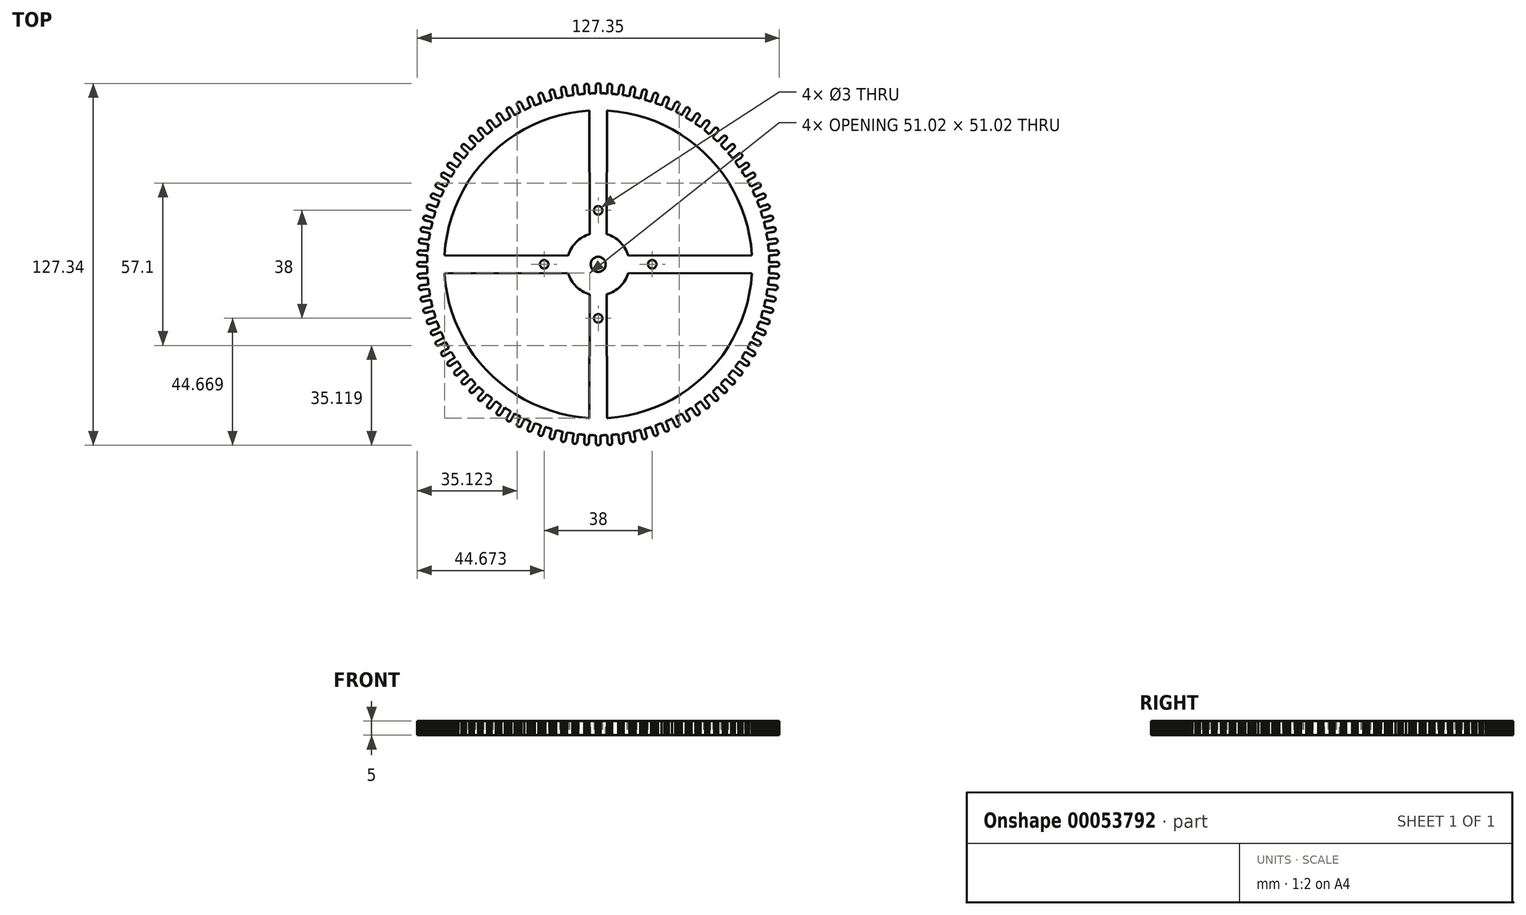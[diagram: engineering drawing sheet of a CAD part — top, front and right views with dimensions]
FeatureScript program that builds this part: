
annotation { "Feature Type Name" : "Feature", "Feature Type Description" : "" }
export const myFeature = defineFeature(function(context is Context, id is Id, definition is map)
    precondition{}
    {
        {
            var Q0;
            Q0=qCreatedBy(makeId("Top.planeOp"),FACE);
            var sketch = newSketch(context, id + "F0", { "sketchPlane" : qUnion([Q0])});
            skLineSegment(sketch, "E0", {"start": v(59.2, -0.78) * mm, "end": v(59.38, -0.79) * mm});
            skLineSegment(sketch, "E1", {"start": v(59.38, -0.79) * mm, "end": v(59.58, -0.79) * mm});
            skLineSegment(sketch, "E2", {"start": v(59.58, -0.79) * mm, "end": v(59.79, -0.8) * mm});
            skLineSegment(sketch, "E3", {"start": v(59.79, -0.8) * mm, "end": v(60, -0.8) * mm});
            skLineSegment(sketch, "E4", {"start": v(60, -0.8) * mm, "end": v(60.2, -0.8) * mm});
            skLineSegment(sketch, "E5", {"start": v(60.2, -0.8) * mm, "end": v(60.41, -0.8) * mm});
            skLineSegment(sketch, "E6", {"start": v(60.41, -0.8) * mm, "end": v(60.62, -0.8) * mm});
            skLineSegment(sketch, "E7", {"start": v(60.62, -0.8) * mm, "end": v(60.83, -0.8) * mm});
            skLineSegment(sketch, "E8", {"start": v(60.83, -0.8) * mm, "end": v(61.04, -0.8) * mm});
            skLineSegment(sketch, "E9", {"start": v(61.04, -0.8) * mm, "end": v(61.25, -0.81) * mm});
            skLineSegment(sketch, "E10", {"start": v(61.25, -0.81) * mm, "end": v(61.45, -0.81) * mm});
            skLineSegment(sketch, "E11", {"start": v(61.45, -0.81) * mm, "end": v(61.66, -0.82) * mm});
            skLineSegment(sketch, "E12", {"start": v(61.66, -0.82) * mm, "end": v(61.87, -0.82) * mm});
            skLineSegment(sketch, "E13", {"start": v(61.87, -0.82) * mm, "end": v(62.08, -0.8) * mm});
            skLineSegment(sketch, "E14", {"start": v(62.08, -0.8) * mm, "end": v(62.28, -0.71) * mm});
            skLineSegment(sketch, "E15", {"start": v(62.28, -0.71) * mm, "end": v(62.45, -0.58) * mm});
            skLineSegment(sketch, "E16", {"start": v(62.45, -0.58) * mm, "end": v(62.58, -0.41) * mm});
            skLineSegment(sketch, "E17", {"start": v(62.58, -0.41) * mm, "end": v(62.67, -0.21) * mm});
            skLineSegment(sketch, "E18", {"start": v(62.67, -0.21) * mm, "end": v(62.7, 0) * mm});
            skLineSegment(sketch, "E19", {"start": v(62.7, 0) * mm, "end": v(62.67, 0.21) * mm});
            skLineSegment(sketch, "E20", {"start": v(62.67, 0.21) * mm, "end": v(62.58, 0.41) * mm});
            skLineSegment(sketch, "E21", {"start": v(62.58, 0.41) * mm, "end": v(62.45, 0.58) * mm});
            skLineSegment(sketch, "E22", {"start": v(62.45, 0.58) * mm, "end": v(62.28, 0.71) * mm});
            skLineSegment(sketch, "E23", {"start": v(62.28, 0.71) * mm, "end": v(62.08, 0.8) * mm});
            skLineSegment(sketch, "E24", {"start": v(62.08, 0.8) * mm, "end": v(61.87, 0.82) * mm});
            skLineSegment(sketch, "E25", {"start": v(61.87, 0.82) * mm, "end": v(61.67, 0.82) * mm});
            skLineSegment(sketch, "E26", {"start": v(61.67, 0.82) * mm, "end": v(61.46, 0.81) * mm});
            skLineSegment(sketch, "E27", {"start": v(61.46, 0.81) * mm, "end": v(61.25, 0.81) * mm});
            skLineSegment(sketch, "E28", {"start": v(61.25, 0.81) * mm, "end": v(61.04, 0.8) * mm});
            skLineSegment(sketch, "E29", {"start": v(61.04, 0.8) * mm, "end": v(60.84, 0.8) * mm});
            skLineSegment(sketch, "E30", {"start": v(60.84, 0.8) * mm, "end": v(60.62, 0.8) * mm});
            skLineSegment(sketch, "E31", {"start": v(60.62, 0.8) * mm, "end": v(60.42, 0.8) * mm});
            skLineSegment(sketch, "E32", {"start": v(60.42, 0.8) * mm, "end": v(60.21, 0.8) * mm});
            skLineSegment(sketch, "E33", {"start": v(60.21, 0.8) * mm, "end": v(60, 0.8) * mm});
            skLineSegment(sketch, "E34", {"start": v(60, 0.8) * mm, "end": v(59.8, 0.8) * mm});
            skLineSegment(sketch, "E35", {"start": v(59.8, 0.8) * mm, "end": v(59.59, 0.79) * mm});
            skLineSegment(sketch, "E36", {"start": v(59.59, 0.79) * mm, "end": v(59.38, 0.79) * mm});
            skLineSegment(sketch, "E37", {"start": v(59.38, 0.79) * mm, "end": v(59.2, 0.78) * mm});
            skLineSegment(sketch, "E38", {"start": v(59.2, 0.78) * mm, "end": v(59.2, 0.99) * mm});
            skLineSegment(sketch, "E39", {"start": v(59.2, 0.99) * mm, "end": v(59.19, 1.2) * mm});
            skLineSegment(sketch, "E40", {"start": v(59.19, 1.2) * mm, "end": v(59.18, 1.4) * mm});
            skLineSegment(sketch, "E41", {"start": v(59.18, 1.4) * mm, "end": v(59.17, 1.6) * mm});
            skLineSegment(sketch, "E42", {"start": v(59.17, 1.6) * mm, "end": v(59.17, 1.81) * mm});
            skLineSegment(sketch, "E43", {"start": v(59.17, 1.81) * mm, "end": v(59.16, 2.02) * mm});
            skLineSegment(sketch, "E44", {"start": v(59.16, 2.02) * mm, "end": v(59.15, 2.22) * mm});
            skLineSegment(sketch, "E45", {"start": v(59.15, 2.22) * mm, "end": v(59.15, 2.43) * mm});
            skLineSegment(sketch, "E46", {"start": v(59.15, 2.43) * mm, "end": v(59.14, 2.64) * mm});
            skLineSegment(sketch, "E47", {"start": v(59.14, 2.64) * mm, "end": v(59.13, 2.84) * mm});
            skLineSegment(sketch, "E48", {"start": v(59.13, 2.84) * mm, "end": v(59.13, 3.05) * mm});
            skLineSegment(sketch, "E49", {"start": v(59.13, 3.05) * mm, "end": v(59.12, 3.15) * mm});
            skLineSegment(sketch, "E50", {"start": v(59.12, 3.15) * mm, "end": v(59.33, 3.16) * mm});
            skLineSegment(sketch, "E51", {"start": v(59.33, 3.16) * mm, "end": v(59.53, 3.17) * mm});
            skLineSegment(sketch, "E52", {"start": v(59.53, 3.17) * mm, "end": v(59.74, 3.19) * mm});
            skLineSegment(sketch, "E53", {"start": v(59.74, 3.19) * mm, "end": v(59.95, 3.2) * mm});
            skLineSegment(sketch, "E54", {"start": v(59.95, 3.2) * mm, "end": v(60.16, 3.2) * mm});
            skLineSegment(sketch, "E55", {"start": v(60.16, 3.2) * mm, "end": v(60.37, 3.22) * mm});
            skLineSegment(sketch, "E56", {"start": v(60.37, 3.22) * mm, "end": v(60.57, 3.23) * mm});
            skLineSegment(sketch, "E57", {"start": v(60.57, 3.23) * mm, "end": v(60.78, 3.24) * mm});
            skLineSegment(sketch, "E58", {"start": v(60.78, 3.24) * mm, "end": v(60.99, 3.25) * mm});
            skLineSegment(sketch, "E59", {"start": v(60.99, 3.25) * mm, "end": v(61.2, 3.26) * mm});
            skLineSegment(sketch, "E60", {"start": v(61.2, 3.26) * mm, "end": v(61.4, 3.27) * mm});
            skLineSegment(sketch, "E61", {"start": v(61.4, 3.27) * mm, "end": v(61.61, 3.28) * mm});
            skLineSegment(sketch, "E62", {"start": v(61.61, 3.28) * mm, "end": v(61.83, 3.3) * mm});
            skLineSegment(sketch, "E63", {"start": v(61.83, 3.3) * mm, "end": v(62.04, 3.35) * mm});
            skLineSegment(sketch, "E64", {"start": v(62.04, 3.35) * mm, "end": v(62.23, 3.45) * mm});
            skLineSegment(sketch, "E65", {"start": v(62.23, 3.45) * mm, "end": v(62.38, 3.6) * mm});
            skLineSegment(sketch, "E66", {"start": v(62.38, 3.6) * mm, "end": v(62.5, 3.79) * mm});
            skLineSegment(sketch, "E67", {"start": v(62.5, 3.79) * mm, "end": v(62.55, 4) * mm});
            skLineSegment(sketch, "E68", {"start": v(62.55, 4) * mm, "end": v(62.55, 4.2) * mm});
            skLineSegment(sketch, "E69", {"start": v(62.55, 4.2) * mm, "end": v(62.5, 4.41) * mm});
            skLineSegment(sketch, "E70", {"start": v(62.5, 4.41) * mm, "end": v(62.4, 4.6) * mm});
            skLineSegment(sketch, "E71", {"start": v(62.4, 4.6) * mm, "end": v(62.25, 4.76) * mm});
            skLineSegment(sketch, "E72", {"start": v(62.25, 4.76) * mm, "end": v(62.06, 4.86) * mm});
            skLineSegment(sketch, "E73", {"start": v(62.06, 4.86) * mm, "end": v(61.86, 4.92) * mm});
            skLineSegment(sketch, "E74", {"start": v(61.86, 4.92) * mm, "end": v(61.73, 4.93) * mm});
            skLineSegment(sketch, "E75", {"start": v(61.73, 4.93) * mm, "end": v(61.5, 4.91) * mm});
            skLineSegment(sketch, "E76", {"start": v(61.5, 4.91) * mm, "end": v(61.3, 4.9) * mm});
            skLineSegment(sketch, "E77", {"start": v(61.3, 4.9) * mm, "end": v(61.1, 4.88) * mm});
            skLineSegment(sketch, "E78", {"start": v(61.1, 4.88) * mm, "end": v(60.88, 4.86) * mm});
            skLineSegment(sketch, "E79", {"start": v(60.88, 4.86) * mm, "end": v(60.68, 4.85) * mm});
            skLineSegment(sketch, "E80", {"start": v(60.68, 4.85) * mm, "end": v(60.47, 4.83) * mm});
            skLineSegment(sketch, "E81", {"start": v(60.47, 4.83) * mm, "end": v(60.26, 4.82) * mm});
            skLineSegment(sketch, "E82", {"start": v(60.26, 4.82) * mm, "end": v(60.06, 4.8) * mm});
            skLineSegment(sketch, "E83", {"start": v(60.06, 4.8) * mm, "end": v(59.85, 4.78) * mm});
            skLineSegment(sketch, "E84", {"start": v(59.85, 4.78) * mm, "end": v(59.64, 4.77) * mm});
            skLineSegment(sketch, "E85", {"start": v(59.64, 4.77) * mm, "end": v(59.44, 4.75) * mm});
            skLineSegment(sketch, "E86", {"start": v(59.44, 4.75) * mm, "end": v(59.23, 4.73) * mm});
            skLineSegment(sketch, "E87", {"start": v(59.23, 4.73) * mm, "end": v(59.02, 4.72) * mm});
            skLineSegment(sketch, "E88", {"start": v(59.02, 4.72) * mm, "end": v(59, 4.92) * mm});
            skLineSegment(sketch, "E89", {"start": v(59, 4.92) * mm, "end": v(58.98, 5.13) * mm});
            skLineSegment(sketch, "E90", {"start": v(58.98, 5.13) * mm, "end": v(58.96, 5.33) * mm});
            skLineSegment(sketch, "E91", {"start": v(58.96, 5.33) * mm, "end": v(58.94, 5.54) * mm});
            skLineSegment(sketch, "E92", {"start": v(58.94, 5.54) * mm, "end": v(58.92, 5.74) * mm});
            skLineSegment(sketch, "E93", {"start": v(58.92, 5.74) * mm, "end": v(58.9, 5.95) * mm});
            skLineSegment(sketch, "E94", {"start": v(58.9, 5.95) * mm, "end": v(58.88, 6.15) * mm});
            skLineSegment(sketch, "E95", {"start": v(58.88, 6.15) * mm, "end": v(58.86, 6.36) * mm});
            skLineSegment(sketch, "E96", {"start": v(58.86, 6.36) * mm, "end": v(58.84, 6.56) * mm});
            skLineSegment(sketch, "E97", {"start": v(58.84, 6.56) * mm, "end": v(58.82, 6.77) * mm});
            skLineSegment(sketch, "E98", {"start": v(58.82, 6.77) * mm, "end": v(58.8, 6.97) * mm});
            skLineSegment(sketch, "E99", {"start": v(58.8, 6.97) * mm, "end": v(58.79, 7.08) * mm});
            skLineSegment(sketch, "E100", {"start": v(58.79, 7.08) * mm, "end": v(59, 7.1) * mm});
            skLineSegment(sketch, "E101", {"start": v(59, 7.1) * mm, "end": v(59.2, 7.13) * mm});
            skLineSegment(sketch, "E102", {"start": v(59.2, 7.13) * mm, "end": v(59.4, 7.15) * mm});
            skLineSegment(sketch, "E103", {"start": v(59.4, 7.15) * mm, "end": v(59.61, 7.17) * mm});
            skLineSegment(sketch, "E104", {"start": v(59.61, 7.17) * mm, "end": v(59.82, 7.2) * mm});
            skLineSegment(sketch, "E105", {"start": v(59.82, 7.2) * mm, "end": v(60.03, 7.22) * mm});
            skLineSegment(sketch, "E106", {"start": v(60.03, 7.22) * mm, "end": v(60.23, 7.25) * mm});
            skLineSegment(sketch, "E107", {"start": v(60.23, 7.25) * mm, "end": v(60.43, 7.27) * mm});
            skLineSegment(sketch, "E108", {"start": v(60.43, 7.27) * mm, "end": v(60.64, 7.3) * mm});
            skLineSegment(sketch, "E109", {"start": v(60.64, 7.3) * mm, "end": v(60.85, 7.32) * mm});
            skLineSegment(sketch, "E110", {"start": v(60.85, 7.32) * mm, "end": v(61.05, 7.35) * mm});
            skLineSegment(sketch, "E111", {"start": v(61.05, 7.35) * mm, "end": v(61.26, 7.37) * mm});
            skLineSegment(sketch, "E112", {"start": v(61.26, 7.37) * mm, "end": v(61.48, 7.4) * mm});
            skLineSegment(sketch, "E113", {"start": v(61.48, 7.4) * mm, "end": v(61.69, 7.46) * mm});
            skLineSegment(sketch, "E114", {"start": v(61.69, 7.46) * mm, "end": v(61.87, 7.58) * mm});
            skLineSegment(sketch, "E115", {"start": v(61.87, 7.58) * mm, "end": v(62.01, 7.74) * mm});
            skLineSegment(sketch, "E116", {"start": v(62.01, 7.74) * mm, "end": v(62.11, 7.93) * mm});
            skLineSegment(sketch, "E117", {"start": v(62.11, 7.93) * mm, "end": v(62.15, 8.14) * mm});
            skLineSegment(sketch, "E118", {"start": v(62.15, 8.14) * mm, "end": v(62.14, 8.35) * mm});
            skLineSegment(sketch, "E119", {"start": v(62.14, 8.35) * mm, "end": v(62.08, 8.56) * mm});
            skLineSegment(sketch, "E120", {"start": v(62.08, 8.56) * mm, "end": v(61.96, 8.74) * mm});
            skLineSegment(sketch, "E121", {"start": v(61.96, 8.74) * mm, "end": v(61.8, 8.88) * mm});
            skLineSegment(sketch, "E122", {"start": v(61.8, 8.88) * mm, "end": v(61.6, 8.98) * mm});
            skLineSegment(sketch, "E123", {"start": v(61.6, 8.98) * mm, "end": v(61.4, 9.02) * mm});
            skLineSegment(sketch, "E124", {"start": v(61.4, 9.02) * mm, "end": v(61.36, 9.02) * mm});
            skLineSegment(sketch, "E125", {"start": v(61.36, 9.02) * mm, "end": v(61.14, 9) * mm});
            skLineSegment(sketch, "E126", {"start": v(61.14, 9) * mm, "end": v(60.93, 8.97) * mm});
            skLineSegment(sketch, "E127", {"start": v(60.93, 8.97) * mm, "end": v(60.73, 8.94) * mm});
            skLineSegment(sketch, "E128", {"start": v(60.73, 8.94) * mm, "end": v(60.52, 8.91) * mm});
            skLineSegment(sketch, "E129", {"start": v(60.52, 8.91) * mm, "end": v(60.32, 8.88) * mm});
            skLineSegment(sketch, "E130", {"start": v(60.32, 8.88) * mm, "end": v(60.11, 8.85) * mm});
            skLineSegment(sketch, "E131", {"start": v(60.11, 8.85) * mm, "end": v(59.9, 8.82) * mm});
            skLineSegment(sketch, "E132", {"start": v(59.9, 8.82) * mm, "end": v(59.7, 8.8) * mm});
            skLineSegment(sketch, "E133", {"start": v(59.7, 8.8) * mm, "end": v(59.5, 8.76) * mm});
            skLineSegment(sketch, "E134", {"start": v(59.5, 8.76) * mm, "end": v(59.29, 8.73) * mm});
            skLineSegment(sketch, "E135", {"start": v(59.29, 8.73) * mm, "end": v(59.08, 8.7) * mm});
            skLineSegment(sketch, "E136", {"start": v(59.08, 8.7) * mm, "end": v(58.88, 8.67) * mm});
            skLineSegment(sketch, "E137", {"start": v(58.88, 8.67) * mm, "end": v(58.67, 8.64) * mm});
            skLineSegment(sketch, "E138", {"start": v(58.67, 8.64) * mm, "end": v(58.58, 8.63) * mm});
            skLineSegment(sketch, "E139", {"start": v(58.58, 8.63) * mm, "end": v(58.55, 8.83) * mm});
            skLineSegment(sketch, "E140", {"start": v(58.55, 8.83) * mm, "end": v(58.52, 9.04) * mm});
            skLineSegment(sketch, "E141", {"start": v(58.52, 9.04) * mm, "end": v(58.48, 9.24) * mm});
            skLineSegment(sketch, "E142", {"start": v(58.48, 9.24) * mm, "end": v(58.45, 9.44) * mm});
            skLineSegment(sketch, "E143", {"start": v(58.45, 9.44) * mm, "end": v(58.41, 9.65) * mm});
            skLineSegment(sketch, "E144", {"start": v(58.41, 9.65) * mm, "end": v(58.38, 9.85) * mm});
            skLineSegment(sketch, "E145", {"start": v(58.38, 9.85) * mm, "end": v(58.35, 10.05) * mm});
            skLineSegment(sketch, "E146", {"start": v(58.35, 10.05) * mm, "end": v(58.31, 10.26) * mm});
            skLineSegment(sketch, "E147", {"start": v(58.31, 10.26) * mm, "end": v(58.28, 10.46) * mm});
            skLineSegment(sketch, "E148", {"start": v(58.28, 10.46) * mm, "end": v(58.25, 10.66) * mm});
            skLineSegment(sketch, "E149", {"start": v(58.25, 10.66) * mm, "end": v(58.21, 10.87) * mm});
            skLineSegment(sketch, "E150", {"start": v(58.21, 10.87) * mm, "end": v(58.2, 10.97) * mm});
            skLineSegment(sketch, "E151", {"start": v(58.2, 10.97) * mm, "end": v(58.4, 11) * mm});
            skLineSegment(sketch, "E152", {"start": v(58.4, 11) * mm, "end": v(58.6, 11.05) * mm});
            skLineSegment(sketch, "E153", {"start": v(58.6, 11.05) * mm, "end": v(58.8, 11.08) * mm});
            skLineSegment(sketch, "E154", {"start": v(58.8, 11.08) * mm, "end": v(59.01, 11.12) * mm});
            skLineSegment(sketch, "E155", {"start": v(59.01, 11.12) * mm, "end": v(59.21, 11.16) * mm});
            skLineSegment(sketch, "E156", {"start": v(59.21, 11.16) * mm, "end": v(59.42, 11.2) * mm});
            skLineSegment(sketch, "E157", {"start": v(59.42, 11.2) * mm, "end": v(59.62, 11.24) * mm});
            skLineSegment(sketch, "E158", {"start": v(59.62, 11.24) * mm, "end": v(59.83, 11.27) * mm});
            skLineSegment(sketch, "E159", {"start": v(59.83, 11.27) * mm, "end": v(60.04, 11.31) * mm});
            skLineSegment(sketch, "E160", {"start": v(60.04, 11.31) * mm, "end": v(60.24, 11.35) * mm});
            skLineSegment(sketch, "E161", {"start": v(60.24, 11.35) * mm, "end": v(60.44, 11.39) * mm});
            skLineSegment(sketch, "E162", {"start": v(60.44, 11.39) * mm, "end": v(60.65, 11.43) * mm});
            skLineSegment(sketch, "E163", {"start": v(60.65, 11.43) * mm, "end": v(60.87, 11.47) * mm});
            skLineSegment(sketch, "E164", {"start": v(60.87, 11.47) * mm, "end": v(61.07, 11.55) * mm});
            skLineSegment(sketch, "E165", {"start": v(61.07, 11.55) * mm, "end": v(61.24, 11.67) * mm});
            skLineSegment(sketch, "E166", {"start": v(61.24, 11.67) * mm, "end": v(61.37, 11.84) * mm});
            skLineSegment(sketch, "E167", {"start": v(61.37, 11.84) * mm, "end": v(61.46, 12.04) * mm});
            skLineSegment(sketch, "E168", {"start": v(61.46, 12.04) * mm, "end": v(61.49, 12.25) * mm});
            skLineSegment(sketch, "E169", {"start": v(61.49, 12.25) * mm, "end": v(61.46, 12.46) * mm});
            skLineSegment(sketch, "E170", {"start": v(61.46, 12.46) * mm, "end": v(61.38, 12.66) * mm});
            skLineSegment(sketch, "E171", {"start": v(61.38, 12.66) * mm, "end": v(61.25, 12.83) * mm});
            skLineSegment(sketch, "E172", {"start": v(61.25, 12.83) * mm, "end": v(61.09, 12.97) * mm});
            skLineSegment(sketch, "E173", {"start": v(61.09, 12.97) * mm, "end": v(60.89, 13.05) * mm});
            skLineSegment(sketch, "E174", {"start": v(60.89, 13.05) * mm, "end": v(60.68, 13.08) * mm});
            skLineSegment(sketch, "E175", {"start": v(60.68, 13.08) * mm, "end": v(60.47, 13.05) * mm});
            skLineSegment(sketch, "E176", {"start": v(60.47, 13.05) * mm, "end": v(60.27, 13.01) * mm});
            skLineSegment(sketch, "E177", {"start": v(60.27, 13.01) * mm, "end": v(60.07, 12.97) * mm});
            skLineSegment(sketch, "E178", {"start": v(60.07, 12.97) * mm, "end": v(59.87, 12.93) * mm});
            skLineSegment(sketch, "E179", {"start": v(59.87, 12.93) * mm, "end": v(59.67, 12.89) * mm});
            skLineSegment(sketch, "E180", {"start": v(59.67, 12.89) * mm, "end": v(59.46, 12.84) * mm});
            skLineSegment(sketch, "E181", {"start": v(59.46, 12.84) * mm, "end": v(59.26, 12.8) * mm});
            skLineSegment(sketch, "E182", {"start": v(59.26, 12.8) * mm, "end": v(59.06, 12.76) * mm});
            skLineSegment(sketch, "E183", {"start": v(59.06, 12.76) * mm, "end": v(58.85, 12.71) * mm});
            skLineSegment(sketch, "E184", {"start": v(58.85, 12.71) * mm, "end": v(58.65, 12.67) * mm});
            skLineSegment(sketch, "E185", {"start": v(58.65, 12.67) * mm, "end": v(58.45, 12.63) * mm});
            skLineSegment(sketch, "E186", {"start": v(58.45, 12.63) * mm, "end": v(58.24, 12.58) * mm});
            skLineSegment(sketch, "E187", {"start": v(58.24, 12.58) * mm, "end": v(58.04, 12.54) * mm});
            skLineSegment(sketch, "E188", {"start": v(58.04, 12.54) * mm, "end": v(57.9, 12.5) * mm});
            skLineSegment(sketch, "E189", {"start": v(57.9, 12.5) * mm, "end": v(57.84, 12.7) * mm});
            skLineSegment(sketch, "E190", {"start": v(57.84, 12.7) * mm, "end": v(57.8, 12.9) * mm});
            skLineSegment(sketch, "E191", {"start": v(57.8, 12.9) * mm, "end": v(57.75, 13.1) * mm});
            skLineSegment(sketch, "E192", {"start": v(57.75, 13.1) * mm, "end": v(57.7, 13.31) * mm});
            skLineSegment(sketch, "E193", {"start": v(57.7, 13.31) * mm, "end": v(57.66, 13.51) * mm});
            skLineSegment(sketch, "E194", {"start": v(57.66, 13.51) * mm, "end": v(57.6, 13.71) * mm});
            skLineSegment(sketch, "E195", {"start": v(57.6, 13.71) * mm, "end": v(57.56, 13.91) * mm});
            skLineSegment(sketch, "E196", {"start": v(57.56, 13.91) * mm, "end": v(57.52, 14.11) * mm});
            skLineSegment(sketch, "E197", {"start": v(57.52, 14.11) * mm, "end": v(57.47, 14.31) * mm});
            skLineSegment(sketch, "E198", {"start": v(57.47, 14.31) * mm, "end": v(57.42, 14.51) * mm});
            skLineSegment(sketch, "E199", {"start": v(57.42, 14.51) * mm, "end": v(57.38, 14.71) * mm});
            skLineSegment(sketch, "E200", {"start": v(57.38, 14.71) * mm, "end": v(57.35, 14.82) * mm});
            skLineSegment(sketch, "E201", {"start": v(57.35, 14.82) * mm, "end": v(57.55, 14.87) * mm});
            skLineSegment(sketch, "E202", {"start": v(57.55, 14.87) * mm, "end": v(57.75, 14.92) * mm});
            skLineSegment(sketch, "E203", {"start": v(57.75, 14.92) * mm, "end": v(57.96, 14.97) * mm});
            skLineSegment(sketch, "E204", {"start": v(57.96, 14.97) * mm, "end": v(58.16, 15.02) * mm});
            skLineSegment(sketch, "E205", {"start": v(58.16, 15.02) * mm, "end": v(58.36, 15.07) * mm});
            skLineSegment(sketch, "E206", {"start": v(58.36, 15.07) * mm, "end": v(58.56, 15.12) * mm});
            skLineSegment(sketch, "E207", {"start": v(58.56, 15.12) * mm, "end": v(58.76, 15.17) * mm});
            skLineSegment(sketch, "E208", {"start": v(58.76, 15.17) * mm, "end": v(58.96, 15.23) * mm});
            skLineSegment(sketch, "E209", {"start": v(58.96, 15.23) * mm, "end": v(59.16, 15.28) * mm});
            skLineSegment(sketch, "E210", {"start": v(59.16, 15.28) * mm, "end": v(59.36, 15.33) * mm});
            skLineSegment(sketch, "E211", {"start": v(59.36, 15.33) * mm, "end": v(59.56, 15.38) * mm});
            skLineSegment(sketch, "E212", {"start": v(59.56, 15.38) * mm, "end": v(59.77, 15.43) * mm});
            skLineSegment(sketch, "E213", {"start": v(59.77, 15.43) * mm, "end": v(59.98, 15.49) * mm});
            skLineSegment(sketch, "E214", {"start": v(59.98, 15.49) * mm, "end": v(60.18, 15.58) * mm});
            skLineSegment(sketch, "E215", {"start": v(60.18, 15.58) * mm, "end": v(60.34, 15.72) * mm});
            skLineSegment(sketch, "E216", {"start": v(60.34, 15.72) * mm, "end": v(60.46, 15.9) * mm});
            skLineSegment(sketch, "E217", {"start": v(60.46, 15.9) * mm, "end": v(60.54, 16.1) * mm});
            skLineSegment(sketch, "E218", {"start": v(60.54, 16.1) * mm, "end": v(60.55, 16.3) * mm});
            skLineSegment(sketch, "E219", {"start": v(60.55, 16.3) * mm, "end": v(60.51, 16.52) * mm});
            skLineSegment(sketch, "E220", {"start": v(60.51, 16.52) * mm, "end": v(60.42, 16.71) * mm});
            skLineSegment(sketch, "E221", {"start": v(60.42, 16.71) * mm, "end": v(60.28, 16.88) * mm});
            skLineSegment(sketch, "E222", {"start": v(60.28, 16.88) * mm, "end": v(60.1, 17) * mm});
            skLineSegment(sketch, "E223", {"start": v(60.1, 17) * mm, "end": v(59.9, 17.07) * mm});
            skLineSegment(sketch, "E224", {"start": v(59.9, 17.07) * mm, "end": v(59.73, 17.09) * mm});
            skLineSegment(sketch, "E225", {"start": v(59.73, 17.09) * mm, "end": v(59.52, 17.06) * mm});
            skLineSegment(sketch, "E226", {"start": v(59.52, 17.06) * mm, "end": v(59.32, 17) * mm});
            skLineSegment(sketch, "E227", {"start": v(59.32, 17) * mm, "end": v(59.12, 16.94) * mm});
            skLineSegment(sketch, "E228", {"start": v(59.12, 16.94) * mm, "end": v(58.92, 16.89) * mm});
            skLineSegment(sketch, "E229", {"start": v(58.92, 16.89) * mm, "end": v(58.72, 16.83) * mm});
            skLineSegment(sketch, "E230", {"start": v(58.72, 16.83) * mm, "end": v(58.52, 16.78) * mm});
            skLineSegment(sketch, "E231", {"start": v(58.52, 16.78) * mm, "end": v(58.32, 16.72) * mm});
            skLineSegment(sketch, "E232", {"start": v(58.32, 16.72) * mm, "end": v(58.12, 16.66) * mm});
            skLineSegment(sketch, "E233", {"start": v(58.12, 16.66) * mm, "end": v(57.92, 16.6) * mm});
            skLineSegment(sketch, "E234", {"start": v(57.92, 16.6) * mm, "end": v(57.72, 16.55) * mm});
            skLineSegment(sketch, "E235", {"start": v(57.72, 16.55) * mm, "end": v(57.52, 16.5) * mm});
            skLineSegment(sketch, "E236", {"start": v(57.52, 16.5) * mm, "end": v(57.32, 16.44) * mm});
            skLineSegment(sketch, "E237", {"start": v(57.32, 16.44) * mm, "end": v(57.12, 16.38) * mm});
            skLineSegment(sketch, "E238", {"start": v(57.12, 16.38) * mm, "end": v(56.95, 16.33) * mm});
            skLineSegment(sketch, "E239", {"start": v(56.95, 16.33) * mm, "end": v(56.89, 16.53) * mm});
            skLineSegment(sketch, "E240", {"start": v(56.89, 16.53) * mm, "end": v(56.83, 16.73) * mm});
            skLineSegment(sketch, "E241", {"start": v(56.83, 16.73) * mm, "end": v(56.77, 16.92) * mm});
            skLineSegment(sketch, "E242", {"start": v(56.77, 16.92) * mm, "end": v(56.7, 17.12) * mm});
            skLineSegment(sketch, "E243", {"start": v(56.7, 17.12) * mm, "end": v(56.65, 17.32) * mm});
            skLineSegment(sketch, "E244", {"start": v(56.65, 17.32) * mm, "end": v(56.59, 17.51) * mm});
            skLineSegment(sketch, "E245", {"start": v(56.59, 17.51) * mm, "end": v(56.53, 17.71) * mm});
            skLineSegment(sketch, "E246", {"start": v(56.53, 17.71) * mm, "end": v(56.47, 17.9) * mm});
            skLineSegment(sketch, "E247", {"start": v(56.47, 17.9) * mm, "end": v(56.4, 18.1) * mm});
            skLineSegment(sketch, "E248", {"start": v(56.4, 18.1) * mm, "end": v(56.35, 18.3) * mm});
            skLineSegment(sketch, "E249", {"start": v(56.35, 18.3) * mm, "end": v(56.29, 18.5) * mm});
            skLineSegment(sketch, "E250", {"start": v(56.29, 18.5) * mm, "end": v(56.26, 18.6) * mm});
            skLineSegment(sketch, "E251", {"start": v(56.26, 18.6) * mm, "end": v(56.45, 18.66) * mm});
            skLineSegment(sketch, "E252", {"start": v(56.45, 18.66) * mm, "end": v(56.65, 18.73) * mm});
            skLineSegment(sketch, "E253", {"start": v(56.65, 18.73) * mm, "end": v(56.85, 18.8) * mm});
            skLineSegment(sketch, "E254", {"start": v(56.85, 18.8) * mm, "end": v(57.05, 18.86) * mm});
            skLineSegment(sketch, "E255", {"start": v(57.05, 18.86) * mm, "end": v(57.24, 18.92) * mm});
            skLineSegment(sketch, "E256", {"start": v(57.24, 18.92) * mm, "end": v(57.44, 18.99) * mm});
            skLineSegment(sketch, "E257", {"start": v(57.44, 18.99) * mm, "end": v(57.64, 19.05) * mm});
            skLineSegment(sketch, "E258", {"start": v(57.64, 19.05) * mm, "end": v(57.84, 19.11) * mm});
            skLineSegment(sketch, "E259", {"start": v(57.84, 19.11) * mm, "end": v(58.04, 19.18) * mm});
            skLineSegment(sketch, "E260", {"start": v(58.04, 19.18) * mm, "end": v(58.23, 19.24) * mm});
            skLineSegment(sketch, "E261", {"start": v(58.23, 19.24) * mm, "end": v(58.43, 19.3) * mm});
            skLineSegment(sketch, "E262", {"start": v(58.43, 19.3) * mm, "end": v(58.63, 19.37) * mm});
            skLineSegment(sketch, "E263", {"start": v(58.63, 19.37) * mm, "end": v(58.84, 19.44) * mm});
            skLineSegment(sketch, "E264", {"start": v(58.84, 19.44) * mm, "end": v(59.03, 19.54) * mm});
            skLineSegment(sketch, "E265", {"start": v(59.03, 19.54) * mm, "end": v(59.18, 19.7) * mm});
            skLineSegment(sketch, "E266", {"start": v(59.18, 19.7) * mm, "end": v(59.3, 19.88) * mm});
            skLineSegment(sketch, "E267", {"start": v(59.3, 19.88) * mm, "end": v(59.35, 20.08) * mm});
            skLineSegment(sketch, "E268", {"start": v(59.35, 20.08) * mm, "end": v(59.35, 20.3) * mm});
            skLineSegment(sketch, "E269", {"start": v(59.35, 20.3) * mm, "end": v(59.3, 20.5) * mm});
            skLineSegment(sketch, "E270", {"start": v(59.3, 20.5) * mm, "end": v(59.2, 20.7) * mm});
            skLineSegment(sketch, "E271", {"start": v(59.2, 20.7) * mm, "end": v(59.05, 20.85) * mm});
            skLineSegment(sketch, "E272", {"start": v(59.05, 20.85) * mm, "end": v(58.86, 20.96) * mm});
            skLineSegment(sketch, "E273", {"start": v(58.86, 20.96) * mm, "end": v(58.65, 21.01) * mm});
            skLineSegment(sketch, "E274", {"start": v(58.65, 21.01) * mm, "end": v(58.53, 21.02) * mm});
            skLineSegment(sketch, "E275", {"start": v(58.53, 21.02) * mm, "end": v(58.31, 20.99) * mm});
            skLineSegment(sketch, "E276", {"start": v(58.31, 20.99) * mm, "end": v(58.1, 20.92) * mm});
            skLineSegment(sketch, "E277", {"start": v(58.1, 20.92) * mm, "end": v(57.91, 20.85) * mm});
            skLineSegment(sketch, "E278", {"start": v(57.91, 20.85) * mm, "end": v(57.72, 20.78) * mm});
            skLineSegment(sketch, "E279", {"start": v(57.72, 20.78) * mm, "end": v(57.52, 20.7) * mm});
            skLineSegment(sketch, "E280", {"start": v(57.52, 20.7) * mm, "end": v(57.32, 20.64) * mm});
            skLineSegment(sketch, "E281", {"start": v(57.32, 20.64) * mm, "end": v(57.13, 20.57) * mm});
            skLineSegment(sketch, "E282", {"start": v(57.13, 20.57) * mm, "end": v(56.93, 20.5) * mm});
            skLineSegment(sketch, "E283", {"start": v(56.93, 20.5) * mm, "end": v(56.74, 20.43) * mm});
            skLineSegment(sketch, "E284", {"start": v(56.74, 20.43) * mm, "end": v(56.54, 20.36) * mm});
            skLineSegment(sketch, "E285", {"start": v(56.54, 20.36) * mm, "end": v(56.34, 20.3) * mm});
            skLineSegment(sketch, "E286", {"start": v(56.34, 20.3) * mm, "end": v(56.15, 20.22) * mm});
            skLineSegment(sketch, "E287", {"start": v(56.15, 20.22) * mm, "end": v(55.95, 20.16) * mm});
            skLineSegment(sketch, "E288", {"start": v(55.95, 20.16) * mm, "end": v(55.75, 20.08) * mm});
            skLineSegment(sketch, "E289", {"start": v(55.75, 20.08) * mm, "end": v(55.68, 20.28) * mm});
            skLineSegment(sketch, "E290", {"start": v(55.68, 20.28) * mm, "end": v(55.6, 20.47) * mm});
            skLineSegment(sketch, "E291", {"start": v(55.6, 20.47) * mm, "end": v(55.54, 20.66) * mm});
            skLineSegment(sketch, "E292", {"start": v(55.54, 20.66) * mm, "end": v(55.46, 20.86) * mm});
            skLineSegment(sketch, "E293", {"start": v(55.46, 20.86) * mm, "end": v(55.4, 21.05) * mm});
            skLineSegment(sketch, "E294", {"start": v(55.4, 21.05) * mm, "end": v(55.32, 21.24) * mm});
            skLineSegment(sketch, "E295", {"start": v(55.32, 21.24) * mm, "end": v(55.25, 21.43) * mm});
            skLineSegment(sketch, "E296", {"start": v(55.25, 21.43) * mm, "end": v(55.17, 21.63) * mm});
            skLineSegment(sketch, "E297", {"start": v(55.17, 21.63) * mm, "end": v(55.1, 21.82) * mm});
            skLineSegment(sketch, "E298", {"start": v(55.1, 21.82) * mm, "end": v(55.03, 22.01) * mm});
            skLineSegment(sketch, "E299", {"start": v(55.03, 22.01) * mm, "end": v(54.96, 22.2) * mm});
            skLineSegment(sketch, "E300", {"start": v(54.96, 22.2) * mm, "end": v(54.92, 22.3) * mm});
            skLineSegment(sketch, "E301", {"start": v(54.92, 22.3) * mm, "end": v(55.11, 22.38) * mm});
            skLineSegment(sketch, "E302", {"start": v(55.11, 22.38) * mm, "end": v(55.3, 22.46) * mm});
            skLineSegment(sketch, "E303", {"start": v(55.3, 22.46) * mm, "end": v(55.5, 22.53) * mm});
            skLineSegment(sketch, "E304", {"start": v(55.5, 22.53) * mm, "end": v(55.69, 22.61) * mm});
            skLineSegment(sketch, "E305", {"start": v(55.69, 22.61) * mm, "end": v(55.88, 22.69) * mm});
            skLineSegment(sketch, "E306", {"start": v(55.88, 22.69) * mm, "end": v(56.08, 22.77) * mm});
            skLineSegment(sketch, "E307", {"start": v(56.08, 22.77) * mm, "end": v(56.27, 22.84) * mm});
            skLineSegment(sketch, "E308", {"start": v(56.27, 22.84) * mm, "end": v(56.46, 22.92) * mm});
            skLineSegment(sketch, "E309", {"start": v(56.46, 22.92) * mm, "end": v(56.66, 23) * mm});
            skLineSegment(sketch, "E310", {"start": v(56.66, 23) * mm, "end": v(56.85, 23.07) * mm});
            skLineSegment(sketch, "E311", {"start": v(56.85, 23.07) * mm, "end": v(57.04, 23.15) * mm});
            skLineSegment(sketch, "E312", {"start": v(57.04, 23.15) * mm, "end": v(57.24, 23.23) * mm});
            skLineSegment(sketch, "E313", {"start": v(57.24, 23.23) * mm, "end": v(57.44, 23.31) * mm});
            skLineSegment(sketch, "E314", {"start": v(57.44, 23.31) * mm, "end": v(57.62, 23.43) * mm});
            skLineSegment(sketch, "E315", {"start": v(57.62, 23.43) * mm, "end": v(57.77, 23.59) * mm});
            skLineSegment(sketch, "E316", {"start": v(57.77, 23.59) * mm, "end": v(57.86, 23.78) * mm});
            skLineSegment(sketch, "E317", {"start": v(57.86, 23.78) * mm, "end": v(57.9, 23.99) * mm});
            skLineSegment(sketch, "E318", {"start": v(57.9, 23.99) * mm, "end": v(57.9, 24.2) * mm});
            skLineSegment(sketch, "E319", {"start": v(57.9, 24.2) * mm, "end": v(57.83, 24.4) * mm});
            skLineSegment(sketch, "E320", {"start": v(57.83, 24.4) * mm, "end": v(57.71, 24.59) * mm});
            skLineSegment(sketch, "E321", {"start": v(57.71, 24.59) * mm, "end": v(57.55, 24.73) * mm});
            skLineSegment(sketch, "E322", {"start": v(57.55, 24.73) * mm, "end": v(57.36, 24.83) * mm});
            skLineSegment(sketch, "E323", {"start": v(57.36, 24.83) * mm, "end": v(57.15, 24.87) * mm});
            skLineSegment(sketch, "E324", {"start": v(57.15, 24.87) * mm, "end": v(57.1, 24.87) * mm});
            skLineSegment(sketch, "E325", {"start": v(57.1, 24.87) * mm, "end": v(56.9, 24.85) * mm});
            skLineSegment(sketch, "E326", {"start": v(56.9, 24.85) * mm, "end": v(56.7, 24.77) * mm});
            skLineSegment(sketch, "E327", {"start": v(56.7, 24.77) * mm, "end": v(56.5, 24.7) * mm});
            skLineSegment(sketch, "E328", {"start": v(56.5, 24.7) * mm, "end": v(56.31, 24.6) * mm});
            skLineSegment(sketch, "E329", {"start": v(56.31, 24.6) * mm, "end": v(56.12, 24.53) * mm});
            skLineSegment(sketch, "E330", {"start": v(56.12, 24.53) * mm, "end": v(55.93, 24.44) * mm});
            skLineSegment(sketch, "E331", {"start": v(55.93, 24.44) * mm, "end": v(55.74, 24.36) * mm});
            skLineSegment(sketch, "E332", {"start": v(55.74, 24.36) * mm, "end": v(55.55, 24.28) * mm});
            skLineSegment(sketch, "E333", {"start": v(55.55, 24.28) * mm, "end": v(55.36, 24.2) * mm});
            skLineSegment(sketch, "E334", {"start": v(55.36, 24.2) * mm, "end": v(55.17, 24.12) * mm});
            skLineSegment(sketch, "E335", {"start": v(55.17, 24.12) * mm, "end": v(54.97, 24.03) * mm});
            skLineSegment(sketch, "E336", {"start": v(54.97, 24.03) * mm, "end": v(54.78, 23.95) * mm});
            skLineSegment(sketch, "E337", {"start": v(54.78, 23.95) * mm, "end": v(54.6, 23.87) * mm});
            skLineSegment(sketch, "E338", {"start": v(54.6, 23.87) * mm, "end": v(54.4, 23.79) * mm});
            skLineSegment(sketch, "E339", {"start": v(54.4, 23.79) * mm, "end": v(54.32, 23.75) * mm});
            skLineSegment(sketch, "E340", {"start": v(54.32, 23.75) * mm, "end": v(54.23, 23.94) * mm});
            skLineSegment(sketch, "E341", {"start": v(54.23, 23.94) * mm, "end": v(54.15, 24.13) * mm});
            skLineSegment(sketch, "E342", {"start": v(54.15, 24.13) * mm, "end": v(54.06, 24.32) * mm});
            skLineSegment(sketch, "E343", {"start": v(54.06, 24.32) * mm, "end": v(53.98, 24.5) * mm});
            skLineSegment(sketch, "E344", {"start": v(53.98, 24.5) * mm, "end": v(53.9, 24.7) * mm});
            skLineSegment(sketch, "E345", {"start": v(53.9, 24.7) * mm, "end": v(53.8, 24.88) * mm});
            skLineSegment(sketch, "E346", {"start": v(53.8, 24.88) * mm, "end": v(53.72, 25.07) * mm});
            skLineSegment(sketch, "E347", {"start": v(53.72, 25.07) * mm, "end": v(53.64, 25.25) * mm});
            skLineSegment(sketch, "E348", {"start": v(53.64, 25.25) * mm, "end": v(53.55, 25.44) * mm});
            skLineSegment(sketch, "E349", {"start": v(53.55, 25.44) * mm, "end": v(53.47, 25.63) * mm});
            skLineSegment(sketch, "E350", {"start": v(53.47, 25.63) * mm, "end": v(53.38, 25.82) * mm});
            skLineSegment(sketch, "E351", {"start": v(53.38, 25.82) * mm, "end": v(53.34, 25.91) * mm});
            skLineSegment(sketch, "E352", {"start": v(53.34, 25.91) * mm, "end": v(53.53, 26) * mm});
            skLineSegment(sketch, "E353", {"start": v(53.53, 26) * mm, "end": v(53.71, 26.09) * mm});
            skLineSegment(sketch, "E354", {"start": v(53.71, 26.09) * mm, "end": v(53.9, 26.18) * mm});
            skLineSegment(sketch, "E355", {"start": v(53.9, 26.18) * mm, "end": v(54.09, 26.27) * mm});
            skLineSegment(sketch, "E356", {"start": v(54.09, 26.27) * mm, "end": v(54.27, 26.36) * mm});
            skLineSegment(sketch, "E357", {"start": v(54.27, 26.36) * mm, "end": v(54.47, 26.45) * mm});
            skLineSegment(sketch, "E358", {"start": v(54.47, 26.45) * mm, "end": v(54.65, 26.54) * mm});
            skLineSegment(sketch, "E359", {"start": v(54.65, 26.54) * mm, "end": v(54.84, 26.63) * mm});
            skLineSegment(sketch, "E360", {"start": v(54.84, 26.63) * mm, "end": v(55.03, 26.72) * mm});
            skLineSegment(sketch, "E361", {"start": v(55.03, 26.72) * mm, "end": v(55.21, 26.8) * mm});
            skLineSegment(sketch, "E362", {"start": v(55.21, 26.8) * mm, "end": v(55.4, 26.9) * mm});
            skLineSegment(sketch, "E363", {"start": v(55.4, 26.9) * mm, "end": v(55.6, 26.99) * mm});
            skLineSegment(sketch, "E364", {"start": v(55.6, 26.99) * mm, "end": v(55.8, 27.08) * mm});
            skLineSegment(sketch, "E365", {"start": v(55.8, 27.08) * mm, "end": v(55.96, 27.2) * mm});
            skLineSegment(sketch, "E366", {"start": v(55.96, 27.2) * mm, "end": v(56.1, 27.38) * mm});
            skLineSegment(sketch, "E367", {"start": v(56.1, 27.38) * mm, "end": v(56.18, 27.57) * mm});
            skLineSegment(sketch, "E368", {"start": v(56.18, 27.57) * mm, "end": v(56.21, 27.79) * mm});
            skLineSegment(sketch, "E369", {"start": v(56.21, 27.79) * mm, "end": v(56.19, 28) * mm});
            skLineSegment(sketch, "E370", {"start": v(56.19, 28) * mm, "end": v(56.1, 28.2) * mm});
            skLineSegment(sketch, "E371", {"start": v(56.1, 28.2) * mm, "end": v(55.98, 28.37) * mm});
            skLineSegment(sketch, "E372", {"start": v(55.98, 28.37) * mm, "end": v(55.81, 28.5) * mm});
            skLineSegment(sketch, "E373", {"start": v(55.81, 28.5) * mm, "end": v(55.61, 28.59) * mm});
            skLineSegment(sketch, "E374", {"start": v(55.61, 28.59) * mm, "end": v(55.4, 28.62) * mm});
            skLineSegment(sketch, "E375", {"start": v(55.4, 28.62) * mm, "end": v(55.19, 28.6) * mm});
            skLineSegment(sketch, "E376", {"start": v(55.19, 28.6) * mm, "end": v(55, 28.51) * mm});
            skLineSegment(sketch, "E377", {"start": v(55, 28.51) * mm, "end": v(54.81, 28.42) * mm});
            skLineSegment(sketch, "E378", {"start": v(54.81, 28.42) * mm, "end": v(54.63, 28.33) * mm});
            skLineSegment(sketch, "E379", {"start": v(54.63, 28.33) * mm, "end": v(54.45, 28.24) * mm});
            skLineSegment(sketch, "E380", {"start": v(54.45, 28.24) * mm, "end": v(54.26, 28.14) * mm});
            skLineSegment(sketch, "E381", {"start": v(54.26, 28.14) * mm, "end": v(54.08, 28.05) * mm});
            skLineSegment(sketch, "E382", {"start": v(54.08, 28.05) * mm, "end": v(53.9, 27.95) * mm});
            skLineSegment(sketch, "E383", {"start": v(53.9, 27.95) * mm, "end": v(53.7, 27.86) * mm});
            skLineSegment(sketch, "E384", {"start": v(53.7, 27.86) * mm, "end": v(53.52, 27.76) * mm});
            skLineSegment(sketch, "E385", {"start": v(53.52, 27.76) * mm, "end": v(53.34, 27.67) * mm});
            skLineSegment(sketch, "E386", {"start": v(53.34, 27.67) * mm, "end": v(53.15, 27.58) * mm});
            skLineSegment(sketch, "E387", {"start": v(53.15, 27.58) * mm, "end": v(52.96, 27.48) * mm});
            skLineSegment(sketch, "E388", {"start": v(52.96, 27.48) * mm, "end": v(52.78, 27.39) * mm});
            skLineSegment(sketch, "E389", {"start": v(52.78, 27.39) * mm, "end": v(52.65, 27.32) * mm});
            skLineSegment(sketch, "E390", {"start": v(52.65, 27.32) * mm, "end": v(52.55, 27.5) * mm});
            skLineSegment(sketch, "E391", {"start": v(52.55, 27.5) * mm, "end": v(52.45, 27.68) * mm});
            skLineSegment(sketch, "E392", {"start": v(52.45, 27.68) * mm, "end": v(52.36, 27.86) * mm});
            skLineSegment(sketch, "E393", {"start": v(52.36, 27.86) * mm, "end": v(52.26, 28.04) * mm});
            skLineSegment(sketch, "E394", {"start": v(52.26, 28.04) * mm, "end": v(52.16, 28.23) * mm});
            skLineSegment(sketch, "E395", {"start": v(52.16, 28.23) * mm, "end": v(52.06, 28.4) * mm});
            skLineSegment(sketch, "E396", {"start": v(52.06, 28.4) * mm, "end": v(51.97, 28.59) * mm});
            skLineSegment(sketch, "E397", {"start": v(51.97, 28.59) * mm, "end": v(51.87, 28.77) * mm});
            skLineSegment(sketch, "E398", {"start": v(51.87, 28.77) * mm, "end": v(51.77, 28.95) * mm});
            skLineSegment(sketch, "E399", {"start": v(51.77, 28.95) * mm, "end": v(51.68, 29.13) * mm});
            skLineSegment(sketch, "E400", {"start": v(51.68, 29.13) * mm, "end": v(51.58, 29.32) * mm});
            skLineSegment(sketch, "E401", {"start": v(51.58, 29.32) * mm, "end": v(51.53, 29.4) * mm});
            skLineSegment(sketch, "E402", {"start": v(51.53, 29.4) * mm, "end": v(51.7, 29.5) * mm});
            skLineSegment(sketch, "E403", {"start": v(51.7, 29.5) * mm, "end": v(51.89, 29.61) * mm});
            skLineSegment(sketch, "E404", {"start": v(51.89, 29.61) * mm, "end": v(52.07, 29.71) * mm});
            skLineSegment(sketch, "E405", {"start": v(52.07, 29.71) * mm, "end": v(52.25, 29.81) * mm});
            skLineSegment(sketch, "E406", {"start": v(52.25, 29.81) * mm, "end": v(52.43, 29.91) * mm});
            skLineSegment(sketch, "E407", {"start": v(52.43, 29.91) * mm, "end": v(52.62, 30.02) * mm});
            skLineSegment(sketch, "E408", {"start": v(52.62, 30.02) * mm, "end": v(52.8, 30.12) * mm});
            skLineSegment(sketch, "E409", {"start": v(52.8, 30.12) * mm, "end": v(52.98, 30.22) * mm});
            skLineSegment(sketch, "E410", {"start": v(52.98, 30.22) * mm, "end": v(53.16, 30.32) * mm});
            skLineSegment(sketch, "E411", {"start": v(53.16, 30.32) * mm, "end": v(53.34, 30.42) * mm});
            skLineSegment(sketch, "E412", {"start": v(53.34, 30.42) * mm, "end": v(53.52, 30.52) * mm});
            skLineSegment(sketch, "E413", {"start": v(53.52, 30.52) * mm, "end": v(53.7, 30.63) * mm});
            skLineSegment(sketch, "E414", {"start": v(53.7, 30.63) * mm, "end": v(53.9, 30.74) * mm});
            skLineSegment(sketch, "E415", {"start": v(53.9, 30.74) * mm, "end": v(54.06, 30.88) * mm});
            skLineSegment(sketch, "E416", {"start": v(54.06, 30.88) * mm, "end": v(54.18, 31.05) * mm});
            skLineSegment(sketch, "E417", {"start": v(54.18, 31.05) * mm, "end": v(54.26, 31.25) * mm});
            skLineSegment(sketch, "E418", {"start": v(54.26, 31.25) * mm, "end": v(54.27, 31.47) * mm});
            skLineSegment(sketch, "E419", {"start": v(54.27, 31.47) * mm, "end": v(54.23, 31.68) * mm});
            skLineSegment(sketch, "E420", {"start": v(54.23, 31.68) * mm, "end": v(54.14, 31.87) * mm});
            skLineSegment(sketch, "E421", {"start": v(54.14, 31.87) * mm, "end": v(54, 32.04) * mm});
            skLineSegment(sketch, "E422", {"start": v(54, 32.04) * mm, "end": v(53.83, 32.16) * mm});
            skLineSegment(sketch, "E423", {"start": v(53.83, 32.16) * mm, "end": v(53.62, 32.23) * mm});
            skLineSegment(sketch, "E424", {"start": v(53.62, 32.23) * mm, "end": v(53.45, 32.25) * mm});
            skLineSegment(sketch, "E425", {"start": v(53.45, 32.25) * mm, "end": v(53.24, 32.22) * mm});
            skLineSegment(sketch, "E426", {"start": v(53.24, 32.22) * mm, "end": v(53.04, 32.13) * mm});
            skLineSegment(sketch, "E427", {"start": v(53.04, 32.13) * mm, "end": v(52.86, 32.03) * mm});
            skLineSegment(sketch, "E428", {"start": v(52.86, 32.03) * mm, "end": v(52.69, 31.92) * mm});
            skLineSegment(sketch, "E429", {"start": v(52.69, 31.92) * mm, "end": v(52.5, 31.81) * mm});
            skLineSegment(sketch, "E430", {"start": v(52.5, 31.81) * mm, "end": v(52.33, 31.7) * mm});
            skLineSegment(sketch, "E431", {"start": v(52.33, 31.7) * mm, "end": v(52.15, 31.6) * mm});
            skLineSegment(sketch, "E432", {"start": v(52.15, 31.6) * mm, "end": v(51.97, 31.5) * mm});
            skLineSegment(sketch, "E433", {"start": v(51.97, 31.5) * mm, "end": v(51.8, 31.4) * mm});
            skLineSegment(sketch, "E434", {"start": v(51.8, 31.4) * mm, "end": v(51.62, 31.28) * mm});
            skLineSegment(sketch, "E435", {"start": v(51.62, 31.28) * mm, "end": v(51.43, 31.18) * mm});
            skLineSegment(sketch, "E436", {"start": v(51.43, 31.18) * mm, "end": v(51.26, 31.07) * mm});
            skLineSegment(sketch, "E437", {"start": v(51.26, 31.07) * mm, "end": v(51.08, 30.97) * mm});
            skLineSegment(sketch, "E438", {"start": v(51.08, 30.97) * mm, "end": v(50.9, 30.86) * mm});
            skLineSegment(sketch, "E439", {"start": v(50.9, 30.86) * mm, "end": v(50.75, 30.77) * mm});
            skLineSegment(sketch, "E440", {"start": v(50.75, 30.77) * mm, "end": v(50.64, 30.94) * mm});
            skLineSegment(sketch, "E441", {"start": v(50.64, 30.94) * mm, "end": v(50.53, 31.12) * mm});
            skLineSegment(sketch, "E442", {"start": v(50.53, 31.12) * mm, "end": v(50.42, 31.3) * mm});
            skLineSegment(sketch, "E443", {"start": v(50.42, 31.3) * mm, "end": v(50.31, 31.47) * mm});
            skLineSegment(sketch, "E444", {"start": v(50.31, 31.47) * mm, "end": v(50.2, 31.64) * mm});
            skLineSegment(sketch, "E445", {"start": v(50.2, 31.64) * mm, "end": v(50.1, 31.82) * mm});
            skLineSegment(sketch, "E446", {"start": v(50.1, 31.82) * mm, "end": v(49.98, 32) * mm});
            skLineSegment(sketch, "E447", {"start": v(49.98, 32) * mm, "end": v(49.88, 32.17) * mm});
            skLineSegment(sketch, "E448", {"start": v(49.88, 32.17) * mm, "end": v(49.77, 32.34) * mm});
            skLineSegment(sketch, "E449", {"start": v(49.77, 32.34) * mm, "end": v(49.66, 32.52) * mm});
            skLineSegment(sketch, "E450", {"start": v(49.66, 32.52) * mm, "end": v(49.55, 32.7) * mm});
            skLineSegment(sketch, "E451", {"start": v(49.55, 32.7) * mm, "end": v(49.5, 32.78) * mm});
            skLineSegment(sketch, "E452", {"start": v(49.5, 32.78) * mm, "end": v(49.67, 32.9) * mm});
            skLineSegment(sketch, "E453", {"start": v(49.67, 32.9) * mm, "end": v(49.84, 33) * mm});
            skLineSegment(sketch, "E454", {"start": v(49.84, 33) * mm, "end": v(50.02, 33.12) * mm});
            skLineSegment(sketch, "E455", {"start": v(50.02, 33.12) * mm, "end": v(50.19, 33.23) * mm});
            skLineSegment(sketch, "E456", {"start": v(50.19, 33.23) * mm, "end": v(50.36, 33.34) * mm});
            skLineSegment(sketch, "E457", {"start": v(50.36, 33.34) * mm, "end": v(50.54, 33.46) * mm});
            skLineSegment(sketch, "E458", {"start": v(50.54, 33.46) * mm, "end": v(50.71, 33.57) * mm});
            skLineSegment(sketch, "E459", {"start": v(50.71, 33.57) * mm, "end": v(50.88, 33.68) * mm});
            skLineSegment(sketch, "E460", {"start": v(50.88, 33.68) * mm, "end": v(51.06, 33.8) * mm});
            skLineSegment(sketch, "E461", {"start": v(51.06, 33.8) * mm, "end": v(51.23, 33.91) * mm});
            skLineSegment(sketch, "E462", {"start": v(51.23, 33.91) * mm, "end": v(51.4, 34.02) * mm});
            skLineSegment(sketch, "E463", {"start": v(51.4, 34.02) * mm, "end": v(51.58, 34.14) * mm});
            skLineSegment(sketch, "E464", {"start": v(51.58, 34.14) * mm, "end": v(51.77, 34.26) * mm});
            skLineSegment(sketch, "E465", {"start": v(51.77, 34.26) * mm, "end": v(51.92, 34.4) * mm});
            skLineSegment(sketch, "E466", {"start": v(51.92, 34.4) * mm, "end": v(52.03, 34.6) * mm});
            skLineSegment(sketch, "E467", {"start": v(52.03, 34.6) * mm, "end": v(52.1, 34.8) * mm});
            skLineSegment(sketch, "E468", {"start": v(52.1, 34.8) * mm, "end": v(52.1, 35.01) * mm});
            skLineSegment(sketch, "E469", {"start": v(52.1, 35.01) * mm, "end": v(52.04, 35.22) * mm});
            skLineSegment(sketch, "E470", {"start": v(52.04, 35.22) * mm, "end": v(51.94, 35.4) * mm});
            skLineSegment(sketch, "E471", {"start": v(51.94, 35.4) * mm, "end": v(51.79, 35.56) * mm});
            skLineSegment(sketch, "E472", {"start": v(51.79, 35.56) * mm, "end": v(51.6, 35.67) * mm});
            skLineSegment(sketch, "E473", {"start": v(51.6, 35.67) * mm, "end": v(51.4, 35.73) * mm});
            skLineSegment(sketch, "E474", {"start": v(51.4, 35.73) * mm, "end": v(51.27, 35.74) * mm});
            skLineSegment(sketch, "E475", {"start": v(51.27, 35.74) * mm, "end": v(51.06, 35.7) * mm});
            skLineSegment(sketch, "E476", {"start": v(51.06, 35.7) * mm, "end": v(50.86, 35.62) * mm});
            skLineSegment(sketch, "E477", {"start": v(50.86, 35.62) * mm, "end": v(50.68, 35.5) * mm});
            skLineSegment(sketch, "E478", {"start": v(50.68, 35.5) * mm, "end": v(50.5, 35.38) * mm});
            skLineSegment(sketch, "E479", {"start": v(50.5, 35.38) * mm, "end": v(50.34, 35.26) * mm});
            skLineSegment(sketch, "E480", {"start": v(50.34, 35.26) * mm, "end": v(50.16, 35.14) * mm});
            skLineSegment(sketch, "E481", {"start": v(50.16, 35.14) * mm, "end": v(50, 35.03) * mm});
            skLineSegment(sketch, "E482", {"start": v(50, 35.03) * mm, "end": v(49.82, 34.9) * mm});
            skLineSegment(sketch, "E483", {"start": v(49.82, 34.9) * mm, "end": v(49.65, 34.79) * mm});
            skLineSegment(sketch, "E484", {"start": v(49.65, 34.79) * mm, "end": v(49.48, 34.67) * mm});
            skLineSegment(sketch, "E485", {"start": v(49.48, 34.67) * mm, "end": v(49.31, 34.56) * mm});
            skLineSegment(sketch, "E486", {"start": v(49.31, 34.56) * mm, "end": v(49.14, 34.44) * mm});
            skLineSegment(sketch, "E487", {"start": v(49.14, 34.44) * mm, "end": v(48.97, 34.32) * mm});
            skLineSegment(sketch, "E488", {"start": v(48.97, 34.32) * mm, "end": v(48.8, 34.2) * mm});
            skLineSegment(sketch, "E489", {"start": v(48.8, 34.2) * mm, "end": v(48.62, 34.08) * mm});
            skLineSegment(sketch, "E490", {"start": v(48.62, 34.08) * mm, "end": v(48.5, 34.25) * mm});
            skLineSegment(sketch, "E491", {"start": v(48.5, 34.25) * mm, "end": v(48.38, 34.42) * mm});
            skLineSegment(sketch, "E492", {"start": v(48.38, 34.42) * mm, "end": v(48.26, 34.59) * mm});
            skLineSegment(sketch, "E493", {"start": v(48.26, 34.59) * mm, "end": v(48.14, 34.75) * mm});
            skLineSegment(sketch, "E494", {"start": v(48.14, 34.75) * mm, "end": v(48.02, 34.92) * mm});
            skLineSegment(sketch, "E495", {"start": v(48.02, 34.92) * mm, "end": v(47.9, 35.09) * mm});
            skLineSegment(sketch, "E496", {"start": v(47.9, 35.09) * mm, "end": v(47.78, 35.26) * mm});
            skLineSegment(sketch, "E497", {"start": v(47.78, 35.26) * mm, "end": v(47.66, 35.42) * mm});
            skLineSegment(sketch, "E498", {"start": v(47.66, 35.42) * mm, "end": v(47.54, 35.6) * mm});
            skLineSegment(sketch, "E499", {"start": v(47.54, 35.6) * mm, "end": v(47.42, 35.76) * mm});
            skLineSegment(sketch, "E500", {"start": v(47.42, 35.76) * mm, "end": v(47.3, 35.93) * mm});
            skLineSegment(sketch, "E501", {"start": v(47.3, 35.93) * mm, "end": v(47.24, 36.01) * mm});
            skLineSegment(sketch, "E502", {"start": v(47.24, 36.01) * mm, "end": v(47.4, 36.13) * mm});
            skLineSegment(sketch, "E503", {"start": v(47.4, 36.13) * mm, "end": v(47.57, 36.26) * mm});
            skLineSegment(sketch, "E504", {"start": v(47.57, 36.26) * mm, "end": v(47.74, 36.38) * mm});
            skLineSegment(sketch, "E505", {"start": v(47.74, 36.38) * mm, "end": v(47.9, 36.5) * mm});
            skLineSegment(sketch, "E506", {"start": v(47.9, 36.5) * mm, "end": v(48.07, 36.63) * mm});
            skLineSegment(sketch, "E507", {"start": v(48.07, 36.63) * mm, "end": v(48.24, 36.76) * mm});
            skLineSegment(sketch, "E508", {"start": v(48.24, 36.76) * mm, "end": v(48.4, 36.88) * mm});
            skLineSegment(sketch, "E509", {"start": v(48.4, 36.88) * mm, "end": v(48.57, 37) * mm});
            skLineSegment(sketch, "E510", {"start": v(48.57, 37) * mm, "end": v(48.74, 37.13) * mm});
            skLineSegment(sketch, "E511", {"start": v(48.74, 37.13) * mm, "end": v(48.9, 37.25) * mm});
            skLineSegment(sketch, "E512", {"start": v(48.9, 37.25) * mm, "end": v(49.07, 37.38) * mm});
            skLineSegment(sketch, "E513", {"start": v(49.07, 37.38) * mm, "end": v(49.24, 37.5) * mm});
            skLineSegment(sketch, "E514", {"start": v(49.24, 37.5) * mm, "end": v(49.42, 37.64) * mm});
            skLineSegment(sketch, "E515", {"start": v(49.42, 37.64) * mm, "end": v(49.56, 37.8) * mm});
            skLineSegment(sketch, "E516", {"start": v(49.56, 37.8) * mm, "end": v(49.66, 37.99) * mm});
            skLineSegment(sketch, "E517", {"start": v(49.66, 37.99) * mm, "end": v(49.7, 38.2) * mm});
            skLineSegment(sketch, "E518", {"start": v(49.7, 38.2) * mm, "end": v(49.7, 38.41) * mm});
            skLineSegment(sketch, "E519", {"start": v(49.7, 38.41) * mm, "end": v(49.63, 38.61) * mm});
            skLineSegment(sketch, "E520", {"start": v(49.63, 38.61) * mm, "end": v(49.51, 38.8) * mm});
            skLineSegment(sketch, "E521", {"start": v(49.51, 38.8) * mm, "end": v(49.35, 38.94) * mm});
            skLineSegment(sketch, "E522", {"start": v(49.35, 38.94) * mm, "end": v(49.16, 39.03) * mm});
            skLineSegment(sketch, "E523", {"start": v(49.16, 39.03) * mm, "end": v(48.95, 39.08) * mm});
            skLineSegment(sketch, "E524", {"start": v(48.95, 39.08) * mm, "end": v(48.9, 39.08) * mm});
            skLineSegment(sketch, "E525", {"start": v(48.9, 39.08) * mm, "end": v(48.7, 39.06) * mm});
            skLineSegment(sketch, "E526", {"start": v(48.7, 39.06) * mm, "end": v(48.5, 38.98) * mm});
            skLineSegment(sketch, "E527", {"start": v(48.5, 38.98) * mm, "end": v(48.32, 38.85) * mm});
            skLineSegment(sketch, "E528", {"start": v(48.32, 38.85) * mm, "end": v(48.15, 38.73) * mm});
            skLineSegment(sketch, "E529", {"start": v(48.15, 38.73) * mm, "end": v(48, 38.6) * mm});
            skLineSegment(sketch, "E530", {"start": v(48, 38.6) * mm, "end": v(47.83, 38.47) * mm});
            skLineSegment(sketch, "E531", {"start": v(47.83, 38.47) * mm, "end": v(47.66, 38.34) * mm});
            skLineSegment(sketch, "E532", {"start": v(47.66, 38.34) * mm, "end": v(47.5, 38.21) * mm});
            skLineSegment(sketch, "E533", {"start": v(47.5, 38.21) * mm, "end": v(47.34, 38.08) * mm});
            skLineSegment(sketch, "E534", {"start": v(47.34, 38.08) * mm, "end": v(47.17, 37.95) * mm});
            skLineSegment(sketch, "E535", {"start": v(47.17, 37.95) * mm, "end": v(47.01, 37.83) * mm});
            skLineSegment(sketch, "E536", {"start": v(47.01, 37.83) * mm, "end": v(46.85, 37.7) * mm});
            skLineSegment(sketch, "E537", {"start": v(46.85, 37.7) * mm, "end": v(46.68, 37.57) * mm});
            skLineSegment(sketch, "E538", {"start": v(46.68, 37.57) * mm, "end": v(46.52, 37.44) * mm});
            skLineSegment(sketch, "E539", {"start": v(46.52, 37.44) * mm, "end": v(46.36, 37.3) * mm});
            skLineSegment(sketch, "E540", {"start": v(46.36, 37.3) * mm, "end": v(46.29, 37.25) * mm});
            skLineSegment(sketch, "E541", {"start": v(46.29, 37.25) * mm, "end": v(46.16, 37.41) * mm});
            skLineSegment(sketch, "E542", {"start": v(46.16, 37.41) * mm, "end": v(46.03, 37.57) * mm});
            skLineSegment(sketch, "E543", {"start": v(46.03, 37.57) * mm, "end": v(45.9, 37.73) * mm});
            skLineSegment(sketch, "E544", {"start": v(45.9, 37.73) * mm, "end": v(45.76, 37.9) * mm});
            skLineSegment(sketch, "E545", {"start": v(45.76, 37.9) * mm, "end": v(45.63, 38.05) * mm});
            skLineSegment(sketch, "E546", {"start": v(45.63, 38.05) * mm, "end": v(45.5, 38.2) * mm});
            skLineSegment(sketch, "E547", {"start": v(45.5, 38.2) * mm, "end": v(45.37, 38.37) * mm});
            skLineSegment(sketch, "E548", {"start": v(45.37, 38.37) * mm, "end": v(45.24, 38.53) * mm});
            skLineSegment(sketch, "E549", {"start": v(45.24, 38.53) * mm, "end": v(45.11, 38.69) * mm});
            skLineSegment(sketch, "E550", {"start": v(45.11, 38.69) * mm, "end": v(44.98, 38.85) * mm});
            skLineSegment(sketch, "E551", {"start": v(44.98, 38.85) * mm, "end": v(44.85, 39) * mm});
            skLineSegment(sketch, "E552", {"start": v(44.85, 39) * mm, "end": v(44.78, 39.09) * mm});
            skLineSegment(sketch, "E553", {"start": v(44.78, 39.09) * mm, "end": v(44.94, 39.22) * mm});
            skLineSegment(sketch, "E554", {"start": v(44.94, 39.22) * mm, "end": v(45.1, 39.35) * mm});
            skLineSegment(sketch, "E555", {"start": v(45.1, 39.35) * mm, "end": v(45.26, 39.5) * mm});
            skLineSegment(sketch, "E556", {"start": v(45.26, 39.5) * mm, "end": v(45.41, 39.63) * mm});
            skLineSegment(sketch, "E557", {"start": v(45.41, 39.63) * mm, "end": v(45.57, 39.76) * mm});
            skLineSegment(sketch, "E558", {"start": v(45.57, 39.76) * mm, "end": v(45.73, 39.9) * mm});
            skLineSegment(sketch, "E559", {"start": v(45.73, 39.9) * mm, "end": v(45.89, 40.03) * mm});
            skLineSegment(sketch, "E560", {"start": v(45.89, 40.03) * mm, "end": v(46.04, 40.16) * mm});
            skLineSegment(sketch, "E561", {"start": v(46.04, 40.16) * mm, "end": v(46.2, 40.3) * mm});
            skLineSegment(sketch, "E562", {"start": v(46.2, 40.3) * mm, "end": v(46.36, 40.44) * mm});
            skLineSegment(sketch, "E563", {"start": v(46.36, 40.44) * mm, "end": v(46.52, 40.57) * mm});
            skLineSegment(sketch, "E564", {"start": v(46.52, 40.57) * mm, "end": v(46.68, 40.7) * mm});
            skLineSegment(sketch, "E565", {"start": v(46.68, 40.7) * mm, "end": v(46.85, 40.85) * mm});
            skLineSegment(sketch, "E566", {"start": v(46.85, 40.85) * mm, "end": v(46.98, 41.02) * mm});
            skLineSegment(sketch, "E567", {"start": v(46.98, 41.02) * mm, "end": v(47.07, 41.22) * mm});
            skLineSegment(sketch, "E568", {"start": v(47.07, 41.22) * mm, "end": v(47.1, 41.43) * mm});
            skLineSegment(sketch, "E569", {"start": v(47.1, 41.43) * mm, "end": v(47.07, 41.64) * mm});
            skLineSegment(sketch, "E570", {"start": v(47.07, 41.64) * mm, "end": v(47, 41.84) * mm});
            skLineSegment(sketch, "E571", {"start": v(47, 41.84) * mm, "end": v(46.86, 42.01) * mm});
            skLineSegment(sketch, "E572", {"start": v(46.86, 42.01) * mm, "end": v(46.7, 42.15) * mm});
            skLineSegment(sketch, "E573", {"start": v(46.7, 42.15) * mm, "end": v(46.5, 42.23) * mm});
            skLineSegment(sketch, "E574", {"start": v(46.5, 42.23) * mm, "end": v(46.29, 42.26) * mm});
            skLineSegment(sketch, "E575", {"start": v(46.29, 42.26) * mm, "end": v(46.07, 42.23) * mm});
            skLineSegment(sketch, "E576", {"start": v(46.07, 42.23) * mm, "end": v(45.87, 42.15) * mm});
            skLineSegment(sketch, "E577", {"start": v(45.87, 42.15) * mm, "end": v(45.71, 42.03) * mm});
            skLineSegment(sketch, "E578", {"start": v(45.71, 42.03) * mm, "end": v(45.56, 41.9) * mm});
            skLineSegment(sketch, "E579", {"start": v(45.56, 41.9) * mm, "end": v(45.4, 41.76) * mm});
            skLineSegment(sketch, "E580", {"start": v(45.4, 41.76) * mm, "end": v(45.25, 41.62) * mm});
            skLineSegment(sketch, "E581", {"start": v(45.25, 41.62) * mm, "end": v(45.1, 41.48) * mm});
            skLineSegment(sketch, "E582", {"start": v(45.1, 41.48) * mm, "end": v(44.94, 41.34) * mm});
            skLineSegment(sketch, "E583", {"start": v(44.94, 41.34) * mm, "end": v(44.79, 41.2) * mm});
            skLineSegment(sketch, "E584", {"start": v(44.79, 41.2) * mm, "end": v(44.63, 41.06) * mm});
            skLineSegment(sketch, "E585", {"start": v(44.63, 41.06) * mm, "end": v(44.48, 40.92) * mm});
            skLineSegment(sketch, "E586", {"start": v(44.48, 40.92) * mm, "end": v(44.32, 40.78) * mm});
            skLineSegment(sketch, "E587", {"start": v(44.32, 40.78) * mm, "end": v(44.17, 40.65) * mm});
            skLineSegment(sketch, "E588", {"start": v(44.17, 40.65) * mm, "end": v(44.01, 40.5) * mm});
            skLineSegment(sketch, "E589", {"start": v(44.01, 40.5) * mm, "end": v(43.86, 40.37) * mm});
            skLineSegment(sketch, "E590", {"start": v(43.86, 40.37) * mm, "end": v(43.75, 40.27) * mm});
            skLineSegment(sketch, "E591", {"start": v(43.75, 40.27) * mm, "end": v(43.6, 40.42) * mm});
            skLineSegment(sketch, "E592", {"start": v(43.6, 40.42) * mm, "end": v(43.47, 40.57) * mm});
            skLineSegment(sketch, "E593", {"start": v(43.47, 40.57) * mm, "end": v(43.33, 40.72) * mm});
            skLineSegment(sketch, "E594", {"start": v(43.33, 40.72) * mm, "end": v(43.19, 40.87) * mm});
            skLineSegment(sketch, "E595", {"start": v(43.19, 40.87) * mm, "end": v(43.05, 41.02) * mm});
            skLineSegment(sketch, "E596", {"start": v(43.05, 41.02) * mm, "end": v(42.9, 41.17) * mm});
            skLineSegment(sketch, "E597", {"start": v(42.9, 41.17) * mm, "end": v(42.76, 41.32) * mm});
            skLineSegment(sketch, "E598", {"start": v(42.76, 41.32) * mm, "end": v(42.62, 41.47) * mm});
            skLineSegment(sketch, "E599", {"start": v(42.62, 41.47) * mm, "end": v(42.48, 41.62) * mm});
            skLineSegment(sketch, "E600", {"start": v(42.48, 41.62) * mm, "end": v(42.34, 41.77) * mm});
            skLineSegment(sketch, "E601", {"start": v(42.34, 41.77) * mm, "end": v(42.2, 41.92) * mm});
            skLineSegment(sketch, "E602", {"start": v(42.2, 41.92) * mm, "end": v(42.13, 42) * mm});
            skLineSegment(sketch, "E603", {"start": v(42.13, 42) * mm, "end": v(42.28, 42.14) * mm});
            skLineSegment(sketch, "E604", {"start": v(42.28, 42.14) * mm, "end": v(42.42, 42.28) * mm});
            skLineSegment(sketch, "E605", {"start": v(42.42, 42.28) * mm, "end": v(42.58, 42.43) * mm});
            skLineSegment(sketch, "E606", {"start": v(42.58, 42.43) * mm, "end": v(42.72, 42.58) * mm});
            skLineSegment(sketch, "E607", {"start": v(42.72, 42.58) * mm, "end": v(42.87, 42.72) * mm});
            skLineSegment(sketch, "E608", {"start": v(42.87, 42.72) * mm, "end": v(43.02, 42.87) * mm});
            skLineSegment(sketch, "E609", {"start": v(43.02, 42.87) * mm, "end": v(43.17, 43.01) * mm});
            skLineSegment(sketch, "E610", {"start": v(43.17, 43.01) * mm, "end": v(43.32, 43.15) * mm});
            skLineSegment(sketch, "E611", {"start": v(43.32, 43.15) * mm, "end": v(43.47, 43.3) * mm});
            skLineSegment(sketch, "E612", {"start": v(43.47, 43.3) * mm, "end": v(43.62, 43.45) * mm});
            skLineSegment(sketch, "E613", {"start": v(43.62, 43.45) * mm, "end": v(43.76, 43.59) * mm});
            skLineSegment(sketch, "E614", {"start": v(43.76, 43.59) * mm, "end": v(43.91, 43.74) * mm});
            skLineSegment(sketch, "E615", {"start": v(43.91, 43.74) * mm, "end": v(44.07, 43.9) * mm});
            skLineSegment(sketch, "E616", {"start": v(44.07, 43.9) * mm, "end": v(44.2, 44.07) * mm});
            skLineSegment(sketch, "E617", {"start": v(44.2, 44.07) * mm, "end": v(44.27, 44.27) * mm});
            skLineSegment(sketch, "E618", {"start": v(44.27, 44.27) * mm, "end": v(44.28, 44.48) * mm});
            skLineSegment(sketch, "E619", {"start": v(44.28, 44.48) * mm, "end": v(44.25, 44.7) * mm});
            skLineSegment(sketch, "E620", {"start": v(44.25, 44.7) * mm, "end": v(44.15, 44.89) * mm});
            skLineSegment(sketch, "E621", {"start": v(44.15, 44.89) * mm, "end": v(44.01, 45.05) * mm});
            skLineSegment(sketch, "E622", {"start": v(44.01, 45.05) * mm, "end": v(43.84, 45.17) * mm});
            skLineSegment(sketch, "E623", {"start": v(43.84, 45.17) * mm, "end": v(43.64, 45.25) * mm});
            skLineSegment(sketch, "E624", {"start": v(43.64, 45.25) * mm, "end": v(43.46, 45.26) * mm});
            skLineSegment(sketch, "E625", {"start": v(43.46, 45.26) * mm, "end": v(43.25, 45.23) * mm});
            skLineSegment(sketch, "E626", {"start": v(43.25, 45.23) * mm, "end": v(43.05, 45.15) * mm});
            skLineSegment(sketch, "E627", {"start": v(43.05, 45.15) * mm, "end": v(42.88, 45.02) * mm});
            skLineSegment(sketch, "E628", {"start": v(42.88, 45.02) * mm, "end": v(42.74, 44.87) * mm});
            skLineSegment(sketch, "E629", {"start": v(42.74, 44.87) * mm, "end": v(42.6, 44.72) * mm});
            skLineSegment(sketch, "E630", {"start": v(42.6, 44.72) * mm, "end": v(42.45, 44.57) * mm});
            skLineSegment(sketch, "E631", {"start": v(42.45, 44.57) * mm, "end": v(42.3, 44.42) * mm});
            skLineSegment(sketch, "E632", {"start": v(42.3, 44.42) * mm, "end": v(42.16, 44.28) * mm});
            skLineSegment(sketch, "E633", {"start": v(42.16, 44.28) * mm, "end": v(42.01, 44.13) * mm});
            skLineSegment(sketch, "E634", {"start": v(42.01, 44.13) * mm, "end": v(41.87, 43.98) * mm});
            skLineSegment(sketch, "E635", {"start": v(41.87, 43.98) * mm, "end": v(41.73, 43.83) * mm});
            skLineSegment(sketch, "E636", {"start": v(41.73, 43.83) * mm, "end": v(41.58, 43.68) * mm});
            skLineSegment(sketch, "E637", {"start": v(41.58, 43.68) * mm, "end": v(41.44, 43.53) * mm});
            skLineSegment(sketch, "E638", {"start": v(41.44, 43.53) * mm, "end": v(41.3, 43.38) * mm});
            skLineSegment(sketch, "E639", {"start": v(41.3, 43.38) * mm, "end": v(41.14, 43.23) * mm});
            skLineSegment(sketch, "E640", {"start": v(41.14, 43.23) * mm, "end": v(41.02, 43.1) * mm});
            skLineSegment(sketch, "E641", {"start": v(41.02, 43.1) * mm, "end": v(40.87, 43.25) * mm});
            skLineSegment(sketch, "E642", {"start": v(40.87, 43.25) * mm, "end": v(40.72, 43.39) * mm});
            skLineSegment(sketch, "E643", {"start": v(40.72, 43.39) * mm, "end": v(40.57, 43.53) * mm});
            skLineSegment(sketch, "E644", {"start": v(40.57, 43.53) * mm, "end": v(40.42, 43.67) * mm});
            skLineSegment(sketch, "E645", {"start": v(40.42, 43.67) * mm, "end": v(40.27, 43.8) * mm});
            skLineSegment(sketch, "E646", {"start": v(40.27, 43.8) * mm, "end": v(40.12, 43.95) * mm});
            skLineSegment(sketch, "E647", {"start": v(40.12, 43.95) * mm, "end": v(39.97, 44.1) * mm});
            skLineSegment(sketch, "E648", {"start": v(39.97, 44.1) * mm, "end": v(39.82, 44.23) * mm});
            skLineSegment(sketch, "E649", {"start": v(39.82, 44.23) * mm, "end": v(39.67, 44.37) * mm});
            skLineSegment(sketch, "E650", {"start": v(39.67, 44.37) * mm, "end": v(39.52, 44.51) * mm});
            skLineSegment(sketch, "E651", {"start": v(39.52, 44.51) * mm, "end": v(39.37, 44.65) * mm});
            skLineSegment(sketch, "E652", {"start": v(39.37, 44.65) * mm, "end": v(39.29, 44.73) * mm});
            skLineSegment(sketch, "E653", {"start": v(39.29, 44.73) * mm, "end": v(39.43, 44.88) * mm});
            skLineSegment(sketch, "E654", {"start": v(39.43, 44.88) * mm, "end": v(39.57, 45.03) * mm});
            skLineSegment(sketch, "E655", {"start": v(39.57, 45.03) * mm, "end": v(39.7, 45.19) * mm});
            skLineSegment(sketch, "E656", {"start": v(39.7, 45.19) * mm, "end": v(39.84, 45.34) * mm});
            skLineSegment(sketch, "E657", {"start": v(39.84, 45.34) * mm, "end": v(39.98, 45.5) * mm});
            skLineSegment(sketch, "E658", {"start": v(39.98, 45.5) * mm, "end": v(40.12, 45.65) * mm});
            skLineSegment(sketch, "E659", {"start": v(40.12, 45.65) * mm, "end": v(40.26, 45.8) * mm});
            skLineSegment(sketch, "E660", {"start": v(40.26, 45.8) * mm, "end": v(40.4, 45.96) * mm});
            skLineSegment(sketch, "E661", {"start": v(40.4, 45.96) * mm, "end": v(40.54, 46.12) * mm});
            skLineSegment(sketch, "E662", {"start": v(40.54, 46.12) * mm, "end": v(40.68, 46.27) * mm});
            skLineSegment(sketch, "E663", {"start": v(40.68, 46.27) * mm, "end": v(40.82, 46.42) * mm});
            skLineSegment(sketch, "E664", {"start": v(40.82, 46.42) * mm, "end": v(40.96, 46.58) * mm});
            skLineSegment(sketch, "E665", {"start": v(40.96, 46.58) * mm, "end": v(41.1, 46.74) * mm});
            skLineSegment(sketch, "E666", {"start": v(41.1, 46.74) * mm, "end": v(41.22, 46.93) * mm});
            skLineSegment(sketch, "E667", {"start": v(41.22, 46.93) * mm, "end": v(41.28, 47.13) * mm});
            skLineSegment(sketch, "E668", {"start": v(41.28, 47.13) * mm, "end": v(41.28, 47.35) * mm});
            skLineSegment(sketch, "E669", {"start": v(41.28, 47.35) * mm, "end": v(41.23, 47.56) * mm});
            skLineSegment(sketch, "E670", {"start": v(41.23, 47.56) * mm, "end": v(41.12, 47.74) * mm});
            skLineSegment(sketch, "E671", {"start": v(41.12, 47.74) * mm, "end": v(40.97, 47.9) * mm});
            skLineSegment(sketch, "E672", {"start": v(40.97, 47.9) * mm, "end": v(40.79, 48) * mm});
            skLineSegment(sketch, "E673", {"start": v(40.79, 48) * mm, "end": v(40.58, 48.07) * mm});
            skLineSegment(sketch, "E674", {"start": v(40.58, 48.07) * mm, "end": v(40.45, 48.07) * mm});
            skLineSegment(sketch, "E675", {"start": v(40.45, 48.07) * mm, "end": v(40.24, 48.04) * mm});
            skLineSegment(sketch, "E676", {"start": v(40.24, 48.04) * mm, "end": v(40.04, 47.96) * mm});
            skLineSegment(sketch, "E677", {"start": v(40.04, 47.96) * mm, "end": v(39.88, 47.82) * mm});
            skLineSegment(sketch, "E678", {"start": v(39.88, 47.82) * mm, "end": v(39.73, 47.66) * mm});
            skLineSegment(sketch, "E679", {"start": v(39.73, 47.66) * mm, "end": v(39.6, 47.5) * mm});
            skLineSegment(sketch, "E680", {"start": v(39.6, 47.5) * mm, "end": v(39.46, 47.34) * mm});
            skLineSegment(sketch, "E681", {"start": v(39.46, 47.34) * mm, "end": v(39.33, 47.18) * mm});
            skLineSegment(sketch, "E682", {"start": v(39.33, 47.18) * mm, "end": v(39.2, 47.03) * mm});
            skLineSegment(sketch, "E683", {"start": v(39.2, 47.03) * mm, "end": v(39.06, 46.87) * mm});
            skLineSegment(sketch, "E684", {"start": v(39.06, 46.87) * mm, "end": v(38.92, 46.7) * mm});
            skLineSegment(sketch, "E685", {"start": v(38.92, 46.7) * mm, "end": v(38.79, 46.55) * mm});
            skLineSegment(sketch, "E686", {"start": v(38.79, 46.55) * mm, "end": v(38.65, 46.4) * mm});
            skLineSegment(sketch, "E687", {"start": v(38.65, 46.4) * mm, "end": v(38.52, 46.23) * mm});
            skLineSegment(sketch, "E688", {"start": v(38.52, 46.23) * mm, "end": v(38.38, 46.08) * mm});
            skLineSegment(sketch, "E689", {"start": v(38.38, 46.08) * mm, "end": v(38.25, 45.92) * mm});
            skLineSegment(sketch, "E690", {"start": v(38.25, 45.92) * mm, "end": v(38.11, 45.76) * mm});
            skLineSegment(sketch, "E691", {"start": v(38.11, 45.76) * mm, "end": v(37.95, 45.9) * mm});
            skLineSegment(sketch, "E692", {"start": v(37.95, 45.9) * mm, "end": v(37.8, 46.02) * mm});
            skLineSegment(sketch, "E693", {"start": v(37.8, 46.02) * mm, "end": v(37.63, 46.15) * mm});
            skLineSegment(sketch, "E694", {"start": v(37.63, 46.15) * mm, "end": v(37.47, 46.28) * mm});
            skLineSegment(sketch, "E695", {"start": v(37.47, 46.28) * mm, "end": v(37.31, 46.41) * mm});
            skLineSegment(sketch, "E696", {"start": v(37.31, 46.41) * mm, "end": v(37.16, 46.54) * mm});
            skLineSegment(sketch, "E697", {"start": v(37.16, 46.54) * mm, "end": v(37, 46.67) * mm});
            skLineSegment(sketch, "E698", {"start": v(37, 46.67) * mm, "end": v(36.84, 46.8) * mm});
            skLineSegment(sketch, "E699", {"start": v(36.84, 46.8) * mm, "end": v(36.68, 46.94) * mm});
            skLineSegment(sketch, "E700", {"start": v(36.68, 46.94) * mm, "end": v(36.52, 47.07) * mm});
            skLineSegment(sketch, "E701", {"start": v(36.52, 47.07) * mm, "end": v(36.36, 47.2) * mm});
            skLineSegment(sketch, "E702", {"start": v(36.36, 47.2) * mm, "end": v(36.28, 47.26) * mm});
            skLineSegment(sketch, "E703", {"start": v(36.28, 47.26) * mm, "end": v(36.4, 47.43) * mm});
            skLineSegment(sketch, "E704", {"start": v(36.4, 47.43) * mm, "end": v(36.53, 47.59) * mm});
            skLineSegment(sketch, "E705", {"start": v(36.53, 47.59) * mm, "end": v(36.66, 47.75) * mm});
            skLineSegment(sketch, "E706", {"start": v(36.66, 47.75) * mm, "end": v(36.8, 47.91) * mm});
            skLineSegment(sketch, "E707", {"start": v(36.8, 47.91) * mm, "end": v(36.92, 48.08) * mm});
            skLineSegment(sketch, "E708", {"start": v(36.92, 48.08) * mm, "end": v(37.05, 48.24) * mm});
            skLineSegment(sketch, "E709", {"start": v(37.05, 48.24) * mm, "end": v(37.18, 48.4) * mm});
            skLineSegment(sketch, "E710", {"start": v(37.18, 48.4) * mm, "end": v(37.3, 48.57) * mm});
            skLineSegment(sketch, "E711", {"start": v(37.3, 48.57) * mm, "end": v(37.44, 48.73) * mm});
            skLineSegment(sketch, "E712", {"start": v(37.44, 48.73) * mm, "end": v(37.56, 48.9) * mm});
            skLineSegment(sketch, "E713", {"start": v(37.56, 48.9) * mm, "end": v(37.7, 49.06) * mm});
            skLineSegment(sketch, "E714", {"start": v(37.7, 49.06) * mm, "end": v(37.82, 49.22) * mm});
            skLineSegment(sketch, "E715", {"start": v(37.82, 49.22) * mm, "end": v(37.96, 49.4) * mm});
            skLineSegment(sketch, "E716", {"start": v(37.96, 49.4) * mm, "end": v(38.06, 49.59) * mm});
            skLineSegment(sketch, "E717", {"start": v(38.06, 49.59) * mm, "end": v(38.1, 49.8) * mm});
            skLineSegment(sketch, "E718", {"start": v(38.1, 49.8) * mm, "end": v(38.1, 50.01) * mm});
            skLineSegment(sketch, "E719", {"start": v(38.1, 50.01) * mm, "end": v(38.03, 50.22) * mm});
            skLineSegment(sketch, "E720", {"start": v(38.03, 50.22) * mm, "end": v(37.9, 50.4) * mm});
            skLineSegment(sketch, "E721", {"start": v(37.9, 50.4) * mm, "end": v(37.75, 50.54) * mm});
            skLineSegment(sketch, "E722", {"start": v(37.75, 50.54) * mm, "end": v(37.56, 50.64) * mm});
            skLineSegment(sketch, "E723", {"start": v(37.56, 50.64) * mm, "end": v(37.35, 50.68) * mm});
            skLineSegment(sketch, "E724", {"start": v(37.35, 50.68) * mm, "end": v(37.3, 50.68) * mm});
            skLineSegment(sketch, "E725", {"start": v(37.3, 50.68) * mm, "end": v(37.1, 50.66) * mm});
            skLineSegment(sketch, "E726", {"start": v(37.1, 50.66) * mm, "end": v(36.9, 50.58) * mm});
            skLineSegment(sketch, "E727", {"start": v(36.9, 50.58) * mm, "end": v(36.72, 50.46) * mm});
            skLineSegment(sketch, "E728", {"start": v(36.72, 50.46) * mm, "end": v(36.58, 50.29) * mm});
            skLineSegment(sketch, "E729", {"start": v(36.58, 50.29) * mm, "end": v(36.46, 50.12) * mm});
            skLineSegment(sketch, "E730", {"start": v(36.46, 50.12) * mm, "end": v(36.33, 49.96) * mm});
            skLineSegment(sketch, "E731", {"start": v(36.33, 49.96) * mm, "end": v(36.2, 49.79) * mm});
            skLineSegment(sketch, "E732", {"start": v(36.2, 49.79) * mm, "end": v(36.08, 49.62) * mm});
            skLineSegment(sketch, "E733", {"start": v(36.08, 49.62) * mm, "end": v(35.96, 49.46) * mm});
            skLineSegment(sketch, "E734", {"start": v(35.96, 49.46) * mm, "end": v(35.83, 49.29) * mm});
            skLineSegment(sketch, "E735", {"start": v(35.83, 49.29) * mm, "end": v(35.71, 49.12) * mm});
            skLineSegment(sketch, "E736", {"start": v(35.71, 49.12) * mm, "end": v(35.59, 48.96) * mm});
            skLineSegment(sketch, "E737", {"start": v(35.59, 48.96) * mm, "end": v(35.46, 48.79) * mm});
            skLineSegment(sketch, "E738", {"start": v(35.46, 48.79) * mm, "end": v(35.34, 48.62) * mm});
            skLineSegment(sketch, "E739", {"start": v(35.34, 48.62) * mm, "end": v(35.21, 48.46) * mm});
            skLineSegment(sketch, "E740", {"start": v(35.21, 48.46) * mm, "end": v(35.09, 48.29) * mm});
            skLineSegment(sketch, "E741", {"start": v(35.09, 48.29) * mm, "end": v(35.03, 48.22) * mm});
            skLineSegment(sketch, "E742", {"start": v(35.03, 48.22) * mm, "end": v(34.87, 48.34) * mm});
            skLineSegment(sketch, "E743", {"start": v(34.87, 48.34) * mm, "end": v(34.7, 48.46) * mm});
            skLineSegment(sketch, "E744", {"start": v(34.7, 48.46) * mm, "end": v(34.53, 48.58) * mm});
            skLineSegment(sketch, "E745", {"start": v(34.53, 48.58) * mm, "end": v(34.36, 48.7) * mm});
            skLineSegment(sketch, "E746", {"start": v(34.36, 48.7) * mm, "end": v(34.2, 48.82) * mm});
            skLineSegment(sketch, "E747", {"start": v(34.2, 48.82) * mm, "end": v(34.03, 48.94) * mm});
            skLineSegment(sketch, "E748", {"start": v(34.03, 48.94) * mm, "end": v(33.86, 49.06) * mm});
            skLineSegment(sketch, "E749", {"start": v(33.86, 49.06) * mm, "end": v(33.7, 49.18) * mm});
            skLineSegment(sketch, "E750", {"start": v(33.7, 49.18) * mm, "end": v(33.53, 49.3) * mm});
            skLineSegment(sketch, "E751", {"start": v(33.53, 49.3) * mm, "end": v(33.36, 49.42) * mm});
            skLineSegment(sketch, "E752", {"start": v(33.36, 49.42) * mm, "end": v(33.2, 49.54) * mm});
            skLineSegment(sketch, "E753", {"start": v(33.2, 49.54) * mm, "end": v(33.1, 49.6) * mm});
            skLineSegment(sketch, "E754", {"start": v(33.1, 49.6) * mm, "end": v(33.22, 49.77) * mm});
            skLineSegment(sketch, "E755", {"start": v(33.22, 49.77) * mm, "end": v(33.34, 49.94) * mm});
            skLineSegment(sketch, "E756", {"start": v(33.34, 49.94) * mm, "end": v(33.46, 50.11) * mm});
            skLineSegment(sketch, "E757", {"start": v(33.46, 50.11) * mm, "end": v(33.58, 50.28) * mm});
            skLineSegment(sketch, "E758", {"start": v(33.58, 50.28) * mm, "end": v(33.7, 50.45) * mm});
            skLineSegment(sketch, "E759", {"start": v(33.7, 50.45) * mm, "end": v(33.81, 50.63) * mm});
            skLineSegment(sketch, "E760", {"start": v(33.81, 50.63) * mm, "end": v(33.93, 50.8) * mm});
            skLineSegment(sketch, "E761", {"start": v(33.93, 50.8) * mm, "end": v(34.05, 50.97) * mm});
            skLineSegment(sketch, "E762", {"start": v(34.05, 50.97) * mm, "end": v(34.17, 51.14) * mm});
            skLineSegment(sketch, "E763", {"start": v(34.17, 51.14) * mm, "end": v(34.28, 51.31) * mm});
            skLineSegment(sketch, "E764", {"start": v(34.28, 51.31) * mm, "end": v(34.4, 51.48) * mm});
            skLineSegment(sketch, "E765", {"start": v(34.4, 51.48) * mm, "end": v(34.52, 51.65) * mm});
            skLineSegment(sketch, "E766", {"start": v(34.52, 51.65) * mm, "end": v(34.64, 51.84) * mm});
            skLineSegment(sketch, "E767", {"start": v(34.64, 51.84) * mm, "end": v(34.73, 52.03) * mm});
            skLineSegment(sketch, "E768", {"start": v(34.73, 52.03) * mm, "end": v(34.76, 52.25) * mm});
            skLineSegment(sketch, "E769", {"start": v(34.76, 52.25) * mm, "end": v(34.74, 52.46) * mm});
            skLineSegment(sketch, "E770", {"start": v(34.74, 52.46) * mm, "end": v(34.66, 52.66) * mm});
            skLineSegment(sketch, "E771", {"start": v(34.66, 52.66) * mm, "end": v(34.53, 52.83) * mm});
            skLineSegment(sketch, "E772", {"start": v(34.53, 52.83) * mm, "end": v(34.36, 52.96) * mm});
            skLineSegment(sketch, "E773", {"start": v(34.36, 52.96) * mm, "end": v(34.16, 53.05) * mm});
            skLineSegment(sketch, "E774", {"start": v(34.16, 53.05) * mm, "end": v(33.95, 53.08) * mm});
            skLineSegment(sketch, "E775", {"start": v(33.95, 53.08) * mm, "end": v(33.74, 53.05) * mm});
            skLineSegment(sketch, "E776", {"start": v(33.74, 53.05) * mm, "end": v(33.54, 52.97) * mm});
            skLineSegment(sketch, "E777", {"start": v(33.54, 52.97) * mm, "end": v(33.37, 52.84) * mm});
            skLineSegment(sketch, "E778", {"start": v(33.37, 52.84) * mm, "end": v(33.24, 52.68) * mm});
            skLineSegment(sketch, "E779", {"start": v(33.24, 52.68) * mm, "end": v(33.13, 52.5) * mm});
            skLineSegment(sketch, "E780", {"start": v(33.13, 52.5) * mm, "end": v(33.02, 52.34) * mm});
            skLineSegment(sketch, "E781", {"start": v(33.02, 52.34) * mm, "end": v(32.9, 52.16) * mm});
            skLineSegment(sketch, "E782", {"start": v(32.9, 52.16) * mm, "end": v(32.8, 52) * mm});
            skLineSegment(sketch, "E783", {"start": v(32.8, 52) * mm, "end": v(32.68, 51.81) * mm});
            skLineSegment(sketch, "E784", {"start": v(32.68, 51.81) * mm, "end": v(32.56, 51.64) * mm});
            skLineSegment(sketch, "E785", {"start": v(32.56, 51.64) * mm, "end": v(32.45, 51.47) * mm});
            skLineSegment(sketch, "E786", {"start": v(32.45, 51.47) * mm, "end": v(32.34, 51.3) * mm});
            skLineSegment(sketch, "E787", {"start": v(32.34, 51.3) * mm, "end": v(32.22, 51.12) * mm});
            skLineSegment(sketch, "E788", {"start": v(32.22, 51.12) * mm, "end": v(32.11, 50.95) * mm});
            skLineSegment(sketch, "E789", {"start": v(32.11, 50.95) * mm, "end": v(32, 50.77) * mm});
            skLineSegment(sketch, "E790", {"start": v(32, 50.77) * mm, "end": v(31.89, 50.6) * mm});
            skLineSegment(sketch, "E791", {"start": v(31.89, 50.6) * mm, "end": v(31.8, 50.47) * mm});
            skLineSegment(sketch, "E792", {"start": v(31.8, 50.47) * mm, "end": v(31.63, 50.58) * mm});
            skLineSegment(sketch, "E793", {"start": v(31.63, 50.58) * mm, "end": v(31.45, 50.69) * mm});
            skLineSegment(sketch, "E794", {"start": v(31.45, 50.69) * mm, "end": v(31.28, 50.8) * mm});
            skLineSegment(sketch, "E795", {"start": v(31.28, 50.8) * mm, "end": v(31.1, 50.9) * mm});
            skLineSegment(sketch, "E796", {"start": v(31.1, 50.9) * mm, "end": v(30.93, 51.01) * mm});
            skLineSegment(sketch, "E797", {"start": v(30.93, 51.01) * mm, "end": v(30.75, 51.12) * mm});
            skLineSegment(sketch, "E798", {"start": v(30.75, 51.12) * mm, "end": v(30.58, 51.23) * mm});
            skLineSegment(sketch, "E799", {"start": v(30.58, 51.23) * mm, "end": v(30.4, 51.34) * mm});
            skLineSegment(sketch, "E800", {"start": v(30.4, 51.34) * mm, "end": v(30.23, 51.45) * mm});
            skLineSegment(sketch, "E801", {"start": v(30.23, 51.45) * mm, "end": v(30.05, 51.56) * mm});
            skLineSegment(sketch, "E802", {"start": v(30.05, 51.56) * mm, "end": v(29.88, 51.67) * mm});
            skLineSegment(sketch, "E803", {"start": v(29.88, 51.67) * mm, "end": v(29.8, 51.72) * mm});
            skLineSegment(sketch, "E804", {"start": v(29.8, 51.72) * mm, "end": v(29.9, 51.9) * mm});
            skLineSegment(sketch, "E805", {"start": v(29.9, 51.9) * mm, "end": v(30, 52.08) * mm});
            skLineSegment(sketch, "E806", {"start": v(30, 52.08) * mm, "end": v(30.1, 52.26) * mm});
            skLineSegment(sketch, "E807", {"start": v(30.1, 52.26) * mm, "end": v(30.21, 52.43) * mm});
            skLineSegment(sketch, "E808", {"start": v(30.21, 52.43) * mm, "end": v(30.32, 52.61) * mm});
            skLineSegment(sketch, "E809", {"start": v(30.32, 52.61) * mm, "end": v(30.43, 52.8) * mm});
            skLineSegment(sketch, "E810", {"start": v(30.43, 52.8) * mm, "end": v(30.53, 52.97) * mm});
            skLineSegment(sketch, "E811", {"start": v(30.53, 52.97) * mm, "end": v(30.64, 53.15) * mm});
            skLineSegment(sketch, "E812", {"start": v(30.64, 53.15) * mm, "end": v(30.75, 53.33) * mm});
            skLineSegment(sketch, "E813", {"start": v(30.75, 53.33) * mm, "end": v(30.85, 53.5) * mm});
            skLineSegment(sketch, "E814", {"start": v(30.85, 53.5) * mm, "end": v(30.96, 53.68) * mm});
            skLineSegment(sketch, "E815", {"start": v(30.96, 53.68) * mm, "end": v(31.07, 53.87) * mm});
            skLineSegment(sketch, "E816", {"start": v(31.07, 53.87) * mm, "end": v(31.18, 54.06) * mm});
            skLineSegment(sketch, "E817", {"start": v(31.18, 54.06) * mm, "end": v(31.25, 54.26) * mm});
            skLineSegment(sketch, "E818", {"start": v(31.25, 54.26) * mm, "end": v(31.27, 54.47) * mm});
            skLineSegment(sketch, "E819", {"start": v(31.27, 54.47) * mm, "end": v(31.23, 54.68) * mm});
            skLineSegment(sketch, "E820", {"start": v(31.23, 54.68) * mm, "end": v(31.14, 54.88) * mm});
            skLineSegment(sketch, "E821", {"start": v(31.14, 54.88) * mm, "end": v(31, 55.04) * mm});
            skLineSegment(sketch, "E822", {"start": v(31, 55.04) * mm, "end": v(30.82, 55.16) * mm});
            skLineSegment(sketch, "E823", {"start": v(30.82, 55.16) * mm, "end": v(30.62, 55.23) * mm});
            skLineSegment(sketch, "E824", {"start": v(30.62, 55.23) * mm, "end": v(30.45, 55.25) * mm});
            skLineSegment(sketch, "E825", {"start": v(30.45, 55.25) * mm, "end": v(30.24, 55.22) * mm});
            skLineSegment(sketch, "E826", {"start": v(30.24, 55.22) * mm, "end": v(30.04, 55.14) * mm});
            skLineSegment(sketch, "E827", {"start": v(30.04, 55.14) * mm, "end": v(29.87, 55) * mm});
            skLineSegment(sketch, "E828", {"start": v(29.87, 55) * mm, "end": v(29.74, 54.84) * mm});
            skLineSegment(sketch, "E829", {"start": v(29.74, 54.84) * mm, "end": v(29.64, 54.66) * mm});
            skLineSegment(sketch, "E830", {"start": v(29.64, 54.66) * mm, "end": v(29.54, 54.48) * mm});
            skLineSegment(sketch, "E831", {"start": v(29.54, 54.48) * mm, "end": v(29.43, 54.3) * mm});
            skLineSegment(sketch, "E832", {"start": v(29.43, 54.3) * mm, "end": v(29.33, 54.11) * mm});
            skLineSegment(sketch, "E833", {"start": v(29.33, 54.11) * mm, "end": v(29.23, 53.93) * mm});
            skLineSegment(sketch, "E834", {"start": v(29.23, 53.93) * mm, "end": v(29.13, 53.75) * mm});
            skLineSegment(sketch, "E835", {"start": v(29.13, 53.75) * mm, "end": v(29.03, 53.57) * mm});
            skLineSegment(sketch, "E836", {"start": v(29.03, 53.57) * mm, "end": v(28.93, 53.39) * mm});
            skLineSegment(sketch, "E837", {"start": v(28.93, 53.39) * mm, "end": v(28.82, 53.2) * mm});
            skLineSegment(sketch, "E838", {"start": v(28.82, 53.2) * mm, "end": v(28.72, 53.03) * mm});
            skLineSegment(sketch, "E839", {"start": v(28.72, 53.03) * mm, "end": v(28.62, 52.85) * mm});
            skLineSegment(sketch, "E840", {"start": v(28.62, 52.85) * mm, "end": v(28.52, 52.66) * mm});
            skLineSegment(sketch, "E841", {"start": v(28.52, 52.66) * mm, "end": v(28.43, 52.5) * mm});
            skLineSegment(sketch, "E842", {"start": v(28.43, 52.5) * mm, "end": v(28.25, 52.6) * mm});
            skLineSegment(sketch, "E843", {"start": v(28.25, 52.6) * mm, "end": v(28.07, 52.7) * mm});
            skLineSegment(sketch, "E844", {"start": v(28.07, 52.7) * mm, "end": v(27.89, 52.8) * mm});
            skLineSegment(sketch, "E845", {"start": v(27.89, 52.8) * mm, "end": v(27.7, 52.9) * mm});
            skLineSegment(sketch, "E846", {"start": v(27.7, 52.9) * mm, "end": v(27.52, 53) * mm});
            skLineSegment(sketch, "E847", {"start": v(27.52, 53) * mm, "end": v(27.34, 53.09) * mm});
            skLineSegment(sketch, "E848", {"start": v(27.34, 53.09) * mm, "end": v(27.16, 53.19) * mm});
            skLineSegment(sketch, "E849", {"start": v(27.16, 53.19) * mm, "end": v(26.98, 53.28) * mm});
            skLineSegment(sketch, "E850", {"start": v(26.98, 53.28) * mm, "end": v(26.8, 53.38) * mm});
            skLineSegment(sketch, "E851", {"start": v(26.8, 53.38) * mm, "end": v(26.62, 53.48) * mm});
            skLineSegment(sketch, "E852", {"start": v(26.62, 53.48) * mm, "end": v(26.43, 53.57) * mm});
            skLineSegment(sketch, "E853", {"start": v(26.43, 53.57) * mm, "end": v(26.34, 53.62) * mm});
            skLineSegment(sketch, "E854", {"start": v(26.34, 53.62) * mm, "end": v(26.43, 53.8) * mm});
            skLineSegment(sketch, "E855", {"start": v(26.43, 53.8) * mm, "end": v(26.53, 54) * mm});
            skLineSegment(sketch, "E856", {"start": v(26.53, 54) * mm, "end": v(26.62, 54.18) * mm});
            skLineSegment(sketch, "E857", {"start": v(26.62, 54.18) * mm, "end": v(26.72, 54.36) * mm});
            skLineSegment(sketch, "E858", {"start": v(26.72, 54.36) * mm, "end": v(26.81, 54.55) * mm});
            skLineSegment(sketch, "E859", {"start": v(26.81, 54.55) * mm, "end": v(26.9, 54.73) * mm});
            skLineSegment(sketch, "E860", {"start": v(26.9, 54.73) * mm, "end": v(27, 54.92) * mm});
            skLineSegment(sketch, "E861", {"start": v(27, 54.92) * mm, "end": v(27.1, 55.1) * mm});
            skLineSegment(sketch, "E862", {"start": v(27.1, 55.1) * mm, "end": v(27.2, 55.3) * mm});
            skLineSegment(sketch, "E863", {"start": v(27.2, 55.3) * mm, "end": v(27.28, 55.47) * mm});
            skLineSegment(sketch, "E864", {"start": v(27.28, 55.47) * mm, "end": v(27.38, 55.66) * mm});
            skLineSegment(sketch, "E865", {"start": v(27.38, 55.66) * mm, "end": v(27.47, 55.85) * mm});
            skLineSegment(sketch, "E866", {"start": v(27.47, 55.85) * mm, "end": v(27.57, 56.04) * mm});
            skLineSegment(sketch, "E867", {"start": v(27.57, 56.04) * mm, "end": v(27.63, 56.25) * mm});
            skLineSegment(sketch, "E868", {"start": v(27.63, 56.25) * mm, "end": v(27.64, 56.46) * mm});
            skLineSegment(sketch, "E869", {"start": v(27.64, 56.46) * mm, "end": v(27.58, 56.67) * mm});
            skLineSegment(sketch, "E870", {"start": v(27.58, 56.67) * mm, "end": v(27.48, 56.86) * mm});
            skLineSegment(sketch, "E871", {"start": v(27.48, 56.86) * mm, "end": v(27.33, 57.01) * mm});
            skLineSegment(sketch, "E872", {"start": v(27.33, 57.01) * mm, "end": v(27.15, 57.12) * mm});
            skLineSegment(sketch, "E873", {"start": v(27.15, 57.12) * mm, "end": v(26.94, 57.18) * mm});
            skLineSegment(sketch, "E874", {"start": v(26.94, 57.18) * mm, "end": v(26.8, 57.19) * mm});
            skLineSegment(sketch, "E875", {"start": v(26.8, 57.19) * mm, "end": v(26.6, 57.16) * mm});
            skLineSegment(sketch, "E876", {"start": v(26.6, 57.16) * mm, "end": v(26.4, 57.07) * mm});
            skLineSegment(sketch, "E877", {"start": v(26.4, 57.07) * mm, "end": v(26.23, 56.94) * mm});
            skLineSegment(sketch, "E878", {"start": v(26.23, 56.94) * mm, "end": v(26.1, 56.77) * mm});
            skLineSegment(sketch, "E879", {"start": v(26.1, 56.77) * mm, "end": v(26, 56.57) * mm});
            skLineSegment(sketch, "E880", {"start": v(26, 56.57) * mm, "end": v(25.92, 56.38) * mm});
            skLineSegment(sketch, "E881", {"start": v(25.92, 56.38) * mm, "end": v(25.83, 56.2) * mm});
            skLineSegment(sketch, "E882", {"start": v(25.83, 56.2) * mm, "end": v(25.74, 56) * mm});
            skLineSegment(sketch, "E883", {"start": v(25.74, 56) * mm, "end": v(25.65, 55.82) * mm});
            skLineSegment(sketch, "E884", {"start": v(25.65, 55.82) * mm, "end": v(25.56, 55.63) * mm});
            skLineSegment(sketch, "E885", {"start": v(25.56, 55.63) * mm, "end": v(25.47, 55.44) * mm});
            skLineSegment(sketch, "E886", {"start": v(25.47, 55.44) * mm, "end": v(25.38, 55.26) * mm});
            skLineSegment(sketch, "E887", {"start": v(25.38, 55.26) * mm, "end": v(25.3, 55.07) * mm});
            skLineSegment(sketch, "E888", {"start": v(25.3, 55.07) * mm, "end": v(25.2, 54.88) * mm});
            skLineSegment(sketch, "E889", {"start": v(25.2, 54.88) * mm, "end": v(25.11, 54.7) * mm});
            skLineSegment(sketch, "E890", {"start": v(25.11, 54.7) * mm, "end": v(25.03, 54.5) * mm});
            skLineSegment(sketch, "E891", {"start": v(25.03, 54.5) * mm, "end": v(24.94, 54.32) * mm});
            skLineSegment(sketch, "E892", {"start": v(24.94, 54.32) * mm, "end": v(24.75, 54.4) * mm});
            skLineSegment(sketch, "E893", {"start": v(24.75, 54.4) * mm, "end": v(24.56, 54.49) * mm});
            skLineSegment(sketch, "E894", {"start": v(24.56, 54.49) * mm, "end": v(24.37, 54.57) * mm});
            skLineSegment(sketch, "E895", {"start": v(24.37, 54.57) * mm, "end": v(24.18, 54.66) * mm});
            skLineSegment(sketch, "E896", {"start": v(24.18, 54.66) * mm, "end": v(24, 54.74) * mm});
            skLineSegment(sketch, "E897", {"start": v(24, 54.74) * mm, "end": v(23.8, 54.83) * mm});
            skLineSegment(sketch, "E898", {"start": v(23.8, 54.83) * mm, "end": v(23.62, 54.91) * mm});
            skLineSegment(sketch, "E899", {"start": v(23.62, 54.91) * mm, "end": v(23.43, 55) * mm});
            skLineSegment(sketch, "E900", {"start": v(23.43, 55) * mm, "end": v(23.25, 55.08) * mm});
            skLineSegment(sketch, "E901", {"start": v(23.25, 55.08) * mm, "end": v(23.06, 55.17) * mm});
            skLineSegment(sketch, "E902", {"start": v(23.06, 55.17) * mm, "end": v(22.87, 55.25) * mm});
            skLineSegment(sketch, "E903", {"start": v(22.87, 55.25) * mm, "end": v(22.78, 55.3) * mm});
            skLineSegment(sketch, "E904", {"start": v(22.78, 55.3) * mm, "end": v(22.86, 55.48) * mm});
            skLineSegment(sketch, "E905", {"start": v(22.86, 55.48) * mm, "end": v(22.94, 55.67) * mm});
            skLineSegment(sketch, "E906", {"start": v(22.94, 55.67) * mm, "end": v(23.02, 55.87) * mm});
            skLineSegment(sketch, "E907", {"start": v(23.02, 55.87) * mm, "end": v(23.1, 56.06) * mm});
            skLineSegment(sketch, "E908", {"start": v(23.1, 56.06) * mm, "end": v(23.18, 56.25) * mm});
            skLineSegment(sketch, "E909", {"start": v(23.18, 56.25) * mm, "end": v(23.27, 56.44) * mm});
            skLineSegment(sketch, "E910", {"start": v(23.27, 56.44) * mm, "end": v(23.35, 56.63) * mm});
            skLineSegment(sketch, "E911", {"start": v(23.35, 56.63) * mm, "end": v(23.43, 56.82) * mm});
            skLineSegment(sketch, "E912", {"start": v(23.43, 56.82) * mm, "end": v(23.51, 57.01) * mm});
            skLineSegment(sketch, "E913", {"start": v(23.51, 57.01) * mm, "end": v(23.6, 57.2) * mm});
            skLineSegment(sketch, "E914", {"start": v(23.6, 57.2) * mm, "end": v(23.68, 57.4) * mm});
            skLineSegment(sketch, "E915", {"start": v(23.68, 57.4) * mm, "end": v(23.76, 57.59) * mm});
            skLineSegment(sketch, "E916", {"start": v(23.76, 57.59) * mm, "end": v(23.85, 57.8) * mm});
            skLineSegment(sketch, "E917", {"start": v(23.85, 57.8) * mm, "end": v(23.9, 58) * mm});
            skLineSegment(sketch, "E918", {"start": v(23.9, 58) * mm, "end": v(23.88, 58.21) * mm});
            skLineSegment(sketch, "E919", {"start": v(23.88, 58.21) * mm, "end": v(23.82, 58.42) * mm});
            skLineSegment(sketch, "E920", {"start": v(23.82, 58.42) * mm, "end": v(23.7, 58.6) * mm});
            skLineSegment(sketch, "E921", {"start": v(23.7, 58.6) * mm, "end": v(23.54, 58.74) * mm});
            skLineSegment(sketch, "E922", {"start": v(23.54, 58.74) * mm, "end": v(23.35, 58.84) * mm});
            skLineSegment(sketch, "E923", {"start": v(23.35, 58.84) * mm, "end": v(23.14, 58.89) * mm});
            skLineSegment(sketch, "E924", {"start": v(23.14, 58.89) * mm, "end": v(23.1, 58.89) * mm});
            skLineSegment(sketch, "E925", {"start": v(23.1, 58.89) * mm, "end": v(22.88, 58.86) * mm});
            skLineSegment(sketch, "E926", {"start": v(22.88, 58.86) * mm, "end": v(22.68, 58.79) * mm});
            skLineSegment(sketch, "E927", {"start": v(22.68, 58.79) * mm, "end": v(22.5, 58.66) * mm});
            skLineSegment(sketch, "E928", {"start": v(22.5, 58.66) * mm, "end": v(22.38, 58.5) * mm});
            skLineSegment(sketch, "E929", {"start": v(22.38, 58.5) * mm, "end": v(22.28, 58.3) * mm});
            skLineSegment(sketch, "E930", {"start": v(22.28, 58.3) * mm, "end": v(22.2, 58.1) * mm});
            skLineSegment(sketch, "E931", {"start": v(22.2, 58.1) * mm, "end": v(22.13, 57.91) * mm});
            skLineSegment(sketch, "E932", {"start": v(22.13, 57.91) * mm, "end": v(22.05, 57.72) * mm});
            skLineSegment(sketch, "E933", {"start": v(22.05, 57.72) * mm, "end": v(21.98, 57.52) * mm});
            skLineSegment(sketch, "E934", {"start": v(21.98, 57.52) * mm, "end": v(21.9, 57.33) * mm});
            skLineSegment(sketch, "E935", {"start": v(21.9, 57.33) * mm, "end": v(21.82, 57.14) * mm});
            skLineSegment(sketch, "E936", {"start": v(21.82, 57.14) * mm, "end": v(21.75, 56.95) * mm});
            skLineSegment(sketch, "E937", {"start": v(21.75, 56.95) * mm, "end": v(21.67, 56.75) * mm});
            skLineSegment(sketch, "E938", {"start": v(21.67, 56.75) * mm, "end": v(21.6, 56.56) * mm});
            skLineSegment(sketch, "E939", {"start": v(21.6, 56.56) * mm, "end": v(21.51, 56.37) * mm});
            skLineSegment(sketch, "E940", {"start": v(21.51, 56.37) * mm, "end": v(21.44, 56.17) * mm});
            skLineSegment(sketch, "E941", {"start": v(21.44, 56.17) * mm, "end": v(21.36, 55.98) * mm});
            skLineSegment(sketch, "E942", {"start": v(21.36, 55.98) * mm, "end": v(21.33, 55.9) * mm});
            skLineSegment(sketch, "E943", {"start": v(21.33, 55.9) * mm, "end": v(21.13, 55.97) * mm});
            skLineSegment(sketch, "E944", {"start": v(21.13, 55.97) * mm, "end": v(20.94, 56.04) * mm});
            skLineSegment(sketch, "E945", {"start": v(20.94, 56.04) * mm, "end": v(20.75, 56.11) * mm});
            skLineSegment(sketch, "E946", {"start": v(20.75, 56.11) * mm, "end": v(20.56, 56.19) * mm});
            skLineSegment(sketch, "E947", {"start": v(20.56, 56.19) * mm, "end": v(20.36, 56.26) * mm});
            skLineSegment(sketch, "E948", {"start": v(20.36, 56.26) * mm, "end": v(20.17, 56.33) * mm});
            skLineSegment(sketch, "E949", {"start": v(20.17, 56.33) * mm, "end": v(19.98, 56.4) * mm});
            skLineSegment(sketch, "E950", {"start": v(19.98, 56.4) * mm, "end": v(19.79, 56.48) * mm});
            skLineSegment(sketch, "E951", {"start": v(19.79, 56.48) * mm, "end": v(19.6, 56.55) * mm});
            skLineSegment(sketch, "E952", {"start": v(19.6, 56.55) * mm, "end": v(19.4, 56.62) * mm});
            skLineSegment(sketch, "E953", {"start": v(19.4, 56.62) * mm, "end": v(19.2, 56.7) * mm});
            skLineSegment(sketch, "E954", {"start": v(19.2, 56.7) * mm, "end": v(19.1, 56.73) * mm});
            skLineSegment(sketch, "E955", {"start": v(19.1, 56.73) * mm, "end": v(19.18, 56.92) * mm});
            skLineSegment(sketch, "E956", {"start": v(19.18, 56.92) * mm, "end": v(19.25, 57.12) * mm});
            skLineSegment(sketch, "E957", {"start": v(19.25, 57.12) * mm, "end": v(19.32, 57.32) * mm});
            skLineSegment(sketch, "E958", {"start": v(19.32, 57.32) * mm, "end": v(19.39, 57.51) * mm});
            skLineSegment(sketch, "E959", {"start": v(19.39, 57.51) * mm, "end": v(19.45, 57.7) * mm});
            skLineSegment(sketch, "E960", {"start": v(19.45, 57.7) * mm, "end": v(19.52, 57.9) * mm});
            skLineSegment(sketch, "E961", {"start": v(19.52, 57.9) * mm, "end": v(19.6, 58.1) * mm});
            skLineSegment(sketch, "E962", {"start": v(19.6, 58.1) * mm, "end": v(19.66, 58.3) * mm});
            skLineSegment(sketch, "E963", {"start": v(19.66, 58.3) * mm, "end": v(19.73, 58.5) * mm});
            skLineSegment(sketch, "E964", {"start": v(19.73, 58.5) * mm, "end": v(19.8, 58.69) * mm});
            skLineSegment(sketch, "E965", {"start": v(19.8, 58.69) * mm, "end": v(19.87, 58.88) * mm});
            skLineSegment(sketch, "E966", {"start": v(19.87, 58.88) * mm, "end": v(19.94, 59.08) * mm});
            skLineSegment(sketch, "E967", {"start": v(19.94, 59.08) * mm, "end": v(20.01, 59.3) * mm});
            skLineSegment(sketch, "E968", {"start": v(20.01, 59.3) * mm, "end": v(20.05, 59.5) * mm});
            skLineSegment(sketch, "E969", {"start": v(20.05, 59.5) * mm, "end": v(20.02, 59.72) * mm});
            skLineSegment(sketch, "E970", {"start": v(20.02, 59.72) * mm, "end": v(19.94, 59.92) * mm});
            skLineSegment(sketch, "E971", {"start": v(19.94, 59.92) * mm, "end": v(19.81, 60.09) * mm});
            skLineSegment(sketch, "E972", {"start": v(19.81, 60.09) * mm, "end": v(19.65, 60.22) * mm});
            skLineSegment(sketch, "E973", {"start": v(19.65, 60.22) * mm, "end": v(19.45, 60.3) * mm});
            skLineSegment(sketch, "E974", {"start": v(19.45, 60.3) * mm, "end": v(19.24, 60.34) * mm});
            skLineSegment(sketch, "E975", {"start": v(19.24, 60.34) * mm, "end": v(19.02, 60.31) * mm});
            skLineSegment(sketch, "E976", {"start": v(19.02, 60.31) * mm, "end": v(18.82, 60.23) * mm});
            skLineSegment(sketch, "E977", {"start": v(18.82, 60.23) * mm, "end": v(18.65, 60.1) * mm});
            skLineSegment(sketch, "E978", {"start": v(18.65, 60.1) * mm, "end": v(18.52, 59.93) * mm});
            skLineSegment(sketch, "E979", {"start": v(18.52, 59.93) * mm, "end": v(18.44, 59.74) * mm});
            skLineSegment(sketch, "E980", {"start": v(18.44, 59.74) * mm, "end": v(18.38, 59.55) * mm});
            skLineSegment(sketch, "E981", {"start": v(18.38, 59.55) * mm, "end": v(18.31, 59.35) * mm});
            skLineSegment(sketch, "E982", {"start": v(18.31, 59.35) * mm, "end": v(18.25, 59.16) * mm});
            skLineSegment(sketch, "E983", {"start": v(18.25, 59.16) * mm, "end": v(18.18, 58.96) * mm});
            skLineSegment(sketch, "E984", {"start": v(18.18, 58.96) * mm, "end": v(18.12, 58.76) * mm});
            skLineSegment(sketch, "E985", {"start": v(18.12, 58.76) * mm, "end": v(18.06, 58.56) * mm});
            skLineSegment(sketch, "E986", {"start": v(18.06, 58.56) * mm, "end": v(18, 58.37) * mm});
            skLineSegment(sketch, "E987", {"start": v(18, 58.37) * mm, "end": v(17.93, 58.17) * mm});
            skLineSegment(sketch, "E988", {"start": v(17.93, 58.17) * mm, "end": v(17.86, 57.97) * mm});
            skLineSegment(sketch, "E989", {"start": v(17.86, 57.97) * mm, "end": v(17.8, 57.77) * mm});
            skLineSegment(sketch, "E990", {"start": v(17.8, 57.77) * mm, "end": v(17.73, 57.57) * mm});
            skLineSegment(sketch, "E991", {"start": v(17.73, 57.57) * mm, "end": v(17.67, 57.38) * mm});
            skLineSegment(sketch, "E992", {"start": v(17.67, 57.38) * mm, "end": v(17.62, 57.23) * mm});
            skLineSegment(sketch, "E993", {"start": v(17.62, 57.23) * mm, "end": v(17.43, 57.3) * mm});
            skLineSegment(sketch, "E994", {"start": v(17.43, 57.3) * mm, "end": v(17.23, 57.35) * mm});
            skLineSegment(sketch, "E995", {"start": v(17.23, 57.35) * mm, "end": v(17.03, 57.41) * mm});
            skLineSegment(sketch, "E996", {"start": v(17.03, 57.41) * mm, "end": v(16.84, 57.47) * mm});
            skLineSegment(sketch, "E997", {"start": v(16.84, 57.47) * mm, "end": v(16.64, 57.53) * mm});
            skLineSegment(sketch, "E998", {"start": v(16.64, 57.53) * mm, "end": v(16.44, 57.6) * mm});
            skLineSegment(sketch, "E999", {"start": v(16.44, 57.6) * mm, "end": v(16.24, 57.65) * mm});
            skLineSegment(sketch, "E1000", {"start": v(16.24, 57.65) * mm, "end": v(16.05, 57.71) * mm});
            skLineSegment(sketch, "E1001", {"start": v(16.05, 57.71) * mm, "end": v(15.85, 57.77) * mm});
            skLineSegment(sketch, "E1002", {"start": v(15.85, 57.77) * mm, "end": v(15.65, 57.83) * mm});
            skLineSegment(sketch, "E1003", {"start": v(15.65, 57.83) * mm, "end": v(15.46, 57.9) * mm});
            skLineSegment(sketch, "E1004", {"start": v(15.46, 57.9) * mm, "end": v(15.35, 57.92) * mm});
            skLineSegment(sketch, "E1005", {"start": v(15.35, 57.92) * mm, "end": v(15.41, 58.12) * mm});
            skLineSegment(sketch, "E1006", {"start": v(15.41, 58.12) * mm, "end": v(15.47, 58.32) * mm});
            skLineSegment(sketch, "E1007", {"start": v(15.47, 58.32) * mm, "end": v(15.52, 58.52) * mm});
            skLineSegment(sketch, "E1008", {"start": v(15.52, 58.52) * mm, "end": v(15.58, 58.72) * mm});
            skLineSegment(sketch, "E1009", {"start": v(15.58, 58.72) * mm, "end": v(15.64, 58.92) * mm});
            skLineSegment(sketch, "E1010", {"start": v(15.64, 58.92) * mm, "end": v(15.7, 59.12) * mm});
            skLineSegment(sketch, "E1011", {"start": v(15.7, 59.12) * mm, "end": v(15.75, 59.32) * mm});
            skLineSegment(sketch, "E1012", {"start": v(15.75, 59.32) * mm, "end": v(15.8, 59.52) * mm});
            skLineSegment(sketch, "E1013", {"start": v(15.8, 59.52) * mm, "end": v(15.86, 59.72) * mm});
            skLineSegment(sketch, "E1014", {"start": v(15.86, 59.72) * mm, "end": v(15.92, 59.92) * mm});
            skLineSegment(sketch, "E1015", {"start": v(15.92, 59.92) * mm, "end": v(15.97, 60.12) * mm});
            skLineSegment(sketch, "E1016", {"start": v(15.97, 60.12) * mm, "end": v(16.03, 60.32) * mm});
            skLineSegment(sketch, "E1017", {"start": v(16.03, 60.32) * mm, "end": v(16.1, 60.54) * mm});
            skLineSegment(sketch, "E1018", {"start": v(16.1, 60.54) * mm, "end": v(16.1, 60.75) * mm});
            skLineSegment(sketch, "E1019", {"start": v(16.1, 60.75) * mm, "end": v(16.07, 60.96) * mm});
            skLineSegment(sketch, "E1020", {"start": v(16.07, 60.96) * mm, "end": v(15.98, 61.16) * mm});
            skLineSegment(sketch, "E1021", {"start": v(15.98, 61.16) * mm, "end": v(15.84, 61.32) * mm});
            skLineSegment(sketch, "E1022", {"start": v(15.84, 61.32) * mm, "end": v(15.66, 61.44) * mm});
            skLineSegment(sketch, "E1023", {"start": v(15.66, 61.44) * mm, "end": v(15.46, 61.51) * mm});
            skLineSegment(sketch, "E1024", {"start": v(15.46, 61.51) * mm, "end": v(15.29, 61.53) * mm});
            skLineSegment(sketch, "E1025", {"start": v(15.29, 61.53) * mm, "end": v(15.08, 61.5) * mm});
            skLineSegment(sketch, "E1026", {"start": v(15.08, 61.5) * mm, "end": v(14.88, 61.42) * mm});
            skLineSegment(sketch, "E1027", {"start": v(14.88, 61.42) * mm, "end": v(14.7, 61.29) * mm});
            skLineSegment(sketch, "E1028", {"start": v(14.7, 61.29) * mm, "end": v(14.58, 61.12) * mm});
            skLineSegment(sketch, "E1029", {"start": v(14.58, 61.12) * mm, "end": v(14.5, 60.92) * mm});
            skLineSegment(sketch, "E1030", {"start": v(14.5, 60.92) * mm, "end": v(14.45, 60.72) * mm});
            skLineSegment(sketch, "E1031", {"start": v(14.45, 60.72) * mm, "end": v(14.4, 60.52) * mm});
            skLineSegment(sketch, "E1032", {"start": v(14.4, 60.52) * mm, "end": v(14.34, 60.31) * mm});
            skLineSegment(sketch, "E1033", {"start": v(14.34, 60.31) * mm, "end": v(14.3, 60.11) * mm});
            skLineSegment(sketch, "E1034", {"start": v(14.3, 60.11) * mm, "end": v(14.24, 59.91) * mm});
            skLineSegment(sketch, "E1035", {"start": v(14.24, 59.91) * mm, "end": v(14.2, 59.7) * mm});
            skLineSegment(sketch, "E1036", {"start": v(14.2, 59.7) * mm, "end": v(14.14, 59.51) * mm});
            skLineSegment(sketch, "E1037", {"start": v(14.14, 59.51) * mm, "end": v(14.09, 59.31) * mm});
            skLineSegment(sketch, "E1038", {"start": v(14.09, 59.31) * mm, "end": v(14.04, 59.1) * mm});
            skLineSegment(sketch, "E1039", {"start": v(14.04, 59.1) * mm, "end": v(13.99, 58.9) * mm});
            skLineSegment(sketch, "E1040", {"start": v(13.99, 58.9) * mm, "end": v(13.94, 58.7) * mm});
            skLineSegment(sketch, "E1041", {"start": v(13.94, 58.7) * mm, "end": v(13.88, 58.5) * mm});
            skLineSegment(sketch, "E1042", {"start": v(13.88, 58.5) * mm, "end": v(13.84, 58.33) * mm});
            skLineSegment(sketch, "E1043", {"start": v(13.84, 58.33) * mm, "end": v(13.64, 58.38) * mm});
            skLineSegment(sketch, "E1044", {"start": v(13.64, 58.38) * mm, "end": v(13.44, 58.42) * mm});
            skLineSegment(sketch, "E1045", {"start": v(13.44, 58.42) * mm, "end": v(13.24, 58.47) * mm});
            skLineSegment(sketch, "E1046", {"start": v(13.24, 58.47) * mm, "end": v(13.04, 58.52) * mm});
            skLineSegment(sketch, "E1047", {"start": v(13.04, 58.52) * mm, "end": v(12.84, 58.56) * mm});
            skLineSegment(sketch, "E1048", {"start": v(12.84, 58.56) * mm, "end": v(12.64, 58.6) * mm});
            skLineSegment(sketch, "E1049", {"start": v(12.64, 58.6) * mm, "end": v(12.44, 58.66) * mm});
            skLineSegment(sketch, "E1050", {"start": v(12.44, 58.66) * mm, "end": v(12.24, 58.7) * mm});
            skLineSegment(sketch, "E1051", {"start": v(12.24, 58.7) * mm, "end": v(12.04, 58.75) * mm});
            skLineSegment(sketch, "E1052", {"start": v(12.04, 58.75) * mm, "end": v(11.83, 58.8) * mm});
            skLineSegment(sketch, "E1053", {"start": v(11.83, 58.8) * mm, "end": v(11.63, 58.84) * mm});
            skLineSegment(sketch, "E1054", {"start": v(11.63, 58.84) * mm, "end": v(11.53, 58.87) * mm});
            skLineSegment(sketch, "E1055", {"start": v(11.53, 58.87) * mm, "end": v(11.57, 59.07) * mm});
            skLineSegment(sketch, "E1056", {"start": v(11.57, 59.07) * mm, "end": v(11.62, 59.27) * mm});
            skLineSegment(sketch, "E1057", {"start": v(11.62, 59.27) * mm, "end": v(11.66, 59.48) * mm});
            skLineSegment(sketch, "E1058", {"start": v(11.66, 59.48) * mm, "end": v(11.7, 59.68) * mm});
            skLineSegment(sketch, "E1059", {"start": v(11.7, 59.68) * mm, "end": v(11.75, 59.88) * mm});
            skLineSegment(sketch, "E1060", {"start": v(11.75, 59.88) * mm, "end": v(11.8, 60.09) * mm});
            skLineSegment(sketch, "E1061", {"start": v(11.8, 60.09) * mm, "end": v(11.83, 60.29) * mm});
            skLineSegment(sketch, "E1062", {"start": v(11.83, 60.29) * mm, "end": v(11.88, 60.49) * mm});
            skLineSegment(sketch, "E1063", {"start": v(11.88, 60.49) * mm, "end": v(11.92, 60.7) * mm});
            skLineSegment(sketch, "E1064", {"start": v(11.92, 60.7) * mm, "end": v(11.96, 60.9) * mm});
            skLineSegment(sketch, "E1065", {"start": v(11.96, 60.9) * mm, "end": v(12, 61.1) * mm});
            skLineSegment(sketch, "E1066", {"start": v(12, 61.1) * mm, "end": v(12.05, 61.3) * mm});
            skLineSegment(sketch, "E1067", {"start": v(12.05, 61.3) * mm, "end": v(12.1, 61.52) * mm});
            skLineSegment(sketch, "E1068", {"start": v(12.1, 61.52) * mm, "end": v(12.1, 61.74) * mm});
            skLineSegment(sketch, "E1069", {"start": v(12.1, 61.74) * mm, "end": v(12.05, 61.95) * mm});
            skLineSegment(sketch, "E1070", {"start": v(12.05, 61.95) * mm, "end": v(11.94, 62.13) * mm});
            skLineSegment(sketch, "E1071", {"start": v(11.94, 62.13) * mm, "end": v(11.8, 62.29) * mm});
            skLineSegment(sketch, "E1072", {"start": v(11.8, 62.29) * mm, "end": v(11.6, 62.4) * mm});
            skLineSegment(sketch, "E1073", {"start": v(11.6, 62.4) * mm, "end": v(11.4, 62.46) * mm});
            skLineSegment(sketch, "E1074", {"start": v(11.4, 62.46) * mm, "end": v(11.27, 62.46) * mm});
            skLineSegment(sketch, "E1075", {"start": v(11.27, 62.46) * mm, "end": v(11.06, 62.43) * mm});
            skLineSegment(sketch, "E1076", {"start": v(11.06, 62.43) * mm, "end": v(10.86, 62.35) * mm});
            skLineSegment(sketch, "E1077", {"start": v(10.86, 62.35) * mm, "end": v(10.7, 62.21) * mm});
            skLineSegment(sketch, "E1078", {"start": v(10.7, 62.21) * mm, "end": v(10.57, 62.04) * mm});
            skLineSegment(sketch, "E1079", {"start": v(10.57, 62.04) * mm, "end": v(10.5, 61.84) * mm});
            skLineSegment(sketch, "E1080", {"start": v(10.5, 61.84) * mm, "end": v(10.45, 61.63) * mm});
            skLineSegment(sketch, "E1081", {"start": v(10.45, 61.63) * mm, "end": v(10.41, 61.42) * mm});
            skLineSegment(sketch, "E1082", {"start": v(10.41, 61.42) * mm, "end": v(10.37, 61.22) * mm});
            skLineSegment(sketch, "E1083", {"start": v(10.37, 61.22) * mm, "end": v(10.33, 61.01) * mm});
            skLineSegment(sketch, "E1084", {"start": v(10.33, 61.01) * mm, "end": v(10.3, 60.8) * mm});
            skLineSegment(sketch, "E1085", {"start": v(10.3, 60.8) * mm, "end": v(10.26, 60.6) * mm});
            skLineSegment(sketch, "E1086", {"start": v(10.26, 60.6) * mm, "end": v(10.22, 60.4) * mm});
            skLineSegment(sketch, "E1087", {"start": v(10.22, 60.4) * mm, "end": v(10.18, 60.2) * mm});
            skLineSegment(sketch, "E1088", {"start": v(10.18, 60.2) * mm, "end": v(10.15, 60) * mm});
            skLineSegment(sketch, "E1089", {"start": v(10.15, 60) * mm, "end": v(10.1, 59.79) * mm});
            skLineSegment(sketch, "E1090", {"start": v(10.1, 59.79) * mm, "end": v(10.07, 59.58) * mm});
            skLineSegment(sketch, "E1091", {"start": v(10.07, 59.58) * mm, "end": v(10.03, 59.38) * mm});
            skLineSegment(sketch, "E1092", {"start": v(10.03, 59.38) * mm, "end": v(10, 59.17) * mm});
            skLineSegment(sketch, "E1093", {"start": v(10, 59.17) * mm, "end": v(9.8, 59.2) * mm});
            skLineSegment(sketch, "E1094", {"start": v(9.8, 59.2) * mm, "end": v(9.59, 59.24) * mm});
            skLineSegment(sketch, "E1095", {"start": v(9.59, 59.24) * mm, "end": v(9.38, 59.27) * mm});
            skLineSegment(sketch, "E1096", {"start": v(9.38, 59.27) * mm, "end": v(9.18, 59.3) * mm});
            skLineSegment(sketch, "E1097", {"start": v(9.18, 59.3) * mm, "end": v(8.98, 59.34) * mm});
            skLineSegment(sketch, "E1098", {"start": v(8.98, 59.34) * mm, "end": v(8.77, 59.37) * mm});
            skLineSegment(sketch, "E1099", {"start": v(8.77, 59.37) * mm, "end": v(8.57, 59.4) * mm});
            skLineSegment(sketch, "E1100", {"start": v(8.57, 59.4) * mm, "end": v(8.37, 59.44) * mm});
            skLineSegment(sketch, "E1101", {"start": v(8.37, 59.44) * mm, "end": v(8.16, 59.47) * mm});
            skLineSegment(sketch, "E1102", {"start": v(8.16, 59.47) * mm, "end": v(7.96, 59.5) * mm});
            skLineSegment(sketch, "E1103", {"start": v(7.96, 59.5) * mm, "end": v(7.76, 59.54) * mm});
            skLineSegment(sketch, "E1104", {"start": v(7.76, 59.54) * mm, "end": v(7.65, 59.56) * mm});
            skLineSegment(sketch, "E1105", {"start": v(7.65, 59.56) * mm, "end": v(7.68, 59.76) * mm});
            skLineSegment(sketch, "E1106", {"start": v(7.68, 59.76) * mm, "end": v(7.71, 59.97) * mm});
            skLineSegment(sketch, "E1107", {"start": v(7.71, 59.97) * mm, "end": v(7.74, 60.18) * mm});
            skLineSegment(sketch, "E1108", {"start": v(7.74, 60.18) * mm, "end": v(7.77, 60.38) * mm});
            skLineSegment(sketch, "E1109", {"start": v(7.77, 60.38) * mm, "end": v(7.8, 60.58) * mm});
            skLineSegment(sketch, "E1110", {"start": v(7.8, 60.58) * mm, "end": v(7.83, 60.8) * mm});
            skLineSegment(sketch, "E1111", {"start": v(7.83, 60.8) * mm, "end": v(7.86, 61) * mm});
            skLineSegment(sketch, "E1112", {"start": v(7.86, 61) * mm, "end": v(7.9, 61.2) * mm});
            skLineSegment(sketch, "E1113", {"start": v(7.9, 61.2) * mm, "end": v(7.92, 61.41) * mm});
            skLineSegment(sketch, "E1114", {"start": v(7.92, 61.41) * mm, "end": v(7.95, 61.61) * mm});
            skLineSegment(sketch, "E1115", {"start": v(7.95, 61.61) * mm, "end": v(7.98, 61.82) * mm});
            skLineSegment(sketch, "E1116", {"start": v(7.98, 61.82) * mm, "end": v(8.01, 62.03) * mm});
            skLineSegment(sketch, "E1117", {"start": v(8.01, 62.03) * mm, "end": v(8.04, 62.25) * mm});
            skLineSegment(sketch, "E1118", {"start": v(8.04, 62.25) * mm, "end": v(8.03, 62.46) * mm});
            skLineSegment(sketch, "E1119", {"start": v(8.03, 62.46) * mm, "end": v(7.97, 62.67) * mm});
            skLineSegment(sketch, "E1120", {"start": v(7.97, 62.67) * mm, "end": v(7.85, 62.85) * mm});
            skLineSegment(sketch, "E1121", {"start": v(7.85, 62.85) * mm, "end": v(7.7, 62.99) * mm});
            skLineSegment(sketch, "E1122", {"start": v(7.7, 62.99) * mm, "end": v(7.5, 63.09) * mm});
            skLineSegment(sketch, "E1123", {"start": v(7.5, 63.09) * mm, "end": v(7.3, 63.13) * mm});
            skLineSegment(sketch, "E1124", {"start": v(7.3, 63.13) * mm, "end": v(7.25, 63.13) * mm});
            skLineSegment(sketch, "E1125", {"start": v(7.25, 63.13) * mm, "end": v(7.03, 63.11) * mm});
            skLineSegment(sketch, "E1126", {"start": v(7.03, 63.11) * mm, "end": v(6.83, 63.03) * mm});
            skLineSegment(sketch, "E1127", {"start": v(6.83, 63.03) * mm, "end": v(6.66, 62.9) * mm});
            skLineSegment(sketch, "E1128", {"start": v(6.66, 62.9) * mm, "end": v(6.53, 62.74) * mm});
            skLineSegment(sketch, "E1129", {"start": v(6.53, 62.74) * mm, "end": v(6.44, 62.54) * mm});
            skLineSegment(sketch, "E1130", {"start": v(6.44, 62.54) * mm, "end": v(6.4, 62.33) * mm});
            skLineSegment(sketch, "E1131", {"start": v(6.4, 62.33) * mm, "end": v(6.38, 62.12) * mm});
            skLineSegment(sketch, "E1132", {"start": v(6.38, 62.12) * mm, "end": v(6.36, 61.92) * mm});
            skLineSegment(sketch, "E1133", {"start": v(6.36, 61.92) * mm, "end": v(6.33, 61.7) * mm});
            skLineSegment(sketch, "E1134", {"start": v(6.33, 61.7) * mm, "end": v(6.3, 61.5) * mm});
            skLineSegment(sketch, "E1135", {"start": v(6.3, 61.5) * mm, "end": v(6.28, 61.3) * mm});
            skLineSegment(sketch, "E1136", {"start": v(6.28, 61.3) * mm, "end": v(6.26, 61.1) * mm});
            skLineSegment(sketch, "E1137", {"start": v(6.26, 61.1) * mm, "end": v(6.23, 60.89) * mm});
            skLineSegment(sketch, "E1138", {"start": v(6.23, 60.89) * mm, "end": v(6.2, 60.68) * mm});
            skLineSegment(sketch, "E1139", {"start": v(6.2, 60.68) * mm, "end": v(6.18, 60.47) * mm});
            skLineSegment(sketch, "E1140", {"start": v(6.18, 60.47) * mm, "end": v(6.16, 60.27) * mm});
            skLineSegment(sketch, "E1141", {"start": v(6.16, 60.27) * mm, "end": v(6.14, 60.06) * mm});
            skLineSegment(sketch, "E1142", {"start": v(6.14, 60.06) * mm, "end": v(6.11, 59.85) * mm});
            skLineSegment(sketch, "E1143", {"start": v(6.11, 59.85) * mm, "end": v(6.1, 59.76) * mm});
            skLineSegment(sketch, "E1144", {"start": v(6.1, 59.76) * mm, "end": v(5.9, 59.78) * mm});
            skLineSegment(sketch, "E1145", {"start": v(5.9, 59.78) * mm, "end": v(5.7, 59.8) * mm});
            skLineSegment(sketch, "E1146", {"start": v(5.7, 59.8) * mm, "end": v(5.49, 59.82) * mm});
            skLineSegment(sketch, "E1147", {"start": v(5.49, 59.82) * mm, "end": v(5.28, 59.84) * mm});
            skLineSegment(sketch, "E1148", {"start": v(5.28, 59.84) * mm, "end": v(5.08, 59.86) * mm});
            skLineSegment(sketch, "E1149", {"start": v(5.08, 59.86) * mm, "end": v(4.87, 59.88) * mm});
            skLineSegment(sketch, "E1150", {"start": v(4.87, 59.88) * mm, "end": v(4.67, 59.9) * mm});
            skLineSegment(sketch, "E1151", {"start": v(4.67, 59.9) * mm, "end": v(4.46, 59.93) * mm});
            skLineSegment(sketch, "E1152", {"start": v(4.46, 59.93) * mm, "end": v(4.26, 59.95) * mm});
            skLineSegment(sketch, "E1153", {"start": v(4.26, 59.95) * mm, "end": v(4.05, 59.97) * mm});
            skLineSegment(sketch, "E1154", {"start": v(4.05, 59.97) * mm, "end": v(3.85, 59.99) * mm});
            skLineSegment(sketch, "E1155", {"start": v(3.85, 59.99) * mm, "end": v(3.74, 60) * mm});
            skLineSegment(sketch, "E1156", {"start": v(3.74, 60) * mm, "end": v(3.76, 60.2) * mm});
            skLineSegment(sketch, "E1157", {"start": v(3.76, 60.2) * mm, "end": v(3.77, 60.4) * mm});
            skLineSegment(sketch, "E1158", {"start": v(3.77, 60.4) * mm, "end": v(3.79, 60.62) * mm});
            skLineSegment(sketch, "E1159", {"start": v(3.79, 60.62) * mm, "end": v(3.8, 60.82) * mm});
            skLineSegment(sketch, "E1160", {"start": v(3.8, 60.82) * mm, "end": v(3.82, 61.03) * mm});
            skLineSegment(sketch, "E1161", {"start": v(3.82, 61.03) * mm, "end": v(3.84, 61.24) * mm});
            skLineSegment(sketch, "E1162", {"start": v(3.84, 61.24) * mm, "end": v(3.85, 61.44) * mm});
            skLineSegment(sketch, "E1163", {"start": v(3.85, 61.44) * mm, "end": v(3.87, 61.65) * mm});
            skLineSegment(sketch, "E1164", {"start": v(3.87, 61.65) * mm, "end": v(3.89, 61.86) * mm});
            skLineSegment(sketch, "E1165", {"start": v(3.89, 61.86) * mm, "end": v(3.9, 62.07) * mm});
            skLineSegment(sketch, "E1166", {"start": v(3.9, 62.07) * mm, "end": v(3.92, 62.27) * mm});
            skLineSegment(sketch, "E1167", {"start": v(3.92, 62.27) * mm, "end": v(3.94, 62.48) * mm});
            skLineSegment(sketch, "E1168", {"start": v(3.94, 62.48) * mm, "end": v(3.95, 62.7) * mm});
            skLineSegment(sketch, "E1169", {"start": v(3.95, 62.7) * mm, "end": v(3.93, 62.92) * mm});
            skLineSegment(sketch, "E1170", {"start": v(3.93, 62.92) * mm, "end": v(3.85, 63.12) * mm});
            skLineSegment(sketch, "E1171", {"start": v(3.85, 63.12) * mm, "end": v(3.72, 63.29) * mm});
            skLineSegment(sketch, "E1172", {"start": v(3.72, 63.29) * mm, "end": v(3.55, 63.42) * mm});
            skLineSegment(sketch, "E1173", {"start": v(3.55, 63.42) * mm, "end": v(3.36, 63.5) * mm});
            skLineSegment(sketch, "E1174", {"start": v(3.36, 63.5) * mm, "end": v(3.14, 63.54) * mm});
            skLineSegment(sketch, "E1175", {"start": v(3.14, 63.54) * mm, "end": v(2.93, 63.51) * mm});
            skLineSegment(sketch, "E1176", {"start": v(2.93, 63.51) * mm, "end": v(2.73, 63.43) * mm});
            skLineSegment(sketch, "E1177", {"start": v(2.73, 63.43) * mm, "end": v(2.56, 63.3) * mm});
            skLineSegment(sketch, "E1178", {"start": v(2.56, 63.3) * mm, "end": v(2.43, 63.13) * mm});
            skLineSegment(sketch, "E1179", {"start": v(2.43, 63.13) * mm, "end": v(2.34, 62.94) * mm});
            skLineSegment(sketch, "E1180", {"start": v(2.34, 62.94) * mm, "end": v(2.32, 62.73) * mm});
            skLineSegment(sketch, "E1181", {"start": v(2.32, 62.73) * mm, "end": v(2.3, 62.53) * mm});
            skLineSegment(sketch, "E1182", {"start": v(2.3, 62.53) * mm, "end": v(2.3, 62.32) * mm});
            skLineSegment(sketch, "E1183", {"start": v(2.3, 62.32) * mm, "end": v(2.28, 62.12) * mm});
            skLineSegment(sketch, "E1184", {"start": v(2.28, 62.12) * mm, "end": v(2.27, 61.91) * mm});
            skLineSegment(sketch, "E1185", {"start": v(2.27, 61.91) * mm, "end": v(2.26, 61.7) * mm});
            skLineSegment(sketch, "E1186", {"start": v(2.26, 61.7) * mm, "end": v(2.25, 61.5) * mm});
            skLineSegment(sketch, "E1187", {"start": v(2.25, 61.5) * mm, "end": v(2.24, 61.29) * mm});
            skLineSegment(sketch, "E1188", {"start": v(2.24, 61.29) * mm, "end": v(2.23, 61.08) * mm});
            skLineSegment(sketch, "E1189", {"start": v(2.23, 61.08) * mm, "end": v(2.22, 60.87) * mm});
            skLineSegment(sketch, "E1190", {"start": v(2.22, 60.87) * mm, "end": v(2.2, 60.67) * mm});
            skLineSegment(sketch, "E1191", {"start": v(2.2, 60.67) * mm, "end": v(2.2, 60.45) * mm});
            skLineSegment(sketch, "E1192", {"start": v(2.2, 60.45) * mm, "end": v(2.18, 60.25) * mm});
            skLineSegment(sketch, "E1193", {"start": v(2.18, 60.25) * mm, "end": v(2.18, 60.1) * mm});
            skLineSegment(sketch, "E1194", {"start": v(2.18, 60.1) * mm, "end": v(1.97, 60.1) * mm});
            skLineSegment(sketch, "E1195", {"start": v(1.97, 60.1) * mm, "end": v(1.76, 60.11) * mm});
            skLineSegment(sketch, "E1196", {"start": v(1.76, 60.11) * mm, "end": v(1.56, 60.12) * mm});
            skLineSegment(sketch, "E1197", {"start": v(1.56, 60.12) * mm, "end": v(1.35, 60.13) * mm});
            skLineSegment(sketch, "E1198", {"start": v(1.35, 60.13) * mm, "end": v(1.15, 60.13) * mm});
            skLineSegment(sketch, "E1199", {"start": v(1.15, 60.13) * mm, "end": v(0.94, 60.14) * mm});
            skLineSegment(sketch, "E1200", {"start": v(0.94, 60.14) * mm, "end": v(0.74, 60.15) * mm});
            skLineSegment(sketch, "E1201", {"start": v(0.74, 60.15) * mm, "end": v(0.53, 60.15) * mm});
            skLineSegment(sketch, "E1202", {"start": v(0.53, 60.15) * mm, "end": v(0.32, 60.16) * mm});
            skLineSegment(sketch, "E1203", {"start": v(0.32, 60.16) * mm, "end": v(0.12, 60.17) * mm});
            skLineSegment(sketch, "E1204", {"start": v(0.12, 60.17) * mm, "end": v(-0.09, 60.17) * mm});
            skLineSegment(sketch, "E1205", {"start": v(-0.09, 60.17) * mm, "end": v(-0.2, 60.18) * mm});
            skLineSegment(sketch, "E1206", {"start": v(-0.2, 60.18) * mm, "end": v(-0.2, 60.38) * mm});
            skLineSegment(sketch, "E1207", {"start": v(-0.2, 60.38) * mm, "end": v(-0.19, 60.59) * mm});
            skLineSegment(sketch, "E1208", {"start": v(-0.19, 60.59) * mm, "end": v(-0.19, 60.8) * mm});
            skLineSegment(sketch, "E1209", {"start": v(-0.19, 60.8) * mm, "end": v(-0.18, 61) * mm});
            skLineSegment(sketch, "E1210", {"start": v(-0.18, 61) * mm, "end": v(-0.18, 61.21) * mm});
            skLineSegment(sketch, "E1211", {"start": v(-0.18, 61.21) * mm, "end": v(-0.18, 61.42) * mm});
            skLineSegment(sketch, "E1212", {"start": v(-0.18, 61.42) * mm, "end": v(-0.17, 61.63) * mm});
            skLineSegment(sketch, "E1213", {"start": v(-0.17, 61.63) * mm, "end": v(-0.17, 61.83) * mm});
            skLineSegment(sketch, "E1214", {"start": v(-0.17, 61.83) * mm, "end": v(-0.17, 62.05) * mm});
            skLineSegment(sketch, "E1215", {"start": v(-0.17, 62.05) * mm, "end": v(-0.17, 62.25) * mm});
            skLineSegment(sketch, "E1216", {"start": v(-0.17, 62.25) * mm, "end": v(-0.16, 62.46) * mm});
            skLineSegment(sketch, "E1217", {"start": v(-0.16, 62.46) * mm, "end": v(-0.16, 62.67) * mm});
            skLineSegment(sketch, "E1218", {"start": v(-0.16, 62.67) * mm, "end": v(-0.16, 62.9) * mm});
            skLineSegment(sketch, "E1219", {"start": v(-0.16, 62.9) * mm, "end": v(-0.2, 63.1) * mm});
            skLineSegment(sketch, "E1220", {"start": v(-0.2, 63.1) * mm, "end": v(-0.29, 63.3) * mm});
            skLineSegment(sketch, "E1221", {"start": v(-0.29, 63.3) * mm, "end": v(-0.43, 63.46) * mm});
            skLineSegment(sketch, "E1222", {"start": v(-0.43, 63.46) * mm, "end": v(-0.6, 63.58) * mm});
            skLineSegment(sketch, "E1223", {"start": v(-0.6, 63.58) * mm, "end": v(-0.8, 63.65) * mm});
            skLineSegment(sketch, "E1224", {"start": v(-0.8, 63.65) * mm, "end": v(-0.98, 63.67) * mm});
            skLineSegment(sketch, "E1225", {"start": v(-0.98, 63.67) * mm, "end": v(-1.19, 63.64) * mm});
            skLineSegment(sketch, "E1226", {"start": v(-1.19, 63.64) * mm, "end": v(-1.39, 63.56) * mm});
            skLineSegment(sketch, "E1227", {"start": v(-1.39, 63.56) * mm, "end": v(-1.56, 63.43) * mm});
            skLineSegment(sketch, "E1228", {"start": v(-1.56, 63.43) * mm, "end": v(-1.69, 63.26) * mm});
            skLineSegment(sketch, "E1229", {"start": v(-1.69, 63.26) * mm, "end": v(-1.77, 63.06) * mm});
            skLineSegment(sketch, "E1230", {"start": v(-1.77, 63.06) * mm, "end": v(-1.8, 62.85) * mm});
            skLineSegment(sketch, "E1231", {"start": v(-1.8, 62.85) * mm, "end": v(-1.8, 62.64) * mm});
            skLineSegment(sketch, "E1232", {"start": v(-1.8, 62.64) * mm, "end": v(-1.8, 62.44) * mm});
            skLineSegment(sketch, "E1233", {"start": v(-1.8, 62.44) * mm, "end": v(-1.79, 62.22) * mm});
            skLineSegment(sketch, "E1234", {"start": v(-1.79, 62.22) * mm, "end": v(-1.79, 62.02) * mm});
            skLineSegment(sketch, "E1235", {"start": v(-1.79, 62.02) * mm, "end": v(-1.78, 61.81) * mm});
            skLineSegment(sketch, "E1236", {"start": v(-1.78, 61.81) * mm, "end": v(-1.78, 61.6) * mm});
            skLineSegment(sketch, "E1237", {"start": v(-1.78, 61.6) * mm, "end": v(-1.78, 61.4) * mm});
            skLineSegment(sketch, "E1238", {"start": v(-1.78, 61.4) * mm, "end": v(-1.77, 61.19) * mm});
            skLineSegment(sketch, "E1239", {"start": v(-1.77, 61.19) * mm, "end": v(-1.77, 60.98) * mm});
            skLineSegment(sketch, "E1240", {"start": v(-1.77, 60.98) * mm, "end": v(-1.77, 60.77) * mm});
            skLineSegment(sketch, "E1241", {"start": v(-1.77, 60.77) * mm, "end": v(-1.77, 60.57) * mm});
            skLineSegment(sketch, "E1242", {"start": v(-1.77, 60.57) * mm, "end": v(-1.76, 60.35) * mm});
            skLineSegment(sketch, "E1243", {"start": v(-1.76, 60.35) * mm, "end": v(-1.76, 60.18) * mm});
            skLineSegment(sketch, "E1244", {"start": v(-1.76, 60.18) * mm, "end": v(-1.97, 60.17) * mm});
            skLineSegment(sketch, "E1245", {"start": v(-1.97, 60.17) * mm, "end": v(-2.17, 60.16) * mm});
            skLineSegment(sketch, "E1246", {"start": v(-2.17, 60.16) * mm, "end": v(-2.38, 60.16) * mm});
            skLineSegment(sketch, "E1247", {"start": v(-2.38, 60.16) * mm, "end": v(-2.58, 60.15) * mm});
            skLineSegment(sketch, "E1248", {"start": v(-2.58, 60.15) * mm, "end": v(-2.8, 60.14) * mm});
            skLineSegment(sketch, "E1249", {"start": v(-2.8, 60.14) * mm, "end": v(-3, 60.14) * mm});
            skLineSegment(sketch, "E1250", {"start": v(-3, 60.14) * mm, "end": v(-3.2, 60.13) * mm});
            skLineSegment(sketch, "E1251", {"start": v(-3.2, 60.13) * mm, "end": v(-3.4, 60.12) * mm});
            skLineSegment(sketch, "E1252", {"start": v(-3.4, 60.12) * mm, "end": v(-3.61, 60.12) * mm});
            skLineSegment(sketch, "E1253", {"start": v(-3.61, 60.12) * mm, "end": v(-3.82, 60.1) * mm});
            skLineSegment(sketch, "E1254", {"start": v(-3.82, 60.1) * mm, "end": v(-4.03, 60.1) * mm});
            skLineSegment(sketch, "E1255", {"start": v(-4.03, 60.1) * mm, "end": v(-4.13, 60.1) * mm});
            skLineSegment(sketch, "E1256", {"start": v(-4.13, 60.1) * mm, "end": v(-4.14, 60.3) * mm});
            skLineSegment(sketch, "E1257", {"start": v(-4.14, 60.3) * mm, "end": v(-4.15, 60.5) * mm});
            skLineSegment(sketch, "E1258", {"start": v(-4.15, 60.5) * mm, "end": v(-4.16, 60.72) * mm});
            skLineSegment(sketch, "E1259", {"start": v(-4.16, 60.72) * mm, "end": v(-4.17, 60.93) * mm});
            skLineSegment(sketch, "E1260", {"start": v(-4.17, 60.93) * mm, "end": v(-4.18, 61.13) * mm});
            skLineSegment(sketch, "E1261", {"start": v(-4.18, 61.13) * mm, "end": v(-4.2, 61.34) * mm});
            skLineSegment(sketch, "E1262", {"start": v(-4.2, 61.34) * mm, "end": v(-4.2, 61.55) * mm});
            skLineSegment(sketch, "E1263", {"start": v(-4.2, 61.55) * mm, "end": v(-4.22, 61.76) * mm});
            skLineSegment(sketch, "E1264", {"start": v(-4.22, 61.76) * mm, "end": v(-4.23, 61.97) * mm});
            skLineSegment(sketch, "E1265", {"start": v(-4.23, 61.97) * mm, "end": v(-4.24, 62.17) * mm});
            skLineSegment(sketch, "E1266", {"start": v(-4.24, 62.17) * mm, "end": v(-4.25, 62.38) * mm});
            skLineSegment(sketch, "E1267", {"start": v(-4.25, 62.38) * mm, "end": v(-4.26, 62.59) * mm});
            skLineSegment(sketch, "E1268", {"start": v(-4.26, 62.59) * mm, "end": v(-4.27, 62.8) * mm});
            skLineSegment(sketch, "E1269", {"start": v(-4.27, 62.8) * mm, "end": v(-4.33, 63.02) * mm});
            skLineSegment(sketch, "E1270", {"start": v(-4.33, 63.02) * mm, "end": v(-4.43, 63.2) * mm});
            skLineSegment(sketch, "E1271", {"start": v(-4.43, 63.2) * mm, "end": v(-4.58, 63.36) * mm});
            skLineSegment(sketch, "E1272", {"start": v(-4.58, 63.36) * mm, "end": v(-4.76, 63.47) * mm});
            skLineSegment(sketch, "E1273", {"start": v(-4.76, 63.47) * mm, "end": v(-4.97, 63.53) * mm});
            skLineSegment(sketch, "E1274", {"start": v(-4.97, 63.53) * mm, "end": v(-5.1, 63.54) * mm});
            skLineSegment(sketch, "E1275", {"start": v(-5.1, 63.54) * mm, "end": v(-5.31, 63.5) * mm});
            skLineSegment(sketch, "E1276", {"start": v(-5.31, 63.5) * mm, "end": v(-5.5, 63.42) * mm});
            skLineSegment(sketch, "E1277", {"start": v(-5.5, 63.42) * mm, "end": v(-5.68, 63.29) * mm});
            skLineSegment(sketch, "E1278", {"start": v(-5.68, 63.29) * mm, "end": v(-5.8, 63.12) * mm});
            skLineSegment(sketch, "E1279", {"start": v(-5.8, 63.12) * mm, "end": v(-5.88, 62.92) * mm});
            skLineSegment(sketch, "E1280", {"start": v(-5.88, 62.92) * mm, "end": v(-5.9, 62.7) * mm});
            skLineSegment(sketch, "E1281", {"start": v(-5.9, 62.7) * mm, "end": v(-5.9, 62.48) * mm});
            skLineSegment(sketch, "E1282", {"start": v(-5.9, 62.48) * mm, "end": v(-5.87, 62.28) * mm});
            skLineSegment(sketch, "E1283", {"start": v(-5.87, 62.28) * mm, "end": v(-5.86, 62.07) * mm});
            skLineSegment(sketch, "E1284", {"start": v(-5.86, 62.07) * mm, "end": v(-5.84, 61.86) * mm});
            skLineSegment(sketch, "E1285", {"start": v(-5.84, 61.86) * mm, "end": v(-5.83, 61.66) * mm});
            skLineSegment(sketch, "E1286", {"start": v(-5.83, 61.66) * mm, "end": v(-5.8, 61.45) * mm});
            skLineSegment(sketch, "E1287", {"start": v(-5.8, 61.45) * mm, "end": v(-5.8, 61.24) * mm});
            skLineSegment(sketch, "E1288", {"start": v(-5.8, 61.24) * mm, "end": v(-5.78, 61.03) * mm});
            skLineSegment(sketch, "E1289", {"start": v(-5.78, 61.03) * mm, "end": v(-5.76, 60.83) * mm});
            skLineSegment(sketch, "E1290", {"start": v(-5.76, 60.83) * mm, "end": v(-5.74, 60.62) * mm});
            skLineSegment(sketch, "E1291", {"start": v(-5.74, 60.62) * mm, "end": v(-5.73, 60.41) * mm});
            skLineSegment(sketch, "E1292", {"start": v(-5.73, 60.41) * mm, "end": v(-5.71, 60.2) * mm});
            skLineSegment(sketch, "E1293", {"start": v(-5.71, 60.2) * mm, "end": v(-5.7, 60) * mm});
            skLineSegment(sketch, "E1294", {"start": v(-5.7, 60) * mm, "end": v(-5.9, 59.98) * mm});
            skLineSegment(sketch, "E1295", {"start": v(-5.9, 59.98) * mm, "end": v(-6.1, 59.96) * mm});
            skLineSegment(sketch, "E1296", {"start": v(-6.1, 59.96) * mm, "end": v(-6.31, 59.94) * mm});
            skLineSegment(sketch, "E1297", {"start": v(-6.31, 59.94) * mm, "end": v(-6.52, 59.92) * mm});
            skLineSegment(sketch, "E1298", {"start": v(-6.52, 59.92) * mm, "end": v(-6.72, 59.9) * mm});
            skLineSegment(sketch, "E1299", {"start": v(-6.72, 59.9) * mm, "end": v(-6.93, 59.87) * mm});
            skLineSegment(sketch, "E1300", {"start": v(-6.93, 59.87) * mm, "end": v(-7.13, 59.85) * mm});
            skLineSegment(sketch, "E1301", {"start": v(-7.13, 59.85) * mm, "end": v(-7.33, 59.83) * mm});
            skLineSegment(sketch, "E1302", {"start": v(-7.33, 59.83) * mm, "end": v(-7.54, 59.81) * mm});
            skLineSegment(sketch, "E1303", {"start": v(-7.54, 59.81) * mm, "end": v(-7.74, 59.8) * mm});
            skLineSegment(sketch, "E1304", {"start": v(-7.74, 59.8) * mm, "end": v(-7.95, 59.77) * mm});
            skLineSegment(sketch, "E1305", {"start": v(-7.95, 59.77) * mm, "end": v(-8.05, 59.76) * mm});
            skLineSegment(sketch, "E1306", {"start": v(-8.05, 59.76) * mm, "end": v(-8.08, 59.97) * mm});
            skLineSegment(sketch, "E1307", {"start": v(-8.08, 59.97) * mm, "end": v(-8.1, 60.17) * mm});
            skLineSegment(sketch, "E1308", {"start": v(-8.1, 60.17) * mm, "end": v(-8.13, 60.38) * mm});
            skLineSegment(sketch, "E1309", {"start": v(-8.13, 60.38) * mm, "end": v(-8.15, 60.59) * mm});
            skLineSegment(sketch, "E1310", {"start": v(-8.15, 60.59) * mm, "end": v(-8.18, 60.8) * mm});
            skLineSegment(sketch, "E1311", {"start": v(-8.18, 60.8) * mm, "end": v(-8.2, 61) * mm});
            skLineSegment(sketch, "E1312", {"start": v(-8.2, 61) * mm, "end": v(-8.23, 61.2) * mm});
            skLineSegment(sketch, "E1313", {"start": v(-8.23, 61.2) * mm, "end": v(-8.25, 61.41) * mm});
            skLineSegment(sketch, "E1314", {"start": v(-8.25, 61.41) * mm, "end": v(-8.27, 61.62) * mm});
            skLineSegment(sketch, "E1315", {"start": v(-8.27, 61.62) * mm, "end": v(-8.3, 61.83) * mm});
            skLineSegment(sketch, "E1316", {"start": v(-8.3, 61.83) * mm, "end": v(-8.32, 62.03) * mm});
            skLineSegment(sketch, "E1317", {"start": v(-8.32, 62.03) * mm, "end": v(-8.35, 62.24) * mm});
            skLineSegment(sketch, "E1318", {"start": v(-8.35, 62.24) * mm, "end": v(-8.38, 62.46) * mm});
            skLineSegment(sketch, "E1319", {"start": v(-8.38, 62.46) * mm, "end": v(-8.44, 62.66) * mm});
            skLineSegment(sketch, "E1320", {"start": v(-8.44, 62.66) * mm, "end": v(-8.56, 62.84) * mm});
            skLineSegment(sketch, "E1321", {"start": v(-8.56, 62.84) * mm, "end": v(-8.72, 62.99) * mm});
            skLineSegment(sketch, "E1322", {"start": v(-8.72, 62.99) * mm, "end": v(-8.9, 63.09) * mm});
            skLineSegment(sketch, "E1323", {"start": v(-8.9, 63.09) * mm, "end": v(-9.12, 63.13) * mm});
            skLineSegment(sketch, "E1324", {"start": v(-9.12, 63.13) * mm, "end": v(-9.2, 63.13) * mm});
            skLineSegment(sketch, "E1325", {"start": v(-9.2, 63.13) * mm, "end": v(-9.41, 63.1) * mm});
            skLineSegment(sketch, "E1326", {"start": v(-9.41, 63.1) * mm, "end": v(-9.61, 63.01) * mm});
            skLineSegment(sketch, "E1327", {"start": v(-9.61, 63.01) * mm, "end": v(-9.78, 62.88) * mm});
            skLineSegment(sketch, "E1328", {"start": v(-9.78, 62.88) * mm, "end": v(-9.9, 62.7) * mm});
            skLineSegment(sketch, "E1329", {"start": v(-9.9, 62.7) * mm, "end": v(-9.98, 62.5) * mm});
            skLineSegment(sketch, "E1330", {"start": v(-9.98, 62.5) * mm, "end": v(-10, 62.29) * mm});
            skLineSegment(sketch, "E1331", {"start": v(-10, 62.29) * mm, "end": v(-9.97, 62.08) * mm});
            skLineSegment(sketch, "E1332", {"start": v(-9.97, 62.08) * mm, "end": v(-9.95, 61.88) * mm});
            skLineSegment(sketch, "E1333", {"start": v(-9.95, 61.88) * mm, "end": v(-9.92, 61.67) * mm});
            skLineSegment(sketch, "E1334", {"start": v(-9.92, 61.67) * mm, "end": v(-9.89, 61.47) * mm});
            skLineSegment(sketch, "E1335", {"start": v(-9.89, 61.47) * mm, "end": v(-9.86, 61.27) * mm});
            skLineSegment(sketch, "E1336", {"start": v(-9.86, 61.27) * mm, "end": v(-9.83, 61.06) * mm});
            skLineSegment(sketch, "E1337", {"start": v(-9.83, 61.06) * mm, "end": v(-9.8, 60.85) * mm});
            skLineSegment(sketch, "E1338", {"start": v(-9.8, 60.85) * mm, "end": v(-9.77, 60.65) * mm});
            skLineSegment(sketch, "E1339", {"start": v(-9.77, 60.65) * mm, "end": v(-9.74, 60.44) * mm});
            skLineSegment(sketch, "E1340", {"start": v(-9.74, 60.44) * mm, "end": v(-9.7, 60.24) * mm});
            skLineSegment(sketch, "E1341", {"start": v(-9.7, 60.24) * mm, "end": v(-9.68, 60.03) * mm});
            skLineSegment(sketch, "E1342", {"start": v(-9.68, 60.03) * mm, "end": v(-9.65, 59.82) * mm});
            skLineSegment(sketch, "E1343", {"start": v(-9.65, 59.82) * mm, "end": v(-9.62, 59.62) * mm});
            skLineSegment(sketch, "E1344", {"start": v(-9.62, 59.62) * mm, "end": v(-9.6, 59.56) * mm});
            skLineSegment(sketch, "E1345", {"start": v(-9.6, 59.56) * mm, "end": v(-9.81, 59.53) * mm});
            skLineSegment(sketch, "E1346", {"start": v(-9.81, 59.53) * mm, "end": v(-10.02, 59.5) * mm});
            skLineSegment(sketch, "E1347", {"start": v(-10.02, 59.5) * mm, "end": v(-10.22, 59.46) * mm});
            skLineSegment(sketch, "E1348", {"start": v(-10.22, 59.46) * mm, "end": v(-10.42, 59.42) * mm});
            skLineSegment(sketch, "E1349", {"start": v(-10.42, 59.42) * mm, "end": v(-10.63, 59.4) * mm});
            skLineSegment(sketch, "E1350", {"start": v(-10.63, 59.4) * mm, "end": v(-10.83, 59.36) * mm});
            skLineSegment(sketch, "E1351", {"start": v(-10.83, 59.36) * mm, "end": v(-11.03, 59.32) * mm});
            skLineSegment(sketch, "E1352", {"start": v(-11.03, 59.32) * mm, "end": v(-11.23, 59.3) * mm});
            skLineSegment(sketch, "E1353", {"start": v(-11.23, 59.3) * mm, "end": v(-11.44, 59.26) * mm});
            skLineSegment(sketch, "E1354", {"start": v(-11.44, 59.26) * mm, "end": v(-11.64, 59.22) * mm});
            skLineSegment(sketch, "E1355", {"start": v(-11.64, 59.22) * mm, "end": v(-11.84, 59.19) * mm});
            skLineSegment(sketch, "E1356", {"start": v(-11.84, 59.19) * mm, "end": v(-11.95, 59.17) * mm});
            skLineSegment(sketch, "E1357", {"start": v(-11.95, 59.17) * mm, "end": v(-11.99, 59.38) * mm});
            skLineSegment(sketch, "E1358", {"start": v(-11.99, 59.38) * mm, "end": v(-12.02, 59.58) * mm});
            skLineSegment(sketch, "E1359", {"start": v(-12.02, 59.58) * mm, "end": v(-12.06, 59.79) * mm});
            skLineSegment(sketch, "E1360", {"start": v(-12.06, 59.79) * mm, "end": v(-12.1, 59.99) * mm});
            skLineSegment(sketch, "E1361", {"start": v(-12.1, 59.99) * mm, "end": v(-12.14, 60.2) * mm});
            skLineSegment(sketch, "E1362", {"start": v(-12.14, 60.2) * mm, "end": v(-12.18, 60.4) * mm});
            skLineSegment(sketch, "E1363", {"start": v(-12.18, 60.4) * mm, "end": v(-12.21, 60.6) * mm});
            skLineSegment(sketch, "E1364", {"start": v(-12.21, 60.6) * mm, "end": v(-12.25, 60.8) * mm});
            skLineSegment(sketch, "E1365", {"start": v(-12.25, 60.8) * mm, "end": v(-12.29, 61.01) * mm});
            skLineSegment(sketch, "E1366", {"start": v(-12.29, 61.01) * mm, "end": v(-12.33, 61.21) * mm});
            skLineSegment(sketch, "E1367", {"start": v(-12.33, 61.21) * mm, "end": v(-12.36, 61.42) * mm});
            skLineSegment(sketch, "E1368", {"start": v(-12.36, 61.42) * mm, "end": v(-12.4, 61.63) * mm});
            skLineSegment(sketch, "E1369", {"start": v(-12.4, 61.63) * mm, "end": v(-12.44, 61.84) * mm});
            skLineSegment(sketch, "E1370", {"start": v(-12.44, 61.84) * mm, "end": v(-12.52, 62.04) * mm});
            skLineSegment(sketch, "E1371", {"start": v(-12.52, 62.04) * mm, "end": v(-12.65, 62.21) * mm});
            skLineSegment(sketch, "E1372", {"start": v(-12.65, 62.21) * mm, "end": v(-12.82, 62.35) * mm});
            skLineSegment(sketch, "E1373", {"start": v(-12.82, 62.35) * mm, "end": v(-13.02, 62.43) * mm});
            skLineSegment(sketch, "E1374", {"start": v(-13.02, 62.43) * mm, "end": v(-13.23, 62.46) * mm});
            skLineSegment(sketch, "E1375", {"start": v(-13.23, 62.46) * mm, "end": v(-13.44, 62.44) * mm});
            skLineSegment(sketch, "E1376", {"start": v(-13.44, 62.44) * mm, "end": v(-13.64, 62.36) * mm});
            skLineSegment(sketch, "E1377", {"start": v(-13.64, 62.36) * mm, "end": v(-13.81, 62.23) * mm});
            skLineSegment(sketch, "E1378", {"start": v(-13.81, 62.23) * mm, "end": v(-13.94, 62.06) * mm});
            skLineSegment(sketch, "E1379", {"start": v(-13.94, 62.06) * mm, "end": v(-14.03, 61.86) * mm});
            skLineSegment(sketch, "E1380", {"start": v(-14.03, 61.86) * mm, "end": v(-14.06, 61.65) * mm});
            skLineSegment(sketch, "E1381", {"start": v(-14.06, 61.65) * mm, "end": v(-14.03, 61.45) * mm});
            skLineSegment(sketch, "E1382", {"start": v(-14.03, 61.45) * mm, "end": v(-14, 61.25) * mm});
            skLineSegment(sketch, "E1383", {"start": v(-14, 61.25) * mm, "end": v(-13.95, 61.05) * mm});
            skLineSegment(sketch, "E1384", {"start": v(-13.95, 61.05) * mm, "end": v(-13.9, 60.84) * mm});
            skLineSegment(sketch, "E1385", {"start": v(-13.9, 60.84) * mm, "end": v(-13.86, 60.64) * mm});
            skLineSegment(sketch, "E1386", {"start": v(-13.86, 60.64) * mm, "end": v(-13.82, 60.44) * mm});
            skLineSegment(sketch, "E1387", {"start": v(-13.82, 60.44) * mm, "end": v(-13.78, 60.23) * mm});
            skLineSegment(sketch, "E1388", {"start": v(-13.78, 60.23) * mm, "end": v(-13.73, 60.03) * mm});
            skLineSegment(sketch, "E1389", {"start": v(-13.73, 60.03) * mm, "end": v(-13.69, 59.83) * mm});
            skLineSegment(sketch, "E1390", {"start": v(-13.69, 59.83) * mm, "end": v(-13.65, 59.62) * mm});
            skLineSegment(sketch, "E1391", {"start": v(-13.65, 59.62) * mm, "end": v(-13.6, 59.42) * mm});
            skLineSegment(sketch, "E1392", {"start": v(-13.6, 59.42) * mm, "end": v(-13.56, 59.22) * mm});
            skLineSegment(sketch, "E1393", {"start": v(-13.56, 59.22) * mm, "end": v(-13.52, 59.01) * mm});
            skLineSegment(sketch, "E1394", {"start": v(-13.52, 59.01) * mm, "end": v(-13.49, 58.87) * mm});
            skLineSegment(sketch, "E1395", {"start": v(-13.49, 58.87) * mm, "end": v(-13.69, 58.82) * mm});
            skLineSegment(sketch, "E1396", {"start": v(-13.69, 58.82) * mm, "end": v(-13.89, 58.77) * mm});
            skLineSegment(sketch, "E1397", {"start": v(-13.89, 58.77) * mm, "end": v(-14.09, 58.73) * mm});
            skLineSegment(sketch, "E1398", {"start": v(-14.09, 58.73) * mm, "end": v(-14.29, 58.68) * mm});
            skLineSegment(sketch, "E1399", {"start": v(-14.29, 58.68) * mm, "end": v(-14.49, 58.63) * mm});
            skLineSegment(sketch, "E1400", {"start": v(-14.49, 58.63) * mm, "end": v(-14.69, 58.59) * mm});
            skLineSegment(sketch, "E1401", {"start": v(-14.69, 58.59) * mm, "end": v(-14.9, 58.54) * mm});
            skLineSegment(sketch, "E1402", {"start": v(-14.9, 58.54) * mm, "end": v(-15.1, 58.5) * mm});
            skLineSegment(sketch, "E1403", {"start": v(-15.1, 58.5) * mm, "end": v(-15.3, 58.45) * mm});
            skLineSegment(sketch, "E1404", {"start": v(-15.3, 58.45) * mm, "end": v(-15.5, 58.4) * mm});
            skLineSegment(sketch, "E1405", {"start": v(-15.5, 58.4) * mm, "end": v(-15.7, 58.35) * mm});
            skLineSegment(sketch, "E1406", {"start": v(-15.7, 58.35) * mm, "end": v(-15.8, 58.33) * mm});
            skLineSegment(sketch, "E1407", {"start": v(-15.8, 58.33) * mm, "end": v(-15.85, 58.53) * mm});
            skLineSegment(sketch, "E1408", {"start": v(-15.85, 58.53) * mm, "end": v(-15.9, 58.73) * mm});
            skLineSegment(sketch, "E1409", {"start": v(-15.9, 58.73) * mm, "end": v(-15.95, 58.93) * mm});
            skLineSegment(sketch, "E1410", {"start": v(-15.95, 58.93) * mm, "end": v(-16, 59.13) * mm});
            skLineSegment(sketch, "E1411", {"start": v(-16, 59.13) * mm, "end": v(-16.05, 59.33) * mm});
            skLineSegment(sketch, "E1412", {"start": v(-16.05, 59.33) * mm, "end": v(-16.1, 59.54) * mm});
            skLineSegment(sketch, "E1413", {"start": v(-16.1, 59.54) * mm, "end": v(-16.15, 59.74) * mm});
            skLineSegment(sketch, "E1414", {"start": v(-16.15, 59.74) * mm, "end": v(-16.2, 59.94) * mm});
            skLineSegment(sketch, "E1415", {"start": v(-16.2, 59.94) * mm, "end": v(-16.26, 60.14) * mm});
            skLineSegment(sketch, "E1416", {"start": v(-16.26, 60.14) * mm, "end": v(-16.3, 60.34) * mm});
            skLineSegment(sketch, "E1417", {"start": v(-16.3, 60.34) * mm, "end": v(-16.36, 60.54) * mm});
            skLineSegment(sketch, "E1418", {"start": v(-16.36, 60.54) * mm, "end": v(-16.4, 60.75) * mm});
            skLineSegment(sketch, "E1419", {"start": v(-16.4, 60.75) * mm, "end": v(-16.46, 60.96) * mm});
            skLineSegment(sketch, "E1420", {"start": v(-16.46, 60.96) * mm, "end": v(-16.56, 61.15) * mm});
            skLineSegment(sketch, "E1421", {"start": v(-16.56, 61.15) * mm, "end": v(-16.7, 61.32) * mm});
            skLineSegment(sketch, "E1422", {"start": v(-16.7, 61.32) * mm, "end": v(-16.87, 61.44) * mm});
            skLineSegment(sketch, "E1423", {"start": v(-16.87, 61.44) * mm, "end": v(-17.07, 61.51) * mm});
            skLineSegment(sketch, "E1424", {"start": v(-17.07, 61.51) * mm, "end": v(-17.24, 61.53) * mm});
            skLineSegment(sketch, "E1425", {"start": v(-17.24, 61.53) * mm, "end": v(-17.46, 61.5) * mm});
            skLineSegment(sketch, "E1426", {"start": v(-17.46, 61.5) * mm, "end": v(-17.66, 61.42) * mm});
            skLineSegment(sketch, "E1427", {"start": v(-17.66, 61.42) * mm, "end": v(-17.83, 61.29) * mm});
            skLineSegment(sketch, "E1428", {"start": v(-17.83, 61.29) * mm, "end": v(-17.96, 61.12) * mm});
            skLineSegment(sketch, "E1429", {"start": v(-17.96, 61.12) * mm, "end": v(-18.04, 60.92) * mm});
            skLineSegment(sketch, "E1430", {"start": v(-18.04, 60.92) * mm, "end": v(-18.06, 60.7) * mm});
            skLineSegment(sketch, "E1431", {"start": v(-18.06, 60.7) * mm, "end": v(-18.03, 60.5) * mm});
            skLineSegment(sketch, "E1432", {"start": v(-18.03, 60.5) * mm, "end": v(-17.98, 60.3) * mm});
            skLineSegment(sketch, "E1433", {"start": v(-17.98, 60.3) * mm, "end": v(-17.92, 60.1) * mm});
            skLineSegment(sketch, "E1434", {"start": v(-17.92, 60.1) * mm, "end": v(-17.87, 59.9) * mm});
            skLineSegment(sketch, "E1435", {"start": v(-17.87, 59.9) * mm, "end": v(-17.8, 59.7) * mm});
            skLineSegment(sketch, "E1436", {"start": v(-17.8, 59.7) * mm, "end": v(-17.75, 59.5) * mm});
            skLineSegment(sketch, "E1437", {"start": v(-17.75, 59.5) * mm, "end": v(-17.7, 59.3) * mm});
            skLineSegment(sketch, "E1438", {"start": v(-17.7, 59.3) * mm, "end": v(-17.64, 59.1) * mm});
            skLineSegment(sketch, "E1439", {"start": v(-17.64, 59.1) * mm, "end": v(-17.58, 58.9) * mm});
            skLineSegment(sketch, "E1440", {"start": v(-17.58, 58.9) * mm, "end": v(-17.53, 58.7) * mm});
            skLineSegment(sketch, "E1441", {"start": v(-17.53, 58.7) * mm, "end": v(-17.47, 58.5) * mm});
            skLineSegment(sketch, "E1442", {"start": v(-17.47, 58.5) * mm, "end": v(-17.42, 58.3) * mm});
            skLineSegment(sketch, "E1443", {"start": v(-17.42, 58.3) * mm, "end": v(-17.36, 58.1) * mm});
            skLineSegment(sketch, "E1444", {"start": v(-17.36, 58.1) * mm, "end": v(-17.3, 57.92) * mm});
            skLineSegment(sketch, "E1445", {"start": v(-17.3, 57.92) * mm, "end": v(-17.5, 57.86) * mm});
            skLineSegment(sketch, "E1446", {"start": v(-17.5, 57.86) * mm, "end": v(-17.7, 57.8) * mm});
            skLineSegment(sketch, "E1447", {"start": v(-17.7, 57.8) * mm, "end": v(-17.9, 57.74) * mm});
            skLineSegment(sketch, "E1448", {"start": v(-17.9, 57.74) * mm, "end": v(-18.1, 57.68) * mm});
            skLineSegment(sketch, "E1449", {"start": v(-18.1, 57.68) * mm, "end": v(-18.3, 57.62) * mm});
            skLineSegment(sketch, "E1450", {"start": v(-18.3, 57.62) * mm, "end": v(-18.5, 57.56) * mm});
            skLineSegment(sketch, "E1451", {"start": v(-18.5, 57.56) * mm, "end": v(-18.69, 57.5) * mm});
            skLineSegment(sketch, "E1452", {"start": v(-18.69, 57.5) * mm, "end": v(-18.89, 57.44) * mm});
            skLineSegment(sketch, "E1453", {"start": v(-18.89, 57.44) * mm, "end": v(-19.08, 57.38) * mm});
            skLineSegment(sketch, "E1454", {"start": v(-19.08, 57.38) * mm, "end": v(-19.28, 57.32) * mm});
            skLineSegment(sketch, "E1455", {"start": v(-19.28, 57.32) * mm, "end": v(-19.48, 57.27) * mm});
            skLineSegment(sketch, "E1456", {"start": v(-19.48, 57.27) * mm, "end": v(-19.58, 57.23) * mm});
            skLineSegment(sketch, "E1457", {"start": v(-19.58, 57.23) * mm, "end": v(-19.64, 57.43) * mm});
            skLineSegment(sketch, "E1458", {"start": v(-19.64, 57.43) * mm, "end": v(-19.7, 57.63) * mm});
            skLineSegment(sketch, "E1459", {"start": v(-19.7, 57.63) * mm, "end": v(-19.77, 57.83) * mm});
            skLineSegment(sketch, "E1460", {"start": v(-19.77, 57.83) * mm, "end": v(-19.83, 58.02) * mm});
            skLineSegment(sketch, "E1461", {"start": v(-19.83, 58.02) * mm, "end": v(-19.9, 58.22) * mm});
            skLineSegment(sketch, "E1462", {"start": v(-19.9, 58.22) * mm, "end": v(-19.96, 58.42) * mm});
            skLineSegment(sketch, "E1463", {"start": v(-19.96, 58.42) * mm, "end": v(-20.03, 58.62) * mm});
            skLineSegment(sketch, "E1464", {"start": v(-20.03, 58.62) * mm, "end": v(-20.1, 58.81) * mm});
            skLineSegment(sketch, "E1465", {"start": v(-20.1, 58.81) * mm, "end": v(-20.16, 59.01) * mm});
            skLineSegment(sketch, "E1466", {"start": v(-20.16, 59.01) * mm, "end": v(-20.22, 59.2) * mm});
            skLineSegment(sketch, "E1467", {"start": v(-20.22, 59.2) * mm, "end": v(-20.28, 59.4) * mm});
            skLineSegment(sketch, "E1468", {"start": v(-20.28, 59.4) * mm, "end": v(-20.35, 59.6) * mm});
            skLineSegment(sketch, "E1469", {"start": v(-20.35, 59.6) * mm, "end": v(-20.42, 59.82) * mm});
            skLineSegment(sketch, "E1470", {"start": v(-20.42, 59.82) * mm, "end": v(-20.52, 60) * mm});
            skLineSegment(sketch, "E1471", {"start": v(-20.52, 60) * mm, "end": v(-20.67, 60.16) * mm});
            skLineSegment(sketch, "E1472", {"start": v(-20.67, 60.16) * mm, "end": v(-20.86, 60.27) * mm});
            skLineSegment(sketch, "E1473", {"start": v(-20.86, 60.27) * mm, "end": v(-21.06, 60.33) * mm});
            skLineSegment(sketch, "E1474", {"start": v(-21.06, 60.33) * mm, "end": v(-21.2, 60.34) * mm});
            skLineSegment(sketch, "E1475", {"start": v(-21.2, 60.34) * mm, "end": v(-21.4, 60.3) * mm});
            skLineSegment(sketch, "E1476", {"start": v(-21.4, 60.3) * mm, "end": v(-21.6, 60.22) * mm});
            skLineSegment(sketch, "E1477", {"start": v(-21.6, 60.22) * mm, "end": v(-21.77, 60.09) * mm});
            skLineSegment(sketch, "E1478", {"start": v(-21.77, 60.09) * mm, "end": v(-21.9, 59.92) * mm});
            skLineSegment(sketch, "E1479", {"start": v(-21.9, 59.92) * mm, "end": v(-21.98, 59.72) * mm});
            skLineSegment(sketch, "E1480", {"start": v(-21.98, 59.72) * mm, "end": v(-22, 59.5) * mm});
            skLineSegment(sketch, "E1481", {"start": v(-22, 59.5) * mm, "end": v(-21.97, 59.3) * mm});
            skLineSegment(sketch, "E1482", {"start": v(-21.97, 59.3) * mm, "end": v(-21.9, 59.08) * mm});
            skLineSegment(sketch, "E1483", {"start": v(-21.9, 59.08) * mm, "end": v(-21.83, 58.89) * mm});
            skLineSegment(sketch, "E1484", {"start": v(-21.83, 58.89) * mm, "end": v(-21.76, 58.7) * mm});
            skLineSegment(sketch, "E1485", {"start": v(-21.76, 58.7) * mm, "end": v(-21.69, 58.5) * mm});
            skLineSegment(sketch, "E1486", {"start": v(-21.69, 58.5) * mm, "end": v(-21.62, 58.3) * mm});
            skLineSegment(sketch, "E1487", {"start": v(-21.62, 58.3) * mm, "end": v(-21.55, 58.1) * mm});
            skLineSegment(sketch, "E1488", {"start": v(-21.55, 58.1) * mm, "end": v(-21.48, 57.9) * mm});
            skLineSegment(sketch, "E1489", {"start": v(-21.48, 57.9) * mm, "end": v(-21.41, 57.71) * mm});
            skLineSegment(sketch, "E1490", {"start": v(-21.41, 57.71) * mm, "end": v(-21.34, 57.52) * mm});
            skLineSegment(sketch, "E1491", {"start": v(-21.34, 57.52) * mm, "end": v(-21.27, 57.32) * mm});
            skLineSegment(sketch, "E1492", {"start": v(-21.27, 57.32) * mm, "end": v(-21.2, 57.12) * mm});
            skLineSegment(sketch, "E1493", {"start": v(-21.2, 57.12) * mm, "end": v(-21.13, 56.93) * mm});
            skLineSegment(sketch, "E1494", {"start": v(-21.13, 56.93) * mm, "end": v(-21.06, 56.73) * mm});
            skLineSegment(sketch, "E1495", {"start": v(-21.06, 56.73) * mm, "end": v(-21.26, 56.66) * mm});
            skLineSegment(sketch, "E1496", {"start": v(-21.26, 56.66) * mm, "end": v(-21.45, 56.59) * mm});
            skLineSegment(sketch, "E1497", {"start": v(-21.45, 56.59) * mm, "end": v(-21.64, 56.51) * mm});
            skLineSegment(sketch, "E1498", {"start": v(-21.64, 56.51) * mm, "end": v(-21.83, 56.44) * mm});
            skLineSegment(sketch, "E1499", {"start": v(-21.83, 56.44) * mm, "end": v(-22.03, 56.37) * mm});
            skLineSegment(sketch, "E1500", {"start": v(-22.03, 56.37) * mm, "end": v(-22.22, 56.3) * mm});
            skLineSegment(sketch, "E1501", {"start": v(-22.22, 56.3) * mm, "end": v(-22.41, 56.22) * mm});
            skLineSegment(sketch, "E1502", {"start": v(-22.41, 56.22) * mm, "end": v(-22.6, 56.15) * mm});
            skLineSegment(sketch, "E1503", {"start": v(-22.6, 56.15) * mm, "end": v(-22.8, 56.08) * mm});
            skLineSegment(sketch, "E1504", {"start": v(-22.8, 56.08) * mm, "end": v(-23, 56) * mm});
            skLineSegment(sketch, "E1505", {"start": v(-23, 56) * mm, "end": v(-23.18, 55.93) * mm});
            skLineSegment(sketch, "E1506", {"start": v(-23.18, 55.93) * mm, "end": v(-23.28, 55.9) * mm});
            skLineSegment(sketch, "E1507", {"start": v(-23.28, 55.9) * mm, "end": v(-23.36, 56.09) * mm});
            skLineSegment(sketch, "E1508", {"start": v(-23.36, 56.09) * mm, "end": v(-23.43, 56.28) * mm});
            skLineSegment(sketch, "E1509", {"start": v(-23.43, 56.28) * mm, "end": v(-23.51, 56.47) * mm});
            skLineSegment(sketch, "E1510", {"start": v(-23.51, 56.47) * mm, "end": v(-23.59, 56.67) * mm});
            skLineSegment(sketch, "E1511", {"start": v(-23.59, 56.67) * mm, "end": v(-23.67, 56.86) * mm});
            skLineSegment(sketch, "E1512", {"start": v(-23.67, 56.86) * mm, "end": v(-23.74, 57.05) * mm});
            skLineSegment(sketch, "E1513", {"start": v(-23.74, 57.05) * mm, "end": v(-23.82, 57.24) * mm});
            skLineSegment(sketch, "E1514", {"start": v(-23.82, 57.24) * mm, "end": v(-23.9, 57.44) * mm});
            skLineSegment(sketch, "E1515", {"start": v(-23.9, 57.44) * mm, "end": v(-23.97, 57.63) * mm});
            skLineSegment(sketch, "E1516", {"start": v(-23.97, 57.63) * mm, "end": v(-24.05, 57.82) * mm});
            skLineSegment(sketch, "E1517", {"start": v(-24.05, 57.82) * mm, "end": v(-24.13, 58.02) * mm});
            skLineSegment(sketch, "E1518", {"start": v(-24.13, 58.02) * mm, "end": v(-24.2, 58.21) * mm});
            skLineSegment(sketch, "E1519", {"start": v(-24.2, 58.21) * mm, "end": v(-24.29, 58.42) * mm});
            skLineSegment(sketch, "E1520", {"start": v(-24.29, 58.42) * mm, "end": v(-24.4, 58.6) * mm});
            skLineSegment(sketch, "E1521", {"start": v(-24.4, 58.6) * mm, "end": v(-24.56, 58.74) * mm});
            skLineSegment(sketch, "E1522", {"start": v(-24.56, 58.74) * mm, "end": v(-24.75, 58.84) * mm});
            skLineSegment(sketch, "E1523", {"start": v(-24.75, 58.84) * mm, "end": v(-24.96, 58.88) * mm});
            skLineSegment(sketch, "E1524", {"start": v(-24.96, 58.88) * mm, "end": v(-25.05, 58.89) * mm});
            skLineSegment(sketch, "E1525", {"start": v(-25.05, 58.89) * mm, "end": v(-25.26, 58.85) * mm});
            skLineSegment(sketch, "E1526", {"start": v(-25.26, 58.85) * mm, "end": v(-25.46, 58.77) * mm});
            skLineSegment(sketch, "E1527", {"start": v(-25.46, 58.77) * mm, "end": v(-25.63, 58.63) * mm});
            skLineSegment(sketch, "E1528", {"start": v(-25.63, 58.63) * mm, "end": v(-25.75, 58.46) * mm});
            skLineSegment(sketch, "E1529", {"start": v(-25.75, 58.46) * mm, "end": v(-25.83, 58.26) * mm});
            skLineSegment(sketch, "E1530", {"start": v(-25.83, 58.26) * mm, "end": v(-25.85, 58.04) * mm});
            skLineSegment(sketch, "E1531", {"start": v(-25.85, 58.04) * mm, "end": v(-25.81, 57.83) * mm});
            skLineSegment(sketch, "E1532", {"start": v(-25.81, 57.83) * mm, "end": v(-25.74, 57.64) * mm});
            skLineSegment(sketch, "E1533", {"start": v(-25.74, 57.64) * mm, "end": v(-25.66, 57.45) * mm});
            skLineSegment(sketch, "E1534", {"start": v(-25.66, 57.45) * mm, "end": v(-25.57, 57.26) * mm});
            skLineSegment(sketch, "E1535", {"start": v(-25.57, 57.26) * mm, "end": v(-25.5, 57.07) * mm});
            skLineSegment(sketch, "E1536", {"start": v(-25.5, 57.07) * mm, "end": v(-25.41, 56.88) * mm});
            skLineSegment(sketch, "E1537", {"start": v(-25.41, 56.88) * mm, "end": v(-25.33, 56.69) * mm});
            skLineSegment(sketch, "E1538", {"start": v(-25.33, 56.69) * mm, "end": v(-25.25, 56.5) * mm});
            skLineSegment(sketch, "E1539", {"start": v(-25.25, 56.5) * mm, "end": v(-25.17, 56.3) * mm});
            skLineSegment(sketch, "E1540", {"start": v(-25.17, 56.3) * mm, "end": v(-25.08, 56.11) * mm});
            skLineSegment(sketch, "E1541", {"start": v(-25.08, 56.11) * mm, "end": v(-25, 55.92) * mm});
            skLineSegment(sketch, "E1542", {"start": v(-25, 55.92) * mm, "end": v(-24.92, 55.74) * mm});
            skLineSegment(sketch, "E1543", {"start": v(-24.92, 55.74) * mm, "end": v(-24.84, 55.54) * mm});
            skLineSegment(sketch, "E1544", {"start": v(-24.84, 55.54) * mm, "end": v(-24.75, 55.35) * mm});
            skLineSegment(sketch, "E1545", {"start": v(-24.75, 55.35) * mm, "end": v(-24.73, 55.3) * mm});
            skLineSegment(sketch, "E1546", {"start": v(-24.73, 55.3) * mm, "end": v(-24.92, 55.21) * mm});
            skLineSegment(sketch, "E1547", {"start": v(-24.92, 55.21) * mm, "end": v(-25.1, 55.13) * mm});
            skLineSegment(sketch, "E1548", {"start": v(-25.1, 55.13) * mm, "end": v(-25.3, 55.04) * mm});
            skLineSegment(sketch, "E1549", {"start": v(-25.3, 55.04) * mm, "end": v(-25.48, 54.96) * mm});
            skLineSegment(sketch, "E1550", {"start": v(-25.48, 54.96) * mm, "end": v(-25.67, 54.87) * mm});
            skLineSegment(sketch, "E1551", {"start": v(-25.67, 54.87) * mm, "end": v(-25.86, 54.79) * mm});
            skLineSegment(sketch, "E1552", {"start": v(-25.86, 54.79) * mm, "end": v(-26.04, 54.7) * mm});
            skLineSegment(sketch, "E1553", {"start": v(-26.04, 54.7) * mm, "end": v(-26.23, 54.62) * mm});
            skLineSegment(sketch, "E1554", {"start": v(-26.23, 54.62) * mm, "end": v(-26.42, 54.53) * mm});
            skLineSegment(sketch, "E1555", {"start": v(-26.42, 54.53) * mm, "end": v(-26.6, 54.45) * mm});
            skLineSegment(sketch, "E1556", {"start": v(-26.6, 54.45) * mm, "end": v(-26.8, 54.36) * mm});
            skLineSegment(sketch, "E1557", {"start": v(-26.8, 54.36) * mm, "end": v(-26.89, 54.32) * mm});
            skLineSegment(sketch, "E1558", {"start": v(-26.89, 54.32) * mm, "end": v(-26.98, 54.5) * mm});
            skLineSegment(sketch, "E1559", {"start": v(-26.98, 54.5) * mm, "end": v(-27.07, 54.69) * mm});
            skLineSegment(sketch, "E1560", {"start": v(-27.07, 54.69) * mm, "end": v(-27.16, 54.88) * mm});
            skLineSegment(sketch, "E1561", {"start": v(-27.16, 54.88) * mm, "end": v(-27.25, 55.07) * mm});
            skLineSegment(sketch, "E1562", {"start": v(-27.25, 55.07) * mm, "end": v(-27.34, 55.25) * mm});
            skLineSegment(sketch, "E1563", {"start": v(-27.34, 55.25) * mm, "end": v(-27.43, 55.44) * mm});
            skLineSegment(sketch, "E1564", {"start": v(-27.43, 55.44) * mm, "end": v(-27.52, 55.63) * mm});
            skLineSegment(sketch, "E1565", {"start": v(-27.52, 55.63) * mm, "end": v(-27.6, 55.81) * mm});
            skLineSegment(sketch, "E1566", {"start": v(-27.6, 55.81) * mm, "end": v(-27.7, 56) * mm});
            skLineSegment(sketch, "E1567", {"start": v(-27.7, 56) * mm, "end": v(-27.78, 56.2) * mm});
            skLineSegment(sketch, "E1568", {"start": v(-27.78, 56.2) * mm, "end": v(-27.87, 56.38) * mm});
            skLineSegment(sketch, "E1569", {"start": v(-27.87, 56.38) * mm, "end": v(-27.96, 56.57) * mm});
            skLineSegment(sketch, "E1570", {"start": v(-27.96, 56.57) * mm, "end": v(-28.06, 56.77) * mm});
            skLineSegment(sketch, "E1571", {"start": v(-28.06, 56.77) * mm, "end": v(-28.19, 56.94) * mm});
            skLineSegment(sketch, "E1572", {"start": v(-28.19, 56.94) * mm, "end": v(-28.36, 57.07) * mm});
            skLineSegment(sketch, "E1573", {"start": v(-28.36, 57.07) * mm, "end": v(-28.55, 57.16) * mm});
            skLineSegment(sketch, "E1574", {"start": v(-28.55, 57.16) * mm, "end": v(-28.76, 57.19) * mm});
            skLineSegment(sketch, "E1575", {"start": v(-28.76, 57.19) * mm, "end": v(-28.98, 57.16) * mm});
            skLineSegment(sketch, "E1576", {"start": v(-28.98, 57.16) * mm, "end": v(-29.18, 57.09) * mm});
            skLineSegment(sketch, "E1577", {"start": v(-29.18, 57.09) * mm, "end": v(-29.35, 56.96) * mm});
            skLineSegment(sketch, "E1578", {"start": v(-29.35, 56.96) * mm, "end": v(-29.48, 56.79) * mm});
            skLineSegment(sketch, "E1579", {"start": v(-29.48, 56.79) * mm, "end": v(-29.57, 56.6) * mm});
            skLineSegment(sketch, "E1580", {"start": v(-29.57, 56.6) * mm, "end": v(-29.6, 56.38) * mm});
            skLineSegment(sketch, "E1581", {"start": v(-29.6, 56.38) * mm, "end": v(-29.57, 56.17) * mm});
            skLineSegment(sketch, "E1582", {"start": v(-29.57, 56.17) * mm, "end": v(-29.49, 55.98) * mm});
            skLineSegment(sketch, "E1583", {"start": v(-29.49, 55.98) * mm, "end": v(-29.4, 55.8) * mm});
            skLineSegment(sketch, "E1584", {"start": v(-29.4, 55.8) * mm, "end": v(-29.3, 55.6) * mm});
            skLineSegment(sketch, "E1585", {"start": v(-29.3, 55.6) * mm, "end": v(-29.21, 55.42) * mm});
            skLineSegment(sketch, "E1586", {"start": v(-29.21, 55.42) * mm, "end": v(-29.12, 55.24) * mm});
            skLineSegment(sketch, "E1587", {"start": v(-29.12, 55.24) * mm, "end": v(-29.02, 55.05) * mm});
            skLineSegment(sketch, "E1588", {"start": v(-29.02, 55.05) * mm, "end": v(-28.93, 54.87) * mm});
            skLineSegment(sketch, "E1589", {"start": v(-28.93, 54.87) * mm, "end": v(-28.84, 54.69) * mm});
            skLineSegment(sketch, "E1590", {"start": v(-28.84, 54.69) * mm, "end": v(-28.74, 54.5) * mm});
            skLineSegment(sketch, "E1591", {"start": v(-28.74, 54.5) * mm, "end": v(-28.65, 54.31) * mm});
            skLineSegment(sketch, "E1592", {"start": v(-28.65, 54.31) * mm, "end": v(-28.55, 54.13) * mm});
            skLineSegment(sketch, "E1593", {"start": v(-28.55, 54.13) * mm, "end": v(-28.46, 53.94) * mm});
            skLineSegment(sketch, "E1594", {"start": v(-28.46, 53.94) * mm, "end": v(-28.36, 53.76) * mm});
            skLineSegment(sketch, "E1595", {"start": v(-28.36, 53.76) * mm, "end": v(-28.3, 53.62) * mm});
            skLineSegment(sketch, "E1596", {"start": v(-28.3, 53.62) * mm, "end": v(-28.48, 53.53) * mm});
            skLineSegment(sketch, "E1597", {"start": v(-28.48, 53.53) * mm, "end": v(-28.66, 53.43) * mm});
            skLineSegment(sketch, "E1598", {"start": v(-28.66, 53.43) * mm, "end": v(-28.84, 53.33) * mm});
            skLineSegment(sketch, "E1599", {"start": v(-28.84, 53.33) * mm, "end": v(-29.02, 53.24) * mm});
            skLineSegment(sketch, "E1600", {"start": v(-29.02, 53.24) * mm, "end": v(-29.2, 53.14) * mm});
            skLineSegment(sketch, "E1601", {"start": v(-29.2, 53.14) * mm, "end": v(-29.39, 53.04) * mm});
            skLineSegment(sketch, "E1602", {"start": v(-29.39, 53.04) * mm, "end": v(-29.57, 52.94) * mm});
            skLineSegment(sketch, "E1603", {"start": v(-29.57, 52.94) * mm, "end": v(-29.75, 52.85) * mm});
            skLineSegment(sketch, "E1604", {"start": v(-29.75, 52.85) * mm, "end": v(-29.93, 52.75) * mm});
            skLineSegment(sketch, "E1605", {"start": v(-29.93, 52.75) * mm, "end": v(-30.11, 52.65) * mm});
            skLineSegment(sketch, "E1606", {"start": v(-30.11, 52.65) * mm, "end": v(-30.3, 52.56) * mm});
            skLineSegment(sketch, "E1607", {"start": v(-30.3, 52.56) * mm, "end": v(-30.39, 52.5) * mm});
            skLineSegment(sketch, "E1608", {"start": v(-30.39, 52.5) * mm, "end": v(-30.49, 52.69) * mm});
            skLineSegment(sketch, "E1609", {"start": v(-30.49, 52.69) * mm, "end": v(-30.59, 52.87) * mm});
            skLineSegment(sketch, "E1610", {"start": v(-30.59, 52.87) * mm, "end": v(-30.7, 53.05) * mm});
            skLineSegment(sketch, "E1611", {"start": v(-30.7, 53.05) * mm, "end": v(-30.8, 53.23) * mm});
            skLineSegment(sketch, "E1612", {"start": v(-30.8, 53.23) * mm, "end": v(-30.9, 53.4) * mm});
            skLineSegment(sketch, "E1613", {"start": v(-30.9, 53.4) * mm, "end": v(-31, 53.6) * mm});
            skLineSegment(sketch, "E1614", {"start": v(-31, 53.6) * mm, "end": v(-31.1, 53.77) * mm});
            skLineSegment(sketch, "E1615", {"start": v(-31.1, 53.77) * mm, "end": v(-31.2, 53.95) * mm});
            skLineSegment(sketch, "E1616", {"start": v(-31.2, 53.95) * mm, "end": v(-31.3, 54.14) * mm});
            skLineSegment(sketch, "E1617", {"start": v(-31.3, 54.14) * mm, "end": v(-31.4, 54.32) * mm});
            skLineSegment(sketch, "E1618", {"start": v(-31.4, 54.32) * mm, "end": v(-31.5, 54.5) * mm});
            skLineSegment(sketch, "E1619", {"start": v(-31.5, 54.5) * mm, "end": v(-31.6, 54.68) * mm});
            skLineSegment(sketch, "E1620", {"start": v(-31.6, 54.68) * mm, "end": v(-31.71, 54.87) * mm});
            skLineSegment(sketch, "E1621", {"start": v(-31.71, 54.87) * mm, "end": v(-31.85, 55.04) * mm});
            skLineSegment(sketch, "E1622", {"start": v(-31.85, 55.04) * mm, "end": v(-32.03, 55.16) * mm});
            skLineSegment(sketch, "E1623", {"start": v(-32.03, 55.16) * mm, "end": v(-32.23, 55.23) * mm});
            skLineSegment(sketch, "E1624", {"start": v(-32.23, 55.23) * mm, "end": v(-32.4, 55.25) * mm});
            skLineSegment(sketch, "E1625", {"start": v(-32.4, 55.25) * mm, "end": v(-32.62, 55.22) * mm});
            skLineSegment(sketch, "E1626", {"start": v(-32.62, 55.22) * mm, "end": v(-32.81, 55.14) * mm});
            skLineSegment(sketch, "E1627", {"start": v(-32.81, 55.14) * mm, "end": v(-32.98, 55.01) * mm});
            skLineSegment(sketch, "E1628", {"start": v(-32.98, 55.01) * mm, "end": v(-33.11, 54.84) * mm});
            skLineSegment(sketch, "E1629", {"start": v(-33.11, 54.84) * mm, "end": v(-33.2, 54.64) * mm});
            skLineSegment(sketch, "E1630", {"start": v(-33.2, 54.64) * mm, "end": v(-33.22, 54.43) * mm});
            skLineSegment(sketch, "E1631", {"start": v(-33.22, 54.43) * mm, "end": v(-33.2, 54.22) * mm});
            skLineSegment(sketch, "E1632", {"start": v(-33.2, 54.22) * mm, "end": v(-33.11, 54.02) * mm});
            skLineSegment(sketch, "E1633", {"start": v(-33.11, 54.02) * mm, "end": v(-33, 53.84) * mm});
            skLineSegment(sketch, "E1634", {"start": v(-33, 53.84) * mm, "end": v(-32.9, 53.66) * mm});
            skLineSegment(sketch, "E1635", {"start": v(-32.9, 53.66) * mm, "end": v(-32.8, 53.48) * mm});
            skLineSegment(sketch, "E1636", {"start": v(-32.8, 53.48) * mm, "end": v(-32.69, 53.3) * mm});
            skLineSegment(sketch, "E1637", {"start": v(-32.69, 53.3) * mm, "end": v(-32.58, 53.13) * mm});
            skLineSegment(sketch, "E1638", {"start": v(-32.58, 53.13) * mm, "end": v(-32.47, 52.95) * mm});
            skLineSegment(sketch, "E1639", {"start": v(-32.47, 52.95) * mm, "end": v(-32.37, 52.77) * mm});
            skLineSegment(sketch, "E1640", {"start": v(-32.37, 52.77) * mm, "end": v(-32.26, 52.6) * mm});
            skLineSegment(sketch, "E1641", {"start": v(-32.26, 52.6) * mm, "end": v(-32.15, 52.41) * mm});
            skLineSegment(sketch, "E1642", {"start": v(-32.15, 52.41) * mm, "end": v(-32.05, 52.23) * mm});
            skLineSegment(sketch, "E1643", {"start": v(-32.05, 52.23) * mm, "end": v(-31.94, 52.06) * mm});
            skLineSegment(sketch, "E1644", {"start": v(-31.94, 52.06) * mm, "end": v(-31.84, 51.88) * mm});
            skLineSegment(sketch, "E1645", {"start": v(-31.84, 51.88) * mm, "end": v(-31.74, 51.72) * mm});
            skLineSegment(sketch, "E1646", {"start": v(-31.74, 51.72) * mm, "end": v(-31.92, 51.61) * mm});
            skLineSegment(sketch, "E1647", {"start": v(-31.92, 51.61) * mm, "end": v(-32.1, 51.5) * mm});
            skLineSegment(sketch, "E1648", {"start": v(-32.1, 51.5) * mm, "end": v(-32.27, 51.4) * mm});
            skLineSegment(sketch, "E1649", {"start": v(-32.27, 51.4) * mm, "end": v(-32.44, 51.29) * mm});
            skLineSegment(sketch, "E1650", {"start": v(-32.44, 51.29) * mm, "end": v(-32.62, 51.18) * mm});
            skLineSegment(sketch, "E1651", {"start": v(-32.62, 51.18) * mm, "end": v(-32.8, 51.07) * mm});
            skLineSegment(sketch, "E1652", {"start": v(-32.8, 51.07) * mm, "end": v(-32.97, 50.96) * mm});
            skLineSegment(sketch, "E1653", {"start": v(-32.97, 50.96) * mm, "end": v(-33.14, 50.85) * mm});
            skLineSegment(sketch, "E1654", {"start": v(-33.14, 50.85) * mm, "end": v(-33.32, 50.74) * mm});
            skLineSegment(sketch, "E1655", {"start": v(-33.32, 50.74) * mm, "end": v(-33.5, 50.63) * mm});
            skLineSegment(sketch, "E1656", {"start": v(-33.5, 50.63) * mm, "end": v(-33.67, 50.53) * mm});
            skLineSegment(sketch, "E1657", {"start": v(-33.67, 50.53) * mm, "end": v(-33.76, 50.47) * mm});
            skLineSegment(sketch, "E1658", {"start": v(-33.76, 50.47) * mm, "end": v(-33.87, 50.64) * mm});
            skLineSegment(sketch, "E1659", {"start": v(-33.87, 50.64) * mm, "end": v(-33.98, 50.82) * mm});
            skLineSegment(sketch, "E1660", {"start": v(-33.98, 50.82) * mm, "end": v(-34.1, 51) * mm});
            skLineSegment(sketch, "E1661", {"start": v(-34.1, 51) * mm, "end": v(-34.2, 51.17) * mm});
            skLineSegment(sketch, "E1662", {"start": v(-34.2, 51.17) * mm, "end": v(-34.32, 51.34) * mm});
            skLineSegment(sketch, "E1663", {"start": v(-34.32, 51.34) * mm, "end": v(-34.44, 51.52) * mm});
            skLineSegment(sketch, "E1664", {"start": v(-34.44, 51.52) * mm, "end": v(-34.55, 51.69) * mm});
            skLineSegment(sketch, "E1665", {"start": v(-34.55, 51.69) * mm, "end": v(-34.66, 51.86) * mm});
            skLineSegment(sketch, "E1666", {"start": v(-34.66, 51.86) * mm, "end": v(-34.78, 52.04) * mm});
            skLineSegment(sketch, "E1667", {"start": v(-34.78, 52.04) * mm, "end": v(-34.89, 52.21) * mm});
            skLineSegment(sketch, "E1668", {"start": v(-34.89, 52.21) * mm, "end": v(-35, 52.38) * mm});
            skLineSegment(sketch, "E1669", {"start": v(-35, 52.38) * mm, "end": v(-35.12, 52.56) * mm});
            skLineSegment(sketch, "E1670", {"start": v(-35.12, 52.56) * mm, "end": v(-35.24, 52.75) * mm});
            skLineSegment(sketch, "E1671", {"start": v(-35.24, 52.75) * mm, "end": v(-35.39, 52.9) * mm});
            skLineSegment(sketch, "E1672", {"start": v(-35.39, 52.9) * mm, "end": v(-35.57, 53.01) * mm});
            skLineSegment(sketch, "E1673", {"start": v(-35.57, 53.01) * mm, "end": v(-35.78, 53.07) * mm});
            skLineSegment(sketch, "E1674", {"start": v(-35.78, 53.07) * mm, "end": v(-35.9, 53.08) * mm});
            skLineSegment(sketch, "E1675", {"start": v(-35.9, 53.08) * mm, "end": v(-36.12, 53.05) * mm});
            skLineSegment(sketch, "E1676", {"start": v(-36.12, 53.05) * mm, "end": v(-36.32, 52.96) * mm});
            skLineSegment(sketch, "E1677", {"start": v(-36.32, 52.96) * mm, "end": v(-36.48, 52.83) * mm});
            skLineSegment(sketch, "E1678", {"start": v(-36.48, 52.83) * mm, "end": v(-36.61, 52.66) * mm});
            skLineSegment(sketch, "E1679", {"start": v(-36.61, 52.66) * mm, "end": v(-36.7, 52.46) * mm});
            skLineSegment(sketch, "E1680", {"start": v(-36.7, 52.46) * mm, "end": v(-36.72, 52.25) * mm});
            skLineSegment(sketch, "E1681", {"start": v(-36.72, 52.25) * mm, "end": v(-36.68, 52.03) * mm});
            skLineSegment(sketch, "E1682", {"start": v(-36.68, 52.03) * mm, "end": v(-36.6, 51.84) * mm});
            skLineSegment(sketch, "E1683", {"start": v(-36.6, 51.84) * mm, "end": v(-36.47, 51.65) * mm});
            skLineSegment(sketch, "E1684", {"start": v(-36.47, 51.65) * mm, "end": v(-36.36, 51.48) * mm});
            skLineSegment(sketch, "E1685", {"start": v(-36.36, 51.48) * mm, "end": v(-36.24, 51.31) * mm});
            skLineSegment(sketch, "E1686", {"start": v(-36.24, 51.31) * mm, "end": v(-36.12, 51.14) * mm});
            skLineSegment(sketch, "E1687", {"start": v(-36.12, 51.14) * mm, "end": v(-36, 50.97) * mm});
            skLineSegment(sketch, "E1688", {"start": v(-36, 50.97) * mm, "end": v(-35.89, 50.8) * mm});
            skLineSegment(sketch, "E1689", {"start": v(-35.89, 50.8) * mm, "end": v(-35.77, 50.63) * mm});
            skLineSegment(sketch, "E1690", {"start": v(-35.77, 50.63) * mm, "end": v(-35.65, 50.46) * mm});
            skLineSegment(sketch, "E1691", {"start": v(-35.65, 50.46) * mm, "end": v(-35.53, 50.29) * mm});
            skLineSegment(sketch, "E1692", {"start": v(-35.53, 50.29) * mm, "end": v(-35.41, 50.11) * mm});
            skLineSegment(sketch, "E1693", {"start": v(-35.41, 50.11) * mm, "end": v(-35.3, 49.94) * mm});
            skLineSegment(sketch, "E1694", {"start": v(-35.3, 49.94) * mm, "end": v(-35.18, 49.77) * mm});
            skLineSegment(sketch, "E1695", {"start": v(-35.18, 49.77) * mm, "end": v(-35.06, 49.6) * mm});
            skLineSegment(sketch, "E1696", {"start": v(-35.06, 49.6) * mm, "end": v(-35.23, 49.48) * mm});
            skLineSegment(sketch, "E1697", {"start": v(-35.23, 49.48) * mm, "end": v(-35.4, 49.36) * mm});
            skLineSegment(sketch, "E1698", {"start": v(-35.4, 49.36) * mm, "end": v(-35.56, 49.24) * mm});
            skLineSegment(sketch, "E1699", {"start": v(-35.56, 49.24) * mm, "end": v(-35.73, 49.12) * mm});
            skLineSegment(sketch, "E1700", {"start": v(-35.73, 49.12) * mm, "end": v(-35.9, 49) * mm});
            skLineSegment(sketch, "E1701", {"start": v(-35.9, 49) * mm, "end": v(-36.07, 48.88) * mm});
            skLineSegment(sketch, "E1702", {"start": v(-36.07, 48.88) * mm, "end": v(-36.23, 48.76) * mm});
            skLineSegment(sketch, "E1703", {"start": v(-36.23, 48.76) * mm, "end": v(-36.4, 48.64) * mm});
            skLineSegment(sketch, "E1704", {"start": v(-36.4, 48.64) * mm, "end": v(-36.57, 48.52) * mm});
            skLineSegment(sketch, "E1705", {"start": v(-36.57, 48.52) * mm, "end": v(-36.74, 48.4) * mm});
            skLineSegment(sketch, "E1706", {"start": v(-36.74, 48.4) * mm, "end": v(-36.9, 48.28) * mm});
            skLineSegment(sketch, "E1707", {"start": v(-36.9, 48.28) * mm, "end": v(-36.99, 48.22) * mm});
            skLineSegment(sketch, "E1708", {"start": v(-36.99, 48.22) * mm, "end": v(-37.11, 48.38) * mm});
            skLineSegment(sketch, "E1709", {"start": v(-37.11, 48.38) * mm, "end": v(-37.23, 48.55) * mm});
            skLineSegment(sketch, "E1710", {"start": v(-37.23, 48.55) * mm, "end": v(-37.36, 48.72) * mm});
            skLineSegment(sketch, "E1711", {"start": v(-37.36, 48.72) * mm, "end": v(-37.48, 48.88) * mm});
            skLineSegment(sketch, "E1712", {"start": v(-37.48, 48.88) * mm, "end": v(-37.6, 49.05) * mm});
            skLineSegment(sketch, "E1713", {"start": v(-37.6, 49.05) * mm, "end": v(-37.73, 49.22) * mm});
            skLineSegment(sketch, "E1714", {"start": v(-37.73, 49.22) * mm, "end": v(-37.86, 49.38) * mm});
            skLineSegment(sketch, "E1715", {"start": v(-37.86, 49.38) * mm, "end": v(-37.98, 49.55) * mm});
            skLineSegment(sketch, "E1716", {"start": v(-37.98, 49.55) * mm, "end": v(-38.1, 49.72) * mm});
            skLineSegment(sketch, "E1717", {"start": v(-38.1, 49.72) * mm, "end": v(-38.23, 49.88) * mm});
            skLineSegment(sketch, "E1718", {"start": v(-38.23, 49.88) * mm, "end": v(-38.35, 50.05) * mm});
            skLineSegment(sketch, "E1719", {"start": v(-38.35, 50.05) * mm, "end": v(-38.48, 50.22) * mm});
            skLineSegment(sketch, "E1720", {"start": v(-38.48, 50.22) * mm, "end": v(-38.61, 50.4) * mm});
            skLineSegment(sketch, "E1721", {"start": v(-38.61, 50.4) * mm, "end": v(-38.77, 50.54) * mm});
            skLineSegment(sketch, "E1722", {"start": v(-38.77, 50.54) * mm, "end": v(-38.96, 50.64) * mm});
            skLineSegment(sketch, "E1723", {"start": v(-38.96, 50.64) * mm, "end": v(-39.17, 50.68) * mm});
            skLineSegment(sketch, "E1724", {"start": v(-39.17, 50.68) * mm, "end": v(-39.26, 50.68) * mm});
            skLineSegment(sketch, "E1725", {"start": v(-39.26, 50.68) * mm, "end": v(-39.47, 50.65) * mm});
            skLineSegment(sketch, "E1726", {"start": v(-39.47, 50.65) * mm, "end": v(-39.67, 50.56) * mm});
            skLineSegment(sketch, "E1727", {"start": v(-39.67, 50.56) * mm, "end": v(-39.83, 50.43) * mm});
            skLineSegment(sketch, "E1728", {"start": v(-39.83, 50.43) * mm, "end": v(-39.96, 50.25) * mm});
            skLineSegment(sketch, "E1729", {"start": v(-39.96, 50.25) * mm, "end": v(-40.04, 50.05) * mm});
            skLineSegment(sketch, "E1730", {"start": v(-40.04, 50.05) * mm, "end": v(-40.06, 49.84) * mm});
            skLineSegment(sketch, "E1731", {"start": v(-40.06, 49.84) * mm, "end": v(-40.02, 49.63) * mm});
            skLineSegment(sketch, "E1732", {"start": v(-40.02, 49.63) * mm, "end": v(-39.94, 49.43) * mm});
            skLineSegment(sketch, "E1733", {"start": v(-39.94, 49.43) * mm, "end": v(-39.81, 49.27) * mm});
            skLineSegment(sketch, "E1734", {"start": v(-39.81, 49.27) * mm, "end": v(-39.68, 49.1) * mm});
            skLineSegment(sketch, "E1735", {"start": v(-39.68, 49.1) * mm, "end": v(-39.56, 48.94) * mm});
            skLineSegment(sketch, "E1736", {"start": v(-39.56, 48.94) * mm, "end": v(-39.43, 48.78) * mm});
            skLineSegment(sketch, "E1737", {"start": v(-39.43, 48.78) * mm, "end": v(-39.3, 48.62) * mm});
            skLineSegment(sketch, "E1738", {"start": v(-39.3, 48.62) * mm, "end": v(-39.17, 48.45) * mm});
            skLineSegment(sketch, "E1739", {"start": v(-39.17, 48.45) * mm, "end": v(-39.04, 48.3) * mm});
            skLineSegment(sketch, "E1740", {"start": v(-39.04, 48.3) * mm, "end": v(-38.91, 48.13) * mm});
            skLineSegment(sketch, "E1741", {"start": v(-38.91, 48.13) * mm, "end": v(-38.78, 47.96) * mm});
            skLineSegment(sketch, "E1742", {"start": v(-38.78, 47.96) * mm, "end": v(-38.66, 47.8) * mm});
            skLineSegment(sketch, "E1743", {"start": v(-38.66, 47.8) * mm, "end": v(-38.53, 47.64) * mm});
            skLineSegment(sketch, "E1744", {"start": v(-38.53, 47.64) * mm, "end": v(-38.4, 47.47) * mm});
            skLineSegment(sketch, "E1745", {"start": v(-38.4, 47.47) * mm, "end": v(-38.27, 47.31) * mm});
            skLineSegment(sketch, "E1746", {"start": v(-38.27, 47.31) * mm, "end": v(-38.23, 47.26) * mm});
            skLineSegment(sketch, "E1747", {"start": v(-38.23, 47.26) * mm, "end": v(-38.4, 47.13) * mm});
            skLineSegment(sketch, "E1748", {"start": v(-38.4, 47.13) * mm, "end": v(-38.55, 47) * mm});
            skLineSegment(sketch, "E1749", {"start": v(-38.55, 47) * mm, "end": v(-38.71, 46.87) * mm});
            skLineSegment(sketch, "E1750", {"start": v(-38.71, 46.87) * mm, "end": v(-38.87, 46.74) * mm});
            skLineSegment(sketch, "E1751", {"start": v(-38.87, 46.74) * mm, "end": v(-39.03, 46.61) * mm});
            skLineSegment(sketch, "E1752", {"start": v(-39.03, 46.61) * mm, "end": v(-39.19, 46.48) * mm});
            skLineSegment(sketch, "E1753", {"start": v(-39.19, 46.48) * mm, "end": v(-39.35, 46.35) * mm});
            skLineSegment(sketch, "E1754", {"start": v(-39.35, 46.35) * mm, "end": v(-39.5, 46.22) * mm});
            skLineSegment(sketch, "E1755", {"start": v(-39.5, 46.22) * mm, "end": v(-39.67, 46.09) * mm});
            skLineSegment(sketch, "E1756", {"start": v(-39.67, 46.09) * mm, "end": v(-39.82, 45.96) * mm});
            skLineSegment(sketch, "E1757", {"start": v(-39.82, 45.96) * mm, "end": v(-39.98, 45.83) * mm});
            skLineSegment(sketch, "E1758", {"start": v(-39.98, 45.83) * mm, "end": v(-40.07, 45.76) * mm});
            skLineSegment(sketch, "E1759", {"start": v(-40.07, 45.76) * mm, "end": v(-40.2, 45.92) * mm});
            skLineSegment(sketch, "E1760", {"start": v(-40.2, 45.92) * mm, "end": v(-40.33, 46.07) * mm});
            skLineSegment(sketch, "E1761", {"start": v(-40.33, 46.07) * mm, "end": v(-40.47, 46.23) * mm});
            skLineSegment(sketch, "E1762", {"start": v(-40.47, 46.23) * mm, "end": v(-40.6, 46.4) * mm});
            skLineSegment(sketch, "E1763", {"start": v(-40.6, 46.4) * mm, "end": v(-40.74, 46.55) * mm});
            skLineSegment(sketch, "E1764", {"start": v(-40.74, 46.55) * mm, "end": v(-40.87, 46.7) * mm});
            skLineSegment(sketch, "E1765", {"start": v(-40.87, 46.7) * mm, "end": v(-41, 46.86) * mm});
            skLineSegment(sketch, "E1766", {"start": v(-41, 46.86) * mm, "end": v(-41.14, 47.02) * mm});
            skLineSegment(sketch, "E1767", {"start": v(-41.14, 47.02) * mm, "end": v(-41.28, 47.18) * mm});
            skLineSegment(sketch, "E1768", {"start": v(-41.28, 47.18) * mm, "end": v(-41.41, 47.34) * mm});
            skLineSegment(sketch, "E1769", {"start": v(-41.41, 47.34) * mm, "end": v(-41.55, 47.5) * mm});
            skLineSegment(sketch, "E1770", {"start": v(-41.55, 47.5) * mm, "end": v(-41.68, 47.66) * mm});
            skLineSegment(sketch, "E1771", {"start": v(-41.68, 47.66) * mm, "end": v(-41.83, 47.82) * mm});
            skLineSegment(sketch, "E1772", {"start": v(-41.83, 47.82) * mm, "end": v(-42, 47.96) * mm});
            skLineSegment(sketch, "E1773", {"start": v(-42, 47.96) * mm, "end": v(-42.2, 48.04) * mm});
            skLineSegment(sketch, "E1774", {"start": v(-42.2, 48.04) * mm, "end": v(-42.4, 48.07) * mm});
            skLineSegment(sketch, "E1775", {"start": v(-42.4, 48.07) * mm, "end": v(-42.62, 48.05) * mm});
            skLineSegment(sketch, "E1776", {"start": v(-42.62, 48.05) * mm, "end": v(-42.82, 47.97) * mm});
            skLineSegment(sketch, "E1777", {"start": v(-42.82, 47.97) * mm, "end": v(-43, 47.84) * mm});
            skLineSegment(sketch, "E1778", {"start": v(-43, 47.84) * mm, "end": v(-43.12, 47.67) * mm});
            skLineSegment(sketch, "E1779", {"start": v(-43.12, 47.67) * mm, "end": v(-43.2, 47.48) * mm});
            skLineSegment(sketch, "E1780", {"start": v(-43.2, 47.48) * mm, "end": v(-43.24, 47.26) * mm});
            skLineSegment(sketch, "E1781", {"start": v(-43.24, 47.26) * mm, "end": v(-43.21, 47.05) * mm});
            skLineSegment(sketch, "E1782", {"start": v(-43.21, 47.05) * mm, "end": v(-43.13, 46.85) * mm});
            skLineSegment(sketch, "E1783", {"start": v(-43.13, 46.85) * mm, "end": v(-43, 46.69) * mm});
            skLineSegment(sketch, "E1784", {"start": v(-43, 46.69) * mm, "end": v(-42.87, 46.53) * mm});
            skLineSegment(sketch, "E1785", {"start": v(-42.87, 46.53) * mm, "end": v(-42.73, 46.38) * mm});
            skLineSegment(sketch, "E1786", {"start": v(-42.73, 46.38) * mm, "end": v(-42.6, 46.23) * mm});
            skLineSegment(sketch, "E1787", {"start": v(-42.6, 46.23) * mm, "end": v(-42.46, 46.07) * mm});
            skLineSegment(sketch, "E1788", {"start": v(-42.46, 46.07) * mm, "end": v(-42.32, 45.92) * mm});
            skLineSegment(sketch, "E1789", {"start": v(-42.32, 45.92) * mm, "end": v(-42.18, 45.76) * mm});
            skLineSegment(sketch, "E1790", {"start": v(-42.18, 45.76) * mm, "end": v(-42.04, 45.61) * mm});
            skLineSegment(sketch, "E1791", {"start": v(-42.04, 45.61) * mm, "end": v(-41.9, 45.45) * mm});
            skLineSegment(sketch, "E1792", {"start": v(-41.9, 45.45) * mm, "end": v(-41.76, 45.3) * mm});
            skLineSegment(sketch, "E1793", {"start": v(-41.76, 45.3) * mm, "end": v(-41.62, 45.15) * mm});
            skLineSegment(sketch, "E1794", {"start": v(-41.62, 45.15) * mm, "end": v(-41.48, 45) * mm});
            skLineSegment(sketch, "E1795", {"start": v(-41.48, 45) * mm, "end": v(-41.34, 44.84) * mm});
            skLineSegment(sketch, "E1796", {"start": v(-41.34, 44.84) * mm, "end": v(-41.24, 44.73) * mm});
            skLineSegment(sketch, "E1797", {"start": v(-41.24, 44.73) * mm, "end": v(-41.4, 44.58) * mm});
            skLineSegment(sketch, "E1798", {"start": v(-41.4, 44.58) * mm, "end": v(-41.54, 44.44) * mm});
            skLineSegment(sketch, "E1799", {"start": v(-41.54, 44.44) * mm, "end": v(-41.7, 44.3) * mm});
            skLineSegment(sketch, "E1800", {"start": v(-41.7, 44.3) * mm, "end": v(-41.85, 44.16) * mm});
            skLineSegment(sketch, "E1801", {"start": v(-41.85, 44.16) * mm, "end": v(-42, 44.02) * mm});
            skLineSegment(sketch, "E1802", {"start": v(-42, 44.02) * mm, "end": v(-42.15, 43.88) * mm});
            skLineSegment(sketch, "E1803", {"start": v(-42.15, 43.88) * mm, "end": v(-42.3, 43.74) * mm});
            skLineSegment(sketch, "E1804", {"start": v(-42.3, 43.74) * mm, "end": v(-42.45, 43.6) * mm});
            skLineSegment(sketch, "E1805", {"start": v(-42.45, 43.6) * mm, "end": v(-42.6, 43.46) * mm});
            skLineSegment(sketch, "E1806", {"start": v(-42.6, 43.46) * mm, "end": v(-42.75, 43.32) * mm});
            skLineSegment(sketch, "E1807", {"start": v(-42.75, 43.32) * mm, "end": v(-42.9, 43.18) * mm});
            skLineSegment(sketch, "E1808", {"start": v(-42.9, 43.18) * mm, "end": v(-42.97, 43.1) * mm});
            skLineSegment(sketch, "E1809", {"start": v(-42.97, 43.1) * mm, "end": v(-43.12, 43.25) * mm});
            skLineSegment(sketch, "E1810", {"start": v(-43.12, 43.25) * mm, "end": v(-43.26, 43.4) * mm});
            skLineSegment(sketch, "E1811", {"start": v(-43.26, 43.4) * mm, "end": v(-43.4, 43.55) * mm});
            skLineSegment(sketch, "E1812", {"start": v(-43.4, 43.55) * mm, "end": v(-43.55, 43.7) * mm});
            skLineSegment(sketch, "E1813", {"start": v(-43.55, 43.7) * mm, "end": v(-43.7, 43.85) * mm});
            skLineSegment(sketch, "E1814", {"start": v(-43.7, 43.85) * mm, "end": v(-43.84, 44) * mm});
            skLineSegment(sketch, "E1815", {"start": v(-43.84, 44) * mm, "end": v(-43.99, 44.15) * mm});
            skLineSegment(sketch, "E1816", {"start": v(-43.99, 44.15) * mm, "end": v(-44.13, 44.3) * mm});
            skLineSegment(sketch, "E1817", {"start": v(-44.13, 44.3) * mm, "end": v(-44.28, 44.44) * mm});
            skLineSegment(sketch, "E1818", {"start": v(-44.28, 44.44) * mm, "end": v(-44.42, 44.6) * mm});
            skLineSegment(sketch, "E1819", {"start": v(-44.42, 44.6) * mm, "end": v(-44.57, 44.74) * mm});
            skLineSegment(sketch, "E1820", {"start": v(-44.57, 44.74) * mm, "end": v(-44.71, 44.9) * mm});
            skLineSegment(sketch, "E1821", {"start": v(-44.71, 44.9) * mm, "end": v(-44.87, 45.05) * mm});
            skLineSegment(sketch, "E1822", {"start": v(-44.87, 45.05) * mm, "end": v(-45.05, 45.17) * mm});
            skLineSegment(sketch, "E1823", {"start": v(-45.05, 45.17) * mm, "end": v(-45.25, 45.24) * mm});
            skLineSegment(sketch, "E1824", {"start": v(-45.25, 45.24) * mm, "end": v(-45.42, 45.26) * mm});
            skLineSegment(sketch, "E1825", {"start": v(-45.42, 45.26) * mm, "end": v(-45.63, 45.24) * mm});
            skLineSegment(sketch, "E1826", {"start": v(-45.63, 45.24) * mm, "end": v(-45.83, 45.15) * mm});
            skLineSegment(sketch, "E1827", {"start": v(-45.83, 45.15) * mm, "end": v(-46, 45.02) * mm});
            skLineSegment(sketch, "E1828", {"start": v(-46, 45.02) * mm, "end": v(-46.13, 44.85) * mm});
            skLineSegment(sketch, "E1829", {"start": v(-46.13, 44.85) * mm, "end": v(-46.21, 44.65) * mm});
            skLineSegment(sketch, "E1830", {"start": v(-46.21, 44.65) * mm, "end": v(-46.24, 44.44) * mm});
            skLineSegment(sketch, "E1831", {"start": v(-46.24, 44.44) * mm, "end": v(-46.21, 44.23) * mm});
            skLineSegment(sketch, "E1832", {"start": v(-46.21, 44.23) * mm, "end": v(-46.13, 44.03) * mm});
            skLineSegment(sketch, "E1833", {"start": v(-46.13, 44.03) * mm, "end": v(-46, 43.86) * mm});
            skLineSegment(sketch, "E1834", {"start": v(-46, 43.86) * mm, "end": v(-45.85, 43.72) * mm});
            skLineSegment(sketch, "E1835", {"start": v(-45.85, 43.72) * mm, "end": v(-45.7, 43.57) * mm});
            skLineSegment(sketch, "E1836", {"start": v(-45.7, 43.57) * mm, "end": v(-45.55, 43.43) * mm});
            skLineSegment(sketch, "E1837", {"start": v(-45.55, 43.43) * mm, "end": v(-45.4, 43.28) * mm});
            skLineSegment(sketch, "E1838", {"start": v(-45.4, 43.28) * mm, "end": v(-45.26, 43.14) * mm});
            skLineSegment(sketch, "E1839", {"start": v(-45.26, 43.14) * mm, "end": v(-45.1, 43) * mm});
            skLineSegment(sketch, "E1840", {"start": v(-45.1, 43) * mm, "end": v(-44.96, 42.85) * mm});
            skLineSegment(sketch, "E1841", {"start": v(-44.96, 42.85) * mm, "end": v(-44.8, 42.7) * mm});
            skLineSegment(sketch, "E1842", {"start": v(-44.8, 42.7) * mm, "end": v(-44.66, 42.56) * mm});
            skLineSegment(sketch, "E1843", {"start": v(-44.66, 42.56) * mm, "end": v(-44.5, 42.41) * mm});
            skLineSegment(sketch, "E1844", {"start": v(-44.5, 42.41) * mm, "end": v(-44.36, 42.27) * mm});
            skLineSegment(sketch, "E1845", {"start": v(-44.36, 42.27) * mm, "end": v(-44.21, 42.12) * mm});
            skLineSegment(sketch, "E1846", {"start": v(-44.21, 42.12) * mm, "end": v(-44.08, 42) * mm});
            skLineSegment(sketch, "E1847", {"start": v(-44.08, 42) * mm, "end": v(-44.22, 41.85) * mm});
            skLineSegment(sketch, "E1848", {"start": v(-44.22, 41.85) * mm, "end": v(-44.36, 41.7) * mm});
            skLineSegment(sketch, "E1849", {"start": v(-44.36, 41.7) * mm, "end": v(-44.5, 41.55) * mm});
            skLineSegment(sketch, "E1850", {"start": v(-44.5, 41.55) * mm, "end": v(-44.65, 41.4) * mm});
            skLineSegment(sketch, "E1851", {"start": v(-44.65, 41.4) * mm, "end": v(-44.79, 41.24) * mm});
            skLineSegment(sketch, "E1852", {"start": v(-44.79, 41.24) * mm, "end": v(-44.93, 41.1) * mm});
            skLineSegment(sketch, "E1853", {"start": v(-44.93, 41.1) * mm, "end": v(-45.07, 40.94) * mm});
            skLineSegment(sketch, "E1854", {"start": v(-45.07, 40.94) * mm, "end": v(-45.2, 40.8) * mm});
            skLineSegment(sketch, "E1855", {"start": v(-45.2, 40.8) * mm, "end": v(-45.35, 40.64) * mm});
            skLineSegment(sketch, "E1856", {"start": v(-45.35, 40.64) * mm, "end": v(-45.5, 40.5) * mm});
            skLineSegment(sketch, "E1857", {"start": v(-45.5, 40.5) * mm, "end": v(-45.63, 40.34) * mm});
            skLineSegment(sketch, "E1858", {"start": v(-45.63, 40.34) * mm, "end": v(-45.7, 40.27) * mm});
            skLineSegment(sketch, "E1859", {"start": v(-45.7, 40.27) * mm, "end": v(-45.86, 40.4) * mm});
            skLineSegment(sketch, "E1860", {"start": v(-45.86, 40.4) * mm, "end": v(-46, 40.54) * mm});
            skLineSegment(sketch, "E1861", {"start": v(-46, 40.54) * mm, "end": v(-46.17, 40.68) * mm});
            skLineSegment(sketch, "E1862", {"start": v(-46.17, 40.68) * mm, "end": v(-46.32, 40.82) * mm});
            skLineSegment(sketch, "E1863", {"start": v(-46.32, 40.82) * mm, "end": v(-46.47, 40.96) * mm});
            skLineSegment(sketch, "E1864", {"start": v(-46.47, 40.96) * mm, "end": v(-46.63, 41.1) * mm});
            skLineSegment(sketch, "E1865", {"start": v(-46.63, 41.1) * mm, "end": v(-46.78, 41.24) * mm});
            skLineSegment(sketch, "E1866", {"start": v(-46.78, 41.24) * mm, "end": v(-46.94, 41.38) * mm});
            skLineSegment(sketch, "E1867", {"start": v(-46.94, 41.38) * mm, "end": v(-47.1, 41.52) * mm});
            skLineSegment(sketch, "E1868", {"start": v(-47.1, 41.52) * mm, "end": v(-47.25, 41.66) * mm});
            skLineSegment(sketch, "E1869", {"start": v(-47.25, 41.66) * mm, "end": v(-47.4, 41.8) * mm});
            skLineSegment(sketch, "E1870", {"start": v(-47.4, 41.8) * mm, "end": v(-47.56, 41.93) * mm});
            skLineSegment(sketch, "E1871", {"start": v(-47.56, 41.93) * mm, "end": v(-47.72, 42.08) * mm});
            skLineSegment(sketch, "E1872", {"start": v(-47.72, 42.08) * mm, "end": v(-47.9, 42.2) * mm});
            skLineSegment(sketch, "E1873", {"start": v(-47.9, 42.2) * mm, "end": v(-48.11, 42.25) * mm});
            skLineSegment(sketch, "E1874", {"start": v(-48.11, 42.25) * mm, "end": v(-48.24, 42.26) * mm});
            skLineSegment(sketch, "E1875", {"start": v(-48.24, 42.26) * mm, "end": v(-48.45, 42.23) * mm});
            skLineSegment(sketch, "E1876", {"start": v(-48.45, 42.23) * mm, "end": v(-48.65, 42.15) * mm});
            skLineSegment(sketch, "E1877", {"start": v(-48.65, 42.15) * mm, "end": v(-48.82, 42.01) * mm});
            skLineSegment(sketch, "E1878", {"start": v(-48.82, 42.01) * mm, "end": v(-48.95, 41.84) * mm});
            skLineSegment(sketch, "E1879", {"start": v(-48.95, 41.84) * mm, "end": v(-49.03, 41.64) * mm});
            skLineSegment(sketch, "E1880", {"start": v(-49.03, 41.64) * mm, "end": v(-49.05, 41.43) * mm});
            skLineSegment(sketch, "E1881", {"start": v(-49.05, 41.43) * mm, "end": v(-49.02, 41.22) * mm});
            skLineSegment(sketch, "E1882", {"start": v(-49.02, 41.22) * mm, "end": v(-48.93, 41.02) * mm});
            skLineSegment(sketch, "E1883", {"start": v(-48.93, 41.02) * mm, "end": v(-48.8, 40.85) * mm});
            skLineSegment(sketch, "E1884", {"start": v(-48.8, 40.85) * mm, "end": v(-48.63, 40.7) * mm});
            skLineSegment(sketch, "E1885", {"start": v(-48.63, 40.7) * mm, "end": v(-48.48, 40.57) * mm});
            skLineSegment(sketch, "E1886", {"start": v(-48.48, 40.57) * mm, "end": v(-48.32, 40.44) * mm});
            skLineSegment(sketch, "E1887", {"start": v(-48.32, 40.44) * mm, "end": v(-48.16, 40.3) * mm});
            skLineSegment(sketch, "E1888", {"start": v(-48.16, 40.3) * mm, "end": v(-48, 40.17) * mm});
            skLineSegment(sketch, "E1889", {"start": v(-48, 40.17) * mm, "end": v(-47.85, 40.03) * mm});
            skLineSegment(sketch, "E1890", {"start": v(-47.85, 40.03) * mm, "end": v(-47.69, 39.9) * mm});
            skLineSegment(sketch, "E1891", {"start": v(-47.69, 39.9) * mm, "end": v(-47.53, 39.76) * mm});
            skLineSegment(sketch, "E1892", {"start": v(-47.53, 39.76) * mm, "end": v(-47.37, 39.63) * mm});
            skLineSegment(sketch, "E1893", {"start": v(-47.37, 39.63) * mm, "end": v(-47.21, 39.5) * mm});
            skLineSegment(sketch, "E1894", {"start": v(-47.21, 39.5) * mm, "end": v(-47.05, 39.36) * mm});
            skLineSegment(sketch, "E1895", {"start": v(-47.05, 39.36) * mm, "end": v(-46.9, 39.22) * mm});
            skLineSegment(sketch, "E1896", {"start": v(-46.9, 39.22) * mm, "end": v(-46.74, 39.09) * mm});
            skLineSegment(sketch, "E1897", {"start": v(-46.74, 39.09) * mm, "end": v(-46.87, 38.93) * mm});
            skLineSegment(sketch, "E1898", {"start": v(-46.87, 38.93) * mm, "end": v(-47, 38.77) * mm});
            skLineSegment(sketch, "E1899", {"start": v(-47, 38.77) * mm, "end": v(-47.13, 38.6) * mm});
            skLineSegment(sketch, "E1900", {"start": v(-47.13, 38.6) * mm, "end": v(-47.26, 38.45) * mm});
            skLineSegment(sketch, "E1901", {"start": v(-47.26, 38.45) * mm, "end": v(-47.4, 38.3) * mm});
            skLineSegment(sketch, "E1902", {"start": v(-47.4, 38.3) * mm, "end": v(-47.52, 38.13) * mm});
            skLineSegment(sketch, "E1903", {"start": v(-47.52, 38.13) * mm, "end": v(-47.65, 37.97) * mm});
            skLineSegment(sketch, "E1904", {"start": v(-47.65, 37.97) * mm, "end": v(-47.78, 37.81) * mm});
            skLineSegment(sketch, "E1905", {"start": v(-47.78, 37.81) * mm, "end": v(-47.91, 37.65) * mm});
            skLineSegment(sketch, "E1906", {"start": v(-47.91, 37.65) * mm, "end": v(-48.04, 37.5) * mm});
            skLineSegment(sketch, "E1907", {"start": v(-48.04, 37.5) * mm, "end": v(-48.17, 37.34) * mm});
            skLineSegment(sketch, "E1908", {"start": v(-48.17, 37.34) * mm, "end": v(-48.24, 37.25) * mm});
            skLineSegment(sketch, "E1909", {"start": v(-48.24, 37.25) * mm, "end": v(-48.4, 37.38) * mm});
            skLineSegment(sketch, "E1910", {"start": v(-48.4, 37.38) * mm, "end": v(-48.56, 37.5) * mm});
            skLineSegment(sketch, "E1911", {"start": v(-48.56, 37.5) * mm, "end": v(-48.73, 37.64) * mm});
            skLineSegment(sketch, "E1912", {"start": v(-48.73, 37.64) * mm, "end": v(-48.9, 37.77) * mm});
            skLineSegment(sketch, "E1913", {"start": v(-48.9, 37.77) * mm, "end": v(-49.05, 37.9) * mm});
            skLineSegment(sketch, "E1914", {"start": v(-49.05, 37.9) * mm, "end": v(-49.22, 38.03) * mm});
            skLineSegment(sketch, "E1915", {"start": v(-49.22, 38.03) * mm, "end": v(-49.38, 38.15) * mm});
            skLineSegment(sketch, "E1916", {"start": v(-49.38, 38.15) * mm, "end": v(-49.54, 38.28) * mm});
            skLineSegment(sketch, "E1917", {"start": v(-49.54, 38.28) * mm, "end": v(-49.71, 38.41) * mm});
            skLineSegment(sketch, "E1918", {"start": v(-49.71, 38.41) * mm, "end": v(-49.87, 38.54) * mm});
            skLineSegment(sketch, "E1919", {"start": v(-49.87, 38.54) * mm, "end": v(-50.03, 38.67) * mm});
            skLineSegment(sketch, "E1920", {"start": v(-50.03, 38.67) * mm, "end": v(-50.2, 38.8) * mm});
            skLineSegment(sketch, "E1921", {"start": v(-50.2, 38.8) * mm, "end": v(-50.37, 38.93) * mm});
            skLineSegment(sketch, "E1922", {"start": v(-50.37, 38.93) * mm, "end": v(-50.57, 39.03) * mm});
            skLineSegment(sketch, "E1923", {"start": v(-50.57, 39.03) * mm, "end": v(-50.77, 39.08) * mm});
            skLineSegment(sketch, "E1924", {"start": v(-50.77, 39.08) * mm, "end": v(-50.86, 39.08) * mm});
            skLineSegment(sketch, "E1925", {"start": v(-50.86, 39.08) * mm, "end": v(-51.07, 39.05) * mm});
            skLineSegment(sketch, "E1926", {"start": v(-51.07, 39.05) * mm, "end": v(-51.27, 38.96) * mm});
            skLineSegment(sketch, "E1927", {"start": v(-51.27, 38.96) * mm, "end": v(-51.44, 38.83) * mm});
            skLineSegment(sketch, "E1928", {"start": v(-51.44, 38.83) * mm, "end": v(-51.56, 38.65) * mm});
            skLineSegment(sketch, "E1929", {"start": v(-51.56, 38.65) * mm, "end": v(-51.64, 38.45) * mm});
            skLineSegment(sketch, "E1930", {"start": v(-51.64, 38.45) * mm, "end": v(-51.66, 38.24) * mm});
            skLineSegment(sketch, "E1931", {"start": v(-51.66, 38.24) * mm, "end": v(-51.63, 38.03) * mm});
            skLineSegment(sketch, "E1932", {"start": v(-51.63, 38.03) * mm, "end": v(-51.54, 37.83) * mm});
            skLineSegment(sketch, "E1933", {"start": v(-51.54, 37.83) * mm, "end": v(-51.4, 37.67) * mm});
            skLineSegment(sketch, "E1934", {"start": v(-51.4, 37.67) * mm, "end": v(-51.24, 37.54) * mm});
            skLineSegment(sketch, "E1935", {"start": v(-51.24, 37.54) * mm, "end": v(-51.08, 37.41) * mm});
            skLineSegment(sketch, "E1936", {"start": v(-51.08, 37.41) * mm, "end": v(-50.9, 37.29) * mm});
            skLineSegment(sketch, "E1937", {"start": v(-50.9, 37.29) * mm, "end": v(-50.74, 37.17) * mm});
            skLineSegment(sketch, "E1938", {"start": v(-50.74, 37.17) * mm, "end": v(-50.58, 37.04) * mm});
            skLineSegment(sketch, "E1939", {"start": v(-50.58, 37.04) * mm, "end": v(-50.4, 36.92) * mm});
            skLineSegment(sketch, "E1940", {"start": v(-50.4, 36.92) * mm, "end": v(-50.24, 36.8) * mm});
            skLineSegment(sketch, "E1941", {"start": v(-50.24, 36.8) * mm, "end": v(-50.08, 36.67) * mm});
            skLineSegment(sketch, "E1942", {"start": v(-50.08, 36.67) * mm, "end": v(-49.9, 36.54) * mm});
            skLineSegment(sketch, "E1943", {"start": v(-49.9, 36.54) * mm, "end": v(-49.74, 36.42) * mm});
            skLineSegment(sketch, "E1944", {"start": v(-49.74, 36.42) * mm, "end": v(-49.58, 36.3) * mm});
            skLineSegment(sketch, "E1945", {"start": v(-49.58, 36.3) * mm, "end": v(-49.4, 36.17) * mm});
            skLineSegment(sketch, "E1946", {"start": v(-49.4, 36.17) * mm, "end": v(-49.24, 36.05) * mm});
            skLineSegment(sketch, "E1947", {"start": v(-49.24, 36.05) * mm, "end": v(-49.2, 36.01) * mm});
            skLineSegment(sketch, "E1948", {"start": v(-49.2, 36.01) * mm, "end": v(-49.32, 35.84) * mm});
            skLineSegment(sketch, "E1949", {"start": v(-49.32, 35.84) * mm, "end": v(-49.44, 35.68) * mm});
            skLineSegment(sketch, "E1950", {"start": v(-49.44, 35.68) * mm, "end": v(-49.56, 35.5) * mm});
            skLineSegment(sketch, "E1951", {"start": v(-49.56, 35.5) * mm, "end": v(-49.68, 35.34) * mm});
            skLineSegment(sketch, "E1952", {"start": v(-49.68, 35.34) * mm, "end": v(-49.8, 35.17) * mm});
            skLineSegment(sketch, "E1953", {"start": v(-49.8, 35.17) * mm, "end": v(-49.92, 35) * mm});
            skLineSegment(sketch, "E1954", {"start": v(-49.92, 35) * mm, "end": v(-50.04, 34.84) * mm});
            skLineSegment(sketch, "E1955", {"start": v(-50.04, 34.84) * mm, "end": v(-50.16, 34.67) * mm});
            skLineSegment(sketch, "E1956", {"start": v(-50.16, 34.67) * mm, "end": v(-50.28, 34.5) * mm});
            skLineSegment(sketch, "E1957", {"start": v(-50.28, 34.5) * mm, "end": v(-50.4, 34.34) * mm});
            skLineSegment(sketch, "E1958", {"start": v(-50.4, 34.34) * mm, "end": v(-50.52, 34.17) * mm});
            skLineSegment(sketch, "E1959", {"start": v(-50.52, 34.17) * mm, "end": v(-50.58, 34.08) * mm});
            skLineSegment(sketch, "E1960", {"start": v(-50.58, 34.08) * mm, "end": v(-50.75, 34.2) * mm});
            skLineSegment(sketch, "E1961", {"start": v(-50.75, 34.2) * mm, "end": v(-50.92, 34.32) * mm});
            skLineSegment(sketch, "E1962", {"start": v(-50.92, 34.32) * mm, "end": v(-51.1, 34.44) * mm});
            skLineSegment(sketch, "E1963", {"start": v(-51.1, 34.44) * mm, "end": v(-51.26, 34.55) * mm});
            skLineSegment(sketch, "E1964", {"start": v(-51.26, 34.55) * mm, "end": v(-51.43, 34.67) * mm});
            skLineSegment(sketch, "E1965", {"start": v(-51.43, 34.67) * mm, "end": v(-51.6, 34.79) * mm});
            skLineSegment(sketch, "E1966", {"start": v(-51.6, 34.79) * mm, "end": v(-51.77, 34.9) * mm});
            skLineSegment(sketch, "E1967", {"start": v(-51.77, 34.9) * mm, "end": v(-51.94, 35.02) * mm});
            skLineSegment(sketch, "E1968", {"start": v(-51.94, 35.02) * mm, "end": v(-52.12, 35.14) * mm});
            skLineSegment(sketch, "E1969", {"start": v(-52.12, 35.14) * mm, "end": v(-52.29, 35.26) * mm});
            skLineSegment(sketch, "E1970", {"start": v(-52.29, 35.26) * mm, "end": v(-52.46, 35.38) * mm});
            skLineSegment(sketch, "E1971", {"start": v(-52.46, 35.38) * mm, "end": v(-52.63, 35.5) * mm});
            skLineSegment(sketch, "E1972", {"start": v(-52.63, 35.5) * mm, "end": v(-52.82, 35.62) * mm});
            skLineSegment(sketch, "E1973", {"start": v(-52.82, 35.62) * mm, "end": v(-53.01, 35.7) * mm});
            skLineSegment(sketch, "E1974", {"start": v(-53.01, 35.7) * mm, "end": v(-53.22, 35.74) * mm});
            skLineSegment(sketch, "E1975", {"start": v(-53.22, 35.74) * mm, "end": v(-53.44, 35.71) * mm});
            skLineSegment(sketch, "E1976", {"start": v(-53.44, 35.71) * mm, "end": v(-53.64, 35.63) * mm});
            skLineSegment(sketch, "E1977", {"start": v(-53.64, 35.63) * mm, "end": v(-53.8, 35.5) * mm});
            skLineSegment(sketch, "E1978", {"start": v(-53.8, 35.5) * mm, "end": v(-53.94, 35.34) * mm});
            skLineSegment(sketch, "E1979", {"start": v(-53.94, 35.34) * mm, "end": v(-54.03, 35.14) * mm});
            skLineSegment(sketch, "E1980", {"start": v(-54.03, 35.14) * mm, "end": v(-54.06, 34.93) * mm});
            skLineSegment(sketch, "E1981", {"start": v(-54.06, 34.93) * mm, "end": v(-54.03, 34.71) * mm});
            skLineSegment(sketch, "E1982", {"start": v(-54.03, 34.71) * mm, "end": v(-53.95, 34.52) * mm});
            skLineSegment(sketch, "E1983", {"start": v(-53.95, 34.52) * mm, "end": v(-53.82, 34.34) * mm});
            skLineSegment(sketch, "E1984", {"start": v(-53.82, 34.34) * mm, "end": v(-53.66, 34.22) * mm});
            skLineSegment(sketch, "E1985", {"start": v(-53.66, 34.22) * mm, "end": v(-53.49, 34.1) * mm});
            skLineSegment(sketch, "E1986", {"start": v(-53.49, 34.1) * mm, "end": v(-53.32, 34) * mm});
            skLineSegment(sketch, "E1987", {"start": v(-53.32, 34) * mm, "end": v(-53.14, 33.88) * mm});
            skLineSegment(sketch, "E1988", {"start": v(-53.14, 33.88) * mm, "end": v(-52.97, 33.77) * mm});
            skLineSegment(sketch, "E1989", {"start": v(-52.97, 33.77) * mm, "end": v(-52.8, 33.65) * mm});
            skLineSegment(sketch, "E1990", {"start": v(-52.8, 33.65) * mm, "end": v(-52.62, 33.54) * mm});
            skLineSegment(sketch, "E1991", {"start": v(-52.62, 33.54) * mm, "end": v(-52.45, 33.43) * mm});
            skLineSegment(sketch, "E1992", {"start": v(-52.45, 33.43) * mm, "end": v(-52.27, 33.31) * mm});
            skLineSegment(sketch, "E1993", {"start": v(-52.27, 33.31) * mm, "end": v(-52.1, 33.2) * mm});
            skLineSegment(sketch, "E1994", {"start": v(-52.1, 33.2) * mm, "end": v(-51.92, 33.09) * mm});
            skLineSegment(sketch, "E1995", {"start": v(-51.92, 33.09) * mm, "end": v(-51.75, 32.97) * mm});
            skLineSegment(sketch, "E1996", {"start": v(-51.75, 32.97) * mm, "end": v(-51.57, 32.86) * mm});
            skLineSegment(sketch, "E1997", {"start": v(-51.57, 32.86) * mm, "end": v(-51.45, 32.78) * mm});
            skLineSegment(sketch, "E1998", {"start": v(-51.45, 32.78) * mm, "end": v(-51.56, 32.6) * mm});
            skLineSegment(sketch, "E1999", {"start": v(-51.56, 32.6) * mm, "end": v(-51.67, 32.43) * mm});
            skLineSegment(sketch, "E2000", {"start": v(-51.67, 32.43) * mm, "end": v(-51.77, 32.26) * mm});
            skLineSegment(sketch, "E2001", {"start": v(-51.77, 32.26) * mm, "end": v(-51.88, 32.08) * mm});
            skLineSegment(sketch, "E2002", {"start": v(-51.88, 32.08) * mm, "end": v(-52, 31.9) * mm});
            skLineSegment(sketch, "E2003", {"start": v(-52, 31.9) * mm, "end": v(-52.1, 31.73) * mm});
            skLineSegment(sketch, "E2004", {"start": v(-52.1, 31.73) * mm, "end": v(-52.2, 31.56) * mm});
            skLineSegment(sketch, "E2005", {"start": v(-52.2, 31.56) * mm, "end": v(-52.32, 31.38) * mm});
            skLineSegment(sketch, "E2006", {"start": v(-52.32, 31.38) * mm, "end": v(-52.43, 31.2) * mm});
            skLineSegment(sketch, "E2007", {"start": v(-52.43, 31.2) * mm, "end": v(-52.54, 31.03) * mm});
            skLineSegment(sketch, "E2008", {"start": v(-52.54, 31.03) * mm, "end": v(-52.64, 30.86) * mm});
            skLineSegment(sketch, "E2009", {"start": v(-52.64, 30.86) * mm, "end": v(-52.7, 30.77) * mm});
            skLineSegment(sketch, "E2010", {"start": v(-52.7, 30.77) * mm, "end": v(-52.88, 30.87) * mm});
            skLineSegment(sketch, "E2011", {"start": v(-52.88, 30.87) * mm, "end": v(-53.05, 30.98) * mm});
            skLineSegment(sketch, "E2012", {"start": v(-53.05, 30.98) * mm, "end": v(-53.24, 31.09) * mm});
            skLineSegment(sketch, "E2013", {"start": v(-53.24, 31.09) * mm, "end": v(-53.41, 31.2) * mm});
            skLineSegment(sketch, "E2014", {"start": v(-53.41, 31.2) * mm, "end": v(-53.59, 31.3) * mm});
            skLineSegment(sketch, "E2015", {"start": v(-53.59, 31.3) * mm, "end": v(-53.77, 31.4) * mm});
            skLineSegment(sketch, "E2016", {"start": v(-53.77, 31.4) * mm, "end": v(-53.95, 31.5) * mm});
            skLineSegment(sketch, "E2017", {"start": v(-53.95, 31.5) * mm, "end": v(-54.13, 31.61) * mm});
            skLineSegment(sketch, "E2018", {"start": v(-54.13, 31.61) * mm, "end": v(-54.3, 31.72) * mm});
            skLineSegment(sketch, "E2019", {"start": v(-54.3, 31.72) * mm, "end": v(-54.48, 31.83) * mm});
            skLineSegment(sketch, "E2020", {"start": v(-54.48, 31.83) * mm, "end": v(-54.66, 31.93) * mm});
            skLineSegment(sketch, "E2021", {"start": v(-54.66, 31.93) * mm, "end": v(-54.84, 32.04) * mm});
            skLineSegment(sketch, "E2022", {"start": v(-54.84, 32.04) * mm, "end": v(-55.03, 32.15) * mm});
            skLineSegment(sketch, "E2023", {"start": v(-55.03, 32.15) * mm, "end": v(-55.24, 32.23) * mm});
            skLineSegment(sketch, "E2024", {"start": v(-55.24, 32.23) * mm, "end": v(-55.4, 32.25) * mm});
            skLineSegment(sketch, "E2025", {"start": v(-55.4, 32.25) * mm, "end": v(-55.62, 32.22) * mm});
            skLineSegment(sketch, "E2026", {"start": v(-55.62, 32.22) * mm, "end": v(-55.82, 32.14) * mm});
            skLineSegment(sketch, "E2027", {"start": v(-55.82, 32.14) * mm, "end": v(-55.99, 32) * mm});
            skLineSegment(sketch, "E2028", {"start": v(-55.99, 32) * mm, "end": v(-56.12, 31.84) * mm});
            skLineSegment(sketch, "E2029", {"start": v(-56.12, 31.84) * mm, "end": v(-56.2, 31.64) * mm});
            skLineSegment(sketch, "E2030", {"start": v(-56.2, 31.64) * mm, "end": v(-56.23, 31.42) * mm});
            skLineSegment(sketch, "E2031", {"start": v(-56.23, 31.42) * mm, "end": v(-56.2, 31.21) * mm});
            skLineSegment(sketch, "E2032", {"start": v(-56.2, 31.21) * mm, "end": v(-56.12, 31.01) * mm});
            skLineSegment(sketch, "E2033", {"start": v(-56.12, 31.01) * mm, "end": v(-55.99, 30.84) * mm});
            skLineSegment(sketch, "E2034", {"start": v(-55.99, 30.84) * mm, "end": v(-55.82, 30.71) * mm});
            skLineSegment(sketch, "E2035", {"start": v(-55.82, 30.71) * mm, "end": v(-55.64, 30.61) * mm});
            skLineSegment(sketch, "E2036", {"start": v(-55.64, 30.61) * mm, "end": v(-55.46, 30.51) * mm});
            skLineSegment(sketch, "E2037", {"start": v(-55.46, 30.51) * mm, "end": v(-55.27, 30.4) * mm});
            skLineSegment(sketch, "E2038", {"start": v(-55.27, 30.4) * mm, "end": v(-55.1, 30.3) * mm});
            skLineSegment(sketch, "E2039", {"start": v(-55.1, 30.3) * mm, "end": v(-54.91, 30.2) * mm});
            skLineSegment(sketch, "E2040", {"start": v(-54.91, 30.2) * mm, "end": v(-54.73, 30.1) * mm});
            skLineSegment(sketch, "E2041", {"start": v(-54.73, 30.1) * mm, "end": v(-54.55, 30) * mm});
            skLineSegment(sketch, "E2042", {"start": v(-54.55, 30) * mm, "end": v(-54.37, 29.9) * mm});
            skLineSegment(sketch, "E2043", {"start": v(-54.37, 29.9) * mm, "end": v(-54.18, 29.8) * mm});
            skLineSegment(sketch, "E2044", {"start": v(-54.18, 29.8) * mm, "end": v(-54, 29.7) * mm});
            skLineSegment(sketch, "E2045", {"start": v(-54, 29.7) * mm, "end": v(-53.82, 29.6) * mm});
            skLineSegment(sketch, "E2046", {"start": v(-53.82, 29.6) * mm, "end": v(-53.64, 29.5) * mm});
            skLineSegment(sketch, "E2047", {"start": v(-53.64, 29.5) * mm, "end": v(-53.48, 29.4) * mm});
            skLineSegment(sketch, "E2048", {"start": v(-53.48, 29.4) * mm, "end": v(-53.58, 29.23) * mm});
            skLineSegment(sketch, "E2049", {"start": v(-53.58, 29.23) * mm, "end": v(-53.68, 29.05) * mm});
            skLineSegment(sketch, "E2050", {"start": v(-53.68, 29.05) * mm, "end": v(-53.77, 28.86) * mm});
            skLineSegment(sketch, "E2051", {"start": v(-53.77, 28.86) * mm, "end": v(-53.87, 28.68) * mm});
            skLineSegment(sketch, "E2052", {"start": v(-53.87, 28.68) * mm, "end": v(-53.97, 28.5) * mm});
            skLineSegment(sketch, "E2053", {"start": v(-53.97, 28.5) * mm, "end": v(-54.07, 28.32) * mm});
            skLineSegment(sketch, "E2054", {"start": v(-54.07, 28.32) * mm, "end": v(-54.16, 28.14) * mm});
            skLineSegment(sketch, "E2055", {"start": v(-54.16, 28.14) * mm, "end": v(-54.26, 27.96) * mm});
            skLineSegment(sketch, "E2056", {"start": v(-54.26, 27.96) * mm, "end": v(-54.36, 27.77) * mm});
            skLineSegment(sketch, "E2057", {"start": v(-54.36, 27.77) * mm, "end": v(-54.45, 27.6) * mm});
            skLineSegment(sketch, "E2058", {"start": v(-54.45, 27.6) * mm, "end": v(-54.55, 27.41) * mm});
            skLineSegment(sketch, "E2059", {"start": v(-54.55, 27.41) * mm, "end": v(-54.6, 27.32) * mm});
            skLineSegment(sketch, "E2060", {"start": v(-54.6, 27.32) * mm, "end": v(-54.78, 27.41) * mm});
            skLineSegment(sketch, "E2061", {"start": v(-54.78, 27.41) * mm, "end": v(-54.97, 27.5) * mm});
            skLineSegment(sketch, "E2062", {"start": v(-54.97, 27.5) * mm, "end": v(-55.16, 27.6) * mm});
            skLineSegment(sketch, "E2063", {"start": v(-55.16, 27.6) * mm, "end": v(-55.34, 27.7) * mm});
            skLineSegment(sketch, "E2064", {"start": v(-55.34, 27.7) * mm, "end": v(-55.52, 27.79) * mm});
            skLineSegment(sketch, "E2065", {"start": v(-55.52, 27.79) * mm, "end": v(-55.71, 27.88) * mm});
            skLineSegment(sketch, "E2066", {"start": v(-55.71, 27.88) * mm, "end": v(-55.9, 27.98) * mm});
            skLineSegment(sketch, "E2067", {"start": v(-55.9, 27.98) * mm, "end": v(-56.08, 28.07) * mm});
            skLineSegment(sketch, "E2068", {"start": v(-56.08, 28.07) * mm, "end": v(-56.27, 28.17) * mm});
            skLineSegment(sketch, "E2069", {"start": v(-56.27, 28.17) * mm, "end": v(-56.45, 28.26) * mm});
            skLineSegment(sketch, "E2070", {"start": v(-56.45, 28.26) * mm, "end": v(-56.63, 28.35) * mm});
            skLineSegment(sketch, "E2071", {"start": v(-56.63, 28.35) * mm, "end": v(-56.82, 28.45) * mm});
            skLineSegment(sketch, "E2072", {"start": v(-56.82, 28.45) * mm, "end": v(-57.02, 28.55) * mm});
            skLineSegment(sketch, "E2073", {"start": v(-57.02, 28.55) * mm, "end": v(-57.23, 28.6) * mm});
            skLineSegment(sketch, "E2074", {"start": v(-57.23, 28.6) * mm, "end": v(-57.36, 28.62) * mm});
            skLineSegment(sketch, "E2075", {"start": v(-57.36, 28.62) * mm, "end": v(-57.57, 28.59) * mm});
            skLineSegment(sketch, "E2076", {"start": v(-57.57, 28.59) * mm, "end": v(-57.77, 28.5) * mm});
            skLineSegment(sketch, "E2077", {"start": v(-57.77, 28.5) * mm, "end": v(-57.93, 28.37) * mm});
            skLineSegment(sketch, "E2078", {"start": v(-57.93, 28.37) * mm, "end": v(-58.06, 28.2) * mm});
            skLineSegment(sketch, "E2079", {"start": v(-58.06, 28.2) * mm, "end": v(-58.14, 28) * mm});
            skLineSegment(sketch, "E2080", {"start": v(-58.14, 28) * mm, "end": v(-58.17, 27.79) * mm});
            skLineSegment(sketch, "E2081", {"start": v(-58.17, 27.79) * mm, "end": v(-58.14, 27.57) * mm});
            skLineSegment(sketch, "E2082", {"start": v(-58.14, 27.57) * mm, "end": v(-58.05, 27.38) * mm});
            skLineSegment(sketch, "E2083", {"start": v(-58.05, 27.38) * mm, "end": v(-57.92, 27.2) * mm});
            skLineSegment(sketch, "E2084", {"start": v(-57.92, 27.2) * mm, "end": v(-57.74, 27.08) * mm});
            skLineSegment(sketch, "E2085", {"start": v(-57.74, 27.08) * mm, "end": v(-57.55, 26.99) * mm});
            skLineSegment(sketch, "E2086", {"start": v(-57.55, 26.99) * mm, "end": v(-57.36, 26.9) * mm});
            skLineSegment(sketch, "E2087", {"start": v(-57.36, 26.9) * mm, "end": v(-57.17, 26.8) * mm});
            skLineSegment(sketch, "E2088", {"start": v(-57.17, 26.8) * mm, "end": v(-56.98, 26.72) * mm});
            skLineSegment(sketch, "E2089", {"start": v(-56.98, 26.72) * mm, "end": v(-56.8, 26.63) * mm});
            skLineSegment(sketch, "E2090", {"start": v(-56.8, 26.63) * mm, "end": v(-56.61, 26.54) * mm});
            skLineSegment(sketch, "E2091", {"start": v(-56.61, 26.54) * mm, "end": v(-56.42, 26.45) * mm});
            skLineSegment(sketch, "E2092", {"start": v(-56.42, 26.45) * mm, "end": v(-56.23, 26.36) * mm});
            skLineSegment(sketch, "E2093", {"start": v(-56.23, 26.36) * mm, "end": v(-56.05, 26.27) * mm});
            skLineSegment(sketch, "E2094", {"start": v(-56.05, 26.27) * mm, "end": v(-55.86, 26.18) * mm});
            skLineSegment(sketch, "E2095", {"start": v(-55.86, 26.18) * mm, "end": v(-55.67, 26.1) * mm});
            skLineSegment(sketch, "E2096", {"start": v(-55.67, 26.1) * mm, "end": v(-55.49, 26) * mm});
            skLineSegment(sketch, "E2097", {"start": v(-55.49, 26) * mm, "end": v(-55.3, 25.91) * mm});
            skLineSegment(sketch, "E2098", {"start": v(-55.3, 25.91) * mm, "end": v(-55.38, 25.72) * mm});
            skLineSegment(sketch, "E2099", {"start": v(-55.38, 25.72) * mm, "end": v(-55.46, 25.54) * mm});
            skLineSegment(sketch, "E2100", {"start": v(-55.46, 25.54) * mm, "end": v(-55.55, 25.35) * mm});
            skLineSegment(sketch, "E2101", {"start": v(-55.55, 25.35) * mm, "end": v(-55.63, 25.16) * mm});
            skLineSegment(sketch, "E2102", {"start": v(-55.63, 25.16) * mm, "end": v(-55.72, 24.97) * mm});
            skLineSegment(sketch, "E2103", {"start": v(-55.72, 24.97) * mm, "end": v(-55.8, 24.79) * mm});
            skLineSegment(sketch, "E2104", {"start": v(-55.8, 24.79) * mm, "end": v(-55.89, 24.6) * mm});
            skLineSegment(sketch, "E2105", {"start": v(-55.89, 24.6) * mm, "end": v(-55.97, 24.41) * mm});
            skLineSegment(sketch, "E2106", {"start": v(-55.97, 24.41) * mm, "end": v(-56.06, 24.22) * mm});
            skLineSegment(sketch, "E2107", {"start": v(-56.06, 24.22) * mm, "end": v(-56.14, 24.04) * mm});
            skLineSegment(sketch, "E2108", {"start": v(-56.14, 24.04) * mm, "end": v(-56.23, 23.85) * mm});
            skLineSegment(sketch, "E2109", {"start": v(-56.23, 23.85) * mm, "end": v(-56.27, 23.75) * mm});
            skLineSegment(sketch, "E2110", {"start": v(-56.27, 23.75) * mm, "end": v(-56.46, 23.83) * mm});
            skLineSegment(sketch, "E2111", {"start": v(-56.46, 23.83) * mm, "end": v(-56.65, 23.91) * mm});
            skLineSegment(sketch, "E2112", {"start": v(-56.65, 23.91) * mm, "end": v(-56.85, 24) * mm});
            skLineSegment(sketch, "E2113", {"start": v(-56.85, 24) * mm, "end": v(-57.04, 24.08) * mm});
            skLineSegment(sketch, "E2114", {"start": v(-57.04, 24.08) * mm, "end": v(-57.22, 24.16) * mm});
            skLineSegment(sketch, "E2115", {"start": v(-57.22, 24.16) * mm, "end": v(-57.42, 24.24) * mm});
            skLineSegment(sketch, "E2116", {"start": v(-57.42, 24.24) * mm, "end": v(-57.6, 24.33) * mm});
            skLineSegment(sketch, "E2117", {"start": v(-57.6, 24.33) * mm, "end": v(-57.8, 24.4) * mm});
            skLineSegment(sketch, "E2118", {"start": v(-57.8, 24.4) * mm, "end": v(-58, 24.5) * mm});
            skLineSegment(sketch, "E2119", {"start": v(-58, 24.5) * mm, "end": v(-58.18, 24.57) * mm});
            skLineSegment(sketch, "E2120", {"start": v(-58.18, 24.57) * mm, "end": v(-58.37, 24.65) * mm});
            skLineSegment(sketch, "E2121", {"start": v(-58.37, 24.65) * mm, "end": v(-58.56, 24.74) * mm});
            skLineSegment(sketch, "E2122", {"start": v(-58.56, 24.74) * mm, "end": v(-58.77, 24.82) * mm});
            skLineSegment(sketch, "E2123", {"start": v(-58.77, 24.82) * mm, "end": v(-58.98, 24.87) * mm});
            skLineSegment(sketch, "E2124", {"start": v(-58.98, 24.87) * mm, "end": v(-59.06, 24.87) * mm});
            skLineSegment(sketch, "E2125", {"start": v(-59.06, 24.87) * mm, "end": v(-59.28, 24.84) * mm});
            skLineSegment(sketch, "E2126", {"start": v(-59.28, 24.84) * mm, "end": v(-59.47, 24.75) * mm});
            skLineSegment(sketch, "E2127", {"start": v(-59.47, 24.75) * mm, "end": v(-59.64, 24.62) * mm});
            skLineSegment(sketch, "E2128", {"start": v(-59.64, 24.62) * mm, "end": v(-59.77, 24.44) * mm});
            skLineSegment(sketch, "E2129", {"start": v(-59.77, 24.44) * mm, "end": v(-59.84, 24.24) * mm});
            skLineSegment(sketch, "E2130", {"start": v(-59.84, 24.24) * mm, "end": v(-59.86, 24.03) * mm});
            skLineSegment(sketch, "E2131", {"start": v(-59.86, 24.03) * mm, "end": v(-59.83, 23.82) * mm});
            skLineSegment(sketch, "E2132", {"start": v(-59.83, 23.82) * mm, "end": v(-59.74, 23.62) * mm});
            skLineSegment(sketch, "E2133", {"start": v(-59.74, 23.62) * mm, "end": v(-59.6, 23.46) * mm});
            skLineSegment(sketch, "E2134", {"start": v(-59.6, 23.46) * mm, "end": v(-59.43, 23.33) * mm});
            skLineSegment(sketch, "E2135", {"start": v(-59.43, 23.33) * mm, "end": v(-59.24, 23.25) * mm});
            skLineSegment(sketch, "E2136", {"start": v(-59.24, 23.25) * mm, "end": v(-59.05, 23.17) * mm});
            skLineSegment(sketch, "E2137", {"start": v(-59.05, 23.17) * mm, "end": v(-58.86, 23.1) * mm});
            skLineSegment(sketch, "E2138", {"start": v(-58.86, 23.1) * mm, "end": v(-58.67, 23.02) * mm});
            skLineSegment(sketch, "E2139", {"start": v(-58.67, 23.02) * mm, "end": v(-58.48, 22.94) * mm});
            skLineSegment(sketch, "E2140", {"start": v(-58.48, 22.94) * mm, "end": v(-58.28, 22.86) * mm});
            skLineSegment(sketch, "E2141", {"start": v(-58.28, 22.86) * mm, "end": v(-58.09, 22.79) * mm});
            skLineSegment(sketch, "E2142", {"start": v(-58.09, 22.79) * mm, "end": v(-57.9, 22.71) * mm});
            skLineSegment(sketch, "E2143", {"start": v(-57.9, 22.71) * mm, "end": v(-57.7, 22.63) * mm});
            skLineSegment(sketch, "E2144", {"start": v(-57.7, 22.63) * mm, "end": v(-57.5, 22.56) * mm});
            skLineSegment(sketch, "E2145", {"start": v(-57.5, 22.56) * mm, "end": v(-57.32, 22.48) * mm});
            skLineSegment(sketch, "E2146", {"start": v(-57.32, 22.48) * mm, "end": v(-57.12, 22.4) * mm});
            skLineSegment(sketch, "E2147", {"start": v(-57.12, 22.4) * mm, "end": v(-56.93, 22.33) * mm});
            skLineSegment(sketch, "E2148", {"start": v(-56.93, 22.33) * mm, "end": v(-56.87, 22.3) * mm});
            skLineSegment(sketch, "E2149", {"start": v(-56.87, 22.3) * mm, "end": v(-56.95, 22.11) * mm});
            skLineSegment(sketch, "E2150", {"start": v(-56.95, 22.11) * mm, "end": v(-57.02, 21.92) * mm});
            skLineSegment(sketch, "E2151", {"start": v(-57.02, 21.92) * mm, "end": v(-57.1, 21.73) * mm});
            skLineSegment(sketch, "E2152", {"start": v(-57.1, 21.73) * mm, "end": v(-57.16, 21.53) * mm});
            skLineSegment(sketch, "E2153", {"start": v(-57.16, 21.53) * mm, "end": v(-57.24, 21.34) * mm});
            skLineSegment(sketch, "E2154", {"start": v(-57.24, 21.34) * mm, "end": v(-57.3, 21.15) * mm});
            skLineSegment(sketch, "E2155", {"start": v(-57.3, 21.15) * mm, "end": v(-57.38, 20.95) * mm});
            skLineSegment(sketch, "E2156", {"start": v(-57.38, 20.95) * mm, "end": v(-57.45, 20.76) * mm});
            skLineSegment(sketch, "E2157", {"start": v(-57.45, 20.76) * mm, "end": v(-57.53, 20.57) * mm});
            skLineSegment(sketch, "E2158", {"start": v(-57.53, 20.57) * mm, "end": v(-57.6, 20.38) * mm});
            skLineSegment(sketch, "E2159", {"start": v(-57.6, 20.38) * mm, "end": v(-57.67, 20.18) * mm});
            skLineSegment(sketch, "E2160", {"start": v(-57.67, 20.18) * mm, "end": v(-57.7, 20.08) * mm});
            skLineSegment(sketch, "E2161", {"start": v(-57.7, 20.08) * mm, "end": v(-57.9, 20.15) * mm});
            skLineSegment(sketch, "E2162", {"start": v(-57.9, 20.15) * mm, "end": v(-58.1, 20.22) * mm});
            skLineSegment(sketch, "E2163", {"start": v(-58.1, 20.22) * mm, "end": v(-58.3, 20.3) * mm});
            skLineSegment(sketch, "E2164", {"start": v(-58.3, 20.3) * mm, "end": v(-58.5, 20.36) * mm});
            skLineSegment(sketch, "E2165", {"start": v(-58.5, 20.36) * mm, "end": v(-58.68, 20.43) * mm});
            skLineSegment(sketch, "E2166", {"start": v(-58.68, 20.43) * mm, "end": v(-58.88, 20.5) * mm});
            skLineSegment(sketch, "E2167", {"start": v(-58.88, 20.5) * mm, "end": v(-59.08, 20.57) * mm});
            skLineSegment(sketch, "E2168", {"start": v(-59.08, 20.57) * mm, "end": v(-59.27, 20.64) * mm});
            skLineSegment(sketch, "E2169", {"start": v(-59.27, 20.64) * mm, "end": v(-59.47, 20.7) * mm});
            skLineSegment(sketch, "E2170", {"start": v(-59.47, 20.7) * mm, "end": v(-59.67, 20.78) * mm});
            skLineSegment(sketch, "E2171", {"start": v(-59.67, 20.78) * mm, "end": v(-59.86, 20.85) * mm});
            skLineSegment(sketch, "E2172", {"start": v(-59.86, 20.85) * mm, "end": v(-60.06, 20.92) * mm});
            skLineSegment(sketch, "E2173", {"start": v(-60.06, 20.92) * mm, "end": v(-60.27, 20.99) * mm});
            skLineSegment(sketch, "E2174", {"start": v(-60.27, 20.99) * mm, "end": v(-60.48, 21.02) * mm});
            skLineSegment(sketch, "E2175", {"start": v(-60.48, 21.02) * mm, "end": v(-60.7, 21) * mm});
            skLineSegment(sketch, "E2176", {"start": v(-60.7, 21) * mm, "end": v(-60.9, 20.92) * mm});
            skLineSegment(sketch, "E2177", {"start": v(-60.9, 20.92) * mm, "end": v(-61.07, 20.8) * mm});
            skLineSegment(sketch, "E2178", {"start": v(-61.07, 20.8) * mm, "end": v(-61.2, 20.62) * mm});
            skLineSegment(sketch, "E2179", {"start": v(-61.2, 20.62) * mm, "end": v(-61.28, 20.43) * mm});
            skLineSegment(sketch, "E2180", {"start": v(-61.28, 20.43) * mm, "end": v(-61.31, 20.21) * mm});
            skLineSegment(sketch, "E2181", {"start": v(-61.31, 20.21) * mm, "end": v(-61.29, 20) * mm});
            skLineSegment(sketch, "E2182", {"start": v(-61.29, 20) * mm, "end": v(-61.2, 19.8) * mm});
            skLineSegment(sketch, "E2183", {"start": v(-61.2, 19.8) * mm, "end": v(-61.08, 19.63) * mm});
            skLineSegment(sketch, "E2184", {"start": v(-61.08, 19.63) * mm, "end": v(-60.91, 19.5) * mm});
            skLineSegment(sketch, "E2185", {"start": v(-60.91, 19.5) * mm, "end": v(-60.72, 19.42) * mm});
            skLineSegment(sketch, "E2186", {"start": v(-60.72, 19.42) * mm, "end": v(-60.52, 19.35) * mm});
            skLineSegment(sketch, "E2187", {"start": v(-60.52, 19.35) * mm, "end": v(-60.33, 19.29) * mm});
            skLineSegment(sketch, "E2188", {"start": v(-60.33, 19.29) * mm, "end": v(-60.13, 19.22) * mm});
            skLineSegment(sketch, "E2189", {"start": v(-60.13, 19.22) * mm, "end": v(-59.94, 19.16) * mm});
            skLineSegment(sketch, "E2190", {"start": v(-59.94, 19.16) * mm, "end": v(-59.74, 19.1) * mm});
            skLineSegment(sketch, "E2191", {"start": v(-59.74, 19.1) * mm, "end": v(-59.54, 19.03) * mm});
            skLineSegment(sketch, "E2192", {"start": v(-59.54, 19.03) * mm, "end": v(-59.35, 18.97) * mm});
            skLineSegment(sketch, "E2193", {"start": v(-59.35, 18.97) * mm, "end": v(-59.14, 18.9) * mm});
            skLineSegment(sketch, "E2194", {"start": v(-59.14, 18.9) * mm, "end": v(-58.95, 18.84) * mm});
            skLineSegment(sketch, "E2195", {"start": v(-58.95, 18.84) * mm, "end": v(-58.75, 18.78) * mm});
            skLineSegment(sketch, "E2196", {"start": v(-58.75, 18.78) * mm, "end": v(-58.55, 18.71) * mm});
            skLineSegment(sketch, "E2197", {"start": v(-58.55, 18.71) * mm, "end": v(-58.36, 18.65) * mm});
            skLineSegment(sketch, "E2198", {"start": v(-58.36, 18.65) * mm, "end": v(-58.21, 18.6) * mm});
            skLineSegment(sketch, "E2199", {"start": v(-58.21, 18.6) * mm, "end": v(-58.27, 18.4) * mm});
            skLineSegment(sketch, "E2200", {"start": v(-58.27, 18.4) * mm, "end": v(-58.33, 18.2) * mm});
            skLineSegment(sketch, "E2201", {"start": v(-58.33, 18.2) * mm, "end": v(-58.4, 18) * mm});
            skLineSegment(sketch, "E2202", {"start": v(-58.4, 18) * mm, "end": v(-58.45, 17.81) * mm});
            skLineSegment(sketch, "E2203", {"start": v(-58.45, 17.81) * mm, "end": v(-58.51, 17.61) * mm});
            skLineSegment(sketch, "E2204", {"start": v(-58.51, 17.61) * mm, "end": v(-58.57, 17.42) * mm});
            skLineSegment(sketch, "E2205", {"start": v(-58.57, 17.42) * mm, "end": v(-58.63, 17.22) * mm});
            skLineSegment(sketch, "E2206", {"start": v(-58.63, 17.22) * mm, "end": v(-58.7, 17.02) * mm});
            skLineSegment(sketch, "E2207", {"start": v(-58.7, 17.02) * mm, "end": v(-58.75, 16.83) * mm});
            skLineSegment(sketch, "E2208", {"start": v(-58.75, 16.83) * mm, "end": v(-58.81, 16.63) * mm});
            skLineSegment(sketch, "E2209", {"start": v(-58.81, 16.63) * mm, "end": v(-58.87, 16.43) * mm});
            skLineSegment(sketch, "E2210", {"start": v(-58.87, 16.43) * mm, "end": v(-58.9, 16.33) * mm});
            skLineSegment(sketch, "E2211", {"start": v(-58.9, 16.33) * mm, "end": v(-59.1, 16.39) * mm});
            skLineSegment(sketch, "E2212", {"start": v(-59.1, 16.39) * mm, "end": v(-59.3, 16.44) * mm});
            skLineSegment(sketch, "E2213", {"start": v(-59.3, 16.44) * mm, "end": v(-59.5, 16.5) * mm});
            skLineSegment(sketch, "E2214", {"start": v(-59.5, 16.5) * mm, "end": v(-59.7, 16.56) * mm});
            skLineSegment(sketch, "E2215", {"start": v(-59.7, 16.56) * mm, "end": v(-59.9, 16.61) * mm});
            skLineSegment(sketch, "E2216", {"start": v(-59.9, 16.61) * mm, "end": v(-60.1, 16.67) * mm});
            skLineSegment(sketch, "E2217", {"start": v(-60.1, 16.67) * mm, "end": v(-60.3, 16.73) * mm});
            skLineSegment(sketch, "E2218", {"start": v(-60.3, 16.73) * mm, "end": v(-60.5, 16.78) * mm});
            skLineSegment(sketch, "E2219", {"start": v(-60.5, 16.78) * mm, "end": v(-60.7, 16.84) * mm});
            skLineSegment(sketch, "E2220", {"start": v(-60.7, 16.84) * mm, "end": v(-60.9, 16.9) * mm});
            skLineSegment(sketch, "E2221", {"start": v(-60.9, 16.9) * mm, "end": v(-61.1, 16.95) * mm});
            skLineSegment(sketch, "E2222", {"start": v(-61.1, 16.95) * mm, "end": v(-61.3, 17) * mm});
            skLineSegment(sketch, "E2223", {"start": v(-61.3, 17) * mm, "end": v(-61.51, 17.07) * mm});
            skLineSegment(sketch, "E2224", {"start": v(-61.51, 17.07) * mm, "end": v(-61.68, 17.09) * mm});
            skLineSegment(sketch, "E2225", {"start": v(-61.68, 17.09) * mm, "end": v(-61.9, 17.06) * mm});
            skLineSegment(sketch, "E2226", {"start": v(-61.9, 17.06) * mm, "end": v(-62.1, 16.98) * mm});
            skLineSegment(sketch, "E2227", {"start": v(-62.1, 16.98) * mm, "end": v(-62.27, 16.85) * mm});
            skLineSegment(sketch, "E2228", {"start": v(-62.27, 16.85) * mm, "end": v(-62.4, 16.68) * mm});
            skLineSegment(sketch, "E2229", {"start": v(-62.4, 16.68) * mm, "end": v(-62.48, 16.48) * mm});
            skLineSegment(sketch, "E2230", {"start": v(-62.48, 16.48) * mm, "end": v(-62.5, 16.27) * mm});
            skLineSegment(sketch, "E2231", {"start": v(-62.5, 16.27) * mm, "end": v(-62.48, 16.05) * mm});
            skLineSegment(sketch, "E2232", {"start": v(-62.48, 16.05) * mm, "end": v(-62.4, 15.86) * mm});
            skLineSegment(sketch, "E2233", {"start": v(-62.4, 15.86) * mm, "end": v(-62.27, 15.69) * mm});
            skLineSegment(sketch, "E2234", {"start": v(-62.27, 15.69) * mm, "end": v(-62.1, 15.56) * mm});
            skLineSegment(sketch, "E2235", {"start": v(-62.1, 15.56) * mm, "end": v(-61.9, 15.47) * mm});
            skLineSegment(sketch, "E2236", {"start": v(-61.9, 15.47) * mm, "end": v(-61.7, 15.42) * mm});
            skLineSegment(sketch, "E2237", {"start": v(-61.7, 15.42) * mm, "end": v(-61.5, 15.37) * mm});
            skLineSegment(sketch, "E2238", {"start": v(-61.5, 15.37) * mm, "end": v(-61.3, 15.32) * mm});
            skLineSegment(sketch, "E2239", {"start": v(-61.3, 15.32) * mm, "end": v(-61.1, 15.27) * mm});
            skLineSegment(sketch, "E2240", {"start": v(-61.1, 15.27) * mm, "end": v(-60.9, 15.22) * mm});
            skLineSegment(sketch, "E2241", {"start": v(-60.9, 15.22) * mm, "end": v(-60.69, 15.17) * mm});
            skLineSegment(sketch, "E2242", {"start": v(-60.69, 15.17) * mm, "end": v(-60.49, 15.12) * mm});
            skLineSegment(sketch, "E2243", {"start": v(-60.49, 15.12) * mm, "end": v(-60.29, 15.07) * mm});
            skLineSegment(sketch, "E2244", {"start": v(-60.29, 15.07) * mm, "end": v(-60.08, 15.01) * mm});
            skLineSegment(sketch, "E2245", {"start": v(-60.08, 15.01) * mm, "end": v(-59.88, 14.96) * mm});
            skLineSegment(sketch, "E2246", {"start": v(-59.88, 14.96) * mm, "end": v(-59.68, 14.91) * mm});
            skLineSegment(sketch, "E2247", {"start": v(-59.68, 14.91) * mm, "end": v(-59.48, 14.86) * mm});
            skLineSegment(sketch, "E2248", {"start": v(-59.48, 14.86) * mm, "end": v(-59.3, 14.82) * mm});
            skLineSegment(sketch, "E2249", {"start": v(-59.3, 14.82) * mm, "end": v(-59.35, 14.62) * mm});
            skLineSegment(sketch, "E2250", {"start": v(-59.35, 14.62) * mm, "end": v(-59.4, 14.42) * mm});
            skLineSegment(sketch, "E2251", {"start": v(-59.4, 14.42) * mm, "end": v(-59.45, 14.22) * mm});
            skLineSegment(sketch, "E2252", {"start": v(-59.45, 14.22) * mm, "end": v(-59.5, 14.01) * mm});
            skLineSegment(sketch, "E2253", {"start": v(-59.5, 14.01) * mm, "end": v(-59.54, 13.81) * mm});
            skLineSegment(sketch, "E2254", {"start": v(-59.54, 13.81) * mm, "end": v(-59.59, 13.61) * mm});
            skLineSegment(sketch, "E2255", {"start": v(-59.59, 13.61) * mm, "end": v(-59.63, 13.41) * mm});
            skLineSegment(sketch, "E2256", {"start": v(-59.63, 13.41) * mm, "end": v(-59.68, 13.21) * mm});
            skLineSegment(sketch, "E2257", {"start": v(-59.68, 13.21) * mm, "end": v(-59.73, 13.01) * mm});
            skLineSegment(sketch, "E2258", {"start": v(-59.73, 13.01) * mm, "end": v(-59.77, 12.81) * mm});
            skLineSegment(sketch, "E2259", {"start": v(-59.77, 12.81) * mm, "end": v(-59.82, 12.61) * mm});
            skLineSegment(sketch, "E2260", {"start": v(-59.82, 12.61) * mm, "end": v(-59.84, 12.5) * mm});
            skLineSegment(sketch, "E2261", {"start": v(-59.84, 12.5) * mm, "end": v(-60.05, 12.55) * mm});
            skLineSegment(sketch, "E2262", {"start": v(-60.05, 12.55) * mm, "end": v(-60.25, 12.6) * mm});
            skLineSegment(sketch, "E2263", {"start": v(-60.25, 12.6) * mm, "end": v(-60.45, 12.64) * mm});
            skLineSegment(sketch, "E2264", {"start": v(-60.45, 12.64) * mm, "end": v(-60.66, 12.68) * mm});
            skLineSegment(sketch, "E2265", {"start": v(-60.66, 12.68) * mm, "end": v(-60.86, 12.72) * mm});
            skLineSegment(sketch, "E2266", {"start": v(-60.86, 12.72) * mm, "end": v(-61.06, 12.77) * mm});
            skLineSegment(sketch, "E2267", {"start": v(-61.06, 12.77) * mm, "end": v(-61.27, 12.81) * mm});
            skLineSegment(sketch, "E2268", {"start": v(-61.27, 12.81) * mm, "end": v(-61.47, 12.85) * mm});
            skLineSegment(sketch, "E2269", {"start": v(-61.47, 12.85) * mm, "end": v(-61.67, 12.9) * mm});
            skLineSegment(sketch, "E2270", {"start": v(-61.67, 12.9) * mm, "end": v(-61.88, 12.94) * mm});
            skLineSegment(sketch, "E2271", {"start": v(-61.88, 12.94) * mm, "end": v(-62.08, 12.98) * mm});
            skLineSegment(sketch, "E2272", {"start": v(-62.08, 12.98) * mm, "end": v(-62.28, 13.03) * mm});
            skLineSegment(sketch, "E2273", {"start": v(-62.28, 13.03) * mm, "end": v(-62.5, 13.07) * mm});
            skLineSegment(sketch, "E2274", {"start": v(-62.5, 13.07) * mm, "end": v(-62.63, 13.08) * mm});
            skLineSegment(sketch, "E2275", {"start": v(-62.63, 13.08) * mm, "end": v(-62.84, 13.05) * mm});
            skLineSegment(sketch, "E2276", {"start": v(-62.84, 13.05) * mm, "end": v(-63.04, 12.97) * mm});
            skLineSegment(sketch, "E2277", {"start": v(-63.04, 12.97) * mm, "end": v(-63.2, 12.83) * mm});
            skLineSegment(sketch, "E2278", {"start": v(-63.2, 12.83) * mm, "end": v(-63.34, 12.66) * mm});
            skLineSegment(sketch, "E2279", {"start": v(-63.34, 12.66) * mm, "end": v(-63.42, 12.46) * mm});
            skLineSegment(sketch, "E2280", {"start": v(-63.42, 12.46) * mm, "end": v(-63.44, 12.25) * mm});
            skLineSegment(sketch, "E2281", {"start": v(-63.44, 12.25) * mm, "end": v(-63.41, 12.04) * mm});
            skLineSegment(sketch, "E2282", {"start": v(-63.41, 12.04) * mm, "end": v(-63.33, 11.84) * mm});
            skLineSegment(sketch, "E2283", {"start": v(-63.33, 11.84) * mm, "end": v(-63.2, 11.67) * mm});
            skLineSegment(sketch, "E2284", {"start": v(-63.2, 11.67) * mm, "end": v(-63.02, 11.55) * mm});
            skLineSegment(sketch, "E2285", {"start": v(-63.02, 11.55) * mm, "end": v(-62.82, 11.47) * mm});
            skLineSegment(sketch, "E2286", {"start": v(-62.82, 11.47) * mm, "end": v(-62.6, 11.43) * mm});
            skLineSegment(sketch, "E2287", {"start": v(-62.6, 11.43) * mm, "end": v(-62.4, 11.39) * mm});
            skLineSegment(sketch, "E2288", {"start": v(-62.4, 11.39) * mm, "end": v(-62.2, 11.35) * mm});
            skLineSegment(sketch, "E2289", {"start": v(-62.2, 11.35) * mm, "end": v(-61.99, 11.31) * mm});
            skLineSegment(sketch, "E2290", {"start": v(-61.99, 11.31) * mm, "end": v(-61.79, 11.27) * mm});
            skLineSegment(sketch, "E2291", {"start": v(-61.79, 11.27) * mm, "end": v(-61.58, 11.24) * mm});
            skLineSegment(sketch, "E2292", {"start": v(-61.58, 11.24) * mm, "end": v(-61.38, 11.2) * mm});
            skLineSegment(sketch, "E2293", {"start": v(-61.38, 11.2) * mm, "end": v(-61.17, 11.16) * mm});
            skLineSegment(sketch, "E2294", {"start": v(-61.17, 11.16) * mm, "end": v(-60.97, 11.12) * mm});
            skLineSegment(sketch, "E2295", {"start": v(-60.97, 11.12) * mm, "end": v(-60.76, 11.08) * mm});
            skLineSegment(sketch, "E2296", {"start": v(-60.76, 11.08) * mm, "end": v(-60.56, 11.05) * mm});
            skLineSegment(sketch, "E2297", {"start": v(-60.56, 11.05) * mm, "end": v(-60.36, 11) * mm});
            skLineSegment(sketch, "E2298", {"start": v(-60.36, 11) * mm, "end": v(-60.15, 10.97) * mm});
            skLineSegment(sketch, "E2299", {"start": v(-60.15, 10.97) * mm, "end": v(-60.18, 10.77) * mm});
            skLineSegment(sketch, "E2300", {"start": v(-60.18, 10.77) * mm, "end": v(-60.22, 10.56) * mm});
            skLineSegment(sketch, "E2301", {"start": v(-60.22, 10.56) * mm, "end": v(-60.25, 10.36) * mm});
            skLineSegment(sketch, "E2302", {"start": v(-60.25, 10.36) * mm, "end": v(-60.28, 10.16) * mm});
            skLineSegment(sketch, "E2303", {"start": v(-60.28, 10.16) * mm, "end": v(-60.32, 9.95) * mm});
            skLineSegment(sketch, "E2304", {"start": v(-60.32, 9.95) * mm, "end": v(-60.35, 9.75) * mm});
            skLineSegment(sketch, "E2305", {"start": v(-60.35, 9.75) * mm, "end": v(-60.39, 9.55) * mm});
            skLineSegment(sketch, "E2306", {"start": v(-60.39, 9.55) * mm, "end": v(-60.42, 9.34) * mm});
            skLineSegment(sketch, "E2307", {"start": v(-60.42, 9.34) * mm, "end": v(-60.45, 9.14) * mm});
            skLineSegment(sketch, "E2308", {"start": v(-60.45, 9.14) * mm, "end": v(-60.49, 8.94) * mm});
            skLineSegment(sketch, "E2309", {"start": v(-60.49, 8.94) * mm, "end": v(-60.52, 8.74) * mm});
            skLineSegment(sketch, "E2310", {"start": v(-60.52, 8.74) * mm, "end": v(-60.54, 8.63) * mm});
            skLineSegment(sketch, "E2311", {"start": v(-60.54, 8.63) * mm, "end": v(-60.74, 8.66) * mm});
            skLineSegment(sketch, "E2312", {"start": v(-60.74, 8.66) * mm, "end": v(-60.94, 8.7) * mm});
            skLineSegment(sketch, "E2313", {"start": v(-60.94, 8.7) * mm, "end": v(-61.15, 8.72) * mm});
            skLineSegment(sketch, "E2314", {"start": v(-61.15, 8.72) * mm, "end": v(-61.36, 8.75) * mm});
            skLineSegment(sketch, "E2315", {"start": v(-61.36, 8.75) * mm, "end": v(-61.56, 8.78) * mm});
            skLineSegment(sketch, "E2316", {"start": v(-61.56, 8.78) * mm, "end": v(-61.77, 8.81) * mm});
            skLineSegment(sketch, "E2317", {"start": v(-61.77, 8.81) * mm, "end": v(-61.97, 8.84) * mm});
            skLineSegment(sketch, "E2318", {"start": v(-61.97, 8.84) * mm, "end": v(-62.18, 8.87) * mm});
            skLineSegment(sketch, "E2319", {"start": v(-62.18, 8.87) * mm, "end": v(-62.39, 8.9) * mm});
            skLineSegment(sketch, "E2320", {"start": v(-62.39, 8.9) * mm, "end": v(-62.6, 8.93) * mm});
            skLineSegment(sketch, "E2321", {"start": v(-62.6, 8.93) * mm, "end": v(-62.8, 8.96) * mm});
            skLineSegment(sketch, "E2322", {"start": v(-62.8, 8.96) * mm, "end": v(-63, 8.99) * mm});
            skLineSegment(sketch, "E2323", {"start": v(-63, 8.99) * mm, "end": v(-63.22, 9.02) * mm});
            skLineSegment(sketch, "E2324", {"start": v(-63.22, 9.02) * mm, "end": v(-63.31, 9.02) * mm});
            skLineSegment(sketch, "E2325", {"start": v(-63.31, 9.02) * mm, "end": v(-63.52, 8.99) * mm});
            skLineSegment(sketch, "E2326", {"start": v(-63.52, 8.99) * mm, "end": v(-63.72, 8.9) * mm});
            skLineSegment(sketch, "E2327", {"start": v(-63.72, 8.9) * mm, "end": v(-63.89, 8.77) * mm});
            skLineSegment(sketch, "E2328", {"start": v(-63.89, 8.77) * mm, "end": v(-64.01, 8.6) * mm});
            skLineSegment(sketch, "E2329", {"start": v(-64.01, 8.6) * mm, "end": v(-64.09, 8.4) * mm});
            skLineSegment(sketch, "E2330", {"start": v(-64.09, 8.4) * mm, "end": v(-64.11, 8.18) * mm});
            skLineSegment(sketch, "E2331", {"start": v(-64.11, 8.18) * mm, "end": v(-64.08, 7.97) * mm});
            skLineSegment(sketch, "E2332", {"start": v(-64.08, 7.97) * mm, "end": v(-64, 7.77) * mm});
            skLineSegment(sketch, "E2333", {"start": v(-64, 7.77) * mm, "end": v(-63.85, 7.6) * mm});
            skLineSegment(sketch, "E2334", {"start": v(-63.85, 7.6) * mm, "end": v(-63.68, 7.48) * mm});
            skLineSegment(sketch, "E2335", {"start": v(-63.68, 7.48) * mm, "end": v(-63.48, 7.4) * mm});
            skLineSegment(sketch, "E2336", {"start": v(-63.48, 7.4) * mm, "end": v(-63.28, 7.38) * mm});
            skLineSegment(sketch, "E2337", {"start": v(-63.28, 7.38) * mm, "end": v(-63.07, 7.35) * mm});
            skLineSegment(sketch, "E2338", {"start": v(-63.07, 7.35) * mm, "end": v(-62.86, 7.33) * mm});
            skLineSegment(sketch, "E2339", {"start": v(-62.86, 7.33) * mm, "end": v(-62.66, 7.3) * mm});
            skLineSegment(sketch, "E2340", {"start": v(-62.66, 7.3) * mm, "end": v(-62.46, 7.28) * mm});
            skLineSegment(sketch, "E2341", {"start": v(-62.46, 7.28) * mm, "end": v(-62.25, 7.25) * mm});
            skLineSegment(sketch, "E2342", {"start": v(-62.25, 7.25) * mm, "end": v(-62.04, 7.23) * mm});
            skLineSegment(sketch, "E2343", {"start": v(-62.04, 7.23) * mm, "end": v(-61.84, 7.2) * mm});
            skLineSegment(sketch, "E2344", {"start": v(-61.84, 7.2) * mm, "end": v(-61.63, 7.18) * mm});
            skLineSegment(sketch, "E2345", {"start": v(-61.63, 7.18) * mm, "end": v(-61.42, 7.16) * mm});
            skLineSegment(sketch, "E2346", {"start": v(-61.42, 7.16) * mm, "end": v(-61.22, 7.13) * mm});
            skLineSegment(sketch, "E2347", {"start": v(-61.22, 7.13) * mm, "end": v(-61, 7.1) * mm});
            skLineSegment(sketch, "E2348", {"start": v(-61, 7.1) * mm, "end": v(-60.8, 7.08) * mm});
            skLineSegment(sketch, "E2349", {"start": v(-60.8, 7.08) * mm, "end": v(-60.74, 7.08) * mm});
            skLineSegment(sketch, "E2350", {"start": v(-60.74, 7.08) * mm, "end": v(-60.76, 6.87) * mm});
            skLineSegment(sketch, "E2351", {"start": v(-60.76, 6.87) * mm, "end": v(-60.78, 6.67) * mm});
            skLineSegment(sketch, "E2352", {"start": v(-60.78, 6.67) * mm, "end": v(-60.8, 6.46) * mm});
            skLineSegment(sketch, "E2353", {"start": v(-60.8, 6.46) * mm, "end": v(-60.82, 6.26) * mm});
            skLineSegment(sketch, "E2354", {"start": v(-60.82, 6.26) * mm, "end": v(-60.84, 6.05) * mm});
            skLineSegment(sketch, "E2355", {"start": v(-60.84, 6.05) * mm, "end": v(-60.86, 5.85) * mm});
            skLineSegment(sketch, "E2356", {"start": v(-60.86, 5.85) * mm, "end": v(-60.88, 5.64) * mm});
            skLineSegment(sketch, "E2357", {"start": v(-60.88, 5.64) * mm, "end": v(-60.9, 5.44) * mm});
            skLineSegment(sketch, "E2358", {"start": v(-60.9, 5.44) * mm, "end": v(-60.92, 5.23) * mm});
            skLineSegment(sketch, "E2359", {"start": v(-60.92, 5.23) * mm, "end": v(-60.94, 5.03) * mm});
            skLineSegment(sketch, "E2360", {"start": v(-60.94, 5.03) * mm, "end": v(-60.96, 4.82) * mm});
            skLineSegment(sketch, "E2361", {"start": v(-60.96, 4.82) * mm, "end": v(-60.97, 4.72) * mm});
            skLineSegment(sketch, "E2362", {"start": v(-60.97, 4.72) * mm, "end": v(-61.18, 4.73) * mm});
            skLineSegment(sketch, "E2363", {"start": v(-61.18, 4.73) * mm, "end": v(-61.38, 4.75) * mm});
            skLineSegment(sketch, "E2364", {"start": v(-61.38, 4.75) * mm, "end": v(-61.6, 4.77) * mm});
            skLineSegment(sketch, "E2365", {"start": v(-61.6, 4.77) * mm, "end": v(-61.8, 4.78) * mm});
            skLineSegment(sketch, "E2366", {"start": v(-61.8, 4.78) * mm, "end": v(-62, 4.8) * mm});
            skLineSegment(sketch, "E2367", {"start": v(-62, 4.8) * mm, "end": v(-62.22, 4.82) * mm});
            skLineSegment(sketch, "E2368", {"start": v(-62.22, 4.82) * mm, "end": v(-62.42, 4.83) * mm});
            skLineSegment(sketch, "E2369", {"start": v(-62.42, 4.83) * mm, "end": v(-62.63, 4.85) * mm});
            skLineSegment(sketch, "E2370", {"start": v(-62.63, 4.85) * mm, "end": v(-62.84, 4.86) * mm});
            skLineSegment(sketch, "E2371", {"start": v(-62.84, 4.86) * mm, "end": v(-63.04, 4.88) * mm});
            skLineSegment(sketch, "E2372", {"start": v(-63.04, 4.88) * mm, "end": v(-63.25, 4.9) * mm});
            skLineSegment(sketch, "E2373", {"start": v(-63.25, 4.9) * mm, "end": v(-63.46, 4.91) * mm});
            skLineSegment(sketch, "E2374", {"start": v(-63.46, 4.91) * mm, "end": v(-63.68, 4.93) * mm});
            skLineSegment(sketch, "E2375", {"start": v(-63.68, 4.93) * mm, "end": v(-63.9, 4.9) * mm});
            skLineSegment(sketch, "E2376", {"start": v(-63.9, 4.9) * mm, "end": v(-64.1, 4.83) * mm});
            skLineSegment(sketch, "E2377", {"start": v(-64.1, 4.83) * mm, "end": v(-64.27, 4.7) * mm});
            skLineSegment(sketch, "E2378", {"start": v(-64.27, 4.7) * mm, "end": v(-64.4, 4.53) * mm});
            skLineSegment(sketch, "E2379", {"start": v(-64.4, 4.53) * mm, "end": v(-64.48, 4.33) * mm});
            skLineSegment(sketch, "E2380", {"start": v(-64.48, 4.33) * mm, "end": v(-64.51, 4.12) * mm});
            skLineSegment(sketch, "E2381", {"start": v(-64.51, 4.12) * mm, "end": v(-64.49, 3.9) * mm});
            skLineSegment(sketch, "E2382", {"start": v(-64.49, 3.9) * mm, "end": v(-64.4, 3.7) * mm});
            skLineSegment(sketch, "E2383", {"start": v(-64.4, 3.7) * mm, "end": v(-64.28, 3.54) * mm});
            skLineSegment(sketch, "E2384", {"start": v(-64.28, 3.54) * mm, "end": v(-64.11, 3.4) * mm});
            skLineSegment(sketch, "E2385", {"start": v(-64.11, 3.4) * mm, "end": v(-63.91, 3.32) * mm});
            skLineSegment(sketch, "E2386", {"start": v(-63.91, 3.32) * mm, "end": v(-63.71, 3.3) * mm});
            skLineSegment(sketch, "E2387", {"start": v(-63.71, 3.3) * mm, "end": v(-63.5, 3.28) * mm});
            skLineSegment(sketch, "E2388", {"start": v(-63.5, 3.28) * mm, "end": v(-63.3, 3.27) * mm});
            skLineSegment(sketch, "E2389", {"start": v(-63.3, 3.27) * mm, "end": v(-63.1, 3.26) * mm});
            skLineSegment(sketch, "E2390", {"start": v(-63.1, 3.26) * mm, "end": v(-62.89, 3.25) * mm});
            skLineSegment(sketch, "E2391", {"start": v(-62.89, 3.25) * mm, "end": v(-62.68, 3.24) * mm});
            skLineSegment(sketch, "E2392", {"start": v(-62.68, 3.24) * mm, "end": v(-62.47, 3.23) * mm});
            skLineSegment(sketch, "E2393", {"start": v(-62.47, 3.23) * mm, "end": v(-62.27, 3.22) * mm});
            skLineSegment(sketch, "E2394", {"start": v(-62.27, 3.22) * mm, "end": v(-62.05, 3.2) * mm});
            skLineSegment(sketch, "E2395", {"start": v(-62.05, 3.2) * mm, "end": v(-61.85, 3.2) * mm});
            skLineSegment(sketch, "E2396", {"start": v(-61.85, 3.2) * mm, "end": v(-61.64, 3.18) * mm});
            skLineSegment(sketch, "E2397", {"start": v(-61.64, 3.18) * mm, "end": v(-61.43, 3.17) * mm});
            skLineSegment(sketch, "E2398", {"start": v(-61.43, 3.17) * mm, "end": v(-61.23, 3.16) * mm});
            skLineSegment(sketch, "E2399", {"start": v(-61.23, 3.16) * mm, "end": v(-61.08, 3.15) * mm});
            skLineSegment(sketch, "E2400", {"start": v(-61.08, 3.15) * mm, "end": v(-61.08, 2.95) * mm});
            skLineSegment(sketch, "E2401", {"start": v(-61.08, 2.95) * mm, "end": v(-61.09, 2.74) * mm});
            skLineSegment(sketch, "E2402", {"start": v(-61.09, 2.74) * mm, "end": v(-61.1, 2.54) * mm});
            skLineSegment(sketch, "E2403", {"start": v(-61.1, 2.54) * mm, "end": v(-61.1, 2.33) * mm});
            skLineSegment(sketch, "E2404", {"start": v(-61.1, 2.33) * mm, "end": v(-61.1, 2.12) * mm});
            skLineSegment(sketch, "E2405", {"start": v(-61.1, 2.12) * mm, "end": v(-61.12, 1.92) * mm});
            skLineSegment(sketch, "E2406", {"start": v(-61.12, 1.92) * mm, "end": v(-61.12, 1.71) * mm});
            skLineSegment(sketch, "E2407", {"start": v(-61.12, 1.71) * mm, "end": v(-61.13, 1.5) * mm});
            skLineSegment(sketch, "E2408", {"start": v(-61.13, 1.5) * mm, "end": v(-61.14, 1.3) * mm});
            skLineSegment(sketch, "E2409", {"start": v(-61.14, 1.3) * mm, "end": v(-61.14, 1.1) * mm});
            skLineSegment(sketch, "E2410", {"start": v(-61.14, 1.1) * mm, "end": v(-61.15, 0.89) * mm});
            skLineSegment(sketch, "E2411", {"start": v(-61.15, 0.89) * mm, "end": v(-61.15, 0.78) * mm});
            skLineSegment(sketch, "E2412", {"start": v(-61.15, 0.78) * mm, "end": v(-61.36, 0.79) * mm});
            skLineSegment(sketch, "E2413", {"start": v(-61.36, 0.79) * mm, "end": v(-61.57, 0.79) * mm});
            skLineSegment(sketch, "E2414", {"start": v(-61.57, 0.79) * mm, "end": v(-61.78, 0.8) * mm});
            skLineSegment(sketch, "E2415", {"start": v(-61.78, 0.8) * mm, "end": v(-61.98, 0.8) * mm});
            skLineSegment(sketch, "E2416", {"start": v(-61.98, 0.8) * mm, "end": v(-62.19, 0.8) * mm});
            skLineSegment(sketch, "E2417", {"start": v(-62.19, 0.8) * mm, "end": v(-62.4, 0.8) * mm});
            skLineSegment(sketch, "E2418", {"start": v(-62.4, 0.8) * mm, "end": v(-62.6, 0.8) * mm});
            skLineSegment(sketch, "E2419", {"start": v(-62.6, 0.8) * mm, "end": v(-62.81, 0.8) * mm});
            skLineSegment(sketch, "E2420", {"start": v(-62.81, 0.8) * mm, "end": v(-63.02, 0.8) * mm});
            skLineSegment(sketch, "E2421", {"start": v(-63.02, 0.8) * mm, "end": v(-63.23, 0.81) * mm});
            skLineSegment(sketch, "E2422", {"start": v(-63.23, 0.81) * mm, "end": v(-63.44, 0.81) * mm});
            skLineSegment(sketch, "E2423", {"start": v(-63.44, 0.81) * mm, "end": v(-63.65, 0.82) * mm});
            skLineSegment(sketch, "E2424", {"start": v(-63.65, 0.82) * mm, "end": v(-63.83, 0.82) * mm});
            skLineSegment(sketch, "E2425", {"start": v(-63.83, 0.82) * mm, "end": v(-64.04, 0.8) * mm});
            skLineSegment(sketch, "E2426", {"start": v(-64.04, 0.8) * mm, "end": v(-64.24, 0.71) * mm});
            skLineSegment(sketch, "E2427", {"start": v(-64.24, 0.71) * mm, "end": v(-64.4, 0.58) * mm});
            skLineSegment(sketch, "E2428", {"start": v(-64.4, 0.58) * mm, "end": v(-64.54, 0.41) * mm});
            skLineSegment(sketch, "E2429", {"start": v(-64.54, 0.41) * mm, "end": v(-64.62, 0.21) * mm});
            skLineSegment(sketch, "E2430", {"start": v(-64.62, 0.21) * mm, "end": v(-64.65, 0) * mm});
            skLineSegment(sketch, "E2431", {"start": v(-64.65, 0) * mm, "end": v(-64.62, -0.21) * mm});
            skLineSegment(sketch, "E2432", {"start": v(-64.62, -0.21) * mm, "end": v(-64.54, -0.41) * mm});
            skLineSegment(sketch, "E2433", {"start": v(-64.54, -0.41) * mm, "end": v(-64.4, -0.58) * mm});
            skLineSegment(sketch, "E2434", {"start": v(-64.4, -0.58) * mm, "end": v(-64.24, -0.71) * mm});
            skLineSegment(sketch, "E2435", {"start": v(-64.24, -0.71) * mm, "end": v(-64.04, -0.8) * mm});
            skLineSegment(sketch, "E2436", {"start": v(-64.04, -0.8) * mm, "end": v(-63.83, -0.82) * mm});
            skLineSegment(sketch, "E2437", {"start": v(-63.83, -0.82) * mm, "end": v(-63.62, -0.82) * mm});
            skLineSegment(sketch, "E2438", {"start": v(-63.62, -0.82) * mm, "end": v(-63.41, -0.81) * mm});
            skLineSegment(sketch, "E2439", {"start": v(-63.41, -0.81) * mm, "end": v(-63.2, -0.81) * mm});
            skLineSegment(sketch, "E2440", {"start": v(-63.2, -0.81) * mm, "end": v(-63, -0.8) * mm});
            skLineSegment(sketch, "E2441", {"start": v(-63, -0.8) * mm, "end": v(-62.8, -0.8) * mm});
            skLineSegment(sketch, "E2442", {"start": v(-62.8, -0.8) * mm, "end": v(-62.58, -0.8) * mm});
            skLineSegment(sketch, "E2443", {"start": v(-62.58, -0.8) * mm, "end": v(-62.37, -0.8) * mm});
            skLineSegment(sketch, "E2444", {"start": v(-62.37, -0.8) * mm, "end": v(-62.17, -0.8) * mm});
            skLineSegment(sketch, "E2445", {"start": v(-62.17, -0.8) * mm, "end": v(-61.96, -0.8) * mm});
            skLineSegment(sketch, "E2446", {"start": v(-61.96, -0.8) * mm, "end": v(-61.75, -0.8) * mm});
            skLineSegment(sketch, "E2447", {"start": v(-61.75, -0.8) * mm, "end": v(-61.54, -0.79) * mm});
            skLineSegment(sketch, "E2448", {"start": v(-61.54, -0.79) * mm, "end": v(-61.33, -0.79) * mm});
            skLineSegment(sketch, "E2449", {"start": v(-61.33, -0.79) * mm, "end": v(-61.15, -0.78) * mm});
            skLineSegment(sketch, "E2450", {"start": v(-61.15, -0.78) * mm, "end": v(-61.15, -1) * mm});
            skLineSegment(sketch, "E2451", {"start": v(-61.15, -1) * mm, "end": v(-61.14, -1.2) * mm});
            skLineSegment(sketch, "E2452", {"start": v(-61.14, -1.2) * mm, "end": v(-61.13, -1.4) * mm});
            skLineSegment(sketch, "E2453", {"start": v(-61.13, -1.4) * mm, "end": v(-61.13, -1.6) * mm});
            skLineSegment(sketch, "E2454", {"start": v(-61.13, -1.6) * mm, "end": v(-61.12, -1.81) * mm});
            skLineSegment(sketch, "E2455", {"start": v(-61.12, -1.81) * mm, "end": v(-61.11, -2.02) * mm});
            skLineSegment(sketch, "E2456", {"start": v(-61.11, -2.02) * mm, "end": v(-61.1, -2.23) * mm});
            skLineSegment(sketch, "E2457", {"start": v(-61.1, -2.23) * mm, "end": v(-61.1, -2.43) * mm});
            skLineSegment(sketch, "E2458", {"start": v(-61.1, -2.43) * mm, "end": v(-61.1, -2.64) * mm});
            skLineSegment(sketch, "E2459", {"start": v(-61.1, -2.64) * mm, "end": v(-61.09, -2.84) * mm});
            skLineSegment(sketch, "E2460", {"start": v(-61.09, -2.84) * mm, "end": v(-61.08, -3.05) * mm});
            skLineSegment(sketch, "E2461", {"start": v(-61.08, -3.05) * mm, "end": v(-61.08, -3.15) * mm});
            skLineSegment(sketch, "E2462", {"start": v(-61.08, -3.15) * mm, "end": v(-61.28, -3.16) * mm});
            skLineSegment(sketch, "E2463", {"start": v(-61.28, -3.16) * mm, "end": v(-61.49, -3.18) * mm});
            skLineSegment(sketch, "E2464", {"start": v(-61.49, -3.18) * mm, "end": v(-61.7, -3.19) * mm});
            skLineSegment(sketch, "E2465", {"start": v(-61.7, -3.19) * mm, "end": v(-61.9, -3.2) * mm});
            skLineSegment(sketch, "E2466", {"start": v(-61.9, -3.2) * mm, "end": v(-62.11, -3.2) * mm});
            skLineSegment(sketch, "E2467", {"start": v(-62.11, -3.2) * mm, "end": v(-62.32, -3.22) * mm});
            skLineSegment(sketch, "E2468", {"start": v(-62.32, -3.22) * mm, "end": v(-62.53, -3.23) * mm});
            skLineSegment(sketch, "E2469", {"start": v(-62.53, -3.23) * mm, "end": v(-62.73, -3.24) * mm});
            skLineSegment(sketch, "E2470", {"start": v(-62.73, -3.24) * mm, "end": v(-62.94, -3.25) * mm});
            skLineSegment(sketch, "E2471", {"start": v(-62.94, -3.25) * mm, "end": v(-63.15, -3.26) * mm});
            skLineSegment(sketch, "E2472", {"start": v(-63.15, -3.26) * mm, "end": v(-63.36, -3.27) * mm});
            skLineSegment(sketch, "E2473", {"start": v(-63.36, -3.27) * mm, "end": v(-63.57, -3.28) * mm});
            skLineSegment(sketch, "E2474", {"start": v(-63.57, -3.28) * mm, "end": v(-63.79, -3.3) * mm});
            skLineSegment(sketch, "E2475", {"start": v(-63.79, -3.3) * mm, "end": v(-64, -3.35) * mm});
            skLineSegment(sketch, "E2476", {"start": v(-64, -3.35) * mm, "end": v(-64.18, -3.45) * mm});
            skLineSegment(sketch, "E2477", {"start": v(-64.18, -3.45) * mm, "end": v(-64.34, -3.6) * mm});
            skLineSegment(sketch, "E2478", {"start": v(-64.34, -3.6) * mm, "end": v(-64.45, -3.79) * mm});
            skLineSegment(sketch, "E2479", {"start": v(-64.45, -3.79) * mm, "end": v(-64.5, -4) * mm});
            skLineSegment(sketch, "E2480", {"start": v(-64.5, -4) * mm, "end": v(-64.5, -4.2) * mm});
            skLineSegment(sketch, "E2481", {"start": v(-64.5, -4.2) * mm, "end": v(-64.46, -4.42) * mm});
            skLineSegment(sketch, "E2482", {"start": v(-64.46, -4.42) * mm, "end": v(-64.35, -4.6) * mm});
            skLineSegment(sketch, "E2483", {"start": v(-64.35, -4.6) * mm, "end": v(-64.2, -4.76) * mm});
            skLineSegment(sketch, "E2484", {"start": v(-64.2, -4.76) * mm, "end": v(-64.02, -4.87) * mm});
            skLineSegment(sketch, "E2485", {"start": v(-64.02, -4.87) * mm, "end": v(-63.8, -4.92) * mm});
            skLineSegment(sketch, "E2486", {"start": v(-63.8, -4.92) * mm, "end": v(-63.6, -4.92) * mm});
            skLineSegment(sketch, "E2487", {"start": v(-63.6, -4.92) * mm, "end": v(-63.4, -4.9) * mm});
            skLineSegment(sketch, "E2488", {"start": v(-63.4, -4.9) * mm, "end": v(-63.2, -4.9) * mm});
            skLineSegment(sketch, "E2489", {"start": v(-63.2, -4.9) * mm, "end": v(-62.99, -4.88) * mm});
            skLineSegment(sketch, "E2490", {"start": v(-62.99, -4.88) * mm, "end": v(-62.78, -4.86) * mm});
            skLineSegment(sketch, "E2491", {"start": v(-62.78, -4.86) * mm, "end": v(-62.57, -4.84) * mm});
            skLineSegment(sketch, "E2492", {"start": v(-62.57, -4.84) * mm, "end": v(-62.37, -4.83) * mm});
            skLineSegment(sketch, "E2493", {"start": v(-62.37, -4.83) * mm, "end": v(-62.16, -4.81) * mm});
            skLineSegment(sketch, "E2494", {"start": v(-62.16, -4.81) * mm, "end": v(-61.95, -4.8) * mm});
            skLineSegment(sketch, "E2495", {"start": v(-61.95, -4.8) * mm, "end": v(-61.75, -4.78) * mm});
            skLineSegment(sketch, "E2496", {"start": v(-61.75, -4.78) * mm, "end": v(-61.54, -4.76) * mm});
            skLineSegment(sketch, "E2497", {"start": v(-61.54, -4.76) * mm, "end": v(-61.33, -4.75) * mm});
            skLineSegment(sketch, "E2498", {"start": v(-61.33, -4.75) * mm, "end": v(-61.12, -4.73) * mm});
            skLineSegment(sketch, "E2499", {"start": v(-61.12, -4.73) * mm, "end": v(-60.97, -4.72) * mm});
            skLineSegment(sketch, "E2500", {"start": v(-60.97, -4.72) * mm, "end": v(-60.95, -4.92) * mm});
            skLineSegment(sketch, "E2501", {"start": v(-60.95, -4.92) * mm, "end": v(-60.93, -5.13) * mm});
            skLineSegment(sketch, "E2502", {"start": v(-60.93, -5.13) * mm, "end": v(-60.91, -5.33) * mm});
            skLineSegment(sketch, "E2503", {"start": v(-60.91, -5.33) * mm, "end": v(-60.9, -5.54) * mm});
            skLineSegment(sketch, "E2504", {"start": v(-60.9, -5.54) * mm, "end": v(-60.87, -5.74) * mm});
            skLineSegment(sketch, "E2505", {"start": v(-60.87, -5.74) * mm, "end": v(-60.85, -5.95) * mm});
            skLineSegment(sketch, "E2506", {"start": v(-60.85, -5.95) * mm, "end": v(-60.83, -6.15) * mm});
            skLineSegment(sketch, "E2507", {"start": v(-60.83, -6.15) * mm, "end": v(-60.81, -6.36) * mm});
            skLineSegment(sketch, "E2508", {"start": v(-60.81, -6.36) * mm, "end": v(-60.8, -6.56) * mm});
            skLineSegment(sketch, "E2509", {"start": v(-60.8, -6.56) * mm, "end": v(-60.77, -6.77) * mm});
            skLineSegment(sketch, "E2510", {"start": v(-60.77, -6.77) * mm, "end": v(-60.75, -6.97) * mm});
            skLineSegment(sketch, "E2511", {"start": v(-60.75, -6.97) * mm, "end": v(-60.74, -7.08) * mm});
            skLineSegment(sketch, "E2512", {"start": v(-60.74, -7.08) * mm, "end": v(-60.95, -7.1) * mm});
            skLineSegment(sketch, "E2513", {"start": v(-60.95, -7.1) * mm, "end": v(-61.15, -7.13) * mm});
            skLineSegment(sketch, "E2514", {"start": v(-61.15, -7.13) * mm, "end": v(-61.36, -7.15) * mm});
            skLineSegment(sketch, "E2515", {"start": v(-61.36, -7.15) * mm, "end": v(-61.57, -7.18) * mm});
            skLineSegment(sketch, "E2516", {"start": v(-61.57, -7.18) * mm, "end": v(-61.77, -7.2) * mm});
            skLineSegment(sketch, "E2517", {"start": v(-61.77, -7.2) * mm, "end": v(-61.98, -7.22) * mm});
            skLineSegment(sketch, "E2518", {"start": v(-61.98, -7.22) * mm, "end": v(-62.18, -7.25) * mm});
            skLineSegment(sketch, "E2519", {"start": v(-62.18, -7.25) * mm, "end": v(-62.39, -7.27) * mm});
            skLineSegment(sketch, "E2520", {"start": v(-62.39, -7.27) * mm, "end": v(-62.6, -7.3) * mm});
            skLineSegment(sketch, "E2521", {"start": v(-62.6, -7.3) * mm, "end": v(-62.8, -7.32) * mm});
            skLineSegment(sketch, "E2522", {"start": v(-62.8, -7.32) * mm, "end": v(-63, -7.35) * mm});
            skLineSegment(sketch, "E2523", {"start": v(-63, -7.35) * mm, "end": v(-63.22, -7.37) * mm});
            skLineSegment(sketch, "E2524", {"start": v(-63.22, -7.37) * mm, "end": v(-63.44, -7.4) * mm});
            skLineSegment(sketch, "E2525", {"start": v(-63.44, -7.4) * mm, "end": v(-63.64, -7.46) * mm});
            skLineSegment(sketch, "E2526", {"start": v(-63.64, -7.46) * mm, "end": v(-63.82, -7.58) * mm});
            skLineSegment(sketch, "E2527", {"start": v(-63.82, -7.58) * mm, "end": v(-63.97, -7.74) * mm});
            skLineSegment(sketch, "E2528", {"start": v(-63.97, -7.74) * mm, "end": v(-64.06, -7.93) * mm});
            skLineSegment(sketch, "E2529", {"start": v(-64.06, -7.93) * mm, "end": v(-64.1, -8.14) * mm});
            skLineSegment(sketch, "E2530", {"start": v(-64.1, -8.14) * mm, "end": v(-64.1, -8.35) * mm});
            skLineSegment(sketch, "E2531", {"start": v(-64.1, -8.35) * mm, "end": v(-64.03, -8.56) * mm});
            skLineSegment(sketch, "E2532", {"start": v(-64.03, -8.56) * mm, "end": v(-63.91, -8.74) * mm});
            skLineSegment(sketch, "E2533", {"start": v(-63.91, -8.74) * mm, "end": v(-63.75, -8.88) * mm});
            skLineSegment(sketch, "E2534", {"start": v(-63.75, -8.88) * mm, "end": v(-63.56, -8.98) * mm});
            skLineSegment(sketch, "E2535", {"start": v(-63.56, -8.98) * mm, "end": v(-63.35, -9.02) * mm});
            skLineSegment(sketch, "E2536", {"start": v(-63.35, -9.02) * mm, "end": v(-63.15, -9) * mm});
            skLineSegment(sketch, "E2537", {"start": v(-63.15, -9) * mm, "end": v(-62.94, -8.98) * mm});
            skLineSegment(sketch, "E2538", {"start": v(-62.94, -8.98) * mm, "end": v(-62.74, -8.95) * mm});
            skLineSegment(sketch, "E2539", {"start": v(-62.74, -8.95) * mm, "end": v(-62.54, -8.92) * mm});
            skLineSegment(sketch, "E2540", {"start": v(-62.54, -8.92) * mm, "end": v(-62.33, -8.9) * mm});
            skLineSegment(sketch, "E2541", {"start": v(-62.33, -8.9) * mm, "end": v(-62.12, -8.86) * mm});
            skLineSegment(sketch, "E2542", {"start": v(-62.12, -8.86) * mm, "end": v(-61.92, -8.83) * mm});
            skLineSegment(sketch, "E2543", {"start": v(-61.92, -8.83) * mm, "end": v(-61.72, -8.8) * mm});
            skLineSegment(sketch, "E2544", {"start": v(-61.72, -8.8) * mm, "end": v(-61.5, -8.77) * mm});
            skLineSegment(sketch, "E2545", {"start": v(-61.5, -8.77) * mm, "end": v(-61.3, -8.74) * mm});
            skLineSegment(sketch, "E2546", {"start": v(-61.3, -8.74) * mm, "end": v(-61.1, -8.71) * mm});
            skLineSegment(sketch, "E2547", {"start": v(-61.1, -8.71) * mm, "end": v(-60.89, -8.68) * mm});
            skLineSegment(sketch, "E2548", {"start": v(-60.89, -8.68) * mm, "end": v(-60.69, -8.65) * mm});
            skLineSegment(sketch, "E2549", {"start": v(-60.69, -8.65) * mm, "end": v(-60.54, -8.63) * mm});
            skLineSegment(sketch, "E2550", {"start": v(-60.54, -8.63) * mm, "end": v(-60.5, -8.84) * mm});
            skLineSegment(sketch, "E2551", {"start": v(-60.5, -8.84) * mm, "end": v(-60.47, -9.04) * mm});
            skLineSegment(sketch, "E2552", {"start": v(-60.47, -9.04) * mm, "end": v(-60.44, -9.24) * mm});
            skLineSegment(sketch, "E2553", {"start": v(-60.44, -9.24) * mm, "end": v(-60.4, -9.45) * mm});
            skLineSegment(sketch, "E2554", {"start": v(-60.4, -9.45) * mm, "end": v(-60.37, -9.65) * mm});
            skLineSegment(sketch, "E2555", {"start": v(-60.37, -9.65) * mm, "end": v(-60.34, -9.85) * mm});
            skLineSegment(sketch, "E2556", {"start": v(-60.34, -9.85) * mm, "end": v(-60.3, -10.05) * mm});
            skLineSegment(sketch, "E2557", {"start": v(-60.3, -10.05) * mm, "end": v(-60.27, -10.26) * mm});
            skLineSegment(sketch, "E2558", {"start": v(-60.27, -10.26) * mm, "end": v(-60.23, -10.46) * mm});
            skLineSegment(sketch, "E2559", {"start": v(-60.23, -10.46) * mm, "end": v(-60.2, -10.66) * mm});
            skLineSegment(sketch, "E2560", {"start": v(-60.2, -10.66) * mm, "end": v(-60.17, -10.87) * mm});
            skLineSegment(sketch, "E2561", {"start": v(-60.17, -10.87) * mm, "end": v(-60.15, -10.97) * mm});
            skLineSegment(sketch, "E2562", {"start": v(-60.15, -10.97) * mm, "end": v(-60.35, -11) * mm});
            skLineSegment(sketch, "E2563", {"start": v(-60.35, -11) * mm, "end": v(-60.56, -11.05) * mm});
            skLineSegment(sketch, "E2564", {"start": v(-60.56, -11.05) * mm, "end": v(-60.76, -11.09) * mm});
            skLineSegment(sketch, "E2565", {"start": v(-60.76, -11.09) * mm, "end": v(-60.97, -11.12) * mm});
            skLineSegment(sketch, "E2566", {"start": v(-60.97, -11.12) * mm, "end": v(-61.17, -11.16) * mm});
            skLineSegment(sketch, "E2567", {"start": v(-61.17, -11.16) * mm, "end": v(-61.38, -11.2) * mm});
            skLineSegment(sketch, "E2568", {"start": v(-61.38, -11.2) * mm, "end": v(-61.58, -11.24) * mm});
            skLineSegment(sketch, "E2569", {"start": v(-61.58, -11.24) * mm, "end": v(-61.78, -11.27) * mm});
            skLineSegment(sketch, "E2570", {"start": v(-61.78, -11.27) * mm, "end": v(-61.99, -11.31) * mm});
            skLineSegment(sketch, "E2571", {"start": v(-61.99, -11.31) * mm, "end": v(-62.2, -11.35) * mm});
            skLineSegment(sketch, "E2572", {"start": v(-62.2, -11.35) * mm, "end": v(-62.4, -11.39) * mm});
            skLineSegment(sketch, "E2573", {"start": v(-62.4, -11.39) * mm, "end": v(-62.6, -11.43) * mm});
            skLineSegment(sketch, "E2574", {"start": v(-62.6, -11.43) * mm, "end": v(-62.82, -11.47) * mm});
            skLineSegment(sketch, "E2575", {"start": v(-62.82, -11.47) * mm, "end": v(-63.02, -11.55) * mm});
            skLineSegment(sketch, "E2576", {"start": v(-63.02, -11.55) * mm, "end": v(-63.2, -11.67) * mm});
            skLineSegment(sketch, "E2577", {"start": v(-63.2, -11.67) * mm, "end": v(-63.33, -11.84) * mm});
            skLineSegment(sketch, "E2578", {"start": v(-63.33, -11.84) * mm, "end": v(-63.41, -12.04) * mm});
            skLineSegment(sketch, "E2579", {"start": v(-63.41, -12.04) * mm, "end": v(-63.44, -12.25) * mm});
            skLineSegment(sketch, "E2580", {"start": v(-63.44, -12.25) * mm, "end": v(-63.42, -12.46) * mm});
            skLineSegment(sketch, "E2581", {"start": v(-63.42, -12.46) * mm, "end": v(-63.34, -12.66) * mm});
            skLineSegment(sketch, "E2582", {"start": v(-63.34, -12.66) * mm, "end": v(-63.2, -12.84) * mm});
            skLineSegment(sketch, "E2583", {"start": v(-63.2, -12.84) * mm, "end": v(-63.04, -12.97) * mm});
            skLineSegment(sketch, "E2584", {"start": v(-63.04, -12.97) * mm, "end": v(-62.84, -13.05) * mm});
            skLineSegment(sketch, "E2585", {"start": v(-62.84, -13.05) * mm, "end": v(-62.63, -13.08) * mm});
            skLineSegment(sketch, "E2586", {"start": v(-62.63, -13.08) * mm, "end": v(-62.43, -13.05) * mm});
            skLineSegment(sketch, "E2587", {"start": v(-62.43, -13.05) * mm, "end": v(-62.22, -13.01) * mm});
            skLineSegment(sketch, "E2588", {"start": v(-62.22, -13.01) * mm, "end": v(-62.02, -12.97) * mm});
            skLineSegment(sketch, "E2589", {"start": v(-62.02, -12.97) * mm, "end": v(-61.82, -12.93) * mm});
            skLineSegment(sketch, "E2590", {"start": v(-61.82, -12.93) * mm, "end": v(-61.62, -12.89) * mm});
            skLineSegment(sketch, "E2591", {"start": v(-61.62, -12.89) * mm, "end": v(-61.41, -12.84) * mm});
            skLineSegment(sketch, "E2592", {"start": v(-61.41, -12.84) * mm, "end": v(-61.21, -12.8) * mm});
            skLineSegment(sketch, "E2593", {"start": v(-61.21, -12.8) * mm, "end": v(-61.01, -12.76) * mm});
            skLineSegment(sketch, "E2594", {"start": v(-61.01, -12.76) * mm, "end": v(-60.8, -12.71) * mm});
            skLineSegment(sketch, "E2595", {"start": v(-60.8, -12.71) * mm, "end": v(-60.6, -12.67) * mm});
            skLineSegment(sketch, "E2596", {"start": v(-60.6, -12.67) * mm, "end": v(-60.4, -12.63) * mm});
            skLineSegment(sketch, "E2597", {"start": v(-60.4, -12.63) * mm, "end": v(-60.2, -12.58) * mm});
            skLineSegment(sketch, "E2598", {"start": v(-60.2, -12.58) * mm, "end": v(-60, -12.54) * mm});
            skLineSegment(sketch, "E2599", {"start": v(-60, -12.54) * mm, "end": v(-59.84, -12.5) * mm});
            skLineSegment(sketch, "E2600", {"start": v(-59.84, -12.5) * mm, "end": v(-59.8, -12.7) * mm});
            skLineSegment(sketch, "E2601", {"start": v(-59.8, -12.7) * mm, "end": v(-59.75, -12.91) * mm});
            skLineSegment(sketch, "E2602", {"start": v(-59.75, -12.91) * mm, "end": v(-59.7, -13.11) * mm});
            skLineSegment(sketch, "E2603", {"start": v(-59.7, -13.11) * mm, "end": v(-59.66, -13.31) * mm});
            skLineSegment(sketch, "E2604", {"start": v(-59.66, -13.31) * mm, "end": v(-59.61, -13.51) * mm});
            skLineSegment(sketch, "E2605", {"start": v(-59.61, -13.51) * mm, "end": v(-59.56, -13.71) * mm});
            skLineSegment(sketch, "E2606", {"start": v(-59.56, -13.71) * mm, "end": v(-59.52, -13.91) * mm});
            skLineSegment(sketch, "E2607", {"start": v(-59.52, -13.91) * mm, "end": v(-59.47, -14.11) * mm});
            skLineSegment(sketch, "E2608", {"start": v(-59.47, -14.11) * mm, "end": v(-59.42, -14.31) * mm});
            skLineSegment(sketch, "E2609", {"start": v(-59.42, -14.31) * mm, "end": v(-59.38, -14.52) * mm});
            skLineSegment(sketch, "E2610", {"start": v(-59.38, -14.52) * mm, "end": v(-59.33, -14.72) * mm});
            skLineSegment(sketch, "E2611", {"start": v(-59.33, -14.72) * mm, "end": v(-59.3, -14.82) * mm});
            skLineSegment(sketch, "E2612", {"start": v(-59.3, -14.82) * mm, "end": v(-59.5, -14.87) * mm});
            skLineSegment(sketch, "E2613", {"start": v(-59.5, -14.87) * mm, "end": v(-59.7, -14.92) * mm});
            skLineSegment(sketch, "E2614", {"start": v(-59.7, -14.92) * mm, "end": v(-59.91, -14.97) * mm});
            skLineSegment(sketch, "E2615", {"start": v(-59.91, -14.97) * mm, "end": v(-60.11, -15.02) * mm});
            skLineSegment(sketch, "E2616", {"start": v(-60.11, -15.02) * mm, "end": v(-60.3, -15.07) * mm});
            skLineSegment(sketch, "E2617", {"start": v(-60.3, -15.07) * mm, "end": v(-60.51, -15.13) * mm});
            skLineSegment(sketch, "E2618", {"start": v(-60.51, -15.13) * mm, "end": v(-60.71, -15.18) * mm});
            skLineSegment(sketch, "E2619", {"start": v(-60.71, -15.18) * mm, "end": v(-60.91, -15.23) * mm});
            skLineSegment(sketch, "E2620", {"start": v(-60.91, -15.23) * mm, "end": v(-61.12, -15.28) * mm});
            skLineSegment(sketch, "E2621", {"start": v(-61.12, -15.28) * mm, "end": v(-61.32, -15.33) * mm});
            skLineSegment(sketch, "E2622", {"start": v(-61.32, -15.33) * mm, "end": v(-61.52, -15.38) * mm});
            skLineSegment(sketch, "E2623", {"start": v(-61.52, -15.38) * mm, "end": v(-61.72, -15.43) * mm});
            skLineSegment(sketch, "E2624", {"start": v(-61.72, -15.43) * mm, "end": v(-61.94, -15.49) * mm});
            skLineSegment(sketch, "E2625", {"start": v(-61.94, -15.49) * mm, "end": v(-62.13, -15.58) * mm});
            skLineSegment(sketch, "E2626", {"start": v(-62.13, -15.58) * mm, "end": v(-62.3, -15.72) * mm});
            skLineSegment(sketch, "E2627", {"start": v(-62.3, -15.72) * mm, "end": v(-62.42, -15.9) * mm});
            skLineSegment(sketch, "E2628", {"start": v(-62.42, -15.9) * mm, "end": v(-62.49, -16.1) * mm});
            skLineSegment(sketch, "E2629", {"start": v(-62.49, -16.1) * mm, "end": v(-62.5, -16.31) * mm});
            skLineSegment(sketch, "E2630", {"start": v(-62.5, -16.31) * mm, "end": v(-62.47, -16.52) * mm});
            skLineSegment(sketch, "E2631", {"start": v(-62.47, -16.52) * mm, "end": v(-62.38, -16.72) * mm});
            skLineSegment(sketch, "E2632", {"start": v(-62.38, -16.72) * mm, "end": v(-62.24, -16.88) * mm});
            skLineSegment(sketch, "E2633", {"start": v(-62.24, -16.88) * mm, "end": v(-62.06, -17) * mm});
            skLineSegment(sketch, "E2634", {"start": v(-62.06, -17) * mm, "end": v(-61.86, -17.07) * mm});
            skLineSegment(sketch, "E2635", {"start": v(-61.86, -17.07) * mm, "end": v(-61.64, -17.09) * mm});
            skLineSegment(sketch, "E2636", {"start": v(-61.64, -17.09) * mm, "end": v(-61.44, -17.04) * mm});
            skLineSegment(sketch, "E2637", {"start": v(-61.44, -17.04) * mm, "end": v(-61.24, -17) * mm});
            skLineSegment(sketch, "E2638", {"start": v(-61.24, -17) * mm, "end": v(-61.04, -16.94) * mm});
            skLineSegment(sketch, "E2639", {"start": v(-61.04, -16.94) * mm, "end": v(-60.85, -16.88) * mm});
            skLineSegment(sketch, "E2640", {"start": v(-60.85, -16.88) * mm, "end": v(-60.65, -16.83) * mm});
            skLineSegment(sketch, "E2641", {"start": v(-60.65, -16.83) * mm, "end": v(-60.44, -16.77) * mm});
            skLineSegment(sketch, "E2642", {"start": v(-60.44, -16.77) * mm, "end": v(-60.25, -16.71) * mm});
            skLineSegment(sketch, "E2643", {"start": v(-60.25, -16.71) * mm, "end": v(-60.05, -16.66) * mm});
            skLineSegment(sketch, "E2644", {"start": v(-60.05, -16.66) * mm, "end": v(-59.84, -16.6) * mm});
            skLineSegment(sketch, "E2645", {"start": v(-59.84, -16.6) * mm, "end": v(-59.65, -16.54) * mm});
            skLineSegment(sketch, "E2646", {"start": v(-59.65, -16.54) * mm, "end": v(-59.45, -16.49) * mm});
            skLineSegment(sketch, "E2647", {"start": v(-59.45, -16.49) * mm, "end": v(-59.24, -16.43) * mm});
            skLineSegment(sketch, "E2648", {"start": v(-59.24, -16.43) * mm, "end": v(-59.05, -16.37) * mm});
            skLineSegment(sketch, "E2649", {"start": v(-59.05, -16.37) * mm, "end": v(-58.9, -16.33) * mm});
            skLineSegment(sketch, "E2650", {"start": v(-58.9, -16.33) * mm, "end": v(-58.84, -16.53) * mm});
            skLineSegment(sketch, "E2651", {"start": v(-58.84, -16.53) * mm, "end": v(-58.78, -16.73) * mm});
            skLineSegment(sketch, "E2652", {"start": v(-58.78, -16.73) * mm, "end": v(-58.72, -16.92) * mm});
            skLineSegment(sketch, "E2653", {"start": v(-58.72, -16.92) * mm, "end": v(-58.66, -17.12) * mm});
            skLineSegment(sketch, "E2654", {"start": v(-58.66, -17.12) * mm, "end": v(-58.6, -17.32) * mm});
            skLineSegment(sketch, "E2655", {"start": v(-58.6, -17.32) * mm, "end": v(-58.54, -17.52) * mm});
            skLineSegment(sketch, "E2656", {"start": v(-58.54, -17.52) * mm, "end": v(-58.48, -17.71) * mm});
            skLineSegment(sketch, "E2657", {"start": v(-58.48, -17.71) * mm, "end": v(-58.42, -17.9) * mm});
            skLineSegment(sketch, "E2658", {"start": v(-58.42, -17.9) * mm, "end": v(-58.36, -18.1) * mm});
            skLineSegment(sketch, "E2659", {"start": v(-58.36, -18.1) * mm, "end": v(-58.3, -18.3) * mm});
            skLineSegment(sketch, "E2660", {"start": v(-58.3, -18.3) * mm, "end": v(-58.24, -18.5) * mm});
            skLineSegment(sketch, "E2661", {"start": v(-58.24, -18.5) * mm, "end": v(-58.21, -18.6) * mm});
            skLineSegment(sketch, "E2662", {"start": v(-58.21, -18.6) * mm, "end": v(-58.4, -18.66) * mm});
            skLineSegment(sketch, "E2663", {"start": v(-58.4, -18.66) * mm, "end": v(-58.6, -18.73) * mm});
            skLineSegment(sketch, "E2664", {"start": v(-58.6, -18.73) * mm, "end": v(-58.8, -18.8) * mm});
            skLineSegment(sketch, "E2665", {"start": v(-58.8, -18.8) * mm, "end": v(-59, -18.86) * mm});
            skLineSegment(sketch, "E2666", {"start": v(-59, -18.86) * mm, "end": v(-59.2, -18.92) * mm});
            skLineSegment(sketch, "E2667", {"start": v(-59.2, -18.92) * mm, "end": v(-59.4, -18.99) * mm});
            skLineSegment(sketch, "E2668", {"start": v(-59.4, -18.99) * mm, "end": v(-59.6, -19.05) * mm});
            skLineSegment(sketch, "E2669", {"start": v(-59.6, -19.05) * mm, "end": v(-59.79, -19.11) * mm});
            skLineSegment(sketch, "E2670", {"start": v(-59.79, -19.11) * mm, "end": v(-60, -19.18) * mm});
            skLineSegment(sketch, "E2671", {"start": v(-60, -19.18) * mm, "end": v(-60.19, -19.24) * mm});
            skLineSegment(sketch, "E2672", {"start": v(-60.19, -19.24) * mm, "end": v(-60.38, -19.3) * mm});
            skLineSegment(sketch, "E2673", {"start": v(-60.38, -19.3) * mm, "end": v(-60.58, -19.37) * mm});
            skLineSegment(sketch, "E2674", {"start": v(-60.58, -19.37) * mm, "end": v(-60.8, -19.44) * mm});
            skLineSegment(sketch, "E2675", {"start": v(-60.8, -19.44) * mm, "end": v(-60.98, -19.55) * mm});
            skLineSegment(sketch, "E2676", {"start": v(-60.98, -19.55) * mm, "end": v(-61.14, -19.7) * mm});
            skLineSegment(sketch, "E2677", {"start": v(-61.14, -19.7) * mm, "end": v(-61.25, -19.88) * mm});
            skLineSegment(sketch, "E2678", {"start": v(-61.25, -19.88) * mm, "end": v(-61.3, -20.09) * mm});
            skLineSegment(sketch, "E2679", {"start": v(-61.3, -20.09) * mm, "end": v(-61.3, -20.3) * mm});
            skLineSegment(sketch, "E2680", {"start": v(-61.3, -20.3) * mm, "end": v(-61.26, -20.5) * mm});
            skLineSegment(sketch, "E2681", {"start": v(-61.26, -20.5) * mm, "end": v(-61.15, -20.7) * mm});
            skLineSegment(sketch, "E2682", {"start": v(-61.15, -20.7) * mm, "end": v(-61, -20.85) * mm});
            skLineSegment(sketch, "E2683", {"start": v(-61, -20.85) * mm, "end": v(-60.82, -20.96) * mm});
            skLineSegment(sketch, "E2684", {"start": v(-60.82, -20.96) * mm, "end": v(-60.6, -21.02) * mm});
            skLineSegment(sketch, "E2685", {"start": v(-60.6, -21.02) * mm, "end": v(-60.4, -21.02) * mm});
            skLineSegment(sketch, "E2686", {"start": v(-60.4, -21.02) * mm, "end": v(-60.2, -20.96) * mm});
            skLineSegment(sketch, "E2687", {"start": v(-60.2, -20.96) * mm, "end": v(-60, -20.9) * mm});
            skLineSegment(sketch, "E2688", {"start": v(-60, -20.9) * mm, "end": v(-59.8, -20.83) * mm});
            skLineSegment(sketch, "E2689", {"start": v(-59.8, -20.83) * mm, "end": v(-59.61, -20.76) * mm});
            skLineSegment(sketch, "E2690", {"start": v(-59.61, -20.76) * mm, "end": v(-59.42, -20.7) * mm});
            skLineSegment(sketch, "E2691", {"start": v(-59.42, -20.7) * mm, "end": v(-59.22, -20.62) * mm});
            skLineSegment(sketch, "E2692", {"start": v(-59.22, -20.62) * mm, "end": v(-59.03, -20.55) * mm});
            skLineSegment(sketch, "E2693", {"start": v(-59.03, -20.55) * mm, "end": v(-58.83, -20.48) * mm});
            skLineSegment(sketch, "E2694", {"start": v(-58.83, -20.48) * mm, "end": v(-58.63, -20.41) * mm});
            skLineSegment(sketch, "E2695", {"start": v(-58.63, -20.41) * mm, "end": v(-58.44, -20.34) * mm});
            skLineSegment(sketch, "E2696", {"start": v(-58.44, -20.34) * mm, "end": v(-58.24, -20.28) * mm});
            skLineSegment(sketch, "E2697", {"start": v(-58.24, -20.28) * mm, "end": v(-58.04, -20.2) * mm});
            skLineSegment(sketch, "E2698", {"start": v(-58.04, -20.2) * mm, "end": v(-57.85, -20.14) * mm});
            skLineSegment(sketch, "E2699", {"start": v(-57.85, -20.14) * mm, "end": v(-57.7, -20.09) * mm});
            skLineSegment(sketch, "E2700", {"start": v(-57.7, -20.09) * mm, "end": v(-57.64, -20.28) * mm});
            skLineSegment(sketch, "E2701", {"start": v(-57.64, -20.28) * mm, "end": v(-57.56, -20.47) * mm});
            skLineSegment(sketch, "E2702", {"start": v(-57.56, -20.47) * mm, "end": v(-57.5, -20.66) * mm});
            skLineSegment(sketch, "E2703", {"start": v(-57.5, -20.66) * mm, "end": v(-57.42, -20.86) * mm});
            skLineSegment(sketch, "E2704", {"start": v(-57.42, -20.86) * mm, "end": v(-57.35, -21.05) * mm});
            skLineSegment(sketch, "E2705", {"start": v(-57.35, -21.05) * mm, "end": v(-57.27, -21.24) * mm});
            skLineSegment(sketch, "E2706", {"start": v(-57.27, -21.24) * mm, "end": v(-57.2, -21.44) * mm});
            skLineSegment(sketch, "E2707", {"start": v(-57.2, -21.44) * mm, "end": v(-57.13, -21.63) * mm});
            skLineSegment(sketch, "E2708", {"start": v(-57.13, -21.63) * mm, "end": v(-57.06, -21.82) * mm});
            skLineSegment(sketch, "E2709", {"start": v(-57.06, -21.82) * mm, "end": v(-56.98, -22.01) * mm});
            skLineSegment(sketch, "E2710", {"start": v(-56.98, -22.01) * mm, "end": v(-56.91, -22.2) * mm});
            skLineSegment(sketch, "E2711", {"start": v(-56.91, -22.2) * mm, "end": v(-56.87, -22.3) * mm});
            skLineSegment(sketch, "E2712", {"start": v(-56.87, -22.3) * mm, "end": v(-57.06, -22.38) * mm});
            skLineSegment(sketch, "E2713", {"start": v(-57.06, -22.38) * mm, "end": v(-57.26, -22.46) * mm});
            skLineSegment(sketch, "E2714", {"start": v(-57.26, -22.46) * mm, "end": v(-57.45, -22.54) * mm});
            skLineSegment(sketch, "E2715", {"start": v(-57.45, -22.54) * mm, "end": v(-57.64, -22.61) * mm});
            skLineSegment(sketch, "E2716", {"start": v(-57.64, -22.61) * mm, "end": v(-57.83, -22.69) * mm});
            skLineSegment(sketch, "E2717", {"start": v(-57.83, -22.69) * mm, "end": v(-58.03, -22.77) * mm});
            skLineSegment(sketch, "E2718", {"start": v(-58.03, -22.77) * mm, "end": v(-58.22, -22.84) * mm});
            skLineSegment(sketch, "E2719", {"start": v(-58.22, -22.84) * mm, "end": v(-58.41, -22.92) * mm});
            skLineSegment(sketch, "E2720", {"start": v(-58.41, -22.92) * mm, "end": v(-58.61, -23) * mm});
            skLineSegment(sketch, "E2721", {"start": v(-58.61, -23) * mm, "end": v(-58.8, -23.07) * mm});
            skLineSegment(sketch, "E2722", {"start": v(-58.8, -23.07) * mm, "end": v(-59, -23.15) * mm});
            skLineSegment(sketch, "E2723", {"start": v(-59, -23.15) * mm, "end": v(-59.19, -23.23) * mm});
            skLineSegment(sketch, "E2724", {"start": v(-59.19, -23.23) * mm, "end": v(-59.4, -23.31) * mm});
            skLineSegment(sketch, "E2725", {"start": v(-59.4, -23.31) * mm, "end": v(-59.58, -23.43) * mm});
            skLineSegment(sketch, "E2726", {"start": v(-59.58, -23.43) * mm, "end": v(-59.72, -23.59) * mm});
            skLineSegment(sketch, "E2727", {"start": v(-59.72, -23.59) * mm, "end": v(-59.82, -23.78) * mm});
            skLineSegment(sketch, "E2728", {"start": v(-59.82, -23.78) * mm, "end": v(-59.86, -23.99) * mm});
            skLineSegment(sketch, "E2729", {"start": v(-59.86, -23.99) * mm, "end": v(-59.85, -24.2) * mm});
            skLineSegment(sketch, "E2730", {"start": v(-59.85, -24.2) * mm, "end": v(-59.79, -24.4) * mm});
            skLineSegment(sketch, "E2731", {"start": v(-59.79, -24.4) * mm, "end": v(-59.67, -24.59) * mm});
            skLineSegment(sketch, "E2732", {"start": v(-59.67, -24.59) * mm, "end": v(-59.5, -24.73) * mm});
            skLineSegment(sketch, "E2733", {"start": v(-59.5, -24.73) * mm, "end": v(-59.32, -24.83) * mm});
            skLineSegment(sketch, "E2734", {"start": v(-59.32, -24.83) * mm, "end": v(-59.1, -24.87) * mm});
            skLineSegment(sketch, "E2735", {"start": v(-59.1, -24.87) * mm, "end": v(-58.9, -24.86) * mm});
            skLineSegment(sketch, "E2736", {"start": v(-58.9, -24.86) * mm, "end": v(-58.7, -24.8) * mm});
            skLineSegment(sketch, "E2737", {"start": v(-58.7, -24.8) * mm, "end": v(-58.5, -24.71) * mm});
            skLineSegment(sketch, "E2738", {"start": v(-58.5, -24.71) * mm, "end": v(-58.32, -24.63) * mm});
            skLineSegment(sketch, "E2739", {"start": v(-58.32, -24.63) * mm, "end": v(-58.13, -24.55) * mm});
            skLineSegment(sketch, "E2740", {"start": v(-58.13, -24.55) * mm, "end": v(-57.94, -24.47) * mm});
            skLineSegment(sketch, "E2741", {"start": v(-57.94, -24.47) * mm, "end": v(-57.75, -24.39) * mm});
            skLineSegment(sketch, "E2742", {"start": v(-57.75, -24.39) * mm, "end": v(-57.56, -24.3) * mm});
            skLineSegment(sketch, "E2743", {"start": v(-57.56, -24.3) * mm, "end": v(-57.37, -24.22) * mm});
            skLineSegment(sketch, "E2744", {"start": v(-57.37, -24.22) * mm, "end": v(-57.17, -24.14) * mm});
            skLineSegment(sketch, "E2745", {"start": v(-57.17, -24.14) * mm, "end": v(-56.98, -24.06) * mm});
            skLineSegment(sketch, "E2746", {"start": v(-56.98, -24.06) * mm, "end": v(-56.8, -23.98) * mm});
            skLineSegment(sketch, "E2747", {"start": v(-56.8, -23.98) * mm, "end": v(-56.6, -23.9) * mm});
            skLineSegment(sketch, "E2748", {"start": v(-56.6, -23.9) * mm, "end": v(-56.41, -23.81) * mm});
            skLineSegment(sketch, "E2749", {"start": v(-56.41, -23.81) * mm, "end": v(-56.27, -23.75) * mm});
            skLineSegment(sketch, "E2750", {"start": v(-56.27, -23.75) * mm, "end": v(-56.19, -23.94) * mm});
            skLineSegment(sketch, "E2751", {"start": v(-56.19, -23.94) * mm, "end": v(-56.1, -24.13) * mm});
            skLineSegment(sketch, "E2752", {"start": v(-56.1, -24.13) * mm, "end": v(-56.02, -24.32) * mm});
            skLineSegment(sketch, "E2753", {"start": v(-56.02, -24.32) * mm, "end": v(-55.93, -24.5) * mm});
            skLineSegment(sketch, "E2754", {"start": v(-55.93, -24.5) * mm, "end": v(-55.85, -24.7) * mm});
            skLineSegment(sketch, "E2755", {"start": v(-55.85, -24.7) * mm, "end": v(-55.76, -24.88) * mm});
            skLineSegment(sketch, "E2756", {"start": v(-55.76, -24.88) * mm, "end": v(-55.68, -25.07) * mm});
            skLineSegment(sketch, "E2757", {"start": v(-55.68, -25.07) * mm, "end": v(-55.6, -25.25) * mm});
            skLineSegment(sketch, "E2758", {"start": v(-55.6, -25.25) * mm, "end": v(-55.5, -25.44) * mm});
            skLineSegment(sketch, "E2759", {"start": v(-55.5, -25.44) * mm, "end": v(-55.42, -25.63) * mm});
            skLineSegment(sketch, "E2760", {"start": v(-55.42, -25.63) * mm, "end": v(-55.34, -25.82) * mm});
            skLineSegment(sketch, "E2761", {"start": v(-55.34, -25.82) * mm, "end": v(-55.3, -25.91) * mm});
            skLineSegment(sketch, "E2762", {"start": v(-55.3, -25.91) * mm, "end": v(-55.48, -26) * mm});
            skLineSegment(sketch, "E2763", {"start": v(-55.48, -26) * mm, "end": v(-55.67, -26.1) * mm});
            skLineSegment(sketch, "E2764", {"start": v(-55.67, -26.1) * mm, "end": v(-55.86, -26.18) * mm});
            skLineSegment(sketch, "E2765", {"start": v(-55.86, -26.18) * mm, "end": v(-56.04, -26.27) * mm});
            skLineSegment(sketch, "E2766", {"start": v(-56.04, -26.27) * mm, "end": v(-56.23, -26.36) * mm});
            skLineSegment(sketch, "E2767", {"start": v(-56.23, -26.36) * mm, "end": v(-56.42, -26.45) * mm});
            skLineSegment(sketch, "E2768", {"start": v(-56.42, -26.45) * mm, "end": v(-56.6, -26.54) * mm});
            skLineSegment(sketch, "E2769", {"start": v(-56.6, -26.54) * mm, "end": v(-56.8, -26.63) * mm});
            skLineSegment(sketch, "E2770", {"start": v(-56.8, -26.63) * mm, "end": v(-56.98, -26.72) * mm});
            skLineSegment(sketch, "E2771", {"start": v(-56.98, -26.72) * mm, "end": v(-57.17, -26.8) * mm});
            skLineSegment(sketch, "E2772", {"start": v(-57.17, -26.8) * mm, "end": v(-57.35, -26.9) * mm});
            skLineSegment(sketch, "E2773", {"start": v(-57.35, -26.9) * mm, "end": v(-57.55, -26.99) * mm});
            skLineSegment(sketch, "E2774", {"start": v(-57.55, -26.99) * mm, "end": v(-57.74, -27.08) * mm});
            skLineSegment(sketch, "E2775", {"start": v(-57.74, -27.08) * mm, "end": v(-57.92, -27.21) * mm});
            skLineSegment(sketch, "E2776", {"start": v(-57.92, -27.21) * mm, "end": v(-58.05, -27.38) * mm});
            skLineSegment(sketch, "E2777", {"start": v(-58.05, -27.38) * mm, "end": v(-58.14, -27.58) * mm});
            skLineSegment(sketch, "E2778", {"start": v(-58.14, -27.58) * mm, "end": v(-58.17, -27.79) * mm});
            skLineSegment(sketch, "E2779", {"start": v(-58.17, -27.79) * mm, "end": v(-58.14, -28) * mm});
            skLineSegment(sketch, "E2780", {"start": v(-58.14, -28) * mm, "end": v(-58.06, -28.2) * mm});
            skLineSegment(sketch, "E2781", {"start": v(-58.06, -28.2) * mm, "end": v(-57.93, -28.37) * mm});
            skLineSegment(sketch, "E2782", {"start": v(-57.93, -28.37) * mm, "end": v(-57.77, -28.5) * mm});
            skLineSegment(sketch, "E2783", {"start": v(-57.77, -28.5) * mm, "end": v(-57.57, -28.59) * mm});
            skLineSegment(sketch, "E2784", {"start": v(-57.57, -28.59) * mm, "end": v(-57.36, -28.62) * mm});
            skLineSegment(sketch, "E2785", {"start": v(-57.36, -28.62) * mm, "end": v(-57.14, -28.6) * mm});
            skLineSegment(sketch, "E2786", {"start": v(-57.14, -28.6) * mm, "end": v(-56.95, -28.51) * mm});
            skLineSegment(sketch, "E2787", {"start": v(-56.95, -28.51) * mm, "end": v(-56.77, -28.42) * mm});
            skLineSegment(sketch, "E2788", {"start": v(-56.77, -28.42) * mm, "end": v(-56.59, -28.33) * mm});
            skLineSegment(sketch, "E2789", {"start": v(-56.59, -28.33) * mm, "end": v(-56.4, -28.24) * mm});
            skLineSegment(sketch, "E2790", {"start": v(-56.4, -28.24) * mm, "end": v(-56.22, -28.14) * mm});
            skLineSegment(sketch, "E2791", {"start": v(-56.22, -28.14) * mm, "end": v(-56.03, -28.05) * mm});
            skLineSegment(sketch, "E2792", {"start": v(-56.03, -28.05) * mm, "end": v(-55.85, -27.95) * mm});
            skLineSegment(sketch, "E2793", {"start": v(-55.85, -27.95) * mm, "end": v(-55.66, -27.86) * mm});
            skLineSegment(sketch, "E2794", {"start": v(-55.66, -27.86) * mm, "end": v(-55.47, -27.76) * mm});
            skLineSegment(sketch, "E2795", {"start": v(-55.47, -27.76) * mm, "end": v(-55.3, -27.67) * mm});
            skLineSegment(sketch, "E2796", {"start": v(-55.3, -27.67) * mm, "end": v(-55.1, -27.58) * mm});
            skLineSegment(sketch, "E2797", {"start": v(-55.1, -27.58) * mm, "end": v(-54.92, -27.48) * mm});
            skLineSegment(sketch, "E2798", {"start": v(-54.92, -27.48) * mm, "end": v(-54.74, -27.39) * mm});
            skLineSegment(sketch, "E2799", {"start": v(-54.74, -27.39) * mm, "end": v(-54.6, -27.32) * mm});
            skLineSegment(sketch, "E2800", {"start": v(-54.6, -27.32) * mm, "end": v(-54.5, -27.5) * mm});
            skLineSegment(sketch, "E2801", {"start": v(-54.5, -27.5) * mm, "end": v(-54.4, -27.68) * mm});
            skLineSegment(sketch, "E2802", {"start": v(-54.4, -27.68) * mm, "end": v(-54.31, -27.86) * mm});
            skLineSegment(sketch, "E2803", {"start": v(-54.31, -27.86) * mm, "end": v(-54.21, -28.05) * mm});
            skLineSegment(sketch, "E2804", {"start": v(-54.21, -28.05) * mm, "end": v(-54.12, -28.23) * mm});
            skLineSegment(sketch, "E2805", {"start": v(-54.12, -28.23) * mm, "end": v(-54.02, -28.4) * mm});
            skLineSegment(sketch, "E2806", {"start": v(-54.02, -28.4) * mm, "end": v(-53.92, -28.6) * mm});
            skLineSegment(sketch, "E2807", {"start": v(-53.92, -28.6) * mm, "end": v(-53.82, -28.77) * mm});
            skLineSegment(sketch, "E2808", {"start": v(-53.82, -28.77) * mm, "end": v(-53.73, -28.95) * mm});
            skLineSegment(sketch, "E2809", {"start": v(-53.73, -28.95) * mm, "end": v(-53.63, -29.14) * mm});
            skLineSegment(sketch, "E2810", {"start": v(-53.63, -29.14) * mm, "end": v(-53.53, -29.32) * mm});
            skLineSegment(sketch, "E2811", {"start": v(-53.53, -29.32) * mm, "end": v(-53.48, -29.4) * mm});
            skLineSegment(sketch, "E2812", {"start": v(-53.48, -29.4) * mm, "end": v(-53.66, -29.51) * mm});
            skLineSegment(sketch, "E2813", {"start": v(-53.66, -29.51) * mm, "end": v(-53.84, -29.61) * mm});
            skLineSegment(sketch, "E2814", {"start": v(-53.84, -29.61) * mm, "end": v(-54.03, -29.71) * mm});
            skLineSegment(sketch, "E2815", {"start": v(-54.03, -29.71) * mm, "end": v(-54.2, -29.82) * mm});
            skLineSegment(sketch, "E2816", {"start": v(-54.2, -29.82) * mm, "end": v(-54.39, -29.92) * mm});
            skLineSegment(sketch, "E2817", {"start": v(-54.39, -29.92) * mm, "end": v(-54.57, -30.02) * mm});
            skLineSegment(sketch, "E2818", {"start": v(-54.57, -30.02) * mm, "end": v(-54.75, -30.12) * mm});
            skLineSegment(sketch, "E2819", {"start": v(-54.75, -30.12) * mm, "end": v(-54.93, -30.22) * mm});
            skLineSegment(sketch, "E2820", {"start": v(-54.93, -30.22) * mm, "end": v(-55.12, -30.32) * mm});
            skLineSegment(sketch, "E2821", {"start": v(-55.12, -30.32) * mm, "end": v(-55.3, -30.42) * mm});
            skLineSegment(sketch, "E2822", {"start": v(-55.3, -30.42) * mm, "end": v(-55.48, -30.53) * mm});
            skLineSegment(sketch, "E2823", {"start": v(-55.48, -30.53) * mm, "end": v(-55.66, -30.63) * mm});
            skLineSegment(sketch, "E2824", {"start": v(-55.66, -30.63) * mm, "end": v(-55.85, -30.74) * mm});
            skLineSegment(sketch, "E2825", {"start": v(-55.85, -30.74) * mm, "end": v(-56.02, -30.88) * mm});
            skLineSegment(sketch, "E2826", {"start": v(-56.02, -30.88) * mm, "end": v(-56.14, -31.05) * mm});
            skLineSegment(sketch, "E2827", {"start": v(-56.14, -31.05) * mm, "end": v(-56.21, -31.25) * mm});
            skLineSegment(sketch, "E2828", {"start": v(-56.21, -31.25) * mm, "end": v(-56.23, -31.47) * mm});
            skLineSegment(sketch, "E2829", {"start": v(-56.23, -31.47) * mm, "end": v(-56.19, -31.68) * mm});
            skLineSegment(sketch, "E2830", {"start": v(-56.19, -31.68) * mm, "end": v(-56.1, -31.87) * mm});
            skLineSegment(sketch, "E2831", {"start": v(-56.1, -31.87) * mm, "end": v(-55.96, -32.04) * mm});
            skLineSegment(sketch, "E2832", {"start": v(-55.96, -32.04) * mm, "end": v(-55.78, -32.16) * mm});
            skLineSegment(sketch, "E2833", {"start": v(-55.78, -32.16) * mm, "end": v(-55.58, -32.23) * mm});
            skLineSegment(sketch, "E2834", {"start": v(-55.58, -32.23) * mm, "end": v(-55.36, -32.24) * mm});
            skLineSegment(sketch, "E2835", {"start": v(-55.36, -32.24) * mm, "end": v(-55.15, -32.2) * mm});
            skLineSegment(sketch, "E2836", {"start": v(-55.15, -32.2) * mm, "end": v(-54.97, -32.11) * mm});
            skLineSegment(sketch, "E2837", {"start": v(-54.97, -32.11) * mm, "end": v(-54.79, -32.01) * mm});
            skLineSegment(sketch, "E2838", {"start": v(-54.79, -32.01) * mm, "end": v(-54.61, -31.9) * mm});
            skLineSegment(sketch, "E2839", {"start": v(-54.61, -31.9) * mm, "end": v(-54.44, -31.8) * mm});
            skLineSegment(sketch, "E2840", {"start": v(-54.44, -31.8) * mm, "end": v(-54.26, -31.7) * mm});
            skLineSegment(sketch, "E2841", {"start": v(-54.26, -31.7) * mm, "end": v(-54.08, -31.59) * mm});
            skLineSegment(sketch, "E2842", {"start": v(-54.08, -31.59) * mm, "end": v(-53.9, -31.48) * mm});
            skLineSegment(sketch, "E2843", {"start": v(-53.9, -31.48) * mm, "end": v(-53.72, -31.38) * mm});
            skLineSegment(sketch, "E2844", {"start": v(-53.72, -31.38) * mm, "end": v(-53.54, -31.27) * mm});
            skLineSegment(sketch, "E2845", {"start": v(-53.54, -31.27) * mm, "end": v(-53.36, -31.16) * mm});
            skLineSegment(sketch, "E2846", {"start": v(-53.36, -31.16) * mm, "end": v(-53.19, -31.06) * mm});
            skLineSegment(sketch, "E2847", {"start": v(-53.19, -31.06) * mm, "end": v(-53, -30.95) * mm});
            skLineSegment(sketch, "E2848", {"start": v(-53, -30.95) * mm, "end": v(-52.83, -30.84) * mm});
            skLineSegment(sketch, "E2849", {"start": v(-52.83, -30.84) * mm, "end": v(-52.7, -30.77) * mm});
            skLineSegment(sketch, "E2850", {"start": v(-52.7, -30.77) * mm, "end": v(-52.6, -30.94) * mm});
            skLineSegment(sketch, "E2851", {"start": v(-52.6, -30.94) * mm, "end": v(-52.48, -31.12) * mm});
            skLineSegment(sketch, "E2852", {"start": v(-52.48, -31.12) * mm, "end": v(-52.37, -31.3) * mm});
            skLineSegment(sketch, "E2853", {"start": v(-52.37, -31.3) * mm, "end": v(-52.26, -31.47) * mm});
            skLineSegment(sketch, "E2854", {"start": v(-52.26, -31.47) * mm, "end": v(-52.16, -31.64) * mm});
            skLineSegment(sketch, "E2855", {"start": v(-52.16, -31.64) * mm, "end": v(-52.05, -31.82) * mm});
            skLineSegment(sketch, "E2856", {"start": v(-52.05, -31.82) * mm, "end": v(-51.94, -32) * mm});
            skLineSegment(sketch, "E2857", {"start": v(-51.94, -32) * mm, "end": v(-51.83, -32.17) * mm});
            skLineSegment(sketch, "E2858", {"start": v(-51.83, -32.17) * mm, "end": v(-51.72, -32.34) * mm});
            skLineSegment(sketch, "E2859", {"start": v(-51.72, -32.34) * mm, "end": v(-51.61, -32.52) * mm});
            skLineSegment(sketch, "E2860", {"start": v(-51.61, -32.52) * mm, "end": v(-51.5, -32.7) * mm});
            skLineSegment(sketch, "E2861", {"start": v(-51.5, -32.7) * mm, "end": v(-51.45, -32.78) * mm});
            skLineSegment(sketch, "E2862", {"start": v(-51.45, -32.78) * mm, "end": v(-51.62, -32.9) * mm});
            skLineSegment(sketch, "E2863", {"start": v(-51.62, -32.9) * mm, "end": v(-51.8, -33) * mm});
            skLineSegment(sketch, "E2864", {"start": v(-51.8, -33) * mm, "end": v(-51.97, -33.12) * mm});
            skLineSegment(sketch, "E2865", {"start": v(-51.97, -33.12) * mm, "end": v(-52.14, -33.23) * mm});
            skLineSegment(sketch, "E2866", {"start": v(-52.14, -33.23) * mm, "end": v(-52.32, -33.35) * mm});
            skLineSegment(sketch, "E2867", {"start": v(-52.32, -33.35) * mm, "end": v(-52.5, -33.46) * mm});
            skLineSegment(sketch, "E2868", {"start": v(-52.5, -33.46) * mm, "end": v(-52.67, -33.57) * mm});
            skLineSegment(sketch, "E2869", {"start": v(-52.67, -33.57) * mm, "end": v(-52.84, -33.68) * mm});
            skLineSegment(sketch, "E2870", {"start": v(-52.84, -33.68) * mm, "end": v(-53.02, -33.8) * mm});
            skLineSegment(sketch, "E2871", {"start": v(-53.02, -33.8) * mm, "end": v(-53.19, -33.91) * mm});
            skLineSegment(sketch, "E2872", {"start": v(-53.19, -33.91) * mm, "end": v(-53.36, -34.02) * mm});
            skLineSegment(sketch, "E2873", {"start": v(-53.36, -34.02) * mm, "end": v(-53.54, -34.14) * mm});
            skLineSegment(sketch, "E2874", {"start": v(-53.54, -34.14) * mm, "end": v(-53.72, -34.26) * mm});
            skLineSegment(sketch, "E2875", {"start": v(-53.72, -34.26) * mm, "end": v(-53.88, -34.41) * mm});
            skLineSegment(sketch, "E2876", {"start": v(-53.88, -34.41) * mm, "end": v(-53.99, -34.6) * mm});
            skLineSegment(sketch, "E2877", {"start": v(-53.99, -34.6) * mm, "end": v(-54.05, -34.8) * mm});
            skLineSegment(sketch, "E2878", {"start": v(-54.05, -34.8) * mm, "end": v(-54.05, -35.01) * mm});
            skLineSegment(sketch, "E2879", {"start": v(-54.05, -35.01) * mm, "end": v(-54, -35.22) * mm});
            skLineSegment(sketch, "E2880", {"start": v(-54, -35.22) * mm, "end": v(-53.9, -35.41) * mm});
            skLineSegment(sketch, "E2881", {"start": v(-53.9, -35.41) * mm, "end": v(-53.74, -35.56) * mm});
            skLineSegment(sketch, "E2882", {"start": v(-53.74, -35.56) * mm, "end": v(-53.56, -35.67) * mm});
            skLineSegment(sketch, "E2883", {"start": v(-53.56, -35.67) * mm, "end": v(-53.35, -35.73) * mm});
            skLineSegment(sketch, "E2884", {"start": v(-53.35, -35.73) * mm, "end": v(-53.14, -35.73) * mm});
            skLineSegment(sketch, "E2885", {"start": v(-53.14, -35.73) * mm, "end": v(-52.93, -35.68) * mm});
            skLineSegment(sketch, "E2886", {"start": v(-52.93, -35.68) * mm, "end": v(-52.75, -35.58) * mm});
            skLineSegment(sketch, "E2887", {"start": v(-52.75, -35.58) * mm, "end": v(-52.58, -35.46) * mm});
            skLineSegment(sketch, "E2888", {"start": v(-52.58, -35.46) * mm, "end": v(-52.41, -35.35) * mm});
            skLineSegment(sketch, "E2889", {"start": v(-52.41, -35.35) * mm, "end": v(-52.24, -35.23) * mm});
            skLineSegment(sketch, "E2890", {"start": v(-52.24, -35.23) * mm, "end": v(-52.07, -35.11) * mm});
            skLineSegment(sketch, "E2891", {"start": v(-52.07, -35.11) * mm, "end": v(-51.9, -35) * mm});
            skLineSegment(sketch, "E2892", {"start": v(-51.9, -35) * mm, "end": v(-51.73, -34.88) * mm});
            skLineSegment(sketch, "E2893", {"start": v(-51.73, -34.88) * mm, "end": v(-51.56, -34.76) * mm});
            skLineSegment(sketch, "E2894", {"start": v(-51.56, -34.76) * mm, "end": v(-51.38, -34.64) * mm});
            skLineSegment(sketch, "E2895", {"start": v(-51.38, -34.64) * mm, "end": v(-51.21, -34.52) * mm});
            skLineSegment(sketch, "E2896", {"start": v(-51.21, -34.52) * mm, "end": v(-51.04, -34.4) * mm});
            skLineSegment(sketch, "E2897", {"start": v(-51.04, -34.4) * mm, "end": v(-50.87, -34.29) * mm});
            skLineSegment(sketch, "E2898", {"start": v(-50.87, -34.29) * mm, "end": v(-50.7, -34.17) * mm});
            skLineSegment(sketch, "E2899", {"start": v(-50.7, -34.17) * mm, "end": v(-50.58, -34.08) * mm});
            skLineSegment(sketch, "E2900", {"start": v(-50.58, -34.08) * mm, "end": v(-50.46, -34.25) * mm});
            skLineSegment(sketch, "E2901", {"start": v(-50.46, -34.25) * mm, "end": v(-50.34, -34.42) * mm});
            skLineSegment(sketch, "E2902", {"start": v(-50.34, -34.42) * mm, "end": v(-50.22, -34.59) * mm});
            skLineSegment(sketch, "E2903", {"start": v(-50.22, -34.59) * mm, "end": v(-50.1, -34.75) * mm});
            skLineSegment(sketch, "E2904", {"start": v(-50.1, -34.75) * mm, "end": v(-49.98, -34.92) * mm});
            skLineSegment(sketch, "E2905", {"start": v(-49.98, -34.92) * mm, "end": v(-49.86, -35.09) * mm});
            skLineSegment(sketch, "E2906", {"start": v(-49.86, -35.09) * mm, "end": v(-49.74, -35.26) * mm});
            skLineSegment(sketch, "E2907", {"start": v(-49.74, -35.26) * mm, "end": v(-49.62, -35.42) * mm});
            skLineSegment(sketch, "E2908", {"start": v(-49.62, -35.42) * mm, "end": v(-49.5, -35.6) * mm});
            skLineSegment(sketch, "E2909", {"start": v(-49.5, -35.6) * mm, "end": v(-49.38, -35.76) * mm});
            skLineSegment(sketch, "E2910", {"start": v(-49.38, -35.76) * mm, "end": v(-49.26, -35.93) * mm});
            skLineSegment(sketch, "E2911", {"start": v(-49.26, -35.93) * mm, "end": v(-49.2, -36.01) * mm});
            skLineSegment(sketch, "E2912", {"start": v(-49.2, -36.01) * mm, "end": v(-49.36, -36.14) * mm});
            skLineSegment(sketch, "E2913", {"start": v(-49.36, -36.14) * mm, "end": v(-49.53, -36.26) * mm});
            skLineSegment(sketch, "E2914", {"start": v(-49.53, -36.26) * mm, "end": v(-49.7, -36.38) * mm});
            skLineSegment(sketch, "E2915", {"start": v(-49.7, -36.38) * mm, "end": v(-49.86, -36.5) * mm});
            skLineSegment(sketch, "E2916", {"start": v(-49.86, -36.5) * mm, "end": v(-50.03, -36.63) * mm});
            skLineSegment(sketch, "E2917", {"start": v(-50.03, -36.63) * mm, "end": v(-50.2, -36.76) * mm});
            skLineSegment(sketch, "E2918", {"start": v(-50.2, -36.76) * mm, "end": v(-50.36, -36.88) * mm});
            skLineSegment(sketch, "E2919", {"start": v(-50.36, -36.88) * mm, "end": v(-50.52, -37) * mm});
            skLineSegment(sketch, "E2920", {"start": v(-50.52, -37) * mm, "end": v(-50.7, -37.13) * mm});
            skLineSegment(sketch, "E2921", {"start": v(-50.7, -37.13) * mm, "end": v(-50.86, -37.25) * mm});
            skLineSegment(sketch, "E2922", {"start": v(-50.86, -37.25) * mm, "end": v(-51.02, -37.38) * mm});
            skLineSegment(sketch, "E2923", {"start": v(-51.02, -37.38) * mm, "end": v(-51.2, -37.5) * mm});
            skLineSegment(sketch, "E2924", {"start": v(-51.2, -37.5) * mm, "end": v(-51.37, -37.64) * mm});
            skLineSegment(sketch, "E2925", {"start": v(-51.37, -37.64) * mm, "end": v(-51.51, -37.8) * mm});
            skLineSegment(sketch, "E2926", {"start": v(-51.51, -37.8) * mm, "end": v(-51.61, -37.99) * mm});
            skLineSegment(sketch, "E2927", {"start": v(-51.61, -37.99) * mm, "end": v(-51.66, -38.2) * mm});
            skLineSegment(sketch, "E2928", {"start": v(-51.66, -38.2) * mm, "end": v(-51.65, -38.41) * mm});
            skLineSegment(sketch, "E2929", {"start": v(-51.65, -38.41) * mm, "end": v(-51.58, -38.62) * mm});
            skLineSegment(sketch, "E2930", {"start": v(-51.58, -38.62) * mm, "end": v(-51.46, -38.8) * mm});
            skLineSegment(sketch, "E2931", {"start": v(-51.46, -38.8) * mm, "end": v(-51.3, -38.94) * mm});
            skLineSegment(sketch, "E2932", {"start": v(-51.3, -38.94) * mm, "end": v(-51.11, -39.04) * mm});
            skLineSegment(sketch, "E2933", {"start": v(-51.11, -39.04) * mm, "end": v(-50.9, -39.08) * mm});
            skLineSegment(sketch, "E2934", {"start": v(-50.9, -39.08) * mm, "end": v(-50.69, -39.07) * mm});
            skLineSegment(sketch, "E2935", {"start": v(-50.69, -39.07) * mm, "end": v(-50.49, -39) * mm});
            skLineSegment(sketch, "E2936", {"start": v(-50.49, -39) * mm, "end": v(-50.32, -38.89) * mm});
            skLineSegment(sketch, "E2937", {"start": v(-50.32, -38.89) * mm, "end": v(-50.15, -38.76) * mm});
            skLineSegment(sketch, "E2938", {"start": v(-50.15, -38.76) * mm, "end": v(-50, -38.63) * mm});
            skLineSegment(sketch, "E2939", {"start": v(-50, -38.63) * mm, "end": v(-49.83, -38.5) * mm});
            skLineSegment(sketch, "E2940", {"start": v(-49.83, -38.5) * mm, "end": v(-49.67, -38.38) * mm});
            skLineSegment(sketch, "E2941", {"start": v(-49.67, -38.38) * mm, "end": v(-49.5, -38.25) * mm});
            skLineSegment(sketch, "E2942", {"start": v(-49.5, -38.25) * mm, "end": v(-49.34, -38.12) * mm});
            skLineSegment(sketch, "E2943", {"start": v(-49.34, -38.12) * mm, "end": v(-49.18, -38) * mm});
            skLineSegment(sketch, "E2944", {"start": v(-49.18, -38) * mm, "end": v(-49.01, -37.86) * mm});
            skLineSegment(sketch, "E2945", {"start": v(-49.01, -37.86) * mm, "end": v(-48.85, -37.73) * mm});
            skLineSegment(sketch, "E2946", {"start": v(-48.85, -37.73) * mm, "end": v(-48.69, -37.6) * mm});
            skLineSegment(sketch, "E2947", {"start": v(-48.69, -37.6) * mm, "end": v(-48.52, -37.48) * mm});
            skLineSegment(sketch, "E2948", {"start": v(-48.52, -37.48) * mm, "end": v(-48.36, -37.35) * mm});
            skLineSegment(sketch, "E2949", {"start": v(-48.36, -37.35) * mm, "end": v(-48.24, -37.26) * mm});
            skLineSegment(sketch, "E2950", {"start": v(-48.24, -37.26) * mm, "end": v(-48.11, -37.41) * mm});
            skLineSegment(sketch, "E2951", {"start": v(-48.11, -37.41) * mm, "end": v(-47.98, -37.57) * mm});
            skLineSegment(sketch, "E2952", {"start": v(-47.98, -37.57) * mm, "end": v(-47.85, -37.73) * mm});
            skLineSegment(sketch, "E2953", {"start": v(-47.85, -37.73) * mm, "end": v(-47.72, -37.9) * mm});
            skLineSegment(sketch, "E2954", {"start": v(-47.72, -37.9) * mm, "end": v(-47.59, -38.05) * mm});
            skLineSegment(sketch, "E2955", {"start": v(-47.59, -38.05) * mm, "end": v(-47.46, -38.21) * mm});
            skLineSegment(sketch, "E2956", {"start": v(-47.46, -38.21) * mm, "end": v(-47.33, -38.37) * mm});
            skLineSegment(sketch, "E2957", {"start": v(-47.33, -38.37) * mm, "end": v(-47.2, -38.53) * mm});
            skLineSegment(sketch, "E2958", {"start": v(-47.2, -38.53) * mm, "end": v(-47.07, -38.69) * mm});
            skLineSegment(sketch, "E2959", {"start": v(-47.07, -38.69) * mm, "end": v(-46.93, -38.85) * mm});
            skLineSegment(sketch, "E2960", {"start": v(-46.93, -38.85) * mm, "end": v(-46.8, -39) * mm});
            skLineSegment(sketch, "E2961", {"start": v(-46.8, -39) * mm, "end": v(-46.74, -39.09) * mm});
            skLineSegment(sketch, "E2962", {"start": v(-46.74, -39.09) * mm, "end": v(-46.9, -39.22) * mm});
            skLineSegment(sketch, "E2963", {"start": v(-46.9, -39.22) * mm, "end": v(-47.05, -39.36) * mm});
            skLineSegment(sketch, "E2964", {"start": v(-47.05, -39.36) * mm, "end": v(-47.21, -39.5) * mm});
            skLineSegment(sketch, "E2965", {"start": v(-47.21, -39.5) * mm, "end": v(-47.37, -39.63) * mm});
            skLineSegment(sketch, "E2966", {"start": v(-47.37, -39.63) * mm, "end": v(-47.52, -39.76) * mm});
            skLineSegment(sketch, "E2967", {"start": v(-47.52, -39.76) * mm, "end": v(-47.69, -39.9) * mm});
            skLineSegment(sketch, "E2968", {"start": v(-47.69, -39.9) * mm, "end": v(-47.84, -40.03) * mm});
            skLineSegment(sketch, "E2969", {"start": v(-47.84, -40.03) * mm, "end": v(-48, -40.17) * mm});
            skLineSegment(sketch, "E2970", {"start": v(-48, -40.17) * mm, "end": v(-48.16, -40.3) * mm});
            skLineSegment(sketch, "E2971", {"start": v(-48.16, -40.3) * mm, "end": v(-48.32, -40.44) * mm});
            skLineSegment(sketch, "E2972", {"start": v(-48.32, -40.44) * mm, "end": v(-48.47, -40.57) * mm});
            skLineSegment(sketch, "E2973", {"start": v(-48.47, -40.57) * mm, "end": v(-48.63, -40.7) * mm});
            skLineSegment(sketch, "E2974", {"start": v(-48.63, -40.7) * mm, "end": v(-48.8, -40.85) * mm});
            skLineSegment(sketch, "E2975", {"start": v(-48.8, -40.85) * mm, "end": v(-48.93, -41.02) * mm});
            skLineSegment(sketch, "E2976", {"start": v(-48.93, -41.02) * mm, "end": v(-49.02, -41.22) * mm});
            skLineSegment(sketch, "E2977", {"start": v(-49.02, -41.22) * mm, "end": v(-49.05, -41.43) * mm});
            skLineSegment(sketch, "E2978", {"start": v(-49.05, -41.43) * mm, "end": v(-49.03, -41.64) * mm});
            skLineSegment(sketch, "E2979", {"start": v(-49.03, -41.64) * mm, "end": v(-48.95, -41.84) * mm});
            skLineSegment(sketch, "E2980", {"start": v(-48.95, -41.84) * mm, "end": v(-48.82, -42.01) * mm});
            skLineSegment(sketch, "E2981", {"start": v(-48.82, -42.01) * mm, "end": v(-48.65, -42.15) * mm});
            skLineSegment(sketch, "E2982", {"start": v(-48.65, -42.15) * mm, "end": v(-48.45, -42.23) * mm});
            skLineSegment(sketch, "E2983", {"start": v(-48.45, -42.23) * mm, "end": v(-48.24, -42.26) * mm});
            skLineSegment(sketch, "E2984", {"start": v(-48.24, -42.26) * mm, "end": v(-48.03, -42.24) * mm});
            skLineSegment(sketch, "E2985", {"start": v(-48.03, -42.24) * mm, "end": v(-47.83, -42.16) * mm});
            skLineSegment(sketch, "E2986", {"start": v(-47.83, -42.16) * mm, "end": v(-47.67, -42.03) * mm});
            skLineSegment(sketch, "E2987", {"start": v(-47.67, -42.03) * mm, "end": v(-47.51, -41.9) * mm});
            skLineSegment(sketch, "E2988", {"start": v(-47.51, -41.9) * mm, "end": v(-47.36, -41.76) * mm});
            skLineSegment(sketch, "E2989", {"start": v(-47.36, -41.76) * mm, "end": v(-47.2, -41.62) * mm});
            skLineSegment(sketch, "E2990", {"start": v(-47.2, -41.62) * mm, "end": v(-47.05, -41.48) * mm});
            skLineSegment(sketch, "E2991", {"start": v(-47.05, -41.48) * mm, "end": v(-46.9, -41.34) * mm});
            skLineSegment(sketch, "E2992", {"start": v(-46.9, -41.34) * mm, "end": v(-46.74, -41.2) * mm});
            skLineSegment(sketch, "E2993", {"start": v(-46.74, -41.2) * mm, "end": v(-46.59, -41.06) * mm});
            skLineSegment(sketch, "E2994", {"start": v(-46.59, -41.06) * mm, "end": v(-46.43, -40.92) * mm});
            skLineSegment(sketch, "E2995", {"start": v(-46.43, -40.92) * mm, "end": v(-46.28, -40.78) * mm});
            skLineSegment(sketch, "E2996", {"start": v(-46.28, -40.78) * mm, "end": v(-46.13, -40.65) * mm});
            skLineSegment(sketch, "E2997", {"start": v(-46.13, -40.65) * mm, "end": v(-45.97, -40.5) * mm});
            skLineSegment(sketch, "E2998", {"start": v(-45.97, -40.5) * mm, "end": v(-45.82, -40.37) * mm});
            skLineSegment(sketch, "E2999", {"start": v(-45.82, -40.37) * mm, "end": v(-45.7, -40.27) * mm});
            skLineSegment(sketch, "E3000", {"start": v(-45.7, -40.27) * mm, "end": v(-45.56, -40.42) * mm});
            skLineSegment(sketch, "E3001", {"start": v(-45.56, -40.42) * mm, "end": v(-45.42, -40.57) * mm});
            skLineSegment(sketch, "E3002", {"start": v(-45.42, -40.57) * mm, "end": v(-45.28, -40.72) * mm});
            skLineSegment(sketch, "E3003", {"start": v(-45.28, -40.72) * mm, "end": v(-45.14, -40.87) * mm});
            skLineSegment(sketch, "E3004", {"start": v(-45.14, -40.87) * mm, "end": v(-45, -41.02) * mm});
            skLineSegment(sketch, "E3005", {"start": v(-45, -41.02) * mm, "end": v(-44.86, -41.17) * mm});
            skLineSegment(sketch, "E3006", {"start": v(-44.86, -41.17) * mm, "end": v(-44.72, -41.32) * mm});
            skLineSegment(sketch, "E3007", {"start": v(-44.72, -41.32) * mm, "end": v(-44.58, -41.47) * mm});
            skLineSegment(sketch, "E3008", {"start": v(-44.58, -41.47) * mm, "end": v(-44.44, -41.62) * mm});
            skLineSegment(sketch, "E3009", {"start": v(-44.44, -41.62) * mm, "end": v(-44.3, -41.77) * mm});
            skLineSegment(sketch, "E3010", {"start": v(-44.3, -41.77) * mm, "end": v(-44.15, -41.92) * mm});
            skLineSegment(sketch, "E3011", {"start": v(-44.15, -41.92) * mm, "end": v(-44.08, -42) * mm});
            skLineSegment(sketch, "E3012", {"start": v(-44.08, -42) * mm, "end": v(-44.23, -42.14) * mm});
            skLineSegment(sketch, "E3013", {"start": v(-44.23, -42.14) * mm, "end": v(-44.38, -42.28) * mm});
            skLineSegment(sketch, "E3014", {"start": v(-44.38, -42.28) * mm, "end": v(-44.53, -42.43) * mm});
            skLineSegment(sketch, "E3015", {"start": v(-44.53, -42.43) * mm, "end": v(-44.68, -42.58) * mm});
            skLineSegment(sketch, "E3016", {"start": v(-44.68, -42.58) * mm, "end": v(-44.82, -42.72) * mm});
            skLineSegment(sketch, "E3017", {"start": v(-44.82, -42.72) * mm, "end": v(-44.98, -42.87) * mm});
            skLineSegment(sketch, "E3018", {"start": v(-44.98, -42.87) * mm, "end": v(-45.12, -43.01) * mm});
            skLineSegment(sketch, "E3019", {"start": v(-45.12, -43.01) * mm, "end": v(-45.27, -43.16) * mm});
            skLineSegment(sketch, "E3020", {"start": v(-45.27, -43.16) * mm, "end": v(-45.42, -43.3) * mm});
            skLineSegment(sketch, "E3021", {"start": v(-45.42, -43.3) * mm, "end": v(-45.57, -43.45) * mm});
            skLineSegment(sketch, "E3022", {"start": v(-45.57, -43.45) * mm, "end": v(-45.72, -43.6) * mm});
            skLineSegment(sketch, "E3023", {"start": v(-45.72, -43.6) * mm, "end": v(-45.87, -43.74) * mm});
            skLineSegment(sketch, "E3024", {"start": v(-45.87, -43.74) * mm, "end": v(-46.03, -43.9) * mm});
            skLineSegment(sketch, "E3025", {"start": v(-46.03, -43.9) * mm, "end": v(-46.15, -44.07) * mm});
            skLineSegment(sketch, "E3026", {"start": v(-46.15, -44.07) * mm, "end": v(-46.22, -44.27) * mm});
            skLineSegment(sketch, "E3027", {"start": v(-46.22, -44.27) * mm, "end": v(-46.24, -44.49) * mm});
            skLineSegment(sketch, "E3028", {"start": v(-46.24, -44.49) * mm, "end": v(-46.2, -44.7) * mm});
            skLineSegment(sketch, "E3029", {"start": v(-46.2, -44.7) * mm, "end": v(-46.1, -44.9) * mm});
            skLineSegment(sketch, "E3030", {"start": v(-46.1, -44.9) * mm, "end": v(-45.97, -45.05) * mm});
            skLineSegment(sketch, "E3031", {"start": v(-45.97, -45.05) * mm, "end": v(-45.8, -45.17) * mm});
            skLineSegment(sketch, "E3032", {"start": v(-45.8, -45.17) * mm, "end": v(-45.59, -45.25) * mm});
            skLineSegment(sketch, "E3033", {"start": v(-45.59, -45.25) * mm, "end": v(-45.38, -45.26) * mm});
            skLineSegment(sketch, "E3034", {"start": v(-45.38, -45.26) * mm, "end": v(-45.17, -45.22) * mm});
            skLineSegment(sketch, "E3035", {"start": v(-45.17, -45.22) * mm, "end": v(-44.97, -45.13) * mm});
            skLineSegment(sketch, "E3036", {"start": v(-44.97, -45.13) * mm, "end": v(-44.82, -45) * mm});
            skLineSegment(sketch, "E3037", {"start": v(-44.82, -45) * mm, "end": v(-44.67, -44.85) * mm});
            skLineSegment(sketch, "E3038", {"start": v(-44.67, -44.85) * mm, "end": v(-44.53, -44.7) * mm});
            skLineSegment(sketch, "E3039", {"start": v(-44.53, -44.7) * mm, "end": v(-44.38, -44.55) * mm});
            skLineSegment(sketch, "E3040", {"start": v(-44.38, -44.55) * mm, "end": v(-44.24, -44.4) * mm});
            skLineSegment(sketch, "E3041", {"start": v(-44.24, -44.4) * mm, "end": v(-44.1, -44.25) * mm});
            skLineSegment(sketch, "E3042", {"start": v(-44.1, -44.25) * mm, "end": v(-43.95, -44.1) * mm});
            skLineSegment(sketch, "E3043", {"start": v(-43.95, -44.1) * mm, "end": v(-43.8, -43.96) * mm});
            skLineSegment(sketch, "E3044", {"start": v(-43.8, -43.96) * mm, "end": v(-43.66, -43.8) * mm});
            skLineSegment(sketch, "E3045", {"start": v(-43.66, -43.8) * mm, "end": v(-43.51, -43.66) * mm});
            skLineSegment(sketch, "E3046", {"start": v(-43.51, -43.66) * mm, "end": v(-43.37, -43.51) * mm});
            skLineSegment(sketch, "E3047", {"start": v(-43.37, -43.51) * mm, "end": v(-43.22, -43.36) * mm});
            skLineSegment(sketch, "E3048", {"start": v(-43.22, -43.36) * mm, "end": v(-43.08, -43.21) * mm});
            skLineSegment(sketch, "E3049", {"start": v(-43.08, -43.21) * mm, "end": v(-42.97, -43.1) * mm});
            skLineSegment(sketch, "E3050", {"start": v(-42.97, -43.1) * mm, "end": v(-42.82, -43.25) * mm});
            skLineSegment(sketch, "E3051", {"start": v(-42.82, -43.25) * mm, "end": v(-42.67, -43.39) * mm});
            skLineSegment(sketch, "E3052", {"start": v(-42.67, -43.39) * mm, "end": v(-42.52, -43.53) * mm});
            skLineSegment(sketch, "E3053", {"start": v(-42.52, -43.53) * mm, "end": v(-42.37, -43.67) * mm});
            skLineSegment(sketch, "E3054", {"start": v(-42.37, -43.67) * mm, "end": v(-42.22, -43.81) * mm});
            skLineSegment(sketch, "E3055", {"start": v(-42.22, -43.81) * mm, "end": v(-42.07, -43.95) * mm});
            skLineSegment(sketch, "E3056", {"start": v(-42.07, -43.95) * mm, "end": v(-41.92, -44.1) * mm});
            skLineSegment(sketch, "E3057", {"start": v(-41.92, -44.1) * mm, "end": v(-41.77, -44.23) * mm});
            skLineSegment(sketch, "E3058", {"start": v(-41.77, -44.23) * mm, "end": v(-41.62, -44.37) * mm});
            skLineSegment(sketch, "E3059", {"start": v(-41.62, -44.37) * mm, "end": v(-41.47, -44.51) * mm});
            skLineSegment(sketch, "E3060", {"start": v(-41.47, -44.51) * mm, "end": v(-41.32, -44.65) * mm});
            skLineSegment(sketch, "E3061", {"start": v(-41.32, -44.65) * mm, "end": v(-41.24, -44.73) * mm});
            skLineSegment(sketch, "E3062", {"start": v(-41.24, -44.73) * mm, "end": v(-41.38, -44.88) * mm});
            skLineSegment(sketch, "E3063", {"start": v(-41.38, -44.88) * mm, "end": v(-41.52, -45.03) * mm});
            skLineSegment(sketch, "E3064", {"start": v(-41.52, -45.03) * mm, "end": v(-41.66, -45.2) * mm});
            skLineSegment(sketch, "E3065", {"start": v(-41.66, -45.2) * mm, "end": v(-41.8, -45.34) * mm});
            skLineSegment(sketch, "E3066", {"start": v(-41.8, -45.34) * mm, "end": v(-41.94, -45.5) * mm});
            skLineSegment(sketch, "E3067", {"start": v(-41.94, -45.5) * mm, "end": v(-42.08, -45.65) * mm});
            skLineSegment(sketch, "E3068", {"start": v(-42.08, -45.65) * mm, "end": v(-42.22, -45.8) * mm});
            skLineSegment(sketch, "E3069", {"start": v(-42.22, -45.8) * mm, "end": v(-42.35, -45.96) * mm});
            skLineSegment(sketch, "E3070", {"start": v(-42.35, -45.96) * mm, "end": v(-42.5, -46.12) * mm});
            skLineSegment(sketch, "E3071", {"start": v(-42.5, -46.12) * mm, "end": v(-42.63, -46.27) * mm});
            skLineSegment(sketch, "E3072", {"start": v(-42.63, -46.27) * mm, "end": v(-42.77, -46.42) * mm});
            skLineSegment(sketch, "E3073", {"start": v(-42.77, -46.42) * mm, "end": v(-42.91, -46.58) * mm});
            skLineSegment(sketch, "E3074", {"start": v(-42.91, -46.58) * mm, "end": v(-43.06, -46.75) * mm});
            skLineSegment(sketch, "E3075", {"start": v(-43.06, -46.75) * mm, "end": v(-43.17, -46.93) * mm});
            skLineSegment(sketch, "E3076", {"start": v(-43.17, -46.93) * mm, "end": v(-43.23, -47.14) * mm});
            skLineSegment(sketch, "E3077", {"start": v(-43.23, -47.14) * mm, "end": v(-43.23, -47.35) * mm});
            skLineSegment(sketch, "E3078", {"start": v(-43.23, -47.35) * mm, "end": v(-43.18, -47.56) * mm});
            skLineSegment(sketch, "E3079", {"start": v(-43.18, -47.56) * mm, "end": v(-43.08, -47.75) * mm});
            skLineSegment(sketch, "E3080", {"start": v(-43.08, -47.75) * mm, "end": v(-42.93, -47.9) * mm});
            skLineSegment(sketch, "E3081", {"start": v(-42.93, -47.9) * mm, "end": v(-42.74, -48) * mm});
            skLineSegment(sketch, "E3082", {"start": v(-42.74, -48) * mm, "end": v(-42.54, -48.07) * mm});
            skLineSegment(sketch, "E3083", {"start": v(-42.54, -48.07) * mm, "end": v(-42.32, -48.07) * mm});
            skLineSegment(sketch, "E3084", {"start": v(-42.32, -48.07) * mm, "end": v(-42.11, -48.02) * mm});
            skLineSegment(sketch, "E3085", {"start": v(-42.11, -48.02) * mm, "end": v(-41.93, -47.9) * mm});
            skLineSegment(sketch, "E3086", {"start": v(-41.93, -47.9) * mm, "end": v(-41.78, -47.76) * mm});
            skLineSegment(sketch, "E3087", {"start": v(-41.78, -47.76) * mm, "end": v(-41.64, -47.6) * mm});
            skLineSegment(sketch, "E3088", {"start": v(-41.64, -47.6) * mm, "end": v(-41.51, -47.45) * mm});
            skLineSegment(sketch, "E3089", {"start": v(-41.51, -47.45) * mm, "end": v(-41.38, -47.3) * mm});
            skLineSegment(sketch, "E3090", {"start": v(-41.38, -47.3) * mm, "end": v(-41.24, -47.14) * mm});
            skLineSegment(sketch, "E3091", {"start": v(-41.24, -47.14) * mm, "end": v(-41.1, -46.98) * mm});
            skLineSegment(sketch, "E3092", {"start": v(-41.1, -46.98) * mm, "end": v(-40.97, -46.82) * mm});
            skLineSegment(sketch, "E3093", {"start": v(-40.97, -46.82) * mm, "end": v(-40.84, -46.67) * mm});
            skLineSegment(sketch, "E3094", {"start": v(-40.84, -46.67) * mm, "end": v(-40.7, -46.5) * mm});
            skLineSegment(sketch, "E3095", {"start": v(-40.7, -46.5) * mm, "end": v(-40.57, -46.35) * mm});
            skLineSegment(sketch, "E3096", {"start": v(-40.57, -46.35) * mm, "end": v(-40.43, -46.2) * mm});
            skLineSegment(sketch, "E3097", {"start": v(-40.43, -46.2) * mm, "end": v(-40.3, -46.03) * mm});
            skLineSegment(sketch, "E3098", {"start": v(-40.3, -46.03) * mm, "end": v(-40.16, -45.87) * mm});
            skLineSegment(sketch, "E3099", {"start": v(-40.16, -45.87) * mm, "end": v(-40.07, -45.76) * mm});
            skLineSegment(sketch, "E3100", {"start": v(-40.07, -45.76) * mm, "end": v(-39.9, -45.9) * mm});
            skLineSegment(sketch, "E3101", {"start": v(-39.9, -45.9) * mm, "end": v(-39.75, -46.02) * mm});
            skLineSegment(sketch, "E3102", {"start": v(-39.75, -46.02) * mm, "end": v(-39.59, -46.15) * mm});
            skLineSegment(sketch, "E3103", {"start": v(-39.59, -46.15) * mm, "end": v(-39.43, -46.28) * mm});
            skLineSegment(sketch, "E3104", {"start": v(-39.43, -46.28) * mm, "end": v(-39.27, -46.41) * mm});
            skLineSegment(sketch, "E3105", {"start": v(-39.27, -46.41) * mm, "end": v(-39.1, -46.54) * mm});
            skLineSegment(sketch, "E3106", {"start": v(-39.1, -46.54) * mm, "end": v(-38.95, -46.68) * mm});
            skLineSegment(sketch, "E3107", {"start": v(-38.95, -46.68) * mm, "end": v(-38.8, -46.8) * mm});
            skLineSegment(sketch, "E3108", {"start": v(-38.8, -46.8) * mm, "end": v(-38.63, -46.94) * mm});
            skLineSegment(sketch, "E3109", {"start": v(-38.63, -46.94) * mm, "end": v(-38.47, -47.07) * mm});
            skLineSegment(sketch, "E3110", {"start": v(-38.47, -47.07) * mm, "end": v(-38.31, -47.2) * mm});
            skLineSegment(sketch, "E3111", {"start": v(-38.31, -47.2) * mm, "end": v(-38.23, -47.26) * mm});
            skLineSegment(sketch, "E3112", {"start": v(-38.23, -47.26) * mm, "end": v(-38.36, -47.43) * mm});
            skLineSegment(sketch, "E3113", {"start": v(-38.36, -47.43) * mm, "end": v(-38.49, -47.59) * mm});
            skLineSegment(sketch, "E3114", {"start": v(-38.49, -47.59) * mm, "end": v(-38.62, -47.75) * mm});
            skLineSegment(sketch, "E3115", {"start": v(-38.62, -47.75) * mm, "end": v(-38.75, -47.92) * mm});
            skLineSegment(sketch, "E3116", {"start": v(-38.75, -47.92) * mm, "end": v(-38.87, -48.08) * mm});
            skLineSegment(sketch, "E3117", {"start": v(-38.87, -48.08) * mm, "end": v(-39, -48.24) * mm});
            skLineSegment(sketch, "E3118", {"start": v(-39, -48.24) * mm, "end": v(-39.13, -48.4) * mm});
            skLineSegment(sketch, "E3119", {"start": v(-39.13, -48.4) * mm, "end": v(-39.26, -48.57) * mm});
            skLineSegment(sketch, "E3120", {"start": v(-39.26, -48.57) * mm, "end": v(-39.4, -48.73) * mm});
            skLineSegment(sketch, "E3121", {"start": v(-39.4, -48.73) * mm, "end": v(-39.52, -48.9) * mm});
            skLineSegment(sketch, "E3122", {"start": v(-39.52, -48.9) * mm, "end": v(-39.65, -49.06) * mm});
            skLineSegment(sketch, "E3123", {"start": v(-39.65, -49.06) * mm, "end": v(-39.78, -49.22) * mm});
            skLineSegment(sketch, "E3124", {"start": v(-39.78, -49.22) * mm, "end": v(-39.91, -49.4) * mm});
            skLineSegment(sketch, "E3125", {"start": v(-39.91, -49.4) * mm, "end": v(-40.01, -49.59) * mm});
            skLineSegment(sketch, "E3126", {"start": v(-40.01, -49.59) * mm, "end": v(-40.06, -49.8) * mm});
            skLineSegment(sketch, "E3127", {"start": v(-40.06, -49.8) * mm, "end": v(-40.05, -50.01) * mm});
            skLineSegment(sketch, "E3128", {"start": v(-40.05, -50.01) * mm, "end": v(-39.98, -50.22) * mm});
            skLineSegment(sketch, "E3129", {"start": v(-39.98, -50.22) * mm, "end": v(-39.86, -50.4) * mm});
            skLineSegment(sketch, "E3130", {"start": v(-39.86, -50.4) * mm, "end": v(-39.7, -50.54) * mm});
            skLineSegment(sketch, "E3131", {"start": v(-39.7, -50.54) * mm, "end": v(-39.51, -50.64) * mm});
            skLineSegment(sketch, "E3132", {"start": v(-39.51, -50.64) * mm, "end": v(-39.3, -50.68) * mm});
            skLineSegment(sketch, "E3133", {"start": v(-39.3, -50.68) * mm, "end": v(-39.09, -50.67) * mm});
            skLineSegment(sketch, "E3134", {"start": v(-39.09, -50.67) * mm, "end": v(-38.88, -50.6) * mm});
            skLineSegment(sketch, "E3135", {"start": v(-38.88, -50.6) * mm, "end": v(-38.7, -50.49) * mm});
            skLineSegment(sketch, "E3136", {"start": v(-38.7, -50.49) * mm, "end": v(-38.57, -50.33) * mm});
            skLineSegment(sketch, "E3137", {"start": v(-38.57, -50.33) * mm, "end": v(-38.44, -50.17) * mm});
            skLineSegment(sketch, "E3138", {"start": v(-38.44, -50.17) * mm, "end": v(-38.32, -50) * mm});
            skLineSegment(sketch, "E3139", {"start": v(-38.32, -50) * mm, "end": v(-38.2, -49.84) * mm});
            skLineSegment(sketch, "E3140", {"start": v(-38.2, -49.84) * mm, "end": v(-38.07, -49.67) * mm});
            skLineSegment(sketch, "E3141", {"start": v(-38.07, -49.67) * mm, "end": v(-37.95, -49.5) * mm});
            skLineSegment(sketch, "E3142", {"start": v(-37.95, -49.5) * mm, "end": v(-37.82, -49.34) * mm});
            skLineSegment(sketch, "E3143", {"start": v(-37.82, -49.34) * mm, "end": v(-37.7, -49.17) * mm});
            skLineSegment(sketch, "E3144", {"start": v(-37.7, -49.17) * mm, "end": v(-37.57, -49) * mm});
            skLineSegment(sketch, "E3145", {"start": v(-37.57, -49) * mm, "end": v(-37.45, -48.84) * mm});
            skLineSegment(sketch, "E3146", {"start": v(-37.45, -48.84) * mm, "end": v(-37.33, -48.67) * mm});
            skLineSegment(sketch, "E3147", {"start": v(-37.33, -48.67) * mm, "end": v(-37.2, -48.5) * mm});
            skLineSegment(sketch, "E3148", {"start": v(-37.2, -48.5) * mm, "end": v(-37.08, -48.34) * mm});
            skLineSegment(sketch, "E3149", {"start": v(-37.08, -48.34) * mm, "end": v(-36.99, -48.22) * mm});
            skLineSegment(sketch, "E3150", {"start": v(-36.99, -48.22) * mm, "end": v(-36.82, -48.34) * mm});
            skLineSegment(sketch, "E3151", {"start": v(-36.82, -48.34) * mm, "end": v(-36.65, -48.46) * mm});
            skLineSegment(sketch, "E3152", {"start": v(-36.65, -48.46) * mm, "end": v(-36.49, -48.58) * mm});
            skLineSegment(sketch, "E3153", {"start": v(-36.49, -48.58) * mm, "end": v(-36.32, -48.7) * mm});
            skLineSegment(sketch, "E3154", {"start": v(-36.32, -48.7) * mm, "end": v(-36.15, -48.82) * mm});
            skLineSegment(sketch, "E3155", {"start": v(-36.15, -48.82) * mm, "end": v(-35.98, -48.94) * mm});
            skLineSegment(sketch, "E3156", {"start": v(-35.98, -48.94) * mm, "end": v(-35.82, -49.06) * mm});
            skLineSegment(sketch, "E3157", {"start": v(-35.82, -49.06) * mm, "end": v(-35.65, -49.18) * mm});
            skLineSegment(sketch, "E3158", {"start": v(-35.65, -49.18) * mm, "end": v(-35.48, -49.3) * mm});
            skLineSegment(sketch, "E3159", {"start": v(-35.48, -49.3) * mm, "end": v(-35.31, -49.42) * mm});
            skLineSegment(sketch, "E3160", {"start": v(-35.31, -49.42) * mm, "end": v(-35.15, -49.54) * mm});
            skLineSegment(sketch, "E3161", {"start": v(-35.15, -49.54) * mm, "end": v(-35.06, -49.6) * mm});
            skLineSegment(sketch, "E3162", {"start": v(-35.06, -49.6) * mm, "end": v(-35.18, -49.77) * mm});
            skLineSegment(sketch, "E3163", {"start": v(-35.18, -49.77) * mm, "end": v(-35.3, -49.94) * mm});
            skLineSegment(sketch, "E3164", {"start": v(-35.3, -49.94) * mm, "end": v(-35.41, -50.11) * mm});
            skLineSegment(sketch, "E3165", {"start": v(-35.41, -50.11) * mm, "end": v(-35.53, -50.28) * mm});
            skLineSegment(sketch, "E3166", {"start": v(-35.53, -50.28) * mm, "end": v(-35.65, -50.45) * mm});
            skLineSegment(sketch, "E3167", {"start": v(-35.65, -50.45) * mm, "end": v(-35.77, -50.63) * mm});
            skLineSegment(sketch, "E3168", {"start": v(-35.77, -50.63) * mm, "end": v(-35.88, -50.8) * mm});
            skLineSegment(sketch, "E3169", {"start": v(-35.88, -50.8) * mm, "end": v(-36, -50.97) * mm});
            skLineSegment(sketch, "E3170", {"start": v(-36, -50.97) * mm, "end": v(-36.12, -51.14) * mm});
            skLineSegment(sketch, "E3171", {"start": v(-36.12, -51.14) * mm, "end": v(-36.24, -51.31) * mm});
            skLineSegment(sketch, "E3172", {"start": v(-36.24, -51.31) * mm, "end": v(-36.35, -51.48) * mm});
            skLineSegment(sketch, "E3173", {"start": v(-36.35, -51.48) * mm, "end": v(-36.47, -51.66) * mm});
            skLineSegment(sketch, "E3174", {"start": v(-36.47, -51.66) * mm, "end": v(-36.6, -51.84) * mm});
            skLineSegment(sketch, "E3175", {"start": v(-36.6, -51.84) * mm, "end": v(-36.68, -52.04) * mm});
            skLineSegment(sketch, "E3176", {"start": v(-36.68, -52.04) * mm, "end": v(-36.72, -52.25) * mm});
            skLineSegment(sketch, "E3177", {"start": v(-36.72, -52.25) * mm, "end": v(-36.7, -52.46) * mm});
            skLineSegment(sketch, "E3178", {"start": v(-36.7, -52.46) * mm, "end": v(-36.61, -52.66) * mm});
            skLineSegment(sketch, "E3179", {"start": v(-36.61, -52.66) * mm, "end": v(-36.48, -52.83) * mm});
            skLineSegment(sketch, "E3180", {"start": v(-36.48, -52.83) * mm, "end": v(-36.32, -52.97) * mm});
            skLineSegment(sketch, "E3181", {"start": v(-36.32, -52.97) * mm, "end": v(-36.12, -53.05) * mm});
            skLineSegment(sketch, "E3182", {"start": v(-36.12, -53.05) * mm, "end": v(-35.9, -53.08) * mm});
            skLineSegment(sketch, "E3183", {"start": v(-35.9, -53.08) * mm, "end": v(-35.7, -53.05) * mm});
            skLineSegment(sketch, "E3184", {"start": v(-35.7, -53.05) * mm, "end": v(-35.5, -52.97) * mm});
            skLineSegment(sketch, "E3185", {"start": v(-35.5, -52.97) * mm, "end": v(-35.32, -52.84) * mm});
            skLineSegment(sketch, "E3186", {"start": v(-35.32, -52.84) * mm, "end": v(-35.2, -52.68) * mm});
            skLineSegment(sketch, "E3187", {"start": v(-35.2, -52.68) * mm, "end": v(-35.08, -52.51) * mm});
            skLineSegment(sketch, "E3188", {"start": v(-35.08, -52.51) * mm, "end": v(-34.97, -52.34) * mm});
            skLineSegment(sketch, "E3189", {"start": v(-34.97, -52.34) * mm, "end": v(-34.86, -52.17) * mm});
            skLineSegment(sketch, "E3190", {"start": v(-34.86, -52.17) * mm, "end": v(-34.75, -52) * mm});
            skLineSegment(sketch, "E3191", {"start": v(-34.75, -52) * mm, "end": v(-34.63, -51.82) * mm});
            skLineSegment(sketch, "E3192", {"start": v(-34.63, -51.82) * mm, "end": v(-34.52, -51.64) * mm});
            skLineSegment(sketch, "E3193", {"start": v(-34.52, -51.64) * mm, "end": v(-34.4, -51.47) * mm});
            skLineSegment(sketch, "E3194", {"start": v(-34.4, -51.47) * mm, "end": v(-34.3, -51.3) * mm});
            skLineSegment(sketch, "E3195", {"start": v(-34.3, -51.3) * mm, "end": v(-34.18, -51.12) * mm});
            skLineSegment(sketch, "E3196", {"start": v(-34.18, -51.12) * mm, "end": v(-34.07, -50.95) * mm});
            skLineSegment(sketch, "E3197", {"start": v(-34.07, -50.95) * mm, "end": v(-33.95, -50.77) * mm});
            skLineSegment(sketch, "E3198", {"start": v(-33.95, -50.77) * mm, "end": v(-33.84, -50.6) * mm});
            skLineSegment(sketch, "E3199", {"start": v(-33.84, -50.6) * mm, "end": v(-33.76, -50.47) * mm});
            skLineSegment(sketch, "E3200", {"start": v(-33.76, -50.47) * mm, "end": v(-33.58, -50.58) * mm});
            skLineSegment(sketch, "E3201", {"start": v(-33.58, -50.58) * mm, "end": v(-33.4, -50.69) * mm});
            skLineSegment(sketch, "E3202", {"start": v(-33.4, -50.69) * mm, "end": v(-33.23, -50.8) * mm});
            skLineSegment(sketch, "E3203", {"start": v(-33.23, -50.8) * mm, "end": v(-33.06, -50.9) * mm});
            skLineSegment(sketch, "E3204", {"start": v(-33.06, -50.9) * mm, "end": v(-32.88, -51.01) * mm});
            skLineSegment(sketch, "E3205", {"start": v(-32.88, -51.01) * mm, "end": v(-32.7, -51.12) * mm});
            skLineSegment(sketch, "E3206", {"start": v(-32.7, -51.12) * mm, "end": v(-32.53, -51.23) * mm});
            skLineSegment(sketch, "E3207", {"start": v(-32.53, -51.23) * mm, "end": v(-32.36, -51.34) * mm});
            skLineSegment(sketch, "E3208", {"start": v(-32.36, -51.34) * mm, "end": v(-32.18, -51.45) * mm});
            skLineSegment(sketch, "E3209", {"start": v(-32.18, -51.45) * mm, "end": v(-32, -51.56) * mm});
            skLineSegment(sketch, "E3210", {"start": v(-32, -51.56) * mm, "end": v(-31.83, -51.67) * mm});
            skLineSegment(sketch, "E3211", {"start": v(-31.83, -51.67) * mm, "end": v(-31.74, -51.72) * mm});
            skLineSegment(sketch, "E3212", {"start": v(-31.74, -51.72) * mm, "end": v(-31.85, -51.9) * mm});
            skLineSegment(sketch, "E3213", {"start": v(-31.85, -51.9) * mm, "end": v(-31.96, -52.08) * mm});
            skLineSegment(sketch, "E3214", {"start": v(-31.96, -52.08) * mm, "end": v(-32.06, -52.26) * mm});
            skLineSegment(sketch, "E3215", {"start": v(-32.06, -52.26) * mm, "end": v(-32.17, -52.44) * mm});
            skLineSegment(sketch, "E3216", {"start": v(-32.17, -52.44) * mm, "end": v(-32.27, -52.61) * mm});
            skLineSegment(sketch, "E3217", {"start": v(-32.27, -52.61) * mm, "end": v(-32.38, -52.8) * mm});
            skLineSegment(sketch, "E3218", {"start": v(-32.38, -52.8) * mm, "end": v(-32.49, -52.97) * mm});
            skLineSegment(sketch, "E3219", {"start": v(-32.49, -52.97) * mm, "end": v(-32.6, -53.15) * mm});
            skLineSegment(sketch, "E3220", {"start": v(-32.6, -53.15) * mm, "end": v(-32.7, -53.33) * mm});
            skLineSegment(sketch, "E3221", {"start": v(-32.7, -53.33) * mm, "end": v(-32.8, -53.5) * mm});
            skLineSegment(sketch, "E3222", {"start": v(-32.8, -53.5) * mm, "end": v(-32.91, -53.68) * mm});
            skLineSegment(sketch, "E3223", {"start": v(-32.91, -53.68) * mm, "end": v(-33.02, -53.87) * mm});
            skLineSegment(sketch, "E3224", {"start": v(-33.02, -53.87) * mm, "end": v(-33.13, -54.06) * mm});
            skLineSegment(sketch, "E3225", {"start": v(-33.13, -54.06) * mm, "end": v(-33.2, -54.26) * mm});
            skLineSegment(sketch, "E3226", {"start": v(-33.2, -54.26) * mm, "end": v(-33.22, -54.47) * mm});
            skLineSegment(sketch, "E3227", {"start": v(-33.22, -54.47) * mm, "end": v(-33.18, -54.68) * mm});
            skLineSegment(sketch, "E3228", {"start": v(-33.18, -54.68) * mm, "end": v(-33.1, -54.88) * mm});
            skLineSegment(sketch, "E3229", {"start": v(-33.1, -54.88) * mm, "end": v(-32.95, -55.04) * mm});
            skLineSegment(sketch, "E3230", {"start": v(-32.95, -55.04) * mm, "end": v(-32.78, -55.16) * mm});
            skLineSegment(sketch, "E3231", {"start": v(-32.78, -55.16) * mm, "end": v(-32.57, -55.23) * mm});
            skLineSegment(sketch, "E3232", {"start": v(-32.57, -55.23) * mm, "end": v(-32.36, -55.25) * mm});
            skLineSegment(sketch, "E3233", {"start": v(-32.36, -55.25) * mm, "end": v(-32.15, -55.21) * mm});
            skLineSegment(sketch, "E3234", {"start": v(-32.15, -55.21) * mm, "end": v(-31.96, -55.12) * mm});
            skLineSegment(sketch, "E3235", {"start": v(-31.96, -55.12) * mm, "end": v(-31.8, -54.98) * mm});
            skLineSegment(sketch, "E3236", {"start": v(-31.8, -54.98) * mm, "end": v(-31.68, -54.8) * mm});
            skLineSegment(sketch, "E3237", {"start": v(-31.68, -54.8) * mm, "end": v(-31.58, -54.63) * mm});
            skLineSegment(sketch, "E3238", {"start": v(-31.58, -54.63) * mm, "end": v(-31.47, -54.45) * mm});
            skLineSegment(sketch, "E3239", {"start": v(-31.47, -54.45) * mm, "end": v(-31.37, -54.27) * mm});
            skLineSegment(sketch, "E3240", {"start": v(-31.37, -54.27) * mm, "end": v(-31.27, -54.1) * mm});
            skLineSegment(sketch, "E3241", {"start": v(-31.27, -54.1) * mm, "end": v(-31.17, -53.9) * mm});
            skLineSegment(sketch, "E3242", {"start": v(-31.17, -53.9) * mm, "end": v(-31.07, -53.73) * mm});
            skLineSegment(sketch, "E3243", {"start": v(-31.07, -53.73) * mm, "end": v(-30.97, -53.55) * mm});
            skLineSegment(sketch, "E3244", {"start": v(-30.97, -53.55) * mm, "end": v(-30.87, -53.36) * mm});
            skLineSegment(sketch, "E3245", {"start": v(-30.87, -53.36) * mm, "end": v(-30.76, -53.18) * mm});
            skLineSegment(sketch, "E3246", {"start": v(-30.76, -53.18) * mm, "end": v(-30.66, -53) * mm});
            skLineSegment(sketch, "E3247", {"start": v(-30.66, -53) * mm, "end": v(-30.56, -52.82) * mm});
            skLineSegment(sketch, "E3248", {"start": v(-30.56, -52.82) * mm, "end": v(-30.46, -52.64) * mm});
            skLineSegment(sketch, "E3249", {"start": v(-30.46, -52.64) * mm, "end": v(-30.39, -52.5) * mm});
            skLineSegment(sketch, "E3250", {"start": v(-30.39, -52.5) * mm, "end": v(-30.2, -52.6) * mm});
            skLineSegment(sketch, "E3251", {"start": v(-30.2, -52.6) * mm, "end": v(-30.02, -52.7) * mm});
            skLineSegment(sketch, "E3252", {"start": v(-30.02, -52.7) * mm, "end": v(-29.84, -52.8) * mm});
            skLineSegment(sketch, "E3253", {"start": v(-29.84, -52.8) * mm, "end": v(-29.66, -52.9) * mm});
            skLineSegment(sketch, "E3254", {"start": v(-29.66, -52.9) * mm, "end": v(-29.48, -53) * mm});
            skLineSegment(sketch, "E3255", {"start": v(-29.48, -53) * mm, "end": v(-29.3, -53.09) * mm});
            skLineSegment(sketch, "E3256", {"start": v(-29.3, -53.09) * mm, "end": v(-29.12, -53.19) * mm});
            skLineSegment(sketch, "E3257", {"start": v(-29.12, -53.19) * mm, "end": v(-28.93, -53.28) * mm});
            skLineSegment(sketch, "E3258", {"start": v(-28.93, -53.28) * mm, "end": v(-28.75, -53.38) * mm});
            skLineSegment(sketch, "E3259", {"start": v(-28.75, -53.38) * mm, "end": v(-28.57, -53.48) * mm});
            skLineSegment(sketch, "E3260", {"start": v(-28.57, -53.48) * mm, "end": v(-28.39, -53.57) * mm});
            skLineSegment(sketch, "E3261", {"start": v(-28.39, -53.57) * mm, "end": v(-28.3, -53.62) * mm});
            skLineSegment(sketch, "E3262", {"start": v(-28.3, -53.62) * mm, "end": v(-28.39, -53.8) * mm});
            skLineSegment(sketch, "E3263", {"start": v(-28.39, -53.8) * mm, "end": v(-28.48, -54) * mm});
            skLineSegment(sketch, "E3264", {"start": v(-28.48, -54) * mm, "end": v(-28.58, -54.18) * mm});
            skLineSegment(sketch, "E3265", {"start": v(-28.58, -54.18) * mm, "end": v(-28.67, -54.36) * mm});
            skLineSegment(sketch, "E3266", {"start": v(-28.67, -54.36) * mm, "end": v(-28.77, -54.55) * mm});
            skLineSegment(sketch, "E3267", {"start": v(-28.77, -54.55) * mm, "end": v(-28.86, -54.74) * mm});
            skLineSegment(sketch, "E3268", {"start": v(-28.86, -54.74) * mm, "end": v(-28.96, -54.92) * mm});
            skLineSegment(sketch, "E3269", {"start": v(-28.96, -54.92) * mm, "end": v(-29.05, -55.1) * mm});
            skLineSegment(sketch, "E3270", {"start": v(-29.05, -55.1) * mm, "end": v(-29.14, -55.3) * mm});
            skLineSegment(sketch, "E3271", {"start": v(-29.14, -55.3) * mm, "end": v(-29.24, -55.47) * mm});
            skLineSegment(sketch, "E3272", {"start": v(-29.24, -55.47) * mm, "end": v(-29.33, -55.66) * mm});
            skLineSegment(sketch, "E3273", {"start": v(-29.33, -55.66) * mm, "end": v(-29.43, -55.85) * mm});
            skLineSegment(sketch, "E3274", {"start": v(-29.43, -55.85) * mm, "end": v(-29.53, -56.04) * mm});
            skLineSegment(sketch, "E3275", {"start": v(-29.53, -56.04) * mm, "end": v(-29.59, -56.25) * mm});
            skLineSegment(sketch, "E3276", {"start": v(-29.59, -56.25) * mm, "end": v(-29.6, -56.47) * mm});
            skLineSegment(sketch, "E3277", {"start": v(-29.6, -56.47) * mm, "end": v(-29.54, -56.67) * mm});
            skLineSegment(sketch, "E3278", {"start": v(-29.54, -56.67) * mm, "end": v(-29.43, -56.86) * mm});
            skLineSegment(sketch, "E3279", {"start": v(-29.43, -56.86) * mm, "end": v(-29.28, -57.01) * mm});
            skLineSegment(sketch, "E3280", {"start": v(-29.28, -57.01) * mm, "end": v(-29.1, -57.12) * mm});
            skLineSegment(sketch, "E3281", {"start": v(-29.1, -57.12) * mm, "end": v(-28.9, -57.18) * mm});
            skLineSegment(sketch, "E3282", {"start": v(-28.9, -57.18) * mm, "end": v(-28.68, -57.19) * mm});
            skLineSegment(sketch, "E3283", {"start": v(-28.68, -57.19) * mm, "end": v(-28.47, -57.13) * mm});
            skLineSegment(sketch, "E3284", {"start": v(-28.47, -57.13) * mm, "end": v(-28.28, -57.03) * mm});
            skLineSegment(sketch, "E3285", {"start": v(-28.28, -57.03) * mm, "end": v(-28.13, -56.88) * mm});
            skLineSegment(sketch, "E3286", {"start": v(-28.13, -56.88) * mm, "end": v(-28.03, -56.7) * mm});
            skLineSegment(sketch, "E3287", {"start": v(-28.03, -56.7) * mm, "end": v(-27.94, -56.51) * mm});
            skLineSegment(sketch, "E3288", {"start": v(-27.94, -56.51) * mm, "end": v(-27.85, -56.33) * mm});
            skLineSegment(sketch, "E3289", {"start": v(-27.85, -56.33) * mm, "end": v(-27.76, -56.14) * mm});
            skLineSegment(sketch, "E3290", {"start": v(-27.76, -56.14) * mm, "end": v(-27.67, -55.96) * mm});
            skLineSegment(sketch, "E3291", {"start": v(-27.67, -55.96) * mm, "end": v(-27.58, -55.77) * mm});
            skLineSegment(sketch, "E3292", {"start": v(-27.58, -55.77) * mm, "end": v(-27.5, -55.58) * mm});
            skLineSegment(sketch, "E3293", {"start": v(-27.5, -55.58) * mm, "end": v(-27.4, -55.4) * mm});
            skLineSegment(sketch, "E3294", {"start": v(-27.4, -55.4) * mm, "end": v(-27.31, -55.2) * mm});
            skLineSegment(sketch, "E3295", {"start": v(-27.31, -55.2) * mm, "end": v(-27.22, -55.02) * mm});
            skLineSegment(sketch, "E3296", {"start": v(-27.22, -55.02) * mm, "end": v(-27.13, -54.83) * mm});
            skLineSegment(sketch, "E3297", {"start": v(-27.13, -54.83) * mm, "end": v(-27.04, -54.64) * mm});
            skLineSegment(sketch, "E3298", {"start": v(-27.04, -54.64) * mm, "end": v(-26.95, -54.45) * mm});
            skLineSegment(sketch, "E3299", {"start": v(-26.95, -54.45) * mm, "end": v(-26.89, -54.32) * mm});
            skLineSegment(sketch, "E3300", {"start": v(-26.89, -54.32) * mm, "end": v(-26.7, -54.4) * mm});
            skLineSegment(sketch, "E3301", {"start": v(-26.7, -54.4) * mm, "end": v(-26.51, -54.49) * mm});
            skLineSegment(sketch, "E3302", {"start": v(-26.51, -54.49) * mm, "end": v(-26.33, -54.57) * mm});
            skLineSegment(sketch, "E3303", {"start": v(-26.33, -54.57) * mm, "end": v(-26.14, -54.66) * mm});
            skLineSegment(sketch, "E3304", {"start": v(-26.14, -54.66) * mm, "end": v(-25.95, -54.74) * mm});
            skLineSegment(sketch, "E3305", {"start": v(-25.95, -54.74) * mm, "end": v(-25.76, -54.83) * mm});
            skLineSegment(sketch, "E3306", {"start": v(-25.76, -54.83) * mm, "end": v(-25.58, -54.91) * mm});
            skLineSegment(sketch, "E3307", {"start": v(-25.58, -54.91) * mm, "end": v(-25.39, -55) * mm});
            skLineSegment(sketch, "E3308", {"start": v(-25.39, -55) * mm, "end": v(-25.2, -55.08) * mm});
            skLineSegment(sketch, "E3309", {"start": v(-25.2, -55.08) * mm, "end": v(-25.01, -55.17) * mm});
            skLineSegment(sketch, "E3310", {"start": v(-25.01, -55.17) * mm, "end": v(-24.83, -55.25) * mm});
            skLineSegment(sketch, "E3311", {"start": v(-24.83, -55.25) * mm, "end": v(-24.73, -55.3) * mm});
            skLineSegment(sketch, "E3312", {"start": v(-24.73, -55.3) * mm, "end": v(-24.81, -55.49) * mm});
            skLineSegment(sketch, "E3313", {"start": v(-24.81, -55.49) * mm, "end": v(-24.9, -55.67) * mm});
            skLineSegment(sketch, "E3314", {"start": v(-24.9, -55.67) * mm, "end": v(-24.98, -55.87) * mm});
            skLineSegment(sketch, "E3315", {"start": v(-24.98, -55.87) * mm, "end": v(-25.06, -56.06) * mm});
            skLineSegment(sketch, "E3316", {"start": v(-25.06, -56.06) * mm, "end": v(-25.14, -56.25) * mm});
            skLineSegment(sketch, "E3317", {"start": v(-25.14, -56.25) * mm, "end": v(-25.22, -56.44) * mm});
            skLineSegment(sketch, "E3318", {"start": v(-25.22, -56.44) * mm, "end": v(-25.3, -56.63) * mm});
            skLineSegment(sketch, "E3319", {"start": v(-25.3, -56.63) * mm, "end": v(-25.38, -56.82) * mm});
            skLineSegment(sketch, "E3320", {"start": v(-25.38, -56.82) * mm, "end": v(-25.47, -57.02) * mm});
            skLineSegment(sketch, "E3321", {"start": v(-25.47, -57.02) * mm, "end": v(-25.55, -57.2) * mm});
            skLineSegment(sketch, "E3322", {"start": v(-25.55, -57.2) * mm, "end": v(-25.63, -57.4) * mm});
            skLineSegment(sketch, "E3323", {"start": v(-25.63, -57.4) * mm, "end": v(-25.71, -57.59) * mm});
            skLineSegment(sketch, "E3324", {"start": v(-25.71, -57.59) * mm, "end": v(-25.8, -57.8) * mm});
            skLineSegment(sketch, "E3325", {"start": v(-25.8, -57.8) * mm, "end": v(-25.85, -58) * mm});
            skLineSegment(sketch, "E3326", {"start": v(-25.85, -58) * mm, "end": v(-25.84, -58.22) * mm});
            skLineSegment(sketch, "E3327", {"start": v(-25.84, -58.22) * mm, "end": v(-25.77, -58.42) * mm});
            skLineSegment(sketch, "E3328", {"start": v(-25.77, -58.42) * mm, "end": v(-25.65, -58.6) * mm});
            skLineSegment(sketch, "E3329", {"start": v(-25.65, -58.6) * mm, "end": v(-25.5, -58.74) * mm});
            skLineSegment(sketch, "E3330", {"start": v(-25.5, -58.74) * mm, "end": v(-25.3, -58.84) * mm});
            skLineSegment(sketch, "E3331", {"start": v(-25.3, -58.84) * mm, "end": v(-25.1, -58.89) * mm});
            skLineSegment(sketch, "E3332", {"start": v(-25.1, -58.89) * mm, "end": v(-24.88, -58.87) * mm});
            skLineSegment(sketch, "E3333", {"start": v(-24.88, -58.87) * mm, "end": v(-24.68, -58.8) * mm});
            skLineSegment(sketch, "E3334", {"start": v(-24.68, -58.8) * mm, "end": v(-24.5, -58.7) * mm});
            skLineSegment(sketch, "E3335", {"start": v(-24.5, -58.7) * mm, "end": v(-24.35, -58.53) * mm});
            skLineSegment(sketch, "E3336", {"start": v(-24.35, -58.53) * mm, "end": v(-24.26, -58.34) * mm});
            skLineSegment(sketch, "E3337", {"start": v(-24.26, -58.34) * mm, "end": v(-24.18, -58.15) * mm});
            skLineSegment(sketch, "E3338", {"start": v(-24.18, -58.15) * mm, "end": v(-24.1, -57.96) * mm});
            skLineSegment(sketch, "E3339", {"start": v(-24.1, -57.96) * mm, "end": v(-24.03, -57.77) * mm});
            skLineSegment(sketch, "E3340", {"start": v(-24.03, -57.77) * mm, "end": v(-23.95, -57.58) * mm});
            skLineSegment(sketch, "E3341", {"start": v(-23.95, -57.58) * mm, "end": v(-23.88, -57.39) * mm});
            skLineSegment(sketch, "E3342", {"start": v(-23.88, -57.39) * mm, "end": v(-23.8, -57.2) * mm});
            skLineSegment(sketch, "E3343", {"start": v(-23.8, -57.2) * mm, "end": v(-23.72, -57) * mm});
            skLineSegment(sketch, "E3344", {"start": v(-23.72, -57) * mm, "end": v(-23.64, -56.8) * mm});
            skLineSegment(sketch, "E3345", {"start": v(-23.64, -56.8) * mm, "end": v(-23.57, -56.62) * mm});
            skLineSegment(sketch, "E3346", {"start": v(-23.57, -56.62) * mm, "end": v(-23.5, -56.42) * mm});
            skLineSegment(sketch, "E3347", {"start": v(-23.5, -56.42) * mm, "end": v(-23.41, -56.23) * mm});
            skLineSegment(sketch, "E3348", {"start": v(-23.41, -56.23) * mm, "end": v(-23.34, -56.04) * mm});
            skLineSegment(sketch, "E3349", {"start": v(-23.34, -56.04) * mm, "end": v(-23.28, -55.9) * mm});
            skLineSegment(sketch, "E3350", {"start": v(-23.28, -55.9) * mm, "end": v(-23.09, -55.97) * mm});
            skLineSegment(sketch, "E3351", {"start": v(-23.09, -55.97) * mm, "end": v(-22.9, -56.04) * mm});
            skLineSegment(sketch, "E3352", {"start": v(-22.9, -56.04) * mm, "end": v(-22.7, -56.11) * mm});
            skLineSegment(sketch, "E3353", {"start": v(-22.7, -56.11) * mm, "end": v(-22.51, -56.19) * mm});
            skLineSegment(sketch, "E3354", {"start": v(-22.51, -56.19) * mm, "end": v(-22.32, -56.26) * mm});
            skLineSegment(sketch, "E3355", {"start": v(-22.32, -56.26) * mm, "end": v(-22.13, -56.33) * mm});
            skLineSegment(sketch, "E3356", {"start": v(-22.13, -56.33) * mm, "end": v(-21.93, -56.4) * mm});
            skLineSegment(sketch, "E3357", {"start": v(-21.93, -56.4) * mm, "end": v(-21.74, -56.48) * mm});
            skLineSegment(sketch, "E3358", {"start": v(-21.74, -56.48) * mm, "end": v(-21.55, -56.55) * mm});
            skLineSegment(sketch, "E3359", {"start": v(-21.55, -56.55) * mm, "end": v(-21.35, -56.62) * mm});
            skLineSegment(sketch, "E3360", {"start": v(-21.35, -56.62) * mm, "end": v(-21.16, -56.7) * mm});
            skLineSegment(sketch, "E3361", {"start": v(-21.16, -56.7) * mm, "end": v(-21.06, -56.73) * mm});
            skLineSegment(sketch, "E3362", {"start": v(-21.06, -56.73) * mm, "end": v(-21.13, -56.93) * mm});
            skLineSegment(sketch, "E3363", {"start": v(-21.13, -56.93) * mm, "end": v(-21.2, -57.12) * mm});
            skLineSegment(sketch, "E3364", {"start": v(-21.2, -57.12) * mm, "end": v(-21.27, -57.32) * mm});
            skLineSegment(sketch, "E3365", {"start": v(-21.27, -57.32) * mm, "end": v(-21.34, -57.51) * mm});
            skLineSegment(sketch, "E3366", {"start": v(-21.34, -57.51) * mm, "end": v(-21.4, -57.7) * mm});
            skLineSegment(sketch, "E3367", {"start": v(-21.4, -57.7) * mm, "end": v(-21.48, -57.9) * mm});
            skLineSegment(sketch, "E3368", {"start": v(-21.48, -57.9) * mm, "end": v(-21.55, -58.1) * mm});
            skLineSegment(sketch, "E3369", {"start": v(-21.55, -58.1) * mm, "end": v(-21.62, -58.3) * mm});
            skLineSegment(sketch, "E3370", {"start": v(-21.62, -58.3) * mm, "end": v(-21.69, -58.5) * mm});
            skLineSegment(sketch, "E3371", {"start": v(-21.69, -58.5) * mm, "end": v(-21.76, -58.69) * mm});
            skLineSegment(sketch, "E3372", {"start": v(-21.76, -58.69) * mm, "end": v(-21.82, -58.88) * mm});
            skLineSegment(sketch, "E3373", {"start": v(-21.82, -58.88) * mm, "end": v(-21.9, -59.08) * mm});
            skLineSegment(sketch, "E3374", {"start": v(-21.9, -59.08) * mm, "end": v(-21.97, -59.3) * mm});
            skLineSegment(sketch, "E3375", {"start": v(-21.97, -59.3) * mm, "end": v(-22, -59.5) * mm});
            skLineSegment(sketch, "E3376", {"start": v(-22, -59.5) * mm, "end": v(-21.98, -59.72) * mm});
            skLineSegment(sketch, "E3377", {"start": v(-21.98, -59.72) * mm, "end": v(-21.9, -59.92) * mm});
            skLineSegment(sketch, "E3378", {"start": v(-21.9, -59.92) * mm, "end": v(-21.77, -60.09) * mm});
            skLineSegment(sketch, "E3379", {"start": v(-21.77, -60.09) * mm, "end": v(-21.6, -60.22) * mm});
            skLineSegment(sketch, "E3380", {"start": v(-21.6, -60.22) * mm, "end": v(-21.4, -60.3) * mm});
            skLineSegment(sketch, "E3381", {"start": v(-21.4, -60.3) * mm, "end": v(-21.2, -60.34) * mm});
            skLineSegment(sketch, "E3382", {"start": v(-21.2, -60.34) * mm, "end": v(-20.98, -60.31) * mm});
            skLineSegment(sketch, "E3383", {"start": v(-20.98, -60.31) * mm, "end": v(-20.78, -60.23) * mm});
            skLineSegment(sketch, "E3384", {"start": v(-20.78, -60.23) * mm, "end": v(-20.6, -60.1) * mm});
            skLineSegment(sketch, "E3385", {"start": v(-20.6, -60.1) * mm, "end": v(-20.47, -59.93) * mm});
            skLineSegment(sketch, "E3386", {"start": v(-20.47, -59.93) * mm, "end": v(-20.4, -59.74) * mm});
            skLineSegment(sketch, "E3387", {"start": v(-20.4, -59.74) * mm, "end": v(-20.33, -59.55) * mm});
            skLineSegment(sketch, "E3388", {"start": v(-20.33, -59.55) * mm, "end": v(-20.27, -59.35) * mm});
            skLineSegment(sketch, "E3389", {"start": v(-20.27, -59.35) * mm, "end": v(-20.2, -59.16) * mm});
            skLineSegment(sketch, "E3390", {"start": v(-20.2, -59.16) * mm, "end": v(-20.14, -58.96) * mm});
            skLineSegment(sketch, "E3391", {"start": v(-20.14, -58.96) * mm, "end": v(-20.07, -58.76) * mm});
            skLineSegment(sketch, "E3392", {"start": v(-20.07, -58.76) * mm, "end": v(-20, -58.56) * mm});
            skLineSegment(sketch, "E3393", {"start": v(-20, -58.56) * mm, "end": v(-19.95, -58.37) * mm});
            skLineSegment(sketch, "E3394", {"start": v(-19.95, -58.37) * mm, "end": v(-19.88, -58.17) * mm});
            skLineSegment(sketch, "E3395", {"start": v(-19.88, -58.17) * mm, "end": v(-19.82, -57.97) * mm});
            skLineSegment(sketch, "E3396", {"start": v(-19.82, -57.97) * mm, "end": v(-19.75, -57.78) * mm});
            skLineSegment(sketch, "E3397", {"start": v(-19.75, -57.78) * mm, "end": v(-19.69, -57.57) * mm});
            skLineSegment(sketch, "E3398", {"start": v(-19.69, -57.57) * mm, "end": v(-19.62, -57.38) * mm});
            skLineSegment(sketch, "E3399", {"start": v(-19.62, -57.38) * mm, "end": v(-19.58, -57.24) * mm});
            skLineSegment(sketch, "E3400", {"start": v(-19.58, -57.24) * mm, "end": v(-19.38, -57.3) * mm});
            skLineSegment(sketch, "E3401", {"start": v(-19.38, -57.3) * mm, "end": v(-19.18, -57.36) * mm});
            skLineSegment(sketch, "E3402", {"start": v(-19.18, -57.36) * mm, "end": v(-18.99, -57.41) * mm});
            skLineSegment(sketch, "E3403", {"start": v(-18.99, -57.41) * mm, "end": v(-18.79, -57.47) * mm});
            skLineSegment(sketch, "E3404", {"start": v(-18.79, -57.47) * mm, "end": v(-18.6, -57.53) * mm});
            skLineSegment(sketch, "E3405", {"start": v(-18.6, -57.53) * mm, "end": v(-18.4, -57.6) * mm});
            skLineSegment(sketch, "E3406", {"start": v(-18.4, -57.6) * mm, "end": v(-18.2, -57.65) * mm});
            skLineSegment(sketch, "E3407", {"start": v(-18.2, -57.65) * mm, "end": v(-18, -57.71) * mm});
            skLineSegment(sketch, "E3408", {"start": v(-18, -57.71) * mm, "end": v(-17.8, -57.77) * mm});
            skLineSegment(sketch, "E3409", {"start": v(-17.8, -57.77) * mm, "end": v(-17.6, -57.83) * mm});
            skLineSegment(sketch, "E3410", {"start": v(-17.6, -57.83) * mm, "end": v(-17.41, -57.9) * mm});
            skLineSegment(sketch, "E3411", {"start": v(-17.41, -57.9) * mm, "end": v(-17.3, -57.92) * mm});
            skLineSegment(sketch, "E3412", {"start": v(-17.3, -57.92) * mm, "end": v(-17.37, -58.12) * mm});
            skLineSegment(sketch, "E3413", {"start": v(-17.37, -58.12) * mm, "end": v(-17.42, -58.32) * mm});
            skLineSegment(sketch, "E3414", {"start": v(-17.42, -58.32) * mm, "end": v(-17.48, -58.52) * mm});
            skLineSegment(sketch, "E3415", {"start": v(-17.48, -58.52) * mm, "end": v(-17.53, -58.72) * mm});
            skLineSegment(sketch, "E3416", {"start": v(-17.53, -58.72) * mm, "end": v(-17.6, -58.92) * mm});
            skLineSegment(sketch, "E3417", {"start": v(-17.6, -58.92) * mm, "end": v(-17.65, -59.12) * mm});
            skLineSegment(sketch, "E3418", {"start": v(-17.65, -59.12) * mm, "end": v(-17.7, -59.32) * mm});
            skLineSegment(sketch, "E3419", {"start": v(-17.7, -59.32) * mm, "end": v(-17.76, -59.52) * mm});
            skLineSegment(sketch, "E3420", {"start": v(-17.76, -59.52) * mm, "end": v(-17.82, -59.72) * mm});
            skLineSegment(sketch, "E3421", {"start": v(-17.82, -59.72) * mm, "end": v(-17.87, -59.92) * mm});
            skLineSegment(sketch, "E3422", {"start": v(-17.87, -59.92) * mm, "end": v(-17.93, -60.12) * mm});
            skLineSegment(sketch, "E3423", {"start": v(-17.93, -60.12) * mm, "end": v(-17.99, -60.32) * mm});
            skLineSegment(sketch, "E3424", {"start": v(-17.99, -60.32) * mm, "end": v(-18.04, -60.54) * mm});
            skLineSegment(sketch, "E3425", {"start": v(-18.04, -60.54) * mm, "end": v(-18.06, -60.75) * mm});
            skLineSegment(sketch, "E3426", {"start": v(-18.06, -60.75) * mm, "end": v(-18.02, -60.96) * mm});
            skLineSegment(sketch, "E3427", {"start": v(-18.02, -60.96) * mm, "end": v(-17.93, -61.16) * mm});
            skLineSegment(sketch, "E3428", {"start": v(-17.93, -61.16) * mm, "end": v(-17.8, -61.32) * mm});
            skLineSegment(sketch, "E3429", {"start": v(-17.8, -61.32) * mm, "end": v(-17.62, -61.44) * mm});
            skLineSegment(sketch, "E3430", {"start": v(-17.62, -61.44) * mm, "end": v(-17.41, -61.51) * mm});
            skLineSegment(sketch, "E3431", {"start": v(-17.41, -61.51) * mm, "end": v(-17.2, -61.53) * mm});
            skLineSegment(sketch, "E3432", {"start": v(-17.2, -61.53) * mm, "end": v(-17, -61.5) * mm});
            skLineSegment(sketch, "E3433", {"start": v(-17, -61.5) * mm, "end": v(-16.8, -61.4) * mm});
            skLineSegment(sketch, "E3434", {"start": v(-16.8, -61.4) * mm, "end": v(-16.63, -61.26) * mm});
            skLineSegment(sketch, "E3435", {"start": v(-16.63, -61.26) * mm, "end": v(-16.51, -61.08) * mm});
            skLineSegment(sketch, "E3436", {"start": v(-16.51, -61.08) * mm, "end": v(-16.45, -60.89) * mm});
            skLineSegment(sketch, "E3437", {"start": v(-16.45, -60.89) * mm, "end": v(-16.4, -60.69) * mm});
            skLineSegment(sketch, "E3438", {"start": v(-16.4, -60.69) * mm, "end": v(-16.34, -60.49) * mm});
            skLineSegment(sketch, "E3439", {"start": v(-16.34, -60.49) * mm, "end": v(-16.3, -60.29) * mm});
            skLineSegment(sketch, "E3440", {"start": v(-16.3, -60.29) * mm, "end": v(-16.24, -60.09) * mm});
            skLineSegment(sketch, "E3441", {"start": v(-16.24, -60.09) * mm, "end": v(-16.19, -59.88) * mm});
            skLineSegment(sketch, "E3442", {"start": v(-16.19, -59.88) * mm, "end": v(-16.14, -59.68) * mm});
            skLineSegment(sketch, "E3443", {"start": v(-16.14, -59.68) * mm, "end": v(-16.09, -59.48) * mm});
            skLineSegment(sketch, "E3444", {"start": v(-16.09, -59.48) * mm, "end": v(-16.04, -59.28) * mm});
            skLineSegment(sketch, "E3445", {"start": v(-16.04, -59.28) * mm, "end": v(-15.99, -59.08) * mm});
            skLineSegment(sketch, "E3446", {"start": v(-15.99, -59.08) * mm, "end": v(-15.93, -58.88) * mm});
            skLineSegment(sketch, "E3447", {"start": v(-15.93, -58.88) * mm, "end": v(-15.88, -58.67) * mm});
            skLineSegment(sketch, "E3448", {"start": v(-15.88, -58.67) * mm, "end": v(-15.83, -58.48) * mm});
            skLineSegment(sketch, "E3449", {"start": v(-15.83, -58.48) * mm, "end": v(-15.8, -58.33) * mm});
            skLineSegment(sketch, "E3450", {"start": v(-15.8, -58.33) * mm, "end": v(-15.6, -58.38) * mm});
            skLineSegment(sketch, "E3451", {"start": v(-15.6, -58.38) * mm, "end": v(-15.4, -58.42) * mm});
            skLineSegment(sketch, "E3452", {"start": v(-15.4, -58.42) * mm, "end": v(-15.2, -58.47) * mm});
            skLineSegment(sketch, "E3453", {"start": v(-15.2, -58.47) * mm, "end": v(-15, -58.52) * mm});
            skLineSegment(sketch, "E3454", {"start": v(-15, -58.52) * mm, "end": v(-14.8, -58.56) * mm});
            skLineSegment(sketch, "E3455", {"start": v(-14.8, -58.56) * mm, "end": v(-14.6, -58.61) * mm});
            skLineSegment(sketch, "E3456", {"start": v(-14.6, -58.61) * mm, "end": v(-14.4, -58.66) * mm});
            skLineSegment(sketch, "E3457", {"start": v(-14.4, -58.66) * mm, "end": v(-14.2, -58.7) * mm});
            skLineSegment(sketch, "E3458", {"start": v(-14.2, -58.7) * mm, "end": v(-13.99, -58.75) * mm});
            skLineSegment(sketch, "E3459", {"start": v(-13.99, -58.75) * mm, "end": v(-13.79, -58.8) * mm});
            skLineSegment(sketch, "E3460", {"start": v(-13.79, -58.8) * mm, "end": v(-13.59, -58.84) * mm});
            skLineSegment(sketch, "E3461", {"start": v(-13.59, -58.84) * mm, "end": v(-13.49, -58.87) * mm});
            skLineSegment(sketch, "E3462", {"start": v(-13.49, -58.87) * mm, "end": v(-13.53, -59.07) * mm});
            skLineSegment(sketch, "E3463", {"start": v(-13.53, -59.07) * mm, "end": v(-13.57, -59.27) * mm});
            skLineSegment(sketch, "E3464", {"start": v(-13.57, -59.27) * mm, "end": v(-13.62, -59.48) * mm});
            skLineSegment(sketch, "E3465", {"start": v(-13.62, -59.48) * mm, "end": v(-13.66, -59.68) * mm});
            skLineSegment(sketch, "E3466", {"start": v(-13.66, -59.68) * mm, "end": v(-13.7, -59.88) * mm});
            skLineSegment(sketch, "E3467", {"start": v(-13.7, -59.88) * mm, "end": v(-13.75, -60.09) * mm});
            skLineSegment(sketch, "E3468", {"start": v(-13.75, -60.09) * mm, "end": v(-13.79, -60.29) * mm});
            skLineSegment(sketch, "E3469", {"start": v(-13.79, -60.29) * mm, "end": v(-13.83, -60.5) * mm});
            skLineSegment(sketch, "E3470", {"start": v(-13.83, -60.5) * mm, "end": v(-13.87, -60.7) * mm});
            skLineSegment(sketch, "E3471", {"start": v(-13.87, -60.7) * mm, "end": v(-13.92, -60.9) * mm});
            skLineSegment(sketch, "E3472", {"start": v(-13.92, -60.9) * mm, "end": v(-13.96, -61.1) * mm});
            skLineSegment(sketch, "E3473", {"start": v(-13.96, -61.1) * mm, "end": v(-14, -61.3) * mm});
            skLineSegment(sketch, "E3474", {"start": v(-14, -61.3) * mm, "end": v(-14.05, -61.52) * mm});
            skLineSegment(sketch, "E3475", {"start": v(-14.05, -61.52) * mm, "end": v(-14.05, -61.74) * mm});
            skLineSegment(sketch, "E3476", {"start": v(-14.05, -61.74) * mm, "end": v(-14, -61.95) * mm});
            skLineSegment(sketch, "E3477", {"start": v(-14, -61.95) * mm, "end": v(-13.9, -62.13) * mm});
            skLineSegment(sketch, "E3478", {"start": v(-13.9, -62.13) * mm, "end": v(-13.75, -62.29) * mm});
            skLineSegment(sketch, "E3479", {"start": v(-13.75, -62.29) * mm, "end": v(-13.56, -62.4) * mm});
            skLineSegment(sketch, "E3480", {"start": v(-13.56, -62.4) * mm, "end": v(-13.36, -62.46) * mm});
            skLineSegment(sketch, "E3481", {"start": v(-13.36, -62.46) * mm, "end": v(-13.14, -62.46) * mm});
            skLineSegment(sketch, "E3482", {"start": v(-13.14, -62.46) * mm, "end": v(-12.93, -62.4) * mm});
            skLineSegment(sketch, "E3483", {"start": v(-12.93, -62.4) * mm, "end": v(-12.75, -62.3) * mm});
            skLineSegment(sketch, "E3484", {"start": v(-12.75, -62.3) * mm, "end": v(-12.6, -62.15) * mm});
            skLineSegment(sketch, "E3485", {"start": v(-12.6, -62.15) * mm, "end": v(-12.49, -61.97) * mm});
            skLineSegment(sketch, "E3486", {"start": v(-12.49, -61.97) * mm, "end": v(-12.43, -61.77) * mm});
            skLineSegment(sketch, "E3487", {"start": v(-12.43, -61.77) * mm, "end": v(-12.4, -61.56) * mm});
            skLineSegment(sketch, "E3488", {"start": v(-12.4, -61.56) * mm, "end": v(-12.35, -61.36) * mm});
            skLineSegment(sketch, "E3489", {"start": v(-12.35, -61.36) * mm, "end": v(-12.32, -61.16) * mm});
            skLineSegment(sketch, "E3490", {"start": v(-12.32, -61.16) * mm, "end": v(-12.28, -60.96) * mm});
            skLineSegment(sketch, "E3491", {"start": v(-12.28, -60.96) * mm, "end": v(-12.24, -60.75) * mm});
            skLineSegment(sketch, "E3492", {"start": v(-12.24, -60.75) * mm, "end": v(-12.2, -60.55) * mm});
            skLineSegment(sketch, "E3493", {"start": v(-12.2, -60.55) * mm, "end": v(-12.17, -60.35) * mm});
            skLineSegment(sketch, "E3494", {"start": v(-12.17, -60.35) * mm, "end": v(-12.13, -60.14) * mm});
            skLineSegment(sketch, "E3495", {"start": v(-12.13, -60.14) * mm, "end": v(-12.09, -59.93) * mm});
            skLineSegment(sketch, "E3496", {"start": v(-12.09, -59.93) * mm, "end": v(-12.05, -59.73) * mm});
            skLineSegment(sketch, "E3497", {"start": v(-12.05, -59.73) * mm, "end": v(-12.01, -59.52) * mm});
            skLineSegment(sketch, "E3498", {"start": v(-12.01, -59.52) * mm, "end": v(-11.98, -59.32) * mm});
            skLineSegment(sketch, "E3499", {"start": v(-11.98, -59.32) * mm, "end": v(-11.95, -59.17) * mm});
            skLineSegment(sketch, "E3500", {"start": v(-11.95, -59.17) * mm, "end": v(-11.74, -59.2) * mm});
            skLineSegment(sketch, "E3501", {"start": v(-11.74, -59.2) * mm, "end": v(-11.54, -59.24) * mm});
            skLineSegment(sketch, "E3502", {"start": v(-11.54, -59.24) * mm, "end": v(-11.34, -59.27) * mm});
            skLineSegment(sketch, "E3503", {"start": v(-11.34, -59.27) * mm, "end": v(-11.14, -59.3) * mm});
            skLineSegment(sketch, "E3504", {"start": v(-11.14, -59.3) * mm, "end": v(-10.93, -59.34) * mm});
            skLineSegment(sketch, "E3505", {"start": v(-10.93, -59.34) * mm, "end": v(-10.73, -59.38) * mm});
            skLineSegment(sketch, "E3506", {"start": v(-10.73, -59.38) * mm, "end": v(-10.53, -59.4) * mm});
            skLineSegment(sketch, "E3507", {"start": v(-10.53, -59.4) * mm, "end": v(-10.32, -59.44) * mm});
            skLineSegment(sketch, "E3508", {"start": v(-10.32, -59.44) * mm, "end": v(-10.12, -59.48) * mm});
            skLineSegment(sketch, "E3509", {"start": v(-10.12, -59.48) * mm, "end": v(-9.92, -59.5) * mm});
            skLineSegment(sketch, "E3510", {"start": v(-9.92, -59.5) * mm, "end": v(-9.71, -59.54) * mm});
            skLineSegment(sketch, "E3511", {"start": v(-9.71, -59.54) * mm, "end": v(-9.6, -59.56) * mm});
            skLineSegment(sketch, "E3512", {"start": v(-9.6, -59.56) * mm, "end": v(-9.64, -59.76) * mm});
            skLineSegment(sketch, "E3513", {"start": v(-9.64, -59.76) * mm, "end": v(-9.67, -59.97) * mm});
            skLineSegment(sketch, "E3514", {"start": v(-9.67, -59.97) * mm, "end": v(-9.7, -60.18) * mm});
            skLineSegment(sketch, "E3515", {"start": v(-9.7, -60.18) * mm, "end": v(-9.73, -60.38) * mm});
            skLineSegment(sketch, "E3516", {"start": v(-9.73, -60.38) * mm, "end": v(-9.76, -60.58) * mm});
            skLineSegment(sketch, "E3517", {"start": v(-9.76, -60.58) * mm, "end": v(-9.79, -60.8) * mm});
            skLineSegment(sketch, "E3518", {"start": v(-9.79, -60.8) * mm, "end": v(-9.82, -61) * mm});
            skLineSegment(sketch, "E3519", {"start": v(-9.82, -61) * mm, "end": v(-9.85, -61.2) * mm});
            skLineSegment(sketch, "E3520", {"start": v(-9.85, -61.2) * mm, "end": v(-9.88, -61.41) * mm});
            skLineSegment(sketch, "E3521", {"start": v(-9.88, -61.41) * mm, "end": v(-9.9, -61.62) * mm});
            skLineSegment(sketch, "E3522", {"start": v(-9.9, -61.62) * mm, "end": v(-9.94, -61.82) * mm});
            skLineSegment(sketch, "E3523", {"start": v(-9.94, -61.82) * mm, "end": v(-9.97, -62.03) * mm});
            skLineSegment(sketch, "E3524", {"start": v(-9.97, -62.03) * mm, "end": v(-10, -62.25) * mm});
            skLineSegment(sketch, "E3525", {"start": v(-10, -62.25) * mm, "end": v(-9.99, -62.46) * mm});
            skLineSegment(sketch, "E3526", {"start": v(-9.99, -62.46) * mm, "end": v(-9.92, -62.67) * mm});
            skLineSegment(sketch, "E3527", {"start": v(-9.92, -62.67) * mm, "end": v(-9.8, -62.85) * mm});
            skLineSegment(sketch, "E3528", {"start": v(-9.8, -62.85) * mm, "end": v(-9.65, -63) * mm});
            skLineSegment(sketch, "E3529", {"start": v(-9.65, -63) * mm, "end": v(-9.46, -63.09) * mm});
            skLineSegment(sketch, "E3530", {"start": v(-9.46, -63.09) * mm, "end": v(-9.25, -63.13) * mm});
            skLineSegment(sketch, "E3531", {"start": v(-9.25, -63.13) * mm, "end": v(-9.03, -63.12) * mm});
            skLineSegment(sketch, "E3532", {"start": v(-9.03, -63.12) * mm, "end": v(-8.83, -63.05) * mm});
            skLineSegment(sketch, "E3533", {"start": v(-8.83, -63.05) * mm, "end": v(-8.65, -62.94) * mm});
            skLineSegment(sketch, "E3534", {"start": v(-8.65, -62.94) * mm, "end": v(-8.5, -62.78) * mm});
            skLineSegment(sketch, "E3535", {"start": v(-8.5, -62.78) * mm, "end": v(-8.4, -62.59) * mm});
            skLineSegment(sketch, "E3536", {"start": v(-8.4, -62.59) * mm, "end": v(-8.37, -62.38) * mm});
            skLineSegment(sketch, "E3537", {"start": v(-8.37, -62.38) * mm, "end": v(-8.34, -62.18) * mm});
            skLineSegment(sketch, "E3538", {"start": v(-8.34, -62.18) * mm, "end": v(-8.32, -61.98) * mm});
            skLineSegment(sketch, "E3539", {"start": v(-8.32, -61.98) * mm, "end": v(-8.3, -61.77) * mm});
            skLineSegment(sketch, "E3540", {"start": v(-8.3, -61.77) * mm, "end": v(-8.27, -61.57) * mm});
            skLineSegment(sketch, "E3541", {"start": v(-8.27, -61.57) * mm, "end": v(-8.24, -61.36) * mm});
            skLineSegment(sketch, "E3542", {"start": v(-8.24, -61.36) * mm, "end": v(-8.22, -61.15) * mm});
            skLineSegment(sketch, "E3543", {"start": v(-8.22, -61.15) * mm, "end": v(-8.2, -60.95) * mm});
            skLineSegment(sketch, "E3544", {"start": v(-8.2, -60.95) * mm, "end": v(-8.17, -60.74) * mm});
            skLineSegment(sketch, "E3545", {"start": v(-8.17, -60.74) * mm, "end": v(-8.15, -60.53) * mm});
            skLineSegment(sketch, "E3546", {"start": v(-8.15, -60.53) * mm, "end": v(-8.12, -60.33) * mm});
            skLineSegment(sketch, "E3547", {"start": v(-8.12, -60.33) * mm, "end": v(-8.1, -60.12) * mm});
            skLineSegment(sketch, "E3548", {"start": v(-8.1, -60.12) * mm, "end": v(-8.07, -59.91) * mm});
            skLineSegment(sketch, "E3549", {"start": v(-8.07, -59.91) * mm, "end": v(-8.05, -59.76) * mm});
            skLineSegment(sketch, "E3550", {"start": v(-8.05, -59.76) * mm, "end": v(-7.85, -59.78) * mm});
            skLineSegment(sketch, "E3551", {"start": v(-7.85, -59.78) * mm, "end": v(-7.64, -59.8) * mm});
            skLineSegment(sketch, "E3552", {"start": v(-7.64, -59.8) * mm, "end": v(-7.44, -59.83) * mm});
            skLineSegment(sketch, "E3553", {"start": v(-7.44, -59.83) * mm, "end": v(-7.23, -59.85) * mm});
            skLineSegment(sketch, "E3554", {"start": v(-7.23, -59.85) * mm, "end": v(-7.03, -59.87) * mm});
            skLineSegment(sketch, "E3555", {"start": v(-7.03, -59.87) * mm, "end": v(-6.82, -59.89) * mm});
            skLineSegment(sketch, "E3556", {"start": v(-6.82, -59.89) * mm, "end": v(-6.62, -59.9) * mm});
            skLineSegment(sketch, "E3557", {"start": v(-6.62, -59.9) * mm, "end": v(-6.41, -59.93) * mm});
            skLineSegment(sketch, "E3558", {"start": v(-6.41, -59.93) * mm, "end": v(-6.2, -59.95) * mm});
            skLineSegment(sketch, "E3559", {"start": v(-6.2, -59.95) * mm, "end": v(-6, -59.97) * mm});
            skLineSegment(sketch, "E3560", {"start": v(-6, -59.97) * mm, "end": v(-5.8, -59.99) * mm});
            skLineSegment(sketch, "E3561", {"start": v(-5.8, -59.99) * mm, "end": v(-5.7, -60) * mm});
            skLineSegment(sketch, "E3562", {"start": v(-5.7, -60) * mm, "end": v(-5.71, -60.2) * mm});
            skLineSegment(sketch, "E3563", {"start": v(-5.71, -60.2) * mm, "end": v(-5.73, -60.4) * mm});
            skLineSegment(sketch, "E3564", {"start": v(-5.73, -60.4) * mm, "end": v(-5.74, -60.62) * mm});
            skLineSegment(sketch, "E3565", {"start": v(-5.74, -60.62) * mm, "end": v(-5.76, -60.82) * mm});
            skLineSegment(sketch, "E3566", {"start": v(-5.76, -60.82) * mm, "end": v(-5.78, -61.03) * mm});
            skLineSegment(sketch, "E3567", {"start": v(-5.78, -61.03) * mm, "end": v(-5.8, -61.24) * mm});
            skLineSegment(sketch, "E3568", {"start": v(-5.8, -61.24) * mm, "end": v(-5.8, -61.45) * mm});
            skLineSegment(sketch, "E3569", {"start": v(-5.8, -61.45) * mm, "end": v(-5.83, -61.65) * mm});
            skLineSegment(sketch, "E3570", {"start": v(-5.83, -61.65) * mm, "end": v(-5.84, -61.86) * mm});
            skLineSegment(sketch, "E3571", {"start": v(-5.84, -61.86) * mm, "end": v(-5.86, -62.07) * mm});
            skLineSegment(sketch, "E3572", {"start": v(-5.86, -62.07) * mm, "end": v(-5.87, -62.27) * mm});
            skLineSegment(sketch, "E3573", {"start": v(-5.87, -62.27) * mm, "end": v(-5.9, -62.48) * mm});
            skLineSegment(sketch, "E3574", {"start": v(-5.9, -62.48) * mm, "end": v(-5.9, -62.7) * mm});
            skLineSegment(sketch, "E3575", {"start": v(-5.9, -62.7) * mm, "end": v(-5.88, -62.92) * mm});
            skLineSegment(sketch, "E3576", {"start": v(-5.88, -62.92) * mm, "end": v(-5.8, -63.12) * mm});
            skLineSegment(sketch, "E3577", {"start": v(-5.8, -63.12) * mm, "end": v(-5.68, -63.29) * mm});
            skLineSegment(sketch, "E3578", {"start": v(-5.68, -63.29) * mm, "end": v(-5.5, -63.42) * mm});
            skLineSegment(sketch, "E3579", {"start": v(-5.5, -63.42) * mm, "end": v(-5.31, -63.5) * mm});
            skLineSegment(sketch, "E3580", {"start": v(-5.31, -63.5) * mm, "end": v(-5.1, -63.54) * mm});
            skLineSegment(sketch, "E3581", {"start": v(-5.1, -63.54) * mm, "end": v(-4.89, -63.51) * mm});
            skLineSegment(sketch, "E3582", {"start": v(-4.89, -63.51) * mm, "end": v(-4.69, -63.43) * mm});
            skLineSegment(sketch, "E3583", {"start": v(-4.69, -63.43) * mm, "end": v(-4.51, -63.3) * mm});
            skLineSegment(sketch, "E3584", {"start": v(-4.51, -63.3) * mm, "end": v(-4.38, -63.14) * mm});
            skLineSegment(sketch, "E3585", {"start": v(-4.38, -63.14) * mm, "end": v(-4.3, -62.94) * mm});
            skLineSegment(sketch, "E3586", {"start": v(-4.3, -62.94) * mm, "end": v(-4.27, -62.73) * mm});
            skLineSegment(sketch, "E3587", {"start": v(-4.27, -62.73) * mm, "end": v(-4.26, -62.53) * mm});
            skLineSegment(sketch, "E3588", {"start": v(-4.26, -62.53) * mm, "end": v(-4.25, -62.32) * mm});
            skLineSegment(sketch, "E3589", {"start": v(-4.25, -62.32) * mm, "end": v(-4.24, -62.12) * mm});
            skLineSegment(sketch, "E3590", {"start": v(-4.24, -62.12) * mm, "end": v(-4.23, -61.91) * mm});
            skLineSegment(sketch, "E3591", {"start": v(-4.23, -61.91) * mm, "end": v(-4.21, -61.7) * mm});
            skLineSegment(sketch, "E3592", {"start": v(-4.21, -61.7) * mm, "end": v(-4.2, -61.5) * mm});
            skLineSegment(sketch, "E3593", {"start": v(-4.2, -61.5) * mm, "end": v(-4.2, -61.29) * mm});
            skLineSegment(sketch, "E3594", {"start": v(-4.2, -61.29) * mm, "end": v(-4.18, -61.08) * mm});
            skLineSegment(sketch, "E3595", {"start": v(-4.18, -61.08) * mm, "end": v(-4.17, -60.87) * mm});
            skLineSegment(sketch, "E3596", {"start": v(-4.17, -60.87) * mm, "end": v(-4.16, -60.67) * mm});
            skLineSegment(sketch, "E3597", {"start": v(-4.16, -60.67) * mm, "end": v(-4.15, -60.46) * mm});
            skLineSegment(sketch, "E3598", {"start": v(-4.15, -60.46) * mm, "end": v(-4.14, -60.25) * mm});
            skLineSegment(sketch, "E3599", {"start": v(-4.14, -60.25) * mm, "end": v(-4.13, -60.1) * mm});
            skLineSegment(sketch, "E3600", {"start": v(-4.13, -60.1) * mm, "end": v(-3.92, -60.1) * mm});
            skLineSegment(sketch, "E3601", {"start": v(-3.92, -60.1) * mm, "end": v(-3.72, -60.11) * mm});
            skLineSegment(sketch, "E3602", {"start": v(-3.72, -60.11) * mm, "end": v(-3.51, -60.12) * mm});
            skLineSegment(sketch, "E3603", {"start": v(-3.51, -60.12) * mm, "end": v(-3.3, -60.13) * mm});
            skLineSegment(sketch, "E3604", {"start": v(-3.3, -60.13) * mm, "end": v(-3.1, -60.13) * mm});
            skLineSegment(sketch, "E3605", {"start": v(-3.1, -60.13) * mm, "end": v(-2.9, -60.14) * mm});
            skLineSegment(sketch, "E3606", {"start": v(-2.9, -60.14) * mm, "end": v(-2.69, -60.15) * mm});
            skLineSegment(sketch, "E3607", {"start": v(-2.69, -60.15) * mm, "end": v(-2.48, -60.15) * mm});
            skLineSegment(sketch, "E3608", {"start": v(-2.48, -60.15) * mm, "end": v(-2.28, -60.16) * mm});
            skLineSegment(sketch, "E3609", {"start": v(-2.28, -60.16) * mm, "end": v(-2.07, -60.17) * mm});
            skLineSegment(sketch, "E3610", {"start": v(-2.07, -60.17) * mm, "end": v(-1.87, -60.17) * mm});
            skLineSegment(sketch, "E3611", {"start": v(-1.87, -60.17) * mm, "end": v(-1.76, -60.18) * mm});
            skLineSegment(sketch, "E3612", {"start": v(-1.76, -60.18) * mm, "end": v(-1.76, -60.38) * mm});
            skLineSegment(sketch, "E3613", {"start": v(-1.76, -60.38) * mm, "end": v(-1.77, -60.59) * mm});
            skLineSegment(sketch, "E3614", {"start": v(-1.77, -60.59) * mm, "end": v(-1.77, -60.8) * mm});
            skLineSegment(sketch, "E3615", {"start": v(-1.77, -60.8) * mm, "end": v(-1.77, -61) * mm});
            skLineSegment(sketch, "E3616", {"start": v(-1.77, -61) * mm, "end": v(-1.77, -61.21) * mm});
            skLineSegment(sketch, "E3617", {"start": v(-1.77, -61.21) * mm, "end": v(-1.78, -61.42) * mm});
            skLineSegment(sketch, "E3618", {"start": v(-1.78, -61.42) * mm, "end": v(-1.78, -61.63) * mm});
            skLineSegment(sketch, "E3619", {"start": v(-1.78, -61.63) * mm, "end": v(-1.78, -61.84) * mm});
            skLineSegment(sketch, "E3620", {"start": v(-1.78, -61.84) * mm, "end": v(-1.79, -62.05) * mm});
            skLineSegment(sketch, "E3621", {"start": v(-1.79, -62.05) * mm, "end": v(-1.79, -62.25) * mm});
            skLineSegment(sketch, "E3622", {"start": v(-1.79, -62.25) * mm, "end": v(-1.8, -62.46) * mm});
            skLineSegment(sketch, "E3623", {"start": v(-1.8, -62.46) * mm, "end": v(-1.8, -62.67) * mm});
            skLineSegment(sketch, "E3624", {"start": v(-1.8, -62.67) * mm, "end": v(-1.8, -62.9) * mm});
            skLineSegment(sketch, "E3625", {"start": v(-1.8, -62.9) * mm, "end": v(-1.76, -63.1) * mm});
            skLineSegment(sketch, "E3626", {"start": v(-1.76, -63.1) * mm, "end": v(-1.67, -63.3) * mm});
            skLineSegment(sketch, "E3627", {"start": v(-1.67, -63.3) * mm, "end": v(-1.53, -63.46) * mm});
            skLineSegment(sketch, "E3628", {"start": v(-1.53, -63.46) * mm, "end": v(-1.35, -63.58) * mm});
            skLineSegment(sketch, "E3629", {"start": v(-1.35, -63.58) * mm, "end": v(-1.15, -63.65) * mm});
            skLineSegment(sketch, "E3630", {"start": v(-1.15, -63.65) * mm, "end": v(-0.93, -63.67) * mm});
            skLineSegment(sketch, "E3631", {"start": v(-0.93, -63.67) * mm, "end": v(-0.72, -63.63) * mm});
            skLineSegment(sketch, "E3632", {"start": v(-0.72, -63.63) * mm, "end": v(-0.53, -63.54) * mm});
            skLineSegment(sketch, "E3633", {"start": v(-0.53, -63.54) * mm, "end": v(-0.37, -63.4) * mm});
            skLineSegment(sketch, "E3634", {"start": v(-0.37, -63.4) * mm, "end": v(-0.25, -63.22) * mm});
            skLineSegment(sketch, "E3635", {"start": v(-0.25, -63.22) * mm, "end": v(-0.18, -63.02) * mm});
            skLineSegment(sketch, "E3636", {"start": v(-0.18, -63.02) * mm, "end": v(-0.16, -62.81) * mm});
            skLineSegment(sketch, "E3637", {"start": v(-0.16, -62.81) * mm, "end": v(-0.16, -62.6) * mm});
            skLineSegment(sketch, "E3638", {"start": v(-0.16, -62.6) * mm, "end": v(-0.16, -62.4) * mm});
            skLineSegment(sketch, "E3639", {"start": v(-0.16, -62.4) * mm, "end": v(-0.17, -62.2) * mm});
            skLineSegment(sketch, "E3640", {"start": v(-0.17, -62.2) * mm, "end": v(-0.17, -62) * mm});
            skLineSegment(sketch, "E3641", {"start": v(-0.17, -62) * mm, "end": v(-0.17, -61.78) * mm});
            skLineSegment(sketch, "E3642", {"start": v(-0.17, -61.78) * mm, "end": v(-0.18, -61.57) * mm});
            skLineSegment(sketch, "E3643", {"start": v(-0.18, -61.57) * mm, "end": v(-0.18, -61.37) * mm});
            skLineSegment(sketch, "E3644", {"start": v(-0.18, -61.37) * mm, "end": v(-0.18, -61.16) * mm});
            skLineSegment(sketch, "E3645", {"start": v(-0.18, -61.16) * mm, "end": v(-0.18, -60.95) * mm});
            skLineSegment(sketch, "E3646", {"start": v(-0.18, -60.95) * mm, "end": v(-0.19, -60.75) * mm});
            skLineSegment(sketch, "E3647", {"start": v(-0.19, -60.75) * mm, "end": v(-0.19, -60.53) * mm});
            skLineSegment(sketch, "E3648", {"start": v(-0.19, -60.53) * mm, "end": v(-0.2, -60.33) * mm});
            skLineSegment(sketch, "E3649", {"start": v(-0.2, -60.33) * mm, "end": v(-0.2, -60.18) * mm});
            skLineSegment(sketch, "E3650", {"start": v(-0.2, -60.18) * mm, "end": v(0.01, -60.17) * mm});
            skLineSegment(sketch, "E3651", {"start": v(0.01, -60.17) * mm, "end": v(0.22, -60.16) * mm});
            skLineSegment(sketch, "E3652", {"start": v(0.22, -60.16) * mm, "end": v(0.42, -60.16) * mm});
            skLineSegment(sketch, "E3653", {"start": v(0.42, -60.16) * mm, "end": v(0.63, -60.15) * mm});
            skLineSegment(sketch, "E3654", {"start": v(0.63, -60.15) * mm, "end": v(0.84, -60.14) * mm});
            skLineSegment(sketch, "E3655", {"start": v(0.84, -60.14) * mm, "end": v(1.04, -60.14) * mm});
            skLineSegment(sketch, "E3656", {"start": v(1.04, -60.14) * mm, "end": v(1.25, -60.13) * mm});
            skLineSegment(sketch, "E3657", {"start": v(1.25, -60.13) * mm, "end": v(1.45, -60.12) * mm});
            skLineSegment(sketch, "E3658", {"start": v(1.45, -60.12) * mm, "end": v(1.66, -60.12) * mm});
            skLineSegment(sketch, "E3659", {"start": v(1.66, -60.12) * mm, "end": v(1.87, -60.1) * mm});
            skLineSegment(sketch, "E3660", {"start": v(1.87, -60.1) * mm, "end": v(2.07, -60.1) * mm});
            skLineSegment(sketch, "E3661", {"start": v(2.07, -60.1) * mm, "end": v(2.18, -60.1) * mm});
            skLineSegment(sketch, "E3662", {"start": v(2.18, -60.1) * mm, "end": v(2.19, -60.3) * mm});
            skLineSegment(sketch, "E3663", {"start": v(2.19, -60.3) * mm, "end": v(2.2, -60.51) * mm});
            skLineSegment(sketch, "E3664", {"start": v(2.2, -60.51) * mm, "end": v(2.2, -60.72) * mm});
            skLineSegment(sketch, "E3665", {"start": v(2.2, -60.72) * mm, "end": v(2.22, -60.93) * mm});
            skLineSegment(sketch, "E3666", {"start": v(2.22, -60.93) * mm, "end": v(2.23, -61.13) * mm});
            skLineSegment(sketch, "E3667", {"start": v(2.23, -61.13) * mm, "end": v(2.24, -61.34) * mm});
            skLineSegment(sketch, "E3668", {"start": v(2.24, -61.34) * mm, "end": v(2.25, -61.55) * mm});
            skLineSegment(sketch, "E3669", {"start": v(2.25, -61.55) * mm, "end": v(2.26, -61.76) * mm});
            skLineSegment(sketch, "E3670", {"start": v(2.26, -61.76) * mm, "end": v(2.27, -61.97) * mm});
            skLineSegment(sketch, "E3671", {"start": v(2.27, -61.97) * mm, "end": v(2.29, -62.17) * mm});
            skLineSegment(sketch, "E3672", {"start": v(2.29, -62.17) * mm, "end": v(2.3, -62.38) * mm});
            skLineSegment(sketch, "E3673", {"start": v(2.3, -62.38) * mm, "end": v(2.3, -62.6) * mm});
            skLineSegment(sketch, "E3674", {"start": v(2.3, -62.6) * mm, "end": v(2.32, -62.81) * mm});
            skLineSegment(sketch, "E3675", {"start": v(2.32, -62.81) * mm, "end": v(2.37, -63.02) * mm});
            skLineSegment(sketch, "E3676", {"start": v(2.37, -63.02) * mm, "end": v(2.48, -63.2) * mm});
            skLineSegment(sketch, "E3677", {"start": v(2.48, -63.2) * mm, "end": v(2.62, -63.36) * mm});
            skLineSegment(sketch, "E3678", {"start": v(2.62, -63.36) * mm, "end": v(2.8, -63.47) * mm});
            skLineSegment(sketch, "E3679", {"start": v(2.8, -63.47) * mm, "end": v(3.02, -63.53) * mm});
            skLineSegment(sketch, "E3680", {"start": v(3.02, -63.53) * mm, "end": v(3.23, -63.53) * mm});
            skLineSegment(sketch, "E3681", {"start": v(3.23, -63.53) * mm, "end": v(3.44, -63.48) * mm});
            skLineSegment(sketch, "E3682", {"start": v(3.44, -63.48) * mm, "end": v(3.63, -63.37) * mm});
            skLineSegment(sketch, "E3683", {"start": v(3.63, -63.37) * mm, "end": v(3.78, -63.22) * mm});
            skLineSegment(sketch, "E3684", {"start": v(3.78, -63.22) * mm, "end": v(3.89, -63.04) * mm});
            skLineSegment(sketch, "E3685", {"start": v(3.89, -63.04) * mm, "end": v(3.94, -62.83) * mm});
            skLineSegment(sketch, "E3686", {"start": v(3.94, -62.83) * mm, "end": v(3.94, -62.63) * mm});
            skLineSegment(sketch, "E3687", {"start": v(3.94, -62.63) * mm, "end": v(3.93, -62.42) * mm});
            skLineSegment(sketch, "E3688", {"start": v(3.93, -62.42) * mm, "end": v(3.92, -62.22) * mm});
            skLineSegment(sketch, "E3689", {"start": v(3.92, -62.22) * mm, "end": v(3.9, -62.01) * mm});
            skLineSegment(sketch, "E3690", {"start": v(3.9, -62.01) * mm, "end": v(3.88, -61.8) * mm});
            skLineSegment(sketch, "E3691", {"start": v(3.88, -61.8) * mm, "end": v(3.87, -61.6) * mm});
            skLineSegment(sketch, "E3692", {"start": v(3.87, -61.6) * mm, "end": v(3.85, -61.4) * mm});
            skLineSegment(sketch, "E3693", {"start": v(3.85, -61.4) * mm, "end": v(3.83, -61.18) * mm});
            skLineSegment(sketch, "E3694", {"start": v(3.83, -61.18) * mm, "end": v(3.82, -60.97) * mm});
            skLineSegment(sketch, "E3695", {"start": v(3.82, -60.97) * mm, "end": v(3.8, -60.77) * mm});
            skLineSegment(sketch, "E3696", {"start": v(3.8, -60.77) * mm, "end": v(3.79, -60.56) * mm});
            skLineSegment(sketch, "E3697", {"start": v(3.79, -60.56) * mm, "end": v(3.77, -60.35) * mm});
            skLineSegment(sketch, "E3698", {"start": v(3.77, -60.35) * mm, "end": v(3.75, -60.15) * mm});
            skLineSegment(sketch, "E3699", {"start": v(3.75, -60.15) * mm, "end": v(3.74, -60) * mm});
            skLineSegment(sketch, "E3700", {"start": v(3.74, -60) * mm, "end": v(3.95, -59.98) * mm});
            skLineSegment(sketch, "E3701", {"start": v(3.95, -59.98) * mm, "end": v(4.15, -59.96) * mm});
            skLineSegment(sketch, "E3702", {"start": v(4.15, -59.96) * mm, "end": v(4.36, -59.94) * mm});
            skLineSegment(sketch, "E3703", {"start": v(4.36, -59.94) * mm, "end": v(4.56, -59.92) * mm});
            skLineSegment(sketch, "E3704", {"start": v(4.56, -59.92) * mm, "end": v(4.77, -59.9) * mm});
            skLineSegment(sketch, "E3705", {"start": v(4.77, -59.9) * mm, "end": v(4.97, -59.88) * mm});
            skLineSegment(sketch, "E3706", {"start": v(4.97, -59.88) * mm, "end": v(5.18, -59.86) * mm});
            skLineSegment(sketch, "E3707", {"start": v(5.18, -59.86) * mm, "end": v(5.38, -59.84) * mm});
            skLineSegment(sketch, "E3708", {"start": v(5.38, -59.84) * mm, "end": v(5.59, -59.82) * mm});
            skLineSegment(sketch, "E3709", {"start": v(5.59, -59.82) * mm, "end": v(5.8, -59.8) * mm});
            skLineSegment(sketch, "E3710", {"start": v(5.8, -59.8) * mm, "end": v(6, -59.78) * mm});
            skLineSegment(sketch, "E3711", {"start": v(6, -59.78) * mm, "end": v(6.1, -59.76) * mm});
            skLineSegment(sketch, "E3712", {"start": v(6.1, -59.76) * mm, "end": v(6.12, -59.97) * mm});
            skLineSegment(sketch, "E3713", {"start": v(6.12, -59.97) * mm, "end": v(6.15, -60.17) * mm});
            skLineSegment(sketch, "E3714", {"start": v(6.15, -60.17) * mm, "end": v(6.17, -60.38) * mm});
            skLineSegment(sketch, "E3715", {"start": v(6.17, -60.38) * mm, "end": v(6.2, -60.59) * mm});
            skLineSegment(sketch, "E3716", {"start": v(6.2, -60.59) * mm, "end": v(6.22, -60.8) * mm});
            skLineSegment(sketch, "E3717", {"start": v(6.22, -60.8) * mm, "end": v(6.25, -61) * mm});
            skLineSegment(sketch, "E3718", {"start": v(6.25, -61) * mm, "end": v(6.27, -61.2) * mm});
            skLineSegment(sketch, "E3719", {"start": v(6.27, -61.2) * mm, "end": v(6.3, -61.41) * mm});
            skLineSegment(sketch, "E3720", {"start": v(6.3, -61.41) * mm, "end": v(6.32, -61.62) * mm});
            skLineSegment(sketch, "E3721", {"start": v(6.32, -61.62) * mm, "end": v(6.34, -61.83) * mm});
            skLineSegment(sketch, "E3722", {"start": v(6.34, -61.83) * mm, "end": v(6.37, -62.03) * mm});
            skLineSegment(sketch, "E3723", {"start": v(6.37, -62.03) * mm, "end": v(6.4, -62.24) * mm});
            skLineSegment(sketch, "E3724", {"start": v(6.4, -62.24) * mm, "end": v(6.42, -62.46) * mm});
            skLineSegment(sketch, "E3725", {"start": v(6.42, -62.46) * mm, "end": v(6.49, -62.67) * mm});
            skLineSegment(sketch, "E3726", {"start": v(6.49, -62.67) * mm, "end": v(6.6, -62.85) * mm});
            skLineSegment(sketch, "E3727", {"start": v(6.6, -62.85) * mm, "end": v(6.76, -63) * mm});
            skLineSegment(sketch, "E3728", {"start": v(6.76, -63) * mm, "end": v(6.95, -63.09) * mm});
            skLineSegment(sketch, "E3729", {"start": v(6.95, -63.09) * mm, "end": v(7.16, -63.13) * mm});
            skLineSegment(sketch, "E3730", {"start": v(7.16, -63.13) * mm, "end": v(7.38, -63.12) * mm});
            skLineSegment(sketch, "E3731", {"start": v(7.38, -63.12) * mm, "end": v(7.58, -63.06) * mm});
            skLineSegment(sketch, "E3732", {"start": v(7.58, -63.06) * mm, "end": v(7.76, -62.94) * mm});
            skLineSegment(sketch, "E3733", {"start": v(7.76, -62.94) * mm, "end": v(7.9, -62.78) * mm});
            skLineSegment(sketch, "E3734", {"start": v(7.9, -62.78) * mm, "end": v(8, -62.59) * mm});
            skLineSegment(sketch, "E3735", {"start": v(8, -62.59) * mm, "end": v(8.04, -62.38) * mm});
            skLineSegment(sketch, "E3736", {"start": v(8.04, -62.38) * mm, "end": v(8.03, -62.17) * mm});
            skLineSegment(sketch, "E3737", {"start": v(8.03, -62.17) * mm, "end": v(8, -61.97) * mm});
            skLineSegment(sketch, "E3738", {"start": v(8, -61.97) * mm, "end": v(7.97, -61.76) * mm});
            skLineSegment(sketch, "E3739", {"start": v(7.97, -61.76) * mm, "end": v(7.94, -61.56) * mm});
            skLineSegment(sketch, "E3740", {"start": v(7.94, -61.56) * mm, "end": v(7.92, -61.36) * mm});
            skLineSegment(sketch, "E3741", {"start": v(7.92, -61.36) * mm, "end": v(7.88, -61.15) * mm});
            skLineSegment(sketch, "E3742", {"start": v(7.88, -61.15) * mm, "end": v(7.86, -60.94) * mm});
            skLineSegment(sketch, "E3743", {"start": v(7.86, -60.94) * mm, "end": v(7.83, -60.74) * mm});
            skLineSegment(sketch, "E3744", {"start": v(7.83, -60.74) * mm, "end": v(7.8, -60.53) * mm});
            skLineSegment(sketch, "E3745", {"start": v(7.8, -60.53) * mm, "end": v(7.77, -60.33) * mm});
            skLineSegment(sketch, "E3746", {"start": v(7.77, -60.33) * mm, "end": v(7.74, -60.12) * mm});
            skLineSegment(sketch, "E3747", {"start": v(7.74, -60.12) * mm, "end": v(7.7, -59.91) * mm});
            skLineSegment(sketch, "E3748", {"start": v(7.7, -59.91) * mm, "end": v(7.68, -59.7) * mm});
            skLineSegment(sketch, "E3749", {"start": v(7.68, -59.7) * mm, "end": v(7.65, -59.56) * mm});
            skLineSegment(sketch, "E3750", {"start": v(7.65, -59.56) * mm, "end": v(7.86, -59.53) * mm});
            skLineSegment(sketch, "E3751", {"start": v(7.86, -59.53) * mm, "end": v(8.06, -59.5) * mm});
            skLineSegment(sketch, "E3752", {"start": v(8.06, -59.5) * mm, "end": v(8.26, -59.46) * mm});
            skLineSegment(sketch, "E3753", {"start": v(8.26, -59.46) * mm, "end": v(8.47, -59.43) * mm});
            skLineSegment(sketch, "E3754", {"start": v(8.47, -59.43) * mm, "end": v(8.67, -59.4) * mm});
            skLineSegment(sketch, "E3755", {"start": v(8.67, -59.4) * mm, "end": v(8.87, -59.36) * mm});
            skLineSegment(sketch, "E3756", {"start": v(8.87, -59.36) * mm, "end": v(9.08, -59.33) * mm});
            skLineSegment(sketch, "E3757", {"start": v(9.08, -59.33) * mm, "end": v(9.28, -59.3) * mm});
            skLineSegment(sketch, "E3758", {"start": v(9.28, -59.3) * mm, "end": v(9.48, -59.26) * mm});
            skLineSegment(sketch, "E3759", {"start": v(9.48, -59.26) * mm, "end": v(9.69, -59.22) * mm});
            skLineSegment(sketch, "E3760", {"start": v(9.69, -59.22) * mm, "end": v(9.89, -59.2) * mm});
            skLineSegment(sketch, "E3761", {"start": v(9.89, -59.2) * mm, "end": v(10, -59.17) * mm});
            skLineSegment(sketch, "E3762", {"start": v(10, -59.17) * mm, "end": v(10.03, -59.38) * mm});
            skLineSegment(sketch, "E3763", {"start": v(10.03, -59.38) * mm, "end": v(10.07, -59.58) * mm});
            skLineSegment(sketch, "E3764", {"start": v(10.07, -59.58) * mm, "end": v(10.1, -59.79) * mm});
            skLineSegment(sketch, "E3765", {"start": v(10.1, -59.79) * mm, "end": v(10.14, -59.99) * mm});
            skLineSegment(sketch, "E3766", {"start": v(10.14, -59.99) * mm, "end": v(10.18, -60.2) * mm});
            skLineSegment(sketch, "E3767", {"start": v(10.18, -60.2) * mm, "end": v(10.22, -60.4) * mm});
            skLineSegment(sketch, "E3768", {"start": v(10.22, -60.4) * mm, "end": v(10.26, -60.6) * mm});
            skLineSegment(sketch, "E3769", {"start": v(10.26, -60.6) * mm, "end": v(10.3, -60.8) * mm});
            skLineSegment(sketch, "E3770", {"start": v(10.3, -60.8) * mm, "end": v(10.33, -61.01) * mm});
            skLineSegment(sketch, "E3771", {"start": v(10.33, -61.01) * mm, "end": v(10.37, -61.22) * mm});
            skLineSegment(sketch, "E3772", {"start": v(10.37, -61.22) * mm, "end": v(10.4, -61.42) * mm});
            skLineSegment(sketch, "E3773", {"start": v(10.4, -61.42) * mm, "end": v(10.45, -61.63) * mm});
            skLineSegment(sketch, "E3774", {"start": v(10.45, -61.63) * mm, "end": v(10.5, -61.84) * mm});
            skLineSegment(sketch, "E3775", {"start": v(10.5, -61.84) * mm, "end": v(10.57, -62.04) * mm});
            skLineSegment(sketch, "E3776", {"start": v(10.57, -62.04) * mm, "end": v(10.7, -62.22) * mm});
            skLineSegment(sketch, "E3777", {"start": v(10.7, -62.22) * mm, "end": v(10.86, -62.35) * mm});
            skLineSegment(sketch, "E3778", {"start": v(10.86, -62.35) * mm, "end": v(11.06, -62.43) * mm});
            skLineSegment(sketch, "E3779", {"start": v(11.06, -62.43) * mm, "end": v(11.27, -62.47) * mm});
            skLineSegment(sketch, "E3780", {"start": v(11.27, -62.47) * mm, "end": v(11.49, -62.44) * mm});
            skLineSegment(sketch, "E3781", {"start": v(11.49, -62.44) * mm, "end": v(11.69, -62.36) * mm});
            skLineSegment(sketch, "E3782", {"start": v(11.69, -62.36) * mm, "end": v(11.86, -62.23) * mm});
            skLineSegment(sketch, "E3783", {"start": v(11.86, -62.23) * mm, "end": v(12, -62.06) * mm});
            skLineSegment(sketch, "E3784", {"start": v(12, -62.06) * mm, "end": v(12.07, -61.87) * mm});
            skLineSegment(sketch, "E3785", {"start": v(12.07, -61.87) * mm, "end": v(12.1, -61.65) * mm});
            skLineSegment(sketch, "E3786", {"start": v(12.1, -61.65) * mm, "end": v(12.08, -61.45) * mm});
            skLineSegment(sketch, "E3787", {"start": v(12.08, -61.45) * mm, "end": v(12.04, -61.25) * mm});
            skLineSegment(sketch, "E3788", {"start": v(12.04, -61.25) * mm, "end": v(12, -61.05) * mm});
            skLineSegment(sketch, "E3789", {"start": v(12, -61.05) * mm, "end": v(11.95, -60.84) * mm});
            skLineSegment(sketch, "E3790", {"start": v(11.95, -60.84) * mm, "end": v(11.9, -60.64) * mm});
            skLineSegment(sketch, "E3791", {"start": v(11.9, -60.64) * mm, "end": v(11.86, -60.44) * mm});
            skLineSegment(sketch, "E3792", {"start": v(11.86, -60.44) * mm, "end": v(11.82, -60.23) * mm});
            skLineSegment(sketch, "E3793", {"start": v(11.82, -60.23) * mm, "end": v(11.78, -60.03) * mm});
            skLineSegment(sketch, "E3794", {"start": v(11.78, -60.03) * mm, "end": v(11.74, -59.83) * mm});
            skLineSegment(sketch, "E3795", {"start": v(11.74, -59.83) * mm, "end": v(11.7, -59.62) * mm});
            skLineSegment(sketch, "E3796", {"start": v(11.7, -59.62) * mm, "end": v(11.65, -59.42) * mm});
            skLineSegment(sketch, "E3797", {"start": v(11.65, -59.42) * mm, "end": v(11.6, -59.22) * mm});
            skLineSegment(sketch, "E3798", {"start": v(11.6, -59.22) * mm, "end": v(11.56, -59.02) * mm});
            skLineSegment(sketch, "E3799", {"start": v(11.56, -59.02) * mm, "end": v(11.53, -58.87) * mm});
            skLineSegment(sketch, "E3800", {"start": v(11.53, -58.87) * mm, "end": v(11.73, -58.82) * mm});
            skLineSegment(sketch, "E3801", {"start": v(11.73, -58.82) * mm, "end": v(11.93, -58.77) * mm});
            skLineSegment(sketch, "E3802", {"start": v(11.93, -58.77) * mm, "end": v(12.13, -58.73) * mm});
            skLineSegment(sketch, "E3803", {"start": v(12.13, -58.73) * mm, "end": v(12.33, -58.68) * mm});
            skLineSegment(sketch, "E3804", {"start": v(12.33, -58.68) * mm, "end": v(12.53, -58.63) * mm});
            skLineSegment(sketch, "E3805", {"start": v(12.53, -58.63) * mm, "end": v(12.73, -58.59) * mm});
            skLineSegment(sketch, "E3806", {"start": v(12.73, -58.59) * mm, "end": v(12.94, -58.54) * mm});
            skLineSegment(sketch, "E3807", {"start": v(12.94, -58.54) * mm, "end": v(13.14, -58.5) * mm});
            skLineSegment(sketch, "E3808", {"start": v(13.14, -58.5) * mm, "end": v(13.34, -58.45) * mm});
            skLineSegment(sketch, "E3809", {"start": v(13.34, -58.45) * mm, "end": v(13.54, -58.4) * mm});
            skLineSegment(sketch, "E3810", {"start": v(13.54, -58.4) * mm, "end": v(13.74, -58.35) * mm});
            skLineSegment(sketch, "E3811", {"start": v(13.74, -58.35) * mm, "end": v(13.84, -58.33) * mm});
            skLineSegment(sketch, "E3812", {"start": v(13.84, -58.33) * mm, "end": v(13.9, -58.53) * mm});
            skLineSegment(sketch, "E3813", {"start": v(13.9, -58.53) * mm, "end": v(13.94, -58.73) * mm});
            skLineSegment(sketch, "E3814", {"start": v(13.94, -58.73) * mm, "end": v(14, -58.93) * mm});
            skLineSegment(sketch, "E3815", {"start": v(14, -58.93) * mm, "end": v(14.04, -59.13) * mm});
            skLineSegment(sketch, "E3816", {"start": v(14.04, -59.13) * mm, "end": v(14.1, -59.33) * mm});
            skLineSegment(sketch, "E3817", {"start": v(14.1, -59.33) * mm, "end": v(14.15, -59.54) * mm});
            skLineSegment(sketch, "E3818", {"start": v(14.15, -59.54) * mm, "end": v(14.2, -59.74) * mm});
            skLineSegment(sketch, "E3819", {"start": v(14.2, -59.74) * mm, "end": v(14.25, -59.94) * mm});
            skLineSegment(sketch, "E3820", {"start": v(14.25, -59.94) * mm, "end": v(14.3, -60.14) * mm});
            skLineSegment(sketch, "E3821", {"start": v(14.3, -60.14) * mm, "end": v(14.35, -60.34) * mm});
            skLineSegment(sketch, "E3822", {"start": v(14.35, -60.34) * mm, "end": v(14.4, -60.54) * mm});
            skLineSegment(sketch, "E3823", {"start": v(14.4, -60.54) * mm, "end": v(14.45, -60.75) * mm});
            skLineSegment(sketch, "E3824", {"start": v(14.45, -60.75) * mm, "end": v(14.51, -60.96) * mm});
            skLineSegment(sketch, "E3825", {"start": v(14.51, -60.96) * mm, "end": v(14.6, -61.16) * mm});
            skLineSegment(sketch, "E3826", {"start": v(14.6, -61.16) * mm, "end": v(14.74, -61.32) * mm});
            skLineSegment(sketch, "E3827", {"start": v(14.74, -61.32) * mm, "end": v(14.92, -61.44) * mm});
            skLineSegment(sketch, "E3828", {"start": v(14.92, -61.44) * mm, "end": v(15.12, -61.51) * mm});
            skLineSegment(sketch, "E3829", {"start": v(15.12, -61.51) * mm, "end": v(15.33, -61.53) * mm});
            skLineSegment(sketch, "E3830", {"start": v(15.33, -61.53) * mm, "end": v(15.54, -61.5) * mm});
            skLineSegment(sketch, "E3831", {"start": v(15.54, -61.5) * mm, "end": v(15.74, -61.4) * mm});
            skLineSegment(sketch, "E3832", {"start": v(15.74, -61.4) * mm, "end": v(15.9, -61.26) * mm});
            skLineSegment(sketch, "E3833", {"start": v(15.9, -61.26) * mm, "end": v(16.02, -61.08) * mm});
            skLineSegment(sketch, "E3834", {"start": v(16.02, -61.08) * mm, "end": v(16.1, -60.88) * mm});
            skLineSegment(sketch, "E3835", {"start": v(16.1, -60.88) * mm, "end": v(16.1, -60.67) * mm});
            skLineSegment(sketch, "E3836", {"start": v(16.1, -60.67) * mm, "end": v(16.07, -60.46) * mm});
            skLineSegment(sketch, "E3837", {"start": v(16.07, -60.46) * mm, "end": v(16.01, -60.26) * mm});
            skLineSegment(sketch, "E3838", {"start": v(16.01, -60.26) * mm, "end": v(15.96, -60.07) * mm});
            skLineSegment(sketch, "E3839", {"start": v(15.96, -60.07) * mm, "end": v(15.9, -59.87) * mm});
            skLineSegment(sketch, "E3840", {"start": v(15.9, -59.87) * mm, "end": v(15.85, -59.67) * mm});
            skLineSegment(sketch, "E3841", {"start": v(15.85, -59.67) * mm, "end": v(15.8, -59.47) * mm});
            skLineSegment(sketch, "E3842", {"start": v(15.8, -59.47) * mm, "end": v(15.73, -59.27) * mm});
            skLineSegment(sketch, "E3843", {"start": v(15.73, -59.27) * mm, "end": v(15.68, -59.07) * mm});
            skLineSegment(sketch, "E3844", {"start": v(15.68, -59.07) * mm, "end": v(15.62, -58.87) * mm});
            skLineSegment(sketch, "E3845", {"start": v(15.62, -58.87) * mm, "end": v(15.56, -58.67) * mm});
            skLineSegment(sketch, "E3846", {"start": v(15.56, -58.67) * mm, "end": v(15.5, -58.47) * mm});
            skLineSegment(sketch, "E3847", {"start": v(15.5, -58.47) * mm, "end": v(15.45, -58.27) * mm});
            skLineSegment(sketch, "E3848", {"start": v(15.45, -58.27) * mm, "end": v(15.4, -58.07) * mm});
            skLineSegment(sketch, "E3849", {"start": v(15.4, -58.07) * mm, "end": v(15.35, -57.92) * mm});
            skLineSegment(sketch, "E3850", {"start": v(15.35, -57.92) * mm, "end": v(15.55, -57.86) * mm});
            skLineSegment(sketch, "E3851", {"start": v(15.55, -57.86) * mm, "end": v(15.75, -57.8) * mm});
            skLineSegment(sketch, "E3852", {"start": v(15.75, -57.8) * mm, "end": v(15.95, -57.74) * mm});
            skLineSegment(sketch, "E3853", {"start": v(15.95, -57.74) * mm, "end": v(16.14, -57.68) * mm});
            skLineSegment(sketch, "E3854", {"start": v(16.14, -57.68) * mm, "end": v(16.34, -57.62) * mm});
            skLineSegment(sketch, "E3855", {"start": v(16.34, -57.62) * mm, "end": v(16.54, -57.57) * mm});
            skLineSegment(sketch, "E3856", {"start": v(16.54, -57.57) * mm, "end": v(16.73, -57.5) * mm});
            skLineSegment(sketch, "E3857", {"start": v(16.73, -57.5) * mm, "end": v(16.93, -57.45) * mm});
            skLineSegment(sketch, "E3858", {"start": v(16.93, -57.45) * mm, "end": v(17.13, -57.39) * mm});
            skLineSegment(sketch, "E3859", {"start": v(17.13, -57.39) * mm, "end": v(17.33, -57.33) * mm});
            skLineSegment(sketch, "E3860", {"start": v(17.33, -57.33) * mm, "end": v(17.52, -57.27) * mm});
            skLineSegment(sketch, "E3861", {"start": v(17.52, -57.27) * mm, "end": v(17.62, -57.24) * mm});
            skLineSegment(sketch, "E3862", {"start": v(17.62, -57.24) * mm, "end": v(17.69, -57.43) * mm});
            skLineSegment(sketch, "E3863", {"start": v(17.69, -57.43) * mm, "end": v(17.75, -57.63) * mm});
            skLineSegment(sketch, "E3864", {"start": v(17.75, -57.63) * mm, "end": v(17.82, -57.83) * mm});
            skLineSegment(sketch, "E3865", {"start": v(17.82, -57.83) * mm, "end": v(17.88, -58.02) * mm});
            skLineSegment(sketch, "E3866", {"start": v(17.88, -58.02) * mm, "end": v(17.94, -58.22) * mm});
            skLineSegment(sketch, "E3867", {"start": v(17.94, -58.22) * mm, "end": v(18, -58.42) * mm});
            skLineSegment(sketch, "E3868", {"start": v(18, -58.42) * mm, "end": v(18.07, -58.62) * mm});
            skLineSegment(sketch, "E3869", {"start": v(18.07, -58.62) * mm, "end": v(18.14, -58.81) * mm});
            skLineSegment(sketch, "E3870", {"start": v(18.14, -58.81) * mm, "end": v(18.2, -59.01) * mm});
            skLineSegment(sketch, "E3871", {"start": v(18.2, -59.01) * mm, "end": v(18.27, -59.21) * mm});
            skLineSegment(sketch, "E3872", {"start": v(18.27, -59.21) * mm, "end": v(18.33, -59.4) * mm});
            skLineSegment(sketch, "E3873", {"start": v(18.33, -59.4) * mm, "end": v(18.4, -59.6) * mm});
            skLineSegment(sketch, "E3874", {"start": v(18.4, -59.6) * mm, "end": v(18.46, -59.82) * mm});
            skLineSegment(sketch, "E3875", {"start": v(18.46, -59.82) * mm, "end": v(18.57, -60) * mm});
            skLineSegment(sketch, "E3876", {"start": v(18.57, -60) * mm, "end": v(18.72, -60.16) * mm});
            skLineSegment(sketch, "E3877", {"start": v(18.72, -60.16) * mm, "end": v(18.9, -60.27) * mm});
            skLineSegment(sketch, "E3878", {"start": v(18.9, -60.27) * mm, "end": v(19.1, -60.33) * mm});
            skLineSegment(sketch, "E3879", {"start": v(19.1, -60.33) * mm, "end": v(19.32, -60.33) * mm});
            skLineSegment(sketch, "E3880", {"start": v(19.32, -60.33) * mm, "end": v(19.53, -60.28) * mm});
            skLineSegment(sketch, "E3881", {"start": v(19.53, -60.28) * mm, "end": v(19.72, -60.17) * mm});
            skLineSegment(sketch, "E3882", {"start": v(19.72, -60.17) * mm, "end": v(19.87, -60.02) * mm});
            skLineSegment(sketch, "E3883", {"start": v(19.87, -60.02) * mm, "end": v(19.98, -59.84) * mm});
            skLineSegment(sketch, "E3884", {"start": v(19.98, -59.84) * mm, "end": v(20.04, -59.63) * mm});
            skLineSegment(sketch, "E3885", {"start": v(20.04, -59.63) * mm, "end": v(20.04, -59.42) * mm});
            skLineSegment(sketch, "E3886", {"start": v(20.04, -59.42) * mm, "end": v(19.98, -59.22) * mm});
            skLineSegment(sketch, "E3887", {"start": v(19.98, -59.22) * mm, "end": v(19.92, -59.02) * mm});
            skLineSegment(sketch, "E3888", {"start": v(19.92, -59.02) * mm, "end": v(19.85, -58.83) * mm});
            skLineSegment(sketch, "E3889", {"start": v(19.85, -58.83) * mm, "end": v(19.78, -58.64) * mm});
            skLineSegment(sketch, "E3890", {"start": v(19.78, -58.64) * mm, "end": v(19.71, -58.44) * mm});
            skLineSegment(sketch, "E3891", {"start": v(19.71, -58.44) * mm, "end": v(19.64, -58.24) * mm});
            skLineSegment(sketch, "E3892", {"start": v(19.64, -58.24) * mm, "end": v(19.57, -58.05) * mm});
            skLineSegment(sketch, "E3893", {"start": v(19.57, -58.05) * mm, "end": v(19.5, -57.85) * mm});
            skLineSegment(sketch, "E3894", {"start": v(19.5, -57.85) * mm, "end": v(19.44, -57.66) * mm});
            skLineSegment(sketch, "E3895", {"start": v(19.44, -57.66) * mm, "end": v(19.37, -57.46) * mm});
            skLineSegment(sketch, "E3896", {"start": v(19.37, -57.46) * mm, "end": v(19.3, -57.27) * mm});
            skLineSegment(sketch, "E3897", {"start": v(19.3, -57.27) * mm, "end": v(19.23, -57.07) * mm});
            skLineSegment(sketch, "E3898", {"start": v(19.23, -57.07) * mm, "end": v(19.16, -56.87) * mm});
            skLineSegment(sketch, "E3899", {"start": v(19.16, -56.87) * mm, "end": v(19.1, -56.73) * mm});
            skLineSegment(sketch, "E3900", {"start": v(19.1, -56.73) * mm, "end": v(19.3, -56.66) * mm});
            skLineSegment(sketch, "E3901", {"start": v(19.3, -56.66) * mm, "end": v(19.5, -56.59) * mm});
            skLineSegment(sketch, "E3902", {"start": v(19.5, -56.59) * mm, "end": v(19.69, -56.51) * mm});
            skLineSegment(sketch, "E3903", {"start": v(19.69, -56.51) * mm, "end": v(19.88, -56.44) * mm});
            skLineSegment(sketch, "E3904", {"start": v(19.88, -56.44) * mm, "end": v(20.07, -56.37) * mm});
            skLineSegment(sketch, "E3905", {"start": v(20.07, -56.37) * mm, "end": v(20.26, -56.3) * mm});
            skLineSegment(sketch, "E3906", {"start": v(20.26, -56.3) * mm, "end": v(20.46, -56.22) * mm});
            skLineSegment(sketch, "E3907", {"start": v(20.46, -56.22) * mm, "end": v(20.65, -56.15) * mm});
            skLineSegment(sketch, "E3908", {"start": v(20.65, -56.15) * mm, "end": v(20.84, -56.08) * mm});
            skLineSegment(sketch, "E3909", {"start": v(20.84, -56.08) * mm, "end": v(21.04, -56) * mm});
            skLineSegment(sketch, "E3910", {"start": v(21.04, -56) * mm, "end": v(21.23, -55.93) * mm});
            skLineSegment(sketch, "E3911", {"start": v(21.23, -55.93) * mm, "end": v(21.33, -55.9) * mm});
            skLineSegment(sketch, "E3912", {"start": v(21.33, -55.9) * mm, "end": v(21.4, -56.09) * mm});
            skLineSegment(sketch, "E3913", {"start": v(21.4, -56.09) * mm, "end": v(21.48, -56.28) * mm});
            skLineSegment(sketch, "E3914", {"start": v(21.48, -56.28) * mm, "end": v(21.56, -56.48) * mm});
            skLineSegment(sketch, "E3915", {"start": v(21.56, -56.48) * mm, "end": v(21.63, -56.67) * mm});
            skLineSegment(sketch, "E3916", {"start": v(21.63, -56.67) * mm, "end": v(21.71, -56.86) * mm});
            skLineSegment(sketch, "E3917", {"start": v(21.71, -56.86) * mm, "end": v(21.79, -57.05) * mm});
            skLineSegment(sketch, "E3918", {"start": v(21.79, -57.05) * mm, "end": v(21.87, -57.25) * mm});
            skLineSegment(sketch, "E3919", {"start": v(21.87, -57.25) * mm, "end": v(21.94, -57.44) * mm});
            skLineSegment(sketch, "E3920", {"start": v(21.94, -57.44) * mm, "end": v(22.02, -57.63) * mm});
            skLineSegment(sketch, "E3921", {"start": v(22.02, -57.63) * mm, "end": v(22.1, -57.83) * mm});
            skLineSegment(sketch, "E3922", {"start": v(22.1, -57.83) * mm, "end": v(22.17, -58.02) * mm});
            skLineSegment(sketch, "E3923", {"start": v(22.17, -58.02) * mm, "end": v(22.25, -58.21) * mm});
            skLineSegment(sketch, "E3924", {"start": v(22.25, -58.21) * mm, "end": v(22.33, -58.42) * mm});
            skLineSegment(sketch, "E3925", {"start": v(22.33, -58.42) * mm, "end": v(22.45, -58.6) * mm});
            skLineSegment(sketch, "E3926", {"start": v(22.45, -58.6) * mm, "end": v(22.6, -58.74) * mm});
            skLineSegment(sketch, "E3927", {"start": v(22.6, -58.74) * mm, "end": v(22.8, -58.84) * mm});
            skLineSegment(sketch, "E3928", {"start": v(22.8, -58.84) * mm, "end": v(23.01, -58.89) * mm});
            skLineSegment(sketch, "E3929", {"start": v(23.01, -58.89) * mm, "end": v(23.22, -58.87) * mm});
            skLineSegment(sketch, "E3930", {"start": v(23.22, -58.87) * mm, "end": v(23.43, -58.8) * mm});
            skLineSegment(sketch, "E3931", {"start": v(23.43, -58.8) * mm, "end": v(23.6, -58.7) * mm});
            skLineSegment(sketch, "E3932", {"start": v(23.6, -58.7) * mm, "end": v(23.75, -58.53) * mm});
            skLineSegment(sketch, "E3933", {"start": v(23.75, -58.53) * mm, "end": v(23.85, -58.34) * mm});
            skLineSegment(sketch, "E3934", {"start": v(23.85, -58.34) * mm, "end": v(23.9, -58.13) * mm});
            skLineSegment(sketch, "E3935", {"start": v(23.9, -58.13) * mm, "end": v(23.88, -57.92) * mm});
            skLineSegment(sketch, "E3936", {"start": v(23.88, -57.92) * mm, "end": v(23.81, -57.72) * mm});
            skLineSegment(sketch, "E3937", {"start": v(23.81, -57.72) * mm, "end": v(23.74, -57.53) * mm});
            skLineSegment(sketch, "E3938", {"start": v(23.74, -57.53) * mm, "end": v(23.65, -57.34) * mm});
            skLineSegment(sketch, "E3939", {"start": v(23.65, -57.34) * mm, "end": v(23.57, -57.15) * mm});
            skLineSegment(sketch, "E3940", {"start": v(23.57, -57.15) * mm, "end": v(23.5, -56.96) * mm});
            skLineSegment(sketch, "E3941", {"start": v(23.5, -56.96) * mm, "end": v(23.4, -56.77) * mm});
            skLineSegment(sketch, "E3942", {"start": v(23.4, -56.77) * mm, "end": v(23.33, -56.58) * mm});
            skLineSegment(sketch, "E3943", {"start": v(23.33, -56.58) * mm, "end": v(23.25, -56.4) * mm});
            skLineSegment(sketch, "E3944", {"start": v(23.25, -56.4) * mm, "end": v(23.16, -56.2) * mm});
            skLineSegment(sketch, "E3945", {"start": v(23.16, -56.2) * mm, "end": v(23.08, -56) * mm});
            skLineSegment(sketch, "E3946", {"start": v(23.08, -56) * mm, "end": v(23, -55.82) * mm});
            skLineSegment(sketch, "E3947", {"start": v(23, -55.82) * mm, "end": v(22.92, -55.62) * mm});
            skLineSegment(sketch, "E3948", {"start": v(22.92, -55.62) * mm, "end": v(22.84, -55.43) * mm});
            skLineSegment(sketch, "E3949", {"start": v(22.84, -55.43) * mm, "end": v(22.78, -55.3) * mm});
            skLineSegment(sketch, "E3950", {"start": v(22.78, -55.3) * mm, "end": v(22.96, -55.21) * mm});
            skLineSegment(sketch, "E3951", {"start": v(22.96, -55.21) * mm, "end": v(23.15, -55.13) * mm});
            skLineSegment(sketch, "E3952", {"start": v(23.15, -55.13) * mm, "end": v(23.34, -55.04) * mm});
            skLineSegment(sketch, "E3953", {"start": v(23.34, -55.04) * mm, "end": v(23.53, -54.96) * mm});
            skLineSegment(sketch, "E3954", {"start": v(23.53, -54.96) * mm, "end": v(23.71, -54.87) * mm});
            skLineSegment(sketch, "E3955", {"start": v(23.71, -54.87) * mm, "end": v(23.9, -54.79) * mm});
            skLineSegment(sketch, "E3956", {"start": v(23.9, -54.79) * mm, "end": v(24.09, -54.7) * mm});
            skLineSegment(sketch, "E3957", {"start": v(24.09, -54.7) * mm, "end": v(24.28, -54.62) * mm});
            skLineSegment(sketch, "E3958", {"start": v(24.28, -54.62) * mm, "end": v(24.46, -54.53) * mm});
            skLineSegment(sketch, "E3959", {"start": v(24.46, -54.53) * mm, "end": v(24.65, -54.45) * mm});
            skLineSegment(sketch, "E3960", {"start": v(24.65, -54.45) * mm, "end": v(24.84, -54.36) * mm});
            skLineSegment(sketch, "E3961", {"start": v(24.84, -54.36) * mm, "end": v(24.94, -54.32) * mm});
            skLineSegment(sketch, "E3962", {"start": v(24.94, -54.32) * mm, "end": v(25.02, -54.5) * mm});
            skLineSegment(sketch, "E3963", {"start": v(25.02, -54.5) * mm, "end": v(25.11, -54.69) * mm});
            skLineSegment(sketch, "E3964", {"start": v(25.11, -54.69) * mm, "end": v(25.2, -54.88) * mm});
            skLineSegment(sketch, "E3965", {"start": v(25.2, -54.88) * mm, "end": v(25.3, -55.07) * mm});
            skLineSegment(sketch, "E3966", {"start": v(25.3, -55.07) * mm, "end": v(25.38, -55.25) * mm});
            skLineSegment(sketch, "E3967", {"start": v(25.38, -55.25) * mm, "end": v(25.47, -55.44) * mm});
            skLineSegment(sketch, "E3968", {"start": v(25.47, -55.44) * mm, "end": v(25.56, -55.63) * mm});
            skLineSegment(sketch, "E3969", {"start": v(25.56, -55.63) * mm, "end": v(25.65, -55.82) * mm});
            skLineSegment(sketch, "E3970", {"start": v(25.65, -55.82) * mm, "end": v(25.74, -56) * mm});
            skLineSegment(sketch, "E3971", {"start": v(25.74, -56) * mm, "end": v(25.83, -56.2) * mm});
            skLineSegment(sketch, "E3972", {"start": v(25.83, -56.2) * mm, "end": v(25.92, -56.38) * mm});
            skLineSegment(sketch, "E3973", {"start": v(25.92, -56.38) * mm, "end": v(26, -56.57) * mm});
            skLineSegment(sketch, "E3974", {"start": v(26, -56.57) * mm, "end": v(26.1, -56.77) * mm});
            skLineSegment(sketch, "E3975", {"start": v(26.1, -56.77) * mm, "end": v(26.23, -56.94) * mm});
            skLineSegment(sketch, "E3976", {"start": v(26.23, -56.94) * mm, "end": v(26.4, -57.07) * mm});
            skLineSegment(sketch, "E3977", {"start": v(26.4, -57.07) * mm, "end": v(26.6, -57.16) * mm});
            skLineSegment(sketch, "E3978", {"start": v(26.6, -57.16) * mm, "end": v(26.8, -57.2) * mm});
            skLineSegment(sketch, "E3979", {"start": v(26.8, -57.2) * mm, "end": v(27.02, -57.17) * mm});
            skLineSegment(sketch, "E3980", {"start": v(27.02, -57.17) * mm, "end": v(27.22, -57.09) * mm});
            skLineSegment(sketch, "E3981", {"start": v(27.22, -57.09) * mm, "end": v(27.4, -56.96) * mm});
            skLineSegment(sketch, "E3982", {"start": v(27.4, -56.96) * mm, "end": v(27.53, -56.79) * mm});
            skLineSegment(sketch, "E3983", {"start": v(27.53, -56.79) * mm, "end": v(27.61, -56.6) * mm});
            skLineSegment(sketch, "E3984", {"start": v(27.61, -56.6) * mm, "end": v(27.64, -56.38) * mm});
            skLineSegment(sketch, "E3985", {"start": v(27.64, -56.38) * mm, "end": v(27.61, -56.17) * mm});
            skLineSegment(sketch, "E3986", {"start": v(27.61, -56.17) * mm, "end": v(27.54, -55.98) * mm});
            skLineSegment(sketch, "E3987", {"start": v(27.54, -55.98) * mm, "end": v(27.44, -55.8) * mm});
            skLineSegment(sketch, "E3988", {"start": v(27.44, -55.8) * mm, "end": v(27.35, -55.6) * mm});
            skLineSegment(sketch, "E3989", {"start": v(27.35, -55.6) * mm, "end": v(27.26, -55.43) * mm});
            skLineSegment(sketch, "E3990", {"start": v(27.26, -55.43) * mm, "end": v(27.17, -55.24) * mm});
            skLineSegment(sketch, "E3991", {"start": v(27.17, -55.24) * mm, "end": v(27.07, -55.05) * mm});
            skLineSegment(sketch, "E3992", {"start": v(27.07, -55.05) * mm, "end": v(26.98, -54.87) * mm});
            skLineSegment(sketch, "E3993", {"start": v(26.98, -54.87) * mm, "end": v(26.88, -54.69) * mm});
            skLineSegment(sketch, "E3994", {"start": v(26.88, -54.69) * mm, "end": v(26.79, -54.5) * mm});
            skLineSegment(sketch, "E3995", {"start": v(26.79, -54.5) * mm, "end": v(26.7, -54.31) * mm});
            skLineSegment(sketch, "E3996", {"start": v(26.7, -54.31) * mm, "end": v(26.6, -54.13) * mm});
            skLineSegment(sketch, "E3997", {"start": v(26.6, -54.13) * mm, "end": v(26.5, -53.94) * mm});
            skLineSegment(sketch, "E3998", {"start": v(26.5, -53.94) * mm, "end": v(26.4, -53.76) * mm});
            skLineSegment(sketch, "E3999", {"start": v(26.4, -53.76) * mm, "end": v(26.34, -53.62) * mm});
            skLineSegment(sketch, "E4000", {"start": v(26.34, -53.62) * mm, "end": v(26.52, -53.53) * mm});
            skLineSegment(sketch, "E4001", {"start": v(26.52, -53.53) * mm, "end": v(26.7, -53.43) * mm});
            skLineSegment(sketch, "E4002", {"start": v(26.7, -53.43) * mm, "end": v(26.89, -53.33) * mm});
            skLineSegment(sketch, "E4003", {"start": v(26.89, -53.33) * mm, "end": v(27.07, -53.24) * mm});
            skLineSegment(sketch, "E4004", {"start": v(27.07, -53.24) * mm, "end": v(27.25, -53.14) * mm});
            skLineSegment(sketch, "E4005", {"start": v(27.25, -53.14) * mm, "end": v(27.43, -53.04) * mm});
            skLineSegment(sketch, "E4006", {"start": v(27.43, -53.04) * mm, "end": v(27.61, -52.95) * mm});
            skLineSegment(sketch, "E4007", {"start": v(27.61, -52.95) * mm, "end": v(27.8, -52.85) * mm});
            skLineSegment(sketch, "E4008", {"start": v(27.8, -52.85) * mm, "end": v(27.98, -52.75) * mm});
            skLineSegment(sketch, "E4009", {"start": v(27.98, -52.75) * mm, "end": v(28.16, -52.65) * mm});
            skLineSegment(sketch, "E4010", {"start": v(28.16, -52.65) * mm, "end": v(28.34, -52.56) * mm});
            skLineSegment(sketch, "E4011", {"start": v(28.34, -52.56) * mm, "end": v(28.43, -52.5) * mm});
            skLineSegment(sketch, "E4012", {"start": v(28.43, -52.5) * mm, "end": v(28.53, -52.69) * mm});
            skLineSegment(sketch, "E4013", {"start": v(28.53, -52.69) * mm, "end": v(28.63, -52.87) * mm});
            skLineSegment(sketch, "E4014", {"start": v(28.63, -52.87) * mm, "end": v(28.74, -53.05) * mm});
            skLineSegment(sketch, "E4015", {"start": v(28.74, -53.05) * mm, "end": v(28.84, -53.23) * mm});
            skLineSegment(sketch, "E4016", {"start": v(28.84, -53.23) * mm, "end": v(28.94, -53.41) * mm});
            skLineSegment(sketch, "E4017", {"start": v(28.94, -53.41) * mm, "end": v(29.04, -53.6) * mm});
            skLineSegment(sketch, "E4018", {"start": v(29.04, -53.6) * mm, "end": v(29.14, -53.77) * mm});
            skLineSegment(sketch, "E4019", {"start": v(29.14, -53.77) * mm, "end": v(29.24, -53.95) * mm});
            skLineSegment(sketch, "E4020", {"start": v(29.24, -53.95) * mm, "end": v(29.35, -54.14) * mm});
            skLineSegment(sketch, "E4021", {"start": v(29.35, -54.14) * mm, "end": v(29.45, -54.32) * mm});
            skLineSegment(sketch, "E4022", {"start": v(29.45, -54.32) * mm, "end": v(29.55, -54.5) * mm});
            skLineSegment(sketch, "E4023", {"start": v(29.55, -54.5) * mm, "end": v(29.65, -54.68) * mm});
            skLineSegment(sketch, "E4024", {"start": v(29.65, -54.68) * mm, "end": v(29.76, -54.88) * mm});
            skLineSegment(sketch, "E4025", {"start": v(29.76, -54.88) * mm, "end": v(29.9, -55.04) * mm});
            skLineSegment(sketch, "E4026", {"start": v(29.9, -55.04) * mm, "end": v(30.07, -55.16) * mm});
            skLineSegment(sketch, "E4027", {"start": v(30.07, -55.16) * mm, "end": v(30.28, -55.23) * mm});
            skLineSegment(sketch, "E4028", {"start": v(30.28, -55.23) * mm, "end": v(30.5, -55.25) * mm});
            skLineSegment(sketch, "E4029", {"start": v(30.5, -55.25) * mm, "end": v(30.7, -55.21) * mm});
            skLineSegment(sketch, "E4030", {"start": v(30.7, -55.21) * mm, "end": v(30.9, -55.12) * mm});
            skLineSegment(sketch, "E4031", {"start": v(30.9, -55.12) * mm, "end": v(31.06, -54.98) * mm});
            skLineSegment(sketch, "E4032", {"start": v(31.06, -54.98) * mm, "end": v(31.18, -54.8) * mm});
            skLineSegment(sketch, "E4033", {"start": v(31.18, -54.8) * mm, "end": v(31.25, -54.6) * mm});
            skLineSegment(sketch, "E4034", {"start": v(31.25, -54.6) * mm, "end": v(31.27, -54.39) * mm});
            skLineSegment(sketch, "E4035", {"start": v(31.27, -54.39) * mm, "end": v(31.23, -54.18) * mm});
            skLineSegment(sketch, "E4036", {"start": v(31.23, -54.18) * mm, "end": v(31.14, -54) * mm});
            skLineSegment(sketch, "E4037", {"start": v(31.14, -54) * mm, "end": v(31.03, -53.81) * mm});
            skLineSegment(sketch, "E4038", {"start": v(31.03, -53.81) * mm, "end": v(30.93, -53.64) * mm});
            skLineSegment(sketch, "E4039", {"start": v(30.93, -53.64) * mm, "end": v(30.82, -53.46) * mm});
            skLineSegment(sketch, "E4040", {"start": v(30.82, -53.46) * mm, "end": v(30.72, -53.28) * mm});
            skLineSegment(sketch, "E4041", {"start": v(30.72, -53.28) * mm, "end": v(30.6, -53.1) * mm});
            skLineSegment(sketch, "E4042", {"start": v(30.6, -53.1) * mm, "end": v(30.5, -52.92) * mm});
            skLineSegment(sketch, "E4043", {"start": v(30.5, -52.92) * mm, "end": v(30.4, -52.75) * mm});
            skLineSegment(sketch, "E4044", {"start": v(30.4, -52.75) * mm, "end": v(30.3, -52.57) * mm});
            skLineSegment(sketch, "E4045", {"start": v(30.3, -52.57) * mm, "end": v(30.19, -52.39) * mm});
            skLineSegment(sketch, "E4046", {"start": v(30.19, -52.39) * mm, "end": v(30.08, -52.21) * mm});
            skLineSegment(sketch, "E4047", {"start": v(30.08, -52.21) * mm, "end": v(29.97, -52.03) * mm});
            skLineSegment(sketch, "E4048", {"start": v(29.97, -52.03) * mm, "end": v(29.87, -51.85) * mm});
            skLineSegment(sketch, "E4049", {"start": v(29.87, -51.85) * mm, "end": v(29.8, -51.72) * mm});
            skLineSegment(sketch, "E4050", {"start": v(29.8, -51.72) * mm, "end": v(29.96, -51.61) * mm});
            skLineSegment(sketch, "E4051", {"start": v(29.96, -51.61) * mm, "end": v(30.14, -51.5) * mm});
            skLineSegment(sketch, "E4052", {"start": v(30.14, -51.5) * mm, "end": v(30.31, -51.4) * mm});
            skLineSegment(sketch, "E4053", {"start": v(30.31, -51.4) * mm, "end": v(30.49, -51.29) * mm});
            skLineSegment(sketch, "E4054", {"start": v(30.49, -51.29) * mm, "end": v(30.66, -51.18) * mm});
            skLineSegment(sketch, "E4055", {"start": v(30.66, -51.18) * mm, "end": v(30.84, -51.07) * mm});
            skLineSegment(sketch, "E4056", {"start": v(30.84, -51.07) * mm, "end": v(31.01, -50.96) * mm});
            skLineSegment(sketch, "E4057", {"start": v(31.01, -50.96) * mm, "end": v(31.19, -50.85) * mm});
            skLineSegment(sketch, "E4058", {"start": v(31.19, -50.85) * mm, "end": v(31.36, -50.74) * mm});
            skLineSegment(sketch, "E4059", {"start": v(31.36, -50.74) * mm, "end": v(31.54, -50.64) * mm});
            skLineSegment(sketch, "E4060", {"start": v(31.54, -50.64) * mm, "end": v(31.71, -50.53) * mm});
            skLineSegment(sketch, "E4061", {"start": v(31.71, -50.53) * mm, "end": v(31.8, -50.47) * mm});
            skLineSegment(sketch, "E4062", {"start": v(31.8, -50.47) * mm, "end": v(31.92, -50.64) * mm});
            skLineSegment(sketch, "E4063", {"start": v(31.92, -50.64) * mm, "end": v(32.03, -50.82) * mm});
            skLineSegment(sketch, "E4064", {"start": v(32.03, -50.82) * mm, "end": v(32.14, -51) * mm});
            skLineSegment(sketch, "E4065", {"start": v(32.14, -51) * mm, "end": v(32.26, -51.17) * mm});
            skLineSegment(sketch, "E4066", {"start": v(32.26, -51.17) * mm, "end": v(32.37, -51.34) * mm});
            skLineSegment(sketch, "E4067", {"start": v(32.37, -51.34) * mm, "end": v(32.48, -51.52) * mm});
            skLineSegment(sketch, "E4068", {"start": v(32.48, -51.52) * mm, "end": v(32.6, -51.69) * mm});
            skLineSegment(sketch, "E4069", {"start": v(32.6, -51.69) * mm, "end": v(32.7, -51.86) * mm});
            skLineSegment(sketch, "E4070", {"start": v(32.7, -51.86) * mm, "end": v(32.82, -52.04) * mm});
            skLineSegment(sketch, "E4071", {"start": v(32.82, -52.04) * mm, "end": v(32.93, -52.21) * mm});
            skLineSegment(sketch, "E4072", {"start": v(32.93, -52.21) * mm, "end": v(33.05, -52.39) * mm});
            skLineSegment(sketch, "E4073", {"start": v(33.05, -52.39) * mm, "end": v(33.16, -52.56) * mm});
            skLineSegment(sketch, "E4074", {"start": v(33.16, -52.56) * mm, "end": v(33.28, -52.75) * mm});
            skLineSegment(sketch, "E4075", {"start": v(33.28, -52.75) * mm, "end": v(33.43, -52.9) * mm});
            skLineSegment(sketch, "E4076", {"start": v(33.43, -52.9) * mm, "end": v(33.62, -53.01) * mm});
            skLineSegment(sketch, "E4077", {"start": v(33.62, -53.01) * mm, "end": v(33.82, -53.07) * mm});
            skLineSegment(sketch, "E4078", {"start": v(33.82, -53.07) * mm, "end": v(34.04, -53.07) * mm});
            skLineSegment(sketch, "E4079", {"start": v(34.04, -53.07) * mm, "end": v(34.25, -53.02) * mm});
            skLineSegment(sketch, "E4080", {"start": v(34.25, -53.02) * mm, "end": v(34.43, -52.92) * mm});
            skLineSegment(sketch, "E4081", {"start": v(34.43, -52.92) * mm, "end": v(34.59, -52.77) * mm});
            skLineSegment(sketch, "E4082", {"start": v(34.59, -52.77) * mm, "end": v(34.7, -52.58) * mm});
            skLineSegment(sketch, "E4083", {"start": v(34.7, -52.58) * mm, "end": v(34.75, -52.38) * mm});
            skLineSegment(sketch, "E4084", {"start": v(34.75, -52.38) * mm, "end": v(34.76, -52.16) * mm});
            skLineSegment(sketch, "E4085", {"start": v(34.76, -52.16) * mm, "end": v(34.7, -51.95) * mm});
            skLineSegment(sketch, "E4086", {"start": v(34.7, -51.95) * mm, "end": v(34.6, -51.78) * mm});
            skLineSegment(sketch, "E4087", {"start": v(34.6, -51.78) * mm, "end": v(34.48, -51.6) * mm});
            skLineSegment(sketch, "E4088", {"start": v(34.48, -51.6) * mm, "end": v(34.37, -51.44) * mm});
            skLineSegment(sketch, "E4089", {"start": v(34.37, -51.44) * mm, "end": v(34.25, -51.27) * mm});
            skLineSegment(sketch, "E4090", {"start": v(34.25, -51.27) * mm, "end": v(34.13, -51.1) * mm});
            skLineSegment(sketch, "E4091", {"start": v(34.13, -51.1) * mm, "end": v(34.02, -50.92) * mm});
            skLineSegment(sketch, "E4092", {"start": v(34.02, -50.92) * mm, "end": v(33.9, -50.75) * mm});
            skLineSegment(sketch, "E4093", {"start": v(33.9, -50.75) * mm, "end": v(33.78, -50.58) * mm});
            skLineSegment(sketch, "E4094", {"start": v(33.78, -50.58) * mm, "end": v(33.66, -50.4) * mm});
            skLineSegment(sketch, "E4095", {"start": v(33.66, -50.4) * mm, "end": v(33.55, -50.24) * mm});
            skLineSegment(sketch, "E4096", {"start": v(33.55, -50.24) * mm, "end": v(33.43, -50.07) * mm});
            skLineSegment(sketch, "E4097", {"start": v(33.43, -50.07) * mm, "end": v(33.3, -49.9) * mm});
            skLineSegment(sketch, "E4098", {"start": v(33.3, -49.9) * mm, "end": v(33.2, -49.72) * mm});
            skLineSegment(sketch, "E4099", {"start": v(33.2, -49.72) * mm, "end": v(33.1, -49.6) * mm});
            skLineSegment(sketch, "E4100", {"start": v(33.1, -49.6) * mm, "end": v(33.27, -49.48) * mm});
            skLineSegment(sketch, "E4101", {"start": v(33.27, -49.48) * mm, "end": v(33.44, -49.36) * mm});
            skLineSegment(sketch, "E4102", {"start": v(33.44, -49.36) * mm, "end": v(33.6, -49.24) * mm});
            skLineSegment(sketch, "E4103", {"start": v(33.6, -49.24) * mm, "end": v(33.78, -49.12) * mm});
            skLineSegment(sketch, "E4104", {"start": v(33.78, -49.12) * mm, "end": v(33.94, -49) * mm});
            skLineSegment(sketch, "E4105", {"start": v(33.94, -49) * mm, "end": v(34.11, -48.88) * mm});
            skLineSegment(sketch, "E4106", {"start": v(34.11, -48.88) * mm, "end": v(34.28, -48.76) * mm});
            skLineSegment(sketch, "E4107", {"start": v(34.28, -48.76) * mm, "end": v(34.45, -48.64) * mm});
            skLineSegment(sketch, "E4108", {"start": v(34.45, -48.64) * mm, "end": v(34.61, -48.52) * mm});
            skLineSegment(sketch, "E4109", {"start": v(34.61, -48.52) * mm, "end": v(34.78, -48.4) * mm});
            skLineSegment(sketch, "E4110", {"start": v(34.78, -48.4) * mm, "end": v(34.95, -48.28) * mm});
            skLineSegment(sketch, "E4111", {"start": v(34.95, -48.28) * mm, "end": v(35.03, -48.22) * mm});
            skLineSegment(sketch, "E4112", {"start": v(35.03, -48.22) * mm, "end": v(35.16, -48.38) * mm});
            skLineSegment(sketch, "E4113", {"start": v(35.16, -48.38) * mm, "end": v(35.28, -48.55) * mm});
            skLineSegment(sketch, "E4114", {"start": v(35.28, -48.55) * mm, "end": v(35.4, -48.72) * mm});
            skLineSegment(sketch, "E4115", {"start": v(35.4, -48.72) * mm, "end": v(35.53, -48.88) * mm});
            skLineSegment(sketch, "E4116", {"start": v(35.53, -48.88) * mm, "end": v(35.65, -49.05) * mm});
            skLineSegment(sketch, "E4117", {"start": v(35.65, -49.05) * mm, "end": v(35.78, -49.22) * mm});
            skLineSegment(sketch, "E4118", {"start": v(35.78, -49.22) * mm, "end": v(35.9, -49.38) * mm});
            skLineSegment(sketch, "E4119", {"start": v(35.9, -49.38) * mm, "end": v(36.03, -49.55) * mm});
            skLineSegment(sketch, "E4120", {"start": v(36.03, -49.55) * mm, "end": v(36.15, -49.72) * mm});
            skLineSegment(sketch, "E4121", {"start": v(36.15, -49.72) * mm, "end": v(36.28, -49.88) * mm});
            skLineSegment(sketch, "E4122", {"start": v(36.28, -49.88) * mm, "end": v(36.4, -50.05) * mm});
            skLineSegment(sketch, "E4123", {"start": v(36.4, -50.05) * mm, "end": v(36.53, -50.22) * mm});
            skLineSegment(sketch, "E4124", {"start": v(36.53, -50.22) * mm, "end": v(36.66, -50.4) * mm});
            skLineSegment(sketch, "E4125", {"start": v(36.66, -50.4) * mm, "end": v(36.82, -50.54) * mm});
            skLineSegment(sketch, "E4126", {"start": v(36.82, -50.54) * mm, "end": v(37, -50.64) * mm});
            skLineSegment(sketch, "E4127", {"start": v(37, -50.64) * mm, "end": v(37.22, -50.68) * mm});
            skLineSegment(sketch, "E4128", {"start": v(37.22, -50.68) * mm, "end": v(37.43, -50.67) * mm});
            skLineSegment(sketch, "E4129", {"start": v(37.43, -50.67) * mm, "end": v(37.64, -50.6) * mm});
            skLineSegment(sketch, "E4130", {"start": v(37.64, -50.6) * mm, "end": v(37.82, -50.49) * mm});
            skLineSegment(sketch, "E4131", {"start": v(37.82, -50.49) * mm, "end": v(37.96, -50.33) * mm});
            skLineSegment(sketch, "E4132", {"start": v(37.96, -50.33) * mm, "end": v(38.06, -50.14) * mm});
            skLineSegment(sketch, "E4133", {"start": v(38.06, -50.14) * mm, "end": v(38.1, -49.93) * mm});
            skLineSegment(sketch, "E4134", {"start": v(38.1, -49.93) * mm, "end": v(38.1, -49.71) * mm});
            skLineSegment(sketch, "E4135", {"start": v(38.1, -49.71) * mm, "end": v(38.02, -49.5) * mm});
            skLineSegment(sketch, "E4136", {"start": v(38.02, -49.5) * mm, "end": v(37.9, -49.34) * mm});
            skLineSegment(sketch, "E4137", {"start": v(37.9, -49.34) * mm, "end": v(37.78, -49.17) * mm});
            skLineSegment(sketch, "E4138", {"start": v(37.78, -49.17) * mm, "end": v(37.66, -49.01) * mm});
            skLineSegment(sketch, "E4139", {"start": v(37.66, -49.01) * mm, "end": v(37.53, -48.85) * mm});
            skLineSegment(sketch, "E4140", {"start": v(37.53, -48.85) * mm, "end": v(37.4, -48.69) * mm});
            skLineSegment(sketch, "E4141", {"start": v(37.4, -48.69) * mm, "end": v(37.27, -48.52) * mm});
            skLineSegment(sketch, "E4142", {"start": v(37.27, -48.52) * mm, "end": v(37.14, -48.36) * mm});
            skLineSegment(sketch, "E4143", {"start": v(37.14, -48.36) * mm, "end": v(37.02, -48.2) * mm});
            skLineSegment(sketch, "E4144", {"start": v(37.02, -48.2) * mm, "end": v(36.88, -48.03) * mm});
            skLineSegment(sketch, "E4145", {"start": v(36.88, -48.03) * mm, "end": v(36.76, -47.87) * mm});
            skLineSegment(sketch, "E4146", {"start": v(36.76, -47.87) * mm, "end": v(36.63, -47.71) * mm});
            skLineSegment(sketch, "E4147", {"start": v(36.63, -47.71) * mm, "end": v(36.5, -47.54) * mm});
            skLineSegment(sketch, "E4148", {"start": v(36.5, -47.54) * mm, "end": v(36.37, -47.38) * mm});
            skLineSegment(sketch, "E4149", {"start": v(36.37, -47.38) * mm, "end": v(36.28, -47.26) * mm});
            skLineSegment(sketch, "E4150", {"start": v(36.28, -47.26) * mm, "end": v(36.44, -47.13) * mm});
            skLineSegment(sketch, "E4151", {"start": v(36.44, -47.13) * mm, "end": v(36.6, -47) * mm});
            skLineSegment(sketch, "E4152", {"start": v(36.6, -47) * mm, "end": v(36.76, -46.87) * mm});
            skLineSegment(sketch, "E4153", {"start": v(36.76, -46.87) * mm, "end": v(36.91, -46.74) * mm});
            skLineSegment(sketch, "E4154", {"start": v(36.91, -46.74) * mm, "end": v(37.07, -46.61) * mm});
            skLineSegment(sketch, "E4155", {"start": v(37.07, -46.61) * mm, "end": v(37.23, -46.48) * mm});
            skLineSegment(sketch, "E4156", {"start": v(37.23, -46.48) * mm, "end": v(37.4, -46.35) * mm});
            skLineSegment(sketch, "E4157", {"start": v(37.4, -46.35) * mm, "end": v(37.55, -46.22) * mm});
            skLineSegment(sketch, "E4158", {"start": v(37.55, -46.22) * mm, "end": v(37.71, -46.09) * mm});
            skLineSegment(sketch, "E4159", {"start": v(37.71, -46.09) * mm, "end": v(37.87, -45.96) * mm});
            skLineSegment(sketch, "E4160", {"start": v(37.87, -45.96) * mm, "end": v(38.03, -45.83) * mm});
            skLineSegment(sketch, "E4161", {"start": v(38.03, -45.83) * mm, "end": v(38.11, -45.76) * mm});
            skLineSegment(sketch, "E4162", {"start": v(38.11, -45.76) * mm, "end": v(38.24, -45.92) * mm});
            skLineSegment(sketch, "E4163", {"start": v(38.24, -45.92) * mm, "end": v(38.38, -46.07) * mm});
            skLineSegment(sketch, "E4164", {"start": v(38.38, -46.07) * mm, "end": v(38.52, -46.23) * mm});
            skLineSegment(sketch, "E4165", {"start": v(38.52, -46.23) * mm, "end": v(38.65, -46.4) * mm});
            skLineSegment(sketch, "E4166", {"start": v(38.65, -46.4) * mm, "end": v(38.78, -46.55) * mm});
            skLineSegment(sketch, "E4167", {"start": v(38.78, -46.55) * mm, "end": v(38.92, -46.7) * mm});
            skLineSegment(sketch, "E4168", {"start": v(38.92, -46.7) * mm, "end": v(39.05, -46.87) * mm});
            skLineSegment(sketch, "E4169", {"start": v(39.05, -46.87) * mm, "end": v(39.19, -47.02) * mm});
            skLineSegment(sketch, "E4170", {"start": v(39.19, -47.02) * mm, "end": v(39.33, -47.18) * mm});
            skLineSegment(sketch, "E4171", {"start": v(39.33, -47.18) * mm, "end": v(39.46, -47.34) * mm});
            skLineSegment(sketch, "E4172", {"start": v(39.46, -47.34) * mm, "end": v(39.6, -47.5) * mm});
            skLineSegment(sketch, "E4173", {"start": v(39.6, -47.5) * mm, "end": v(39.73, -47.66) * mm});
            skLineSegment(sketch, "E4174", {"start": v(39.73, -47.66) * mm, "end": v(39.88, -47.82) * mm});
            skLineSegment(sketch, "E4175", {"start": v(39.88, -47.82) * mm, "end": v(40.04, -47.96) * mm});
            skLineSegment(sketch, "E4176", {"start": v(40.04, -47.96) * mm, "end": v(40.24, -48.04) * mm});
            skLineSegment(sketch, "E4177", {"start": v(40.24, -48.04) * mm, "end": v(40.45, -48.08) * mm});
            skLineSegment(sketch, "E4178", {"start": v(40.45, -48.08) * mm, "end": v(40.67, -48.05) * mm});
            skLineSegment(sketch, "E4179", {"start": v(40.67, -48.05) * mm, "end": v(40.86, -47.97) * mm});
            skLineSegment(sketch, "E4180", {"start": v(40.86, -47.97) * mm, "end": v(41.04, -47.84) * mm});
            skLineSegment(sketch, "E4181", {"start": v(41.04, -47.84) * mm, "end": v(41.17, -47.67) * mm});
            skLineSegment(sketch, "E4182", {"start": v(41.17, -47.67) * mm, "end": v(41.25, -47.48) * mm});
            skLineSegment(sketch, "E4183", {"start": v(41.25, -47.48) * mm, "end": v(41.28, -47.26) * mm});
            skLineSegment(sketch, "E4184", {"start": v(41.28, -47.26) * mm, "end": v(41.26, -47.05) * mm});
            skLineSegment(sketch, "E4185", {"start": v(41.26, -47.05) * mm, "end": v(41.18, -46.85) * mm});
            skLineSegment(sketch, "E4186", {"start": v(41.18, -46.85) * mm, "end": v(41.05, -46.69) * mm});
            skLineSegment(sketch, "E4187", {"start": v(41.05, -46.69) * mm, "end": v(40.92, -46.53) * mm});
            skLineSegment(sketch, "E4188", {"start": v(40.92, -46.53) * mm, "end": v(40.78, -46.38) * mm});
            skLineSegment(sketch, "E4189", {"start": v(40.78, -46.38) * mm, "end": v(40.64, -46.23) * mm});
            skLineSegment(sketch, "E4190", {"start": v(40.64, -46.23) * mm, "end": v(40.5, -46.08) * mm});
            skLineSegment(sketch, "E4191", {"start": v(40.5, -46.08) * mm, "end": v(40.36, -45.92) * mm});
            skLineSegment(sketch, "E4192", {"start": v(40.36, -45.92) * mm, "end": v(40.22, -45.77) * mm});
            skLineSegment(sketch, "E4193", {"start": v(40.22, -45.77) * mm, "end": v(40.09, -45.61) * mm});
            skLineSegment(sketch, "E4194", {"start": v(40.09, -45.61) * mm, "end": v(39.95, -45.46) * mm});
            skLineSegment(sketch, "E4195", {"start": v(39.95, -45.46) * mm, "end": v(39.8, -45.3) * mm});
            skLineSegment(sketch, "E4196", {"start": v(39.8, -45.3) * mm, "end": v(39.67, -45.15) * mm});
            skLineSegment(sketch, "E4197", {"start": v(39.67, -45.15) * mm, "end": v(39.53, -45) * mm});
            skLineSegment(sketch, "E4198", {"start": v(39.53, -45) * mm, "end": v(39.4, -44.84) * mm});
            skLineSegment(sketch, "E4199", {"start": v(39.4, -44.84) * mm, "end": v(39.29, -44.73) * mm});
            skLineSegment(sketch, "E4200", {"start": v(39.29, -44.73) * mm, "end": v(39.44, -44.59) * mm});
            skLineSegment(sketch, "E4201", {"start": v(39.44, -44.59) * mm, "end": v(39.6, -44.45) * mm});
            skLineSegment(sketch, "E4202", {"start": v(39.6, -44.45) * mm, "end": v(39.74, -44.3) * mm});
            skLineSegment(sketch, "E4203", {"start": v(39.74, -44.3) * mm, "end": v(39.9, -44.16) * mm});
            skLineSegment(sketch, "E4204", {"start": v(39.9, -44.16) * mm, "end": v(40.04, -44.02) * mm});
            skLineSegment(sketch, "E4205", {"start": v(40.04, -44.02) * mm, "end": v(40.2, -43.88) * mm});
            skLineSegment(sketch, "E4206", {"start": v(40.2, -43.88) * mm, "end": v(40.34, -43.74) * mm});
            skLineSegment(sketch, "E4207", {"start": v(40.34, -43.74) * mm, "end": v(40.5, -43.6) * mm});
            skLineSegment(sketch, "E4208", {"start": v(40.5, -43.6) * mm, "end": v(40.64, -43.46) * mm});
            skLineSegment(sketch, "E4209", {"start": v(40.64, -43.46) * mm, "end": v(40.8, -43.32) * mm});
            skLineSegment(sketch, "E4210", {"start": v(40.8, -43.32) * mm, "end": v(40.94, -43.18) * mm});
            skLineSegment(sketch, "E4211", {"start": v(40.94, -43.18) * mm, "end": v(41.02, -43.1) * mm});
            skLineSegment(sketch, "E4212", {"start": v(41.02, -43.1) * mm, "end": v(41.16, -43.25) * mm});
            skLineSegment(sketch, "E4213", {"start": v(41.16, -43.25) * mm, "end": v(41.3, -43.4) * mm});
            skLineSegment(sketch, "E4214", {"start": v(41.3, -43.4) * mm, "end": v(41.45, -43.55) * mm});
            skLineSegment(sketch, "E4215", {"start": v(41.45, -43.55) * mm, "end": v(41.6, -43.7) * mm});
            skLineSegment(sketch, "E4216", {"start": v(41.6, -43.7) * mm, "end": v(41.74, -43.85) * mm});
            skLineSegment(sketch, "E4217", {"start": v(41.74, -43.85) * mm, "end": v(41.89, -44) * mm});
            skLineSegment(sketch, "E4218", {"start": v(41.89, -44) * mm, "end": v(42.03, -44.15) * mm});
            skLineSegment(sketch, "E4219", {"start": v(42.03, -44.15) * mm, "end": v(42.18, -44.3) * mm});
            skLineSegment(sketch, "E4220", {"start": v(42.18, -44.3) * mm, "end": v(42.33, -44.45) * mm});
            skLineSegment(sketch, "E4221", {"start": v(42.33, -44.45) * mm, "end": v(42.47, -44.6) * mm});
            skLineSegment(sketch, "E4222", {"start": v(42.47, -44.6) * mm, "end": v(42.61, -44.74) * mm});
            skLineSegment(sketch, "E4223", {"start": v(42.61, -44.74) * mm, "end": v(42.76, -44.9) * mm});
            skLineSegment(sketch, "E4224", {"start": v(42.76, -44.9) * mm, "end": v(42.92, -45.05) * mm});
            skLineSegment(sketch, "E4225", {"start": v(42.92, -45.05) * mm, "end": v(43.1, -45.17) * mm});
            skLineSegment(sketch, "E4226", {"start": v(43.1, -45.17) * mm, "end": v(43.3, -45.25) * mm});
            skLineSegment(sketch, "E4227", {"start": v(43.3, -45.25) * mm, "end": v(43.5, -45.26) * mm});
            skLineSegment(sketch, "E4228", {"start": v(43.5, -45.26) * mm, "end": v(43.72, -45.22) * mm});
            skLineSegment(sketch, "E4229", {"start": v(43.72, -45.22) * mm, "end": v(43.91, -45.13) * mm});
            skLineSegment(sketch, "E4230", {"start": v(43.91, -45.13) * mm, "end": v(44.08, -45) * mm});
            skLineSegment(sketch, "E4231", {"start": v(44.08, -45) * mm, "end": v(44.2, -44.82) * mm});
            skLineSegment(sketch, "E4232", {"start": v(44.2, -44.82) * mm, "end": v(44.27, -44.61) * mm});
            skLineSegment(sketch, "E4233", {"start": v(44.27, -44.61) * mm, "end": v(44.28, -44.4) * mm});
            skLineSegment(sketch, "E4234", {"start": v(44.28, -44.4) * mm, "end": v(44.24, -44.19) * mm});
            skLineSegment(sketch, "E4235", {"start": v(44.24, -44.19) * mm, "end": v(44.15, -44) * mm});
            skLineSegment(sketch, "E4236", {"start": v(44.15, -44) * mm, "end": v(44.01, -43.84) * mm});
            skLineSegment(sketch, "E4237", {"start": v(44.01, -43.84) * mm, "end": v(43.87, -43.7) * mm});
            skLineSegment(sketch, "E4238", {"start": v(43.87, -43.7) * mm, "end": v(43.72, -43.55) * mm});
            skLineSegment(sketch, "E4239", {"start": v(43.72, -43.55) * mm, "end": v(43.58, -43.4) * mm});
            skLineSegment(sketch, "E4240", {"start": v(43.58, -43.4) * mm, "end": v(43.43, -43.26) * mm});
            skLineSegment(sketch, "E4241", {"start": v(43.43, -43.26) * mm, "end": v(43.28, -43.12) * mm});
            skLineSegment(sketch, "E4242", {"start": v(43.28, -43.12) * mm, "end": v(43.13, -42.97) * mm});
            skLineSegment(sketch, "E4243", {"start": v(43.13, -42.97) * mm, "end": v(42.98, -42.83) * mm});
            skLineSegment(sketch, "E4244", {"start": v(42.98, -42.83) * mm, "end": v(42.83, -42.68) * mm});
            skLineSegment(sketch, "E4245", {"start": v(42.83, -42.68) * mm, "end": v(42.68, -42.54) * mm});
            skLineSegment(sketch, "E4246", {"start": v(42.68, -42.54) * mm, "end": v(42.54, -42.4) * mm});
            skLineSegment(sketch, "E4247", {"start": v(42.54, -42.4) * mm, "end": v(42.38, -42.25) * mm});
            skLineSegment(sketch, "E4248", {"start": v(42.38, -42.25) * mm, "end": v(42.24, -42.1) * mm});
            skLineSegment(sketch, "E4249", {"start": v(42.24, -42.1) * mm, "end": v(42.13, -42) * mm});
            skLineSegment(sketch, "E4250", {"start": v(42.13, -42) * mm, "end": v(42.27, -41.85) * mm});
            skLineSegment(sketch, "E4251", {"start": v(42.27, -41.85) * mm, "end": v(42.41, -41.7) * mm});
            skLineSegment(sketch, "E4252", {"start": v(42.41, -41.7) * mm, "end": v(42.55, -41.55) * mm});
            skLineSegment(sketch, "E4253", {"start": v(42.55, -41.55) * mm, "end": v(42.7, -41.4) * mm});
            skLineSegment(sketch, "E4254", {"start": v(42.7, -41.4) * mm, "end": v(42.83, -41.25) * mm});
            skLineSegment(sketch, "E4255", {"start": v(42.83, -41.25) * mm, "end": v(42.97, -41.1) * mm});
            skLineSegment(sketch, "E4256", {"start": v(42.97, -41.1) * mm, "end": v(43.11, -40.95) * mm});
            skLineSegment(sketch, "E4257", {"start": v(43.11, -40.95) * mm, "end": v(43.25, -40.8) * mm});
            skLineSegment(sketch, "E4258", {"start": v(43.25, -40.8) * mm, "end": v(43.4, -40.64) * mm});
            skLineSegment(sketch, "E4259", {"start": v(43.4, -40.64) * mm, "end": v(43.54, -40.5) * mm});
            skLineSegment(sketch, "E4260", {"start": v(43.54, -40.5) * mm, "end": v(43.68, -40.34) * mm});
            skLineSegment(sketch, "E4261", {"start": v(43.68, -40.34) * mm, "end": v(43.75, -40.27) * mm});
            skLineSegment(sketch, "E4262", {"start": v(43.75, -40.27) * mm, "end": v(43.9, -40.4) * mm});
            skLineSegment(sketch, "E4263", {"start": v(43.9, -40.4) * mm, "end": v(44.06, -40.54) * mm});
            skLineSegment(sketch, "E4264", {"start": v(44.06, -40.54) * mm, "end": v(44.21, -40.68) * mm});
            skLineSegment(sketch, "E4265", {"start": v(44.21, -40.68) * mm, "end": v(44.37, -40.82) * mm});
            skLineSegment(sketch, "E4266", {"start": v(44.37, -40.82) * mm, "end": v(44.52, -40.96) * mm});
            skLineSegment(sketch, "E4267", {"start": v(44.52, -40.96) * mm, "end": v(44.68, -41.1) * mm});
            skLineSegment(sketch, "E4268", {"start": v(44.68, -41.1) * mm, "end": v(44.83, -41.24) * mm});
            skLineSegment(sketch, "E4269", {"start": v(44.83, -41.24) * mm, "end": v(44.98, -41.38) * mm});
            skLineSegment(sketch, "E4270", {"start": v(44.98, -41.38) * mm, "end": v(45.14, -41.52) * mm});
            skLineSegment(sketch, "E4271", {"start": v(45.14, -41.52) * mm, "end": v(45.3, -41.66) * mm});
            skLineSegment(sketch, "E4272", {"start": v(45.3, -41.66) * mm, "end": v(45.45, -41.8) * mm});
            skLineSegment(sketch, "E4273", {"start": v(45.45, -41.8) * mm, "end": v(45.6, -41.94) * mm});
            skLineSegment(sketch, "E4274", {"start": v(45.6, -41.94) * mm, "end": v(45.77, -42.08) * mm});
            skLineSegment(sketch, "E4275", {"start": v(45.77, -42.08) * mm, "end": v(45.95, -42.2) * mm});
            skLineSegment(sketch, "E4276", {"start": v(45.95, -42.2) * mm, "end": v(46.16, -42.25) * mm});
            skLineSegment(sketch, "E4277", {"start": v(46.16, -42.25) * mm, "end": v(46.37, -42.26) * mm});
            skLineSegment(sketch, "E4278", {"start": v(46.37, -42.26) * mm, "end": v(46.58, -42.2) * mm});
            skLineSegment(sketch, "E4279", {"start": v(46.58, -42.2) * mm, "end": v(46.77, -42.1) * mm});
            skLineSegment(sketch, "E4280", {"start": v(46.77, -42.1) * mm, "end": v(46.92, -41.95) * mm});
            skLineSegment(sketch, "E4281", {"start": v(46.92, -41.95) * mm, "end": v(47.03, -41.77) * mm});
            skLineSegment(sketch, "E4282", {"start": v(47.03, -41.77) * mm, "end": v(47.09, -41.56) * mm});
            skLineSegment(sketch, "E4283", {"start": v(47.09, -41.56) * mm, "end": v(47.1, -41.34) * mm});
            skLineSegment(sketch, "E4284", {"start": v(47.1, -41.34) * mm, "end": v(47.04, -41.14) * mm});
            skLineSegment(sketch, "E4285", {"start": v(47.04, -41.14) * mm, "end": v(46.93, -40.95) * mm});
            skLineSegment(sketch, "E4286", {"start": v(46.93, -40.95) * mm, "end": v(46.79, -40.8) * mm});
            skLineSegment(sketch, "E4287", {"start": v(46.79, -40.8) * mm, "end": v(46.63, -40.67) * mm});
            skLineSegment(sketch, "E4288", {"start": v(46.63, -40.67) * mm, "end": v(46.48, -40.53) * mm});
            skLineSegment(sketch, "E4289", {"start": v(46.48, -40.53) * mm, "end": v(46.32, -40.4) * mm});
            skLineSegment(sketch, "E4290", {"start": v(46.32, -40.4) * mm, "end": v(46.16, -40.27) * mm});
            skLineSegment(sketch, "E4291", {"start": v(46.16, -40.27) * mm, "end": v(46, -40.13) * mm});
            skLineSegment(sketch, "E4292", {"start": v(46, -40.13) * mm, "end": v(45.85, -40) * mm});
            skLineSegment(sketch, "E4293", {"start": v(45.85, -40) * mm, "end": v(45.69, -39.86) * mm});
            skLineSegment(sketch, "E4294", {"start": v(45.69, -39.86) * mm, "end": v(45.53, -39.72) * mm});
            skLineSegment(sketch, "E4295", {"start": v(45.53, -39.72) * mm, "end": v(45.37, -39.6) * mm});
            skLineSegment(sketch, "E4296", {"start": v(45.37, -39.6) * mm, "end": v(45.21, -39.46) * mm});
            skLineSegment(sketch, "E4297", {"start": v(45.21, -39.46) * mm, "end": v(45.05, -39.32) * mm});
            skLineSegment(sketch, "E4298", {"start": v(45.05, -39.32) * mm, "end": v(44.9, -39.19) * mm});
            skLineSegment(sketch, "E4299", {"start": v(44.9, -39.19) * mm, "end": v(44.78, -39.09) * mm});
            skLineSegment(sketch, "E4300", {"start": v(44.78, -39.09) * mm, "end": v(44.91, -38.93) * mm});
            skLineSegment(sketch, "E4301", {"start": v(44.91, -38.93) * mm, "end": v(45.04, -38.77) * mm});
            skLineSegment(sketch, "E4302", {"start": v(45.04, -38.77) * mm, "end": v(45.17, -38.61) * mm});
            skLineSegment(sketch, "E4303", {"start": v(45.17, -38.61) * mm, "end": v(45.3, -38.45) * mm});
            skLineSegment(sketch, "E4304", {"start": v(45.3, -38.45) * mm, "end": v(45.44, -38.3) * mm});
            skLineSegment(sketch, "E4305", {"start": v(45.44, -38.3) * mm, "end": v(45.57, -38.13) * mm});
            skLineSegment(sketch, "E4306", {"start": v(45.57, -38.13) * mm, "end": v(45.7, -37.97) * mm});
            skLineSegment(sketch, "E4307", {"start": v(45.7, -37.97) * mm, "end": v(45.83, -37.81) * mm});
            skLineSegment(sketch, "E4308", {"start": v(45.83, -37.81) * mm, "end": v(45.96, -37.66) * mm});
            skLineSegment(sketch, "E4309", {"start": v(45.96, -37.66) * mm, "end": v(46.09, -37.5) * mm});
            skLineSegment(sketch, "E4310", {"start": v(46.09, -37.5) * mm, "end": v(46.22, -37.34) * mm});
            skLineSegment(sketch, "E4311", {"start": v(46.22, -37.34) * mm, "end": v(46.29, -37.26) * mm});
            skLineSegment(sketch, "E4312", {"start": v(46.29, -37.26) * mm, "end": v(46.45, -37.38) * mm});
            skLineSegment(sketch, "E4313", {"start": v(46.45, -37.38) * mm, "end": v(46.61, -37.51) * mm});
            skLineSegment(sketch, "E4314", {"start": v(46.61, -37.51) * mm, "end": v(46.78, -37.64) * mm});
            skLineSegment(sketch, "E4315", {"start": v(46.78, -37.64) * mm, "end": v(46.94, -37.77) * mm});
            skLineSegment(sketch, "E4316", {"start": v(46.94, -37.77) * mm, "end": v(47.1, -37.9) * mm});
            skLineSegment(sketch, "E4317", {"start": v(47.1, -37.9) * mm, "end": v(47.27, -38.03) * mm});
            skLineSegment(sketch, "E4318", {"start": v(47.27, -38.03) * mm, "end": v(47.43, -38.16) * mm});
            skLineSegment(sketch, "E4319", {"start": v(47.43, -38.16) * mm, "end": v(47.59, -38.28) * mm});
            skLineSegment(sketch, "E4320", {"start": v(47.59, -38.28) * mm, "end": v(47.76, -38.41) * mm});
            skLineSegment(sketch, "E4321", {"start": v(47.76, -38.41) * mm, "end": v(47.92, -38.54) * mm});
            skLineSegment(sketch, "E4322", {"start": v(47.92, -38.54) * mm, "end": v(48.08, -38.67) * mm});
            skLineSegment(sketch, "E4323", {"start": v(48.08, -38.67) * mm, "end": v(48.25, -38.8) * mm});
            skLineSegment(sketch, "E4324", {"start": v(48.25, -38.8) * mm, "end": v(48.42, -38.94) * mm});
            skLineSegment(sketch, "E4325", {"start": v(48.42, -38.94) * mm, "end": v(48.61, -39.03) * mm});
            skLineSegment(sketch, "E4326", {"start": v(48.61, -39.03) * mm, "end": v(48.82, -39.08) * mm});
            skLineSegment(sketch, "E4327", {"start": v(48.82, -39.08) * mm, "end": v(49.03, -39.07) * mm});
            skLineSegment(sketch, "E4328", {"start": v(49.03, -39.07) * mm, "end": v(49.24, -39) * mm});
            skLineSegment(sketch, "E4329", {"start": v(49.24, -39) * mm, "end": v(49.42, -38.89) * mm});
            skLineSegment(sketch, "E4330", {"start": v(49.42, -38.89) * mm, "end": v(49.56, -38.73) * mm});
            skLineSegment(sketch, "E4331", {"start": v(49.56, -38.73) * mm, "end": v(49.66, -38.54) * mm});
            skLineSegment(sketch, "E4332", {"start": v(49.66, -38.54) * mm, "end": v(49.7, -38.33) * mm});
            skLineSegment(sketch, "E4333", {"start": v(49.7, -38.33) * mm, "end": v(49.7, -38.11) * mm});
            skLineSegment(sketch, "E4334", {"start": v(49.7, -38.11) * mm, "end": v(49.63, -37.9) * mm});
            skLineSegment(sketch, "E4335", {"start": v(49.63, -37.9) * mm, "end": v(49.5, -37.73) * mm});
            skLineSegment(sketch, "E4336", {"start": v(49.5, -37.73) * mm, "end": v(49.35, -37.6) * mm});
            skLineSegment(sketch, "E4337", {"start": v(49.35, -37.6) * mm, "end": v(49.19, -37.47) * mm});
            skLineSegment(sketch, "E4338", {"start": v(49.19, -37.47) * mm, "end": v(49.03, -37.34) * mm});
            skLineSegment(sketch, "E4339", {"start": v(49.03, -37.34) * mm, "end": v(48.86, -37.22) * mm});
            skLineSegment(sketch, "E4340", {"start": v(48.86, -37.22) * mm, "end": v(48.7, -37.1) * mm});
            skLineSegment(sketch, "E4341", {"start": v(48.7, -37.1) * mm, "end": v(48.53, -36.97) * mm});
            skLineSegment(sketch, "E4342", {"start": v(48.53, -36.97) * mm, "end": v(48.36, -36.85) * mm});
            skLineSegment(sketch, "E4343", {"start": v(48.36, -36.85) * mm, "end": v(48.2, -36.72) * mm});
            skLineSegment(sketch, "E4344", {"start": v(48.2, -36.72) * mm, "end": v(48.03, -36.6) * mm});
            skLineSegment(sketch, "E4345", {"start": v(48.03, -36.6) * mm, "end": v(47.86, -36.47) * mm});
            skLineSegment(sketch, "E4346", {"start": v(47.86, -36.47) * mm, "end": v(47.7, -36.35) * mm});
            skLineSegment(sketch, "E4347", {"start": v(47.7, -36.35) * mm, "end": v(47.53, -36.22) * mm});
            skLineSegment(sketch, "E4348", {"start": v(47.53, -36.22) * mm, "end": v(47.36, -36.1) * mm});
            skLineSegment(sketch, "E4349", {"start": v(47.36, -36.1) * mm, "end": v(47.24, -36.01) * mm});
            skLineSegment(sketch, "E4350", {"start": v(47.24, -36.01) * mm, "end": v(47.36, -35.84) * mm});
            skLineSegment(sketch, "E4351", {"start": v(47.36, -35.84) * mm, "end": v(47.48, -35.68) * mm});
            skLineSegment(sketch, "E4352", {"start": v(47.48, -35.68) * mm, "end": v(47.6, -35.5) * mm});
            skLineSegment(sketch, "E4353", {"start": v(47.6, -35.5) * mm, "end": v(47.72, -35.34) * mm});
            skLineSegment(sketch, "E4354", {"start": v(47.72, -35.34) * mm, "end": v(47.84, -35.17) * mm});
            skLineSegment(sketch, "E4355", {"start": v(47.84, -35.17) * mm, "end": v(47.96, -35) * mm});
            skLineSegment(sketch, "E4356", {"start": v(47.96, -35) * mm, "end": v(48.08, -34.84) * mm});
            skLineSegment(sketch, "E4357", {"start": v(48.08, -34.84) * mm, "end": v(48.2, -34.67) * mm});
            skLineSegment(sketch, "E4358", {"start": v(48.2, -34.67) * mm, "end": v(48.32, -34.5) * mm});
            skLineSegment(sketch, "E4359", {"start": v(48.32, -34.5) * mm, "end": v(48.44, -34.34) * mm});
            skLineSegment(sketch, "E4360", {"start": v(48.44, -34.34) * mm, "end": v(48.56, -34.17) * mm});
            skLineSegment(sketch, "E4361", {"start": v(48.56, -34.17) * mm, "end": v(48.62, -34.08) * mm});
            skLineSegment(sketch, "E4362", {"start": v(48.62, -34.08) * mm, "end": v(48.8, -34.2) * mm});
            skLineSegment(sketch, "E4363", {"start": v(48.8, -34.2) * mm, "end": v(48.96, -34.32) * mm});
            skLineSegment(sketch, "E4364", {"start": v(48.96, -34.32) * mm, "end": v(49.14, -34.44) * mm});
            skLineSegment(sketch, "E4365", {"start": v(49.14, -34.44) * mm, "end": v(49.3, -34.55) * mm});
            skLineSegment(sketch, "E4366", {"start": v(49.3, -34.55) * mm, "end": v(49.48, -34.67) * mm});
            skLineSegment(sketch, "E4367", {"start": v(49.48, -34.67) * mm, "end": v(49.65, -34.8) * mm});
            skLineSegment(sketch, "E4368", {"start": v(49.65, -34.8) * mm, "end": v(49.82, -34.9) * mm});
            skLineSegment(sketch, "E4369", {"start": v(49.82, -34.9) * mm, "end": v(49.99, -35.02) * mm});
            skLineSegment(sketch, "E4370", {"start": v(49.99, -35.02) * mm, "end": v(50.16, -35.14) * mm});
            skLineSegment(sketch, "E4371", {"start": v(50.16, -35.14) * mm, "end": v(50.33, -35.26) * mm});
            skLineSegment(sketch, "E4372", {"start": v(50.33, -35.26) * mm, "end": v(50.5, -35.38) * mm});
            skLineSegment(sketch, "E4373", {"start": v(50.5, -35.38) * mm, "end": v(50.68, -35.5) * mm});
            skLineSegment(sketch, "E4374", {"start": v(50.68, -35.5) * mm, "end": v(50.86, -35.62) * mm});
            skLineSegment(sketch, "E4375", {"start": v(50.86, -35.62) * mm, "end": v(51.06, -35.7) * mm});
            skLineSegment(sketch, "E4376", {"start": v(51.06, -35.7) * mm, "end": v(51.27, -35.74) * mm});
            skLineSegment(sketch, "E4377", {"start": v(51.27, -35.74) * mm, "end": v(51.48, -35.71) * mm});
            skLineSegment(sketch, "E4378", {"start": v(51.48, -35.71) * mm, "end": v(51.68, -35.64) * mm});
            skLineSegment(sketch, "E4379", {"start": v(51.68, -35.64) * mm, "end": v(51.85, -35.5) * mm});
            skLineSegment(sketch, "E4380", {"start": v(51.85, -35.5) * mm, "end": v(51.99, -35.34) * mm});
            skLineSegment(sketch, "E4381", {"start": v(51.99, -35.34) * mm, "end": v(52.07, -35.14) * mm});
            skLineSegment(sketch, "E4382", {"start": v(52.07, -35.14) * mm, "end": v(52.1, -34.93) * mm});
            skLineSegment(sketch, "E4383", {"start": v(52.1, -34.93) * mm, "end": v(52.08, -34.72) * mm});
            skLineSegment(sketch, "E4384", {"start": v(52.08, -34.72) * mm, "end": v(52, -34.52) * mm});
            skLineSegment(sketch, "E4385", {"start": v(52, -34.52) * mm, "end": v(51.87, -34.35) * mm});
            skLineSegment(sketch, "E4386", {"start": v(51.87, -34.35) * mm, "end": v(51.7, -34.22) * mm});
            skLineSegment(sketch, "E4387", {"start": v(51.7, -34.22) * mm, "end": v(51.53, -34.1) * mm});
            skLineSegment(sketch, "E4388", {"start": v(51.53, -34.1) * mm, "end": v(51.36, -34) * mm});
            skLineSegment(sketch, "E4389", {"start": v(51.36, -34) * mm, "end": v(51.19, -33.88) * mm});
            skLineSegment(sketch, "E4390", {"start": v(51.19, -33.88) * mm, "end": v(51.02, -33.77) * mm});
            skLineSegment(sketch, "E4391", {"start": v(51.02, -33.77) * mm, "end": v(50.84, -33.65) * mm});
            skLineSegment(sketch, "E4392", {"start": v(50.84, -33.65) * mm, "end": v(50.67, -33.54) * mm});
            skLineSegment(sketch, "E4393", {"start": v(50.67, -33.54) * mm, "end": v(50.5, -33.43) * mm});
            skLineSegment(sketch, "E4394", {"start": v(50.5, -33.43) * mm, "end": v(50.32, -33.31) * mm});
            skLineSegment(sketch, "E4395", {"start": v(50.32, -33.31) * mm, "end": v(50.14, -33.2) * mm});
            skLineSegment(sketch, "E4396", {"start": v(50.14, -33.2) * mm, "end": v(49.97, -33.1) * mm});
            skLineSegment(sketch, "E4397", {"start": v(49.97, -33.1) * mm, "end": v(49.8, -32.98) * mm});
            skLineSegment(sketch, "E4398", {"start": v(49.8, -32.98) * mm, "end": v(49.62, -32.86) * mm});
            skLineSegment(sketch, "E4399", {"start": v(49.62, -32.86) * mm, "end": v(49.5, -32.78) * mm});
            skLineSegment(sketch, "E4400", {"start": v(49.5, -32.78) * mm, "end": v(49.6, -32.6) * mm});
            skLineSegment(sketch, "E4401", {"start": v(49.6, -32.6) * mm, "end": v(49.71, -32.43) * mm});
            skLineSegment(sketch, "E4402", {"start": v(49.71, -32.43) * mm, "end": v(49.82, -32.26) * mm});
            skLineSegment(sketch, "E4403", {"start": v(49.82, -32.26) * mm, "end": v(49.93, -32.08) * mm});
            skLineSegment(sketch, "E4404", {"start": v(49.93, -32.08) * mm, "end": v(50.04, -31.9) * mm});
            skLineSegment(sketch, "E4405", {"start": v(50.04, -31.9) * mm, "end": v(50.15, -31.73) * mm});
            skLineSegment(sketch, "E4406", {"start": v(50.15, -31.73) * mm, "end": v(50.25, -31.56) * mm});
            skLineSegment(sketch, "E4407", {"start": v(50.25, -31.56) * mm, "end": v(50.36, -31.38) * mm});
            skLineSegment(sketch, "E4408", {"start": v(50.36, -31.38) * mm, "end": v(50.47, -31.2) * mm});
            skLineSegment(sketch, "E4409", {"start": v(50.47, -31.2) * mm, "end": v(50.58, -31.03) * mm});
            skLineSegment(sketch, "E4410", {"start": v(50.58, -31.03) * mm, "end": v(50.69, -30.86) * mm});
            skLineSegment(sketch, "E4411", {"start": v(50.69, -30.86) * mm, "end": v(50.75, -30.77) * mm});
            skLineSegment(sketch, "E4412", {"start": v(50.75, -30.77) * mm, "end": v(50.92, -30.87) * mm});
            skLineSegment(sketch, "E4413", {"start": v(50.92, -30.87) * mm, "end": v(51.1, -30.98) * mm});
            skLineSegment(sketch, "E4414", {"start": v(51.1, -30.98) * mm, "end": v(51.28, -31.09) * mm});
            skLineSegment(sketch, "E4415", {"start": v(51.28, -31.09) * mm, "end": v(51.46, -31.2) * mm});
            skLineSegment(sketch, "E4416", {"start": v(51.46, -31.2) * mm, "end": v(51.64, -31.3) * mm});
            skLineSegment(sketch, "E4417", {"start": v(51.64, -31.3) * mm, "end": v(51.82, -31.4) * mm});
            skLineSegment(sketch, "E4418", {"start": v(51.82, -31.4) * mm, "end": v(52, -31.51) * mm});
            skLineSegment(sketch, "E4419", {"start": v(52, -31.51) * mm, "end": v(52.17, -31.62) * mm});
            skLineSegment(sketch, "E4420", {"start": v(52.17, -31.62) * mm, "end": v(52.35, -31.72) * mm});
            skLineSegment(sketch, "E4421", {"start": v(52.35, -31.72) * mm, "end": v(52.53, -31.83) * mm});
            skLineSegment(sketch, "E4422", {"start": v(52.53, -31.83) * mm, "end": v(52.7, -31.93) * mm});
            skLineSegment(sketch, "E4423", {"start": v(52.7, -31.93) * mm, "end": v(52.89, -32.04) * mm});
            skLineSegment(sketch, "E4424", {"start": v(52.89, -32.04) * mm, "end": v(53.08, -32.15) * mm});
            skLineSegment(sketch, "E4425", {"start": v(53.08, -32.15) * mm, "end": v(53.28, -32.23) * mm});
            skLineSegment(sketch, "E4426", {"start": v(53.28, -32.23) * mm, "end": v(53.5, -32.25) * mm});
            skLineSegment(sketch, "E4427", {"start": v(53.5, -32.25) * mm, "end": v(53.7, -32.2) * mm});
            skLineSegment(sketch, "E4428", {"start": v(53.7, -32.2) * mm, "end": v(53.9, -32.11) * mm});
            skLineSegment(sketch, "E4429", {"start": v(53.9, -32.11) * mm, "end": v(54.06, -31.98) * mm});
            skLineSegment(sketch, "E4430", {"start": v(54.06, -31.98) * mm, "end": v(54.19, -31.8) * mm});
            skLineSegment(sketch, "E4431", {"start": v(54.19, -31.8) * mm, "end": v(54.26, -31.6) * mm});
            skLineSegment(sketch, "E4432", {"start": v(54.26, -31.6) * mm, "end": v(54.27, -31.38) * mm});
            skLineSegment(sketch, "E4433", {"start": v(54.27, -31.38) * mm, "end": v(54.23, -31.17) * mm});
            skLineSegment(sketch, "E4434", {"start": v(54.23, -31.17) * mm, "end": v(54.14, -30.98) * mm});
            skLineSegment(sketch, "E4435", {"start": v(54.14, -30.98) * mm, "end": v(54, -30.82) * mm});
            skLineSegment(sketch, "E4436", {"start": v(54, -30.82) * mm, "end": v(53.83, -30.7) * mm});
            skLineSegment(sketch, "E4437", {"start": v(53.83, -30.7) * mm, "end": v(53.65, -30.6) * mm});
            skLineSegment(sketch, "E4438", {"start": v(53.65, -30.6) * mm, "end": v(53.47, -30.5) * mm});
            skLineSegment(sketch, "E4439", {"start": v(53.47, -30.5) * mm, "end": v(53.3, -30.4) * mm});
            skLineSegment(sketch, "E4440", {"start": v(53.3, -30.4) * mm, "end": v(53.11, -30.3) * mm});
            skLineSegment(sketch, "E4441", {"start": v(53.11, -30.3) * mm, "end": v(52.93, -30.2) * mm});
            skLineSegment(sketch, "E4442", {"start": v(52.93, -30.2) * mm, "end": v(52.75, -30.1) * mm});
            skLineSegment(sketch, "E4443", {"start": v(52.75, -30.1) * mm, "end": v(52.57, -30) * mm});
            skLineSegment(sketch, "E4444", {"start": v(52.57, -30) * mm, "end": v(52.38, -29.89) * mm});
            skLineSegment(sketch, "E4445", {"start": v(52.38, -29.89) * mm, "end": v(52.2, -29.79) * mm});
            skLineSegment(sketch, "E4446", {"start": v(52.2, -29.79) * mm, "end": v(52.02, -29.69) * mm});
            skLineSegment(sketch, "E4447", {"start": v(52.02, -29.69) * mm, "end": v(51.84, -29.58) * mm});
            skLineSegment(sketch, "E4448", {"start": v(51.84, -29.58) * mm, "end": v(51.66, -29.48) * mm});
            skLineSegment(sketch, "E4449", {"start": v(51.66, -29.48) * mm, "end": v(51.53, -29.4) * mm});
            skLineSegment(sketch, "E4450", {"start": v(51.53, -29.4) * mm, "end": v(51.63, -29.23) * mm});
            skLineSegment(sketch, "E4451", {"start": v(51.63, -29.23) * mm, "end": v(51.72, -29.05) * mm});
            skLineSegment(sketch, "E4452", {"start": v(51.72, -29.05) * mm, "end": v(51.82, -28.87) * mm});
            skLineSegment(sketch, "E4453", {"start": v(51.82, -28.87) * mm, "end": v(51.92, -28.68) * mm});
            skLineSegment(sketch, "E4454", {"start": v(51.92, -28.68) * mm, "end": v(52.01, -28.5) * mm});
            skLineSegment(sketch, "E4455", {"start": v(52.01, -28.5) * mm, "end": v(52.11, -28.32) * mm});
            skLineSegment(sketch, "E4456", {"start": v(52.11, -28.32) * mm, "end": v(52.2, -28.14) * mm});
            skLineSegment(sketch, "E4457", {"start": v(52.2, -28.14) * mm, "end": v(52.3, -27.96) * mm});
            skLineSegment(sketch, "E4458", {"start": v(52.3, -27.96) * mm, "end": v(52.4, -27.78) * mm});
            skLineSegment(sketch, "E4459", {"start": v(52.4, -27.78) * mm, "end": v(52.5, -27.6) * mm});
            skLineSegment(sketch, "E4460", {"start": v(52.5, -27.6) * mm, "end": v(52.6, -27.41) * mm});
            skLineSegment(sketch, "E4461", {"start": v(52.6, -27.41) * mm, "end": v(52.65, -27.32) * mm});
            skLineSegment(sketch, "E4462", {"start": v(52.65, -27.32) * mm, "end": v(52.83, -27.41) * mm});
            skLineSegment(sketch, "E4463", {"start": v(52.83, -27.41) * mm, "end": v(53.01, -27.5) * mm});
            skLineSegment(sketch, "E4464", {"start": v(53.01, -27.5) * mm, "end": v(53.2, -27.6) * mm});
            skLineSegment(sketch, "E4465", {"start": v(53.2, -27.6) * mm, "end": v(53.39, -27.7) * mm});
            skLineSegment(sketch, "E4466", {"start": v(53.39, -27.7) * mm, "end": v(53.57, -27.79) * mm});
            skLineSegment(sketch, "E4467", {"start": v(53.57, -27.79) * mm, "end": v(53.76, -27.89) * mm});
            skLineSegment(sketch, "E4468", {"start": v(53.76, -27.89) * mm, "end": v(53.94, -27.98) * mm});
            skLineSegment(sketch, "E4469", {"start": v(53.94, -27.98) * mm, "end": v(54.12, -28.07) * mm});
            skLineSegment(sketch, "E4470", {"start": v(54.12, -28.07) * mm, "end": v(54.31, -28.17) * mm});
            skLineSegment(sketch, "E4471", {"start": v(54.31, -28.17) * mm, "end": v(54.5, -28.26) * mm});
            skLineSegment(sketch, "E4472", {"start": v(54.5, -28.26) * mm, "end": v(54.68, -28.36) * mm});
            skLineSegment(sketch, "E4473", {"start": v(54.68, -28.36) * mm, "end": v(54.87, -28.45) * mm});
            skLineSegment(sketch, "E4474", {"start": v(54.87, -28.45) * mm, "end": v(55.07, -28.55) * mm});
            skLineSegment(sketch, "E4475", {"start": v(55.07, -28.55) * mm, "end": v(55.27, -28.6) * mm});
            skLineSegment(sketch, "E4476", {"start": v(55.27, -28.6) * mm, "end": v(55.49, -28.61) * mm});
            skLineSegment(sketch, "E4477", {"start": v(55.49, -28.61) * mm, "end": v(55.7, -28.56) * mm});
            skLineSegment(sketch, "E4478", {"start": v(55.7, -28.56) * mm, "end": v(55.88, -28.46) * mm});
            skLineSegment(sketch, "E4479", {"start": v(55.88, -28.46) * mm, "end": v(56.04, -28.3) * mm});
            skLineSegment(sketch, "E4480", {"start": v(56.04, -28.3) * mm, "end": v(56.15, -28.12) * mm});
            skLineSegment(sketch, "E4481", {"start": v(56.15, -28.12) * mm, "end": v(56.2, -27.92) * mm});
            skLineSegment(sketch, "E4482", {"start": v(56.2, -27.92) * mm, "end": v(56.2, -27.7) * mm});
            skLineSegment(sketch, "E4483", {"start": v(56.2, -27.7) * mm, "end": v(56.15, -27.5) * mm});
            skLineSegment(sketch, "E4484", {"start": v(56.15, -27.5) * mm, "end": v(56.05, -27.3) * mm});
            skLineSegment(sketch, "E4485", {"start": v(56.05, -27.3) * mm, "end": v(55.9, -27.15) * mm});
            skLineSegment(sketch, "E4486", {"start": v(55.9, -27.15) * mm, "end": v(55.72, -27.05) * mm});
            skLineSegment(sketch, "E4487", {"start": v(55.72, -27.05) * mm, "end": v(55.53, -26.96) * mm});
            skLineSegment(sketch, "E4488", {"start": v(55.53, -26.96) * mm, "end": v(55.35, -26.87) * mm});
            skLineSegment(sketch, "E4489", {"start": v(55.35, -26.87) * mm, "end": v(55.16, -26.78) * mm});
            skLineSegment(sketch, "E4490", {"start": v(55.16, -26.78) * mm, "end": v(54.98, -26.7) * mm});
            skLineSegment(sketch, "E4491", {"start": v(54.98, -26.7) * mm, "end": v(54.79, -26.6) * mm});
            skLineSegment(sketch, "E4492", {"start": v(54.79, -26.6) * mm, "end": v(54.6, -26.51) * mm});
            skLineSegment(sketch, "E4493", {"start": v(54.6, -26.51) * mm, "end": v(54.42, -26.43) * mm});
            skLineSegment(sketch, "E4494", {"start": v(54.42, -26.43) * mm, "end": v(54.22, -26.33) * mm});
            skLineSegment(sketch, "E4495", {"start": v(54.22, -26.33) * mm, "end": v(54.04, -26.25) * mm});
            skLineSegment(sketch, "E4496", {"start": v(54.04, -26.25) * mm, "end": v(53.85, -26.16) * mm});
            skLineSegment(sketch, "E4497", {"start": v(53.85, -26.16) * mm, "end": v(53.66, -26.07) * mm});
            skLineSegment(sketch, "E4498", {"start": v(53.66, -26.07) * mm, "end": v(53.48, -25.98) * mm});
            skLineSegment(sketch, "E4499", {"start": v(53.48, -25.98) * mm, "end": v(53.34, -25.91) * mm});
            skLineSegment(sketch, "E4500", {"start": v(53.34, -25.91) * mm, "end": v(53.43, -25.73) * mm});
            skLineSegment(sketch, "E4501", {"start": v(53.43, -25.73) * mm, "end": v(53.51, -25.54) * mm});
            skLineSegment(sketch, "E4502", {"start": v(53.51, -25.54) * mm, "end": v(53.6, -25.35) * mm});
            skLineSegment(sketch, "E4503", {"start": v(53.6, -25.35) * mm, "end": v(53.68, -25.16) * mm});
            skLineSegment(sketch, "E4504", {"start": v(53.68, -25.16) * mm, "end": v(53.77, -24.97) * mm});
            skLineSegment(sketch, "E4505", {"start": v(53.77, -24.97) * mm, "end": v(53.85, -24.79) * mm});
            skLineSegment(sketch, "E4506", {"start": v(53.85, -24.79) * mm, "end": v(53.94, -24.6) * mm});
            skLineSegment(sketch, "E4507", {"start": v(53.94, -24.6) * mm, "end": v(54.02, -24.41) * mm});
            skLineSegment(sketch, "E4508", {"start": v(54.02, -24.41) * mm, "end": v(54.1, -24.22) * mm});
            skLineSegment(sketch, "E4509", {"start": v(54.1, -24.22) * mm, "end": v(54.2, -24.04) * mm});
            skLineSegment(sketch, "E4510", {"start": v(54.2, -24.04) * mm, "end": v(54.28, -23.85) * mm});
            skLineSegment(sketch, "E4511", {"start": v(54.28, -23.85) * mm, "end": v(54.32, -23.75) * mm});
            skLineSegment(sketch, "E4512", {"start": v(54.32, -23.75) * mm, "end": v(54.5, -23.83) * mm});
            skLineSegment(sketch, "E4513", {"start": v(54.5, -23.83) * mm, "end": v(54.7, -23.92) * mm});
            skLineSegment(sketch, "E4514", {"start": v(54.7, -23.92) * mm, "end": v(54.9, -24) * mm});
            skLineSegment(sketch, "E4515", {"start": v(54.9, -24) * mm, "end": v(55.08, -24.08) * mm});
            skLineSegment(sketch, "E4516", {"start": v(55.08, -24.08) * mm, "end": v(55.27, -24.16) * mm});
            skLineSegment(sketch, "E4517", {"start": v(55.27, -24.16) * mm, "end": v(55.46, -24.25) * mm});
            skLineSegment(sketch, "E4518", {"start": v(55.46, -24.25) * mm, "end": v(55.65, -24.33) * mm});
            skLineSegment(sketch, "E4519", {"start": v(55.65, -24.33) * mm, "end": v(55.84, -24.4) * mm});
            skLineSegment(sketch, "E4520", {"start": v(55.84, -24.4) * mm, "end": v(56.04, -24.5) * mm});
            skLineSegment(sketch, "E4521", {"start": v(56.04, -24.5) * mm, "end": v(56.23, -24.57) * mm});
            skLineSegment(sketch, "E4522", {"start": v(56.23, -24.57) * mm, "end": v(56.42, -24.65) * mm});
            skLineSegment(sketch, "E4523", {"start": v(56.42, -24.65) * mm, "end": v(56.61, -24.74) * mm});
            skLineSegment(sketch, "E4524", {"start": v(56.61, -24.74) * mm, "end": v(56.81, -24.82) * mm});
            skLineSegment(sketch, "E4525", {"start": v(56.81, -24.82) * mm, "end": v(57.02, -24.87) * mm});
            skLineSegment(sketch, "E4526", {"start": v(57.02, -24.87) * mm, "end": v(57.24, -24.86) * mm});
            skLineSegment(sketch, "E4527", {"start": v(57.24, -24.86) * mm, "end": v(57.44, -24.8) * mm});
            skLineSegment(sketch, "E4528", {"start": v(57.44, -24.8) * mm, "end": v(57.62, -24.68) * mm});
            skLineSegment(sketch, "E4529", {"start": v(57.62, -24.68) * mm, "end": v(57.77, -24.52) * mm});
            skLineSegment(sketch, "E4530", {"start": v(57.77, -24.52) * mm, "end": v(57.86, -24.33) * mm});
            skLineSegment(sketch, "E4531", {"start": v(57.86, -24.33) * mm, "end": v(57.9, -24.12) * mm});
            skLineSegment(sketch, "E4532", {"start": v(57.9, -24.12) * mm, "end": v(57.9, -23.9) * mm});
            skLineSegment(sketch, "E4533", {"start": v(57.9, -23.9) * mm, "end": v(57.83, -23.7) * mm});
            skLineSegment(sketch, "E4534", {"start": v(57.83, -23.7) * mm, "end": v(57.71, -23.52) * mm});
            skLineSegment(sketch, "E4535", {"start": v(57.71, -23.52) * mm, "end": v(57.55, -23.38) * mm});
            skLineSegment(sketch, "E4536", {"start": v(57.55, -23.38) * mm, "end": v(57.37, -23.29) * mm});
            skLineSegment(sketch, "E4537", {"start": v(57.37, -23.29) * mm, "end": v(57.18, -23.2) * mm});
            skLineSegment(sketch, "E4538", {"start": v(57.18, -23.2) * mm, "end": v(56.99, -23.13) * mm});
            skLineSegment(sketch, "E4539", {"start": v(56.99, -23.13) * mm, "end": v(56.8, -23.05) * mm});
            skLineSegment(sketch, "E4540", {"start": v(56.8, -23.05) * mm, "end": v(56.6, -22.98) * mm});
            skLineSegment(sketch, "E4541", {"start": v(56.6, -22.98) * mm, "end": v(56.4, -22.9) * mm});
            skLineSegment(sketch, "E4542", {"start": v(56.4, -22.9) * mm, "end": v(56.22, -22.82) * mm});
            skLineSegment(sketch, "E4543", {"start": v(56.22, -22.82) * mm, "end": v(56.03, -22.75) * mm});
            skLineSegment(sketch, "E4544", {"start": v(56.03, -22.75) * mm, "end": v(55.83, -22.67) * mm});
            skLineSegment(sketch, "E4545", {"start": v(55.83, -22.67) * mm, "end": v(55.64, -22.6) * mm});
            skLineSegment(sketch, "E4546", {"start": v(55.64, -22.6) * mm, "end": v(55.45, -22.52) * mm});
            skLineSegment(sketch, "E4547", {"start": v(55.45, -22.52) * mm, "end": v(55.25, -22.44) * mm});
            skLineSegment(sketch, "E4548", {"start": v(55.25, -22.44) * mm, "end": v(55.06, -22.36) * mm});
            skLineSegment(sketch, "E4549", {"start": v(55.06, -22.36) * mm, "end": v(54.92, -22.3) * mm});
            skLineSegment(sketch, "E4550", {"start": v(54.92, -22.3) * mm, "end": v(55, -22.11) * mm});
            skLineSegment(sketch, "E4551", {"start": v(55, -22.11) * mm, "end": v(55.06, -21.92) * mm});
            skLineSegment(sketch, "E4552", {"start": v(55.06, -21.92) * mm, "end": v(55.14, -21.73) * mm});
            skLineSegment(sketch, "E4553", {"start": v(55.14, -21.73) * mm, "end": v(55.2, -21.53) * mm});
            skLineSegment(sketch, "E4554", {"start": v(55.2, -21.53) * mm, "end": v(55.28, -21.34) * mm});
            skLineSegment(sketch, "E4555", {"start": v(55.28, -21.34) * mm, "end": v(55.35, -21.15) * mm});
            skLineSegment(sketch, "E4556", {"start": v(55.35, -21.15) * mm, "end": v(55.43, -20.96) * mm});
            skLineSegment(sketch, "E4557", {"start": v(55.43, -20.96) * mm, "end": v(55.5, -20.76) * mm});
            skLineSegment(sketch, "E4558", {"start": v(55.5, -20.76) * mm, "end": v(55.57, -20.57) * mm});
            skLineSegment(sketch, "E4559", {"start": v(55.57, -20.57) * mm, "end": v(55.64, -20.38) * mm});
            skLineSegment(sketch, "E4560", {"start": v(55.64, -20.38) * mm, "end": v(55.72, -20.18) * mm});
            skLineSegment(sketch, "E4561", {"start": v(55.72, -20.18) * mm, "end": v(55.75, -20.09) * mm});
            skLineSegment(sketch, "E4562", {"start": v(55.75, -20.09) * mm, "end": v(55.95, -20.15) * mm});
            skLineSegment(sketch, "E4563", {"start": v(55.95, -20.15) * mm, "end": v(56.14, -20.22) * mm});
            skLineSegment(sketch, "E4564", {"start": v(56.14, -20.22) * mm, "end": v(56.34, -20.3) * mm});
            skLineSegment(sketch, "E4565", {"start": v(56.34, -20.3) * mm, "end": v(56.54, -20.36) * mm});
            skLineSegment(sketch, "E4566", {"start": v(56.54, -20.36) * mm, "end": v(56.73, -20.43) * mm});
            skLineSegment(sketch, "E4567", {"start": v(56.73, -20.43) * mm, "end": v(56.93, -20.5) * mm});
            skLineSegment(sketch, "E4568", {"start": v(56.93, -20.5) * mm, "end": v(57.12, -20.57) * mm});
            skLineSegment(sketch, "E4569", {"start": v(57.12, -20.57) * mm, "end": v(57.32, -20.64) * mm});
            skLineSegment(sketch, "E4570", {"start": v(57.32, -20.64) * mm, "end": v(57.52, -20.71) * mm});
            skLineSegment(sketch, "E4571", {"start": v(57.52, -20.71) * mm, "end": v(57.71, -20.78) * mm});
            skLineSegment(sketch, "E4572", {"start": v(57.71, -20.78) * mm, "end": v(57.9, -20.85) * mm});
            skLineSegment(sketch, "E4573", {"start": v(57.9, -20.85) * mm, "end": v(58.1, -20.92) * mm});
            skLineSegment(sketch, "E4574", {"start": v(58.1, -20.92) * mm, "end": v(58.31, -21) * mm});
            skLineSegment(sketch, "E4575", {"start": v(58.31, -21) * mm, "end": v(58.53, -21.02) * mm});
            skLineSegment(sketch, "E4576", {"start": v(58.53, -21.02) * mm, "end": v(58.74, -21) * mm});
            skLineSegment(sketch, "E4577", {"start": v(58.74, -21) * mm, "end": v(58.94, -20.92) * mm});
            skLineSegment(sketch, "E4578", {"start": v(58.94, -20.92) * mm, "end": v(59.11, -20.8) * mm});
            skLineSegment(sketch, "E4579", {"start": v(59.11, -20.8) * mm, "end": v(59.24, -20.62) * mm});
            skLineSegment(sketch, "E4580", {"start": v(59.24, -20.62) * mm, "end": v(59.33, -20.43) * mm});
            skLineSegment(sketch, "E4581", {"start": v(59.33, -20.43) * mm, "end": v(59.36, -20.21) * mm});
            skLineSegment(sketch, "E4582", {"start": v(59.36, -20.21) * mm, "end": v(59.33, -20) * mm});
            skLineSegment(sketch, "E4583", {"start": v(59.33, -20) * mm, "end": v(59.25, -19.8) * mm});
            skLineSegment(sketch, "E4584", {"start": v(59.25, -19.8) * mm, "end": v(59.12, -19.63) * mm});
            skLineSegment(sketch, "E4585", {"start": v(59.12, -19.63) * mm, "end": v(58.96, -19.5) * mm});
            skLineSegment(sketch, "E4586", {"start": v(58.96, -19.5) * mm, "end": v(58.77, -19.42) * mm});
            skLineSegment(sketch, "E4587", {"start": v(58.77, -19.42) * mm, "end": v(58.57, -19.35) * mm});
            skLineSegment(sketch, "E4588", {"start": v(58.57, -19.35) * mm, "end": v(58.38, -19.29) * mm});
            skLineSegment(sketch, "E4589", {"start": v(58.38, -19.29) * mm, "end": v(58.18, -19.23) * mm});
            skLineSegment(sketch, "E4590", {"start": v(58.18, -19.23) * mm, "end": v(57.98, -19.16) * mm});
            skLineSegment(sketch, "E4591", {"start": v(57.98, -19.16) * mm, "end": v(57.78, -19.1) * mm});
            skLineSegment(sketch, "E4592", {"start": v(57.78, -19.1) * mm, "end": v(57.59, -19.03) * mm});
            skLineSegment(sketch, "E4593", {"start": v(57.59, -19.03) * mm, "end": v(57.4, -18.97) * mm});
            skLineSegment(sketch, "E4594", {"start": v(57.4, -18.97) * mm, "end": v(57.19, -18.9) * mm});
            skLineSegment(sketch, "E4595", {"start": v(57.19, -18.9) * mm, "end": v(57, -18.84) * mm});
            skLineSegment(sketch, "E4596", {"start": v(57, -18.84) * mm, "end": v(56.8, -18.78) * mm});
            skLineSegment(sketch, "E4597", {"start": v(56.8, -18.78) * mm, "end": v(56.6, -18.71) * mm});
            skLineSegment(sketch, "E4598", {"start": v(56.6, -18.71) * mm, "end": v(56.4, -18.65) * mm});
            skLineSegment(sketch, "E4599", {"start": v(56.4, -18.65) * mm, "end": v(56.26, -18.6) * mm});
            skLineSegment(sketch, "E4600", {"start": v(56.26, -18.6) * mm, "end": v(56.32, -18.4) * mm});
            skLineSegment(sketch, "E4601", {"start": v(56.32, -18.4) * mm, "end": v(56.38, -18.2) * mm});
            skLineSegment(sketch, "E4602", {"start": v(56.38, -18.2) * mm, "end": v(56.44, -18.01) * mm});
            skLineSegment(sketch, "E4603", {"start": v(56.44, -18.01) * mm, "end": v(56.5, -17.81) * mm});
            skLineSegment(sketch, "E4604", {"start": v(56.5, -17.81) * mm, "end": v(56.56, -17.62) * mm});
            skLineSegment(sketch, "E4605", {"start": v(56.56, -17.62) * mm, "end": v(56.62, -17.42) * mm});
            skLineSegment(sketch, "E4606", {"start": v(56.62, -17.42) * mm, "end": v(56.68, -17.22) * mm});
            skLineSegment(sketch, "E4607", {"start": v(56.68, -17.22) * mm, "end": v(56.74, -17.02) * mm});
            skLineSegment(sketch, "E4608", {"start": v(56.74, -17.02) * mm, "end": v(56.8, -16.83) * mm});
            skLineSegment(sketch, "E4609", {"start": v(56.8, -16.83) * mm, "end": v(56.86, -16.63) * mm});
            skLineSegment(sketch, "E4610", {"start": v(56.86, -16.63) * mm, "end": v(56.92, -16.43) * mm});
            skLineSegment(sketch, "E4611", {"start": v(56.92, -16.43) * mm, "end": v(56.95, -16.33) * mm});
            skLineSegment(sketch, "E4612", {"start": v(56.95, -16.33) * mm, "end": v(57.14, -16.39) * mm});
            skLineSegment(sketch, "E4613", {"start": v(57.14, -16.39) * mm, "end": v(57.34, -16.44) * mm});
            skLineSegment(sketch, "E4614", {"start": v(57.34, -16.44) * mm, "end": v(57.55, -16.5) * mm});
            skLineSegment(sketch, "E4615", {"start": v(57.55, -16.5) * mm, "end": v(57.74, -16.56) * mm});
            skLineSegment(sketch, "E4616", {"start": v(57.74, -16.56) * mm, "end": v(57.94, -16.61) * mm});
            skLineSegment(sketch, "E4617", {"start": v(57.94, -16.61) * mm, "end": v(58.15, -16.67) * mm});
            skLineSegment(sketch, "E4618", {"start": v(58.15, -16.67) * mm, "end": v(58.34, -16.73) * mm});
            skLineSegment(sketch, "E4619", {"start": v(58.34, -16.73) * mm, "end": v(58.54, -16.78) * mm});
            skLineSegment(sketch, "E4620", {"start": v(58.54, -16.78) * mm, "end": v(58.75, -16.84) * mm});
            skLineSegment(sketch, "E4621", {"start": v(58.75, -16.84) * mm, "end": v(58.94, -16.9) * mm});
            skLineSegment(sketch, "E4622", {"start": v(58.94, -16.9) * mm, "end": v(59.14, -16.95) * mm});
            skLineSegment(sketch, "E4623", {"start": v(59.14, -16.95) * mm, "end": v(59.35, -17) * mm});
            skLineSegment(sketch, "E4624", {"start": v(59.35, -17) * mm, "end": v(59.56, -17.07) * mm});
            skLineSegment(sketch, "E4625", {"start": v(59.56, -17.07) * mm, "end": v(59.77, -17.09) * mm});
            skLineSegment(sketch, "E4626", {"start": v(59.77, -17.09) * mm, "end": v(59.98, -17.05) * mm});
            skLineSegment(sketch, "E4627", {"start": v(59.98, -17.05) * mm, "end": v(60.18, -16.96) * mm});
            skLineSegment(sketch, "E4628", {"start": v(60.18, -16.96) * mm, "end": v(60.34, -16.82) * mm});
            skLineSegment(sketch, "E4629", {"start": v(60.34, -16.82) * mm, "end": v(60.46, -16.64) * mm});
            skLineSegment(sketch, "E4630", {"start": v(60.46, -16.64) * mm, "end": v(60.54, -16.44) * mm});
            skLineSegment(sketch, "E4631", {"start": v(60.54, -16.44) * mm, "end": v(60.55, -16.22) * mm});
            skLineSegment(sketch, "E4632", {"start": v(60.55, -16.22) * mm, "end": v(60.51, -16.01) * mm});
            skLineSegment(sketch, "E4633", {"start": v(60.51, -16.01) * mm, "end": v(60.42, -15.82) * mm});
            skLineSegment(sketch, "E4634", {"start": v(60.42, -15.82) * mm, "end": v(60.28, -15.66) * mm});
            skLineSegment(sketch, "E4635", {"start": v(60.28, -15.66) * mm, "end": v(60.1, -15.54) * mm});
            skLineSegment(sketch, "E4636", {"start": v(60.1, -15.54) * mm, "end": v(59.9, -15.47) * mm});
            skLineSegment(sketch, "E4637", {"start": v(59.9, -15.47) * mm, "end": v(59.7, -15.42) * mm});
            skLineSegment(sketch, "E4638", {"start": v(59.7, -15.42) * mm, "end": v(59.51, -15.37) * mm});
            skLineSegment(sketch, "E4639", {"start": v(59.51, -15.37) * mm, "end": v(59.31, -15.32) * mm});
            skLineSegment(sketch, "E4640", {"start": v(59.31, -15.32) * mm, "end": v(59.11, -15.26) * mm});
            skLineSegment(sketch, "E4641", {"start": v(59.11, -15.26) * mm, "end": v(58.9, -15.21) * mm});
            skLineSegment(sketch, "E4642", {"start": v(58.9, -15.21) * mm, "end": v(58.7, -15.16) * mm});
            skLineSegment(sketch, "E4643", {"start": v(58.7, -15.16) * mm, "end": v(58.5, -15.11) * mm});
            skLineSegment(sketch, "E4644", {"start": v(58.5, -15.11) * mm, "end": v(58.3, -15.06) * mm});
            skLineSegment(sketch, "E4645", {"start": v(58.3, -15.06) * mm, "end": v(58.1, -15) * mm});
            skLineSegment(sketch, "E4646", {"start": v(58.1, -15) * mm, "end": v(57.9, -14.96) * mm});
            skLineSegment(sketch, "E4647", {"start": v(57.9, -14.96) * mm, "end": v(57.7, -14.9) * mm});
            skLineSegment(sketch, "E4648", {"start": v(57.7, -14.9) * mm, "end": v(57.5, -14.86) * mm});
            skLineSegment(sketch, "E4649", {"start": v(57.5, -14.86) * mm, "end": v(57.35, -14.82) * mm});
            skLineSegment(sketch, "E4650", {"start": v(57.35, -14.82) * mm, "end": v(57.4, -14.62) * mm});
            skLineSegment(sketch, "E4651", {"start": v(57.4, -14.62) * mm, "end": v(57.45, -14.42) * mm});
            skLineSegment(sketch, "E4652", {"start": v(57.45, -14.42) * mm, "end": v(57.5, -14.22) * mm});
            skLineSegment(sketch, "E4653", {"start": v(57.5, -14.22) * mm, "end": v(57.54, -14.02) * mm});
            skLineSegment(sketch, "E4654", {"start": v(57.54, -14.02) * mm, "end": v(57.59, -13.82) * mm});
            skLineSegment(sketch, "E4655", {"start": v(57.59, -13.82) * mm, "end": v(57.63, -13.61) * mm});
            skLineSegment(sketch, "E4656", {"start": v(57.63, -13.61) * mm, "end": v(57.68, -13.41) * mm});
            skLineSegment(sketch, "E4657", {"start": v(57.68, -13.41) * mm, "end": v(57.73, -13.21) * mm});
            skLineSegment(sketch, "E4658", {"start": v(57.73, -13.21) * mm, "end": v(57.77, -13.01) * mm});
            skLineSegment(sketch, "E4659", {"start": v(57.77, -13.01) * mm, "end": v(57.82, -12.81) * mm});
            skLineSegment(sketch, "E4660", {"start": v(57.82, -12.81) * mm, "end": v(57.87, -12.61) * mm});
            skLineSegment(sketch, "E4661", {"start": v(57.87, -12.61) * mm, "end": v(57.9, -12.5) * mm});
            skLineSegment(sketch, "E4662", {"start": v(57.9, -12.5) * mm, "end": v(58.1, -12.55) * mm});
            skLineSegment(sketch, "E4663", {"start": v(58.1, -12.55) * mm, "end": v(58.3, -12.6) * mm});
            skLineSegment(sketch, "E4664", {"start": v(58.3, -12.6) * mm, "end": v(58.5, -12.64) * mm});
            skLineSegment(sketch, "E4665", {"start": v(58.5, -12.64) * mm, "end": v(58.7, -12.68) * mm});
            skLineSegment(sketch, "E4666", {"start": v(58.7, -12.68) * mm, "end": v(58.9, -12.72) * mm});
            skLineSegment(sketch, "E4667", {"start": v(58.9, -12.72) * mm, "end": v(59.1, -12.77) * mm});
            skLineSegment(sketch, "E4668", {"start": v(59.1, -12.77) * mm, "end": v(59.31, -12.81) * mm});
            skLineSegment(sketch, "E4669", {"start": v(59.31, -12.81) * mm, "end": v(59.51, -12.85) * mm});
            skLineSegment(sketch, "E4670", {"start": v(59.51, -12.85) * mm, "end": v(59.72, -12.9) * mm});
            skLineSegment(sketch, "E4671", {"start": v(59.72, -12.9) * mm, "end": v(59.92, -12.94) * mm});
            skLineSegment(sketch, "E4672", {"start": v(59.92, -12.94) * mm, "end": v(60.12, -12.98) * mm});
            skLineSegment(sketch, "E4673", {"start": v(60.12, -12.98) * mm, "end": v(60.33, -13.03) * mm});
            skLineSegment(sketch, "E4674", {"start": v(60.33, -13.03) * mm, "end": v(60.55, -13.07) * mm});
            skLineSegment(sketch, "E4675", {"start": v(60.55, -13.07) * mm, "end": v(60.76, -13.08) * mm});
            skLineSegment(sketch, "E4676", {"start": v(60.76, -13.08) * mm, "end": v(60.97, -13.02) * mm});
            skLineSegment(sketch, "E4677", {"start": v(60.97, -13.02) * mm, "end": v(61.16, -12.92) * mm});
            skLineSegment(sketch, "E4678", {"start": v(61.16, -12.92) * mm, "end": v(61.31, -12.77) * mm});
            skLineSegment(sketch, "E4679", {"start": v(61.31, -12.77) * mm, "end": v(61.42, -12.59) * mm});
            skLineSegment(sketch, "E4680", {"start": v(61.42, -12.59) * mm, "end": v(61.48, -12.38) * mm});
            skLineSegment(sketch, "E4681", {"start": v(61.48, -12.38) * mm, "end": v(61.48, -12.17) * mm});
            skLineSegment(sketch, "E4682", {"start": v(61.48, -12.17) * mm, "end": v(61.43, -11.96) * mm});
            skLineSegment(sketch, "E4683", {"start": v(61.43, -11.96) * mm, "end": v(61.32, -11.77) * mm});
            skLineSegment(sketch, "E4684", {"start": v(61.32, -11.77) * mm, "end": v(61.17, -11.62) * mm});
            skLineSegment(sketch, "E4685", {"start": v(61.17, -11.62) * mm, "end": v(60.99, -11.5) * mm});
            skLineSegment(sketch, "E4686", {"start": v(60.99, -11.5) * mm, "end": v(60.79, -11.46) * mm});
            skLineSegment(sketch, "E4687", {"start": v(60.79, -11.46) * mm, "end": v(60.59, -11.42) * mm});
            skLineSegment(sketch, "E4688", {"start": v(60.59, -11.42) * mm, "end": v(60.39, -11.38) * mm});
            skLineSegment(sketch, "E4689", {"start": v(60.39, -11.38) * mm, "end": v(60.18, -11.34) * mm});
            skLineSegment(sketch, "E4690", {"start": v(60.18, -11.34) * mm, "end": v(59.98, -11.3) * mm});
            skLineSegment(sketch, "E4691", {"start": v(59.98, -11.3) * mm, "end": v(59.77, -11.26) * mm});
            skLineSegment(sketch, "E4692", {"start": v(59.77, -11.26) * mm, "end": v(59.57, -11.23) * mm});
            skLineSegment(sketch, "E4693", {"start": v(59.57, -11.23) * mm, "end": v(59.37, -11.19) * mm});
            skLineSegment(sketch, "E4694", {"start": v(59.37, -11.19) * mm, "end": v(59.16, -11.15) * mm});
            skLineSegment(sketch, "E4695", {"start": v(59.16, -11.15) * mm, "end": v(58.96, -11.11) * mm});
            skLineSegment(sketch, "E4696", {"start": v(58.96, -11.11) * mm, "end": v(58.75, -11.08) * mm});
            skLineSegment(sketch, "E4697", {"start": v(58.75, -11.08) * mm, "end": v(58.55, -11.04) * mm});
            skLineSegment(sketch, "E4698", {"start": v(58.55, -11.04) * mm, "end": v(58.34, -11) * mm});
            skLineSegment(sketch, "E4699", {"start": v(58.34, -11) * mm, "end": v(58.2, -10.97) * mm});
            skLineSegment(sketch, "E4700", {"start": v(58.2, -10.97) * mm, "end": v(58.23, -10.77) * mm});
            skLineSegment(sketch, "E4701", {"start": v(58.23, -10.77) * mm, "end": v(58.26, -10.57) * mm});
            skLineSegment(sketch, "E4702", {"start": v(58.26, -10.57) * mm, "end": v(58.3, -10.36) * mm});
            skLineSegment(sketch, "E4703", {"start": v(58.3, -10.36) * mm, "end": v(58.33, -10.16) * mm});
            skLineSegment(sketch, "E4704", {"start": v(58.33, -10.16) * mm, "end": v(58.36, -9.96) * mm});
            skLineSegment(sketch, "E4705", {"start": v(58.36, -9.96) * mm, "end": v(58.4, -9.75) * mm});
            skLineSegment(sketch, "E4706", {"start": v(58.4, -9.75) * mm, "end": v(58.43, -9.55) * mm});
            skLineSegment(sketch, "E4707", {"start": v(58.43, -9.55) * mm, "end": v(58.46, -9.35) * mm});
            skLineSegment(sketch, "E4708", {"start": v(58.46, -9.35) * mm, "end": v(58.5, -9.14) * mm});
            skLineSegment(sketch, "E4709", {"start": v(58.5, -9.14) * mm, "end": v(58.53, -8.94) * mm});
            skLineSegment(sketch, "E4710", {"start": v(58.53, -8.94) * mm, "end": v(58.57, -8.74) * mm});
            skLineSegment(sketch, "E4711", {"start": v(58.57, -8.74) * mm, "end": v(58.58, -8.63) * mm});
            skLineSegment(sketch, "E4712", {"start": v(58.58, -8.63) * mm, "end": v(58.79, -8.66) * mm});
            skLineSegment(sketch, "E4713", {"start": v(58.79, -8.66) * mm, "end": v(58.99, -8.7) * mm});
            skLineSegment(sketch, "E4714", {"start": v(58.99, -8.7) * mm, "end": v(59.2, -8.72) * mm});
            skLineSegment(sketch, "E4715", {"start": v(59.2, -8.72) * mm, "end": v(59.4, -8.75) * mm});
            skLineSegment(sketch, "E4716", {"start": v(59.4, -8.75) * mm, "end": v(59.6, -8.78) * mm});
            skLineSegment(sketch, "E4717", {"start": v(59.6, -8.78) * mm, "end": v(59.82, -8.81) * mm});
            skLineSegment(sketch, "E4718", {"start": v(59.82, -8.81) * mm, "end": v(60.02, -8.84) * mm});
            skLineSegment(sketch, "E4719", {"start": v(60.02, -8.84) * mm, "end": v(60.22, -8.87) * mm});
            skLineSegment(sketch, "E4720", {"start": v(60.22, -8.87) * mm, "end": v(60.43, -8.9) * mm});
            skLineSegment(sketch, "E4721", {"start": v(60.43, -8.9) * mm, "end": v(60.64, -8.93) * mm});
            skLineSegment(sketch, "E4722", {"start": v(60.64, -8.93) * mm, "end": v(60.84, -8.96) * mm});
            skLineSegment(sketch, "E4723", {"start": v(60.84, -8.96) * mm, "end": v(61.05, -9) * mm});
            skLineSegment(sketch, "E4724", {"start": v(61.05, -9) * mm, "end": v(61.27, -9.02) * mm});
            skLineSegment(sketch, "E4725", {"start": v(61.27, -9.02) * mm, "end": v(61.48, -9.01) * mm});
            skLineSegment(sketch, "E4726", {"start": v(61.48, -9.01) * mm, "end": v(61.69, -8.95) * mm});
            skLineSegment(sketch, "E4727", {"start": v(61.69, -8.95) * mm, "end": v(61.87, -8.83) * mm});
            skLineSegment(sketch, "E4728", {"start": v(61.87, -8.83) * mm, "end": v(62.01, -8.67) * mm});
            skLineSegment(sketch, "E4729", {"start": v(62.01, -8.67) * mm, "end": v(62.11, -8.48) * mm});
            skLineSegment(sketch, "E4730", {"start": v(62.11, -8.48) * mm, "end": v(62.15, -8.27) * mm});
            skLineSegment(sketch, "E4731", {"start": v(62.15, -8.27) * mm, "end": v(62.14, -8.05) * mm});
            skLineSegment(sketch, "E4732", {"start": v(62.14, -8.05) * mm, "end": v(62.08, -7.85) * mm});
            skLineSegment(sketch, "E4733", {"start": v(62.08, -7.85) * mm, "end": v(61.96, -7.67) * mm});
            skLineSegment(sketch, "E4734", {"start": v(61.96, -7.67) * mm, "end": v(61.8, -7.53) * mm});
            skLineSegment(sketch, "E4735", {"start": v(61.8, -7.53) * mm, "end": v(61.6, -7.43) * mm});
            skLineSegment(sketch, "E4736", {"start": v(61.6, -7.43) * mm, "end": v(61.4, -7.4) * mm});
            skLineSegment(sketch, "E4737", {"start": v(61.4, -7.4) * mm, "end": v(61.2, -7.36) * mm});
            skLineSegment(sketch, "E4738", {"start": v(61.2, -7.36) * mm, "end": v(61, -7.34) * mm});
            skLineSegment(sketch, "E4739", {"start": v(61, -7.34) * mm, "end": v(60.8, -7.32) * mm});
            skLineSegment(sketch, "E4740", {"start": v(60.8, -7.32) * mm, "end": v(60.59, -7.3) * mm});
            skLineSegment(sketch, "E4741", {"start": v(60.59, -7.3) * mm, "end": v(60.38, -7.27) * mm});
            skLineSegment(sketch, "E4742", {"start": v(60.38, -7.27) * mm, "end": v(60.17, -7.24) * mm});
            skLineSegment(sketch, "E4743", {"start": v(60.17, -7.24) * mm, "end": v(59.97, -7.22) * mm});
            skLineSegment(sketch, "E4744", {"start": v(59.97, -7.22) * mm, "end": v(59.76, -7.2) * mm});
            skLineSegment(sketch, "E4745", {"start": v(59.76, -7.2) * mm, "end": v(59.56, -7.17) * mm});
            skLineSegment(sketch, "E4746", {"start": v(59.56, -7.17) * mm, "end": v(59.35, -7.14) * mm});
            skLineSegment(sketch, "E4747", {"start": v(59.35, -7.14) * mm, "end": v(59.14, -7.12) * mm});
            skLineSegment(sketch, "E4748", {"start": v(59.14, -7.12) * mm, "end": v(58.94, -7.1) * mm});
            skLineSegment(sketch, "E4749", {"start": v(58.94, -7.1) * mm, "end": v(58.79, -7.08) * mm});
            skLineSegment(sketch, "E4750", {"start": v(58.79, -7.08) * mm, "end": v(58.8, -6.87) * mm});
            skLineSegment(sketch, "E4751", {"start": v(58.8, -6.87) * mm, "end": v(58.83, -6.67) * mm});
            skLineSegment(sketch, "E4752", {"start": v(58.83, -6.67) * mm, "end": v(58.85, -6.46) * mm});
            skLineSegment(sketch, "E4753", {"start": v(58.85, -6.46) * mm, "end": v(58.87, -6.26) * mm});
            skLineSegment(sketch, "E4754", {"start": v(58.87, -6.26) * mm, "end": v(58.89, -6.05) * mm});
            skLineSegment(sketch, "E4755", {"start": v(58.89, -6.05) * mm, "end": v(58.9, -5.85) * mm});
            skLineSegment(sketch, "E4756", {"start": v(58.9, -5.85) * mm, "end": v(58.93, -5.64) * mm});
            skLineSegment(sketch, "E4757", {"start": v(58.93, -5.64) * mm, "end": v(58.95, -5.44) * mm});
            skLineSegment(sketch, "E4758", {"start": v(58.95, -5.44) * mm, "end": v(58.97, -5.23) * mm});
            skLineSegment(sketch, "E4759", {"start": v(58.97, -5.23) * mm, "end": v(58.99, -5.03) * mm});
            skLineSegment(sketch, "E4760", {"start": v(58.99, -5.03) * mm, "end": v(59, -4.82) * mm});
            skLineSegment(sketch, "E4761", {"start": v(59, -4.82) * mm, "end": v(59.02, -4.72) * mm});
            skLineSegment(sketch, "E4762", {"start": v(59.02, -4.72) * mm, "end": v(59.22, -4.73) * mm});
            skLineSegment(sketch, "E4763", {"start": v(59.22, -4.73) * mm, "end": v(59.43, -4.75) * mm});
            skLineSegment(sketch, "E4764", {"start": v(59.43, -4.75) * mm, "end": v(59.64, -4.77) * mm});
            skLineSegment(sketch, "E4765", {"start": v(59.64, -4.77) * mm, "end": v(59.85, -4.78) * mm});
            skLineSegment(sketch, "E4766", {"start": v(59.85, -4.78) * mm, "end": v(60.05, -4.8) * mm});
            skLineSegment(sketch, "E4767", {"start": v(60.05, -4.8) * mm, "end": v(60.26, -4.82) * mm});
            skLineSegment(sketch, "E4768", {"start": v(60.26, -4.82) * mm, "end": v(60.47, -4.83) * mm});
            skLineSegment(sketch, "E4769", {"start": v(60.47, -4.83) * mm, "end": v(60.67, -4.85) * mm});
            skLineSegment(sketch, "E4770", {"start": v(60.67, -4.85) * mm, "end": v(60.88, -4.87) * mm});
            skLineSegment(sketch, "E4771", {"start": v(60.88, -4.87) * mm, "end": v(61.09, -4.88) * mm});
            skLineSegment(sketch, "E4772", {"start": v(61.09, -4.88) * mm, "end": v(61.3, -4.9) * mm});
            skLineSegment(sketch, "E4773", {"start": v(61.3, -4.9) * mm, "end": v(61.5, -4.91) * mm});
            skLineSegment(sketch, "E4774", {"start": v(61.5, -4.91) * mm, "end": v(61.73, -4.93) * mm});
            skLineSegment(sketch, "E4775", {"start": v(61.73, -4.93) * mm, "end": v(61.94, -4.9) * mm});
            skLineSegment(sketch, "E4776", {"start": v(61.94, -4.9) * mm, "end": v(62.14, -4.83) * mm});
            skLineSegment(sketch, "E4777", {"start": v(62.14, -4.83) * mm, "end": v(62.31, -4.7) * mm});
            skLineSegment(sketch, "E4778", {"start": v(62.31, -4.7) * mm, "end": v(62.44, -4.53) * mm});
            skLineSegment(sketch, "E4779", {"start": v(62.44, -4.53) * mm, "end": v(62.53, -4.33) * mm});
            skLineSegment(sketch, "E4780", {"start": v(62.53, -4.33) * mm, "end": v(62.56, -4.12) * mm});
            skLineSegment(sketch, "E4781", {"start": v(62.56, -4.12) * mm, "end": v(62.54, -3.9) * mm});
            skLineSegment(sketch, "E4782", {"start": v(62.54, -3.9) * mm, "end": v(62.46, -3.7) * mm});
            skLineSegment(sketch, "E4783", {"start": v(62.46, -3.7) * mm, "end": v(62.33, -3.54) * mm});
            skLineSegment(sketch, "E4784", {"start": v(62.33, -3.54) * mm, "end": v(62.16, -3.4) * mm});
            skLineSegment(sketch, "E4785", {"start": v(62.16, -3.4) * mm, "end": v(61.96, -3.32) * mm});
            skLineSegment(sketch, "E4786", {"start": v(61.96, -3.32) * mm, "end": v(61.76, -3.3) * mm});
            skLineSegment(sketch, "E4787", {"start": v(61.76, -3.3) * mm, "end": v(61.55, -3.28) * mm});
            skLineSegment(sketch, "E4788", {"start": v(61.55, -3.28) * mm, "end": v(61.35, -3.27) * mm});
            skLineSegment(sketch, "E4789", {"start": v(61.35, -3.27) * mm, "end": v(61.14, -3.26) * mm});
            skLineSegment(sketch, "E4790", {"start": v(61.14, -3.26) * mm, "end": v(60.93, -3.25) * mm});
            skLineSegment(sketch, "E4791", {"start": v(60.93, -3.25) * mm, "end": v(60.72, -3.24) * mm});
            skLineSegment(sketch, "E4792", {"start": v(60.72, -3.24) * mm, "end": v(60.52, -3.23) * mm});
            skLineSegment(sketch, "E4793", {"start": v(60.52, -3.23) * mm, "end": v(60.31, -3.22) * mm});
            skLineSegment(sketch, "E4794", {"start": v(60.31, -3.22) * mm, "end": v(60.1, -3.2) * mm});
            skLineSegment(sketch, "E4795", {"start": v(60.1, -3.2) * mm, "end": v(59.9, -3.2) * mm});
            skLineSegment(sketch, "E4796", {"start": v(59.9, -3.2) * mm, "end": v(59.69, -3.18) * mm});
            skLineSegment(sketch, "E4797", {"start": v(59.69, -3.18) * mm, "end": v(59.48, -3.17) * mm});
            skLineSegment(sketch, "E4798", {"start": v(59.48, -3.17) * mm, "end": v(59.27, -3.16) * mm});
            skLineSegment(sketch, "E4799", {"start": v(59.27, -3.16) * mm, "end": v(59.12, -3.15) * mm});
            skLineSegment(sketch, "E4800", {"start": v(59.12, -3.15) * mm, "end": v(59.13, -2.95) * mm});
            skLineSegment(sketch, "E4801", {"start": v(59.13, -2.95) * mm, "end": v(59.14, -2.74) * mm});
            skLineSegment(sketch, "E4802", {"start": v(59.14, -2.74) * mm, "end": v(59.14, -2.54) * mm});
            skLineSegment(sketch, "E4803", {"start": v(59.14, -2.54) * mm, "end": v(59.15, -2.33) * mm});
            skLineSegment(sketch, "E4804", {"start": v(59.15, -2.33) * mm, "end": v(59.16, -2.12) * mm});
            skLineSegment(sketch, "E4805", {"start": v(59.16, -2.12) * mm, "end": v(59.16, -1.92) * mm});
            skLineSegment(sketch, "E4806", {"start": v(59.16, -1.92) * mm, "end": v(59.17, -1.71) * mm});
            skLineSegment(sketch, "E4807", {"start": v(59.17, -1.71) * mm, "end": v(59.18, -1.5) * mm});
            skLineSegment(sketch, "E4808", {"start": v(59.18, -1.5) * mm, "end": v(59.18, -1.3) * mm});
            skLineSegment(sketch, "E4809", {"start": v(59.18, -1.3) * mm, "end": v(59.19, -1.1) * mm});
            skLineSegment(sketch, "E4810", {"start": v(59.19, -1.1) * mm, "end": v(59.2, -0.89) * mm});
            skLineSegment(sketch, "E4811", {"start": v(59.2, -0.89) * mm, "end": v(59.2, -0.78) * mm});
            skLineSegment(sketch, "E4812", {"start": v(-8.05, 3.33) * mm, "end": v(-7.83, 3.77) * mm});
            skLineSegment(sketch, "E4813", {"start": v(-7.83, 3.77) * mm, "end": v(-7.58, 4.19) * mm});
            skLineSegment(sketch, "E4814", {"start": v(-7.58, 4.19) * mm, "end": v(-7.3, 4.6) * mm});
            skLineSegment(sketch, "E4815", {"start": v(-7.3, 4.6) * mm, "end": v(-7, 4.98) * mm});
            skLineSegment(sketch, "E4816", {"start": v(-7, 4.98) * mm, "end": v(-6.68, 5.35) * mm});
            skLineSegment(sketch, "E4817", {"start": v(-6.68, 5.35) * mm, "end": v(-6.33, 5.7) * mm});
            skLineSegment(sketch, "E4818", {"start": v(-6.33, 5.7) * mm, "end": v(-5.96, 6.02) * mm});
            skLineSegment(sketch, "E4819", {"start": v(-5.96, 6.02) * mm, "end": v(-5.57, 6.32) * mm});
            skLineSegment(sketch, "E4820", {"start": v(-5.57, 6.32) * mm, "end": v(-5.17, 6.6) * mm});
            skLineSegment(sketch, "E4821", {"start": v(-5.17, 6.6) * mm, "end": v(-4.74, 6.85) * mm});
            skLineSegment(sketch, "E4822", {"start": v(-4.74, 6.85) * mm, "end": v(-4.3, 7.07) * mm});
            skLineSegment(sketch, "E4823", {"start": v(-4.3, 7.07) * mm, "end": v(-4, 7.2) * mm});
            skLineSegment(sketch, "E4824", {"start": v(-4, 7.2) * mm, "end": v(-4.14, 54.06) * mm});
            skLineSegment(sketch, "E4825", {"start": v(-4.14, 54.06) * mm, "end": v(-4.38, 54.05) * mm});
            skLineSegment(sketch, "E4826", {"start": v(-4.38, 54.05) * mm, "end": v(-7.76, 53.73) * mm});
            skLineSegment(sketch, "E4827", {"start": v(-7.76, 53.73) * mm, "end": v(-11.13, 53.2) * mm});
            skLineSegment(sketch, "E4828", {"start": v(-11.13, 53.2) * mm, "end": v(-14.45, 52.46) * mm});
            skLineSegment(sketch, "E4829", {"start": v(-14.45, 52.46) * mm, "end": v(-17.71, 51.5) * mm});
            skLineSegment(sketch, "E4830", {"start": v(-17.71, 51.5) * mm, "end": v(-20.92, 50.36) * mm});
            skLineSegment(sketch, "E4831", {"start": v(-20.92, 50.36) * mm, "end": v(-24.04, 49) * mm});
            skLineSegment(sketch, "E4832", {"start": v(-24.04, 49) * mm, "end": v(-27.07, 47.46) * mm});
            skLineSegment(sketch, "E4833", {"start": v(-27.07, 47.46) * mm, "end": v(-30, 45.73) * mm});
            skLineSegment(sketch, "E4834", {"start": v(-30, 45.73) * mm, "end": v(-32.81, 43.82) * mm});
            skLineSegment(sketch, "E4835", {"start": v(-32.81, 43.82) * mm, "end": v(-35.5, 41.73) * mm});
            skLineSegment(sketch, "E4836", {"start": v(-35.5, 41.73) * mm, "end": v(-38.05, 39.48) * mm});
            skLineSegment(sketch, "E4837", {"start": v(-38.05, 39.48) * mm, "end": v(-40.46, 37.08) * mm});
            skLineSegment(sketch, "E4838", {"start": v(-40.46, 37.08) * mm, "end": v(-42.7, 34.52) * mm});
            skLineSegment(sketch, "E4839", {"start": v(-42.7, 34.52) * mm, "end": v(-44.8, 31.83) * mm});
            skLineSegment(sketch, "E4840", {"start": v(-44.8, 31.83) * mm, "end": v(-46.7, 29.02) * mm});
            skLineSegment(sketch, "E4841", {"start": v(-46.7, 29.02) * mm, "end": v(-48.44, 26.1) * mm});
            skLineSegment(sketch, "E4842", {"start": v(-48.44, 26.1) * mm, "end": v(-49.98, 23.06) * mm});
            skLineSegment(sketch, "E4843", {"start": v(-49.98, 23.06) * mm, "end": v(-51.33, 19.94) * mm});
            skLineSegment(sketch, "E4844", {"start": v(-51.33, 19.94) * mm, "end": v(-52.49, 16.74) * mm});
            skLineSegment(sketch, "E4845", {"start": v(-52.49, 16.74) * mm, "end": v(-53.44, 13.47) * mm});
            skLineSegment(sketch, "E4846", {"start": v(-53.44, 13.47) * mm, "end": v(-54.18, 10.15) * mm});
            skLineSegment(sketch, "E4847", {"start": v(-54.18, 10.15) * mm, "end": v(-54.71, 6.79) * mm});
            skLineSegment(sketch, "E4848", {"start": v(-54.71, 6.79) * mm, "end": v(-55.03, 3.4) * mm});
            skLineSegment(sketch, "E4849", {"start": v(-55.03, 3.4) * mm, "end": v(-55.04, 3.16) * mm});
            skLineSegment(sketch, "E4850", {"start": v(-55.04, 3.16) * mm, "end": v(-8.18, 3.03) * mm});
            skLineSegment(sketch, "E4851", {"start": v(-8.18, 3.03) * mm, "end": v(-8.05, 3.33) * mm});
            skLineSegment(sketch, "E4852", {"start": v(53.08, 3.16) * mm, "end": v(53.08, 3.4) * mm});
            skLineSegment(sketch, "E4853", {"start": v(53.08, 3.4) * mm, "end": v(52.76, 6.79) * mm});
            skLineSegment(sketch, "E4854", {"start": v(52.76, 6.79) * mm, "end": v(52.22, 10.15) * mm});
            skLineSegment(sketch, "E4855", {"start": v(52.22, 10.15) * mm, "end": v(51.48, 13.47) * mm});
            skLineSegment(sketch, "E4856", {"start": v(51.48, 13.47) * mm, "end": v(50.53, 16.74) * mm});
            skLineSegment(sketch, "E4857", {"start": v(50.53, 16.74) * mm, "end": v(49.38, 19.94) * mm});
            skLineSegment(sketch, "E4858", {"start": v(49.38, 19.94) * mm, "end": v(48.03, 23.06) * mm});
            skLineSegment(sketch, "E4859", {"start": v(48.03, 23.06) * mm, "end": v(46.48, 26.1) * mm});
            skLineSegment(sketch, "E4860", {"start": v(46.48, 26.1) * mm, "end": v(44.75, 29.02) * mm});
            skLineSegment(sketch, "E4861", {"start": v(44.75, 29.02) * mm, "end": v(42.84, 31.83) * mm});
            skLineSegment(sketch, "E4862", {"start": v(42.84, 31.83) * mm, "end": v(40.75, 34.52) * mm});
            skLineSegment(sketch, "E4863", {"start": v(40.75, 34.52) * mm, "end": v(38.5, 37.08) * mm});
            skLineSegment(sketch, "E4864", {"start": v(38.5, 37.08) * mm, "end": v(36.1, 39.48) * mm});
            skLineSegment(sketch, "E4865", {"start": v(36.1, 39.48) * mm, "end": v(33.55, 41.73) * mm});
            skLineSegment(sketch, "E4866", {"start": v(33.55, 41.73) * mm, "end": v(30.86, 43.82) * mm});
            skLineSegment(sketch, "E4867", {"start": v(30.86, 43.82) * mm, "end": v(28.04, 45.73) * mm});
            skLineSegment(sketch, "E4868", {"start": v(28.04, 45.73) * mm, "end": v(25.12, 47.46) * mm});
            skLineSegment(sketch, "E4869", {"start": v(25.12, 47.46) * mm, "end": v(22.08, 49) * mm});
            skLineSegment(sketch, "E4870", {"start": v(22.08, 49) * mm, "end": v(18.96, 50.36) * mm});
            skLineSegment(sketch, "E4871", {"start": v(18.96, 50.36) * mm, "end": v(15.76, 51.5) * mm});
            skLineSegment(sketch, "E4872", {"start": v(15.76, 51.5) * mm, "end": v(12.5, 52.46) * mm});
            skLineSegment(sketch, "E4873", {"start": v(12.5, 52.46) * mm, "end": v(9.17, 53.2) * mm});
            skLineSegment(sketch, "E4874", {"start": v(9.17, 53.2) * mm, "end": v(5.81, 53.73) * mm});
            skLineSegment(sketch, "E4875", {"start": v(5.81, 53.73) * mm, "end": v(2.42, 54.05) * mm});
            skLineSegment(sketch, "E4876", {"start": v(2.42, 54.05) * mm, "end": v(2.19, 54.06) * mm});
            skLineSegment(sketch, "E4877", {"start": v(2.19, 54.06) * mm, "end": v(2.05, 7.2) * mm});
            skLineSegment(sketch, "E4878", {"start": v(2.05, 7.2) * mm, "end": v(2.35, 7.07) * mm});
            skLineSegment(sketch, "E4879", {"start": v(2.35, 7.07) * mm, "end": v(2.79, 6.85) * mm});
            skLineSegment(sketch, "E4880", {"start": v(2.79, 6.85) * mm, "end": v(3.21, 6.6) * mm});
            skLineSegment(sketch, "E4881", {"start": v(3.21, 6.6) * mm, "end": v(3.62, 6.32) * mm});
            skLineSegment(sketch, "E4882", {"start": v(3.62, 6.32) * mm, "end": v(4, 6.02) * mm});
            skLineSegment(sketch, "E4883", {"start": v(4, 6.02) * mm, "end": v(4.37, 5.7) * mm});
            skLineSegment(sketch, "E4884", {"start": v(4.37, 5.7) * mm, "end": v(4.72, 5.35) * mm});
            skLineSegment(sketch, "E4885", {"start": v(4.72, 5.35) * mm, "end": v(5.05, 4.98) * mm});
            skLineSegment(sketch, "E4886", {"start": v(5.05, 4.98) * mm, "end": v(5.35, 4.6) * mm});
            skLineSegment(sketch, "E4887", {"start": v(5.35, 4.6) * mm, "end": v(5.62, 4.19) * mm});
            skLineSegment(sketch, "E4888", {"start": v(5.62, 4.19) * mm, "end": v(5.87, 3.77) * mm});
            skLineSegment(sketch, "E4889", {"start": v(5.87, 3.77) * mm, "end": v(6.1, 3.33) * mm});
            skLineSegment(sketch, "E4890", {"start": v(6.1, 3.33) * mm, "end": v(6.23, 3.03) * mm});
            skLineSegment(sketch, "E4891", {"start": v(6.23, 3.03) * mm, "end": v(53.08, 3.16) * mm});
            skLineSegment(sketch, "E4892", {"start": v(2.42, -54.05) * mm, "end": v(5.81, -53.73) * mm});
            skLineSegment(sketch, "E4893", {"start": v(5.81, -53.73) * mm, "end": v(9.17, -53.2) * mm});
            skLineSegment(sketch, "E4894", {"start": v(9.17, -53.2) * mm, "end": v(12.5, -52.46) * mm});
            skLineSegment(sketch, "E4895", {"start": v(12.5, -52.46) * mm, "end": v(15.76, -51.51) * mm});
            skLineSegment(sketch, "E4896", {"start": v(15.76, -51.51) * mm, "end": v(18.96, -50.36) * mm});
            skLineSegment(sketch, "E4897", {"start": v(18.96, -50.36) * mm, "end": v(22.08, -49) * mm});
            skLineSegment(sketch, "E4898", {"start": v(22.08, -49) * mm, "end": v(25.12, -47.46) * mm});
            skLineSegment(sketch, "E4899", {"start": v(25.12, -47.46) * mm, "end": v(28.04, -45.73) * mm});
            skLineSegment(sketch, "E4900", {"start": v(28.04, -45.73) * mm, "end": v(30.86, -43.82) * mm});
            skLineSegment(sketch, "E4901", {"start": v(30.86, -43.82) * mm, "end": v(33.55, -41.73) * mm});
            skLineSegment(sketch, "E4902", {"start": v(33.55, -41.73) * mm, "end": v(36.1, -39.48) * mm});
            skLineSegment(sketch, "E4903", {"start": v(36.1, -39.48) * mm, "end": v(38.5, -37.08) * mm});
            skLineSegment(sketch, "E4904", {"start": v(38.5, -37.08) * mm, "end": v(40.75, -34.52) * mm});
            skLineSegment(sketch, "E4905", {"start": v(40.75, -34.52) * mm, "end": v(42.84, -31.84) * mm});
            skLineSegment(sketch, "E4906", {"start": v(42.84, -31.84) * mm, "end": v(44.75, -29.02) * mm});
            skLineSegment(sketch, "E4907", {"start": v(44.75, -29.02) * mm, "end": v(46.48, -26.1) * mm});
            skLineSegment(sketch, "E4908", {"start": v(46.48, -26.1) * mm, "end": v(48.03, -23.06) * mm});
            skLineSegment(sketch, "E4909", {"start": v(48.03, -23.06) * mm, "end": v(49.38, -19.94) * mm});
            skLineSegment(sketch, "E4910", {"start": v(49.38, -19.94) * mm, "end": v(50.53, -16.74) * mm});
            skLineSegment(sketch, "E4911", {"start": v(50.53, -16.74) * mm, "end": v(51.48, -13.47) * mm});
            skLineSegment(sketch, "E4912", {"start": v(51.48, -13.47) * mm, "end": v(52.22, -10.15) * mm});
            skLineSegment(sketch, "E4913", {"start": v(52.22, -10.15) * mm, "end": v(52.76, -6.79) * mm});
            skLineSegment(sketch, "E4914", {"start": v(52.76, -6.79) * mm, "end": v(53.08, -3.4) * mm});
            skLineSegment(sketch, "E4915", {"start": v(53.08, -3.4) * mm, "end": v(53.08, -3.16) * mm});
            skLineSegment(sketch, "E4916", {"start": v(53.08, -3.16) * mm, "end": v(6.23, -3.03) * mm});
            skLineSegment(sketch, "E4917", {"start": v(6.23, -3.03) * mm, "end": v(6.1, -3.33) * mm});
            skLineSegment(sketch, "E4918", {"start": v(6.1, -3.33) * mm, "end": v(5.87, -3.77) * mm});
            skLineSegment(sketch, "E4919", {"start": v(5.87, -3.77) * mm, "end": v(5.62, -4.19) * mm});
            skLineSegment(sketch, "E4920", {"start": v(5.62, -4.19) * mm, "end": v(5.35, -4.6) * mm});
            skLineSegment(sketch, "E4921", {"start": v(5.35, -4.6) * mm, "end": v(5.05, -4.98) * mm});
            skLineSegment(sketch, "E4922", {"start": v(5.05, -4.98) * mm, "end": v(4.72, -5.35) * mm});
            skLineSegment(sketch, "E4923", {"start": v(4.72, -5.35) * mm, "end": v(4.37, -5.7) * mm});
            skLineSegment(sketch, "E4924", {"start": v(4.37, -5.7) * mm, "end": v(4, -6.02) * mm});
            skLineSegment(sketch, "E4925", {"start": v(4, -6.02) * mm, "end": v(3.62, -6.33) * mm});
            skLineSegment(sketch, "E4926", {"start": v(3.62, -6.33) * mm, "end": v(3.21, -6.6) * mm});
            skLineSegment(sketch, "E4927", {"start": v(3.21, -6.6) * mm, "end": v(2.79, -6.85) * mm});
            skLineSegment(sketch, "E4928", {"start": v(2.79, -6.85) * mm, "end": v(2.35, -7.07) * mm});
            skLineSegment(sketch, "E4929", {"start": v(2.35, -7.07) * mm, "end": v(2.05, -7.2) * mm});
            skLineSegment(sketch, "E4930", {"start": v(2.05, -7.2) * mm, "end": v(2.19, -54.06) * mm});
            skLineSegment(sketch, "E4931", {"start": v(2.19, -54.06) * mm, "end": v(2.42, -54.05) * mm});
            skLineSegment(sketch, "E4932", {"start": v(-4, -7.2) * mm, "end": v(-4.3, -7.07) * mm});
            skLineSegment(sketch, "E4933", {"start": v(-4.3, -7.07) * mm, "end": v(-4.74, -6.85) * mm});
            skLineSegment(sketch, "E4934", {"start": v(-4.74, -6.85) * mm, "end": v(-5.17, -6.6) * mm});
            skLineSegment(sketch, "E4935", {"start": v(-5.17, -6.6) * mm, "end": v(-5.57, -6.33) * mm});
            skLineSegment(sketch, "E4936", {"start": v(-5.57, -6.33) * mm, "end": v(-5.96, -6.02) * mm});
            skLineSegment(sketch, "E4937", {"start": v(-5.96, -6.02) * mm, "end": v(-6.33, -5.7) * mm});
            skLineSegment(sketch, "E4938", {"start": v(-6.33, -5.7) * mm, "end": v(-6.68, -5.35) * mm});
            skLineSegment(sketch, "E4939", {"start": v(-6.68, -5.35) * mm, "end": v(-7, -4.98) * mm});
            skLineSegment(sketch, "E4940", {"start": v(-7, -4.98) * mm, "end": v(-7.3, -4.6) * mm});
            skLineSegment(sketch, "E4941", {"start": v(-7.3, -4.6) * mm, "end": v(-7.58, -4.19) * mm});
            skLineSegment(sketch, "E4942", {"start": v(-7.58, -4.19) * mm, "end": v(-7.83, -3.77) * mm});
            skLineSegment(sketch, "E4943", {"start": v(-7.83, -3.77) * mm, "end": v(-8.05, -3.33) * mm});
            skLineSegment(sketch, "E4944", {"start": v(-8.05, -3.33) * mm, "end": v(-8.18, -3.03) * mm});
            skLineSegment(sketch, "E4945", {"start": v(-8.18, -3.03) * mm, "end": v(-55.04, -3.16) * mm});
            skLineSegment(sketch, "E4946", {"start": v(-55.04, -3.16) * mm, "end": v(-55.03, -3.4) * mm});
            skLineSegment(sketch, "E4947", {"start": v(-55.03, -3.4) * mm, "end": v(-54.71, -6.79) * mm});
            skLineSegment(sketch, "E4948", {"start": v(-54.71, -6.79) * mm, "end": v(-54.18, -10.15) * mm});
            skLineSegment(sketch, "E4949", {"start": v(-54.18, -10.15) * mm, "end": v(-53.44, -13.47) * mm});
            skLineSegment(sketch, "E4950", {"start": v(-53.44, -13.47) * mm, "end": v(-52.49, -16.74) * mm});
            skLineSegment(sketch, "E4951", {"start": v(-52.49, -16.74) * mm, "end": v(-51.33, -19.94) * mm});
            skLineSegment(sketch, "E4952", {"start": v(-51.33, -19.94) * mm, "end": v(-49.98, -23.06) * mm});
            skLineSegment(sketch, "E4953", {"start": v(-49.98, -23.06) * mm, "end": v(-48.44, -26.1) * mm});
            skLineSegment(sketch, "E4954", {"start": v(-48.44, -26.1) * mm, "end": v(-46.7, -29.02) * mm});
            skLineSegment(sketch, "E4955", {"start": v(-46.7, -29.02) * mm, "end": v(-44.8, -31.84) * mm});
            skLineSegment(sketch, "E4956", {"start": v(-44.8, -31.84) * mm, "end": v(-42.7, -34.52) * mm});
            skLineSegment(sketch, "E4957", {"start": v(-42.7, -34.52) * mm, "end": v(-40.46, -37.08) * mm});
            skLineSegment(sketch, "E4958", {"start": v(-40.46, -37.08) * mm, "end": v(-38.05, -39.48) * mm});
            skLineSegment(sketch, "E4959", {"start": v(-38.05, -39.48) * mm, "end": v(-35.5, -41.73) * mm});
            skLineSegment(sketch, "E4960", {"start": v(-35.5, -41.73) * mm, "end": v(-32.81, -43.82) * mm});
            skLineSegment(sketch, "E4961", {"start": v(-32.81, -43.82) * mm, "end": v(-30, -45.73) * mm});
            skLineSegment(sketch, "E4962", {"start": v(-30, -45.73) * mm, "end": v(-27.07, -47.46) * mm});
            skLineSegment(sketch, "E4963", {"start": v(-27.07, -47.46) * mm, "end": v(-24.04, -49) * mm});
            skLineSegment(sketch, "E4964", {"start": v(-24.04, -49) * mm, "end": v(-20.92, -50.36) * mm});
            skLineSegment(sketch, "E4965", {"start": v(-20.92, -50.36) * mm, "end": v(-17.71, -51.51) * mm});
            skLineSegment(sketch, "E4966", {"start": v(-17.71, -51.51) * mm, "end": v(-14.45, -52.46) * mm});
            skLineSegment(sketch, "E4967", {"start": v(-14.45, -52.46) * mm, "end": v(-11.13, -53.2) * mm});
            skLineSegment(sketch, "E4968", {"start": v(-11.13, -53.2) * mm, "end": v(-7.76, -53.73) * mm});
            skLineSegment(sketch, "E4969", {"start": v(-7.76, -53.73) * mm, "end": v(-4.38, -54.05) * mm});
            skLineSegment(sketch, "E4970", {"start": v(-4.38, -54.05) * mm, "end": v(-4.14, -54.06) * mm});
            skLineSegment(sketch, "E4971", {"start": v(-4.14, -54.06) * mm, "end": v(-4, -7.2) * mm});
            skCircle(sketch, "E4972", {"center": v(-0.98, 0) * mm, "radius": 11 * mm});
            skLineSegment(sketch, "E4973", {"start": v(-0.98, 0) * mm, "end": v(18.02, 0) * mm, "construction": true});
            skCircle(sketch, "E4974", {"center": v(18.02, 0) * mm, "radius": 1.5 * mm});
            skCircle(sketch, "E4975.1.0", {"center": v(-0.98, 19) * mm, "radius": 1.5 * mm});
            skCircle(sketch, "E4975.2.0", {"center": v(-19.98, 0) * mm, "radius": 1.5 * mm});
            skCircle(sketch, "E4975.3.0", {"center": v(-0.98, -19) * mm, "radius": 1.5 * mm});
            skSolve(sketch);
        }
        {
            var Q0;
            Q0=makeQuery(id+"F0.imprint","IMPRINT",FACE,{"disambiguationData":[TD([[makeQuery(id+"F0.imprint","IMPRINT",EDGE,{"derivedFrom":sQuery(id+"F0.wireOp",EDGE,"E0")}),1.0]])]});
            var Q1;
            Q1=makeQuery(id+"F0.imprint","IMPRINT",FACE,{"disambiguationData":[TD([[makeQuery(id+"F0.imprint","IMPRINT",EDGE,{"derivedFrom":sQuery(id+"F0.wireOp",EDGE,"E4812")}),-1.0]])]});
            var Q2;
            {var subQ0=sQuery(id+"F0.wireOp",EDGE,"E4917");Q2=makeQuery(id+"F0.imprint","IMPRINT",FACE,{"disambiguationData":[TD([[makeQuery(id+"F0.imprint","IMPRINT",EDGE,{"derivedFrom":subQ0}),1.0]])]});}
            var Q3;
            {var subQ0=sQuery(id+"F0.wireOp",EDGE,"E4932");Q3=makeQuery(id+"F0.imprint","IMPRINT",FACE,{"disambiguationData":[TD([[makeQuery(id+"F0.imprint","IMPRINT",EDGE,{"derivedFrom":subQ0}),1.0]])]});}
            var Q4;
            Q4=makeQuery(id+"F0.imprint","IMPRINT",FACE,{"disambiguationData":[TD([[makeQuery(id+"F0.imprint","IMPRINT",EDGE,{"derivedFrom":sQuery(id+"F0.wireOp",EDGE,"E4812")}),1.0]])]});
            var Q5;
            Q5=makeQuery(id+"F0.imprint","IMPRINT",FACE,{"disambiguationData":[TD([[makeQuery(id+"F0.imprint","IMPRINT",EDGE,{"derivedFrom":sQuery(id+"F0.wireOp",EDGE,"E4812")}),1.0]])]});
            var Q6;
            {var subQ0=sQuery(id+"F0.wireOp",EDGE,"E4917");Q6=makeQuery(id+"F0.imprint","IMPRINT",FACE,{"disambiguationData":[TD([[makeQuery(id+"F0.imprint","IMPRINT",EDGE,{"derivedFrom":subQ0}),1.0]])]});}
            var Q7;
            {var subQ0=sQuery(id+"F0.wireOp",EDGE,"E4932");Q7=makeQuery(id+"F0.imprint","IMPRINT",FACE,{"disambiguationData":[TD([[makeQuery(id+"F0.imprint","IMPRINT",EDGE,{"derivedFrom":subQ0}),1.0]])]});}
            var Q8;
            {var subQ0=sQuery(id+"F0.wireOp",EDGE,"E4878");Q8=makeQuery(id+"F0.imprint","IMPRINT",FACE,{"disambiguationData":[TD([[makeQuery(id+"F0.imprint","IMPRINT",EDGE,{"derivedFrom":subQ0}),1.0]])]});}
            extrude(context, id + "F1", {"entities" : qUnion([Q0, Q1, Q2, Q3, Q4, Q5, Q6, Q7, Q8]), "depth" : 5 * mm});
        }
        {
            var Q0;
            Q0=makeQuery(id+"F1.opExtrude","CAP_FACE",FACE,{"disambiguationData":[OSD([sQuery(id+"F0.wireOp",EDGE,"E0"),sQuery(id+"F0.wireOp",EDGE,"E1"),sQuery(id+"F0.wireOp",EDGE,"E2"),sQuery(id+"F0.wireOp",EDGE,"E3"),sQuery(id+"F0.wireOp",EDGE,"E4"),sQuery(id+"F0.wireOp",EDGE,"E5"),sQuery(id+"F0.wireOp",EDGE,"E6"),sQuery(id+"F0.wireOp",EDGE,"E7"),sQuery(id+"F0.wireOp",EDGE,"E8"),sQuery(id+"F0.wireOp",EDGE,"E9"),sQuery(id+"F0.wireOp",EDGE,"E10"),sQuery(id+"F0.wireOp",EDGE,"E11"),sQuery(id+"F0.wireOp",EDGE,"E12"),sQuery(id+"F0.wireOp",EDGE,"E13"),sQuery(id+"F0.wireOp",EDGE,"E14"),sQuery(id+"F0.wireOp",EDGE,"E15"),sQuery(id+"F0.wireOp",EDGE,"E16"),sQuery(id+"F0.wireOp",EDGE,"E17"),sQuery(id+"F0.wireOp",EDGE,"E18"),sQuery(id+"F0.wireOp",EDGE,"E19"),sQuery(id+"F0.wireOp",EDGE,"E20"),sQuery(id+"F0.wireOp",EDGE,"E21"),sQuery(id+"F0.wireOp",EDGE,"E22"),sQuery(id+"F0.wireOp",EDGE,"E23"),sQuery(id+"F0.wireOp",EDGE,"E24"),sQuery(id+"F0.wireOp",EDGE,"E25"),sQuery(id+"F0.wireOp",EDGE,"E26"),sQuery(id+"F0.wireOp",EDGE,"E27"),sQuery(id+"F0.wireOp",EDGE,"E28"),sQuery(id+"F0.wireOp",EDGE,"E29"),sQuery(id+"F0.wireOp",EDGE,"E30"),sQuery(id+"F0.wireOp",EDGE,"E31"),sQuery(id+"F0.wireOp",EDGE,"E32"),sQuery(id+"F0.wireOp",EDGE,"E33"),sQuery(id+"F0.wireOp",EDGE,"E34"),sQuery(id+"F0.wireOp",EDGE,"E35"),sQuery(id+"F0.wireOp",EDGE,"E36"),sQuery(id+"F0.wireOp",EDGE,"E37"),sQuery(id+"F0.wireOp",EDGE,"E38"),sQuery(id+"F0.wireOp",EDGE,"E39"),sQuery(id+"F0.wireOp",EDGE,"E40"),sQuery(id+"F0.wireOp",EDGE,"E41"),sQuery(id+"F0.wireOp",EDGE,"E42"),sQuery(id+"F0.wireOp",EDGE,"E43"),sQuery(id+"F0.wireOp",EDGE,"E44"),sQuery(id+"F0.wireOp",EDGE,"E45"),sQuery(id+"F0.wireOp",EDGE,"E46"),sQuery(id+"F0.wireOp",EDGE,"E47"),sQuery(id+"F0.wireOp",EDGE,"E48"),sQuery(id+"F0.wireOp",EDGE,"E49"),sQuery(id+"F0.wireOp",EDGE,"E50"),sQuery(id+"F0.wireOp",EDGE,"E51"),sQuery(id+"F0.wireOp",EDGE,"E52"),sQuery(id+"F0.wireOp",EDGE,"E53"),sQuery(id+"F0.wireOp",EDGE,"E54"),sQuery(id+"F0.wireOp",EDGE,"E55"),sQuery(id+"F0.wireOp",EDGE,"E56"),sQuery(id+"F0.wireOp",EDGE,"E57"),sQuery(id+"F0.wireOp",EDGE,"E58"),sQuery(id+"F0.wireOp",EDGE,"E59"),sQuery(id+"F0.wireOp",EDGE,"E60"),sQuery(id+"F0.wireOp",EDGE,"E61"),sQuery(id+"F0.wireOp",EDGE,"E62"),sQuery(id+"F0.wireOp",EDGE,"E63"),sQuery(id+"F0.wireOp",EDGE,"E64"),sQuery(id+"F0.wireOp",EDGE,"E65"),sQuery(id+"F0.wireOp",EDGE,"E66"),sQuery(id+"F0.wireOp",EDGE,"E67"),sQuery(id+"F0.wireOp",EDGE,"E68"),sQuery(id+"F0.wireOp",EDGE,"E69"),sQuery(id+"F0.wireOp",EDGE,"E70"),sQuery(id+"F0.wireOp",EDGE,"E71"),sQuery(id+"F0.wireOp",EDGE,"E72"),sQuery(id+"F0.wireOp",EDGE,"E73"),sQuery(id+"F0.wireOp",EDGE,"E74"),sQuery(id+"F0.wireOp",EDGE,"E75"),sQuery(id+"F0.wireOp",EDGE,"E76"),sQuery(id+"F0.wireOp",EDGE,"E77"),sQuery(id+"F0.wireOp",EDGE,"E78"),sQuery(id+"F0.wireOp",EDGE,"E79"),sQuery(id+"F0.wireOp",EDGE,"E80"),sQuery(id+"F0.wireOp",EDGE,"E81"),sQuery(id+"F0.wireOp",EDGE,"E82"),sQuery(id+"F0.wireOp",EDGE,"E83"),sQuery(id+"F0.wireOp",EDGE,"E84"),sQuery(id+"F0.wireOp",EDGE,"E85"),sQuery(id+"F0.wireOp",EDGE,"E86"),sQuery(id+"F0.wireOp",EDGE,"E87"),sQuery(id+"F0.wireOp",EDGE,"E88"),sQuery(id+"F0.wireOp",EDGE,"E89"),sQuery(id+"F0.wireOp",EDGE,"E90"),sQuery(id+"F0.wireOp",EDGE,"E91"),sQuery(id+"F0.wireOp",EDGE,"E92"),sQuery(id+"F0.wireOp",EDGE,"E93"),sQuery(id+"F0.wireOp",EDGE,"E94"),sQuery(id+"F0.wireOp",EDGE,"E95"),sQuery(id+"F0.wireOp",EDGE,"E96"),sQuery(id+"F0.wireOp",EDGE,"E97"),sQuery(id+"F0.wireOp",EDGE,"E98"),sQuery(id+"F0.wireOp",EDGE,"E99"),sQuery(id+"F0.wireOp",EDGE,"E100"),sQuery(id+"F0.wireOp",EDGE,"E101"),sQuery(id+"F0.wireOp",EDGE,"E102"),sQuery(id+"F0.wireOp",EDGE,"E103"),sQuery(id+"F0.wireOp",EDGE,"E104"),sQuery(id+"F0.wireOp",EDGE,"E105"),sQuery(id+"F0.wireOp",EDGE,"E106"),sQuery(id+"F0.wireOp",EDGE,"E107"),sQuery(id+"F0.wireOp",EDGE,"E108"),sQuery(id+"F0.wireOp",EDGE,"E109"),sQuery(id+"F0.wireOp",EDGE,"E110"),sQuery(id+"F0.wireOp",EDGE,"E111"),sQuery(id+"F0.wireOp",EDGE,"E112"),sQuery(id+"F0.wireOp",EDGE,"E113"),sQuery(id+"F0.wireOp",EDGE,"E114"),sQuery(id+"F0.wireOp",EDGE,"E115"),sQuery(id+"F0.wireOp",EDGE,"E116"),sQuery(id+"F0.wireOp",EDGE,"E117"),sQuery(id+"F0.wireOp",EDGE,"E118"),sQuery(id+"F0.wireOp",EDGE,"E119"),sQuery(id+"F0.wireOp",EDGE,"E120"),sQuery(id+"F0.wireOp",EDGE,"E121"),sQuery(id+"F0.wireOp",EDGE,"E122"),sQuery(id+"F0.wireOp",EDGE,"E123"),sQuery(id+"F0.wireOp",EDGE,"E124"),sQuery(id+"F0.wireOp",EDGE,"E125"),sQuery(id+"F0.wireOp",EDGE,"E126"),sQuery(id+"F0.wireOp",EDGE,"E127"),sQuery(id+"F0.wireOp",EDGE,"E128"),sQuery(id+"F0.wireOp",EDGE,"E129"),sQuery(id+"F0.wireOp",EDGE,"E130"),sQuery(id+"F0.wireOp",EDGE,"E131"),sQuery(id+"F0.wireOp",EDGE,"E132"),sQuery(id+"F0.wireOp",EDGE,"E133"),sQuery(id+"F0.wireOp",EDGE,"E134"),sQuery(id+"F0.wireOp",EDGE,"E135"),sQuery(id+"F0.wireOp",EDGE,"E136"),sQuery(id+"F0.wireOp",EDGE,"E137"),sQuery(id+"F0.wireOp",EDGE,"E138"),sQuery(id+"F0.wireOp",EDGE,"E139"),sQuery(id+"F0.wireOp",EDGE,"E140"),sQuery(id+"F0.wireOp",EDGE,"E141"),sQuery(id+"F0.wireOp",EDGE,"E142"),sQuery(id+"F0.wireOp",EDGE,"E143"),sQuery(id+"F0.wireOp",EDGE,"E144"),sQuery(id+"F0.wireOp",EDGE,"E145"),sQuery(id+"F0.wireOp",EDGE,"E146"),sQuery(id+"F0.wireOp",EDGE,"E147"),sQuery(id+"F0.wireOp",EDGE,"E148"),sQuery(id+"F0.wireOp",EDGE,"E149"),sQuery(id+"F0.wireOp",EDGE,"E150"),sQuery(id+"F0.wireOp",EDGE,"E151"),sQuery(id+"F0.wireOp",EDGE,"E152"),sQuery(id+"F0.wireOp",EDGE,"E153"),sQuery(id+"F0.wireOp",EDGE,"E154"),sQuery(id+"F0.wireOp",EDGE,"E155"),sQuery(id+"F0.wireOp",EDGE,"E156"),sQuery(id+"F0.wireOp",EDGE,"E157"),sQuery(id+"F0.wireOp",EDGE,"E158"),sQuery(id+"F0.wireOp",EDGE,"E159"),sQuery(id+"F0.wireOp",EDGE,"E160"),sQuery(id+"F0.wireOp",EDGE,"E161"),sQuery(id+"F0.wireOp",EDGE,"E162"),sQuery(id+"F0.wireOp",EDGE,"E163"),sQuery(id+"F0.wireOp",EDGE,"E164"),sQuery(id+"F0.wireOp",EDGE,"E165"),sQuery(id+"F0.wireOp",EDGE,"E166"),sQuery(id+"F0.wireOp",EDGE,"E167"),sQuery(id+"F0.wireOp",EDGE,"E168"),sQuery(id+"F0.wireOp",EDGE,"E169"),sQuery(id+"F0.wireOp",EDGE,"E170"),sQuery(id+"F0.wireOp",EDGE,"E171"),sQuery(id+"F0.wireOp",EDGE,"E172"),sQuery(id+"F0.wireOp",EDGE,"E173"),sQuery(id+"F0.wireOp",EDGE,"E174"),sQuery(id+"F0.wireOp",EDGE,"E175"),sQuery(id+"F0.wireOp",EDGE,"E176"),sQuery(id+"F0.wireOp",EDGE,"E177"),sQuery(id+"F0.wireOp",EDGE,"E178"),sQuery(id+"F0.wireOp",EDGE,"E179"),sQuery(id+"F0.wireOp",EDGE,"E180"),sQuery(id+"F0.wireOp",EDGE,"E181"),sQuery(id+"F0.wireOp",EDGE,"E182"),sQuery(id+"F0.wireOp",EDGE,"E183"),sQuery(id+"F0.wireOp",EDGE,"E184"),sQuery(id+"F0.wireOp",EDGE,"E185"),sQuery(id+"F0.wireOp",EDGE,"E186"),sQuery(id+"F0.wireOp",EDGE,"E187"),sQuery(id+"F0.wireOp",EDGE,"E188"),sQuery(id+"F0.wireOp",EDGE,"E189"),sQuery(id+"F0.wireOp",EDGE,"E190"),sQuery(id+"F0.wireOp",EDGE,"E191"),sQuery(id+"F0.wireOp",EDGE,"E192"),sQuery(id+"F0.wireOp",EDGE,"E193"),sQuery(id+"F0.wireOp",EDGE,"E194"),sQuery(id+"F0.wireOp",EDGE,"E195"),sQuery(id+"F0.wireOp",EDGE,"E196"),sQuery(id+"F0.wireOp",EDGE,"E197"),sQuery(id+"F0.wireOp",EDGE,"E198"),sQuery(id+"F0.wireOp",EDGE,"E199"),sQuery(id+"F0.wireOp",EDGE,"E200"),sQuery(id+"F0.wireOp",EDGE,"E201"),sQuery(id+"F0.wireOp",EDGE,"E202"),sQuery(id+"F0.wireOp",EDGE,"E203"),sQuery(id+"F0.wireOp",EDGE,"E204"),sQuery(id+"F0.wireOp",EDGE,"E205"),sQuery(id+"F0.wireOp",EDGE,"E206"),sQuery(id+"F0.wireOp",EDGE,"E207"),sQuery(id+"F0.wireOp",EDGE,"E208"),sQuery(id+"F0.wireOp",EDGE,"E209"),sQuery(id+"F0.wireOp",EDGE,"E210"),sQuery(id+"F0.wireOp",EDGE,"E211"),sQuery(id+"F0.wireOp",EDGE,"E212"),sQuery(id+"F0.wireOp",EDGE,"E213"),sQuery(id+"F0.wireOp",EDGE,"E214"),sQuery(id+"F0.wireOp",EDGE,"E215"),sQuery(id+"F0.wireOp",EDGE,"E216"),sQuery(id+"F0.wireOp",EDGE,"E217"),sQuery(id+"F0.wireOp",EDGE,"E218"),sQuery(id+"F0.wireOp",EDGE,"E219"),sQuery(id+"F0.wireOp",EDGE,"E220"),sQuery(id+"F0.wireOp",EDGE,"E221"),sQuery(id+"F0.wireOp",EDGE,"E222"),sQuery(id+"F0.wireOp",EDGE,"E223"),sQuery(id+"F0.wireOp",EDGE,"E224"),sQuery(id+"F0.wireOp",EDGE,"E225"),sQuery(id+"F0.wireOp",EDGE,"E226"),sQuery(id+"F0.wireOp",EDGE,"E227"),sQuery(id+"F0.wireOp",EDGE,"E228"),sQuery(id+"F0.wireOp",EDGE,"E229"),sQuery(id+"F0.wireOp",EDGE,"E230"),sQuery(id+"F0.wireOp",EDGE,"E231"),sQuery(id+"F0.wireOp",EDGE,"E232"),sQuery(id+"F0.wireOp",EDGE,"E233"),sQuery(id+"F0.wireOp",EDGE,"E234"),sQuery(id+"F0.wireOp",EDGE,"E235"),sQuery(id+"F0.wireOp",EDGE,"E236"),sQuery(id+"F0.wireOp",EDGE,"E237"),sQuery(id+"F0.wireOp",EDGE,"E238"),sQuery(id+"F0.wireOp",EDGE,"E239"),sQuery(id+"F0.wireOp",EDGE,"E240"),sQuery(id+"F0.wireOp",EDGE,"E241"),sQuery(id+"F0.wireOp",EDGE,"E242"),sQuery(id+"F0.wireOp",EDGE,"E243"),sQuery(id+"F0.wireOp",EDGE,"E244"),sQuery(id+"F0.wireOp",EDGE,"E245"),sQuery(id+"F0.wireOp",EDGE,"E246"),sQuery(id+"F0.wireOp",EDGE,"E247"),sQuery(id+"F0.wireOp",EDGE,"E248"),sQuery(id+"F0.wireOp",EDGE,"E249"),sQuery(id+"F0.wireOp",EDGE,"E250"),sQuery(id+"F0.wireOp",EDGE,"E251"),sQuery(id+"F0.wireOp",EDGE,"E252"),sQuery(id+"F0.wireOp",EDGE,"E253"),sQuery(id+"F0.wireOp",EDGE,"E254"),sQuery(id+"F0.wireOp",EDGE,"E255"),sQuery(id+"F0.wireOp",EDGE,"E256"),sQuery(id+"F0.wireOp",EDGE,"E257"),sQuery(id+"F0.wireOp",EDGE,"E258"),sQuery(id+"F0.wireOp",EDGE,"E259"),sQuery(id+"F0.wireOp",EDGE,"E260"),sQuery(id+"F0.wireOp",EDGE,"E261"),sQuery(id+"F0.wireOp",EDGE,"E262"),sQuery(id+"F0.wireOp",EDGE,"E263"),sQuery(id+"F0.wireOp",EDGE,"E264"),sQuery(id+"F0.wireOp",EDGE,"E265"),sQuery(id+"F0.wireOp",EDGE,"E266"),sQuery(id+"F0.wireOp",EDGE,"E267"),sQuery(id+"F0.wireOp",EDGE,"E268"),sQuery(id+"F0.wireOp",EDGE,"E269"),sQuery(id+"F0.wireOp",EDGE,"E270"),sQuery(id+"F0.wireOp",EDGE,"E271"),sQuery(id+"F0.wireOp",EDGE,"E272"),sQuery(id+"F0.wireOp",EDGE,"E273"),sQuery(id+"F0.wireOp",EDGE,"E274"),sQuery(id+"F0.wireOp",EDGE,"E275"),sQuery(id+"F0.wireOp",EDGE,"E276"),sQuery(id+"F0.wireOp",EDGE,"E277"),sQuery(id+"F0.wireOp",EDGE,"E278"),sQuery(id+"F0.wireOp",EDGE,"E279"),sQuery(id+"F0.wireOp",EDGE,"E280"),sQuery(id+"F0.wireOp",EDGE,"E281"),sQuery(id+"F0.wireOp",EDGE,"E282"),sQuery(id+"F0.wireOp",EDGE,"E283"),sQuery(id+"F0.wireOp",EDGE,"E284"),sQuery(id+"F0.wireOp",EDGE,"E285"),sQuery(id+"F0.wireOp",EDGE,"E286"),sQuery(id+"F0.wireOp",EDGE,"E287"),sQuery(id+"F0.wireOp",EDGE,"E288"),sQuery(id+"F0.wireOp",EDGE,"E289"),sQuery(id+"F0.wireOp",EDGE,"E290"),sQuery(id+"F0.wireOp",EDGE,"E291"),sQuery(id+"F0.wireOp",EDGE,"E292"),sQuery(id+"F0.wireOp",EDGE,"E293"),sQuery(id+"F0.wireOp",EDGE,"E294"),sQuery(id+"F0.wireOp",EDGE,"E295"),sQuery(id+"F0.wireOp",EDGE,"E296"),sQuery(id+"F0.wireOp",EDGE,"E297"),sQuery(id+"F0.wireOp",EDGE,"E298"),sQuery(id+"F0.wireOp",EDGE,"E299"),sQuery(id+"F0.wireOp",EDGE,"E300"),sQuery(id+"F0.wireOp",EDGE,"E301"),sQuery(id+"F0.wireOp",EDGE,"E302"),sQuery(id+"F0.wireOp",EDGE,"E303"),sQuery(id+"F0.wireOp",EDGE,"E304"),sQuery(id+"F0.wireOp",EDGE,"E305"),sQuery(id+"F0.wireOp",EDGE,"E306"),sQuery(id+"F0.wireOp",EDGE,"E307"),sQuery(id+"F0.wireOp",EDGE,"E308"),sQuery(id+"F0.wireOp",EDGE,"E309"),sQuery(id+"F0.wireOp",EDGE,"E310"),sQuery(id+"F0.wireOp",EDGE,"E311"),sQuery(id+"F0.wireOp",EDGE,"E312"),sQuery(id+"F0.wireOp",EDGE,"E313"),sQuery(id+"F0.wireOp",EDGE,"E314"),sQuery(id+"F0.wireOp",EDGE,"E315"),sQuery(id+"F0.wireOp",EDGE,"E316"),sQuery(id+"F0.wireOp",EDGE,"E317"),sQuery(id+"F0.wireOp",EDGE,"E318"),sQuery(id+"F0.wireOp",EDGE,"E319"),sQuery(id+"F0.wireOp",EDGE,"E320"),sQuery(id+"F0.wireOp",EDGE,"E321"),sQuery(id+"F0.wireOp",EDGE,"E322"),sQuery(id+"F0.wireOp",EDGE,"E323"),sQuery(id+"F0.wireOp",EDGE,"E324"),sQuery(id+"F0.wireOp",EDGE,"E325"),sQuery(id+"F0.wireOp",EDGE,"E326"),sQuery(id+"F0.wireOp",EDGE,"E327"),sQuery(id+"F0.wireOp",EDGE,"E328"),sQuery(id+"F0.wireOp",EDGE,"E329"),sQuery(id+"F0.wireOp",EDGE,"E330"),sQuery(id+"F0.wireOp",EDGE,"E331"),sQuery(id+"F0.wireOp",EDGE,"E332"),sQuery(id+"F0.wireOp",EDGE,"E333"),sQuery(id+"F0.wireOp",EDGE,"E334"),sQuery(id+"F0.wireOp",EDGE,"E335"),sQuery(id+"F0.wireOp",EDGE,"E336"),sQuery(id+"F0.wireOp",EDGE,"E337"),sQuery(id+"F0.wireOp",EDGE,"E338"),sQuery(id+"F0.wireOp",EDGE,"E339"),sQuery(id+"F0.wireOp",EDGE,"E340"),sQuery(id+"F0.wireOp",EDGE,"E341"),sQuery(id+"F0.wireOp",EDGE,"E342"),sQuery(id+"F0.wireOp",EDGE,"E343"),sQuery(id+"F0.wireOp",EDGE,"E344"),sQuery(id+"F0.wireOp",EDGE,"E345"),sQuery(id+"F0.wireOp",EDGE,"E346"),sQuery(id+"F0.wireOp",EDGE,"E347"),sQuery(id+"F0.wireOp",EDGE,"E348"),sQuery(id+"F0.wireOp",EDGE,"E349"),sQuery(id+"F0.wireOp",EDGE,"E350"),sQuery(id+"F0.wireOp",EDGE,"E351"),sQuery(id+"F0.wireOp",EDGE,"E352"),sQuery(id+"F0.wireOp",EDGE,"E353"),sQuery(id+"F0.wireOp",EDGE,"E354"),sQuery(id+"F0.wireOp",EDGE,"E355"),sQuery(id+"F0.wireOp",EDGE,"E356"),sQuery(id+"F0.wireOp",EDGE,"E357"),sQuery(id+"F0.wireOp",EDGE,"E358"),sQuery(id+"F0.wireOp",EDGE,"E359"),sQuery(id+"F0.wireOp",EDGE,"E360"),sQuery(id+"F0.wireOp",EDGE,"E361"),sQuery(id+"F0.wireOp",EDGE,"E362"),sQuery(id+"F0.wireOp",EDGE,"E363"),sQuery(id+"F0.wireOp",EDGE,"E364"),sQuery(id+"F0.wireOp",EDGE,"E365"),sQuery(id+"F0.wireOp",EDGE,"E366"),sQuery(id+"F0.wireOp",EDGE,"E367"),sQuery(id+"F0.wireOp",EDGE,"E368"),sQuery(id+"F0.wireOp",EDGE,"E369"),sQuery(id+"F0.wireOp",EDGE,"E370"),sQuery(id+"F0.wireOp",EDGE,"E371"),sQuery(id+"F0.wireOp",EDGE,"E372"),sQuery(id+"F0.wireOp",EDGE,"E373"),sQuery(id+"F0.wireOp",EDGE,"E374"),sQuery(id+"F0.wireOp",EDGE,"E375"),sQuery(id+"F0.wireOp",EDGE,"E376"),sQuery(id+"F0.wireOp",EDGE,"E377"),sQuery(id+"F0.wireOp",EDGE,"E378"),sQuery(id+"F0.wireOp",EDGE,"E379"),sQuery(id+"F0.wireOp",EDGE,"E380"),sQuery(id+"F0.wireOp",EDGE,"E381"),sQuery(id+"F0.wireOp",EDGE,"E382"),sQuery(id+"F0.wireOp",EDGE,"E383"),sQuery(id+"F0.wireOp",EDGE,"E384"),sQuery(id+"F0.wireOp",EDGE,"E385"),sQuery(id+"F0.wireOp",EDGE,"E386"),sQuery(id+"F0.wireOp",EDGE,"E387"),sQuery(id+"F0.wireOp",EDGE,"E388"),sQuery(id+"F0.wireOp",EDGE,"E389"),sQuery(id+"F0.wireOp",EDGE,"E390"),sQuery(id+"F0.wireOp",EDGE,"E391"),sQuery(id+"F0.wireOp",EDGE,"E392"),sQuery(id+"F0.wireOp",EDGE,"E393"),sQuery(id+"F0.wireOp",EDGE,"E394"),sQuery(id+"F0.wireOp",EDGE,"E395"),sQuery(id+"F0.wireOp",EDGE,"E396"),sQuery(id+"F0.wireOp",EDGE,"E397"),sQuery(id+"F0.wireOp",EDGE,"E398"),sQuery(id+"F0.wireOp",EDGE,"E399"),sQuery(id+"F0.wireOp",EDGE,"E400"),sQuery(id+"F0.wireOp",EDGE,"E401"),sQuery(id+"F0.wireOp",EDGE,"E402"),sQuery(id+"F0.wireOp",EDGE,"E403"),sQuery(id+"F0.wireOp",EDGE,"E404"),sQuery(id+"F0.wireOp",EDGE,"E405"),sQuery(id+"F0.wireOp",EDGE,"E406"),sQuery(id+"F0.wireOp",EDGE,"E407"),sQuery(id+"F0.wireOp",EDGE,"E408"),sQuery(id+"F0.wireOp",EDGE,"E409"),sQuery(id+"F0.wireOp",EDGE,"E410"),sQuery(id+"F0.wireOp",EDGE,"E411"),sQuery(id+"F0.wireOp",EDGE,"E412"),sQuery(id+"F0.wireOp",EDGE,"E413"),sQuery(id+"F0.wireOp",EDGE,"E414"),sQuery(id+"F0.wireOp",EDGE,"E415"),sQuery(id+"F0.wireOp",EDGE,"E416"),sQuery(id+"F0.wireOp",EDGE,"E417"),sQuery(id+"F0.wireOp",EDGE,"E418"),sQuery(id+"F0.wireOp",EDGE,"E419"),sQuery(id+"F0.wireOp",EDGE,"E420"),sQuery(id+"F0.wireOp",EDGE,"E421"),sQuery(id+"F0.wireOp",EDGE,"E422"),sQuery(id+"F0.wireOp",EDGE,"E423"),sQuery(id+"F0.wireOp",EDGE,"E424"),sQuery(id+"F0.wireOp",EDGE,"E425"),sQuery(id+"F0.wireOp",EDGE,"E426"),sQuery(id+"F0.wireOp",EDGE,"E427"),sQuery(id+"F0.wireOp",EDGE,"E428"),sQuery(id+"F0.wireOp",EDGE,"E429"),sQuery(id+"F0.wireOp",EDGE,"E430"),sQuery(id+"F0.wireOp",EDGE,"E431"),sQuery(id+"F0.wireOp",EDGE,"E432"),sQuery(id+"F0.wireOp",EDGE,"E433"),sQuery(id+"F0.wireOp",EDGE,"E434"),sQuery(id+"F0.wireOp",EDGE,"E435"),sQuery(id+"F0.wireOp",EDGE,"E436"),sQuery(id+"F0.wireOp",EDGE,"E437"),sQuery(id+"F0.wireOp",EDGE,"E438"),sQuery(id+"F0.wireOp",EDGE,"E439"),sQuery(id+"F0.wireOp",EDGE,"E440"),sQuery(id+"F0.wireOp",EDGE,"E441"),sQuery(id+"F0.wireOp",EDGE,"E442"),sQuery(id+"F0.wireOp",EDGE,"E443"),sQuery(id+"F0.wireOp",EDGE,"E444"),sQuery(id+"F0.wireOp",EDGE,"E445"),sQuery(id+"F0.wireOp",EDGE,"E446"),sQuery(id+"F0.wireOp",EDGE,"E447"),sQuery(id+"F0.wireOp",EDGE,"E448"),sQuery(id+"F0.wireOp",EDGE,"E449"),sQuery(id+"F0.wireOp",EDGE,"E450"),sQuery(id+"F0.wireOp",EDGE,"E451"),sQuery(id+"F0.wireOp",EDGE,"E452"),sQuery(id+"F0.wireOp",EDGE,"E453"),sQuery(id+"F0.wireOp",EDGE,"E454"),sQuery(id+"F0.wireOp",EDGE,"E455"),sQuery(id+"F0.wireOp",EDGE,"E456"),sQuery(id+"F0.wireOp",EDGE,"E457"),sQuery(id+"F0.wireOp",EDGE,"E458"),sQuery(id+"F0.wireOp",EDGE,"E459"),sQuery(id+"F0.wireOp",EDGE,"E460"),sQuery(id+"F0.wireOp",EDGE,"E461"),sQuery(id+"F0.wireOp",EDGE,"E462"),sQuery(id+"F0.wireOp",EDGE,"E463"),sQuery(id+"F0.wireOp",EDGE,"E464"),sQuery(id+"F0.wireOp",EDGE,"E465"),sQuery(id+"F0.wireOp",EDGE,"E466"),sQuery(id+"F0.wireOp",EDGE,"E467"),sQuery(id+"F0.wireOp",EDGE,"E468"),sQuery(id+"F0.wireOp",EDGE,"E469"),sQuery(id+"F0.wireOp",EDGE,"E470"),sQuery(id+"F0.wireOp",EDGE,"E471"),sQuery(id+"F0.wireOp",EDGE,"E472"),sQuery(id+"F0.wireOp",EDGE,"E473"),sQuery(id+"F0.wireOp",EDGE,"E474"),sQuery(id+"F0.wireOp",EDGE,"E475"),sQuery(id+"F0.wireOp",EDGE,"E476"),sQuery(id+"F0.wireOp",EDGE,"E477"),sQuery(id+"F0.wireOp",EDGE,"E478"),sQuery(id+"F0.wireOp",EDGE,"E479"),sQuery(id+"F0.wireOp",EDGE,"E480"),sQuery(id+"F0.wireOp",EDGE,"E481"),sQuery(id+"F0.wireOp",EDGE,"E482"),sQuery(id+"F0.wireOp",EDGE,"E483"),sQuery(id+"F0.wireOp",EDGE,"E484"),sQuery(id+"F0.wireOp",EDGE,"E485"),sQuery(id+"F0.wireOp",EDGE,"E486"),sQuery(id+"F0.wireOp",EDGE,"E487"),sQuery(id+"F0.wireOp",EDGE,"E488"),sQuery(id+"F0.wireOp",EDGE,"E489"),sQuery(id+"F0.wireOp",EDGE,"E490"),sQuery(id+"F0.wireOp",EDGE,"E491"),sQuery(id+"F0.wireOp",EDGE,"E492"),sQuery(id+"F0.wireOp",EDGE,"E493"),sQuery(id+"F0.wireOp",EDGE,"E494"),sQuery(id+"F0.wireOp",EDGE,"E495"),sQuery(id+"F0.wireOp",EDGE,"E496"),sQuery(id+"F0.wireOp",EDGE,"E497"),sQuery(id+"F0.wireOp",EDGE,"E498"),sQuery(id+"F0.wireOp",EDGE,"E499"),sQuery(id+"F0.wireOp",EDGE,"E500"),sQuery(id+"F0.wireOp",EDGE,"E501"),sQuery(id+"F0.wireOp",EDGE,"E502"),sQuery(id+"F0.wireOp",EDGE,"E503"),sQuery(id+"F0.wireOp",EDGE,"E504"),sQuery(id+"F0.wireOp",EDGE,"E505"),sQuery(id+"F0.wireOp",EDGE,"E506"),sQuery(id+"F0.wireOp",EDGE,"E507"),sQuery(id+"F0.wireOp",EDGE,"E508"),sQuery(id+"F0.wireOp",EDGE,"E509"),sQuery(id+"F0.wireOp",EDGE,"E510"),sQuery(id+"F0.wireOp",EDGE,"E511"),sQuery(id+"F0.wireOp",EDGE,"E512"),sQuery(id+"F0.wireOp",EDGE,"E513"),sQuery(id+"F0.wireOp",EDGE,"E514"),sQuery(id+"F0.wireOp",EDGE,"E515"),sQuery(id+"F0.wireOp",EDGE,"E516"),sQuery(id+"F0.wireOp",EDGE,"E517"),sQuery(id+"F0.wireOp",EDGE,"E518"),sQuery(id+"F0.wireOp",EDGE,"E519"),sQuery(id+"F0.wireOp",EDGE,"E520"),sQuery(id+"F0.wireOp",EDGE,"E521"),sQuery(id+"F0.wireOp",EDGE,"E522"),sQuery(id+"F0.wireOp",EDGE,"E523"),sQuery(id+"F0.wireOp",EDGE,"E524"),sQuery(id+"F0.wireOp",EDGE,"E525"),sQuery(id+"F0.wireOp",EDGE,"E526"),sQuery(id+"F0.wireOp",EDGE,"E527"),sQuery(id+"F0.wireOp",EDGE,"E528"),sQuery(id+"F0.wireOp",EDGE,"E529"),sQuery(id+"F0.wireOp",EDGE,"E530"),sQuery(id+"F0.wireOp",EDGE,"E531"),sQuery(id+"F0.wireOp",EDGE,"E532"),sQuery(id+"F0.wireOp",EDGE,"E533"),sQuery(id+"F0.wireOp",EDGE,"E534"),sQuery(id+"F0.wireOp",EDGE,"E535"),sQuery(id+"F0.wireOp",EDGE,"E536"),sQuery(id+"F0.wireOp",EDGE,"E537"),sQuery(id+"F0.wireOp",EDGE,"E538"),sQuery(id+"F0.wireOp",EDGE,"E539"),sQuery(id+"F0.wireOp",EDGE,"E540"),sQuery(id+"F0.wireOp",EDGE,"E541"),sQuery(id+"F0.wireOp",EDGE,"E542"),sQuery(id+"F0.wireOp",EDGE,"E543"),sQuery(id+"F0.wireOp",EDGE,"E544"),sQuery(id+"F0.wireOp",EDGE,"E545"),sQuery(id+"F0.wireOp",EDGE,"E546"),sQuery(id+"F0.wireOp",EDGE,"E547"),sQuery(id+"F0.wireOp",EDGE,"E548"),sQuery(id+"F0.wireOp",EDGE,"E549"),sQuery(id+"F0.wireOp",EDGE,"E550"),sQuery(id+"F0.wireOp",EDGE,"E551"),sQuery(id+"F0.wireOp",EDGE,"E552"),sQuery(id+"F0.wireOp",EDGE,"E553"),sQuery(id+"F0.wireOp",EDGE,"E554"),sQuery(id+"F0.wireOp",EDGE,"E555"),sQuery(id+"F0.wireOp",EDGE,"E556"),sQuery(id+"F0.wireOp",EDGE,"E557"),sQuery(id+"F0.wireOp",EDGE,"E558"),sQuery(id+"F0.wireOp",EDGE,"E559"),sQuery(id+"F0.wireOp",EDGE,"E560"),sQuery(id+"F0.wireOp",EDGE,"E561"),sQuery(id+"F0.wireOp",EDGE,"E562"),sQuery(id+"F0.wireOp",EDGE,"E563"),sQuery(id+"F0.wireOp",EDGE,"E564"),sQuery(id+"F0.wireOp",EDGE,"E565"),sQuery(id+"F0.wireOp",EDGE,"E566"),sQuery(id+"F0.wireOp",EDGE,"E567"),sQuery(id+"F0.wireOp",EDGE,"E568"),sQuery(id+"F0.wireOp",EDGE,"E569"),sQuery(id+"F0.wireOp",EDGE,"E570"),sQuery(id+"F0.wireOp",EDGE,"E571"),sQuery(id+"F0.wireOp",EDGE,"E572"),sQuery(id+"F0.wireOp",EDGE,"E573"),sQuery(id+"F0.wireOp",EDGE,"E574"),sQuery(id+"F0.wireOp",EDGE,"E575"),sQuery(id+"F0.wireOp",EDGE,"E576"),sQuery(id+"F0.wireOp",EDGE,"E577"),sQuery(id+"F0.wireOp",EDGE,"E578"),sQuery(id+"F0.wireOp",EDGE,"E579"),sQuery(id+"F0.wireOp",EDGE,"E580"),sQuery(id+"F0.wireOp",EDGE,"E581"),sQuery(id+"F0.wireOp",EDGE,"E582"),sQuery(id+"F0.wireOp",EDGE,"E583"),sQuery(id+"F0.wireOp",EDGE,"E584"),sQuery(id+"F0.wireOp",EDGE,"E585"),sQuery(id+"F0.wireOp",EDGE,"E586"),sQuery(id+"F0.wireOp",EDGE,"E587"),sQuery(id+"F0.wireOp",EDGE,"E588"),sQuery(id+"F0.wireOp",EDGE,"E589"),sQuery(id+"F0.wireOp",EDGE,"E590"),sQuery(id+"F0.wireOp",EDGE,"E591"),sQuery(id+"F0.wireOp",EDGE,"E592"),sQuery(id+"F0.wireOp",EDGE,"E593"),sQuery(id+"F0.wireOp",EDGE,"E594"),sQuery(id+"F0.wireOp",EDGE,"E595"),sQuery(id+"F0.wireOp",EDGE,"E596"),sQuery(id+"F0.wireOp",EDGE,"E597"),sQuery(id+"F0.wireOp",EDGE,"E598"),sQuery(id+"F0.wireOp",EDGE,"E599"),sQuery(id+"F0.wireOp",EDGE,"E600"),sQuery(id+"F0.wireOp",EDGE,"E601"),sQuery(id+"F0.wireOp",EDGE,"E602"),sQuery(id+"F0.wireOp",EDGE,"E603"),sQuery(id+"F0.wireOp",EDGE,"E604"),sQuery(id+"F0.wireOp",EDGE,"E605"),sQuery(id+"F0.wireOp",EDGE,"E606"),sQuery(id+"F0.wireOp",EDGE,"E607"),sQuery(id+"F0.wireOp",EDGE,"E608"),sQuery(id+"F0.wireOp",EDGE,"E609"),sQuery(id+"F0.wireOp",EDGE,"E610"),sQuery(id+"F0.wireOp",EDGE,"E611"),sQuery(id+"F0.wireOp",EDGE,"E612"),sQuery(id+"F0.wireOp",EDGE,"E613"),sQuery(id+"F0.wireOp",EDGE,"E614"),sQuery(id+"F0.wireOp",EDGE,"E615"),sQuery(id+"F0.wireOp",EDGE,"E616"),sQuery(id+"F0.wireOp",EDGE,"E617"),sQuery(id+"F0.wireOp",EDGE,"E618"),sQuery(id+"F0.wireOp",EDGE,"E619"),sQuery(id+"F0.wireOp",EDGE,"E620"),sQuery(id+"F0.wireOp",EDGE,"E621"),sQuery(id+"F0.wireOp",EDGE,"E622"),sQuery(id+"F0.wireOp",EDGE,"E623"),sQuery(id+"F0.wireOp",EDGE,"E624"),sQuery(id+"F0.wireOp",EDGE,"E625"),sQuery(id+"F0.wireOp",EDGE,"E626"),sQuery(id+"F0.wireOp",EDGE,"E627"),sQuery(id+"F0.wireOp",EDGE,"E628"),sQuery(id+"F0.wireOp",EDGE,"E629"),sQuery(id+"F0.wireOp",EDGE,"E630"),sQuery(id+"F0.wireOp",EDGE,"E631"),sQuery(id+"F0.wireOp",EDGE,"E632"),sQuery(id+"F0.wireOp",EDGE,"E633"),sQuery(id+"F0.wireOp",EDGE,"E634"),sQuery(id+"F0.wireOp",EDGE,"E635"),sQuery(id+"F0.wireOp",EDGE,"E636"),sQuery(id+"F0.wireOp",EDGE,"E637"),sQuery(id+"F0.wireOp",EDGE,"E638"),sQuery(id+"F0.wireOp",EDGE,"E639"),sQuery(id+"F0.wireOp",EDGE,"E640"),sQuery(id+"F0.wireOp",EDGE,"E641"),sQuery(id+"F0.wireOp",EDGE,"E642"),sQuery(id+"F0.wireOp",EDGE,"E643"),sQuery(id+"F0.wireOp",EDGE,"E644"),sQuery(id+"F0.wireOp",EDGE,"E645"),sQuery(id+"F0.wireOp",EDGE,"E646"),sQuery(id+"F0.wireOp",EDGE,"E647"),sQuery(id+"F0.wireOp",EDGE,"E648"),sQuery(id+"F0.wireOp",EDGE,"E649"),sQuery(id+"F0.wireOp",EDGE,"E650"),sQuery(id+"F0.wireOp",EDGE,"E651"),sQuery(id+"F0.wireOp",EDGE,"E652"),sQuery(id+"F0.wireOp",EDGE,"E653"),sQuery(id+"F0.wireOp",EDGE,"E654"),sQuery(id+"F0.wireOp",EDGE,"E655"),sQuery(id+"F0.wireOp",EDGE,"E656"),sQuery(id+"F0.wireOp",EDGE,"E657"),sQuery(id+"F0.wireOp",EDGE,"E658"),sQuery(id+"F0.wireOp",EDGE,"E659"),sQuery(id+"F0.wireOp",EDGE,"E660"),sQuery(id+"F0.wireOp",EDGE,"E661"),sQuery(id+"F0.wireOp",EDGE,"E662"),sQuery(id+"F0.wireOp",EDGE,"E663"),sQuery(id+"F0.wireOp",EDGE,"E664"),sQuery(id+"F0.wireOp",EDGE,"E665"),sQuery(id+"F0.wireOp",EDGE,"E666"),sQuery(id+"F0.wireOp",EDGE,"E667"),sQuery(id+"F0.wireOp",EDGE,"E668"),sQuery(id+"F0.wireOp",EDGE,"E669"),sQuery(id+"F0.wireOp",EDGE,"E670"),sQuery(id+"F0.wireOp",EDGE,"E671"),sQuery(id+"F0.wireOp",EDGE,"E672"),sQuery(id+"F0.wireOp",EDGE,"E673"),sQuery(id+"F0.wireOp",EDGE,"E674"),sQuery(id+"F0.wireOp",EDGE,"E675"),sQuery(id+"F0.wireOp",EDGE,"E676"),sQuery(id+"F0.wireOp",EDGE,"E677"),sQuery(id+"F0.wireOp",EDGE,"E678"),sQuery(id+"F0.wireOp",EDGE,"E679"),sQuery(id+"F0.wireOp",EDGE,"E680"),sQuery(id+"F0.wireOp",EDGE,"E681"),sQuery(id+"F0.wireOp",EDGE,"E682"),sQuery(id+"F0.wireOp",EDGE,"E683"),sQuery(id+"F0.wireOp",EDGE,"E684"),sQuery(id+"F0.wireOp",EDGE,"E685"),sQuery(id+"F0.wireOp",EDGE,"E686"),sQuery(id+"F0.wireOp",EDGE,"E687"),sQuery(id+"F0.wireOp",EDGE,"E688"),sQuery(id+"F0.wireOp",EDGE,"E689"),sQuery(id+"F0.wireOp",EDGE,"E690"),sQuery(id+"F0.wireOp",EDGE,"E691"),sQuery(id+"F0.wireOp",EDGE,"E692"),sQuery(id+"F0.wireOp",EDGE,"E693"),sQuery(id+"F0.wireOp",EDGE,"E694"),sQuery(id+"F0.wireOp",EDGE,"E695"),sQuery(id+"F0.wireOp",EDGE,"E696"),sQuery(id+"F0.wireOp",EDGE,"E697"),sQuery(id+"F0.wireOp",EDGE,"E698"),sQuery(id+"F0.wireOp",EDGE,"E699"),sQuery(id+"F0.wireOp",EDGE,"E700"),sQuery(id+"F0.wireOp",EDGE,"E701"),sQuery(id+"F0.wireOp",EDGE,"E702"),sQuery(id+"F0.wireOp",EDGE,"E703"),sQuery(id+"F0.wireOp",EDGE,"E704"),sQuery(id+"F0.wireOp",EDGE,"E705"),sQuery(id+"F0.wireOp",EDGE,"E706"),sQuery(id+"F0.wireOp",EDGE,"E707"),sQuery(id+"F0.wireOp",EDGE,"E708"),sQuery(id+"F0.wireOp",EDGE,"E709"),sQuery(id+"F0.wireOp",EDGE,"E710"),sQuery(id+"F0.wireOp",EDGE,"E711"),sQuery(id+"F0.wireOp",EDGE,"E712"),sQuery(id+"F0.wireOp",EDGE,"E713"),sQuery(id+"F0.wireOp",EDGE,"E714"),sQuery(id+"F0.wireOp",EDGE,"E715"),sQuery(id+"F0.wireOp",EDGE,"E716"),sQuery(id+"F0.wireOp",EDGE,"E717"),sQuery(id+"F0.wireOp",EDGE,"E718"),sQuery(id+"F0.wireOp",EDGE,"E719"),sQuery(id+"F0.wireOp",EDGE,"E720"),sQuery(id+"F0.wireOp",EDGE,"E721"),sQuery(id+"F0.wireOp",EDGE,"E722"),sQuery(id+"F0.wireOp",EDGE,"E723"),sQuery(id+"F0.wireOp",EDGE,"E724"),sQuery(id+"F0.wireOp",EDGE,"E725"),sQuery(id+"F0.wireOp",EDGE,"E726"),sQuery(id+"F0.wireOp",EDGE,"E727"),sQuery(id+"F0.wireOp",EDGE,"E728"),sQuery(id+"F0.wireOp",EDGE,"E729"),sQuery(id+"F0.wireOp",EDGE,"E730"),sQuery(id+"F0.wireOp",EDGE,"E731"),sQuery(id+"F0.wireOp",EDGE,"E732"),sQuery(id+"F0.wireOp",EDGE,"E733"),sQuery(id+"F0.wireOp",EDGE,"E734"),sQuery(id+"F0.wireOp",EDGE,"E735"),sQuery(id+"F0.wireOp",EDGE,"E736"),sQuery(id+"F0.wireOp",EDGE,"E737"),sQuery(id+"F0.wireOp",EDGE,"E738"),sQuery(id+"F0.wireOp",EDGE,"E739"),sQuery(id+"F0.wireOp",EDGE,"E740"),sQuery(id+"F0.wireOp",EDGE,"E741"),sQuery(id+"F0.wireOp",EDGE,"E742"),sQuery(id+"F0.wireOp",EDGE,"E743"),sQuery(id+"F0.wireOp",EDGE,"E744"),sQuery(id+"F0.wireOp",EDGE,"E745"),sQuery(id+"F0.wireOp",EDGE,"E746"),sQuery(id+"F0.wireOp",EDGE,"E747"),sQuery(id+"F0.wireOp",EDGE,"E748"),sQuery(id+"F0.wireOp",EDGE,"E749"),sQuery(id+"F0.wireOp",EDGE,"E750"),sQuery(id+"F0.wireOp",EDGE,"E751"),sQuery(id+"F0.wireOp",EDGE,"E752"),sQuery(id+"F0.wireOp",EDGE,"E753"),sQuery(id+"F0.wireOp",EDGE,"E754"),sQuery(id+"F0.wireOp",EDGE,"E755"),sQuery(id+"F0.wireOp",EDGE,"E756"),sQuery(id+"F0.wireOp",EDGE,"E757"),sQuery(id+"F0.wireOp",EDGE,"E758"),sQuery(id+"F0.wireOp",EDGE,"E759"),sQuery(id+"F0.wireOp",EDGE,"E760"),sQuery(id+"F0.wireOp",EDGE,"E761"),sQuery(id+"F0.wireOp",EDGE,"E762"),sQuery(id+"F0.wireOp",EDGE,"E763"),sQuery(id+"F0.wireOp",EDGE,"E764"),sQuery(id+"F0.wireOp",EDGE,"E765"),sQuery(id+"F0.wireOp",EDGE,"E766"),sQuery(id+"F0.wireOp",EDGE,"E767"),sQuery(id+"F0.wireOp",EDGE,"E768"),sQuery(id+"F0.wireOp",EDGE,"E769"),sQuery(id+"F0.wireOp",EDGE,"E770"),sQuery(id+"F0.wireOp",EDGE,"E771"),sQuery(id+"F0.wireOp",EDGE,"E772"),sQuery(id+"F0.wireOp",EDGE,"E773"),sQuery(id+"F0.wireOp",EDGE,"E774"),sQuery(id+"F0.wireOp",EDGE,"E775"),sQuery(id+"F0.wireOp",EDGE,"E776"),sQuery(id+"F0.wireOp",EDGE,"E777"),sQuery(id+"F0.wireOp",EDGE,"E778"),sQuery(id+"F0.wireOp",EDGE,"E779"),sQuery(id+"F0.wireOp",EDGE,"E780"),sQuery(id+"F0.wireOp",EDGE,"E781"),sQuery(id+"F0.wireOp",EDGE,"E782"),sQuery(id+"F0.wireOp",EDGE,"E783"),sQuery(id+"F0.wireOp",EDGE,"E784"),sQuery(id+"F0.wireOp",EDGE,"E785"),sQuery(id+"F0.wireOp",EDGE,"E786"),sQuery(id+"F0.wireOp",EDGE,"E787"),sQuery(id+"F0.wireOp",EDGE,"E788"),sQuery(id+"F0.wireOp",EDGE,"E789"),sQuery(id+"F0.wireOp",EDGE,"E790"),sQuery(id+"F0.wireOp",EDGE,"E791"),sQuery(id+"F0.wireOp",EDGE,"E792"),sQuery(id+"F0.wireOp",EDGE,"E793"),sQuery(id+"F0.wireOp",EDGE,"E794"),sQuery(id+"F0.wireOp",EDGE,"E795"),sQuery(id+"F0.wireOp",EDGE,"E796"),sQuery(id+"F0.wireOp",EDGE,"E797"),sQuery(id+"F0.wireOp",EDGE,"E798"),sQuery(id+"F0.wireOp",EDGE,"E799"),sQuery(id+"F0.wireOp",EDGE,"E800"),sQuery(id+"F0.wireOp",EDGE,"E801"),sQuery(id+"F0.wireOp",EDGE,"E802"),sQuery(id+"F0.wireOp",EDGE,"E803"),sQuery(id+"F0.wireOp",EDGE,"E804"),sQuery(id+"F0.wireOp",EDGE,"E805"),sQuery(id+"F0.wireOp",EDGE,"E806"),sQuery(id+"F0.wireOp",EDGE,"E807"),sQuery(id+"F0.wireOp",EDGE,"E808"),sQuery(id+"F0.wireOp",EDGE,"E809"),sQuery(id+"F0.wireOp",EDGE,"E810"),sQuery(id+"F0.wireOp",EDGE,"E811"),sQuery(id+"F0.wireOp",EDGE,"E812"),sQuery(id+"F0.wireOp",EDGE,"E813"),sQuery(id+"F0.wireOp",EDGE,"E814"),sQuery(id+"F0.wireOp",EDGE,"E815"),sQuery(id+"F0.wireOp",EDGE,"E816"),sQuery(id+"F0.wireOp",EDGE,"E817"),sQuery(id+"F0.wireOp",EDGE,"E818"),sQuery(id+"F0.wireOp",EDGE,"E819"),sQuery(id+"F0.wireOp",EDGE,"E820"),sQuery(id+"F0.wireOp",EDGE,"E821"),sQuery(id+"F0.wireOp",EDGE,"E822"),sQuery(id+"F0.wireOp",EDGE,"E823"),sQuery(id+"F0.wireOp",EDGE,"E824"),sQuery(id+"F0.wireOp",EDGE,"E825"),sQuery(id+"F0.wireOp",EDGE,"E826"),sQuery(id+"F0.wireOp",EDGE,"E827"),sQuery(id+"F0.wireOp",EDGE,"E828"),sQuery(id+"F0.wireOp",EDGE,"E829"),sQuery(id+"F0.wireOp",EDGE,"E830"),sQuery(id+"F0.wireOp",EDGE,"E831"),sQuery(id+"F0.wireOp",EDGE,"E832"),sQuery(id+"F0.wireOp",EDGE,"E833"),sQuery(id+"F0.wireOp",EDGE,"E834"),sQuery(id+"F0.wireOp",EDGE,"E835"),sQuery(id+"F0.wireOp",EDGE,"E836"),sQuery(id+"F0.wireOp",EDGE,"E837"),sQuery(id+"F0.wireOp",EDGE,"E838"),sQuery(id+"F0.wireOp",EDGE,"E839"),sQuery(id+"F0.wireOp",EDGE,"E840"),sQuery(id+"F0.wireOp",EDGE,"E841"),sQuery(id+"F0.wireOp",EDGE,"E842"),sQuery(id+"F0.wireOp",EDGE,"E843"),sQuery(id+"F0.wireOp",EDGE,"E844"),sQuery(id+"F0.wireOp",EDGE,"E845"),sQuery(id+"F0.wireOp",EDGE,"E846"),sQuery(id+"F0.wireOp",EDGE,"E847"),sQuery(id+"F0.wireOp",EDGE,"E848"),sQuery(id+"F0.wireOp",EDGE,"E849"),sQuery(id+"F0.wireOp",EDGE,"E850"),sQuery(id+"F0.wireOp",EDGE,"E851"),sQuery(id+"F0.wireOp",EDGE,"E852"),sQuery(id+"F0.wireOp",EDGE,"E853"),sQuery(id+"F0.wireOp",EDGE,"E854"),sQuery(id+"F0.wireOp",EDGE,"E855"),sQuery(id+"F0.wireOp",EDGE,"E856"),sQuery(id+"F0.wireOp",EDGE,"E857"),sQuery(id+"F0.wireOp",EDGE,"E858"),sQuery(id+"F0.wireOp",EDGE,"E859"),sQuery(id+"F0.wireOp",EDGE,"E860"),sQuery(id+"F0.wireOp",EDGE,"E861"),sQuery(id+"F0.wireOp",EDGE,"E862"),sQuery(id+"F0.wireOp",EDGE,"E863"),sQuery(id+"F0.wireOp",EDGE,"E864"),sQuery(id+"F0.wireOp",EDGE,"E865"),sQuery(id+"F0.wireOp",EDGE,"E866"),sQuery(id+"F0.wireOp",EDGE,"E867"),sQuery(id+"F0.wireOp",EDGE,"E868"),sQuery(id+"F0.wireOp",EDGE,"E869"),sQuery(id+"F0.wireOp",EDGE,"E870"),sQuery(id+"F0.wireOp",EDGE,"E871"),sQuery(id+"F0.wireOp",EDGE,"E872"),sQuery(id+"F0.wireOp",EDGE,"E873"),sQuery(id+"F0.wireOp",EDGE,"E874"),sQuery(id+"F0.wireOp",EDGE,"E875"),sQuery(id+"F0.wireOp",EDGE,"E876"),sQuery(id+"F0.wireOp",EDGE,"E877"),sQuery(id+"F0.wireOp",EDGE,"E878"),sQuery(id+"F0.wireOp",EDGE,"E879"),sQuery(id+"F0.wireOp",EDGE,"E880"),sQuery(id+"F0.wireOp",EDGE,"E881"),sQuery(id+"F0.wireOp",EDGE,"E882"),sQuery(id+"F0.wireOp",EDGE,"E883"),sQuery(id+"F0.wireOp",EDGE,"E884"),sQuery(id+"F0.wireOp",EDGE,"E885"),sQuery(id+"F0.wireOp",EDGE,"E886"),sQuery(id+"F0.wireOp",EDGE,"E887"),sQuery(id+"F0.wireOp",EDGE,"E888"),sQuery(id+"F0.wireOp",EDGE,"E889"),sQuery(id+"F0.wireOp",EDGE,"E890"),sQuery(id+"F0.wireOp",EDGE,"E891"),sQuery(id+"F0.wireOp",EDGE,"E892"),sQuery(id+"F0.wireOp",EDGE,"E893"),sQuery(id+"F0.wireOp",EDGE,"E894"),sQuery(id+"F0.wireOp",EDGE,"E895"),sQuery(id+"F0.wireOp",EDGE,"E896"),sQuery(id+"F0.wireOp",EDGE,"E897"),sQuery(id+"F0.wireOp",EDGE,"E898"),sQuery(id+"F0.wireOp",EDGE,"E899"),sQuery(id+"F0.wireOp",EDGE,"E900"),sQuery(id+"F0.wireOp",EDGE,"E901"),sQuery(id+"F0.wireOp",EDGE,"E902"),sQuery(id+"F0.wireOp",EDGE,"E903"),sQuery(id+"F0.wireOp",EDGE,"E904"),sQuery(id+"F0.wireOp",EDGE,"E905"),sQuery(id+"F0.wireOp",EDGE,"E906"),sQuery(id+"F0.wireOp",EDGE,"E907"),sQuery(id+"F0.wireOp",EDGE,"E908"),sQuery(id+"F0.wireOp",EDGE,"E909"),sQuery(id+"F0.wireOp",EDGE,"E910"),sQuery(id+"F0.wireOp",EDGE,"E911"),sQuery(id+"F0.wireOp",EDGE,"E912"),sQuery(id+"F0.wireOp",EDGE,"E913"),sQuery(id+"F0.wireOp",EDGE,"E914"),sQuery(id+"F0.wireOp",EDGE,"E915"),sQuery(id+"F0.wireOp",EDGE,"E916"),sQuery(id+"F0.wireOp",EDGE,"E917"),sQuery(id+"F0.wireOp",EDGE,"E918"),sQuery(id+"F0.wireOp",EDGE,"E919"),sQuery(id+"F0.wireOp",EDGE,"E920"),sQuery(id+"F0.wireOp",EDGE,"E921"),sQuery(id+"F0.wireOp",EDGE,"E922"),sQuery(id+"F0.wireOp",EDGE,"E923"),sQuery(id+"F0.wireOp",EDGE,"E924"),sQuery(id+"F0.wireOp",EDGE,"E925"),sQuery(id+"F0.wireOp",EDGE,"E926"),sQuery(id+"F0.wireOp",EDGE,"E927"),sQuery(id+"F0.wireOp",EDGE,"E928"),sQuery(id+"F0.wireOp",EDGE,"E929"),sQuery(id+"F0.wireOp",EDGE,"E930"),sQuery(id+"F0.wireOp",EDGE,"E931"),sQuery(id+"F0.wireOp",EDGE,"E932"),sQuery(id+"F0.wireOp",EDGE,"E933"),sQuery(id+"F0.wireOp",EDGE,"E934"),sQuery(id+"F0.wireOp",EDGE,"E935"),sQuery(id+"F0.wireOp",EDGE,"E936"),sQuery(id+"F0.wireOp",EDGE,"E937"),sQuery(id+"F0.wireOp",EDGE,"E938"),sQuery(id+"F0.wireOp",EDGE,"E939"),sQuery(id+"F0.wireOp",EDGE,"E940"),sQuery(id+"F0.wireOp",EDGE,"E941"),sQuery(id+"F0.wireOp",EDGE,"E942"),sQuery(id+"F0.wireOp",EDGE,"E943"),sQuery(id+"F0.wireOp",EDGE,"E944"),sQuery(id+"F0.wireOp",EDGE,"E945"),sQuery(id+"F0.wireOp",EDGE,"E946"),sQuery(id+"F0.wireOp",EDGE,"E947"),sQuery(id+"F0.wireOp",EDGE,"E948"),sQuery(id+"F0.wireOp",EDGE,"E949"),sQuery(id+"F0.wireOp",EDGE,"E950"),sQuery(id+"F0.wireOp",EDGE,"E951"),sQuery(id+"F0.wireOp",EDGE,"E952"),sQuery(id+"F0.wireOp",EDGE,"E953"),sQuery(id+"F0.wireOp",EDGE,"E954"),sQuery(id+"F0.wireOp",EDGE,"E955"),sQuery(id+"F0.wireOp",EDGE,"E956"),sQuery(id+"F0.wireOp",EDGE,"E957"),sQuery(id+"F0.wireOp",EDGE,"E958"),sQuery(id+"F0.wireOp",EDGE,"E959"),sQuery(id+"F0.wireOp",EDGE,"E960"),sQuery(id+"F0.wireOp",EDGE,"E961"),sQuery(id+"F0.wireOp",EDGE,"E962"),sQuery(id+"F0.wireOp",EDGE,"E963"),sQuery(id+"F0.wireOp",EDGE,"E964"),sQuery(id+"F0.wireOp",EDGE,"E965"),sQuery(id+"F0.wireOp",EDGE,"E966"),sQuery(id+"F0.wireOp",EDGE,"E967"),sQuery(id+"F0.wireOp",EDGE,"E968"),sQuery(id+"F0.wireOp",EDGE,"E969"),sQuery(id+"F0.wireOp",EDGE,"E970"),sQuery(id+"F0.wireOp",EDGE,"E971"),sQuery(id+"F0.wireOp",EDGE,"E972"),sQuery(id+"F0.wireOp",EDGE,"E973"),sQuery(id+"F0.wireOp",EDGE,"E974"),sQuery(id+"F0.wireOp",EDGE,"E975"),sQuery(id+"F0.wireOp",EDGE,"E976"),sQuery(id+"F0.wireOp",EDGE,"E977"),sQuery(id+"F0.wireOp",EDGE,"E978"),sQuery(id+"F0.wireOp",EDGE,"E979"),sQuery(id+"F0.wireOp",EDGE,"E980"),sQuery(id+"F0.wireOp",EDGE,"E981"),sQuery(id+"F0.wireOp",EDGE,"E982"),sQuery(id+"F0.wireOp",EDGE,"E983"),sQuery(id+"F0.wireOp",EDGE,"E984"),sQuery(id+"F0.wireOp",EDGE,"E985"),sQuery(id+"F0.wireOp",EDGE,"E986"),sQuery(id+"F0.wireOp",EDGE,"E987"),sQuery(id+"F0.wireOp",EDGE,"E988"),sQuery(id+"F0.wireOp",EDGE,"E989"),sQuery(id+"F0.wireOp",EDGE,"E990"),sQuery(id+"F0.wireOp",EDGE,"E991"),sQuery(id+"F0.wireOp",EDGE,"E992"),sQuery(id+"F0.wireOp",EDGE,"E993"),sQuery(id+"F0.wireOp",EDGE,"E994"),sQuery(id+"F0.wireOp",EDGE,"E995"),sQuery(id+"F0.wireOp",EDGE,"E996"),sQuery(id+"F0.wireOp",EDGE,"E997"),sQuery(id+"F0.wireOp",EDGE,"E998"),sQuery(id+"F0.wireOp",EDGE,"E999"),sQuery(id+"F0.wireOp",EDGE,"E1000"),sQuery(id+"F0.wireOp",EDGE,"E1001"),sQuery(id+"F0.wireOp",EDGE,"E1002"),sQuery(id+"F0.wireOp",EDGE,"E1003"),sQuery(id+"F0.wireOp",EDGE,"E1004"),sQuery(id+"F0.wireOp",EDGE,"E1005"),sQuery(id+"F0.wireOp",EDGE,"E1006"),sQuery(id+"F0.wireOp",EDGE,"E1007"),sQuery(id+"F0.wireOp",EDGE,"E1008"),sQuery(id+"F0.wireOp",EDGE,"E1009"),sQuery(id+"F0.wireOp",EDGE,"E1010"),sQuery(id+"F0.wireOp",EDGE,"E1011"),sQuery(id+"F0.wireOp",EDGE,"E1012"),sQuery(id+"F0.wireOp",EDGE,"E1013"),sQuery(id+"F0.wireOp",EDGE,"E1014"),sQuery(id+"F0.wireOp",EDGE,"E1015"),sQuery(id+"F0.wireOp",EDGE,"E1016"),sQuery(id+"F0.wireOp",EDGE,"E1017"),sQuery(id+"F0.wireOp",EDGE,"E1018"),sQuery(id+"F0.wireOp",EDGE,"E1019"),sQuery(id+"F0.wireOp",EDGE,"E1020"),sQuery(id+"F0.wireOp",EDGE,"E1021"),sQuery(id+"F0.wireOp",EDGE,"E1022"),sQuery(id+"F0.wireOp",EDGE,"E1023"),sQuery(id+"F0.wireOp",EDGE,"E1024"),sQuery(id+"F0.wireOp",EDGE,"E1025"),sQuery(id+"F0.wireOp",EDGE,"E1026"),sQuery(id+"F0.wireOp",EDGE,"E1027"),sQuery(id+"F0.wireOp",EDGE,"E1028"),sQuery(id+"F0.wireOp",EDGE,"E1029"),sQuery(id+"F0.wireOp",EDGE,"E1030"),sQuery(id+"F0.wireOp",EDGE,"E1031"),sQuery(id+"F0.wireOp",EDGE,"E1032"),sQuery(id+"F0.wireOp",EDGE,"E1033"),sQuery(id+"F0.wireOp",EDGE,"E1034"),sQuery(id+"F0.wireOp",EDGE,"E1035"),sQuery(id+"F0.wireOp",EDGE,"E1036"),sQuery(id+"F0.wireOp",EDGE,"E1037"),sQuery(id+"F0.wireOp",EDGE,"E1038"),sQuery(id+"F0.wireOp",EDGE,"E1039"),sQuery(id+"F0.wireOp",EDGE,"E1040"),sQuery(id+"F0.wireOp",EDGE,"E1041"),sQuery(id+"F0.wireOp",EDGE,"E1042"),sQuery(id+"F0.wireOp",EDGE,"E1043"),sQuery(id+"F0.wireOp",EDGE,"E1044"),sQuery(id+"F0.wireOp",EDGE,"E1045"),sQuery(id+"F0.wireOp",EDGE,"E1046"),sQuery(id+"F0.wireOp",EDGE,"E1047"),sQuery(id+"F0.wireOp",EDGE,"E1048"),sQuery(id+"F0.wireOp",EDGE,"E1049"),sQuery(id+"F0.wireOp",EDGE,"E1050"),sQuery(id+"F0.wireOp",EDGE,"E1051"),sQuery(id+"F0.wireOp",EDGE,"E1052"),sQuery(id+"F0.wireOp",EDGE,"E1053"),sQuery(id+"F0.wireOp",EDGE,"E1054"),sQuery(id+"F0.wireOp",EDGE,"E1055"),sQuery(id+"F0.wireOp",EDGE,"E1056"),sQuery(id+"F0.wireOp",EDGE,"E1057"),sQuery(id+"F0.wireOp",EDGE,"E1058"),sQuery(id+"F0.wireOp",EDGE,"E1059"),sQuery(id+"F0.wireOp",EDGE,"E1060"),sQuery(id+"F0.wireOp",EDGE,"E1061"),sQuery(id+"F0.wireOp",EDGE,"E1062"),sQuery(id+"F0.wireOp",EDGE,"E1063"),sQuery(id+"F0.wireOp",EDGE,"E1064"),sQuery(id+"F0.wireOp",EDGE,"E1065"),sQuery(id+"F0.wireOp",EDGE,"E1066"),sQuery(id+"F0.wireOp",EDGE,"E1067"),sQuery(id+"F0.wireOp",EDGE,"E1068"),sQuery(id+"F0.wireOp",EDGE,"E1069"),sQuery(id+"F0.wireOp",EDGE,"E1070"),sQuery(id+"F0.wireOp",EDGE,"E1071"),sQuery(id+"F0.wireOp",EDGE,"E1072"),sQuery(id+"F0.wireOp",EDGE,"E1073"),sQuery(id+"F0.wireOp",EDGE,"E1074"),sQuery(id+"F0.wireOp",EDGE,"E1075"),sQuery(id+"F0.wireOp",EDGE,"E1076"),sQuery(id+"F0.wireOp",EDGE,"E1077"),sQuery(id+"F0.wireOp",EDGE,"E1078"),sQuery(id+"F0.wireOp",EDGE,"E1079"),sQuery(id+"F0.wireOp",EDGE,"E1080"),sQuery(id+"F0.wireOp",EDGE,"E1081"),sQuery(id+"F0.wireOp",EDGE,"E1082"),sQuery(id+"F0.wireOp",EDGE,"E1083"),sQuery(id+"F0.wireOp",EDGE,"E1084"),sQuery(id+"F0.wireOp",EDGE,"E1085"),sQuery(id+"F0.wireOp",EDGE,"E1086"),sQuery(id+"F0.wireOp",EDGE,"E1087"),sQuery(id+"F0.wireOp",EDGE,"E1088"),sQuery(id+"F0.wireOp",EDGE,"E1089"),sQuery(id+"F0.wireOp",EDGE,"E1090"),sQuery(id+"F0.wireOp",EDGE,"E1091"),sQuery(id+"F0.wireOp",EDGE,"E1092"),sQuery(id+"F0.wireOp",EDGE,"E1093"),sQuery(id+"F0.wireOp",EDGE,"E1094"),sQuery(id+"F0.wireOp",EDGE,"E1095"),sQuery(id+"F0.wireOp",EDGE,"E1096"),sQuery(id+"F0.wireOp",EDGE,"E1097"),sQuery(id+"F0.wireOp",EDGE,"E1098"),sQuery(id+"F0.wireOp",EDGE,"E1099"),sQuery(id+"F0.wireOp",EDGE,"E1100"),sQuery(id+"F0.wireOp",EDGE,"E1101"),sQuery(id+"F0.wireOp",EDGE,"E1102"),sQuery(id+"F0.wireOp",EDGE,"E1103"),sQuery(id+"F0.wireOp",EDGE,"E1104"),sQuery(id+"F0.wireOp",EDGE,"E1105"),sQuery(id+"F0.wireOp",EDGE,"E1106"),sQuery(id+"F0.wireOp",EDGE,"E1107"),sQuery(id+"F0.wireOp",EDGE,"E1108"),sQuery(id+"F0.wireOp",EDGE,"E1109"),sQuery(id+"F0.wireOp",EDGE,"E1110"),sQuery(id+"F0.wireOp",EDGE,"E1111"),sQuery(id+"F0.wireOp",EDGE,"E1112"),sQuery(id+"F0.wireOp",EDGE,"E1113"),sQuery(id+"F0.wireOp",EDGE,"E1114"),sQuery(id+"F0.wireOp",EDGE,"E1115"),sQuery(id+"F0.wireOp",EDGE,"E1116"),sQuery(id+"F0.wireOp",EDGE,"E1117"),sQuery(id+"F0.wireOp",EDGE,"E1118"),sQuery(id+"F0.wireOp",EDGE,"E1119"),sQuery(id+"F0.wireOp",EDGE,"E1120"),sQuery(id+"F0.wireOp",EDGE,"E1121"),sQuery(id+"F0.wireOp",EDGE,"E1122"),sQuery(id+"F0.wireOp",EDGE,"E1123"),sQuery(id+"F0.wireOp",EDGE,"E1124"),sQuery(id+"F0.wireOp",EDGE,"E1125"),sQuery(id+"F0.wireOp",EDGE,"E1126"),sQuery(id+"F0.wireOp",EDGE,"E1127"),sQuery(id+"F0.wireOp",EDGE,"E1128"),sQuery(id+"F0.wireOp",EDGE,"E1129"),sQuery(id+"F0.wireOp",EDGE,"E1130"),sQuery(id+"F0.wireOp",EDGE,"E1131"),sQuery(id+"F0.wireOp",EDGE,"E1132"),sQuery(id+"F0.wireOp",EDGE,"E1133"),sQuery(id+"F0.wireOp",EDGE,"E1134"),sQuery(id+"F0.wireOp",EDGE,"E1135"),sQuery(id+"F0.wireOp",EDGE,"E1136"),sQuery(id+"F0.wireOp",EDGE,"E1137"),sQuery(id+"F0.wireOp",EDGE,"E1138"),sQuery(id+"F0.wireOp",EDGE,"E1139"),sQuery(id+"F0.wireOp",EDGE,"E1140"),sQuery(id+"F0.wireOp",EDGE,"E1141"),sQuery(id+"F0.wireOp",EDGE,"E1142"),sQuery(id+"F0.wireOp",EDGE,"E1143"),sQuery(id+"F0.wireOp",EDGE,"E1144"),sQuery(id+"F0.wireOp",EDGE,"E1145"),sQuery(id+"F0.wireOp",EDGE,"E1146"),sQuery(id+"F0.wireOp",EDGE,"E1147"),sQuery(id+"F0.wireOp",EDGE,"E1148"),sQuery(id+"F0.wireOp",EDGE,"E1149"),sQuery(id+"F0.wireOp",EDGE,"E1150"),sQuery(id+"F0.wireOp",EDGE,"E1151"),sQuery(id+"F0.wireOp",EDGE,"E1152"),sQuery(id+"F0.wireOp",EDGE,"E1153"),sQuery(id+"F0.wireOp",EDGE,"E1154"),sQuery(id+"F0.wireOp",EDGE,"E1155"),sQuery(id+"F0.wireOp",EDGE,"E1156"),sQuery(id+"F0.wireOp",EDGE,"E1157"),sQuery(id+"F0.wireOp",EDGE,"E1158"),sQuery(id+"F0.wireOp",EDGE,"E1159"),sQuery(id+"F0.wireOp",EDGE,"E1160"),sQuery(id+"F0.wireOp",EDGE,"E1161"),sQuery(id+"F0.wireOp",EDGE,"E1162"),sQuery(id+"F0.wireOp",EDGE,"E1163"),sQuery(id+"F0.wireOp",EDGE,"E1164"),sQuery(id+"F0.wireOp",EDGE,"E1165"),sQuery(id+"F0.wireOp",EDGE,"E1166"),sQuery(id+"F0.wireOp",EDGE,"E1167"),sQuery(id+"F0.wireOp",EDGE,"E1168"),sQuery(id+"F0.wireOp",EDGE,"E1169"),sQuery(id+"F0.wireOp",EDGE,"E1170"),sQuery(id+"F0.wireOp",EDGE,"E1171"),sQuery(id+"F0.wireOp",EDGE,"E1172"),sQuery(id+"F0.wireOp",EDGE,"E1173"),sQuery(id+"F0.wireOp",EDGE,"E1174"),sQuery(id+"F0.wireOp",EDGE,"E1175"),sQuery(id+"F0.wireOp",EDGE,"E1176"),sQuery(id+"F0.wireOp",EDGE,"E1177"),sQuery(id+"F0.wireOp",EDGE,"E1178"),sQuery(id+"F0.wireOp",EDGE,"E1179"),sQuery(id+"F0.wireOp",EDGE,"E1180"),sQuery(id+"F0.wireOp",EDGE,"E1181"),sQuery(id+"F0.wireOp",EDGE,"E1182"),sQuery(id+"F0.wireOp",EDGE,"E1183"),sQuery(id+"F0.wireOp",EDGE,"E1184"),sQuery(id+"F0.wireOp",EDGE,"E1185"),sQuery(id+"F0.wireOp",EDGE,"E1186"),sQuery(id+"F0.wireOp",EDGE,"E1187"),sQuery(id+"F0.wireOp",EDGE,"E1188"),sQuery(id+"F0.wireOp",EDGE,"E1189"),sQuery(id+"F0.wireOp",EDGE,"E1190"),sQuery(id+"F0.wireOp",EDGE,"E1191"),sQuery(id+"F0.wireOp",EDGE,"E1192"),sQuery(id+"F0.wireOp",EDGE,"E1193"),sQuery(id+"F0.wireOp",EDGE,"E1194"),sQuery(id+"F0.wireOp",EDGE,"E1195"),sQuery(id+"F0.wireOp",EDGE,"E1196"),sQuery(id+"F0.wireOp",EDGE,"E1197"),sQuery(id+"F0.wireOp",EDGE,"E1198"),sQuery(id+"F0.wireOp",EDGE,"E1199"),sQuery(id+"F0.wireOp",EDGE,"E1200"),sQuery(id+"F0.wireOp",EDGE,"E1201"),sQuery(id+"F0.wireOp",EDGE,"E1202"),sQuery(id+"F0.wireOp",EDGE,"E1203"),sQuery(id+"F0.wireOp",EDGE,"E1204"),sQuery(id+"F0.wireOp",EDGE,"E1205"),sQuery(id+"F0.wireOp",EDGE,"E1206"),sQuery(id+"F0.wireOp",EDGE,"E1207"),sQuery(id+"F0.wireOp",EDGE,"E1208"),sQuery(id+"F0.wireOp",EDGE,"E1209"),sQuery(id+"F0.wireOp",EDGE,"E1210"),sQuery(id+"F0.wireOp",EDGE,"E1211"),sQuery(id+"F0.wireOp",EDGE,"E1212"),sQuery(id+"F0.wireOp",EDGE,"E1213"),sQuery(id+"F0.wireOp",EDGE,"E1214"),sQuery(id+"F0.wireOp",EDGE,"E1215"),sQuery(id+"F0.wireOp",EDGE,"E1216"),sQuery(id+"F0.wireOp",EDGE,"E1217"),sQuery(id+"F0.wireOp",EDGE,"E1218"),sQuery(id+"F0.wireOp",EDGE,"E1219"),sQuery(id+"F0.wireOp",EDGE,"E1220"),sQuery(id+"F0.wireOp",EDGE,"E1221"),sQuery(id+"F0.wireOp",EDGE,"E1222"),sQuery(id+"F0.wireOp",EDGE,"E1223"),sQuery(id+"F0.wireOp",EDGE,"E1224"),sQuery(id+"F0.wireOp",EDGE,"E1225"),sQuery(id+"F0.wireOp",EDGE,"E1226"),sQuery(id+"F0.wireOp",EDGE,"E1227"),sQuery(id+"F0.wireOp",EDGE,"E1228"),sQuery(id+"F0.wireOp",EDGE,"E1229"),sQuery(id+"F0.wireOp",EDGE,"E1230"),sQuery(id+"F0.wireOp",EDGE,"E1231"),sQuery(id+"F0.wireOp",EDGE,"E1232"),sQuery(id+"F0.wireOp",EDGE,"E1233"),sQuery(id+"F0.wireOp",EDGE,"E1234"),sQuery(id+"F0.wireOp",EDGE,"E1235"),sQuery(id+"F0.wireOp",EDGE,"E1236"),sQuery(id+"F0.wireOp",EDGE,"E1237"),sQuery(id+"F0.wireOp",EDGE,"E1238"),sQuery(id+"F0.wireOp",EDGE,"E1239"),sQuery(id+"F0.wireOp",EDGE,"E1240"),sQuery(id+"F0.wireOp",EDGE,"E1241"),sQuery(id+"F0.wireOp",EDGE,"E1242"),sQuery(id+"F0.wireOp",EDGE,"E1243"),sQuery(id+"F0.wireOp",EDGE,"E1244"),sQuery(id+"F0.wireOp",EDGE,"E1245"),sQuery(id+"F0.wireOp",EDGE,"E1246"),sQuery(id+"F0.wireOp",EDGE,"E1247"),sQuery(id+"F0.wireOp",EDGE,"E1248"),sQuery(id+"F0.wireOp",EDGE,"E1249"),sQuery(id+"F0.wireOp",EDGE,"E1250"),sQuery(id+"F0.wireOp",EDGE,"E1251"),sQuery(id+"F0.wireOp",EDGE,"E1252"),sQuery(id+"F0.wireOp",EDGE,"E1253"),sQuery(id+"F0.wireOp",EDGE,"E1254"),sQuery(id+"F0.wireOp",EDGE,"E1255"),sQuery(id+"F0.wireOp",EDGE,"E1256"),sQuery(id+"F0.wireOp",EDGE,"E1257"),sQuery(id+"F0.wireOp",EDGE,"E1258"),sQuery(id+"F0.wireOp",EDGE,"E1259"),sQuery(id+"F0.wireOp",EDGE,"E1260"),sQuery(id+"F0.wireOp",EDGE,"E1261"),sQuery(id+"F0.wireOp",EDGE,"E1262"),sQuery(id+"F0.wireOp",EDGE,"E1263"),sQuery(id+"F0.wireOp",EDGE,"E1264"),sQuery(id+"F0.wireOp",EDGE,"E1265"),sQuery(id+"F0.wireOp",EDGE,"E1266"),sQuery(id+"F0.wireOp",EDGE,"E1267"),sQuery(id+"F0.wireOp",EDGE,"E1268"),sQuery(id+"F0.wireOp",EDGE,"E1269"),sQuery(id+"F0.wireOp",EDGE,"E1270"),sQuery(id+"F0.wireOp",EDGE,"E1271"),sQuery(id+"F0.wireOp",EDGE,"E1272"),sQuery(id+"F0.wireOp",EDGE,"E1273"),sQuery(id+"F0.wireOp",EDGE,"E1274"),sQuery(id+"F0.wireOp",EDGE,"E1275"),sQuery(id+"F0.wireOp",EDGE,"E1276"),sQuery(id+"F0.wireOp",EDGE,"E1277"),sQuery(id+"F0.wireOp",EDGE,"E1278"),sQuery(id+"F0.wireOp",EDGE,"E1279"),sQuery(id+"F0.wireOp",EDGE,"E1280"),sQuery(id+"F0.wireOp",EDGE,"E1281"),sQuery(id+"F0.wireOp",EDGE,"E1282"),sQuery(id+"F0.wireOp",EDGE,"E1283"),sQuery(id+"F0.wireOp",EDGE,"E1284"),sQuery(id+"F0.wireOp",EDGE,"E1285"),sQuery(id+"F0.wireOp",EDGE,"E1286"),sQuery(id+"F0.wireOp",EDGE,"E1287"),sQuery(id+"F0.wireOp",EDGE,"E1288"),sQuery(id+"F0.wireOp",EDGE,"E1289"),sQuery(id+"F0.wireOp",EDGE,"E1290"),sQuery(id+"F0.wireOp",EDGE,"E1291"),sQuery(id+"F0.wireOp",EDGE,"E1292"),sQuery(id+"F0.wireOp",EDGE,"E1293"),sQuery(id+"F0.wireOp",EDGE,"E1294"),sQuery(id+"F0.wireOp",EDGE,"E1295"),sQuery(id+"F0.wireOp",EDGE,"E1296"),sQuery(id+"F0.wireOp",EDGE,"E1297"),sQuery(id+"F0.wireOp",EDGE,"E1298"),sQuery(id+"F0.wireOp",EDGE,"E1299"),sQuery(id+"F0.wireOp",EDGE,"E1300"),sQuery(id+"F0.wireOp",EDGE,"E1301"),sQuery(id+"F0.wireOp",EDGE,"E1302"),sQuery(id+"F0.wireOp",EDGE,"E1303"),sQuery(id+"F0.wireOp",EDGE,"E1304"),sQuery(id+"F0.wireOp",EDGE,"E1305"),sQuery(id+"F0.wireOp",EDGE,"E1306"),sQuery(id+"F0.wireOp",EDGE,"E1307"),sQuery(id+"F0.wireOp",EDGE,"E1308"),sQuery(id+"F0.wireOp",EDGE,"E1309"),sQuery(id+"F0.wireOp",EDGE,"E1310"),sQuery(id+"F0.wireOp",EDGE,"E1311"),sQuery(id+"F0.wireOp",EDGE,"E1312"),sQuery(id+"F0.wireOp",EDGE,"E1313"),sQuery(id+"F0.wireOp",EDGE,"E1314"),sQuery(id+"F0.wireOp",EDGE,"E1315"),sQuery(id+"F0.wireOp",EDGE,"E1316"),sQuery(id+"F0.wireOp",EDGE,"E1317"),sQuery(id+"F0.wireOp",EDGE,"E1318"),sQuery(id+"F0.wireOp",EDGE,"E1319"),sQuery(id+"F0.wireOp",EDGE,"E1320"),sQuery(id+"F0.wireOp",EDGE,"E1321"),sQuery(id+"F0.wireOp",EDGE,"E1322"),sQuery(id+"F0.wireOp",EDGE,"E1323"),sQuery(id+"F0.wireOp",EDGE,"E1324"),sQuery(id+"F0.wireOp",EDGE,"E1325"),sQuery(id+"F0.wireOp",EDGE,"E1326"),sQuery(id+"F0.wireOp",EDGE,"E1327"),sQuery(id+"F0.wireOp",EDGE,"E1328"),sQuery(id+"F0.wireOp",EDGE,"E1329"),sQuery(id+"F0.wireOp",EDGE,"E1330"),sQuery(id+"F0.wireOp",EDGE,"E1331"),sQuery(id+"F0.wireOp",EDGE,"E1332"),sQuery(id+"F0.wireOp",EDGE,"E1333"),sQuery(id+"F0.wireOp",EDGE,"E1334"),sQuery(id+"F0.wireOp",EDGE,"E1335"),sQuery(id+"F0.wireOp",EDGE,"E1336"),sQuery(id+"F0.wireOp",EDGE,"E1337"),sQuery(id+"F0.wireOp",EDGE,"E1338"),sQuery(id+"F0.wireOp",EDGE,"E1339"),sQuery(id+"F0.wireOp",EDGE,"E1340"),sQuery(id+"F0.wireOp",EDGE,"E1341"),sQuery(id+"F0.wireOp",EDGE,"E1342"),sQuery(id+"F0.wireOp",EDGE,"E1343"),sQuery(id+"F0.wireOp",EDGE,"E1344"),sQuery(id+"F0.wireOp",EDGE,"E1345"),sQuery(id+"F0.wireOp",EDGE,"E1346"),sQuery(id+"F0.wireOp",EDGE,"E1347"),sQuery(id+"F0.wireOp",EDGE,"E1348"),sQuery(id+"F0.wireOp",EDGE,"E1349"),sQuery(id+"F0.wireOp",EDGE,"E1350"),sQuery(id+"F0.wireOp",EDGE,"E1351"),sQuery(id+"F0.wireOp",EDGE,"E1352"),sQuery(id+"F0.wireOp",EDGE,"E1353"),sQuery(id+"F0.wireOp",EDGE,"E1354"),sQuery(id+"F0.wireOp",EDGE,"E1355"),sQuery(id+"F0.wireOp",EDGE,"E1356"),sQuery(id+"F0.wireOp",EDGE,"E1357"),sQuery(id+"F0.wireOp",EDGE,"E1358"),sQuery(id+"F0.wireOp",EDGE,"E1359"),sQuery(id+"F0.wireOp",EDGE,"E1360"),sQuery(id+"F0.wireOp",EDGE,"E1361"),sQuery(id+"F0.wireOp",EDGE,"E1362"),sQuery(id+"F0.wireOp",EDGE,"E1363"),sQuery(id+"F0.wireOp",EDGE,"E1364"),sQuery(id+"F0.wireOp",EDGE,"E1365"),sQuery(id+"F0.wireOp",EDGE,"E1366"),sQuery(id+"F0.wireOp",EDGE,"E1367"),sQuery(id+"F0.wireOp",EDGE,"E1368"),sQuery(id+"F0.wireOp",EDGE,"E1369"),sQuery(id+"F0.wireOp",EDGE,"E1370"),sQuery(id+"F0.wireOp",EDGE,"E1371"),sQuery(id+"F0.wireOp",EDGE,"E1372"),sQuery(id+"F0.wireOp",EDGE,"E1373"),sQuery(id+"F0.wireOp",EDGE,"E1374"),sQuery(id+"F0.wireOp",EDGE,"E1375"),sQuery(id+"F0.wireOp",EDGE,"E1376"),sQuery(id+"F0.wireOp",EDGE,"E1377"),sQuery(id+"F0.wireOp",EDGE,"E1378"),sQuery(id+"F0.wireOp",EDGE,"E1379"),sQuery(id+"F0.wireOp",EDGE,"E1380"),sQuery(id+"F0.wireOp",EDGE,"E1381"),sQuery(id+"F0.wireOp",EDGE,"E1382"),sQuery(id+"F0.wireOp",EDGE,"E1383"),sQuery(id+"F0.wireOp",EDGE,"E1384"),sQuery(id+"F0.wireOp",EDGE,"E1385"),sQuery(id+"F0.wireOp",EDGE,"E1386"),sQuery(id+"F0.wireOp",EDGE,"E1387"),sQuery(id+"F0.wireOp",EDGE,"E1388"),sQuery(id+"F0.wireOp",EDGE,"E1389"),sQuery(id+"F0.wireOp",EDGE,"E1390"),sQuery(id+"F0.wireOp",EDGE,"E1391"),sQuery(id+"F0.wireOp",EDGE,"E1392"),sQuery(id+"F0.wireOp",EDGE,"E1393"),sQuery(id+"F0.wireOp",EDGE,"E1394"),sQuery(id+"F0.wireOp",EDGE,"E1395"),sQuery(id+"F0.wireOp",EDGE,"E1396"),sQuery(id+"F0.wireOp",EDGE,"E1397"),sQuery(id+"F0.wireOp",EDGE,"E1398"),sQuery(id+"F0.wireOp",EDGE,"E1399"),sQuery(id+"F0.wireOp",EDGE,"E1400"),sQuery(id+"F0.wireOp",EDGE,"E1401"),sQuery(id+"F0.wireOp",EDGE,"E1402"),sQuery(id+"F0.wireOp",EDGE,"E1403"),sQuery(id+"F0.wireOp",EDGE,"E1404"),sQuery(id+"F0.wireOp",EDGE,"E1405"),sQuery(id+"F0.wireOp",EDGE,"E1406"),sQuery(id+"F0.wireOp",EDGE,"E1407"),sQuery(id+"F0.wireOp",EDGE,"E1408"),sQuery(id+"F0.wireOp",EDGE,"E1409"),sQuery(id+"F0.wireOp",EDGE,"E1410"),sQuery(id+"F0.wireOp",EDGE,"E1411"),sQuery(id+"F0.wireOp",EDGE,"E1412"),sQuery(id+"F0.wireOp",EDGE,"E1413"),sQuery(id+"F0.wireOp",EDGE,"E1414"),sQuery(id+"F0.wireOp",EDGE,"E1415"),sQuery(id+"F0.wireOp",EDGE,"E1416"),sQuery(id+"F0.wireOp",EDGE,"E1417"),sQuery(id+"F0.wireOp",EDGE,"E1418"),sQuery(id+"F0.wireOp",EDGE,"E1419"),sQuery(id+"F0.wireOp",EDGE,"E1420"),sQuery(id+"F0.wireOp",EDGE,"E1421"),sQuery(id+"F0.wireOp",EDGE,"E1422"),sQuery(id+"F0.wireOp",EDGE,"E1423"),sQuery(id+"F0.wireOp",EDGE,"E1424"),sQuery(id+"F0.wireOp",EDGE,"E1425"),sQuery(id+"F0.wireOp",EDGE,"E1426"),sQuery(id+"F0.wireOp",EDGE,"E1427"),sQuery(id+"F0.wireOp",EDGE,"E1428"),sQuery(id+"F0.wireOp",EDGE,"E1429"),sQuery(id+"F0.wireOp",EDGE,"E1430"),sQuery(id+"F0.wireOp",EDGE,"E1431"),sQuery(id+"F0.wireOp",EDGE,"E1432"),sQuery(id+"F0.wireOp",EDGE,"E1433"),sQuery(id+"F0.wireOp",EDGE,"E1434"),sQuery(id+"F0.wireOp",EDGE,"E1435"),sQuery(id+"F0.wireOp",EDGE,"E1436"),sQuery(id+"F0.wireOp",EDGE,"E1437"),sQuery(id+"F0.wireOp",EDGE,"E1438"),sQuery(id+"F0.wireOp",EDGE,"E1439"),sQuery(id+"F0.wireOp",EDGE,"E1440"),sQuery(id+"F0.wireOp",EDGE,"E1441"),sQuery(id+"F0.wireOp",EDGE,"E1442"),sQuery(id+"F0.wireOp",EDGE,"E1443"),sQuery(id+"F0.wireOp",EDGE,"E1444"),sQuery(id+"F0.wireOp",EDGE,"E1445"),sQuery(id+"F0.wireOp",EDGE,"E1446"),sQuery(id+"F0.wireOp",EDGE,"E1447"),sQuery(id+"F0.wireOp",EDGE,"E1448"),sQuery(id+"F0.wireOp",EDGE,"E1449"),sQuery(id+"F0.wireOp",EDGE,"E1450"),sQuery(id+"F0.wireOp",EDGE,"E1451"),sQuery(id+"F0.wireOp",EDGE,"E1452"),sQuery(id+"F0.wireOp",EDGE,"E1453"),sQuery(id+"F0.wireOp",EDGE,"E1454"),sQuery(id+"F0.wireOp",EDGE,"E1455"),sQuery(id+"F0.wireOp",EDGE,"E1456"),sQuery(id+"F0.wireOp",EDGE,"E1457"),sQuery(id+"F0.wireOp",EDGE,"E1458"),sQuery(id+"F0.wireOp",EDGE,"E1459"),sQuery(id+"F0.wireOp",EDGE,"E1460"),sQuery(id+"F0.wireOp",EDGE,"E1461"),sQuery(id+"F0.wireOp",EDGE,"E1462"),sQuery(id+"F0.wireOp",EDGE,"E1463"),sQuery(id+"F0.wireOp",EDGE,"E1464"),sQuery(id+"F0.wireOp",EDGE,"E1465"),sQuery(id+"F0.wireOp",EDGE,"E1466"),sQuery(id+"F0.wireOp",EDGE,"E1467"),sQuery(id+"F0.wireOp",EDGE,"E1468"),sQuery(id+"F0.wireOp",EDGE,"E1469"),sQuery(id+"F0.wireOp",EDGE,"E1470"),sQuery(id+"F0.wireOp",EDGE,"E1471"),sQuery(id+"F0.wireOp",EDGE,"E1472"),sQuery(id+"F0.wireOp",EDGE,"E1473"),sQuery(id+"F0.wireOp",EDGE,"E1474"),sQuery(id+"F0.wireOp",EDGE,"E1475"),sQuery(id+"F0.wireOp",EDGE,"E1476"),sQuery(id+"F0.wireOp",EDGE,"E1477"),sQuery(id+"F0.wireOp",EDGE,"E1478"),sQuery(id+"F0.wireOp",EDGE,"E1479"),sQuery(id+"F0.wireOp",EDGE,"E1480"),sQuery(id+"F0.wireOp",EDGE,"E1481"),sQuery(id+"F0.wireOp",EDGE,"E1482"),sQuery(id+"F0.wireOp",EDGE,"E1483"),sQuery(id+"F0.wireOp",EDGE,"E1484"),sQuery(id+"F0.wireOp",EDGE,"E1485"),sQuery(id+"F0.wireOp",EDGE,"E1486"),sQuery(id+"F0.wireOp",EDGE,"E1487"),sQuery(id+"F0.wireOp",EDGE,"E1488"),sQuery(id+"F0.wireOp",EDGE,"E1489"),sQuery(id+"F0.wireOp",EDGE,"E1490"),sQuery(id+"F0.wireOp",EDGE,"E1491"),sQuery(id+"F0.wireOp",EDGE,"E1492"),sQuery(id+"F0.wireOp",EDGE,"E1493"),sQuery(id+"F0.wireOp",EDGE,"E1494"),sQuery(id+"F0.wireOp",EDGE,"E1495"),sQuery(id+"F0.wireOp",EDGE,"E1496"),sQuery(id+"F0.wireOp",EDGE,"E1497"),sQuery(id+"F0.wireOp",EDGE,"E1498"),sQuery(id+"F0.wireOp",EDGE,"E1499"),sQuery(id+"F0.wireOp",EDGE,"E1500"),sQuery(id+"F0.wireOp",EDGE,"E1501"),sQuery(id+"F0.wireOp",EDGE,"E1502"),sQuery(id+"F0.wireOp",EDGE,"E1503"),sQuery(id+"F0.wireOp",EDGE,"E1504"),sQuery(id+"F0.wireOp",EDGE,"E1505"),sQuery(id+"F0.wireOp",EDGE,"E1506"),sQuery(id+"F0.wireOp",EDGE,"E1507"),sQuery(id+"F0.wireOp",EDGE,"E1508"),sQuery(id+"F0.wireOp",EDGE,"E1509"),sQuery(id+"F0.wireOp",EDGE,"E1510"),sQuery(id+"F0.wireOp",EDGE,"E1511"),sQuery(id+"F0.wireOp",EDGE,"E1512"),sQuery(id+"F0.wireOp",EDGE,"E1513"),sQuery(id+"F0.wireOp",EDGE,"E1514"),sQuery(id+"F0.wireOp",EDGE,"E1515"),sQuery(id+"F0.wireOp",EDGE,"E1516"),sQuery(id+"F0.wireOp",EDGE,"E1517"),sQuery(id+"F0.wireOp",EDGE,"E1518"),sQuery(id+"F0.wireOp",EDGE,"E1519"),sQuery(id+"F0.wireOp",EDGE,"E1520"),sQuery(id+"F0.wireOp",EDGE,"E1521"),sQuery(id+"F0.wireOp",EDGE,"E1522"),sQuery(id+"F0.wireOp",EDGE,"E1523"),sQuery(id+"F0.wireOp",EDGE,"E1524"),sQuery(id+"F0.wireOp",EDGE,"E1525"),sQuery(id+"F0.wireOp",EDGE,"E1526"),sQuery(id+"F0.wireOp",EDGE,"E1527"),sQuery(id+"F0.wireOp",EDGE,"E1528"),sQuery(id+"F0.wireOp",EDGE,"E1529"),sQuery(id+"F0.wireOp",EDGE,"E1530"),sQuery(id+"F0.wireOp",EDGE,"E1531"),sQuery(id+"F0.wireOp",EDGE,"E1532"),sQuery(id+"F0.wireOp",EDGE,"E1533"),sQuery(id+"F0.wireOp",EDGE,"E1534"),sQuery(id+"F0.wireOp",EDGE,"E1535"),sQuery(id+"F0.wireOp",EDGE,"E1536"),sQuery(id+"F0.wireOp",EDGE,"E1537"),sQuery(id+"F0.wireOp",EDGE,"E1538"),sQuery(id+"F0.wireOp",EDGE,"E1539"),sQuery(id+"F0.wireOp",EDGE,"E1540"),sQuery(id+"F0.wireOp",EDGE,"E1541"),sQuery(id+"F0.wireOp",EDGE,"E1542"),sQuery(id+"F0.wireOp",EDGE,"E1543"),sQuery(id+"F0.wireOp",EDGE,"E1544"),sQuery(id+"F0.wireOp",EDGE,"E1545"),sQuery(id+"F0.wireOp",EDGE,"E1546"),sQuery(id+"F0.wireOp",EDGE,"E1547"),sQuery(id+"F0.wireOp",EDGE,"E1548"),sQuery(id+"F0.wireOp",EDGE,"E1549"),sQuery(id+"F0.wireOp",EDGE,"E1550"),sQuery(id+"F0.wireOp",EDGE,"E1551"),sQuery(id+"F0.wireOp",EDGE,"E1552"),sQuery(id+"F0.wireOp",EDGE,"E1553"),sQuery(id+"F0.wireOp",EDGE,"E1554"),sQuery(id+"F0.wireOp",EDGE,"E1555"),sQuery(id+"F0.wireOp",EDGE,"E1556"),sQuery(id+"F0.wireOp",EDGE,"E1557"),sQuery(id+"F0.wireOp",EDGE,"E1558"),sQuery(id+"F0.wireOp",EDGE,"E1559"),sQuery(id+"F0.wireOp",EDGE,"E1560"),sQuery(id+"F0.wireOp",EDGE,"E1561"),sQuery(id+"F0.wireOp",EDGE,"E1562"),sQuery(id+"F0.wireOp",EDGE,"E1563"),sQuery(id+"F0.wireOp",EDGE,"E1564"),sQuery(id+"F0.wireOp",EDGE,"E1565"),sQuery(id+"F0.wireOp",EDGE,"E1566"),sQuery(id+"F0.wireOp",EDGE,"E1567"),sQuery(id+"F0.wireOp",EDGE,"E1568"),sQuery(id+"F0.wireOp",EDGE,"E1569"),sQuery(id+"F0.wireOp",EDGE,"E1570"),sQuery(id+"F0.wireOp",EDGE,"E1571"),sQuery(id+"F0.wireOp",EDGE,"E1572"),sQuery(id+"F0.wireOp",EDGE,"E1573"),sQuery(id+"F0.wireOp",EDGE,"E1574"),sQuery(id+"F0.wireOp",EDGE,"E1575"),sQuery(id+"F0.wireOp",EDGE,"E1576"),sQuery(id+"F0.wireOp",EDGE,"E1577"),sQuery(id+"F0.wireOp",EDGE,"E1578"),sQuery(id+"F0.wireOp",EDGE,"E1579"),sQuery(id+"F0.wireOp",EDGE,"E1580"),sQuery(id+"F0.wireOp",EDGE,"E1581"),sQuery(id+"F0.wireOp",EDGE,"E1582"),sQuery(id+"F0.wireOp",EDGE,"E1583"),sQuery(id+"F0.wireOp",EDGE,"E1584"),sQuery(id+"F0.wireOp",EDGE,"E1585"),sQuery(id+"F0.wireOp",EDGE,"E1586"),sQuery(id+"F0.wireOp",EDGE,"E1587"),sQuery(id+"F0.wireOp",EDGE,"E1588"),sQuery(id+"F0.wireOp",EDGE,"E1589"),sQuery(id+"F0.wireOp",EDGE,"E1590"),sQuery(id+"F0.wireOp",EDGE,"E1591"),sQuery(id+"F0.wireOp",EDGE,"E1592"),sQuery(id+"F0.wireOp",EDGE,"E1593"),sQuery(id+"F0.wireOp",EDGE,"E1594"),sQuery(id+"F0.wireOp",EDGE,"E1595"),sQuery(id+"F0.wireOp",EDGE,"E1596"),sQuery(id+"F0.wireOp",EDGE,"E1597"),sQuery(id+"F0.wireOp",EDGE,"E1598"),sQuery(id+"F0.wireOp",EDGE,"E1599"),sQuery(id+"F0.wireOp",EDGE,"E1600"),sQuery(id+"F0.wireOp",EDGE,"E1601"),sQuery(id+"F0.wireOp",EDGE,"E1602"),sQuery(id+"F0.wireOp",EDGE,"E1603"),sQuery(id+"F0.wireOp",EDGE,"E1604"),sQuery(id+"F0.wireOp",EDGE,"E1605"),sQuery(id+"F0.wireOp",EDGE,"E1606"),sQuery(id+"F0.wireOp",EDGE,"E1607"),sQuery(id+"F0.wireOp",EDGE,"E1608"),sQuery(id+"F0.wireOp",EDGE,"E1609"),sQuery(id+"F0.wireOp",EDGE,"E1610"),sQuery(id+"F0.wireOp",EDGE,"E1611"),sQuery(id+"F0.wireOp",EDGE,"E1612"),sQuery(id+"F0.wireOp",EDGE,"E1613"),sQuery(id+"F0.wireOp",EDGE,"E1614"),sQuery(id+"F0.wireOp",EDGE,"E1615"),sQuery(id+"F0.wireOp",EDGE,"E1616"),sQuery(id+"F0.wireOp",EDGE,"E1617"),sQuery(id+"F0.wireOp",EDGE,"E1618"),sQuery(id+"F0.wireOp",EDGE,"E1619"),sQuery(id+"F0.wireOp",EDGE,"E1620"),sQuery(id+"F0.wireOp",EDGE,"E1621"),sQuery(id+"F0.wireOp",EDGE,"E1622"),sQuery(id+"F0.wireOp",EDGE,"E1623"),sQuery(id+"F0.wireOp",EDGE,"E1624"),sQuery(id+"F0.wireOp",EDGE,"E1625"),sQuery(id+"F0.wireOp",EDGE,"E1626"),sQuery(id+"F0.wireOp",EDGE,"E1627"),sQuery(id+"F0.wireOp",EDGE,"E1628"),sQuery(id+"F0.wireOp",EDGE,"E1629"),sQuery(id+"F0.wireOp",EDGE,"E1630"),sQuery(id+"F0.wireOp",EDGE,"E1631"),sQuery(id+"F0.wireOp",EDGE,"E1632"),sQuery(id+"F0.wireOp",EDGE,"E1633"),sQuery(id+"F0.wireOp",EDGE,"E1634"),sQuery(id+"F0.wireOp",EDGE,"E1635"),sQuery(id+"F0.wireOp",EDGE,"E1636"),sQuery(id+"F0.wireOp",EDGE,"E1637"),sQuery(id+"F0.wireOp",EDGE,"E1638"),sQuery(id+"F0.wireOp",EDGE,"E1639"),sQuery(id+"F0.wireOp",EDGE,"E1640"),sQuery(id+"F0.wireOp",EDGE,"E1641"),sQuery(id+"F0.wireOp",EDGE,"E1642"),sQuery(id+"F0.wireOp",EDGE,"E1643"),sQuery(id+"F0.wireOp",EDGE,"E1644"),sQuery(id+"F0.wireOp",EDGE,"E1645"),sQuery(id+"F0.wireOp",EDGE,"E1646"),sQuery(id+"F0.wireOp",EDGE,"E1647"),sQuery(id+"F0.wireOp",EDGE,"E1648"),sQuery(id+"F0.wireOp",EDGE,"E1649"),sQuery(id+"F0.wireOp",EDGE,"E1650"),sQuery(id+"F0.wireOp",EDGE,"E1651"),sQuery(id+"F0.wireOp",EDGE,"E1652"),sQuery(id+"F0.wireOp",EDGE,"E1653"),sQuery(id+"F0.wireOp",EDGE,"E1654"),sQuery(id+"F0.wireOp",EDGE,"E1655"),sQuery(id+"F0.wireOp",EDGE,"E1656"),sQuery(id+"F0.wireOp",EDGE,"E1657"),sQuery(id+"F0.wireOp",EDGE,"E1658"),sQuery(id+"F0.wireOp",EDGE,"E1659"),sQuery(id+"F0.wireOp",EDGE,"E1660"),sQuery(id+"F0.wireOp",EDGE,"E1661"),sQuery(id+"F0.wireOp",EDGE,"E1662"),sQuery(id+"F0.wireOp",EDGE,"E1663"),sQuery(id+"F0.wireOp",EDGE,"E1664"),sQuery(id+"F0.wireOp",EDGE,"E1665"),sQuery(id+"F0.wireOp",EDGE,"E1666"),sQuery(id+"F0.wireOp",EDGE,"E1667"),sQuery(id+"F0.wireOp",EDGE,"E1668"),sQuery(id+"F0.wireOp",EDGE,"E1669"),sQuery(id+"F0.wireOp",EDGE,"E1670"),sQuery(id+"F0.wireOp",EDGE,"E1671"),sQuery(id+"F0.wireOp",EDGE,"E1672"),sQuery(id+"F0.wireOp",EDGE,"E1673"),sQuery(id+"F0.wireOp",EDGE,"E1674"),sQuery(id+"F0.wireOp",EDGE,"E1675"),sQuery(id+"F0.wireOp",EDGE,"E1676"),sQuery(id+"F0.wireOp",EDGE,"E1677"),sQuery(id+"F0.wireOp",EDGE,"E1678"),sQuery(id+"F0.wireOp",EDGE,"E1679"),sQuery(id+"F0.wireOp",EDGE,"E1680"),sQuery(id+"F0.wireOp",EDGE,"E1681"),sQuery(id+"F0.wireOp",EDGE,"E1682"),sQuery(id+"F0.wireOp",EDGE,"E1683"),sQuery(id+"F0.wireOp",EDGE,"E1684"),sQuery(id+"F0.wireOp",EDGE,"E1685"),sQuery(id+"F0.wireOp",EDGE,"E1686"),sQuery(id+"F0.wireOp",EDGE,"E1687"),sQuery(id+"F0.wireOp",EDGE,"E1688"),sQuery(id+"F0.wireOp",EDGE,"E1689"),sQuery(id+"F0.wireOp",EDGE,"E1690"),sQuery(id+"F0.wireOp",EDGE,"E1691"),sQuery(id+"F0.wireOp",EDGE,"E1692"),sQuery(id+"F0.wireOp",EDGE,"E1693"),sQuery(id+"F0.wireOp",EDGE,"E1694"),sQuery(id+"F0.wireOp",EDGE,"E1695"),sQuery(id+"F0.wireOp",EDGE,"E1696"),sQuery(id+"F0.wireOp",EDGE,"E1697"),sQuery(id+"F0.wireOp",EDGE,"E1698"),sQuery(id+"F0.wireOp",EDGE,"E1699"),sQuery(id+"F0.wireOp",EDGE,"E1700"),sQuery(id+"F0.wireOp",EDGE,"E1701"),sQuery(id+"F0.wireOp",EDGE,"E1702"),sQuery(id+"F0.wireOp",EDGE,"E1703"),sQuery(id+"F0.wireOp",EDGE,"E1704"),sQuery(id+"F0.wireOp",EDGE,"E1705"),sQuery(id+"F0.wireOp",EDGE,"E1706"),sQuery(id+"F0.wireOp",EDGE,"E1707"),sQuery(id+"F0.wireOp",EDGE,"E1708"),sQuery(id+"F0.wireOp",EDGE,"E1709"),sQuery(id+"F0.wireOp",EDGE,"E1710"),sQuery(id+"F0.wireOp",EDGE,"E1711"),sQuery(id+"F0.wireOp",EDGE,"E1712"),sQuery(id+"F0.wireOp",EDGE,"E1713"),sQuery(id+"F0.wireOp",EDGE,"E1714"),sQuery(id+"F0.wireOp",EDGE,"E1715"),sQuery(id+"F0.wireOp",EDGE,"E1716"),sQuery(id+"F0.wireOp",EDGE,"E1717"),sQuery(id+"F0.wireOp",EDGE,"E1718"),sQuery(id+"F0.wireOp",EDGE,"E1719"),sQuery(id+"F0.wireOp",EDGE,"E1720"),sQuery(id+"F0.wireOp",EDGE,"E1721"),sQuery(id+"F0.wireOp",EDGE,"E1722"),sQuery(id+"F0.wireOp",EDGE,"E1723"),sQuery(id+"F0.wireOp",EDGE,"E1724"),sQuery(id+"F0.wireOp",EDGE,"E1725"),sQuery(id+"F0.wireOp",EDGE,"E1726"),sQuery(id+"F0.wireOp",EDGE,"E1727"),sQuery(id+"F0.wireOp",EDGE,"E1728"),sQuery(id+"F0.wireOp",EDGE,"E1729"),sQuery(id+"F0.wireOp",EDGE,"E1730"),sQuery(id+"F0.wireOp",EDGE,"E1731"),sQuery(id+"F0.wireOp",EDGE,"E1732"),sQuery(id+"F0.wireOp",EDGE,"E1733"),sQuery(id+"F0.wireOp",EDGE,"E1734"),sQuery(id+"F0.wireOp",EDGE,"E1735"),sQuery(id+"F0.wireOp",EDGE,"E1736"),sQuery(id+"F0.wireOp",EDGE,"E1737"),sQuery(id+"F0.wireOp",EDGE,"E1738"),sQuery(id+"F0.wireOp",EDGE,"E1739"),sQuery(id+"F0.wireOp",EDGE,"E1740"),sQuery(id+"F0.wireOp",EDGE,"E1741"),sQuery(id+"F0.wireOp",EDGE,"E1742"),sQuery(id+"F0.wireOp",EDGE,"E1743"),sQuery(id+"F0.wireOp",EDGE,"E1744"),sQuery(id+"F0.wireOp",EDGE,"E1745"),sQuery(id+"F0.wireOp",EDGE,"E1746"),sQuery(id+"F0.wireOp",EDGE,"E1747"),sQuery(id+"F0.wireOp",EDGE,"E1748"),sQuery(id+"F0.wireOp",EDGE,"E1749"),sQuery(id+"F0.wireOp",EDGE,"E1750"),sQuery(id+"F0.wireOp",EDGE,"E1751"),sQuery(id+"F0.wireOp",EDGE,"E1752"),sQuery(id+"F0.wireOp",EDGE,"E1753"),sQuery(id+"F0.wireOp",EDGE,"E1754"),sQuery(id+"F0.wireOp",EDGE,"E1755"),sQuery(id+"F0.wireOp",EDGE,"E1756"),sQuery(id+"F0.wireOp",EDGE,"E1757"),sQuery(id+"F0.wireOp",EDGE,"E1758"),sQuery(id+"F0.wireOp",EDGE,"E1759"),sQuery(id+"F0.wireOp",EDGE,"E1760"),sQuery(id+"F0.wireOp",EDGE,"E1761"),sQuery(id+"F0.wireOp",EDGE,"E1762"),sQuery(id+"F0.wireOp",EDGE,"E1763"),sQuery(id+"F0.wireOp",EDGE,"E1764"),sQuery(id+"F0.wireOp",EDGE,"E1765"),sQuery(id+"F0.wireOp",EDGE,"E1766"),sQuery(id+"F0.wireOp",EDGE,"E1767"),sQuery(id+"F0.wireOp",EDGE,"E1768"),sQuery(id+"F0.wireOp",EDGE,"E1769"),sQuery(id+"F0.wireOp",EDGE,"E1770"),sQuery(id+"F0.wireOp",EDGE,"E1771"),sQuery(id+"F0.wireOp",EDGE,"E1772"),sQuery(id+"F0.wireOp",EDGE,"E1773"),sQuery(id+"F0.wireOp",EDGE,"E1774"),sQuery(id+"F0.wireOp",EDGE,"E1775"),sQuery(id+"F0.wireOp",EDGE,"E1776"),sQuery(id+"F0.wireOp",EDGE,"E1777"),sQuery(id+"F0.wireOp",EDGE,"E1778"),sQuery(id+"F0.wireOp",EDGE,"E1779"),sQuery(id+"F0.wireOp",EDGE,"E1780"),sQuery(id+"F0.wireOp",EDGE,"E1781"),sQuery(id+"F0.wireOp",EDGE,"E1782"),sQuery(id+"F0.wireOp",EDGE,"E1783"),sQuery(id+"F0.wireOp",EDGE,"E1784"),sQuery(id+"F0.wireOp",EDGE,"E1785"),sQuery(id+"F0.wireOp",EDGE,"E1786"),sQuery(id+"F0.wireOp",EDGE,"E1787"),sQuery(id+"F0.wireOp",EDGE,"E1788"),sQuery(id+"F0.wireOp",EDGE,"E1789"),sQuery(id+"F0.wireOp",EDGE,"E1790"),sQuery(id+"F0.wireOp",EDGE,"E1791"),sQuery(id+"F0.wireOp",EDGE,"E1792"),sQuery(id+"F0.wireOp",EDGE,"E1793"),sQuery(id+"F0.wireOp",EDGE,"E1794"),sQuery(id+"F0.wireOp",EDGE,"E1795"),sQuery(id+"F0.wireOp",EDGE,"E1796"),sQuery(id+"F0.wireOp",EDGE,"E1797"),sQuery(id+"F0.wireOp",EDGE,"E1798"),sQuery(id+"F0.wireOp",EDGE,"E1799"),sQuery(id+"F0.wireOp",EDGE,"E1800"),sQuery(id+"F0.wireOp",EDGE,"E1801"),sQuery(id+"F0.wireOp",EDGE,"E1802"),sQuery(id+"F0.wireOp",EDGE,"E1803"),sQuery(id+"F0.wireOp",EDGE,"E1804"),sQuery(id+"F0.wireOp",EDGE,"E1805"),sQuery(id+"F0.wireOp",EDGE,"E1806"),sQuery(id+"F0.wireOp",EDGE,"E1807"),sQuery(id+"F0.wireOp",EDGE,"E1808"),sQuery(id+"F0.wireOp",EDGE,"E1809"),sQuery(id+"F0.wireOp",EDGE,"E1810"),sQuery(id+"F0.wireOp",EDGE,"E1811"),sQuery(id+"F0.wireOp",EDGE,"E1812"),sQuery(id+"F0.wireOp",EDGE,"E1813"),sQuery(id+"F0.wireOp",EDGE,"E1814"),sQuery(id+"F0.wireOp",EDGE,"E1815"),sQuery(id+"F0.wireOp",EDGE,"E1816"),sQuery(id+"F0.wireOp",EDGE,"E1817"),sQuery(id+"F0.wireOp",EDGE,"E1818"),sQuery(id+"F0.wireOp",EDGE,"E1819"),sQuery(id+"F0.wireOp",EDGE,"E1820"),sQuery(id+"F0.wireOp",EDGE,"E1821"),sQuery(id+"F0.wireOp",EDGE,"E1822"),sQuery(id+"F0.wireOp",EDGE,"E1823"),sQuery(id+"F0.wireOp",EDGE,"E1824"),sQuery(id+"F0.wireOp",EDGE,"E1825"),sQuery(id+"F0.wireOp",EDGE,"E1826"),sQuery(id+"F0.wireOp",EDGE,"E1827"),sQuery(id+"F0.wireOp",EDGE,"E1828"),sQuery(id+"F0.wireOp",EDGE,"E1829"),sQuery(id+"F0.wireOp",EDGE,"E1830"),sQuery(id+"F0.wireOp",EDGE,"E1831"),sQuery(id+"F0.wireOp",EDGE,"E1832"),sQuery(id+"F0.wireOp",EDGE,"E1833"),sQuery(id+"F0.wireOp",EDGE,"E1834"),sQuery(id+"F0.wireOp",EDGE,"E1835"),sQuery(id+"F0.wireOp",EDGE,"E1836"),sQuery(id+"F0.wireOp",EDGE,"E1837"),sQuery(id+"F0.wireOp",EDGE,"E1838"),sQuery(id+"F0.wireOp",EDGE,"E1839"),sQuery(id+"F0.wireOp",EDGE,"E1840"),sQuery(id+"F0.wireOp",EDGE,"E1841"),sQuery(id+"F0.wireOp",EDGE,"E1842"),sQuery(id+"F0.wireOp",EDGE,"E1843"),sQuery(id+"F0.wireOp",EDGE,"E1844"),sQuery(id+"F0.wireOp",EDGE,"E1845"),sQuery(id+"F0.wireOp",EDGE,"E1846"),sQuery(id+"F0.wireOp",EDGE,"E1847"),sQuery(id+"F0.wireOp",EDGE,"E1848"),sQuery(id+"F0.wireOp",EDGE,"E1849"),sQuery(id+"F0.wireOp",EDGE,"E1850"),sQuery(id+"F0.wireOp",EDGE,"E1851"),sQuery(id+"F0.wireOp",EDGE,"E1852"),sQuery(id+"F0.wireOp",EDGE,"E1853"),sQuery(id+"F0.wireOp",EDGE,"E1854"),sQuery(id+"F0.wireOp",EDGE,"E1855"),sQuery(id+"F0.wireOp",EDGE,"E1856"),sQuery(id+"F0.wireOp",EDGE,"E1857"),sQuery(id+"F0.wireOp",EDGE,"E1858"),sQuery(id+"F0.wireOp",EDGE,"E1859"),sQuery(id+"F0.wireOp",EDGE,"E1860"),sQuery(id+"F0.wireOp",EDGE,"E1861"),sQuery(id+"F0.wireOp",EDGE,"E1862"),sQuery(id+"F0.wireOp",EDGE,"E1863"),sQuery(id+"F0.wireOp",EDGE,"E1864"),sQuery(id+"F0.wireOp",EDGE,"E1865"),sQuery(id+"F0.wireOp",EDGE,"E1866"),sQuery(id+"F0.wireOp",EDGE,"E1867"),sQuery(id+"F0.wireOp",EDGE,"E1868"),sQuery(id+"F0.wireOp",EDGE,"E1869"),sQuery(id+"F0.wireOp",EDGE,"E1870"),sQuery(id+"F0.wireOp",EDGE,"E1871"),sQuery(id+"F0.wireOp",EDGE,"E1872"),sQuery(id+"F0.wireOp",EDGE,"E1873"),sQuery(id+"F0.wireOp",EDGE,"E1874"),sQuery(id+"F0.wireOp",EDGE,"E1875"),sQuery(id+"F0.wireOp",EDGE,"E1876"),sQuery(id+"F0.wireOp",EDGE,"E1877"),sQuery(id+"F0.wireOp",EDGE,"E1878"),sQuery(id+"F0.wireOp",EDGE,"E1879"),sQuery(id+"F0.wireOp",EDGE,"E1880"),sQuery(id+"F0.wireOp",EDGE,"E1881"),sQuery(id+"F0.wireOp",EDGE,"E1882"),sQuery(id+"F0.wireOp",EDGE,"E1883"),sQuery(id+"F0.wireOp",EDGE,"E1884"),sQuery(id+"F0.wireOp",EDGE,"E1885"),sQuery(id+"F0.wireOp",EDGE,"E1886"),sQuery(id+"F0.wireOp",EDGE,"E1887"),sQuery(id+"F0.wireOp",EDGE,"E1888"),sQuery(id+"F0.wireOp",EDGE,"E1889"),sQuery(id+"F0.wireOp",EDGE,"E1890"),sQuery(id+"F0.wireOp",EDGE,"E1891"),sQuery(id+"F0.wireOp",EDGE,"E1892"),sQuery(id+"F0.wireOp",EDGE,"E1893"),sQuery(id+"F0.wireOp",EDGE,"E1894"),sQuery(id+"F0.wireOp",EDGE,"E1895"),sQuery(id+"F0.wireOp",EDGE,"E1896"),sQuery(id+"F0.wireOp",EDGE,"E1897"),sQuery(id+"F0.wireOp",EDGE,"E1898"),sQuery(id+"F0.wireOp",EDGE,"E1899"),sQuery(id+"F0.wireOp",EDGE,"E1900"),sQuery(id+"F0.wireOp",EDGE,"E1901"),sQuery(id+"F0.wireOp",EDGE,"E1902"),sQuery(id+"F0.wireOp",EDGE,"E1903"),sQuery(id+"F0.wireOp",EDGE,"E1904"),sQuery(id+"F0.wireOp",EDGE,"E1905"),sQuery(id+"F0.wireOp",EDGE,"E1906"),sQuery(id+"F0.wireOp",EDGE,"E1907"),sQuery(id+"F0.wireOp",EDGE,"E1908"),sQuery(id+"F0.wireOp",EDGE,"E1909"),sQuery(id+"F0.wireOp",EDGE,"E1910"),sQuery(id+"F0.wireOp",EDGE,"E1911"),sQuery(id+"F0.wireOp",EDGE,"E1912"),sQuery(id+"F0.wireOp",EDGE,"E1913"),sQuery(id+"F0.wireOp",EDGE,"E1914"),sQuery(id+"F0.wireOp",EDGE,"E1915"),sQuery(id+"F0.wireOp",EDGE,"E1916"),sQuery(id+"F0.wireOp",EDGE,"E1917"),sQuery(id+"F0.wireOp",EDGE,"E1918"),sQuery(id+"F0.wireOp",EDGE,"E1919"),sQuery(id+"F0.wireOp",EDGE,"E1920"),sQuery(id+"F0.wireOp",EDGE,"E1921"),sQuery(id+"F0.wireOp",EDGE,"E1922"),sQuery(id+"F0.wireOp",EDGE,"E1923"),sQuery(id+"F0.wireOp",EDGE,"E1924"),sQuery(id+"F0.wireOp",EDGE,"E1925"),sQuery(id+"F0.wireOp",EDGE,"E1926"),sQuery(id+"F0.wireOp",EDGE,"E1927"),sQuery(id+"F0.wireOp",EDGE,"E1928"),sQuery(id+"F0.wireOp",EDGE,"E1929"),sQuery(id+"F0.wireOp",EDGE,"E1930"),sQuery(id+"F0.wireOp",EDGE,"E1931"),sQuery(id+"F0.wireOp",EDGE,"E1932"),sQuery(id+"F0.wireOp",EDGE,"E1933"),sQuery(id+"F0.wireOp",EDGE,"E1934"),sQuery(id+"F0.wireOp",EDGE,"E1935"),sQuery(id+"F0.wireOp",EDGE,"E1936"),sQuery(id+"F0.wireOp",EDGE,"E1937"),sQuery(id+"F0.wireOp",EDGE,"E1938"),sQuery(id+"F0.wireOp",EDGE,"E1939"),sQuery(id+"F0.wireOp",EDGE,"E1940"),sQuery(id+"F0.wireOp",EDGE,"E1941"),sQuery(id+"F0.wireOp",EDGE,"E1942"),sQuery(id+"F0.wireOp",EDGE,"E1943"),sQuery(id+"F0.wireOp",EDGE,"E1944"),sQuery(id+"F0.wireOp",EDGE,"E1945"),sQuery(id+"F0.wireOp",EDGE,"E1946"),sQuery(id+"F0.wireOp",EDGE,"E1947"),sQuery(id+"F0.wireOp",EDGE,"E1948"),sQuery(id+"F0.wireOp",EDGE,"E1949"),sQuery(id+"F0.wireOp",EDGE,"E1950"),sQuery(id+"F0.wireOp",EDGE,"E1951"),sQuery(id+"F0.wireOp",EDGE,"E1952"),sQuery(id+"F0.wireOp",EDGE,"E1953"),sQuery(id+"F0.wireOp",EDGE,"E1954"),sQuery(id+"F0.wireOp",EDGE,"E1955"),sQuery(id+"F0.wireOp",EDGE,"E1956"),sQuery(id+"F0.wireOp",EDGE,"E1957"),sQuery(id+"F0.wireOp",EDGE,"E1958"),sQuery(id+"F0.wireOp",EDGE,"E1959"),sQuery(id+"F0.wireOp",EDGE,"E1960"),sQuery(id+"F0.wireOp",EDGE,"E1961"),sQuery(id+"F0.wireOp",EDGE,"E1962"),sQuery(id+"F0.wireOp",EDGE,"E1963"),sQuery(id+"F0.wireOp",EDGE,"E1964"),sQuery(id+"F0.wireOp",EDGE,"E1965"),sQuery(id+"F0.wireOp",EDGE,"E1966"),sQuery(id+"F0.wireOp",EDGE,"E1967"),sQuery(id+"F0.wireOp",EDGE,"E1968"),sQuery(id+"F0.wireOp",EDGE,"E1969"),sQuery(id+"F0.wireOp",EDGE,"E1970"),sQuery(id+"F0.wireOp",EDGE,"E1971"),sQuery(id+"F0.wireOp",EDGE,"E1972"),sQuery(id+"F0.wireOp",EDGE,"E1973"),sQuery(id+"F0.wireOp",EDGE,"E1974"),sQuery(id+"F0.wireOp",EDGE,"E1975"),sQuery(id+"F0.wireOp",EDGE,"E1976"),sQuery(id+"F0.wireOp",EDGE,"E1977"),sQuery(id+"F0.wireOp",EDGE,"E1978"),sQuery(id+"F0.wireOp",EDGE,"E1979"),sQuery(id+"F0.wireOp",EDGE,"E1980"),sQuery(id+"F0.wireOp",EDGE,"E1981"),sQuery(id+"F0.wireOp",EDGE,"E1982"),sQuery(id+"F0.wireOp",EDGE,"E1983"),sQuery(id+"F0.wireOp",EDGE,"E1984"),sQuery(id+"F0.wireOp",EDGE,"E1985"),sQuery(id+"F0.wireOp",EDGE,"E1986"),sQuery(id+"F0.wireOp",EDGE,"E1987"),sQuery(id+"F0.wireOp",EDGE,"E1988"),sQuery(id+"F0.wireOp",EDGE,"E1989"),sQuery(id+"F0.wireOp",EDGE,"E1990"),sQuery(id+"F0.wireOp",EDGE,"E1991"),sQuery(id+"F0.wireOp",EDGE,"E1992"),sQuery(id+"F0.wireOp",EDGE,"E1993"),sQuery(id+"F0.wireOp",EDGE,"E1994"),sQuery(id+"F0.wireOp",EDGE,"E1995"),sQuery(id+"F0.wireOp",EDGE,"E1996"),sQuery(id+"F0.wireOp",EDGE,"E1997"),sQuery(id+"F0.wireOp",EDGE,"E1998"),sQuery(id+"F0.wireOp",EDGE,"E1999"),sQuery(id+"F0.wireOp",EDGE,"E2000"),sQuery(id+"F0.wireOp",EDGE,"E2001"),sQuery(id+"F0.wireOp",EDGE,"E2002"),sQuery(id+"F0.wireOp",EDGE,"E2003"),sQuery(id+"F0.wireOp",EDGE,"E2004"),sQuery(id+"F0.wireOp",EDGE,"E2005"),sQuery(id+"F0.wireOp",EDGE,"E2006"),sQuery(id+"F0.wireOp",EDGE,"E2007"),sQuery(id+"F0.wireOp",EDGE,"E2008"),sQuery(id+"F0.wireOp",EDGE,"E2009"),sQuery(id+"F0.wireOp",EDGE,"E2010"),sQuery(id+"F0.wireOp",EDGE,"E2011"),sQuery(id+"F0.wireOp",EDGE,"E2012"),sQuery(id+"F0.wireOp",EDGE,"E2013"),sQuery(id+"F0.wireOp",EDGE,"E2014"),sQuery(id+"F0.wireOp",EDGE,"E2015"),sQuery(id+"F0.wireOp",EDGE,"E2016"),sQuery(id+"F0.wireOp",EDGE,"E2017"),sQuery(id+"F0.wireOp",EDGE,"E2018"),sQuery(id+"F0.wireOp",EDGE,"E2019"),sQuery(id+"F0.wireOp",EDGE,"E2020"),sQuery(id+"F0.wireOp",EDGE,"E2021"),sQuery(id+"F0.wireOp",EDGE,"E2022"),sQuery(id+"F0.wireOp",EDGE,"E2023"),sQuery(id+"F0.wireOp",EDGE,"E2024"),sQuery(id+"F0.wireOp",EDGE,"E2025"),sQuery(id+"F0.wireOp",EDGE,"E2026"),sQuery(id+"F0.wireOp",EDGE,"E2027"),sQuery(id+"F0.wireOp",EDGE,"E2028"),sQuery(id+"F0.wireOp",EDGE,"E2029"),sQuery(id+"F0.wireOp",EDGE,"E2030"),sQuery(id+"F0.wireOp",EDGE,"E2031"),sQuery(id+"F0.wireOp",EDGE,"E2032"),sQuery(id+"F0.wireOp",EDGE,"E2033"),sQuery(id+"F0.wireOp",EDGE,"E2034"),sQuery(id+"F0.wireOp",EDGE,"E2035"),sQuery(id+"F0.wireOp",EDGE,"E2036"),sQuery(id+"F0.wireOp",EDGE,"E2037"),sQuery(id+"F0.wireOp",EDGE,"E2038"),sQuery(id+"F0.wireOp",EDGE,"E2039"),sQuery(id+"F0.wireOp",EDGE,"E2040"),sQuery(id+"F0.wireOp",EDGE,"E2041"),sQuery(id+"F0.wireOp",EDGE,"E2042"),sQuery(id+"F0.wireOp",EDGE,"E2043"),sQuery(id+"F0.wireOp",EDGE,"E2044"),sQuery(id+"F0.wireOp",EDGE,"E2045"),sQuery(id+"F0.wireOp",EDGE,"E2046"),sQuery(id+"F0.wireOp",EDGE,"E2047"),sQuery(id+"F0.wireOp",EDGE,"E2048"),sQuery(id+"F0.wireOp",EDGE,"E2049"),sQuery(id+"F0.wireOp",EDGE,"E2050"),sQuery(id+"F0.wireOp",EDGE,"E2051"),sQuery(id+"F0.wireOp",EDGE,"E2052"),sQuery(id+"F0.wireOp",EDGE,"E2053"),sQuery(id+"F0.wireOp",EDGE,"E2054"),sQuery(id+"F0.wireOp",EDGE,"E2055"),sQuery(id+"F0.wireOp",EDGE,"E2056"),sQuery(id+"F0.wireOp",EDGE,"E2057"),sQuery(id+"F0.wireOp",EDGE,"E2058"),sQuery(id+"F0.wireOp",EDGE,"E2059"),sQuery(id+"F0.wireOp",EDGE,"E2060"),sQuery(id+"F0.wireOp",EDGE,"E2061"),sQuery(id+"F0.wireOp",EDGE,"E2062"),sQuery(id+"F0.wireOp",EDGE,"E2063"),sQuery(id+"F0.wireOp",EDGE,"E2064"),sQuery(id+"F0.wireOp",EDGE,"E2065"),sQuery(id+"F0.wireOp",EDGE,"E2066"),sQuery(id+"F0.wireOp",EDGE,"E2067"),sQuery(id+"F0.wireOp",EDGE,"E2068"),sQuery(id+"F0.wireOp",EDGE,"E2069"),sQuery(id+"F0.wireOp",EDGE,"E2070"),sQuery(id+"F0.wireOp",EDGE,"E2071"),sQuery(id+"F0.wireOp",EDGE,"E2072"),sQuery(id+"F0.wireOp",EDGE,"E2073"),sQuery(id+"F0.wireOp",EDGE,"E2074"),sQuery(id+"F0.wireOp",EDGE,"E2075"),sQuery(id+"F0.wireOp",EDGE,"E2076"),sQuery(id+"F0.wireOp",EDGE,"E2077"),sQuery(id+"F0.wireOp",EDGE,"E2078"),sQuery(id+"F0.wireOp",EDGE,"E2079"),sQuery(id+"F0.wireOp",EDGE,"E2080"),sQuery(id+"F0.wireOp",EDGE,"E2081"),sQuery(id+"F0.wireOp",EDGE,"E2082"),sQuery(id+"F0.wireOp",EDGE,"E2083"),sQuery(id+"F0.wireOp",EDGE,"E2084"),sQuery(id+"F0.wireOp",EDGE,"E2085"),sQuery(id+"F0.wireOp",EDGE,"E2086"),sQuery(id+"F0.wireOp",EDGE,"E2087"),sQuery(id+"F0.wireOp",EDGE,"E2088"),sQuery(id+"F0.wireOp",EDGE,"E2089"),sQuery(id+"F0.wireOp",EDGE,"E2090"),sQuery(id+"F0.wireOp",EDGE,"E2091"),sQuery(id+"F0.wireOp",EDGE,"E2092"),sQuery(id+"F0.wireOp",EDGE,"E2093"),sQuery(id+"F0.wireOp",EDGE,"E2094"),sQuery(id+"F0.wireOp",EDGE,"E2095"),sQuery(id+"F0.wireOp",EDGE,"E2096"),sQuery(id+"F0.wireOp",EDGE,"E2097"),sQuery(id+"F0.wireOp",EDGE,"E2098"),sQuery(id+"F0.wireOp",EDGE,"E2099"),sQuery(id+"F0.wireOp",EDGE,"E2100"),sQuery(id+"F0.wireOp",EDGE,"E2101"),sQuery(id+"F0.wireOp",EDGE,"E2102"),sQuery(id+"F0.wireOp",EDGE,"E2103"),sQuery(id+"F0.wireOp",EDGE,"E2104"),sQuery(id+"F0.wireOp",EDGE,"E2105"),sQuery(id+"F0.wireOp",EDGE,"E2106"),sQuery(id+"F0.wireOp",EDGE,"E2107"),sQuery(id+"F0.wireOp",EDGE,"E2108"),sQuery(id+"F0.wireOp",EDGE,"E2109"),sQuery(id+"F0.wireOp",EDGE,"E2110"),sQuery(id+"F0.wireOp",EDGE,"E2111"),sQuery(id+"F0.wireOp",EDGE,"E2112"),sQuery(id+"F0.wireOp",EDGE,"E2113"),sQuery(id+"F0.wireOp",EDGE,"E2114"),sQuery(id+"F0.wireOp",EDGE,"E2115"),sQuery(id+"F0.wireOp",EDGE,"E2116"),sQuery(id+"F0.wireOp",EDGE,"E2117"),sQuery(id+"F0.wireOp",EDGE,"E2118"),sQuery(id+"F0.wireOp",EDGE,"E2119"),sQuery(id+"F0.wireOp",EDGE,"E2120"),sQuery(id+"F0.wireOp",EDGE,"E2121"),sQuery(id+"F0.wireOp",EDGE,"E2122"),sQuery(id+"F0.wireOp",EDGE,"E2123"),sQuery(id+"F0.wireOp",EDGE,"E2124"),sQuery(id+"F0.wireOp",EDGE,"E2125"),sQuery(id+"F0.wireOp",EDGE,"E2126"),sQuery(id+"F0.wireOp",EDGE,"E2127"),sQuery(id+"F0.wireOp",EDGE,"E2128"),sQuery(id+"F0.wireOp",EDGE,"E2129"),sQuery(id+"F0.wireOp",EDGE,"E2130"),sQuery(id+"F0.wireOp",EDGE,"E2131"),sQuery(id+"F0.wireOp",EDGE,"E2132"),sQuery(id+"F0.wireOp",EDGE,"E2133"),sQuery(id+"F0.wireOp",EDGE,"E2134"),sQuery(id+"F0.wireOp",EDGE,"E2135"),sQuery(id+"F0.wireOp",EDGE,"E2136"),sQuery(id+"F0.wireOp",EDGE,"E2137"),sQuery(id+"F0.wireOp",EDGE,"E2138"),sQuery(id+"F0.wireOp",EDGE,"E2139"),sQuery(id+"F0.wireOp",EDGE,"E2140"),sQuery(id+"F0.wireOp",EDGE,"E2141"),sQuery(id+"F0.wireOp",EDGE,"E2142"),sQuery(id+"F0.wireOp",EDGE,"E2143"),sQuery(id+"F0.wireOp",EDGE,"E2144"),sQuery(id+"F0.wireOp",EDGE,"E2145"),sQuery(id+"F0.wireOp",EDGE,"E2146"),sQuery(id+"F0.wireOp",EDGE,"E2147"),sQuery(id+"F0.wireOp",EDGE,"E2148"),sQuery(id+"F0.wireOp",EDGE,"E2149"),sQuery(id+"F0.wireOp",EDGE,"E2150"),sQuery(id+"F0.wireOp",EDGE,"E2151"),sQuery(id+"F0.wireOp",EDGE,"E2152"),sQuery(id+"F0.wireOp",EDGE,"E2153"),sQuery(id+"F0.wireOp",EDGE,"E2154"),sQuery(id+"F0.wireOp",EDGE,"E2155"),sQuery(id+"F0.wireOp",EDGE,"E2156"),sQuery(id+"F0.wireOp",EDGE,"E2157"),sQuery(id+"F0.wireOp",EDGE,"E2158"),sQuery(id+"F0.wireOp",EDGE,"E2159"),sQuery(id+"F0.wireOp",EDGE,"E2160"),sQuery(id+"F0.wireOp",EDGE,"E2161"),sQuery(id+"F0.wireOp",EDGE,"E2162"),sQuery(id+"F0.wireOp",EDGE,"E2163"),sQuery(id+"F0.wireOp",EDGE,"E2164"),sQuery(id+"F0.wireOp",EDGE,"E2165"),sQuery(id+"F0.wireOp",EDGE,"E2166"),sQuery(id+"F0.wireOp",EDGE,"E2167"),sQuery(id+"F0.wireOp",EDGE,"E2168"),sQuery(id+"F0.wireOp",EDGE,"E2169"),sQuery(id+"F0.wireOp",EDGE,"E2170"),sQuery(id+"F0.wireOp",EDGE,"E2171"),sQuery(id+"F0.wireOp",EDGE,"E2172"),sQuery(id+"F0.wireOp",EDGE,"E2173"),sQuery(id+"F0.wireOp",EDGE,"E2174"),sQuery(id+"F0.wireOp",EDGE,"E2175"),sQuery(id+"F0.wireOp",EDGE,"E2176"),sQuery(id+"F0.wireOp",EDGE,"E2177"),sQuery(id+"F0.wireOp",EDGE,"E2178"),sQuery(id+"F0.wireOp",EDGE,"E2179"),sQuery(id+"F0.wireOp",EDGE,"E2180"),sQuery(id+"F0.wireOp",EDGE,"E2181"),sQuery(id+"F0.wireOp",EDGE,"E2182"),sQuery(id+"F0.wireOp",EDGE,"E2183"),sQuery(id+"F0.wireOp",EDGE,"E2184"),sQuery(id+"F0.wireOp",EDGE,"E2185"),sQuery(id+"F0.wireOp",EDGE,"E2186"),sQuery(id+"F0.wireOp",EDGE,"E2187"),sQuery(id+"F0.wireOp",EDGE,"E2188"),sQuery(id+"F0.wireOp",EDGE,"E2189"),sQuery(id+"F0.wireOp",EDGE,"E2190"),sQuery(id+"F0.wireOp",EDGE,"E2191"),sQuery(id+"F0.wireOp",EDGE,"E2192"),sQuery(id+"F0.wireOp",EDGE,"E2193"),sQuery(id+"F0.wireOp",EDGE,"E2194"),sQuery(id+"F0.wireOp",EDGE,"E2195"),sQuery(id+"F0.wireOp",EDGE,"E2196"),sQuery(id+"F0.wireOp",EDGE,"E2197"),sQuery(id+"F0.wireOp",EDGE,"E2198"),sQuery(id+"F0.wireOp",EDGE,"E2199"),sQuery(id+"F0.wireOp",EDGE,"E2200"),sQuery(id+"F0.wireOp",EDGE,"E2201"),sQuery(id+"F0.wireOp",EDGE,"E2202"),sQuery(id+"F0.wireOp",EDGE,"E2203"),sQuery(id+"F0.wireOp",EDGE,"E2204"),sQuery(id+"F0.wireOp",EDGE,"E2205"),sQuery(id+"F0.wireOp",EDGE,"E2206"),sQuery(id+"F0.wireOp",EDGE,"E2207"),sQuery(id+"F0.wireOp",EDGE,"E2208"),sQuery(id+"F0.wireOp",EDGE,"E2209"),sQuery(id+"F0.wireOp",EDGE,"E2210"),sQuery(id+"F0.wireOp",EDGE,"E2211"),sQuery(id+"F0.wireOp",EDGE,"E2212"),sQuery(id+"F0.wireOp",EDGE,"E2213"),sQuery(id+"F0.wireOp",EDGE,"E2214"),sQuery(id+"F0.wireOp",EDGE,"E2215"),sQuery(id+"F0.wireOp",EDGE,"E2216"),sQuery(id+"F0.wireOp",EDGE,"E2217"),sQuery(id+"F0.wireOp",EDGE,"E2218"),sQuery(id+"F0.wireOp",EDGE,"E2219"),sQuery(id+"F0.wireOp",EDGE,"E2220"),sQuery(id+"F0.wireOp",EDGE,"E2221"),sQuery(id+"F0.wireOp",EDGE,"E2222"),sQuery(id+"F0.wireOp",EDGE,"E2223"),sQuery(id+"F0.wireOp",EDGE,"E2224"),sQuery(id+"F0.wireOp",EDGE,"E2225"),sQuery(id+"F0.wireOp",EDGE,"E2226"),sQuery(id+"F0.wireOp",EDGE,"E2227"),sQuery(id+"F0.wireOp",EDGE,"E2228"),sQuery(id+"F0.wireOp",EDGE,"E2229"),sQuery(id+"F0.wireOp",EDGE,"E2230"),sQuery(id+"F0.wireOp",EDGE,"E2231"),sQuery(id+"F0.wireOp",EDGE,"E2232"),sQuery(id+"F0.wireOp",EDGE,"E2233"),sQuery(id+"F0.wireOp",EDGE,"E2234"),sQuery(id+"F0.wireOp",EDGE,"E2235"),sQuery(id+"F0.wireOp",EDGE,"E2236"),sQuery(id+"F0.wireOp",EDGE,"E2237"),sQuery(id+"F0.wireOp",EDGE,"E2238"),sQuery(id+"F0.wireOp",EDGE,"E2239"),sQuery(id+"F0.wireOp",EDGE,"E2240"),sQuery(id+"F0.wireOp",EDGE,"E2241"),sQuery(id+"F0.wireOp",EDGE,"E2242"),sQuery(id+"F0.wireOp",EDGE,"E2243"),sQuery(id+"F0.wireOp",EDGE,"E2244"),sQuery(id+"F0.wireOp",EDGE,"E2245"),sQuery(id+"F0.wireOp",EDGE,"E2246"),sQuery(id+"F0.wireOp",EDGE,"E2247"),sQuery(id+"F0.wireOp",EDGE,"E2248"),sQuery(id+"F0.wireOp",EDGE,"E2249"),sQuery(id+"F0.wireOp",EDGE,"E2250"),sQuery(id+"F0.wireOp",EDGE,"E2251"),sQuery(id+"F0.wireOp",EDGE,"E2252"),sQuery(id+"F0.wireOp",EDGE,"E2253"),sQuery(id+"F0.wireOp",EDGE,"E2254"),sQuery(id+"F0.wireOp",EDGE,"E2255"),sQuery(id+"F0.wireOp",EDGE,"E2256"),sQuery(id+"F0.wireOp",EDGE,"E2257"),sQuery(id+"F0.wireOp",EDGE,"E2258"),sQuery(id+"F0.wireOp",EDGE,"E2259"),sQuery(id+"F0.wireOp",EDGE,"E2260"),sQuery(id+"F0.wireOp",EDGE,"E2261"),sQuery(id+"F0.wireOp",EDGE,"E2262"),sQuery(id+"F0.wireOp",EDGE,"E2263"),sQuery(id+"F0.wireOp",EDGE,"E2264"),sQuery(id+"F0.wireOp",EDGE,"E2265"),sQuery(id+"F0.wireOp",EDGE,"E2266"),sQuery(id+"F0.wireOp",EDGE,"E2267"),sQuery(id+"F0.wireOp",EDGE,"E2268"),sQuery(id+"F0.wireOp",EDGE,"E2269"),sQuery(id+"F0.wireOp",EDGE,"E2270"),sQuery(id+"F0.wireOp",EDGE,"E2271"),sQuery(id+"F0.wireOp",EDGE,"E2272"),sQuery(id+"F0.wireOp",EDGE,"E2273"),sQuery(id+"F0.wireOp",EDGE,"E2274"),sQuery(id+"F0.wireOp",EDGE,"E2275"),sQuery(id+"F0.wireOp",EDGE,"E2276"),sQuery(id+"F0.wireOp",EDGE,"E2277"),sQuery(id+"F0.wireOp",EDGE,"E2278"),sQuery(id+"F0.wireOp",EDGE,"E2279"),sQuery(id+"F0.wireOp",EDGE,"E2280"),sQuery(id+"F0.wireOp",EDGE,"E2281"),sQuery(id+"F0.wireOp",EDGE,"E2282"),sQuery(id+"F0.wireOp",EDGE,"E2283"),sQuery(id+"F0.wireOp",EDGE,"E2284"),sQuery(id+"F0.wireOp",EDGE,"E2285"),sQuery(id+"F0.wireOp",EDGE,"E2286"),sQuery(id+"F0.wireOp",EDGE,"E2287"),sQuery(id+"F0.wireOp",EDGE,"E2288"),sQuery(id+"F0.wireOp",EDGE,"E2289"),sQuery(id+"F0.wireOp",EDGE,"E2290"),sQuery(id+"F0.wireOp",EDGE,"E2291"),sQuery(id+"F0.wireOp",EDGE,"E2292"),sQuery(id+"F0.wireOp",EDGE,"E2293"),sQuery(id+"F0.wireOp",EDGE,"E2294"),sQuery(id+"F0.wireOp",EDGE,"E2295"),sQuery(id+"F0.wireOp",EDGE,"E2296"),sQuery(id+"F0.wireOp",EDGE,"E2297"),sQuery(id+"F0.wireOp",EDGE,"E2298"),sQuery(id+"F0.wireOp",EDGE,"E2299"),sQuery(id+"F0.wireOp",EDGE,"E2300"),sQuery(id+"F0.wireOp",EDGE,"E2301"),sQuery(id+"F0.wireOp",EDGE,"E2302"),sQuery(id+"F0.wireOp",EDGE,"E2303"),sQuery(id+"F0.wireOp",EDGE,"E2304"),sQuery(id+"F0.wireOp",EDGE,"E2305"),sQuery(id+"F0.wireOp",EDGE,"E2306"),sQuery(id+"F0.wireOp",EDGE,"E2307"),sQuery(id+"F0.wireOp",EDGE,"E2308"),sQuery(id+"F0.wireOp",EDGE,"E2309"),sQuery(id+"F0.wireOp",EDGE,"E2310"),sQuery(id+"F0.wireOp",EDGE,"E2311"),sQuery(id+"F0.wireOp",EDGE,"E2312"),sQuery(id+"F0.wireOp",EDGE,"E2313"),sQuery(id+"F0.wireOp",EDGE,"E2314"),sQuery(id+"F0.wireOp",EDGE,"E2315"),sQuery(id+"F0.wireOp",EDGE,"E2316"),sQuery(id+"F0.wireOp",EDGE,"E2317"),sQuery(id+"F0.wireOp",EDGE,"E2318"),sQuery(id+"F0.wireOp",EDGE,"E2319"),sQuery(id+"F0.wireOp",EDGE,"E2320"),sQuery(id+"F0.wireOp",EDGE,"E2321"),sQuery(id+"F0.wireOp",EDGE,"E2322"),sQuery(id+"F0.wireOp",EDGE,"E2323"),sQuery(id+"F0.wireOp",EDGE,"E2324"),sQuery(id+"F0.wireOp",EDGE,"E2325"),sQuery(id+"F0.wireOp",EDGE,"E2326"),sQuery(id+"F0.wireOp",EDGE,"E2327"),sQuery(id+"F0.wireOp",EDGE,"E2328"),sQuery(id+"F0.wireOp",EDGE,"E2329"),sQuery(id+"F0.wireOp",EDGE,"E2330"),sQuery(id+"F0.wireOp",EDGE,"E2331"),sQuery(id+"F0.wireOp",EDGE,"E2332"),sQuery(id+"F0.wireOp",EDGE,"E2333"),sQuery(id+"F0.wireOp",EDGE,"E2334"),sQuery(id+"F0.wireOp",EDGE,"E2335"),sQuery(id+"F0.wireOp",EDGE,"E2336"),sQuery(id+"F0.wireOp",EDGE,"E2337"),sQuery(id+"F0.wireOp",EDGE,"E2338"),sQuery(id+"F0.wireOp",EDGE,"E2339"),sQuery(id+"F0.wireOp",EDGE,"E2340"),sQuery(id+"F0.wireOp",EDGE,"E2341"),sQuery(id+"F0.wireOp",EDGE,"E2342"),sQuery(id+"F0.wireOp",EDGE,"E2343"),sQuery(id+"F0.wireOp",EDGE,"E2344"),sQuery(id+"F0.wireOp",EDGE,"E2345"),sQuery(id+"F0.wireOp",EDGE,"E2346"),sQuery(id+"F0.wireOp",EDGE,"E2347"),sQuery(id+"F0.wireOp",EDGE,"E2348"),sQuery(id+"F0.wireOp",EDGE,"E2349"),sQuery(id+"F0.wireOp",EDGE,"E2350"),sQuery(id+"F0.wireOp",EDGE,"E2351"),sQuery(id+"F0.wireOp",EDGE,"E2352"),sQuery(id+"F0.wireOp",EDGE,"E2353"),sQuery(id+"F0.wireOp",EDGE,"E2354"),sQuery(id+"F0.wireOp",EDGE,"E2355"),sQuery(id+"F0.wireOp",EDGE,"E2356"),sQuery(id+"F0.wireOp",EDGE,"E2357"),sQuery(id+"F0.wireOp",EDGE,"E2358"),sQuery(id+"F0.wireOp",EDGE,"E2359"),sQuery(id+"F0.wireOp",EDGE,"E2360"),sQuery(id+"F0.wireOp",EDGE,"E2361"),sQuery(id+"F0.wireOp",EDGE,"E2362"),sQuery(id+"F0.wireOp",EDGE,"E2363"),sQuery(id+"F0.wireOp",EDGE,"E2364"),sQuery(id+"F0.wireOp",EDGE,"E2365"),sQuery(id+"F0.wireOp",EDGE,"E2366"),sQuery(id+"F0.wireOp",EDGE,"E2367"),sQuery(id+"F0.wireOp",EDGE,"E2368"),sQuery(id+"F0.wireOp",EDGE,"E2369"),sQuery(id+"F0.wireOp",EDGE,"E2370"),sQuery(id+"F0.wireOp",EDGE,"E2371"),sQuery(id+"F0.wireOp",EDGE,"E2372"),sQuery(id+"F0.wireOp",EDGE,"E2373"),sQuery(id+"F0.wireOp",EDGE,"E2374"),sQuery(id+"F0.wireOp",EDGE,"E2375"),sQuery(id+"F0.wireOp",EDGE,"E2376"),sQuery(id+"F0.wireOp",EDGE,"E2377"),sQuery(id+"F0.wireOp",EDGE,"E2378"),sQuery(id+"F0.wireOp",EDGE,"E2379"),sQuery(id+"F0.wireOp",EDGE,"E2380"),sQuery(id+"F0.wireOp",EDGE,"E2381"),sQuery(id+"F0.wireOp",EDGE,"E2382"),sQuery(id+"F0.wireOp",EDGE,"E2383"),sQuery(id+"F0.wireOp",EDGE,"E2384"),sQuery(id+"F0.wireOp",EDGE,"E2385"),sQuery(id+"F0.wireOp",EDGE,"E2386"),sQuery(id+"F0.wireOp",EDGE,"E2387"),sQuery(id+"F0.wireOp",EDGE,"E2388"),sQuery(id+"F0.wireOp",EDGE,"E2389"),sQuery(id+"F0.wireOp",EDGE,"E2390"),sQuery(id+"F0.wireOp",EDGE,"E2391"),sQuery(id+"F0.wireOp",EDGE,"E2392"),sQuery(id+"F0.wireOp",EDGE,"E2393"),sQuery(id+"F0.wireOp",EDGE,"E2394"),sQuery(id+"F0.wireOp",EDGE,"E2395"),sQuery(id+"F0.wireOp",EDGE,"E2396"),sQuery(id+"F0.wireOp",EDGE,"E2397"),sQuery(id+"F0.wireOp",EDGE,"E2398"),sQuery(id+"F0.wireOp",EDGE,"E2399"),sQuery(id+"F0.wireOp",EDGE,"E2400"),sQuery(id+"F0.wireOp",EDGE,"E2401"),sQuery(id+"F0.wireOp",EDGE,"E2402"),sQuery(id+"F0.wireOp",EDGE,"E2403"),sQuery(id+"F0.wireOp",EDGE,"E2404"),sQuery(id+"F0.wireOp",EDGE,"E2405"),sQuery(id+"F0.wireOp",EDGE,"E2406"),sQuery(id+"F0.wireOp",EDGE,"E2407"),sQuery(id+"F0.wireOp",EDGE,"E2408"),sQuery(id+"F0.wireOp",EDGE,"E2409"),sQuery(id+"F0.wireOp",EDGE,"E2410"),sQuery(id+"F0.wireOp",EDGE,"E2411"),sQuery(id+"F0.wireOp",EDGE,"E2412"),sQuery(id+"F0.wireOp",EDGE,"E2413"),sQuery(id+"F0.wireOp",EDGE,"E2414"),sQuery(id+"F0.wireOp",EDGE,"E2415"),sQuery(id+"F0.wireOp",EDGE,"E2416"),sQuery(id+"F0.wireOp",EDGE,"E2417"),sQuery(id+"F0.wireOp",EDGE,"E2418"),sQuery(id+"F0.wireOp",EDGE,"E2419"),sQuery(id+"F0.wireOp",EDGE,"E2420"),sQuery(id+"F0.wireOp",EDGE,"E2421"),sQuery(id+"F0.wireOp",EDGE,"E2422"),sQuery(id+"F0.wireOp",EDGE,"E2423"),sQuery(id+"F0.wireOp",EDGE,"E2424"),sQuery(id+"F0.wireOp",EDGE,"E2425"),sQuery(id+"F0.wireOp",EDGE,"E2426"),sQuery(id+"F0.wireOp",EDGE,"E2427"),sQuery(id+"F0.wireOp",EDGE,"E2428"),sQuery(id+"F0.wireOp",EDGE,"E2429"),sQuery(id+"F0.wireOp",EDGE,"E2430"),sQuery(id+"F0.wireOp",EDGE,"E2431"),sQuery(id+"F0.wireOp",EDGE,"E2432"),sQuery(id+"F0.wireOp",EDGE,"E2433"),sQuery(id+"F0.wireOp",EDGE,"E2434"),sQuery(id+"F0.wireOp",EDGE,"E2435"),sQuery(id+"F0.wireOp",EDGE,"E2436"),sQuery(id+"F0.wireOp",EDGE,"E2437"),sQuery(id+"F0.wireOp",EDGE,"E2438"),sQuery(id+"F0.wireOp",EDGE,"E2439"),sQuery(id+"F0.wireOp",EDGE,"E2440"),sQuery(id+"F0.wireOp",EDGE,"E2441"),sQuery(id+"F0.wireOp",EDGE,"E2442"),sQuery(id+"F0.wireOp",EDGE,"E2443"),sQuery(id+"F0.wireOp",EDGE,"E2444"),sQuery(id+"F0.wireOp",EDGE,"E2445"),sQuery(id+"F0.wireOp",EDGE,"E2446"),sQuery(id+"F0.wireOp",EDGE,"E2447"),sQuery(id+"F0.wireOp",EDGE,"E2448"),sQuery(id+"F0.wireOp",EDGE,"E2449"),sQuery(id+"F0.wireOp",EDGE,"E2450"),sQuery(id+"F0.wireOp",EDGE,"E2451"),sQuery(id+"F0.wireOp",EDGE,"E2452"),sQuery(id+"F0.wireOp",EDGE,"E2453"),sQuery(id+"F0.wireOp",EDGE,"E2454"),sQuery(id+"F0.wireOp",EDGE,"E2455"),sQuery(id+"F0.wireOp",EDGE,"E2456"),sQuery(id+"F0.wireOp",EDGE,"E2457"),sQuery(id+"F0.wireOp",EDGE,"E2458"),sQuery(id+"F0.wireOp",EDGE,"E2459"),sQuery(id+"F0.wireOp",EDGE,"E2460"),sQuery(id+"F0.wireOp",EDGE,"E2461"),sQuery(id+"F0.wireOp",EDGE,"E2462"),sQuery(id+"F0.wireOp",EDGE,"E2463"),sQuery(id+"F0.wireOp",EDGE,"E2464"),sQuery(id+"F0.wireOp",EDGE,"E2465"),sQuery(id+"F0.wireOp",EDGE,"E2466"),sQuery(id+"F0.wireOp",EDGE,"E2467"),sQuery(id+"F0.wireOp",EDGE,"E2468"),sQuery(id+"F0.wireOp",EDGE,"E2469"),sQuery(id+"F0.wireOp",EDGE,"E2470"),sQuery(id+"F0.wireOp",EDGE,"E2471"),sQuery(id+"F0.wireOp",EDGE,"E2472"),sQuery(id+"F0.wireOp",EDGE,"E2473"),sQuery(id+"F0.wireOp",EDGE,"E2474"),sQuery(id+"F0.wireOp",EDGE,"E2475"),sQuery(id+"F0.wireOp",EDGE,"E2476"),sQuery(id+"F0.wireOp",EDGE,"E2477"),sQuery(id+"F0.wireOp",EDGE,"E2478"),sQuery(id+"F0.wireOp",EDGE,"E2479"),sQuery(id+"F0.wireOp",EDGE,"E2480"),sQuery(id+"F0.wireOp",EDGE,"E2481"),sQuery(id+"F0.wireOp",EDGE,"E2482"),sQuery(id+"F0.wireOp",EDGE,"E2483"),sQuery(id+"F0.wireOp",EDGE,"E2484"),sQuery(id+"F0.wireOp",EDGE,"E2485"),sQuery(id+"F0.wireOp",EDGE,"E2486"),sQuery(id+"F0.wireOp",EDGE,"E2487"),sQuery(id+"F0.wireOp",EDGE,"E2488"),sQuery(id+"F0.wireOp",EDGE,"E2489"),sQuery(id+"F0.wireOp",EDGE,"E2490"),sQuery(id+"F0.wireOp",EDGE,"E2491"),sQuery(id+"F0.wireOp",EDGE,"E2492"),sQuery(id+"F0.wireOp",EDGE,"E2493"),sQuery(id+"F0.wireOp",EDGE,"E2494"),sQuery(id+"F0.wireOp",EDGE,"E2495"),sQuery(id+"F0.wireOp",EDGE,"E2496"),sQuery(id+"F0.wireOp",EDGE,"E2497"),sQuery(id+"F0.wireOp",EDGE,"E2498"),sQuery(id+"F0.wireOp",EDGE,"E2499"),sQuery(id+"F0.wireOp",EDGE,"E2500"),sQuery(id+"F0.wireOp",EDGE,"E2501"),sQuery(id+"F0.wireOp",EDGE,"E2502"),sQuery(id+"F0.wireOp",EDGE,"E2503"),sQuery(id+"F0.wireOp",EDGE,"E2504"),sQuery(id+"F0.wireOp",EDGE,"E2505"),sQuery(id+"F0.wireOp",EDGE,"E2506"),sQuery(id+"F0.wireOp",EDGE,"E2507"),sQuery(id+"F0.wireOp",EDGE,"E2508"),sQuery(id+"F0.wireOp",EDGE,"E2509"),sQuery(id+"F0.wireOp",EDGE,"E2510"),sQuery(id+"F0.wireOp",EDGE,"E2511"),sQuery(id+"F0.wireOp",EDGE,"E2512"),sQuery(id+"F0.wireOp",EDGE,"E2513"),sQuery(id+"F0.wireOp",EDGE,"E2514"),sQuery(id+"F0.wireOp",EDGE,"E2515"),sQuery(id+"F0.wireOp",EDGE,"E2516"),sQuery(id+"F0.wireOp",EDGE,"E2517"),sQuery(id+"F0.wireOp",EDGE,"E2518"),sQuery(id+"F0.wireOp",EDGE,"E2519"),sQuery(id+"F0.wireOp",EDGE,"E2520"),sQuery(id+"F0.wireOp",EDGE,"E2521"),sQuery(id+"F0.wireOp",EDGE,"E2522"),sQuery(id+"F0.wireOp",EDGE,"E2523"),sQuery(id+"F0.wireOp",EDGE,"E2524"),sQuery(id+"F0.wireOp",EDGE,"E2525"),sQuery(id+"F0.wireOp",EDGE,"E2526"),sQuery(id+"F0.wireOp",EDGE,"E2527"),sQuery(id+"F0.wireOp",EDGE,"E2528"),sQuery(id+"F0.wireOp",EDGE,"E2529"),sQuery(id+"F0.wireOp",EDGE,"E2530"),sQuery(id+"F0.wireOp",EDGE,"E2531"),sQuery(id+"F0.wireOp",EDGE,"E2532"),sQuery(id+"F0.wireOp",EDGE,"E2533"),sQuery(id+"F0.wireOp",EDGE,"E2534"),sQuery(id+"F0.wireOp",EDGE,"E2535"),sQuery(id+"F0.wireOp",EDGE,"E2536"),sQuery(id+"F0.wireOp",EDGE,"E2537"),sQuery(id+"F0.wireOp",EDGE,"E2538"),sQuery(id+"F0.wireOp",EDGE,"E2539"),sQuery(id+"F0.wireOp",EDGE,"E2540"),sQuery(id+"F0.wireOp",EDGE,"E2541"),sQuery(id+"F0.wireOp",EDGE,"E2542"),sQuery(id+"F0.wireOp",EDGE,"E2543"),sQuery(id+"F0.wireOp",EDGE,"E2544"),sQuery(id+"F0.wireOp",EDGE,"E2545"),sQuery(id+"F0.wireOp",EDGE,"E2546"),sQuery(id+"F0.wireOp",EDGE,"E2547"),sQuery(id+"F0.wireOp",EDGE,"E2548"),sQuery(id+"F0.wireOp",EDGE,"E2549"),sQuery(id+"F0.wireOp",EDGE,"E2550"),sQuery(id+"F0.wireOp",EDGE,"E2551"),sQuery(id+"F0.wireOp",EDGE,"E2552"),sQuery(id+"F0.wireOp",EDGE,"E2553"),sQuery(id+"F0.wireOp",EDGE,"E2554"),sQuery(id+"F0.wireOp",EDGE,"E2555"),sQuery(id+"F0.wireOp",EDGE,"E2556"),sQuery(id+"F0.wireOp",EDGE,"E2557"),sQuery(id+"F0.wireOp",EDGE,"E2558"),sQuery(id+"F0.wireOp",EDGE,"E2559"),sQuery(id+"F0.wireOp",EDGE,"E2560"),sQuery(id+"F0.wireOp",EDGE,"E2561"),sQuery(id+"F0.wireOp",EDGE,"E2562"),sQuery(id+"F0.wireOp",EDGE,"E2563"),sQuery(id+"F0.wireOp",EDGE,"E2564"),sQuery(id+"F0.wireOp",EDGE,"E2565"),sQuery(id+"F0.wireOp",EDGE,"E2566"),sQuery(id+"F0.wireOp",EDGE,"E2567"),sQuery(id+"F0.wireOp",EDGE,"E2568"),sQuery(id+"F0.wireOp",EDGE,"E2569"),sQuery(id+"F0.wireOp",EDGE,"E2570"),sQuery(id+"F0.wireOp",EDGE,"E2571"),sQuery(id+"F0.wireOp",EDGE,"E2572"),sQuery(id+"F0.wireOp",EDGE,"E2573"),sQuery(id+"F0.wireOp",EDGE,"E2574"),sQuery(id+"F0.wireOp",EDGE,"E2575"),sQuery(id+"F0.wireOp",EDGE,"E2576"),sQuery(id+"F0.wireOp",EDGE,"E2577"),sQuery(id+"F0.wireOp",EDGE,"E2578"),sQuery(id+"F0.wireOp",EDGE,"E2579"),sQuery(id+"F0.wireOp",EDGE,"E2580"),sQuery(id+"F0.wireOp",EDGE,"E2581"),sQuery(id+"F0.wireOp",EDGE,"E2582"),sQuery(id+"F0.wireOp",EDGE,"E2583"),sQuery(id+"F0.wireOp",EDGE,"E2584"),sQuery(id+"F0.wireOp",EDGE,"E2585"),sQuery(id+"F0.wireOp",EDGE,"E2586"),sQuery(id+"F0.wireOp",EDGE,"E2587"),sQuery(id+"F0.wireOp",EDGE,"E2588"),sQuery(id+"F0.wireOp",EDGE,"E2589"),sQuery(id+"F0.wireOp",EDGE,"E2590"),sQuery(id+"F0.wireOp",EDGE,"E2591"),sQuery(id+"F0.wireOp",EDGE,"E2592"),sQuery(id+"F0.wireOp",EDGE,"E2593"),sQuery(id+"F0.wireOp",EDGE,"E2594"),sQuery(id+"F0.wireOp",EDGE,"E2595"),sQuery(id+"F0.wireOp",EDGE,"E2596"),sQuery(id+"F0.wireOp",EDGE,"E2597"),sQuery(id+"F0.wireOp",EDGE,"E2598"),sQuery(id+"F0.wireOp",EDGE,"E2599"),sQuery(id+"F0.wireOp",EDGE,"E2600"),sQuery(id+"F0.wireOp",EDGE,"E2601"),sQuery(id+"F0.wireOp",EDGE,"E2602"),sQuery(id+"F0.wireOp",EDGE,"E2603"),sQuery(id+"F0.wireOp",EDGE,"E2604"),sQuery(id+"F0.wireOp",EDGE,"E2605"),sQuery(id+"F0.wireOp",EDGE,"E2606"),sQuery(id+"F0.wireOp",EDGE,"E2607"),sQuery(id+"F0.wireOp",EDGE,"E2608"),sQuery(id+"F0.wireOp",EDGE,"E2609"),sQuery(id+"F0.wireOp",EDGE,"E2610"),sQuery(id+"F0.wireOp",EDGE,"E2611"),sQuery(id+"F0.wireOp",EDGE,"E2612"),sQuery(id+"F0.wireOp",EDGE,"E2613"),sQuery(id+"F0.wireOp",EDGE,"E2614"),sQuery(id+"F0.wireOp",EDGE,"E2615"),sQuery(id+"F0.wireOp",EDGE,"E2616"),sQuery(id+"F0.wireOp",EDGE,"E2617"),sQuery(id+"F0.wireOp",EDGE,"E2618"),sQuery(id+"F0.wireOp",EDGE,"E2619"),sQuery(id+"F0.wireOp",EDGE,"E2620"),sQuery(id+"F0.wireOp",EDGE,"E2621"),sQuery(id+"F0.wireOp",EDGE,"E2622"),sQuery(id+"F0.wireOp",EDGE,"E2623"),sQuery(id+"F0.wireOp",EDGE,"E2624"),sQuery(id+"F0.wireOp",EDGE,"E2625"),sQuery(id+"F0.wireOp",EDGE,"E2626"),sQuery(id+"F0.wireOp",EDGE,"E2627"),sQuery(id+"F0.wireOp",EDGE,"E2628"),sQuery(id+"F0.wireOp",EDGE,"E2629"),sQuery(id+"F0.wireOp",EDGE,"E2630"),sQuery(id+"F0.wireOp",EDGE,"E2631"),sQuery(id+"F0.wireOp",EDGE,"E2632"),sQuery(id+"F0.wireOp",EDGE,"E2633"),sQuery(id+"F0.wireOp",EDGE,"E2634"),sQuery(id+"F0.wireOp",EDGE,"E2635"),sQuery(id+"F0.wireOp",EDGE,"E2636"),sQuery(id+"F0.wireOp",EDGE,"E2637"),sQuery(id+"F0.wireOp",EDGE,"E2638"),sQuery(id+"F0.wireOp",EDGE,"E2639"),sQuery(id+"F0.wireOp",EDGE,"E2640"),sQuery(id+"F0.wireOp",EDGE,"E2641"),sQuery(id+"F0.wireOp",EDGE,"E2642"),sQuery(id+"F0.wireOp",EDGE,"E2643"),sQuery(id+"F0.wireOp",EDGE,"E2644"),sQuery(id+"F0.wireOp",EDGE,"E2645"),sQuery(id+"F0.wireOp",EDGE,"E2646"),sQuery(id+"F0.wireOp",EDGE,"E2647"),sQuery(id+"F0.wireOp",EDGE,"E2648"),sQuery(id+"F0.wireOp",EDGE,"E2649"),sQuery(id+"F0.wireOp",EDGE,"E2650"),sQuery(id+"F0.wireOp",EDGE,"E2651"),sQuery(id+"F0.wireOp",EDGE,"E2652"),sQuery(id+"F0.wireOp",EDGE,"E2653"),sQuery(id+"F0.wireOp",EDGE,"E2654"),sQuery(id+"F0.wireOp",EDGE,"E2655"),sQuery(id+"F0.wireOp",EDGE,"E2656"),sQuery(id+"F0.wireOp",EDGE,"E2657"),sQuery(id+"F0.wireOp",EDGE,"E2658"),sQuery(id+"F0.wireOp",EDGE,"E2659"),sQuery(id+"F0.wireOp",EDGE,"E2660"),sQuery(id+"F0.wireOp",EDGE,"E2661"),sQuery(id+"F0.wireOp",EDGE,"E2662"),sQuery(id+"F0.wireOp",EDGE,"E2663"),sQuery(id+"F0.wireOp",EDGE,"E2664"),sQuery(id+"F0.wireOp",EDGE,"E2665"),sQuery(id+"F0.wireOp",EDGE,"E2666"),sQuery(id+"F0.wireOp",EDGE,"E2667"),sQuery(id+"F0.wireOp",EDGE,"E2668"),sQuery(id+"F0.wireOp",EDGE,"E2669"),sQuery(id+"F0.wireOp",EDGE,"E2670"),sQuery(id+"F0.wireOp",EDGE,"E2671"),sQuery(id+"F0.wireOp",EDGE,"E2672"),sQuery(id+"F0.wireOp",EDGE,"E2673"),sQuery(id+"F0.wireOp",EDGE,"E2674"),sQuery(id+"F0.wireOp",EDGE,"E2675"),sQuery(id+"F0.wireOp",EDGE,"E2676"),sQuery(id+"F0.wireOp",EDGE,"E2677"),sQuery(id+"F0.wireOp",EDGE,"E2678"),sQuery(id+"F0.wireOp",EDGE,"E2679"),sQuery(id+"F0.wireOp",EDGE,"E2680"),sQuery(id+"F0.wireOp",EDGE,"E2681"),sQuery(id+"F0.wireOp",EDGE,"E2682"),sQuery(id+"F0.wireOp",EDGE,"E2683"),sQuery(id+"F0.wireOp",EDGE,"E2684"),sQuery(id+"F0.wireOp",EDGE,"E2685"),sQuery(id+"F0.wireOp",EDGE,"E2686"),sQuery(id+"F0.wireOp",EDGE,"E2687"),sQuery(id+"F0.wireOp",EDGE,"E2688"),sQuery(id+"F0.wireOp",EDGE,"E2689"),sQuery(id+"F0.wireOp",EDGE,"E2690"),sQuery(id+"F0.wireOp",EDGE,"E2691"),sQuery(id+"F0.wireOp",EDGE,"E2692"),sQuery(id+"F0.wireOp",EDGE,"E2693"),sQuery(id+"F0.wireOp",EDGE,"E2694"),sQuery(id+"F0.wireOp",EDGE,"E2695"),sQuery(id+"F0.wireOp",EDGE,"E2696"),sQuery(id+"F0.wireOp",EDGE,"E2697"),sQuery(id+"F0.wireOp",EDGE,"E2698"),sQuery(id+"F0.wireOp",EDGE,"E2699"),sQuery(id+"F0.wireOp",EDGE,"E2700"),sQuery(id+"F0.wireOp",EDGE,"E2701"),sQuery(id+"F0.wireOp",EDGE,"E2702"),sQuery(id+"F0.wireOp",EDGE,"E2703"),sQuery(id+"F0.wireOp",EDGE,"E2704"),sQuery(id+"F0.wireOp",EDGE,"E2705"),sQuery(id+"F0.wireOp",EDGE,"E2706"),sQuery(id+"F0.wireOp",EDGE,"E2707"),sQuery(id+"F0.wireOp",EDGE,"E2708"),sQuery(id+"F0.wireOp",EDGE,"E2709"),sQuery(id+"F0.wireOp",EDGE,"E2710"),sQuery(id+"F0.wireOp",EDGE,"E2711"),sQuery(id+"F0.wireOp",EDGE,"E2712"),sQuery(id+"F0.wireOp",EDGE,"E2713"),sQuery(id+"F0.wireOp",EDGE,"E2714"),sQuery(id+"F0.wireOp",EDGE,"E2715"),sQuery(id+"F0.wireOp",EDGE,"E2716"),sQuery(id+"F0.wireOp",EDGE,"E2717"),sQuery(id+"F0.wireOp",EDGE,"E2718"),sQuery(id+"F0.wireOp",EDGE,"E2719"),sQuery(id+"F0.wireOp",EDGE,"E2720"),sQuery(id+"F0.wireOp",EDGE,"E2721"),sQuery(id+"F0.wireOp",EDGE,"E2722"),sQuery(id+"F0.wireOp",EDGE,"E2723"),sQuery(id+"F0.wireOp",EDGE,"E2724"),sQuery(id+"F0.wireOp",EDGE,"E2725"),sQuery(id+"F0.wireOp",EDGE,"E2726"),sQuery(id+"F0.wireOp",EDGE,"E2727"),sQuery(id+"F0.wireOp",EDGE,"E2728"),sQuery(id+"F0.wireOp",EDGE,"E2729"),sQuery(id+"F0.wireOp",EDGE,"E2730"),sQuery(id+"F0.wireOp",EDGE,"E2731"),sQuery(id+"F0.wireOp",EDGE,"E2732"),sQuery(id+"F0.wireOp",EDGE,"E2733"),sQuery(id+"F0.wireOp",EDGE,"E2734"),sQuery(id+"F0.wireOp",EDGE,"E2735"),sQuery(id+"F0.wireOp",EDGE,"E2736"),sQuery(id+"F0.wireOp",EDGE,"E2737"),sQuery(id+"F0.wireOp",EDGE,"E2738"),sQuery(id+"F0.wireOp",EDGE,"E2739"),sQuery(id+"F0.wireOp",EDGE,"E2740"),sQuery(id+"F0.wireOp",EDGE,"E2741"),sQuery(id+"F0.wireOp",EDGE,"E2742"),sQuery(id+"F0.wireOp",EDGE,"E2743"),sQuery(id+"F0.wireOp",EDGE,"E2744"),sQuery(id+"F0.wireOp",EDGE,"E2745"),sQuery(id+"F0.wireOp",EDGE,"E2746"),sQuery(id+"F0.wireOp",EDGE,"E2747"),sQuery(id+"F0.wireOp",EDGE,"E2748"),sQuery(id+"F0.wireOp",EDGE,"E2749"),sQuery(id+"F0.wireOp",EDGE,"E2750"),sQuery(id+"F0.wireOp",EDGE,"E2751"),sQuery(id+"F0.wireOp",EDGE,"E2752"),sQuery(id+"F0.wireOp",EDGE,"E2753"),sQuery(id+"F0.wireOp",EDGE,"E2754"),sQuery(id+"F0.wireOp",EDGE,"E2755"),sQuery(id+"F0.wireOp",EDGE,"E2756"),sQuery(id+"F0.wireOp",EDGE,"E2757"),sQuery(id+"F0.wireOp",EDGE,"E2758"),sQuery(id+"F0.wireOp",EDGE,"E2759"),sQuery(id+"F0.wireOp",EDGE,"E2760"),sQuery(id+"F0.wireOp",EDGE,"E2761"),sQuery(id+"F0.wireOp",EDGE,"E2762"),sQuery(id+"F0.wireOp",EDGE,"E2763"),sQuery(id+"F0.wireOp",EDGE,"E2764"),sQuery(id+"F0.wireOp",EDGE,"E2765"),sQuery(id+"F0.wireOp",EDGE,"E2766"),sQuery(id+"F0.wireOp",EDGE,"E2767"),sQuery(id+"F0.wireOp",EDGE,"E2768"),sQuery(id+"F0.wireOp",EDGE,"E2769"),sQuery(id+"F0.wireOp",EDGE,"E2770"),sQuery(id+"F0.wireOp",EDGE,"E2771"),sQuery(id+"F0.wireOp",EDGE,"E2772"),sQuery(id+"F0.wireOp",EDGE,"E2773"),sQuery(id+"F0.wireOp",EDGE,"E2774"),sQuery(id+"F0.wireOp",EDGE,"E2775"),sQuery(id+"F0.wireOp",EDGE,"E2776"),sQuery(id+"F0.wireOp",EDGE,"E2777"),sQuery(id+"F0.wireOp",EDGE,"E2778"),sQuery(id+"F0.wireOp",EDGE,"E2779"),sQuery(id+"F0.wireOp",EDGE,"E2780"),sQuery(id+"F0.wireOp",EDGE,"E2781"),sQuery(id+"F0.wireOp",EDGE,"E2782"),sQuery(id+"F0.wireOp",EDGE,"E2783"),sQuery(id+"F0.wireOp",EDGE,"E2784"),sQuery(id+"F0.wireOp",EDGE,"E2785"),sQuery(id+"F0.wireOp",EDGE,"E2786"),sQuery(id+"F0.wireOp",EDGE,"E2787"),sQuery(id+"F0.wireOp",EDGE,"E2788"),sQuery(id+"F0.wireOp",EDGE,"E2789"),sQuery(id+"F0.wireOp",EDGE,"E2790"),sQuery(id+"F0.wireOp",EDGE,"E2791"),sQuery(id+"F0.wireOp",EDGE,"E2792"),sQuery(id+"F0.wireOp",EDGE,"E2793"),sQuery(id+"F0.wireOp",EDGE,"E2794"),sQuery(id+"F0.wireOp",EDGE,"E2795"),sQuery(id+"F0.wireOp",EDGE,"E2796"),sQuery(id+"F0.wireOp",EDGE,"E2797"),sQuery(id+"F0.wireOp",EDGE,"E2798"),sQuery(id+"F0.wireOp",EDGE,"E2799"),sQuery(id+"F0.wireOp",EDGE,"E2800"),sQuery(id+"F0.wireOp",EDGE,"E2801"),sQuery(id+"F0.wireOp",EDGE,"E2802"),sQuery(id+"F0.wireOp",EDGE,"E2803"),sQuery(id+"F0.wireOp",EDGE,"E2804"),sQuery(id+"F0.wireOp",EDGE,"E2805"),sQuery(id+"F0.wireOp",EDGE,"E2806"),sQuery(id+"F0.wireOp",EDGE,"E2807"),sQuery(id+"F0.wireOp",EDGE,"E2808"),sQuery(id+"F0.wireOp",EDGE,"E2809"),sQuery(id+"F0.wireOp",EDGE,"E2810"),sQuery(id+"F0.wireOp",EDGE,"E2811"),sQuery(id+"F0.wireOp",EDGE,"E2812"),sQuery(id+"F0.wireOp",EDGE,"E2813"),sQuery(id+"F0.wireOp",EDGE,"E2814"),sQuery(id+"F0.wireOp",EDGE,"E2815"),sQuery(id+"F0.wireOp",EDGE,"E2816"),sQuery(id+"F0.wireOp",EDGE,"E2817"),sQuery(id+"F0.wireOp",EDGE,"E2818"),sQuery(id+"F0.wireOp",EDGE,"E2819"),sQuery(id+"F0.wireOp",EDGE,"E2820"),sQuery(id+"F0.wireOp",EDGE,"E2821"),sQuery(id+"F0.wireOp",EDGE,"E2822"),sQuery(id+"F0.wireOp",EDGE,"E2823"),sQuery(id+"F0.wireOp",EDGE,"E2824"),sQuery(id+"F0.wireOp",EDGE,"E2825"),sQuery(id+"F0.wireOp",EDGE,"E2826"),sQuery(id+"F0.wireOp",EDGE,"E2827"),sQuery(id+"F0.wireOp",EDGE,"E2828"),sQuery(id+"F0.wireOp",EDGE,"E2829"),sQuery(id+"F0.wireOp",EDGE,"E2830"),sQuery(id+"F0.wireOp",EDGE,"E2831"),sQuery(id+"F0.wireOp",EDGE,"E2832"),sQuery(id+"F0.wireOp",EDGE,"E2833"),sQuery(id+"F0.wireOp",EDGE,"E2834"),sQuery(id+"F0.wireOp",EDGE,"E2835"),sQuery(id+"F0.wireOp",EDGE,"E2836"),sQuery(id+"F0.wireOp",EDGE,"E2837"),sQuery(id+"F0.wireOp",EDGE,"E2838"),sQuery(id+"F0.wireOp",EDGE,"E2839"),sQuery(id+"F0.wireOp",EDGE,"E2840"),sQuery(id+"F0.wireOp",EDGE,"E2841"),sQuery(id+"F0.wireOp",EDGE,"E2842"),sQuery(id+"F0.wireOp",EDGE,"E2843"),sQuery(id+"F0.wireOp",EDGE,"E2844"),sQuery(id+"F0.wireOp",EDGE,"E2845"),sQuery(id+"F0.wireOp",EDGE,"E2846"),sQuery(id+"F0.wireOp",EDGE,"E2847"),sQuery(id+"F0.wireOp",EDGE,"E2848"),sQuery(id+"F0.wireOp",EDGE,"E2849"),sQuery(id+"F0.wireOp",EDGE,"E2850"),sQuery(id+"F0.wireOp",EDGE,"E2851"),sQuery(id+"F0.wireOp",EDGE,"E2852"),sQuery(id+"F0.wireOp",EDGE,"E2853"),sQuery(id+"F0.wireOp",EDGE,"E2854"),sQuery(id+"F0.wireOp",EDGE,"E2855"),sQuery(id+"F0.wireOp",EDGE,"E2856"),sQuery(id+"F0.wireOp",EDGE,"E2857"),sQuery(id+"F0.wireOp",EDGE,"E2858"),sQuery(id+"F0.wireOp",EDGE,"E2859"),sQuery(id+"F0.wireOp",EDGE,"E2860"),sQuery(id+"F0.wireOp",EDGE,"E2861"),sQuery(id+"F0.wireOp",EDGE,"E2862"),sQuery(id+"F0.wireOp",EDGE,"E2863"),sQuery(id+"F0.wireOp",EDGE,"E2864"),sQuery(id+"F0.wireOp",EDGE,"E2865"),sQuery(id+"F0.wireOp",EDGE,"E2866"),sQuery(id+"F0.wireOp",EDGE,"E2867"),sQuery(id+"F0.wireOp",EDGE,"E2868"),sQuery(id+"F0.wireOp",EDGE,"E2869"),sQuery(id+"F0.wireOp",EDGE,"E2870"),sQuery(id+"F0.wireOp",EDGE,"E2871"),sQuery(id+"F0.wireOp",EDGE,"E2872"),sQuery(id+"F0.wireOp",EDGE,"E2873"),sQuery(id+"F0.wireOp",EDGE,"E2874"),sQuery(id+"F0.wireOp",EDGE,"E2875"),sQuery(id+"F0.wireOp",EDGE,"E2876"),sQuery(id+"F0.wireOp",EDGE,"E2877"),sQuery(id+"F0.wireOp",EDGE,"E2878"),sQuery(id+"F0.wireOp",EDGE,"E2879"),sQuery(id+"F0.wireOp",EDGE,"E2880"),sQuery(id+"F0.wireOp",EDGE,"E2881"),sQuery(id+"F0.wireOp",EDGE,"E2882"),sQuery(id+"F0.wireOp",EDGE,"E2883"),sQuery(id+"F0.wireOp",EDGE,"E2884"),sQuery(id+"F0.wireOp",EDGE,"E2885"),sQuery(id+"F0.wireOp",EDGE,"E2886"),sQuery(id+"F0.wireOp",EDGE,"E2887"),sQuery(id+"F0.wireOp",EDGE,"E2888"),sQuery(id+"F0.wireOp",EDGE,"E2889"),sQuery(id+"F0.wireOp",EDGE,"E2890"),sQuery(id+"F0.wireOp",EDGE,"E2891"),sQuery(id+"F0.wireOp",EDGE,"E2892"),sQuery(id+"F0.wireOp",EDGE,"E2893"),sQuery(id+"F0.wireOp",EDGE,"E2894"),sQuery(id+"F0.wireOp",EDGE,"E2895"),sQuery(id+"F0.wireOp",EDGE,"E2896"),sQuery(id+"F0.wireOp",EDGE,"E2897"),sQuery(id+"F0.wireOp",EDGE,"E2898"),sQuery(id+"F0.wireOp",EDGE,"E2899"),sQuery(id+"F0.wireOp",EDGE,"E2900"),sQuery(id+"F0.wireOp",EDGE,"E2901"),sQuery(id+"F0.wireOp",EDGE,"E2902"),sQuery(id+"F0.wireOp",EDGE,"E2903"),sQuery(id+"F0.wireOp",EDGE,"E2904"),sQuery(id+"F0.wireOp",EDGE,"E2905"),sQuery(id+"F0.wireOp",EDGE,"E2906"),sQuery(id+"F0.wireOp",EDGE,"E2907"),sQuery(id+"F0.wireOp",EDGE,"E2908"),sQuery(id+"F0.wireOp",EDGE,"E2909"),sQuery(id+"F0.wireOp",EDGE,"E2910"),sQuery(id+"F0.wireOp",EDGE,"E2911"),sQuery(id+"F0.wireOp",EDGE,"E2912"),sQuery(id+"F0.wireOp",EDGE,"E2913"),sQuery(id+"F0.wireOp",EDGE,"E2914"),sQuery(id+"F0.wireOp",EDGE,"E2915"),sQuery(id+"F0.wireOp",EDGE,"E2916"),sQuery(id+"F0.wireOp",EDGE,"E2917"),sQuery(id+"F0.wireOp",EDGE,"E2918"),sQuery(id+"F0.wireOp",EDGE,"E2919"),sQuery(id+"F0.wireOp",EDGE,"E2920"),sQuery(id+"F0.wireOp",EDGE,"E2921"),sQuery(id+"F0.wireOp",EDGE,"E2922"),sQuery(id+"F0.wireOp",EDGE,"E2923"),sQuery(id+"F0.wireOp",EDGE,"E2924"),sQuery(id+"F0.wireOp",EDGE,"E2925"),sQuery(id+"F0.wireOp",EDGE,"E2926"),sQuery(id+"F0.wireOp",EDGE,"E2927"),sQuery(id+"F0.wireOp",EDGE,"E2928"),sQuery(id+"F0.wireOp",EDGE,"E2929"),sQuery(id+"F0.wireOp",EDGE,"E2930"),sQuery(id+"F0.wireOp",EDGE,"E2931"),sQuery(id+"F0.wireOp",EDGE,"E2932"),sQuery(id+"F0.wireOp",EDGE,"E2933"),sQuery(id+"F0.wireOp",EDGE,"E2934"),sQuery(id+"F0.wireOp",EDGE,"E2935"),sQuery(id+"F0.wireOp",EDGE,"E2936"),sQuery(id+"F0.wireOp",EDGE,"E2937"),sQuery(id+"F0.wireOp",EDGE,"E2938"),sQuery(id+"F0.wireOp",EDGE,"E2939"),sQuery(id+"F0.wireOp",EDGE,"E2940"),sQuery(id+"F0.wireOp",EDGE,"E2941"),sQuery(id+"F0.wireOp",EDGE,"E2942"),sQuery(id+"F0.wireOp",EDGE,"E2943"),sQuery(id+"F0.wireOp",EDGE,"E2944"),sQuery(id+"F0.wireOp",EDGE,"E2945"),sQuery(id+"F0.wireOp",EDGE,"E2946"),sQuery(id+"F0.wireOp",EDGE,"E2947"),sQuery(id+"F0.wireOp",EDGE,"E2948"),sQuery(id+"F0.wireOp",EDGE,"E2949"),sQuery(id+"F0.wireOp",EDGE,"E2950"),sQuery(id+"F0.wireOp",EDGE,"E2951"),sQuery(id+"F0.wireOp",EDGE,"E2952"),sQuery(id+"F0.wireOp",EDGE,"E2953"),sQuery(id+"F0.wireOp",EDGE,"E2954"),sQuery(id+"F0.wireOp",EDGE,"E2955"),sQuery(id+"F0.wireOp",EDGE,"E2956"),sQuery(id+"F0.wireOp",EDGE,"E2957"),sQuery(id+"F0.wireOp",EDGE,"E2958"),sQuery(id+"F0.wireOp",EDGE,"E2959"),sQuery(id+"F0.wireOp",EDGE,"E2960"),sQuery(id+"F0.wireOp",EDGE,"E2961"),sQuery(id+"F0.wireOp",EDGE,"E2962"),sQuery(id+"F0.wireOp",EDGE,"E2963"),sQuery(id+"F0.wireOp",EDGE,"E2964"),sQuery(id+"F0.wireOp",EDGE,"E2965"),sQuery(id+"F0.wireOp",EDGE,"E2966"),sQuery(id+"F0.wireOp",EDGE,"E2967"),sQuery(id+"F0.wireOp",EDGE,"E2968"),sQuery(id+"F0.wireOp",EDGE,"E2969"),sQuery(id+"F0.wireOp",EDGE,"E2970"),sQuery(id+"F0.wireOp",EDGE,"E2971"),sQuery(id+"F0.wireOp",EDGE,"E2972"),sQuery(id+"F0.wireOp",EDGE,"E2973"),sQuery(id+"F0.wireOp",EDGE,"E2974"),sQuery(id+"F0.wireOp",EDGE,"E2975"),sQuery(id+"F0.wireOp",EDGE,"E2976"),sQuery(id+"F0.wireOp",EDGE,"E2977"),sQuery(id+"F0.wireOp",EDGE,"E2978"),sQuery(id+"F0.wireOp",EDGE,"E2979"),sQuery(id+"F0.wireOp",EDGE,"E2980"),sQuery(id+"F0.wireOp",EDGE,"E2981"),sQuery(id+"F0.wireOp",EDGE,"E2982"),sQuery(id+"F0.wireOp",EDGE,"E2983"),sQuery(id+"F0.wireOp",EDGE,"E2984"),sQuery(id+"F0.wireOp",EDGE,"E2985"),sQuery(id+"F0.wireOp",EDGE,"E2986"),sQuery(id+"F0.wireOp",EDGE,"E2987"),sQuery(id+"F0.wireOp",EDGE,"E2988"),sQuery(id+"F0.wireOp",EDGE,"E2989"),sQuery(id+"F0.wireOp",EDGE,"E2990"),sQuery(id+"F0.wireOp",EDGE,"E2991"),sQuery(id+"F0.wireOp",EDGE,"E2992"),sQuery(id+"F0.wireOp",EDGE,"E2993"),sQuery(id+"F0.wireOp",EDGE,"E2994"),sQuery(id+"F0.wireOp",EDGE,"E2995"),sQuery(id+"F0.wireOp",EDGE,"E2996"),sQuery(id+"F0.wireOp",EDGE,"E2997"),sQuery(id+"F0.wireOp",EDGE,"E2998"),sQuery(id+"F0.wireOp",EDGE,"E2999"),sQuery(id+"F0.wireOp",EDGE,"E3000"),sQuery(id+"F0.wireOp",EDGE,"E3001"),sQuery(id+"F0.wireOp",EDGE,"E3002"),sQuery(id+"F0.wireOp",EDGE,"E3003"),sQuery(id+"F0.wireOp",EDGE,"E3004"),sQuery(id+"F0.wireOp",EDGE,"E3005"),sQuery(id+"F0.wireOp",EDGE,"E3006"),sQuery(id+"F0.wireOp",EDGE,"E3007"),sQuery(id+"F0.wireOp",EDGE,"E3008"),sQuery(id+"F0.wireOp",EDGE,"E3009"),sQuery(id+"F0.wireOp",EDGE,"E3010"),sQuery(id+"F0.wireOp",EDGE,"E3011"),sQuery(id+"F0.wireOp",EDGE,"E3012"),sQuery(id+"F0.wireOp",EDGE,"E3013"),sQuery(id+"F0.wireOp",EDGE,"E3014"),sQuery(id+"F0.wireOp",EDGE,"E3015"),sQuery(id+"F0.wireOp",EDGE,"E3016"),sQuery(id+"F0.wireOp",EDGE,"E3017"),sQuery(id+"F0.wireOp",EDGE,"E3018"),sQuery(id+"F0.wireOp",EDGE,"E3019"),sQuery(id+"F0.wireOp",EDGE,"E3020"),sQuery(id+"F0.wireOp",EDGE,"E3021"),sQuery(id+"F0.wireOp",EDGE,"E3022"),sQuery(id+"F0.wireOp",EDGE,"E3023"),sQuery(id+"F0.wireOp",EDGE,"E3024"),sQuery(id+"F0.wireOp",EDGE,"E3025"),sQuery(id+"F0.wireOp",EDGE,"E3026"),sQuery(id+"F0.wireOp",EDGE,"E3027"),sQuery(id+"F0.wireOp",EDGE,"E3028"),sQuery(id+"F0.wireOp",EDGE,"E3029"),sQuery(id+"F0.wireOp",EDGE,"E3030"),sQuery(id+"F0.wireOp",EDGE,"E3031"),sQuery(id+"F0.wireOp",EDGE,"E3032"),sQuery(id+"F0.wireOp",EDGE,"E3033"),sQuery(id+"F0.wireOp",EDGE,"E3034"),sQuery(id+"F0.wireOp",EDGE,"E3035"),sQuery(id+"F0.wireOp",EDGE,"E3036"),sQuery(id+"F0.wireOp",EDGE,"E3037"),sQuery(id+"F0.wireOp",EDGE,"E3038"),sQuery(id+"F0.wireOp",EDGE,"E3039"),sQuery(id+"F0.wireOp",EDGE,"E3040"),sQuery(id+"F0.wireOp",EDGE,"E3041"),sQuery(id+"F0.wireOp",EDGE,"E3042"),sQuery(id+"F0.wireOp",EDGE,"E3043"),sQuery(id+"F0.wireOp",EDGE,"E3044"),sQuery(id+"F0.wireOp",EDGE,"E3045"),sQuery(id+"F0.wireOp",EDGE,"E3046"),sQuery(id+"F0.wireOp",EDGE,"E3047"),sQuery(id+"F0.wireOp",EDGE,"E3048"),sQuery(id+"F0.wireOp",EDGE,"E3049"),sQuery(id+"F0.wireOp",EDGE,"E3050"),sQuery(id+"F0.wireOp",EDGE,"E3051"),sQuery(id+"F0.wireOp",EDGE,"E3052"),sQuery(id+"F0.wireOp",EDGE,"E3053"),sQuery(id+"F0.wireOp",EDGE,"E3054"),sQuery(id+"F0.wireOp",EDGE,"E3055"),sQuery(id+"F0.wireOp",EDGE,"E3056"),sQuery(id+"F0.wireOp",EDGE,"E3057"),sQuery(id+"F0.wireOp",EDGE,"E3058"),sQuery(id+"F0.wireOp",EDGE,"E3059"),sQuery(id+"F0.wireOp",EDGE,"E3060"),sQuery(id+"F0.wireOp",EDGE,"E3061"),sQuery(id+"F0.wireOp",EDGE,"E3062"),sQuery(id+"F0.wireOp",EDGE,"E3063"),sQuery(id+"F0.wireOp",EDGE,"E3064"),sQuery(id+"F0.wireOp",EDGE,"E3065"),sQuery(id+"F0.wireOp",EDGE,"E3066"),sQuery(id+"F0.wireOp",EDGE,"E3067"),sQuery(id+"F0.wireOp",EDGE,"E3068"),sQuery(id+"F0.wireOp",EDGE,"E3069"),sQuery(id+"F0.wireOp",EDGE,"E3070"),sQuery(id+"F0.wireOp",EDGE,"E3071"),sQuery(id+"F0.wireOp",EDGE,"E3072"),sQuery(id+"F0.wireOp",EDGE,"E3073"),sQuery(id+"F0.wireOp",EDGE,"E3074"),sQuery(id+"F0.wireOp",EDGE,"E3075"),sQuery(id+"F0.wireOp",EDGE,"E3076"),sQuery(id+"F0.wireOp",EDGE,"E3077"),sQuery(id+"F0.wireOp",EDGE,"E3078"),sQuery(id+"F0.wireOp",EDGE,"E3079"),sQuery(id+"F0.wireOp",EDGE,"E3080"),sQuery(id+"F0.wireOp",EDGE,"E3081"),sQuery(id+"F0.wireOp",EDGE,"E3082"),sQuery(id+"F0.wireOp",EDGE,"E3083"),sQuery(id+"F0.wireOp",EDGE,"E3084"),sQuery(id+"F0.wireOp",EDGE,"E3085"),sQuery(id+"F0.wireOp",EDGE,"E3086"),sQuery(id+"F0.wireOp",EDGE,"E3087"),sQuery(id+"F0.wireOp",EDGE,"E3088"),sQuery(id+"F0.wireOp",EDGE,"E3089"),sQuery(id+"F0.wireOp",EDGE,"E3090"),sQuery(id+"F0.wireOp",EDGE,"E3091"),sQuery(id+"F0.wireOp",EDGE,"E3092"),sQuery(id+"F0.wireOp",EDGE,"E3093"),sQuery(id+"F0.wireOp",EDGE,"E3094"),sQuery(id+"F0.wireOp",EDGE,"E3095"),sQuery(id+"F0.wireOp",EDGE,"E3096"),sQuery(id+"F0.wireOp",EDGE,"E3097"),sQuery(id+"F0.wireOp",EDGE,"E3098"),sQuery(id+"F0.wireOp",EDGE,"E3099"),sQuery(id+"F0.wireOp",EDGE,"E3100"),sQuery(id+"F0.wireOp",EDGE,"E3101"),sQuery(id+"F0.wireOp",EDGE,"E3102"),sQuery(id+"F0.wireOp",EDGE,"E3103"),sQuery(id+"F0.wireOp",EDGE,"E3104"),sQuery(id+"F0.wireOp",EDGE,"E3105"),sQuery(id+"F0.wireOp",EDGE,"E3106"),sQuery(id+"F0.wireOp",EDGE,"E3107"),sQuery(id+"F0.wireOp",EDGE,"E3108"),sQuery(id+"F0.wireOp",EDGE,"E3109"),sQuery(id+"F0.wireOp",EDGE,"E3110"),sQuery(id+"F0.wireOp",EDGE,"E3111"),sQuery(id+"F0.wireOp",EDGE,"E3112"),sQuery(id+"F0.wireOp",EDGE,"E3113"),sQuery(id+"F0.wireOp",EDGE,"E3114"),sQuery(id+"F0.wireOp",EDGE,"E3115"),sQuery(id+"F0.wireOp",EDGE,"E3116"),sQuery(id+"F0.wireOp",EDGE,"E3117"),sQuery(id+"F0.wireOp",EDGE,"E3118"),sQuery(id+"F0.wireOp",EDGE,"E3119"),sQuery(id+"F0.wireOp",EDGE,"E3120"),sQuery(id+"F0.wireOp",EDGE,"E3121"),sQuery(id+"F0.wireOp",EDGE,"E3122"),sQuery(id+"F0.wireOp",EDGE,"E3123"),sQuery(id+"F0.wireOp",EDGE,"E3124"),sQuery(id+"F0.wireOp",EDGE,"E3125"),sQuery(id+"F0.wireOp",EDGE,"E3126"),sQuery(id+"F0.wireOp",EDGE,"E3127"),sQuery(id+"F0.wireOp",EDGE,"E3128"),sQuery(id+"F0.wireOp",EDGE,"E3129"),sQuery(id+"F0.wireOp",EDGE,"E3130"),sQuery(id+"F0.wireOp",EDGE,"E3131"),sQuery(id+"F0.wireOp",EDGE,"E3132"),sQuery(id+"F0.wireOp",EDGE,"E3133"),sQuery(id+"F0.wireOp",EDGE,"E3134"),sQuery(id+"F0.wireOp",EDGE,"E3135"),sQuery(id+"F0.wireOp",EDGE,"E3136"),sQuery(id+"F0.wireOp",EDGE,"E3137"),sQuery(id+"F0.wireOp",EDGE,"E3138"),sQuery(id+"F0.wireOp",EDGE,"E3139"),sQuery(id+"F0.wireOp",EDGE,"E3140"),sQuery(id+"F0.wireOp",EDGE,"E3141"),sQuery(id+"F0.wireOp",EDGE,"E3142"),sQuery(id+"F0.wireOp",EDGE,"E3143"),sQuery(id+"F0.wireOp",EDGE,"E3144"),sQuery(id+"F0.wireOp",EDGE,"E3145"),sQuery(id+"F0.wireOp",EDGE,"E3146"),sQuery(id+"F0.wireOp",EDGE,"E3147"),sQuery(id+"F0.wireOp",EDGE,"E3148"),sQuery(id+"F0.wireOp",EDGE,"E3149"),sQuery(id+"F0.wireOp",EDGE,"E3150"),sQuery(id+"F0.wireOp",EDGE,"E3151"),sQuery(id+"F0.wireOp",EDGE,"E3152"),sQuery(id+"F0.wireOp",EDGE,"E3153"),sQuery(id+"F0.wireOp",EDGE,"E3154"),sQuery(id+"F0.wireOp",EDGE,"E3155"),sQuery(id+"F0.wireOp",EDGE,"E3156"),sQuery(id+"F0.wireOp",EDGE,"E3157"),sQuery(id+"F0.wireOp",EDGE,"E3158"),sQuery(id+"F0.wireOp",EDGE,"E3159"),sQuery(id+"F0.wireOp",EDGE,"E3160"),sQuery(id+"F0.wireOp",EDGE,"E3161"),sQuery(id+"F0.wireOp",EDGE,"E3162"),sQuery(id+"F0.wireOp",EDGE,"E3163"),sQuery(id+"F0.wireOp",EDGE,"E3164"),sQuery(id+"F0.wireOp",EDGE,"E3165"),sQuery(id+"F0.wireOp",EDGE,"E3166"),sQuery(id+"F0.wireOp",EDGE,"E3167"),sQuery(id+"F0.wireOp",EDGE,"E3168"),sQuery(id+"F0.wireOp",EDGE,"E3169"),sQuery(id+"F0.wireOp",EDGE,"E3170"),sQuery(id+"F0.wireOp",EDGE,"E3171"),sQuery(id+"F0.wireOp",EDGE,"E3172"),sQuery(id+"F0.wireOp",EDGE,"E3173"),sQuery(id+"F0.wireOp",EDGE,"E3174"),sQuery(id+"F0.wireOp",EDGE,"E3175"),sQuery(id+"F0.wireOp",EDGE,"E3176"),sQuery(id+"F0.wireOp",EDGE,"E3177"),sQuery(id+"F0.wireOp",EDGE,"E3178"),sQuery(id+"F0.wireOp",EDGE,"E3179"),sQuery(id+"F0.wireOp",EDGE,"E3180"),sQuery(id+"F0.wireOp",EDGE,"E3181"),sQuery(id+"F0.wireOp",EDGE,"E3182"),sQuery(id+"F0.wireOp",EDGE,"E3183"),sQuery(id+"F0.wireOp",EDGE,"E3184"),sQuery(id+"F0.wireOp",EDGE,"E3185"),sQuery(id+"F0.wireOp",EDGE,"E3186"),sQuery(id+"F0.wireOp",EDGE,"E3187"),sQuery(id+"F0.wireOp",EDGE,"E3188"),sQuery(id+"F0.wireOp",EDGE,"E3189"),sQuery(id+"F0.wireOp",EDGE,"E3190"),sQuery(id+"F0.wireOp",EDGE,"E3191"),sQuery(id+"F0.wireOp",EDGE,"E3192"),sQuery(id+"F0.wireOp",EDGE,"E3193"),sQuery(id+"F0.wireOp",EDGE,"E3194"),sQuery(id+"F0.wireOp",EDGE,"E3195"),sQuery(id+"F0.wireOp",EDGE,"E3196"),sQuery(id+"F0.wireOp",EDGE,"E3197"),sQuery(id+"F0.wireOp",EDGE,"E3198"),sQuery(id+"F0.wireOp",EDGE,"E3199"),sQuery(id+"F0.wireOp",EDGE,"E3200"),sQuery(id+"F0.wireOp",EDGE,"E3201"),sQuery(id+"F0.wireOp",EDGE,"E3202"),sQuery(id+"F0.wireOp",EDGE,"E3203"),sQuery(id+"F0.wireOp",EDGE,"E3204"),sQuery(id+"F0.wireOp",EDGE,"E3205"),sQuery(id+"F0.wireOp",EDGE,"E3206"),sQuery(id+"F0.wireOp",EDGE,"E3207"),sQuery(id+"F0.wireOp",EDGE,"E3208"),sQuery(id+"F0.wireOp",EDGE,"E3209"),sQuery(id+"F0.wireOp",EDGE,"E3210"),sQuery(id+"F0.wireOp",EDGE,"E3211"),sQuery(id+"F0.wireOp",EDGE,"E3212"),sQuery(id+"F0.wireOp",EDGE,"E3213"),sQuery(id+"F0.wireOp",EDGE,"E3214"),sQuery(id+"F0.wireOp",EDGE,"E3215"),sQuery(id+"F0.wireOp",EDGE,"E3216"),sQuery(id+"F0.wireOp",EDGE,"E3217"),sQuery(id+"F0.wireOp",EDGE,"E3218"),sQuery(id+"F0.wireOp",EDGE,"E3219"),sQuery(id+"F0.wireOp",EDGE,"E3220"),sQuery(id+"F0.wireOp",EDGE,"E3221"),sQuery(id+"F0.wireOp",EDGE,"E3222"),sQuery(id+"F0.wireOp",EDGE,"E3223"),sQuery(id+"F0.wireOp",EDGE,"E3224"),sQuery(id+"F0.wireOp",EDGE,"E3225"),sQuery(id+"F0.wireOp",EDGE,"E3226"),sQuery(id+"F0.wireOp",EDGE,"E3227"),sQuery(id+"F0.wireOp",EDGE,"E3228"),sQuery(id+"F0.wireOp",EDGE,"E3229"),sQuery(id+"F0.wireOp",EDGE,"E3230"),sQuery(id+"F0.wireOp",EDGE,"E3231"),sQuery(id+"F0.wireOp",EDGE,"E3232"),sQuery(id+"F0.wireOp",EDGE,"E3233"),sQuery(id+"F0.wireOp",EDGE,"E3234"),sQuery(id+"F0.wireOp",EDGE,"E3235"),sQuery(id+"F0.wireOp",EDGE,"E3236"),sQuery(id+"F0.wireOp",EDGE,"E3237"),sQuery(id+"F0.wireOp",EDGE,"E3238"),sQuery(id+"F0.wireOp",EDGE,"E3239"),sQuery(id+"F0.wireOp",EDGE,"E3240"),sQuery(id+"F0.wireOp",EDGE,"E3241"),sQuery(id+"F0.wireOp",EDGE,"E3242"),sQuery(id+"F0.wireOp",EDGE,"E3243"),sQuery(id+"F0.wireOp",EDGE,"E3244"),sQuery(id+"F0.wireOp",EDGE,"E3245"),sQuery(id+"F0.wireOp",EDGE,"E3246"),sQuery(id+"F0.wireOp",EDGE,"E3247"),sQuery(id+"F0.wireOp",EDGE,"E3248"),sQuery(id+"F0.wireOp",EDGE,"E3249"),sQuery(id+"F0.wireOp",EDGE,"E3250"),sQuery(id+"F0.wireOp",EDGE,"E3251"),sQuery(id+"F0.wireOp",EDGE,"E3252"),sQuery(id+"F0.wireOp",EDGE,"E3253"),sQuery(id+"F0.wireOp",EDGE,"E3254"),sQuery(id+"F0.wireOp",EDGE,"E3255"),sQuery(id+"F0.wireOp",EDGE,"E3256"),sQuery(id+"F0.wireOp",EDGE,"E3257"),sQuery(id+"F0.wireOp",EDGE,"E3258"),sQuery(id+"F0.wireOp",EDGE,"E3259"),sQuery(id+"F0.wireOp",EDGE,"E3260"),sQuery(id+"F0.wireOp",EDGE,"E3261"),sQuery(id+"F0.wireOp",EDGE,"E3262"),sQuery(id+"F0.wireOp",EDGE,"E3263"),sQuery(id+"F0.wireOp",EDGE,"E3264"),sQuery(id+"F0.wireOp",EDGE,"E3265"),sQuery(id+"F0.wireOp",EDGE,"E3266"),sQuery(id+"F0.wireOp",EDGE,"E3267"),sQuery(id+"F0.wireOp",EDGE,"E3268"),sQuery(id+"F0.wireOp",EDGE,"E3269"),sQuery(id+"F0.wireOp",EDGE,"E3270"),sQuery(id+"F0.wireOp",EDGE,"E3271"),sQuery(id+"F0.wireOp",EDGE,"E3272"),sQuery(id+"F0.wireOp",EDGE,"E3273"),sQuery(id+"F0.wireOp",EDGE,"E3274"),sQuery(id+"F0.wireOp",EDGE,"E3275"),sQuery(id+"F0.wireOp",EDGE,"E3276"),sQuery(id+"F0.wireOp",EDGE,"E3277"),sQuery(id+"F0.wireOp",EDGE,"E3278"),sQuery(id+"F0.wireOp",EDGE,"E3279"),sQuery(id+"F0.wireOp",EDGE,"E3280"),sQuery(id+"F0.wireOp",EDGE,"E3281"),sQuery(id+"F0.wireOp",EDGE,"E3282"),sQuery(id+"F0.wireOp",EDGE,"E3283"),sQuery(id+"F0.wireOp",EDGE,"E3284"),sQuery(id+"F0.wireOp",EDGE,"E3285"),sQuery(id+"F0.wireOp",EDGE,"E3286"),sQuery(id+"F0.wireOp",EDGE,"E3287"),sQuery(id+"F0.wireOp",EDGE,"E3288"),sQuery(id+"F0.wireOp",EDGE,"E3289"),sQuery(id+"F0.wireOp",EDGE,"E3290"),sQuery(id+"F0.wireOp",EDGE,"E3291"),sQuery(id+"F0.wireOp",EDGE,"E3292"),sQuery(id+"F0.wireOp",EDGE,"E3293"),sQuery(id+"F0.wireOp",EDGE,"E3294"),sQuery(id+"F0.wireOp",EDGE,"E3295"),sQuery(id+"F0.wireOp",EDGE,"E3296"),sQuery(id+"F0.wireOp",EDGE,"E3297"),sQuery(id+"F0.wireOp",EDGE,"E3298"),sQuery(id+"F0.wireOp",EDGE,"E3299"),sQuery(id+"F0.wireOp",EDGE,"E3300"),sQuery(id+"F0.wireOp",EDGE,"E3301"),sQuery(id+"F0.wireOp",EDGE,"E3302"),sQuery(id+"F0.wireOp",EDGE,"E3303"),sQuery(id+"F0.wireOp",EDGE,"E3304"),sQuery(id+"F0.wireOp",EDGE,"E3305"),sQuery(id+"F0.wireOp",EDGE,"E3306"),sQuery(id+"F0.wireOp",EDGE,"E3307"),sQuery(id+"F0.wireOp",EDGE,"E3308"),sQuery(id+"F0.wireOp",EDGE,"E3309"),sQuery(id+"F0.wireOp",EDGE,"E3310"),sQuery(id+"F0.wireOp",EDGE,"E3311"),sQuery(id+"F0.wireOp",EDGE,"E3312"),sQuery(id+"F0.wireOp",EDGE,"E3313"),sQuery(id+"F0.wireOp",EDGE,"E3314"),sQuery(id+"F0.wireOp",EDGE,"E3315"),sQuery(id+"F0.wireOp",EDGE,"E3316"),sQuery(id+"F0.wireOp",EDGE,"E3317"),sQuery(id+"F0.wireOp",EDGE,"E3318"),sQuery(id+"F0.wireOp",EDGE,"E3319"),sQuery(id+"F0.wireOp",EDGE,"E3320"),sQuery(id+"F0.wireOp",EDGE,"E3321"),sQuery(id+"F0.wireOp",EDGE,"E3322"),sQuery(id+"F0.wireOp",EDGE,"E3323"),sQuery(id+"F0.wireOp",EDGE,"E3324"),sQuery(id+"F0.wireOp",EDGE,"E3325"),sQuery(id+"F0.wireOp",EDGE,"E3326"),sQuery(id+"F0.wireOp",EDGE,"E3327"),sQuery(id+"F0.wireOp",EDGE,"E3328"),sQuery(id+"F0.wireOp",EDGE,"E3329"),sQuery(id+"F0.wireOp",EDGE,"E3330"),sQuery(id+"F0.wireOp",EDGE,"E3331"),sQuery(id+"F0.wireOp",EDGE,"E3332"),sQuery(id+"F0.wireOp",EDGE,"E3333"),sQuery(id+"F0.wireOp",EDGE,"E3334"),sQuery(id+"F0.wireOp",EDGE,"E3335"),sQuery(id+"F0.wireOp",EDGE,"E3336"),sQuery(id+"F0.wireOp",EDGE,"E3337"),sQuery(id+"F0.wireOp",EDGE,"E3338"),sQuery(id+"F0.wireOp",EDGE,"E3339"),sQuery(id+"F0.wireOp",EDGE,"E3340"),sQuery(id+"F0.wireOp",EDGE,"E3341"),sQuery(id+"F0.wireOp",EDGE,"E3342"),sQuery(id+"F0.wireOp",EDGE,"E3343"),sQuery(id+"F0.wireOp",EDGE,"E3344"),sQuery(id+"F0.wireOp",EDGE,"E3345"),sQuery(id+"F0.wireOp",EDGE,"E3346"),sQuery(id+"F0.wireOp",EDGE,"E3347"),sQuery(id+"F0.wireOp",EDGE,"E3348"),sQuery(id+"F0.wireOp",EDGE,"E3349"),sQuery(id+"F0.wireOp",EDGE,"E3350"),sQuery(id+"F0.wireOp",EDGE,"E3351"),sQuery(id+"F0.wireOp",EDGE,"E3352"),sQuery(id+"F0.wireOp",EDGE,"E3353"),sQuery(id+"F0.wireOp",EDGE,"E3354"),sQuery(id+"F0.wireOp",EDGE,"E3355"),sQuery(id+"F0.wireOp",EDGE,"E3356"),sQuery(id+"F0.wireOp",EDGE,"E3357"),sQuery(id+"F0.wireOp",EDGE,"E3358"),sQuery(id+"F0.wireOp",EDGE,"E3359"),sQuery(id+"F0.wireOp",EDGE,"E3360"),sQuery(id+"F0.wireOp",EDGE,"E3361"),sQuery(id+"F0.wireOp",EDGE,"E3362"),sQuery(id+"F0.wireOp",EDGE,"E3363"),sQuery(id+"F0.wireOp",EDGE,"E3364"),sQuery(id+"F0.wireOp",EDGE,"E3365"),sQuery(id+"F0.wireOp",EDGE,"E3366"),sQuery(id+"F0.wireOp",EDGE,"E3367"),sQuery(id+"F0.wireOp",EDGE,"E3368"),sQuery(id+"F0.wireOp",EDGE,"E3369"),sQuery(id+"F0.wireOp",EDGE,"E3370"),sQuery(id+"F0.wireOp",EDGE,"E3371"),sQuery(id+"F0.wireOp",EDGE,"E3372"),sQuery(id+"F0.wireOp",EDGE,"E3373"),sQuery(id+"F0.wireOp",EDGE,"E3374"),sQuery(id+"F0.wireOp",EDGE,"E3375"),sQuery(id+"F0.wireOp",EDGE,"E3376"),sQuery(id+"F0.wireOp",EDGE,"E3377"),sQuery(id+"F0.wireOp",EDGE,"E3378"),sQuery(id+"F0.wireOp",EDGE,"E3379"),sQuery(id+"F0.wireOp",EDGE,"E3380"),sQuery(id+"F0.wireOp",EDGE,"E3381"),sQuery(id+"F0.wireOp",EDGE,"E3382"),sQuery(id+"F0.wireOp",EDGE,"E3383"),sQuery(id+"F0.wireOp",EDGE,"E3384"),sQuery(id+"F0.wireOp",EDGE,"E3385"),sQuery(id+"F0.wireOp",EDGE,"E3386"),sQuery(id+"F0.wireOp",EDGE,"E3387"),sQuery(id+"F0.wireOp",EDGE,"E3388"),sQuery(id+"F0.wireOp",EDGE,"E3389"),sQuery(id+"F0.wireOp",EDGE,"E3390"),sQuery(id+"F0.wireOp",EDGE,"E3391"),sQuery(id+"F0.wireOp",EDGE,"E3392"),sQuery(id+"F0.wireOp",EDGE,"E3393"),sQuery(id+"F0.wireOp",EDGE,"E3394"),sQuery(id+"F0.wireOp",EDGE,"E3395"),sQuery(id+"F0.wireOp",EDGE,"E3396"),sQuery(id+"F0.wireOp",EDGE,"E3397"),sQuery(id+"F0.wireOp",EDGE,"E3398"),sQuery(id+"F0.wireOp",EDGE,"E3399"),sQuery(id+"F0.wireOp",EDGE,"E3400"),sQuery(id+"F0.wireOp",EDGE,"E3401"),sQuery(id+"F0.wireOp",EDGE,"E3402"),sQuery(id+"F0.wireOp",EDGE,"E3403"),sQuery(id+"F0.wireOp",EDGE,"E3404"),sQuery(id+"F0.wireOp",EDGE,"E3405"),sQuery(id+"F0.wireOp",EDGE,"E3406"),sQuery(id+"F0.wireOp",EDGE,"E3407"),sQuery(id+"F0.wireOp",EDGE,"E3408"),sQuery(id+"F0.wireOp",EDGE,"E3409"),sQuery(id+"F0.wireOp",EDGE,"E3410"),sQuery(id+"F0.wireOp",EDGE,"E3411"),sQuery(id+"F0.wireOp",EDGE,"E3412"),sQuery(id+"F0.wireOp",EDGE,"E3413"),sQuery(id+"F0.wireOp",EDGE,"E3414"),sQuery(id+"F0.wireOp",EDGE,"E3415"),sQuery(id+"F0.wireOp",EDGE,"E3416"),sQuery(id+"F0.wireOp",EDGE,"E3417"),sQuery(id+"F0.wireOp",EDGE,"E3418"),sQuery(id+"F0.wireOp",EDGE,"E3419"),sQuery(id+"F0.wireOp",EDGE,"E3420"),sQuery(id+"F0.wireOp",EDGE,"E3421"),sQuery(id+"F0.wireOp",EDGE,"E3422"),sQuery(id+"F0.wireOp",EDGE,"E3423"),sQuery(id+"F0.wireOp",EDGE,"E3424"),sQuery(id+"F0.wireOp",EDGE,"E3425"),sQuery(id+"F0.wireOp",EDGE,"E3426"),sQuery(id+"F0.wireOp",EDGE,"E3427"),sQuery(id+"F0.wireOp",EDGE,"E3428"),sQuery(id+"F0.wireOp",EDGE,"E3429"),sQuery(id+"F0.wireOp",EDGE,"E3430"),sQuery(id+"F0.wireOp",EDGE,"E3431"),sQuery(id+"F0.wireOp",EDGE,"E3432"),sQuery(id+"F0.wireOp",EDGE,"E3433"),sQuery(id+"F0.wireOp",EDGE,"E3434"),sQuery(id+"F0.wireOp",EDGE,"E3435"),sQuery(id+"F0.wireOp",EDGE,"E3436"),sQuery(id+"F0.wireOp",EDGE,"E3437"),sQuery(id+"F0.wireOp",EDGE,"E3438"),sQuery(id+"F0.wireOp",EDGE,"E3439"),sQuery(id+"F0.wireOp",EDGE,"E3440"),sQuery(id+"F0.wireOp",EDGE,"E3441"),sQuery(id+"F0.wireOp",EDGE,"E3442"),sQuery(id+"F0.wireOp",EDGE,"E3443"),sQuery(id+"F0.wireOp",EDGE,"E3444"),sQuery(id+"F0.wireOp",EDGE,"E3445"),sQuery(id+"F0.wireOp",EDGE,"E3446"),sQuery(id+"F0.wireOp",EDGE,"E3447"),sQuery(id+"F0.wireOp",EDGE,"E3448"),sQuery(id+"F0.wireOp",EDGE,"E3449"),sQuery(id+"F0.wireOp",EDGE,"E3450"),sQuery(id+"F0.wireOp",EDGE,"E3451"),sQuery(id+"F0.wireOp",EDGE,"E3452"),sQuery(id+"F0.wireOp",EDGE,"E3453"),sQuery(id+"F0.wireOp",EDGE,"E3454"),sQuery(id+"F0.wireOp",EDGE,"E3455"),sQuery(id+"F0.wireOp",EDGE,"E3456"),sQuery(id+"F0.wireOp",EDGE,"E3457"),sQuery(id+"F0.wireOp",EDGE,"E3458"),sQuery(id+"F0.wireOp",EDGE,"E3459"),sQuery(id+"F0.wireOp",EDGE,"E3460"),sQuery(id+"F0.wireOp",EDGE,"E3461"),sQuery(id+"F0.wireOp",EDGE,"E3462"),sQuery(id+"F0.wireOp",EDGE,"E3463"),sQuery(id+"F0.wireOp",EDGE,"E3464"),sQuery(id+"F0.wireOp",EDGE,"E3465"),sQuery(id+"F0.wireOp",EDGE,"E3466"),sQuery(id+"F0.wireOp",EDGE,"E3467"),sQuery(id+"F0.wireOp",EDGE,"E3468"),sQuery(id+"F0.wireOp",EDGE,"E3469"),sQuery(id+"F0.wireOp",EDGE,"E3470"),sQuery(id+"F0.wireOp",EDGE,"E3471"),sQuery(id+"F0.wireOp",EDGE,"E3472"),sQuery(id+"F0.wireOp",EDGE,"E3473"),sQuery(id+"F0.wireOp",EDGE,"E3474"),sQuery(id+"F0.wireOp",EDGE,"E3475"),sQuery(id+"F0.wireOp",EDGE,"E3476"),sQuery(id+"F0.wireOp",EDGE,"E3477"),sQuery(id+"F0.wireOp",EDGE,"E3478"),sQuery(id+"F0.wireOp",EDGE,"E3479"),sQuery(id+"F0.wireOp",EDGE,"E3480"),sQuery(id+"F0.wireOp",EDGE,"E3481"),sQuery(id+"F0.wireOp",EDGE,"E3482"),sQuery(id+"F0.wireOp",EDGE,"E3483"),sQuery(id+"F0.wireOp",EDGE,"E3484"),sQuery(id+"F0.wireOp",EDGE,"E3485"),sQuery(id+"F0.wireOp",EDGE,"E3486"),sQuery(id+"F0.wireOp",EDGE,"E3487"),sQuery(id+"F0.wireOp",EDGE,"E3488"),sQuery(id+"F0.wireOp",EDGE,"E3489"),sQuery(id+"F0.wireOp",EDGE,"E3490"),sQuery(id+"F0.wireOp",EDGE,"E3491"),sQuery(id+"F0.wireOp",EDGE,"E3492"),sQuery(id+"F0.wireOp",EDGE,"E3493"),sQuery(id+"F0.wireOp",EDGE,"E3494"),sQuery(id+"F0.wireOp",EDGE,"E3495"),sQuery(id+"F0.wireOp",EDGE,"E3496"),sQuery(id+"F0.wireOp",EDGE,"E3497"),sQuery(id+"F0.wireOp",EDGE,"E3498"),sQuery(id+"F0.wireOp",EDGE,"E3499"),sQuery(id+"F0.wireOp",EDGE,"E3500"),sQuery(id+"F0.wireOp",EDGE,"E3501"),sQuery(id+"F0.wireOp",EDGE,"E3502"),sQuery(id+"F0.wireOp",EDGE,"E3503"),sQuery(id+"F0.wireOp",EDGE,"E3504"),sQuery(id+"F0.wireOp",EDGE,"E3505"),sQuery(id+"F0.wireOp",EDGE,"E3506"),sQuery(id+"F0.wireOp",EDGE,"E3507"),sQuery(id+"F0.wireOp",EDGE,"E3508"),sQuery(id+"F0.wireOp",EDGE,"E3509"),sQuery(id+"F0.wireOp",EDGE,"E3510"),sQuery(id+"F0.wireOp",EDGE,"E3511"),sQuery(id+"F0.wireOp",EDGE,"E3512"),sQuery(id+"F0.wireOp",EDGE,"E3513"),sQuery(id+"F0.wireOp",EDGE,"E3514"),sQuery(id+"F0.wireOp",EDGE,"E3515"),sQuery(id+"F0.wireOp",EDGE,"E3516"),sQuery(id+"F0.wireOp",EDGE,"E3517"),sQuery(id+"F0.wireOp",EDGE,"E3518"),sQuery(id+"F0.wireOp",EDGE,"E3519"),sQuery(id+"F0.wireOp",EDGE,"E3520"),sQuery(id+"F0.wireOp",EDGE,"E3521"),sQuery(id+"F0.wireOp",EDGE,"E3522"),sQuery(id+"F0.wireOp",EDGE,"E3523"),sQuery(id+"F0.wireOp",EDGE,"E3524"),sQuery(id+"F0.wireOp",EDGE,"E3525"),sQuery(id+"F0.wireOp",EDGE,"E3526"),sQuery(id+"F0.wireOp",EDGE,"E3527"),sQuery(id+"F0.wireOp",EDGE,"E3528"),sQuery(id+"F0.wireOp",EDGE,"E3529"),sQuery(id+"F0.wireOp",EDGE,"E3530"),sQuery(id+"F0.wireOp",EDGE,"E3531"),sQuery(id+"F0.wireOp",EDGE,"E3532"),sQuery(id+"F0.wireOp",EDGE,"E3533"),sQuery(id+"F0.wireOp",EDGE,"E3534"),sQuery(id+"F0.wireOp",EDGE,"E3535"),sQuery(id+"F0.wireOp",EDGE,"E3536"),sQuery(id+"F0.wireOp",EDGE,"E3537"),sQuery(id+"F0.wireOp",EDGE,"E3538"),sQuery(id+"F0.wireOp",EDGE,"E3539"),sQuery(id+"F0.wireOp",EDGE,"E3540"),sQuery(id+"F0.wireOp",EDGE,"E3541"),sQuery(id+"F0.wireOp",EDGE,"E3542"),sQuery(id+"F0.wireOp",EDGE,"E3543"),sQuery(id+"F0.wireOp",EDGE,"E3544"),sQuery(id+"F0.wireOp",EDGE,"E3545"),sQuery(id+"F0.wireOp",EDGE,"E3546"),sQuery(id+"F0.wireOp",EDGE,"E3547"),sQuery(id+"F0.wireOp",EDGE,"E3548"),sQuery(id+"F0.wireOp",EDGE,"E3549"),sQuery(id+"F0.wireOp",EDGE,"E3550"),sQuery(id+"F0.wireOp",EDGE,"E3551"),sQuery(id+"F0.wireOp",EDGE,"E3552"),sQuery(id+"F0.wireOp",EDGE,"E3553"),sQuery(id+"F0.wireOp",EDGE,"E3554"),sQuery(id+"F0.wireOp",EDGE,"E3555"),sQuery(id+"F0.wireOp",EDGE,"E3556"),sQuery(id+"F0.wireOp",EDGE,"E3557"),sQuery(id+"F0.wireOp",EDGE,"E3558"),sQuery(id+"F0.wireOp",EDGE,"E3559"),sQuery(id+"F0.wireOp",EDGE,"E3560"),sQuery(id+"F0.wireOp",EDGE,"E3561"),sQuery(id+"F0.wireOp",EDGE,"E3562"),sQuery(id+"F0.wireOp",EDGE,"E3563"),sQuery(id+"F0.wireOp",EDGE,"E3564"),sQuery(id+"F0.wireOp",EDGE,"E3565"),sQuery(id+"F0.wireOp",EDGE,"E3566"),sQuery(id+"F0.wireOp",EDGE,"E3567"),sQuery(id+"F0.wireOp",EDGE,"E3568"),sQuery(id+"F0.wireOp",EDGE,"E3569"),sQuery(id+"F0.wireOp",EDGE,"E3570"),sQuery(id+"F0.wireOp",EDGE,"E3571"),sQuery(id+"F0.wireOp",EDGE,"E3572"),sQuery(id+"F0.wireOp",EDGE,"E3573"),sQuery(id+"F0.wireOp",EDGE,"E3574"),sQuery(id+"F0.wireOp",EDGE,"E3575"),sQuery(id+"F0.wireOp",EDGE,"E3576"),sQuery(id+"F0.wireOp",EDGE,"E3577"),sQuery(id+"F0.wireOp",EDGE,"E3578"),sQuery(id+"F0.wireOp",EDGE,"E3579"),sQuery(id+"F0.wireOp",EDGE,"E3580"),sQuery(id+"F0.wireOp",EDGE,"E3581"),sQuery(id+"F0.wireOp",EDGE,"E3582"),sQuery(id+"F0.wireOp",EDGE,"E3583"),sQuery(id+"F0.wireOp",EDGE,"E3584"),sQuery(id+"F0.wireOp",EDGE,"E3585"),sQuery(id+"F0.wireOp",EDGE,"E3586"),sQuery(id+"F0.wireOp",EDGE,"E3587"),sQuery(id+"F0.wireOp",EDGE,"E3588"),sQuery(id+"F0.wireOp",EDGE,"E3589"),sQuery(id+"F0.wireOp",EDGE,"E3590"),sQuery(id+"F0.wireOp",EDGE,"E3591"),sQuery(id+"F0.wireOp",EDGE,"E3592"),sQuery(id+"F0.wireOp",EDGE,"E3593"),sQuery(id+"F0.wireOp",EDGE,"E3594"),sQuery(id+"F0.wireOp",EDGE,"E3595"),sQuery(id+"F0.wireOp",EDGE,"E3596"),sQuery(id+"F0.wireOp",EDGE,"E3597"),sQuery(id+"F0.wireOp",EDGE,"E3598"),sQuery(id+"F0.wireOp",EDGE,"E3599"),sQuery(id+"F0.wireOp",EDGE,"E3600"),sQuery(id+"F0.wireOp",EDGE,"E3601"),sQuery(id+"F0.wireOp",EDGE,"E3602"),sQuery(id+"F0.wireOp",EDGE,"E3603"),sQuery(id+"F0.wireOp",EDGE,"E3604"),sQuery(id+"F0.wireOp",EDGE,"E3605"),sQuery(id+"F0.wireOp",EDGE,"E3606"),sQuery(id+"F0.wireOp",EDGE,"E3607"),sQuery(id+"F0.wireOp",EDGE,"E3608"),sQuery(id+"F0.wireOp",EDGE,"E3609"),sQuery(id+"F0.wireOp",EDGE,"E3610"),sQuery(id+"F0.wireOp",EDGE,"E3611"),sQuery(id+"F0.wireOp",EDGE,"E3612"),sQuery(id+"F0.wireOp",EDGE,"E3613"),sQuery(id+"F0.wireOp",EDGE,"E3614"),sQuery(id+"F0.wireOp",EDGE,"E3615"),sQuery(id+"F0.wireOp",EDGE,"E3616"),sQuery(id+"F0.wireOp",EDGE,"E3617"),sQuery(id+"F0.wireOp",EDGE,"E3618"),sQuery(id+"F0.wireOp",EDGE,"E3619"),sQuery(id+"F0.wireOp",EDGE,"E3620"),sQuery(id+"F0.wireOp",EDGE,"E3621"),sQuery(id+"F0.wireOp",EDGE,"E3622"),sQuery(id+"F0.wireOp",EDGE,"E3623"),sQuery(id+"F0.wireOp",EDGE,"E3624"),sQuery(id+"F0.wireOp",EDGE,"E3625"),sQuery(id+"F0.wireOp",EDGE,"E3626"),sQuery(id+"F0.wireOp",EDGE,"E3627"),sQuery(id+"F0.wireOp",EDGE,"E3628"),sQuery(id+"F0.wireOp",EDGE,"E3629"),sQuery(id+"F0.wireOp",EDGE,"E3630"),sQuery(id+"F0.wireOp",EDGE,"E3631"),sQuery(id+"F0.wireOp",EDGE,"E3632"),sQuery(id+"F0.wireOp",EDGE,"E3633"),sQuery(id+"F0.wireOp",EDGE,"E3634"),sQuery(id+"F0.wireOp",EDGE,"E3635"),sQuery(id+"F0.wireOp",EDGE,"E3636"),sQuery(id+"F0.wireOp",EDGE,"E3637"),sQuery(id+"F0.wireOp",EDGE,"E3638"),sQuery(id+"F0.wireOp",EDGE,"E3639"),sQuery(id+"F0.wireOp",EDGE,"E3640"),sQuery(id+"F0.wireOp",EDGE,"E3641"),sQuery(id+"F0.wireOp",EDGE,"E3642"),sQuery(id+"F0.wireOp",EDGE,"E3643"),sQuery(id+"F0.wireOp",EDGE,"E3644"),sQuery(id+"F0.wireOp",EDGE,"E3645"),sQuery(id+"F0.wireOp",EDGE,"E3646"),sQuery(id+"F0.wireOp",EDGE,"E3647"),sQuery(id+"F0.wireOp",EDGE,"E3648"),sQuery(id+"F0.wireOp",EDGE,"E3649"),sQuery(id+"F0.wireOp",EDGE,"E3650"),sQuery(id+"F0.wireOp",EDGE,"E3651"),sQuery(id+"F0.wireOp",EDGE,"E3652"),sQuery(id+"F0.wireOp",EDGE,"E3653"),sQuery(id+"F0.wireOp",EDGE,"E3654"),sQuery(id+"F0.wireOp",EDGE,"E3655"),sQuery(id+"F0.wireOp",EDGE,"E3656"),sQuery(id+"F0.wireOp",EDGE,"E3657"),sQuery(id+"F0.wireOp",EDGE,"E3658"),sQuery(id+"F0.wireOp",EDGE,"E3659"),sQuery(id+"F0.wireOp",EDGE,"E3660"),sQuery(id+"F0.wireOp",EDGE,"E3661"),sQuery(id+"F0.wireOp",EDGE,"E3662"),sQuery(id+"F0.wireOp",EDGE,"E3663"),sQuery(id+"F0.wireOp",EDGE,"E3664"),sQuery(id+"F0.wireOp",EDGE,"E3665"),sQuery(id+"F0.wireOp",EDGE,"E3666"),sQuery(id+"F0.wireOp",EDGE,"E3667"),sQuery(id+"F0.wireOp",EDGE,"E3668"),sQuery(id+"F0.wireOp",EDGE,"E3669"),sQuery(id+"F0.wireOp",EDGE,"E3670"),sQuery(id+"F0.wireOp",EDGE,"E3671"),sQuery(id+"F0.wireOp",EDGE,"E3672"),sQuery(id+"F0.wireOp",EDGE,"E3673"),sQuery(id+"F0.wireOp",EDGE,"E3674"),sQuery(id+"F0.wireOp",EDGE,"E3675"),sQuery(id+"F0.wireOp",EDGE,"E3676"),sQuery(id+"F0.wireOp",EDGE,"E3677"),sQuery(id+"F0.wireOp",EDGE,"E3678"),sQuery(id+"F0.wireOp",EDGE,"E3679"),sQuery(id+"F0.wireOp",EDGE,"E3680"),sQuery(id+"F0.wireOp",EDGE,"E3681"),sQuery(id+"F0.wireOp",EDGE,"E3682"),sQuery(id+"F0.wireOp",EDGE,"E3683"),sQuery(id+"F0.wireOp",EDGE,"E3684"),sQuery(id+"F0.wireOp",EDGE,"E3685"),sQuery(id+"F0.wireOp",EDGE,"E3686"),sQuery(id+"F0.wireOp",EDGE,"E3687"),sQuery(id+"F0.wireOp",EDGE,"E3688"),sQuery(id+"F0.wireOp",EDGE,"E3689"),sQuery(id+"F0.wireOp",EDGE,"E3690"),sQuery(id+"F0.wireOp",EDGE,"E3691"),sQuery(id+"F0.wireOp",EDGE,"E3692"),sQuery(id+"F0.wireOp",EDGE,"E3693"),sQuery(id+"F0.wireOp",EDGE,"E3694"),sQuery(id+"F0.wireOp",EDGE,"E3695"),sQuery(id+"F0.wireOp",EDGE,"E3696"),sQuery(id+"F0.wireOp",EDGE,"E3697"),sQuery(id+"F0.wireOp",EDGE,"E3698"),sQuery(id+"F0.wireOp",EDGE,"E3699"),sQuery(id+"F0.wireOp",EDGE,"E3700"),sQuery(id+"F0.wireOp",EDGE,"E3701"),sQuery(id+"F0.wireOp",EDGE,"E3702"),sQuery(id+"F0.wireOp",EDGE,"E3703"),sQuery(id+"F0.wireOp",EDGE,"E3704"),sQuery(id+"F0.wireOp",EDGE,"E3705"),sQuery(id+"F0.wireOp",EDGE,"E3706"),sQuery(id+"F0.wireOp",EDGE,"E3707"),sQuery(id+"F0.wireOp",EDGE,"E3708"),sQuery(id+"F0.wireOp",EDGE,"E3709"),sQuery(id+"F0.wireOp",EDGE,"E3710"),sQuery(id+"F0.wireOp",EDGE,"E3711"),sQuery(id+"F0.wireOp",EDGE,"E3712"),sQuery(id+"F0.wireOp",EDGE,"E3713"),sQuery(id+"F0.wireOp",EDGE,"E3714"),sQuery(id+"F0.wireOp",EDGE,"E3715"),sQuery(id+"F0.wireOp",EDGE,"E3716"),sQuery(id+"F0.wireOp",EDGE,"E3717"),sQuery(id+"F0.wireOp",EDGE,"E3718"),sQuery(id+"F0.wireOp",EDGE,"E3719"),sQuery(id+"F0.wireOp",EDGE,"E3720"),sQuery(id+"F0.wireOp",EDGE,"E3721"),sQuery(id+"F0.wireOp",EDGE,"E3722"),sQuery(id+"F0.wireOp",EDGE,"E3723"),sQuery(id+"F0.wireOp",EDGE,"E3724"),sQuery(id+"F0.wireOp",EDGE,"E3725"),sQuery(id+"F0.wireOp",EDGE,"E3726"),sQuery(id+"F0.wireOp",EDGE,"E3727"),sQuery(id+"F0.wireOp",EDGE,"E3728"),sQuery(id+"F0.wireOp",EDGE,"E3729"),sQuery(id+"F0.wireOp",EDGE,"E3730"),sQuery(id+"F0.wireOp",EDGE,"E3731"),sQuery(id+"F0.wireOp",EDGE,"E3732"),sQuery(id+"F0.wireOp",EDGE,"E3733"),sQuery(id+"F0.wireOp",EDGE,"E3734"),sQuery(id+"F0.wireOp",EDGE,"E3735"),sQuery(id+"F0.wireOp",EDGE,"E3736"),sQuery(id+"F0.wireOp",EDGE,"E3737"),sQuery(id+"F0.wireOp",EDGE,"E3738"),sQuery(id+"F0.wireOp",EDGE,"E3739"),sQuery(id+"F0.wireOp",EDGE,"E3740"),sQuery(id+"F0.wireOp",EDGE,"E3741"),sQuery(id+"F0.wireOp",EDGE,"E3742"),sQuery(id+"F0.wireOp",EDGE,"E3743"),sQuery(id+"F0.wireOp",EDGE,"E3744"),sQuery(id+"F0.wireOp",EDGE,"E3745"),sQuery(id+"F0.wireOp",EDGE,"E3746"),sQuery(id+"F0.wireOp",EDGE,"E3747"),sQuery(id+"F0.wireOp",EDGE,"E3748"),sQuery(id+"F0.wireOp",EDGE,"E3749"),sQuery(id+"F0.wireOp",EDGE,"E3750"),sQuery(id+"F0.wireOp",EDGE,"E3751"),sQuery(id+"F0.wireOp",EDGE,"E3752"),sQuery(id+"F0.wireOp",EDGE,"E3753"),sQuery(id+"F0.wireOp",EDGE,"E3754"),sQuery(id+"F0.wireOp",EDGE,"E3755"),sQuery(id+"F0.wireOp",EDGE,"E3756"),sQuery(id+"F0.wireOp",EDGE,"E3757"),sQuery(id+"F0.wireOp",EDGE,"E3758"),sQuery(id+"F0.wireOp",EDGE,"E3759"),sQuery(id+"F0.wireOp",EDGE,"E3760"),sQuery(id+"F0.wireOp",EDGE,"E3761"),sQuery(id+"F0.wireOp",EDGE,"E3762"),sQuery(id+"F0.wireOp",EDGE,"E3763"),sQuery(id+"F0.wireOp",EDGE,"E3764"),sQuery(id+"F0.wireOp",EDGE,"E3765"),sQuery(id+"F0.wireOp",EDGE,"E3766"),sQuery(id+"F0.wireOp",EDGE,"E3767"),sQuery(id+"F0.wireOp",EDGE,"E3768"),sQuery(id+"F0.wireOp",EDGE,"E3769"),sQuery(id+"F0.wireOp",EDGE,"E3770"),sQuery(id+"F0.wireOp",EDGE,"E3771"),sQuery(id+"F0.wireOp",EDGE,"E3772"),sQuery(id+"F0.wireOp",EDGE,"E3773"),sQuery(id+"F0.wireOp",EDGE,"E3774"),sQuery(id+"F0.wireOp",EDGE,"E3775"),sQuery(id+"F0.wireOp",EDGE,"E3776"),sQuery(id+"F0.wireOp",EDGE,"E3777"),sQuery(id+"F0.wireOp",EDGE,"E3778"),sQuery(id+"F0.wireOp",EDGE,"E3779"),sQuery(id+"F0.wireOp",EDGE,"E3780"),sQuery(id+"F0.wireOp",EDGE,"E3781"),sQuery(id+"F0.wireOp",EDGE,"E3782"),sQuery(id+"F0.wireOp",EDGE,"E3783"),sQuery(id+"F0.wireOp",EDGE,"E3784"),sQuery(id+"F0.wireOp",EDGE,"E3785"),sQuery(id+"F0.wireOp",EDGE,"E3786"),sQuery(id+"F0.wireOp",EDGE,"E3787"),sQuery(id+"F0.wireOp",EDGE,"E3788"),sQuery(id+"F0.wireOp",EDGE,"E3789"),sQuery(id+"F0.wireOp",EDGE,"E3790"),sQuery(id+"F0.wireOp",EDGE,"E3791"),sQuery(id+"F0.wireOp",EDGE,"E3792"),sQuery(id+"F0.wireOp",EDGE,"E3793"),sQuery(id+"F0.wireOp",EDGE,"E3794"),sQuery(id+"F0.wireOp",EDGE,"E3795"),sQuery(id+"F0.wireOp",EDGE,"E3796"),sQuery(id+"F0.wireOp",EDGE,"E3797"),sQuery(id+"F0.wireOp",EDGE,"E3798"),sQuery(id+"F0.wireOp",EDGE,"E3799"),sQuery(id+"F0.wireOp",EDGE,"E3800"),sQuery(id+"F0.wireOp",EDGE,"E3801"),sQuery(id+"F0.wireOp",EDGE,"E3802"),sQuery(id+"F0.wireOp",EDGE,"E3803"),sQuery(id+"F0.wireOp",EDGE,"E3804"),sQuery(id+"F0.wireOp",EDGE,"E3805"),sQuery(id+"F0.wireOp",EDGE,"E3806"),sQuery(id+"F0.wireOp",EDGE,"E3807"),sQuery(id+"F0.wireOp",EDGE,"E3808"),sQuery(id+"F0.wireOp",EDGE,"E3809"),sQuery(id+"F0.wireOp",EDGE,"E3810"),sQuery(id+"F0.wireOp",EDGE,"E3811"),sQuery(id+"F0.wireOp",EDGE,"E3812"),sQuery(id+"F0.wireOp",EDGE,"E3813"),sQuery(id+"F0.wireOp",EDGE,"E3814"),sQuery(id+"F0.wireOp",EDGE,"E3815"),sQuery(id+"F0.wireOp",EDGE,"E3816"),sQuery(id+"F0.wireOp",EDGE,"E3817"),sQuery(id+"F0.wireOp",EDGE,"E3818"),sQuery(id+"F0.wireOp",EDGE,"E3819"),sQuery(id+"F0.wireOp",EDGE,"E3820"),sQuery(id+"F0.wireOp",EDGE,"E3821"),sQuery(id+"F0.wireOp",EDGE,"E3822"),sQuery(id+"F0.wireOp",EDGE,"E3823"),sQuery(id+"F0.wireOp",EDGE,"E3824"),sQuery(id+"F0.wireOp",EDGE,"E3825"),sQuery(id+"F0.wireOp",EDGE,"E3826"),sQuery(id+"F0.wireOp",EDGE,"E3827"),sQuery(id+"F0.wireOp",EDGE,"E3828"),sQuery(id+"F0.wireOp",EDGE,"E3829"),sQuery(id+"F0.wireOp",EDGE,"E3830"),sQuery(id+"F0.wireOp",EDGE,"E3831"),sQuery(id+"F0.wireOp",EDGE,"E3832"),sQuery(id+"F0.wireOp",EDGE,"E3833"),sQuery(id+"F0.wireOp",EDGE,"E3834"),sQuery(id+"F0.wireOp",EDGE,"E3835"),sQuery(id+"F0.wireOp",EDGE,"E3836"),sQuery(id+"F0.wireOp",EDGE,"E3837"),sQuery(id+"F0.wireOp",EDGE,"E3838"),sQuery(id+"F0.wireOp",EDGE,"E3839"),sQuery(id+"F0.wireOp",EDGE,"E3840"),sQuery(id+"F0.wireOp",EDGE,"E3841"),sQuery(id+"F0.wireOp",EDGE,"E3842"),sQuery(id+"F0.wireOp",EDGE,"E3843"),sQuery(id+"F0.wireOp",EDGE,"E3844"),sQuery(id+"F0.wireOp",EDGE,"E3845"),sQuery(id+"F0.wireOp",EDGE,"E3846"),sQuery(id+"F0.wireOp",EDGE,"E3847"),sQuery(id+"F0.wireOp",EDGE,"E3848"),sQuery(id+"F0.wireOp",EDGE,"E3849"),sQuery(id+"F0.wireOp",EDGE,"E3850"),sQuery(id+"F0.wireOp",EDGE,"E3851"),sQuery(id+"F0.wireOp",EDGE,"E3852"),sQuery(id+"F0.wireOp",EDGE,"E3853"),sQuery(id+"F0.wireOp",EDGE,"E3854"),sQuery(id+"F0.wireOp",EDGE,"E3855"),sQuery(id+"F0.wireOp",EDGE,"E3856"),sQuery(id+"F0.wireOp",EDGE,"E3857"),sQuery(id+"F0.wireOp",EDGE,"E3858"),sQuery(id+"F0.wireOp",EDGE,"E3859"),sQuery(id+"F0.wireOp",EDGE,"E3860"),sQuery(id+"F0.wireOp",EDGE,"E3861"),sQuery(id+"F0.wireOp",EDGE,"E3862"),sQuery(id+"F0.wireOp",EDGE,"E3863"),sQuery(id+"F0.wireOp",EDGE,"E3864"),sQuery(id+"F0.wireOp",EDGE,"E3865"),sQuery(id+"F0.wireOp",EDGE,"E3866"),sQuery(id+"F0.wireOp",EDGE,"E3867"),sQuery(id+"F0.wireOp",EDGE,"E3868"),sQuery(id+"F0.wireOp",EDGE,"E3869"),sQuery(id+"F0.wireOp",EDGE,"E3870"),sQuery(id+"F0.wireOp",EDGE,"E3871"),sQuery(id+"F0.wireOp",EDGE,"E3872"),sQuery(id+"F0.wireOp",EDGE,"E3873"),sQuery(id+"F0.wireOp",EDGE,"E3874"),sQuery(id+"F0.wireOp",EDGE,"E3875"),sQuery(id+"F0.wireOp",EDGE,"E3876"),sQuery(id+"F0.wireOp",EDGE,"E3877"),sQuery(id+"F0.wireOp",EDGE,"E3878"),sQuery(id+"F0.wireOp",EDGE,"E3879"),sQuery(id+"F0.wireOp",EDGE,"E3880"),sQuery(id+"F0.wireOp",EDGE,"E3881"),sQuery(id+"F0.wireOp",EDGE,"E3882"),sQuery(id+"F0.wireOp",EDGE,"E3883"),sQuery(id+"F0.wireOp",EDGE,"E3884"),sQuery(id+"F0.wireOp",EDGE,"E3885"),sQuery(id+"F0.wireOp",EDGE,"E3886"),sQuery(id+"F0.wireOp",EDGE,"E3887"),sQuery(id+"F0.wireOp",EDGE,"E3888"),sQuery(id+"F0.wireOp",EDGE,"E3889"),sQuery(id+"F0.wireOp",EDGE,"E3890"),sQuery(id+"F0.wireOp",EDGE,"E3891"),sQuery(id+"F0.wireOp",EDGE,"E3892"),sQuery(id+"F0.wireOp",EDGE,"E3893"),sQuery(id+"F0.wireOp",EDGE,"E3894"),sQuery(id+"F0.wireOp",EDGE,"E3895"),sQuery(id+"F0.wireOp",EDGE,"E3896"),sQuery(id+"F0.wireOp",EDGE,"E3897"),sQuery(id+"F0.wireOp",EDGE,"E3898"),sQuery(id+"F0.wireOp",EDGE,"E3899"),sQuery(id+"F0.wireOp",EDGE,"E3900"),sQuery(id+"F0.wireOp",EDGE,"E3901"),sQuery(id+"F0.wireOp",EDGE,"E3902"),sQuery(id+"F0.wireOp",EDGE,"E3903"),sQuery(id+"F0.wireOp",EDGE,"E3904"),sQuery(id+"F0.wireOp",EDGE,"E3905"),sQuery(id+"F0.wireOp",EDGE,"E3906"),sQuery(id+"F0.wireOp",EDGE,"E3907"),sQuery(id+"F0.wireOp",EDGE,"E3908"),sQuery(id+"F0.wireOp",EDGE,"E3909"),sQuery(id+"F0.wireOp",EDGE,"E3910"),sQuery(id+"F0.wireOp",EDGE,"E3911"),sQuery(id+"F0.wireOp",EDGE,"E3912"),sQuery(id+"F0.wireOp",EDGE,"E3913"),sQuery(id+"F0.wireOp",EDGE,"E3914"),sQuery(id+"F0.wireOp",EDGE,"E3915"),sQuery(id+"F0.wireOp",EDGE,"E3916"),sQuery(id+"F0.wireOp",EDGE,"E3917"),sQuery(id+"F0.wireOp",EDGE,"E3918"),sQuery(id+"F0.wireOp",EDGE,"E3919"),sQuery(id+"F0.wireOp",EDGE,"E3920"),sQuery(id+"F0.wireOp",EDGE,"E3921"),sQuery(id+"F0.wireOp",EDGE,"E3922"),sQuery(id+"F0.wireOp",EDGE,"E3923"),sQuery(id+"F0.wireOp",EDGE,"E3924"),sQuery(id+"F0.wireOp",EDGE,"E3925"),sQuery(id+"F0.wireOp",EDGE,"E3926"),sQuery(id+"F0.wireOp",EDGE,"E3927"),sQuery(id+"F0.wireOp",EDGE,"E3928"),sQuery(id+"F0.wireOp",EDGE,"E3929"),sQuery(id+"F0.wireOp",EDGE,"E3930"),sQuery(id+"F0.wireOp",EDGE,"E3931"),sQuery(id+"F0.wireOp",EDGE,"E3932"),sQuery(id+"F0.wireOp",EDGE,"E3933"),sQuery(id+"F0.wireOp",EDGE,"E3934"),sQuery(id+"F0.wireOp",EDGE,"E3935"),sQuery(id+"F0.wireOp",EDGE,"E3936"),sQuery(id+"F0.wireOp",EDGE,"E3937"),sQuery(id+"F0.wireOp",EDGE,"E3938"),sQuery(id+"F0.wireOp",EDGE,"E3939"),sQuery(id+"F0.wireOp",EDGE,"E3940"),sQuery(id+"F0.wireOp",EDGE,"E3941"),sQuery(id+"F0.wireOp",EDGE,"E3942"),sQuery(id+"F0.wireOp",EDGE,"E3943"),sQuery(id+"F0.wireOp",EDGE,"E3944"),sQuery(id+"F0.wireOp",EDGE,"E3945"),sQuery(id+"F0.wireOp",EDGE,"E3946"),sQuery(id+"F0.wireOp",EDGE,"E3947"),sQuery(id+"F0.wireOp",EDGE,"E3948"),sQuery(id+"F0.wireOp",EDGE,"E3949"),sQuery(id+"F0.wireOp",EDGE,"E3950"),sQuery(id+"F0.wireOp",EDGE,"E3951"),sQuery(id+"F0.wireOp",EDGE,"E3952"),sQuery(id+"F0.wireOp",EDGE,"E3953"),sQuery(id+"F0.wireOp",EDGE,"E3954"),sQuery(id+"F0.wireOp",EDGE,"E3955"),sQuery(id+"F0.wireOp",EDGE,"E3956"),sQuery(id+"F0.wireOp",EDGE,"E3957"),sQuery(id+"F0.wireOp",EDGE,"E3958"),sQuery(id+"F0.wireOp",EDGE,"E3959"),sQuery(id+"F0.wireOp",EDGE,"E3960"),sQuery(id+"F0.wireOp",EDGE,"E3961"),sQuery(id+"F0.wireOp",EDGE,"E3962"),sQuery(id+"F0.wireOp",EDGE,"E3963"),sQuery(id+"F0.wireOp",EDGE,"E3964"),sQuery(id+"F0.wireOp",EDGE,"E3965"),sQuery(id+"F0.wireOp",EDGE,"E3966"),sQuery(id+"F0.wireOp",EDGE,"E3967"),sQuery(id+"F0.wireOp",EDGE,"E3968"),sQuery(id+"F0.wireOp",EDGE,"E3969"),sQuery(id+"F0.wireOp",EDGE,"E3970"),sQuery(id+"F0.wireOp",EDGE,"E3971"),sQuery(id+"F0.wireOp",EDGE,"E3972"),sQuery(id+"F0.wireOp",EDGE,"E3973"),sQuery(id+"F0.wireOp",EDGE,"E3974"),sQuery(id+"F0.wireOp",EDGE,"E3975"),sQuery(id+"F0.wireOp",EDGE,"E3976"),sQuery(id+"F0.wireOp",EDGE,"E3977"),sQuery(id+"F0.wireOp",EDGE,"E3978"),sQuery(id+"F0.wireOp",EDGE,"E3979"),sQuery(id+"F0.wireOp",EDGE,"E3980"),sQuery(id+"F0.wireOp",EDGE,"E3981"),sQuery(id+"F0.wireOp",EDGE,"E3982"),sQuery(id+"F0.wireOp",EDGE,"E3983"),sQuery(id+"F0.wireOp",EDGE,"E3984"),sQuery(id+"F0.wireOp",EDGE,"E3985"),sQuery(id+"F0.wireOp",EDGE,"E3986"),sQuery(id+"F0.wireOp",EDGE,"E3987"),sQuery(id+"F0.wireOp",EDGE,"E3988"),sQuery(id+"F0.wireOp",EDGE,"E3989"),sQuery(id+"F0.wireOp",EDGE,"E3990"),sQuery(id+"F0.wireOp",EDGE,"E3991"),sQuery(id+"F0.wireOp",EDGE,"E3992"),sQuery(id+"F0.wireOp",EDGE,"E3993"),sQuery(id+"F0.wireOp",EDGE,"E3994"),sQuery(id+"F0.wireOp",EDGE,"E3995"),sQuery(id+"F0.wireOp",EDGE,"E3996"),sQuery(id+"F0.wireOp",EDGE,"E3997"),sQuery(id+"F0.wireOp",EDGE,"E3998"),sQuery(id+"F0.wireOp",EDGE,"E3999"),sQuery(id+"F0.wireOp",EDGE,"E4000"),sQuery(id+"F0.wireOp",EDGE,"E4001"),sQuery(id+"F0.wireOp",EDGE,"E4002"),sQuery(id+"F0.wireOp",EDGE,"E4003"),sQuery(id+"F0.wireOp",EDGE,"E4004"),sQuery(id+"F0.wireOp",EDGE,"E4005"),sQuery(id+"F0.wireOp",EDGE,"E4006"),sQuery(id+"F0.wireOp",EDGE,"E4007"),sQuery(id+"F0.wireOp",EDGE,"E4008"),sQuery(id+"F0.wireOp",EDGE,"E4009"),sQuery(id+"F0.wireOp",EDGE,"E4010"),sQuery(id+"F0.wireOp",EDGE,"E4011"),sQuery(id+"F0.wireOp",EDGE,"E4012"),sQuery(id+"F0.wireOp",EDGE,"E4013"),sQuery(id+"F0.wireOp",EDGE,"E4014"),sQuery(id+"F0.wireOp",EDGE,"E4015"),sQuery(id+"F0.wireOp",EDGE,"E4016"),sQuery(id+"F0.wireOp",EDGE,"E4017"),sQuery(id+"F0.wireOp",EDGE,"E4018"),sQuery(id+"F0.wireOp",EDGE,"E4019"),sQuery(id+"F0.wireOp",EDGE,"E4020"),sQuery(id+"F0.wireOp",EDGE,"E4021"),sQuery(id+"F0.wireOp",EDGE,"E4022"),sQuery(id+"F0.wireOp",EDGE,"E4023"),sQuery(id+"F0.wireOp",EDGE,"E4024"),sQuery(id+"F0.wireOp",EDGE,"E4025"),sQuery(id+"F0.wireOp",EDGE,"E4026"),sQuery(id+"F0.wireOp",EDGE,"E4027"),sQuery(id+"F0.wireOp",EDGE,"E4028"),sQuery(id+"F0.wireOp",EDGE,"E4029"),sQuery(id+"F0.wireOp",EDGE,"E4030"),sQuery(id+"F0.wireOp",EDGE,"E4031"),sQuery(id+"F0.wireOp",EDGE,"E4032"),sQuery(id+"F0.wireOp",EDGE,"E4033"),sQuery(id+"F0.wireOp",EDGE,"E4034"),sQuery(id+"F0.wireOp",EDGE,"E4035"),sQuery(id+"F0.wireOp",EDGE,"E4036"),sQuery(id+"F0.wireOp",EDGE,"E4037"),sQuery(id+"F0.wireOp",EDGE,"E4038"),sQuery(id+"F0.wireOp",EDGE,"E4039"),sQuery(id+"F0.wireOp",EDGE,"E4040"),sQuery(id+"F0.wireOp",EDGE,"E4041"),sQuery(id+"F0.wireOp",EDGE,"E4042"),sQuery(id+"F0.wireOp",EDGE,"E4043"),sQuery(id+"F0.wireOp",EDGE,"E4044"),sQuery(id+"F0.wireOp",EDGE,"E4045"),sQuery(id+"F0.wireOp",EDGE,"E4046"),sQuery(id+"F0.wireOp",EDGE,"E4047"),sQuery(id+"F0.wireOp",EDGE,"E4048"),sQuery(id+"F0.wireOp",EDGE,"E4049"),sQuery(id+"F0.wireOp",EDGE,"E4050"),sQuery(id+"F0.wireOp",EDGE,"E4051"),sQuery(id+"F0.wireOp",EDGE,"E4052"),sQuery(id+"F0.wireOp",EDGE,"E4053"),sQuery(id+"F0.wireOp",EDGE,"E4054"),sQuery(id+"F0.wireOp",EDGE,"E4055"),sQuery(id+"F0.wireOp",EDGE,"E4056"),sQuery(id+"F0.wireOp",EDGE,"E4057"),sQuery(id+"F0.wireOp",EDGE,"E4058"),sQuery(id+"F0.wireOp",EDGE,"E4059"),sQuery(id+"F0.wireOp",EDGE,"E4060"),sQuery(id+"F0.wireOp",EDGE,"E4061"),sQuery(id+"F0.wireOp",EDGE,"E4062"),sQuery(id+"F0.wireOp",EDGE,"E4063"),sQuery(id+"F0.wireOp",EDGE,"E4064"),sQuery(id+"F0.wireOp",EDGE,"E4065"),sQuery(id+"F0.wireOp",EDGE,"E4066"),sQuery(id+"F0.wireOp",EDGE,"E4067"),sQuery(id+"F0.wireOp",EDGE,"E4068"),sQuery(id+"F0.wireOp",EDGE,"E4069"),sQuery(id+"F0.wireOp",EDGE,"E4070"),sQuery(id+"F0.wireOp",EDGE,"E4071"),sQuery(id+"F0.wireOp",EDGE,"E4072"),sQuery(id+"F0.wireOp",EDGE,"E4073"),sQuery(id+"F0.wireOp",EDGE,"E4074"),sQuery(id+"F0.wireOp",EDGE,"E4075"),sQuery(id+"F0.wireOp",EDGE,"E4076"),sQuery(id+"F0.wireOp",EDGE,"E4077"),sQuery(id+"F0.wireOp",EDGE,"E4078"),sQuery(id+"F0.wireOp",EDGE,"E4079"),sQuery(id+"F0.wireOp",EDGE,"E4080"),sQuery(id+"F0.wireOp",EDGE,"E4081"),sQuery(id+"F0.wireOp",EDGE,"E4082"),sQuery(id+"F0.wireOp",EDGE,"E4083"),sQuery(id+"F0.wireOp",EDGE,"E4084"),sQuery(id+"F0.wireOp",EDGE,"E4085"),sQuery(id+"F0.wireOp",EDGE,"E4086"),sQuery(id+"F0.wireOp",EDGE,"E4087"),sQuery(id+"F0.wireOp",EDGE,"E4088"),sQuery(id+"F0.wireOp",EDGE,"E4089"),sQuery(id+"F0.wireOp",EDGE,"E4090"),sQuery(id+"F0.wireOp",EDGE,"E4091"),sQuery(id+"F0.wireOp",EDGE,"E4092"),sQuery(id+"F0.wireOp",EDGE,"E4093"),sQuery(id+"F0.wireOp",EDGE,"E4094"),sQuery(id+"F0.wireOp",EDGE,"E4095"),sQuery(id+"F0.wireOp",EDGE,"E4096"),sQuery(id+"F0.wireOp",EDGE,"E4097"),sQuery(id+"F0.wireOp",EDGE,"E4098"),sQuery(id+"F0.wireOp",EDGE,"E4099"),sQuery(id+"F0.wireOp",EDGE,"E4100"),sQuery(id+"F0.wireOp",EDGE,"E4101"),sQuery(id+"F0.wireOp",EDGE,"E4102"),sQuery(id+"F0.wireOp",EDGE,"E4103"),sQuery(id+"F0.wireOp",EDGE,"E4104"),sQuery(id+"F0.wireOp",EDGE,"E4105"),sQuery(id+"F0.wireOp",EDGE,"E4106"),sQuery(id+"F0.wireOp",EDGE,"E4107"),sQuery(id+"F0.wireOp",EDGE,"E4108"),sQuery(id+"F0.wireOp",EDGE,"E4109"),sQuery(id+"F0.wireOp",EDGE,"E4110"),sQuery(id+"F0.wireOp",EDGE,"E4111"),sQuery(id+"F0.wireOp",EDGE,"E4112"),sQuery(id+"F0.wireOp",EDGE,"E4113"),sQuery(id+"F0.wireOp",EDGE,"E4114"),sQuery(id+"F0.wireOp",EDGE,"E4115"),sQuery(id+"F0.wireOp",EDGE,"E4116"),sQuery(id+"F0.wireOp",EDGE,"E4117"),sQuery(id+"F0.wireOp",EDGE,"E4118"),sQuery(id+"F0.wireOp",EDGE,"E4119"),sQuery(id+"F0.wireOp",EDGE,"E4120"),sQuery(id+"F0.wireOp",EDGE,"E4121"),sQuery(id+"F0.wireOp",EDGE,"E4122"),sQuery(id+"F0.wireOp",EDGE,"E4123"),sQuery(id+"F0.wireOp",EDGE,"E4124"),sQuery(id+"F0.wireOp",EDGE,"E4125"),sQuery(id+"F0.wireOp",EDGE,"E4126"),sQuery(id+"F0.wireOp",EDGE,"E4127"),sQuery(id+"F0.wireOp",EDGE,"E4128"),sQuery(id+"F0.wireOp",EDGE,"E4129"),sQuery(id+"F0.wireOp",EDGE,"E4130"),sQuery(id+"F0.wireOp",EDGE,"E4131"),sQuery(id+"F0.wireOp",EDGE,"E4132"),sQuery(id+"F0.wireOp",EDGE,"E4133"),sQuery(id+"F0.wireOp",EDGE,"E4134"),sQuery(id+"F0.wireOp",EDGE,"E4135"),sQuery(id+"F0.wireOp",EDGE,"E4136"),sQuery(id+"F0.wireOp",EDGE,"E4137"),sQuery(id+"F0.wireOp",EDGE,"E4138"),sQuery(id+"F0.wireOp",EDGE,"E4139"),sQuery(id+"F0.wireOp",EDGE,"E4140"),sQuery(id+"F0.wireOp",EDGE,"E4141"),sQuery(id+"F0.wireOp",EDGE,"E4142"),sQuery(id+"F0.wireOp",EDGE,"E4143"),sQuery(id+"F0.wireOp",EDGE,"E4144"),sQuery(id+"F0.wireOp",EDGE,"E4145"),sQuery(id+"F0.wireOp",EDGE,"E4146"),sQuery(id+"F0.wireOp",EDGE,"E4147"),sQuery(id+"F0.wireOp",EDGE,"E4148"),sQuery(id+"F0.wireOp",EDGE,"E4149"),sQuery(id+"F0.wireOp",EDGE,"E4150"),sQuery(id+"F0.wireOp",EDGE,"E4151"),sQuery(id+"F0.wireOp",EDGE,"E4152"),sQuery(id+"F0.wireOp",EDGE,"E4153"),sQuery(id+"F0.wireOp",EDGE,"E4154"),sQuery(id+"F0.wireOp",EDGE,"E4155"),sQuery(id+"F0.wireOp",EDGE,"E4156"),sQuery(id+"F0.wireOp",EDGE,"E4157"),sQuery(id+"F0.wireOp",EDGE,"E4158"),sQuery(id+"F0.wireOp",EDGE,"E4159"),sQuery(id+"F0.wireOp",EDGE,"E4160"),sQuery(id+"F0.wireOp",EDGE,"E4161"),sQuery(id+"F0.wireOp",EDGE,"E4162"),sQuery(id+"F0.wireOp",EDGE,"E4163"),sQuery(id+"F0.wireOp",EDGE,"E4164"),sQuery(id+"F0.wireOp",EDGE,"E4165"),sQuery(id+"F0.wireOp",EDGE,"E4166"),sQuery(id+"F0.wireOp",EDGE,"E4167"),sQuery(id+"F0.wireOp",EDGE,"E4168"),sQuery(id+"F0.wireOp",EDGE,"E4169"),sQuery(id+"F0.wireOp",EDGE,"E4170"),sQuery(id+"F0.wireOp",EDGE,"E4171"),sQuery(id+"F0.wireOp",EDGE,"E4172"),sQuery(id+"F0.wireOp",EDGE,"E4173"),sQuery(id+"F0.wireOp",EDGE,"E4174"),sQuery(id+"F0.wireOp",EDGE,"E4175"),sQuery(id+"F0.wireOp",EDGE,"E4176"),sQuery(id+"F0.wireOp",EDGE,"E4177"),sQuery(id+"F0.wireOp",EDGE,"E4178"),sQuery(id+"F0.wireOp",EDGE,"E4179"),sQuery(id+"F0.wireOp",EDGE,"E4180"),sQuery(id+"F0.wireOp",EDGE,"E4181"),sQuery(id+"F0.wireOp",EDGE,"E4182"),sQuery(id+"F0.wireOp",EDGE,"E4183"),sQuery(id+"F0.wireOp",EDGE,"E4184"),sQuery(id+"F0.wireOp",EDGE,"E4185"),sQuery(id+"F0.wireOp",EDGE,"E4186"),sQuery(id+"F0.wireOp",EDGE,"E4187"),sQuery(id+"F0.wireOp",EDGE,"E4188"),sQuery(id+"F0.wireOp",EDGE,"E4189"),sQuery(id+"F0.wireOp",EDGE,"E4190"),sQuery(id+"F0.wireOp",EDGE,"E4191"),sQuery(id+"F0.wireOp",EDGE,"E4192"),sQuery(id+"F0.wireOp",EDGE,"E4193"),sQuery(id+"F0.wireOp",EDGE,"E4194"),sQuery(id+"F0.wireOp",EDGE,"E4195"),sQuery(id+"F0.wireOp",EDGE,"E4196"),sQuery(id+"F0.wireOp",EDGE,"E4197"),sQuery(id+"F0.wireOp",EDGE,"E4198"),sQuery(id+"F0.wireOp",EDGE,"E4199"),sQuery(id+"F0.wireOp",EDGE,"E4200"),sQuery(id+"F0.wireOp",EDGE,"E4201"),sQuery(id+"F0.wireOp",EDGE,"E4202"),sQuery(id+"F0.wireOp",EDGE,"E4203"),sQuery(id+"F0.wireOp",EDGE,"E4204"),sQuery(id+"F0.wireOp",EDGE,"E4205"),sQuery(id+"F0.wireOp",EDGE,"E4206"),sQuery(id+"F0.wireOp",EDGE,"E4207"),sQuery(id+"F0.wireOp",EDGE,"E4208"),sQuery(id+"F0.wireOp",EDGE,"E4209"),sQuery(id+"F0.wireOp",EDGE,"E4210"),sQuery(id+"F0.wireOp",EDGE,"E4211"),sQuery(id+"F0.wireOp",EDGE,"E4212"),sQuery(id+"F0.wireOp",EDGE,"E4213"),sQuery(id+"F0.wireOp",EDGE,"E4214"),sQuery(id+"F0.wireOp",EDGE,"E4215"),sQuery(id+"F0.wireOp",EDGE,"E4216"),sQuery(id+"F0.wireOp",EDGE,"E4217"),sQuery(id+"F0.wireOp",EDGE,"E4218"),sQuery(id+"F0.wireOp",EDGE,"E4219"),sQuery(id+"F0.wireOp",EDGE,"E4220"),sQuery(id+"F0.wireOp",EDGE,"E4221"),sQuery(id+"F0.wireOp",EDGE,"E4222"),sQuery(id+"F0.wireOp",EDGE,"E4223"),sQuery(id+"F0.wireOp",EDGE,"E4224"),sQuery(id+"F0.wireOp",EDGE,"E4225"),sQuery(id+"F0.wireOp",EDGE,"E4226"),sQuery(id+"F0.wireOp",EDGE,"E4227"),sQuery(id+"F0.wireOp",EDGE,"E4228"),sQuery(id+"F0.wireOp",EDGE,"E4229"),sQuery(id+"F0.wireOp",EDGE,"E4230"),sQuery(id+"F0.wireOp",EDGE,"E4231"),sQuery(id+"F0.wireOp",EDGE,"E4232"),sQuery(id+"F0.wireOp",EDGE,"E4233"),sQuery(id+"F0.wireOp",EDGE,"E4234"),sQuery(id+"F0.wireOp",EDGE,"E4235"),sQuery(id+"F0.wireOp",EDGE,"E4236"),sQuery(id+"F0.wireOp",EDGE,"E4237"),sQuery(id+"F0.wireOp",EDGE,"E4238"),sQuery(id+"F0.wireOp",EDGE,"E4239"),sQuery(id+"F0.wireOp",EDGE,"E4240"),sQuery(id+"F0.wireOp",EDGE,"E4241"),sQuery(id+"F0.wireOp",EDGE,"E4242"),sQuery(id+"F0.wireOp",EDGE,"E4243"),sQuery(id+"F0.wireOp",EDGE,"E4244"),sQuery(id+"F0.wireOp",EDGE,"E4245"),sQuery(id+"F0.wireOp",EDGE,"E4246"),sQuery(id+"F0.wireOp",EDGE,"E4247"),sQuery(id+"F0.wireOp",EDGE,"E4248"),sQuery(id+"F0.wireOp",EDGE,"E4249"),sQuery(id+"F0.wireOp",EDGE,"E4250"),sQuery(id+"F0.wireOp",EDGE,"E4251"),sQuery(id+"F0.wireOp",EDGE,"E4252"),sQuery(id+"F0.wireOp",EDGE,"E4253"),sQuery(id+"F0.wireOp",EDGE,"E4254"),sQuery(id+"F0.wireOp",EDGE,"E4255"),sQuery(id+"F0.wireOp",EDGE,"E4256"),sQuery(id+"F0.wireOp",EDGE,"E4257"),sQuery(id+"F0.wireOp",EDGE,"E4258"),sQuery(id+"F0.wireOp",EDGE,"E4259"),sQuery(id+"F0.wireOp",EDGE,"E4260"),sQuery(id+"F0.wireOp",EDGE,"E4261"),sQuery(id+"F0.wireOp",EDGE,"E4262"),sQuery(id+"F0.wireOp",EDGE,"E4263"),sQuery(id+"F0.wireOp",EDGE,"E4264"),sQuery(id+"F0.wireOp",EDGE,"E4265"),sQuery(id+"F0.wireOp",EDGE,"E4266"),sQuery(id+"F0.wireOp",EDGE,"E4267"),sQuery(id+"F0.wireOp",EDGE,"E4268"),sQuery(id+"F0.wireOp",EDGE,"E4269"),sQuery(id+"F0.wireOp",EDGE,"E4270"),sQuery(id+"F0.wireOp",EDGE,"E4271"),sQuery(id+"F0.wireOp",EDGE,"E4272"),sQuery(id+"F0.wireOp",EDGE,"E4273"),sQuery(id+"F0.wireOp",EDGE,"E4274"),sQuery(id+"F0.wireOp",EDGE,"E4275"),sQuery(id+"F0.wireOp",EDGE,"E4276"),sQuery(id+"F0.wireOp",EDGE,"E4277"),sQuery(id+"F0.wireOp",EDGE,"E4278"),sQuery(id+"F0.wireOp",EDGE,"E4279"),sQuery(id+"F0.wireOp",EDGE,"E4280"),sQuery(id+"F0.wireOp",EDGE,"E4281"),sQuery(id+"F0.wireOp",EDGE,"E4282"),sQuery(id+"F0.wireOp",EDGE,"E4283"),sQuery(id+"F0.wireOp",EDGE,"E4284"),sQuery(id+"F0.wireOp",EDGE,"E4285"),sQuery(id+"F0.wireOp",EDGE,"E4286"),sQuery(id+"F0.wireOp",EDGE,"E4287"),sQuery(id+"F0.wireOp",EDGE,"E4288"),sQuery(id+"F0.wireOp",EDGE,"E4289"),sQuery(id+"F0.wireOp",EDGE,"E4290"),sQuery(id+"F0.wireOp",EDGE,"E4291"),sQuery(id+"F0.wireOp",EDGE,"E4292"),sQuery(id+"F0.wireOp",EDGE,"E4293"),sQuery(id+"F0.wireOp",EDGE,"E4294"),sQuery(id+"F0.wireOp",EDGE,"E4295"),sQuery(id+"F0.wireOp",EDGE,"E4296"),sQuery(id+"F0.wireOp",EDGE,"E4297"),sQuery(id+"F0.wireOp",EDGE,"E4298"),sQuery(id+"F0.wireOp",EDGE,"E4299"),sQuery(id+"F0.wireOp",EDGE,"E4300"),sQuery(id+"F0.wireOp",EDGE,"E4301"),sQuery(id+"F0.wireOp",EDGE,"E4302"),sQuery(id+"F0.wireOp",EDGE,"E4303"),sQuery(id+"F0.wireOp",EDGE,"E4304"),sQuery(id+"F0.wireOp",EDGE,"E4305"),sQuery(id+"F0.wireOp",EDGE,"E4306"),sQuery(id+"F0.wireOp",EDGE,"E4307"),sQuery(id+"F0.wireOp",EDGE,"E4308"),sQuery(id+"F0.wireOp",EDGE,"E4309"),sQuery(id+"F0.wireOp",EDGE,"E4310"),sQuery(id+"F0.wireOp",EDGE,"E4311"),sQuery(id+"F0.wireOp",EDGE,"E4312"),sQuery(id+"F0.wireOp",EDGE,"E4313"),sQuery(id+"F0.wireOp",EDGE,"E4314"),sQuery(id+"F0.wireOp",EDGE,"E4315"),sQuery(id+"F0.wireOp",EDGE,"E4316"),sQuery(id+"F0.wireOp",EDGE,"E4317"),sQuery(id+"F0.wireOp",EDGE,"E4318"),sQuery(id+"F0.wireOp",EDGE,"E4319"),sQuery(id+"F0.wireOp",EDGE,"E4320"),sQuery(id+"F0.wireOp",EDGE,"E4321"),sQuery(id+"F0.wireOp",EDGE,"E4322"),sQuery(id+"F0.wireOp",EDGE,"E4323"),sQuery(id+"F0.wireOp",EDGE,"E4324"),sQuery(id+"F0.wireOp",EDGE,"E4325"),sQuery(id+"F0.wireOp",EDGE,"E4326"),sQuery(id+"F0.wireOp",EDGE,"E4327"),sQuery(id+"F0.wireOp",EDGE,"E4328"),sQuery(id+"F0.wireOp",EDGE,"E4329"),sQuery(id+"F0.wireOp",EDGE,"E4330"),sQuery(id+"F0.wireOp",EDGE,"E4331"),sQuery(id+"F0.wireOp",EDGE,"E4332"),sQuery(id+"F0.wireOp",EDGE,"E4333"),sQuery(id+"F0.wireOp",EDGE,"E4334"),sQuery(id+"F0.wireOp",EDGE,"E4335"),sQuery(id+"F0.wireOp",EDGE,"E4336"),sQuery(id+"F0.wireOp",EDGE,"E4337"),sQuery(id+"F0.wireOp",EDGE,"E4338"),sQuery(id+"F0.wireOp",EDGE,"E4339"),sQuery(id+"F0.wireOp",EDGE,"E4340"),sQuery(id+"F0.wireOp",EDGE,"E4341"),sQuery(id+"F0.wireOp",EDGE,"E4342"),sQuery(id+"F0.wireOp",EDGE,"E4343"),sQuery(id+"F0.wireOp",EDGE,"E4344"),sQuery(id+"F0.wireOp",EDGE,"E4345"),sQuery(id+"F0.wireOp",EDGE,"E4346"),sQuery(id+"F0.wireOp",EDGE,"E4347"),sQuery(id+"F0.wireOp",EDGE,"E4348"),sQuery(id+"F0.wireOp",EDGE,"E4349"),sQuery(id+"F0.wireOp",EDGE,"E4350"),sQuery(id+"F0.wireOp",EDGE,"E4351"),sQuery(id+"F0.wireOp",EDGE,"E4352"),sQuery(id+"F0.wireOp",EDGE,"E4353"),sQuery(id+"F0.wireOp",EDGE,"E4354"),sQuery(id+"F0.wireOp",EDGE,"E4355"),sQuery(id+"F0.wireOp",EDGE,"E4356"),sQuery(id+"F0.wireOp",EDGE,"E4357"),sQuery(id+"F0.wireOp",EDGE,"E4358"),sQuery(id+"F0.wireOp",EDGE,"E4359"),sQuery(id+"F0.wireOp",EDGE,"E4360"),sQuery(id+"F0.wireOp",EDGE,"E4361"),sQuery(id+"F0.wireOp",EDGE,"E4362"),sQuery(id+"F0.wireOp",EDGE,"E4363"),sQuery(id+"F0.wireOp",EDGE,"E4364"),sQuery(id+"F0.wireOp",EDGE,"E4365"),sQuery(id+"F0.wireOp",EDGE,"E4366"),sQuery(id+"F0.wireOp",EDGE,"E4367"),sQuery(id+"F0.wireOp",EDGE,"E4368"),sQuery(id+"F0.wireOp",EDGE,"E4369"),sQuery(id+"F0.wireOp",EDGE,"E4370"),sQuery(id+"F0.wireOp",EDGE,"E4371"),sQuery(id+"F0.wireOp",EDGE,"E4372"),sQuery(id+"F0.wireOp",EDGE,"E4373"),sQuery(id+"F0.wireOp",EDGE,"E4374"),sQuery(id+"F0.wireOp",EDGE,"E4375"),sQuery(id+"F0.wireOp",EDGE,"E4376"),sQuery(id+"F0.wireOp",EDGE,"E4377"),sQuery(id+"F0.wireOp",EDGE,"E4378"),sQuery(id+"F0.wireOp",EDGE,"E4379"),sQuery(id+"F0.wireOp",EDGE,"E4380"),sQuery(id+"F0.wireOp",EDGE,"E4381"),sQuery(id+"F0.wireOp",EDGE,"E4382"),sQuery(id+"F0.wireOp",EDGE,"E4383"),sQuery(id+"F0.wireOp",EDGE,"E4384"),sQuery(id+"F0.wireOp",EDGE,"E4385"),sQuery(id+"F0.wireOp",EDGE,"E4386"),sQuery(id+"F0.wireOp",EDGE,"E4387"),sQuery(id+"F0.wireOp",EDGE,"E4388"),sQuery(id+"F0.wireOp",EDGE,"E4389"),sQuery(id+"F0.wireOp",EDGE,"E4390"),sQuery(id+"F0.wireOp",EDGE,"E4391"),sQuery(id+"F0.wireOp",EDGE,"E4392"),sQuery(id+"F0.wireOp",EDGE,"E4393"),sQuery(id+"F0.wireOp",EDGE,"E4394"),sQuery(id+"F0.wireOp",EDGE,"E4395"),sQuery(id+"F0.wireOp",EDGE,"E4396"),sQuery(id+"F0.wireOp",EDGE,"E4397"),sQuery(id+"F0.wireOp",EDGE,"E4398"),sQuery(id+"F0.wireOp",EDGE,"E4399"),sQuery(id+"F0.wireOp",EDGE,"E4400"),sQuery(id+"F0.wireOp",EDGE,"E4401"),sQuery(id+"F0.wireOp",EDGE,"E4402"),sQuery(id+"F0.wireOp",EDGE,"E4403"),sQuery(id+"F0.wireOp",EDGE,"E4404"),sQuery(id+"F0.wireOp",EDGE,"E4405"),sQuery(id+"F0.wireOp",EDGE,"E4406"),sQuery(id+"F0.wireOp",EDGE,"E4407"),sQuery(id+"F0.wireOp",EDGE,"E4408"),sQuery(id+"F0.wireOp",EDGE,"E4409"),sQuery(id+"F0.wireOp",EDGE,"E4410"),sQuery(id+"F0.wireOp",EDGE,"E4411"),sQuery(id+"F0.wireOp",EDGE,"E4412"),sQuery(id+"F0.wireOp",EDGE,"E4413"),sQuery(id+"F0.wireOp",EDGE,"E4414"),sQuery(id+"F0.wireOp",EDGE,"E4415"),sQuery(id+"F0.wireOp",EDGE,"E4416"),sQuery(id+"F0.wireOp",EDGE,"E4417"),sQuery(id+"F0.wireOp",EDGE,"E4418"),sQuery(id+"F0.wireOp",EDGE,"E4419"),sQuery(id+"F0.wireOp",EDGE,"E4420"),sQuery(id+"F0.wireOp",EDGE,"E4421"),sQuery(id+"F0.wireOp",EDGE,"E4422"),sQuery(id+"F0.wireOp",EDGE,"E4423"),sQuery(id+"F0.wireOp",EDGE,"E4424"),sQuery(id+"F0.wireOp",EDGE,"E4425"),sQuery(id+"F0.wireOp",EDGE,"E4426"),sQuery(id+"F0.wireOp",EDGE,"E4427"),sQuery(id+"F0.wireOp",EDGE,"E4428"),sQuery(id+"F0.wireOp",EDGE,"E4429"),sQuery(id+"F0.wireOp",EDGE,"E4430"),sQuery(id+"F0.wireOp",EDGE,"E4431"),sQuery(id+"F0.wireOp",EDGE,"E4432"),sQuery(id+"F0.wireOp",EDGE,"E4433"),sQuery(id+"F0.wireOp",EDGE,"E4434"),sQuery(id+"F0.wireOp",EDGE,"E4435"),sQuery(id+"F0.wireOp",EDGE,"E4436"),sQuery(id+"F0.wireOp",EDGE,"E4437"),sQuery(id+"F0.wireOp",EDGE,"E4438"),sQuery(id+"F0.wireOp",EDGE,"E4439"),sQuery(id+"F0.wireOp",EDGE,"E4440"),sQuery(id+"F0.wireOp",EDGE,"E4441"),sQuery(id+"F0.wireOp",EDGE,"E4442"),sQuery(id+"F0.wireOp",EDGE,"E4443"),sQuery(id+"F0.wireOp",EDGE,"E4444"),sQuery(id+"F0.wireOp",EDGE,"E4445"),sQuery(id+"F0.wireOp",EDGE,"E4446"),sQuery(id+"F0.wireOp",EDGE,"E4447"),sQuery(id+"F0.wireOp",EDGE,"E4448"),sQuery(id+"F0.wireOp",EDGE,"E4449"),sQuery(id+"F0.wireOp",EDGE,"E4450"),sQuery(id+"F0.wireOp",EDGE,"E4451"),sQuery(id+"F0.wireOp",EDGE,"E4452"),sQuery(id+"F0.wireOp",EDGE,"E4453"),sQuery(id+"F0.wireOp",EDGE,"E4454"),sQuery(id+"F0.wireOp",EDGE,"E4455"),sQuery(id+"F0.wireOp",EDGE,"E4456"),sQuery(id+"F0.wireOp",EDGE,"E4457"),sQuery(id+"F0.wireOp",EDGE,"E4458"),sQuery(id+"F0.wireOp",EDGE,"E4459"),sQuery(id+"F0.wireOp",EDGE,"E4460"),sQuery(id+"F0.wireOp",EDGE,"E4461"),sQuery(id+"F0.wireOp",EDGE,"E4462"),sQuery(id+"F0.wireOp",EDGE,"E4463"),sQuery(id+"F0.wireOp",EDGE,"E4464"),sQuery(id+"F0.wireOp",EDGE,"E4465"),sQuery(id+"F0.wireOp",EDGE,"E4466"),sQuery(id+"F0.wireOp",EDGE,"E4467"),sQuery(id+"F0.wireOp",EDGE,"E4468"),sQuery(id+"F0.wireOp",EDGE,"E4469"),sQuery(id+"F0.wireOp",EDGE,"E4470"),sQuery(id+"F0.wireOp",EDGE,"E4471"),sQuery(id+"F0.wireOp",EDGE,"E4472"),sQuery(id+"F0.wireOp",EDGE,"E4473"),sQuery(id+"F0.wireOp",EDGE,"E4474"),sQuery(id+"F0.wireOp",EDGE,"E4475"),sQuery(id+"F0.wireOp",EDGE,"E4476"),sQuery(id+"F0.wireOp",EDGE,"E4477"),sQuery(id+"F0.wireOp",EDGE,"E4478"),sQuery(id+"F0.wireOp",EDGE,"E4479"),sQuery(id+"F0.wireOp",EDGE,"E4480"),sQuery(id+"F0.wireOp",EDGE,"E4481"),sQuery(id+"F0.wireOp",EDGE,"E4482"),sQuery(id+"F0.wireOp",EDGE,"E4483"),sQuery(id+"F0.wireOp",EDGE,"E4484"),sQuery(id+"F0.wireOp",EDGE,"E4485"),sQuery(id+"F0.wireOp",EDGE,"E4486"),sQuery(id+"F0.wireOp",EDGE,"E4487"),sQuery(id+"F0.wireOp",EDGE,"E4488"),sQuery(id+"F0.wireOp",EDGE,"E4489"),sQuery(id+"F0.wireOp",EDGE,"E4490"),sQuery(id+"F0.wireOp",EDGE,"E4491"),sQuery(id+"F0.wireOp",EDGE,"E4492"),sQuery(id+"F0.wireOp",EDGE,"E4493"),sQuery(id+"F0.wireOp",EDGE,"E4494"),sQuery(id+"F0.wireOp",EDGE,"E4495"),sQuery(id+"F0.wireOp",EDGE,"E4496"),sQuery(id+"F0.wireOp",EDGE,"E4497"),sQuery(id+"F0.wireOp",EDGE,"E4498"),sQuery(id+"F0.wireOp",EDGE,"E4499"),sQuery(id+"F0.wireOp",EDGE,"E4500"),sQuery(id+"F0.wireOp",EDGE,"E4501"),sQuery(id+"F0.wireOp",EDGE,"E4502"),sQuery(id+"F0.wireOp",EDGE,"E4503"),sQuery(id+"F0.wireOp",EDGE,"E4504"),sQuery(id+"F0.wireOp",EDGE,"E4505"),sQuery(id+"F0.wireOp",EDGE,"E4506"),sQuery(id+"F0.wireOp",EDGE,"E4507"),sQuery(id+"F0.wireOp",EDGE,"E4508"),sQuery(id+"F0.wireOp",EDGE,"E4509"),sQuery(id+"F0.wireOp",EDGE,"E4510"),sQuery(id+"F0.wireOp",EDGE,"E4511"),sQuery(id+"F0.wireOp",EDGE,"E4512"),sQuery(id+"F0.wireOp",EDGE,"E4513"),sQuery(id+"F0.wireOp",EDGE,"E4514"),sQuery(id+"F0.wireOp",EDGE,"E4515"),sQuery(id+"F0.wireOp",EDGE,"E4516"),sQuery(id+"F0.wireOp",EDGE,"E4517"),sQuery(id+"F0.wireOp",EDGE,"E4518"),sQuery(id+"F0.wireOp",EDGE,"E4519"),sQuery(id+"F0.wireOp",EDGE,"E4520"),sQuery(id+"F0.wireOp",EDGE,"E4521"),sQuery(id+"F0.wireOp",EDGE,"E4522"),sQuery(id+"F0.wireOp",EDGE,"E4523"),sQuery(id+"F0.wireOp",EDGE,"E4524"),sQuery(id+"F0.wireOp",EDGE,"E4525"),sQuery(id+"F0.wireOp",EDGE,"E4526"),sQuery(id+"F0.wireOp",EDGE,"E4527"),sQuery(id+"F0.wireOp",EDGE,"E4528"),sQuery(id+"F0.wireOp",EDGE,"E4529"),sQuery(id+"F0.wireOp",EDGE,"E4530"),sQuery(id+"F0.wireOp",EDGE,"E4531"),sQuery(id+"F0.wireOp",EDGE,"E4532"),sQuery(id+"F0.wireOp",EDGE,"E4533"),sQuery(id+"F0.wireOp",EDGE,"E4534"),sQuery(id+"F0.wireOp",EDGE,"E4535"),sQuery(id+"F0.wireOp",EDGE,"E4536"),sQuery(id+"F0.wireOp",EDGE,"E4537"),sQuery(id+"F0.wireOp",EDGE,"E4538"),sQuery(id+"F0.wireOp",EDGE,"E4539"),sQuery(id+"F0.wireOp",EDGE,"E4540"),sQuery(id+"F0.wireOp",EDGE,"E4541"),sQuery(id+"F0.wireOp",EDGE,"E4542"),sQuery(id+"F0.wireOp",EDGE,"E4543"),sQuery(id+"F0.wireOp",EDGE,"E4544"),sQuery(id+"F0.wireOp",EDGE,"E4545"),sQuery(id+"F0.wireOp",EDGE,"E4546"),sQuery(id+"F0.wireOp",EDGE,"E4547"),sQuery(id+"F0.wireOp",EDGE,"E4548"),sQuery(id+"F0.wireOp",EDGE,"E4549"),sQuery(id+"F0.wireOp",EDGE,"E4550"),sQuery(id+"F0.wireOp",EDGE,"E4551"),sQuery(id+"F0.wireOp",EDGE,"E4552"),sQuery(id+"F0.wireOp",EDGE,"E4553"),sQuery(id+"F0.wireOp",EDGE,"E4554"),sQuery(id+"F0.wireOp",EDGE,"E4555"),sQuery(id+"F0.wireOp",EDGE,"E4556"),sQuery(id+"F0.wireOp",EDGE,"E4557"),sQuery(id+"F0.wireOp",EDGE,"E4558"),sQuery(id+"F0.wireOp",EDGE,"E4559"),sQuery(id+"F0.wireOp",EDGE,"E4560"),sQuery(id+"F0.wireOp",EDGE,"E4561"),sQuery(id+"F0.wireOp",EDGE,"E4562"),sQuery(id+"F0.wireOp",EDGE,"E4563"),sQuery(id+"F0.wireOp",EDGE,"E4564"),sQuery(id+"F0.wireOp",EDGE,"E4565"),sQuery(id+"F0.wireOp",EDGE,"E4566"),sQuery(id+"F0.wireOp",EDGE,"E4567"),sQuery(id+"F0.wireOp",EDGE,"E4568"),sQuery(id+"F0.wireOp",EDGE,"E4569"),sQuery(id+"F0.wireOp",EDGE,"E4570"),sQuery(id+"F0.wireOp",EDGE,"E4571"),sQuery(id+"F0.wireOp",EDGE,"E4572"),sQuery(id+"F0.wireOp",EDGE,"E4573"),sQuery(id+"F0.wireOp",EDGE,"E4574"),sQuery(id+"F0.wireOp",EDGE,"E4575"),sQuery(id+"F0.wireOp",EDGE,"E4576"),sQuery(id+"F0.wireOp",EDGE,"E4577"),sQuery(id+"F0.wireOp",EDGE,"E4578"),sQuery(id+"F0.wireOp",EDGE,"E4579"),sQuery(id+"F0.wireOp",EDGE,"E4580"),sQuery(id+"F0.wireOp",EDGE,"E4581"),sQuery(id+"F0.wireOp",EDGE,"E4582"),sQuery(id+"F0.wireOp",EDGE,"E4583"),sQuery(id+"F0.wireOp",EDGE,"E4584"),sQuery(id+"F0.wireOp",EDGE,"E4585"),sQuery(id+"F0.wireOp",EDGE,"E4586"),sQuery(id+"F0.wireOp",EDGE,"E4587"),sQuery(id+"F0.wireOp",EDGE,"E4588"),sQuery(id+"F0.wireOp",EDGE,"E4589"),sQuery(id+"F0.wireOp",EDGE,"E4590"),sQuery(id+"F0.wireOp",EDGE,"E4591"),sQuery(id+"F0.wireOp",EDGE,"E4592"),sQuery(id+"F0.wireOp",EDGE,"E4593"),sQuery(id+"F0.wireOp",EDGE,"E4594"),sQuery(id+"F0.wireOp",EDGE,"E4595"),sQuery(id+"F0.wireOp",EDGE,"E4596"),sQuery(id+"F0.wireOp",EDGE,"E4597"),sQuery(id+"F0.wireOp",EDGE,"E4598"),sQuery(id+"F0.wireOp",EDGE,"E4599"),sQuery(id+"F0.wireOp",EDGE,"E4600"),sQuery(id+"F0.wireOp",EDGE,"E4601"),sQuery(id+"F0.wireOp",EDGE,"E4602"),sQuery(id+"F0.wireOp",EDGE,"E4603"),sQuery(id+"F0.wireOp",EDGE,"E4604"),sQuery(id+"F0.wireOp",EDGE,"E4605"),sQuery(id+"F0.wireOp",EDGE,"E4606"),sQuery(id+"F0.wireOp",EDGE,"E4607"),sQuery(id+"F0.wireOp",EDGE,"E4608"),sQuery(id+"F0.wireOp",EDGE,"E4609"),sQuery(id+"F0.wireOp",EDGE,"E4610"),sQuery(id+"F0.wireOp",EDGE,"E4611"),sQuery(id+"F0.wireOp",EDGE,"E4612"),sQuery(id+"F0.wireOp",EDGE,"E4613"),sQuery(id+"F0.wireOp",EDGE,"E4614"),sQuery(id+"F0.wireOp",EDGE,"E4615"),sQuery(id+"F0.wireOp",EDGE,"E4616"),sQuery(id+"F0.wireOp",EDGE,"E4617"),sQuery(id+"F0.wireOp",EDGE,"E4618"),sQuery(id+"F0.wireOp",EDGE,"E4619"),sQuery(id+"F0.wireOp",EDGE,"E4620"),sQuery(id+"F0.wireOp",EDGE,"E4621"),sQuery(id+"F0.wireOp",EDGE,"E4622"),sQuery(id+"F0.wireOp",EDGE,"E4623"),sQuery(id+"F0.wireOp",EDGE,"E4624"),sQuery(id+"F0.wireOp",EDGE,"E4625"),sQuery(id+"F0.wireOp",EDGE,"E4626"),sQuery(id+"F0.wireOp",EDGE,"E4627"),sQuery(id+"F0.wireOp",EDGE,"E4628"),sQuery(id+"F0.wireOp",EDGE,"E4629"),sQuery(id+"F0.wireOp",EDGE,"E4630"),sQuery(id+"F0.wireOp",EDGE,"E4631"),sQuery(id+"F0.wireOp",EDGE,"E4632"),sQuery(id+"F0.wireOp",EDGE,"E4633"),sQuery(id+"F0.wireOp",EDGE,"E4634"),sQuery(id+"F0.wireOp",EDGE,"E4635"),sQuery(id+"F0.wireOp",EDGE,"E4636"),sQuery(id+"F0.wireOp",EDGE,"E4637"),sQuery(id+"F0.wireOp",EDGE,"E4638"),sQuery(id+"F0.wireOp",EDGE,"E4639"),sQuery(id+"F0.wireOp",EDGE,"E4640"),sQuery(id+"F0.wireOp",EDGE,"E4641"),sQuery(id+"F0.wireOp",EDGE,"E4642"),sQuery(id+"F0.wireOp",EDGE,"E4643"),sQuery(id+"F0.wireOp",EDGE,"E4644"),sQuery(id+"F0.wireOp",EDGE,"E4645"),sQuery(id+"F0.wireOp",EDGE,"E4646"),sQuery(id+"F0.wireOp",EDGE,"E4647"),sQuery(id+"F0.wireOp",EDGE,"E4648"),sQuery(id+"F0.wireOp",EDGE,"E4649"),sQuery(id+"F0.wireOp",EDGE,"E4650"),sQuery(id+"F0.wireOp",EDGE,"E4651"),sQuery(id+"F0.wireOp",EDGE,"E4652"),sQuery(id+"F0.wireOp",EDGE,"E4653"),sQuery(id+"F0.wireOp",EDGE,"E4654"),sQuery(id+"F0.wireOp",EDGE,"E4655"),sQuery(id+"F0.wireOp",EDGE,"E4656"),sQuery(id+"F0.wireOp",EDGE,"E4657"),sQuery(id+"F0.wireOp",EDGE,"E4658"),sQuery(id+"F0.wireOp",EDGE,"E4659"),sQuery(id+"F0.wireOp",EDGE,"E4660"),sQuery(id+"F0.wireOp",EDGE,"E4661"),sQuery(id+"F0.wireOp",EDGE,"E4662"),sQuery(id+"F0.wireOp",EDGE,"E4663"),sQuery(id+"F0.wireOp",EDGE,"E4664"),sQuery(id+"F0.wireOp",EDGE,"E4665"),sQuery(id+"F0.wireOp",EDGE,"E4666"),sQuery(id+"F0.wireOp",EDGE,"E4667"),sQuery(id+"F0.wireOp",EDGE,"E4668"),sQuery(id+"F0.wireOp",EDGE,"E4669"),sQuery(id+"F0.wireOp",EDGE,"E4670"),sQuery(id+"F0.wireOp",EDGE,"E4671"),sQuery(id+"F0.wireOp",EDGE,"E4672"),sQuery(id+"F0.wireOp",EDGE,"E4673"),sQuery(id+"F0.wireOp",EDGE,"E4674"),sQuery(id+"F0.wireOp",EDGE,"E4675"),sQuery(id+"F0.wireOp",EDGE,"E4676"),sQuery(id+"F0.wireOp",EDGE,"E4677"),sQuery(id+"F0.wireOp",EDGE,"E4678"),sQuery(id+"F0.wireOp",EDGE,"E4679"),sQuery(id+"F0.wireOp",EDGE,"E4680"),sQuery(id+"F0.wireOp",EDGE,"E4681"),sQuery(id+"F0.wireOp",EDGE,"E4682"),sQuery(id+"F0.wireOp",EDGE,"E4683"),sQuery(id+"F0.wireOp",EDGE,"E4684"),sQuery(id+"F0.wireOp",EDGE,"E4685"),sQuery(id+"F0.wireOp",EDGE,"E4686"),sQuery(id+"F0.wireOp",EDGE,"E4687"),sQuery(id+"F0.wireOp",EDGE,"E4688"),sQuery(id+"F0.wireOp",EDGE,"E4689"),sQuery(id+"F0.wireOp",EDGE,"E4690"),sQuery(id+"F0.wireOp",EDGE,"E4691"),sQuery(id+"F0.wireOp",EDGE,"E4692"),sQuery(id+"F0.wireOp",EDGE,"E4693"),sQuery(id+"F0.wireOp",EDGE,"E4694"),sQuery(id+"F0.wireOp",EDGE,"E4695"),sQuery(id+"F0.wireOp",EDGE,"E4696"),sQuery(id+"F0.wireOp",EDGE,"E4697"),sQuery(id+"F0.wireOp",EDGE,"E4698"),sQuery(id+"F0.wireOp",EDGE,"E4699"),sQuery(id+"F0.wireOp",EDGE,"E4700"),sQuery(id+"F0.wireOp",EDGE,"E4701"),sQuery(id+"F0.wireOp",EDGE,"E4702"),sQuery(id+"F0.wireOp",EDGE,"E4703"),sQuery(id+"F0.wireOp",EDGE,"E4704"),sQuery(id+"F0.wireOp",EDGE,"E4705"),sQuery(id+"F0.wireOp",EDGE,"E4706"),sQuery(id+"F0.wireOp",EDGE,"E4707"),sQuery(id+"F0.wireOp",EDGE,"E4708"),sQuery(id+"F0.wireOp",EDGE,"E4709"),sQuery(id+"F0.wireOp",EDGE,"E4710"),sQuery(id+"F0.wireOp",EDGE,"E4711"),sQuery(id+"F0.wireOp",EDGE,"E4712"),sQuery(id+"F0.wireOp",EDGE,"E4713"),sQuery(id+"F0.wireOp",EDGE,"E4714"),sQuery(id+"F0.wireOp",EDGE,"E4715"),sQuery(id+"F0.wireOp",EDGE,"E4716"),sQuery(id+"F0.wireOp",EDGE,"E4717"),sQuery(id+"F0.wireOp",EDGE,"E4718"),sQuery(id+"F0.wireOp",EDGE,"E4719"),sQuery(id+"F0.wireOp",EDGE,"E4720"),sQuery(id+"F0.wireOp",EDGE,"E4721"),sQuery(id+"F0.wireOp",EDGE,"E4722"),sQuery(id+"F0.wireOp",EDGE,"E4723"),sQuery(id+"F0.wireOp",EDGE,"E4724"),sQuery(id+"F0.wireOp",EDGE,"E4725"),sQuery(id+"F0.wireOp",EDGE,"E4726"),sQuery(id+"F0.wireOp",EDGE,"E4727"),sQuery(id+"F0.wireOp",EDGE,"E4728"),sQuery(id+"F0.wireOp",EDGE,"E4729"),sQuery(id+"F0.wireOp",EDGE,"E4730"),sQuery(id+"F0.wireOp",EDGE,"E4731"),sQuery(id+"F0.wireOp",EDGE,"E4732"),sQuery(id+"F0.wireOp",EDGE,"E4733"),sQuery(id+"F0.wireOp",EDGE,"E4734"),sQuery(id+"F0.wireOp",EDGE,"E4735"),sQuery(id+"F0.wireOp",EDGE,"E4736"),sQuery(id+"F0.wireOp",EDGE,"E4737"),sQuery(id+"F0.wireOp",EDGE,"E4738"),sQuery(id+"F0.wireOp",EDGE,"E4739"),sQuery(id+"F0.wireOp",EDGE,"E4740"),sQuery(id+"F0.wireOp",EDGE,"E4741"),sQuery(id+"F0.wireOp",EDGE,"E4742"),sQuery(id+"F0.wireOp",EDGE,"E4743"),sQuery(id+"F0.wireOp",EDGE,"E4744"),sQuery(id+"F0.wireOp",EDGE,"E4745"),sQuery(id+"F0.wireOp",EDGE,"E4746"),sQuery(id+"F0.wireOp",EDGE,"E4747"),sQuery(id+"F0.wireOp",EDGE,"E4748"),sQuery(id+"F0.wireOp",EDGE,"E4749"),sQuery(id+"F0.wireOp",EDGE,"E4750"),sQuery(id+"F0.wireOp",EDGE,"E4751"),sQuery(id+"F0.wireOp",EDGE,"E4752"),sQuery(id+"F0.wireOp",EDGE,"E4753"),sQuery(id+"F0.wireOp",EDGE,"E4754"),sQuery(id+"F0.wireOp",EDGE,"E4755"),sQuery(id+"F0.wireOp",EDGE,"E4756"),sQuery(id+"F0.wireOp",EDGE,"E4757"),sQuery(id+"F0.wireOp",EDGE,"E4758"),sQuery(id+"F0.wireOp",EDGE,"E4759"),sQuery(id+"F0.wireOp",EDGE,"E4760"),sQuery(id+"F0.wireOp",EDGE,"E4761"),sQuery(id+"F0.wireOp",EDGE,"E4762"),sQuery(id+"F0.wireOp",EDGE,"E4763"),sQuery(id+"F0.wireOp",EDGE,"E4764"),sQuery(id+"F0.wireOp",EDGE,"E4765"),sQuery(id+"F0.wireOp",EDGE,"E4766"),sQuery(id+"F0.wireOp",EDGE,"E4767"),sQuery(id+"F0.wireOp",EDGE,"E4768"),sQuery(id+"F0.wireOp",EDGE,"E4769"),sQuery(id+"F0.wireOp",EDGE,"E4770"),sQuery(id+"F0.wireOp",EDGE,"E4771"),sQuery(id+"F0.wireOp",EDGE,"E4772"),sQuery(id+"F0.wireOp",EDGE,"E4773"),sQuery(id+"F0.wireOp",EDGE,"E4774"),sQuery(id+"F0.wireOp",EDGE,"E4775"),sQuery(id+"F0.wireOp",EDGE,"E4776"),sQuery(id+"F0.wireOp",EDGE,"E4777"),sQuery(id+"F0.wireOp",EDGE,"E4778"),sQuery(id+"F0.wireOp",EDGE,"E4779"),sQuery(id+"F0.wireOp",EDGE,"E4780"),sQuery(id+"F0.wireOp",EDGE,"E4781"),sQuery(id+"F0.wireOp",EDGE,"E4782"),sQuery(id+"F0.wireOp",EDGE,"E4783"),sQuery(id+"F0.wireOp",EDGE,"E4784"),sQuery(id+"F0.wireOp",EDGE,"E4785"),sQuery(id+"F0.wireOp",EDGE,"E4786"),sQuery(id+"F0.wireOp",EDGE,"E4787"),sQuery(id+"F0.wireOp",EDGE,"E4788"),sQuery(id+"F0.wireOp",EDGE,"E4789"),sQuery(id+"F0.wireOp",EDGE,"E4790"),sQuery(id+"F0.wireOp",EDGE,"E4791"),sQuery(id+"F0.wireOp",EDGE,"E4792"),sQuery(id+"F0.wireOp",EDGE,"E4793"),sQuery(id+"F0.wireOp",EDGE,"E4794"),sQuery(id+"F0.wireOp",EDGE,"E4795"),sQuery(id+"F0.wireOp",EDGE,"E4796"),sQuery(id+"F0.wireOp",EDGE,"E4797"),sQuery(id+"F0.wireOp",EDGE,"E4798"),sQuery(id+"F0.wireOp",EDGE,"E4799"),sQuery(id+"F0.wireOp",EDGE,"E4800"),sQuery(id+"F0.wireOp",EDGE,"E4801"),sQuery(id+"F0.wireOp",EDGE,"E4802"),sQuery(id+"F0.wireOp",EDGE,"E4803"),sQuery(id+"F0.wireOp",EDGE,"E4804"),sQuery(id+"F0.wireOp",EDGE,"E4805"),sQuery(id+"F0.wireOp",EDGE,"E4806"),sQuery(id+"F0.wireOp",EDGE,"E4807"),sQuery(id+"F0.wireOp",EDGE,"E4808"),sQuery(id+"F0.wireOp",EDGE,"E4809"),sQuery(id+"F0.wireOp",EDGE,"E4810"),sQuery(id+"F0.wireOp",EDGE,"E4811"),sQuery(id+"F0.wireOp",EDGE,"E4824"),sQuery(id+"F0.wireOp",EDGE,"E4825"),sQuery(id+"F0.wireOp",EDGE,"E4826"),sQuery(id+"F0.wireOp",EDGE,"E4827"),sQuery(id+"F0.wireOp",EDGE,"E4828"),sQuery(id+"F0.wireOp",EDGE,"E4829"),sQuery(id+"F0.wireOp",EDGE,"E4830"),sQuery(id+"F0.wireOp",EDGE,"E4831"),sQuery(id+"F0.wireOp",EDGE,"E4832"),sQuery(id+"F0.wireOp",EDGE,"E4833"),sQuery(id+"F0.wireOp",EDGE,"E4834"),sQuery(id+"F0.wireOp",EDGE,"E4835"),sQuery(id+"F0.wireOp",EDGE,"E4836"),sQuery(id+"F0.wireOp",EDGE,"E4837"),sQuery(id+"F0.wireOp",EDGE,"E4838"),sQuery(id+"F0.wireOp",EDGE,"E4839"),sQuery(id+"F0.wireOp",EDGE,"E4840"),sQuery(id+"F0.wireOp",EDGE,"E4841"),sQuery(id+"F0.wireOp",EDGE,"E4842"),sQuery(id+"F0.wireOp",EDGE,"E4843"),sQuery(id+"F0.wireOp",EDGE,"E4844"),sQuery(id+"F0.wireOp",EDGE,"E4845"),sQuery(id+"F0.wireOp",EDGE,"E4846"),sQuery(id+"F0.wireOp",EDGE,"E4847"),sQuery(id+"F0.wireOp",EDGE,"E4848"),sQuery(id+"F0.wireOp",EDGE,"E4849"),sQuery(id+"F0.wireOp",EDGE,"E4850"),sQuery(id+"F0.wireOp",EDGE,"E4852"),sQuery(id+"F0.wireOp",EDGE,"E4853"),sQuery(id+"F0.wireOp",EDGE,"E4854"),sQuery(id+"F0.wireOp",EDGE,"E4855"),sQuery(id+"F0.wireOp",EDGE,"E4856"),sQuery(id+"F0.wireOp",EDGE,"E4857"),sQuery(id+"F0.wireOp",EDGE,"E4858"),sQuery(id+"F0.wireOp",EDGE,"E4859"),sQuery(id+"F0.wireOp",EDGE,"E4860"),sQuery(id+"F0.wireOp",EDGE,"E4861"),sQuery(id+"F0.wireOp",EDGE,"E4862"),sQuery(id+"F0.wireOp",EDGE,"E4863"),sQuery(id+"F0.wireOp",EDGE,"E4864"),sQuery(id+"F0.wireOp",EDGE,"E4865"),sQuery(id+"F0.wireOp",EDGE,"E4866"),sQuery(id+"F0.wireOp",EDGE,"E4867"),sQuery(id+"F0.wireOp",EDGE,"E4868"),sQuery(id+"F0.wireOp",EDGE,"E4869"),sQuery(id+"F0.wireOp",EDGE,"E4870"),sQuery(id+"F0.wireOp",EDGE,"E4871"),sQuery(id+"F0.wireOp",EDGE,"E4872"),sQuery(id+"F0.wireOp",EDGE,"E4873"),sQuery(id+"F0.wireOp",EDGE,"E4874"),sQuery(id+"F0.wireOp",EDGE,"E4875"),sQuery(id+"F0.wireOp",EDGE,"E4876"),sQuery(id+"F0.wireOp",EDGE,"E4877"),sQuery(id+"F0.wireOp",EDGE,"E4891"),sQuery(id+"F0.wireOp",EDGE,"E4892"),sQuery(id+"F0.wireOp",EDGE,"E4893"),sQuery(id+"F0.wireOp",EDGE,"E4894"),sQuery(id+"F0.wireOp",EDGE,"E4895"),sQuery(id+"F0.wireOp",EDGE,"E4896"),sQuery(id+"F0.wireOp",EDGE,"E4897"),sQuery(id+"F0.wireOp",EDGE,"E4898"),sQuery(id+"F0.wireOp",EDGE,"E4899"),sQuery(id+"F0.wireOp",EDGE,"E4900"),sQuery(id+"F0.wireOp",EDGE,"E4901"),sQuery(id+"F0.wireOp",EDGE,"E4902"),sQuery(id+"F0.wireOp",EDGE,"E4903"),sQuery(id+"F0.wireOp",EDGE,"E4904"),sQuery(id+"F0.wireOp",EDGE,"E4905"),sQuery(id+"F0.wireOp",EDGE,"E4906"),sQuery(id+"F0.wireOp",EDGE,"E4907"),sQuery(id+"F0.wireOp",EDGE,"E4908"),sQuery(id+"F0.wireOp",EDGE,"E4909"),sQuery(id+"F0.wireOp",EDGE,"E4910"),sQuery(id+"F0.wireOp",EDGE,"E4911"),sQuery(id+"F0.wireOp",EDGE,"E4912"),sQuery(id+"F0.wireOp",EDGE,"E4913"),sQuery(id+"F0.wireOp",EDGE,"E4914"),sQuery(id+"F0.wireOp",EDGE,"E4915"),sQuery(id+"F0.wireOp",EDGE,"E4916"),sQuery(id+"F0.wireOp",EDGE,"E4930"),sQuery(id+"F0.wireOp",EDGE,"E4931"),sQuery(id+"F0.wireOp",EDGE,"E4945"),sQuery(id+"F0.wireOp",EDGE,"E4946"),sQuery(id+"F0.wireOp",EDGE,"E4947"),sQuery(id+"F0.wireOp",EDGE,"E4948"),sQuery(id+"F0.wireOp",EDGE,"E4949"),sQuery(id+"F0.wireOp",EDGE,"E4950"),sQuery(id+"F0.wireOp",EDGE,"E4951"),sQuery(id+"F0.wireOp",EDGE,"E4952"),sQuery(id+"F0.wireOp",EDGE,"E4953"),sQuery(id+"F0.wireOp",EDGE,"E4954"),sQuery(id+"F0.wireOp",EDGE,"E4955"),sQuery(id+"F0.wireOp",EDGE,"E4956"),sQuery(id+"F0.wireOp",EDGE,"E4957"),sQuery(id+"F0.wireOp",EDGE,"E4958"),sQuery(id+"F0.wireOp",EDGE,"E4959"),sQuery(id+"F0.wireOp",EDGE,"E4960"),sQuery(id+"F0.wireOp",EDGE,"E4961"),sQuery(id+"F0.wireOp",EDGE,"E4962"),sQuery(id+"F0.wireOp",EDGE,"E4963"),sQuery(id+"F0.wireOp",EDGE,"E4964"),sQuery(id+"F0.wireOp",EDGE,"E4965"),sQuery(id+"F0.wireOp",EDGE,"E4966"),sQuery(id+"F0.wireOp",EDGE,"E4967"),sQuery(id+"F0.wireOp",EDGE,"E4968"),sQuery(id+"F0.wireOp",EDGE,"E4969"),sQuery(id+"F0.wireOp",EDGE,"E4970"),sQuery(id+"F0.wireOp",EDGE,"E4971"),sQuery(id+"F0.wireOp",EDGE,"E4972"),sQuery(id+"F0.wireOp",EDGE,"E4974"),sQuery(id+"F0.wireOp",EDGE,"E4975.1.0"),sQuery(id+"F0.wireOp",EDGE,"E4975.2.0"),sQuery(id+"F0.wireOp",EDGE,"E4975.3.0")])],"isStart":false});
            var sketch = newSketch(context, id + "F2", { "sketchPlane" : qUnion([Q0])});
            skCircle(sketch, "E4976", {"center": v(-0.98, 0) * mm, "radius": 2.65 * mm});
            skSolve(sketch);
        }
        {
            var Q0;
            Q0=makeQuery(id+"F2.imprint","IMPRINT",FACE,{"disambiguationData":[TD([[makeQuery(id+"F2.imprint","IMPRINT",EDGE,{"derivedFrom":sQuery(id+"F2.wireOp",EDGE,"E4976")}),1.0]])]});
            extrude(context, id + "F3", {"entities" : qUnion([Q0]), "operationType" : NewBodyOperationType.REMOVE, "oppositeDirection" : true, "depth" : 25 * mm});
        }
    });
